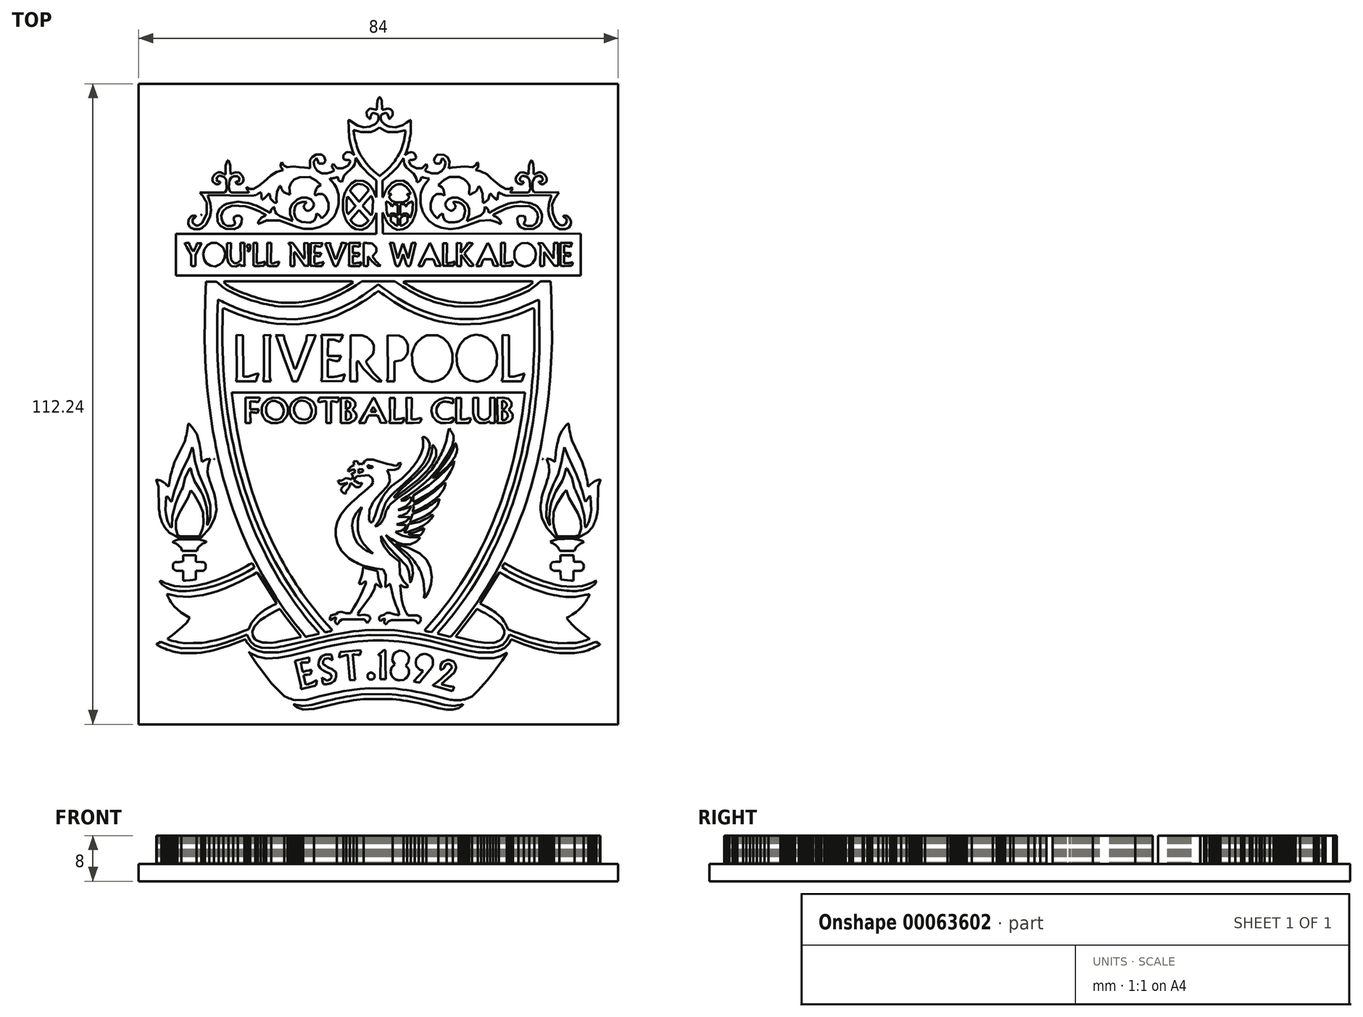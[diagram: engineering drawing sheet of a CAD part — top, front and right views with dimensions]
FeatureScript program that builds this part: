
annotation { "Feature Type Name" : "Feature", "Feature Type Description" : "" }
export const myFeature = defineFeature(function(context is Context, id is Id, definition is map)
    precondition{}
    {
        {
            var Q0;
            Q0=qCreatedBy(makeId("Top.planeOp"),FACE);
            var sketch = newSketch(context, id + "F0", { "sketchPlane" : qUnion([Q0])});
            skLineSegment(sketch, "E0", {"start": v(-12.21, -53.6) * mm, "end": v(-11.26, -53.57) * mm});
            skLineSegment(sketch, "E1", {"start": v(-11.26, -53.57) * mm, "end": v(-7.27, -52.58) * mm});
            skLineSegment(sketch, "E2", {"start": v(-7.27, -52.58) * mm, "end": v(-6.14, -52.35) * mm});
            skLineSegment(sketch, "E3", {"start": v(-6.14, -52.35) * mm, "end": v(-5.6, -52.25) * mm});
            skLineSegment(sketch, "E4", {"start": v(-5.6, -52.25) * mm, "end": v(-4.98, -52.14) * mm});
            skLineSegment(sketch, "E5", {"start": v(-4.98, -52.14) * mm, "end": v(-4.35, -52.04) * mm});
            skLineSegment(sketch, "E6", {"start": v(-4.35, -52.04) * mm, "end": v(-3.78, -51.96) * mm});
            skLineSegment(sketch, "E7", {"start": v(-3.78, -51.96) * mm, "end": v(-2.56, -51.8) * mm});
            skLineSegment(sketch, "E8", {"start": v(-2.56, -51.8) * mm, "end": v(2.51, -51.8) * mm});
            skLineSegment(sketch, "E9", {"start": v(2.51, -51.8) * mm, "end": v(3.74, -51.96) * mm});
            skLineSegment(sketch, "E10", {"start": v(3.74, -51.96) * mm, "end": v(4.37, -52.05) * mm});
            skLineSegment(sketch, "E11", {"start": v(4.37, -52.05) * mm, "end": v(5.03, -52.16) * mm});
            skLineSegment(sketch, "E12", {"start": v(5.03, -52.16) * mm, "end": v(5.7, -52.28) * mm});
            skLineSegment(sketch, "E13", {"start": v(5.7, -52.28) * mm, "end": v(6.39, -52.4) * mm});
            skLineSegment(sketch, "E14", {"start": v(6.39, -52.4) * mm, "end": v(7.08, -52.55) * mm});
            skLineSegment(sketch, "E15", {"start": v(7.08, -52.55) * mm, "end": v(7.76, -52.7) * mm});
            skLineSegment(sketch, "E16", {"start": v(7.76, -52.7) * mm, "end": v(8.43, -52.86) * mm});
            skLineSegment(sketch, "E17", {"start": v(8.43, -52.86) * mm, "end": v(9.08, -53.03) * mm});
            skLineSegment(sketch, "E18", {"start": v(9.08, -53.03) * mm, "end": v(10.49, -53.4) * mm});
            skLineSegment(sketch, "E19", {"start": v(10.49, -53.4) * mm, "end": v(11.94, -53.65) * mm});
            skLineSegment(sketch, "E20", {"start": v(11.94, -53.65) * mm, "end": v(13.03, -53.65) * mm});
            skLineSegment(sketch, "E21", {"start": v(13.03, -53.65) * mm, "end": v(14.07, -53.38) * mm});
            skLineSegment(sketch, "E22", {"start": v(14.07, -53.38) * mm, "end": v(14.43, -53.14) * mm});
            skLineSegment(sketch, "E23", {"start": v(14.43, -53.14) * mm, "end": v(14.57, -53.04) * mm});
            skLineSegment(sketch, "E24", {"start": v(14.57, -53.04) * mm, "end": v(14.69, -52.95) * mm});
            skLineSegment(sketch, "E25", {"start": v(14.69, -52.95) * mm, "end": v(14.77, -52.87) * mm});
            skLineSegment(sketch, "E26", {"start": v(14.77, -52.87) * mm, "end": v(14.79, -52.84) * mm});
            skLineSegment(sketch, "E27", {"start": v(14.79, -52.84) * mm, "end": v(14.8, -52.81) * mm});
            skLineSegment(sketch, "E28", {"start": v(14.8, -52.81) * mm, "end": v(14.8, -52.72) * mm});
            skLineSegment(sketch, "E29", {"start": v(14.8, -52.72) * mm, "end": v(14.65, -52.78) * mm});
            skLineSegment(sketch, "E30", {"start": v(14.65, -52.78) * mm, "end": v(14.54, -52.8) * mm});
            skLineSegment(sketch, "E31", {"start": v(14.54, -52.8) * mm, "end": v(14.37, -52.85) * mm});
            skLineSegment(sketch, "E32", {"start": v(14.37, -52.85) * mm, "end": v(13.89, -52.93) * mm});
            skLineSegment(sketch, "E33", {"start": v(13.89, -52.93) * mm, "end": v(13.27, -53.03) * mm});
            skLineSegment(sketch, "E34", {"start": v(13.27, -53.03) * mm, "end": v(11.56, -52.84) * mm});
            skLineSegment(sketch, "E35", {"start": v(11.56, -52.84) * mm, "end": v(10.35, -52.52) * mm});
            skLineSegment(sketch, "E36", {"start": v(10.35, -52.52) * mm, "end": v(9.17, -52.21) * mm});
            skLineSegment(sketch, "E37", {"start": v(9.17, -52.21) * mm, "end": v(8.12, -51.95) * mm});
            skLineSegment(sketch, "E38", {"start": v(8.12, -51.95) * mm, "end": v(7.18, -51.73) * mm});
            skLineSegment(sketch, "E39", {"start": v(7.18, -51.73) * mm, "end": v(6.32, -51.55) * mm});
            skLineSegment(sketch, "E40", {"start": v(6.32, -51.55) * mm, "end": v(5.5, -51.4) * mm});
            skLineSegment(sketch, "E41", {"start": v(5.5, -51.4) * mm, "end": v(4.71, -51.27) * mm});
            skLineSegment(sketch, "E42", {"start": v(4.71, -51.27) * mm, "end": v(3.92, -51.16) * mm});
            skLineSegment(sketch, "E43", {"start": v(3.92, -51.16) * mm, "end": v(3.1, -51.06) * mm});
            skLineSegment(sketch, "E44", {"start": v(3.1, -51.06) * mm, "end": v(1.7, -50.9) * mm});
            skLineSegment(sketch, "E45", {"start": v(1.7, -50.9) * mm, "end": v(-3.01, -51) * mm});
            skLineSegment(sketch, "E46", {"start": v(-3.01, -51) * mm, "end": v(-4.26, -51.2) * mm});
            skLineSegment(sketch, "E47", {"start": v(-4.26, -51.2) * mm, "end": v(-4.9, -51.3) * mm});
            skLineSegment(sketch, "E48", {"start": v(-4.9, -51.3) * mm, "end": v(-5.54, -51.4) * mm});
            skLineSegment(sketch, "E49", {"start": v(-5.54, -51.4) * mm, "end": v(-6.17, -51.52) * mm});
            skLineSegment(sketch, "E50", {"start": v(-6.17, -51.52) * mm, "end": v(-6.8, -51.65) * mm});
            skLineSegment(sketch, "E51", {"start": v(-6.8, -51.65) * mm, "end": v(-7.45, -51.79) * mm});
            skLineSegment(sketch, "E52", {"start": v(-7.45, -51.79) * mm, "end": v(-8.1, -51.94) * mm});
            skLineSegment(sketch, "E53", {"start": v(-8.1, -51.94) * mm, "end": v(-8.78, -52.1) * mm});
            skLineSegment(sketch, "E54", {"start": v(-8.78, -52.1) * mm, "end": v(-9.5, -52.29) * mm});
            skLineSegment(sketch, "E55", {"start": v(-9.5, -52.29) * mm, "end": v(-11.67, -52.82) * mm});
            skLineSegment(sketch, "E56", {"start": v(-11.67, -52.82) * mm, "end": v(-12.2, -52.9) * mm});
            skLineSegment(sketch, "E57", {"start": v(-12.2, -52.9) * mm, "end": v(-12.76, -52.97) * mm});
            skLineSegment(sketch, "E58", {"start": v(-12.76, -52.97) * mm, "end": v(-13.34, -53.03) * mm});
            skLineSegment(sketch, "E59", {"start": v(-13.34, -53.03) * mm, "end": v(-13.95, -52.93) * mm});
            skLineSegment(sketch, "E60", {"start": v(-13.95, -52.93) * mm, "end": v(-14.43, -52.84) * mm});
            skLineSegment(sketch, "E61", {"start": v(-14.43, -52.84) * mm, "end": v(-14.61, -52.8) * mm});
            skLineSegment(sketch, "E62", {"start": v(-14.61, -52.8) * mm, "end": v(-14.72, -52.77) * mm});
            skLineSegment(sketch, "E63", {"start": v(-14.72, -52.77) * mm, "end": v(-14.89, -52.71) * mm});
            skLineSegment(sketch, "E64", {"start": v(-14.89, -52.71) * mm, "end": v(-14.7, -52.92) * mm});
            skLineSegment(sketch, "E65", {"start": v(-14.7, -52.92) * mm, "end": v(-14.6, -53.01) * mm});
            skLineSegment(sketch, "E66", {"start": v(-14.6, -53.01) * mm, "end": v(-14.5, -53.1) * mm});
            skLineSegment(sketch, "E67", {"start": v(-14.5, -53.1) * mm, "end": v(-14.35, -53.2) * mm});
            skLineSegment(sketch, "E68", {"start": v(-14.35, -53.2) * mm, "end": v(-14.2, -53.29) * mm});
            skLineSegment(sketch, "E69", {"start": v(-14.2, -53.29) * mm, "end": v(-14.03, -53.37) * mm});
            skLineSegment(sketch, "E70", {"start": v(-14.03, -53.37) * mm, "end": v(-13.86, -53.44) * mm});
            skLineSegment(sketch, "E71", {"start": v(-13.86, -53.44) * mm, "end": v(-13.68, -53.5) * mm});
            skLineSegment(sketch, "E72", {"start": v(-13.68, -53.5) * mm, "end": v(-13.5, -53.56) * mm});
            skLineSegment(sketch, "E73", {"start": v(-13.5, -53.56) * mm, "end": v(-13.16, -53.64) * mm});
            skLineSegment(sketch, "E74", {"start": v(-13.16, -53.64) * mm, "end": v(-12.21, -53.6) * mm});
            skLineSegment(sketch, "E75", {"start": v(-13.53, -51.98) * mm, "end": v(-12.53, -51.94) * mm});
            skLineSegment(sketch, "E76", {"start": v(-12.53, -51.94) * mm, "end": v(-11.62, -51.7) * mm});
            skLineSegment(sketch, "E77", {"start": v(-11.62, -51.7) * mm, "end": v(-10.25, -51.34) * mm});
            skLineSegment(sketch, "E78", {"start": v(-10.25, -51.34) * mm, "end": v(-9.04, -51.04) * mm});
            skLineSegment(sketch, "E79", {"start": v(-9.04, -51.04) * mm, "end": v(-7.96, -50.8) * mm});
            skLineSegment(sketch, "E80", {"start": v(-7.96, -50.8) * mm, "end": v(-6.98, -50.6) * mm});
            skLineSegment(sketch, "E81", {"start": v(-6.98, -50.6) * mm, "end": v(-6.05, -50.42) * mm});
            skLineSegment(sketch, "E82", {"start": v(-6.05, -50.42) * mm, "end": v(-5.15, -50.29) * mm});
            skLineSegment(sketch, "E83", {"start": v(-5.15, -50.29) * mm, "end": v(-4.22, -50.17) * mm});
            skLineSegment(sketch, "E84", {"start": v(-4.22, -50.17) * mm, "end": v(-3.23, -50.07) * mm});
            skLineSegment(sketch, "E85", {"start": v(-3.23, -50.07) * mm, "end": v(-1.65, -49.92) * mm});
            skLineSegment(sketch, "E86", {"start": v(-1.65, -49.92) * mm, "end": v(3.06, -50) * mm});
            skLineSegment(sketch, "E87", {"start": v(3.06, -50) * mm, "end": v(4.2, -50.15) * mm});
            skLineSegment(sketch, "E88", {"start": v(4.2, -50.15) * mm, "end": v(5, -50.27) * mm});
            skLineSegment(sketch, "E89", {"start": v(5, -50.27) * mm, "end": v(5.8, -50.4) * mm});
            skLineSegment(sketch, "E90", {"start": v(5.8, -50.4) * mm, "end": v(6.62, -50.54) * mm});
            skLineSegment(sketch, "E91", {"start": v(6.62, -50.54) * mm, "end": v(7.45, -50.7) * mm});
            skLineSegment(sketch, "E92", {"start": v(7.45, -50.7) * mm, "end": v(8.28, -50.87) * mm});
            skLineSegment(sketch, "E93", {"start": v(8.28, -50.87) * mm, "end": v(9.13, -51.07) * mm});
            skLineSegment(sketch, "E94", {"start": v(9.13, -51.07) * mm, "end": v(10, -51.28) * mm});
            skLineSegment(sketch, "E95", {"start": v(10, -51.28) * mm, "end": v(10.87, -51.5) * mm});
            skLineSegment(sketch, "E96", {"start": v(10.87, -51.5) * mm, "end": v(12.07, -51.83) * mm});
            skLineSegment(sketch, "E97", {"start": v(12.07, -51.83) * mm, "end": v(12.64, -51.93) * mm});
            skLineSegment(sketch, "E98", {"start": v(12.64, -51.93) * mm, "end": v(12.9, -51.96) * mm});
            skLineSegment(sketch, "E99", {"start": v(12.9, -51.96) * mm, "end": v(13.22, -52) * mm});
            skLineSegment(sketch, "E100", {"start": v(13.22, -52) * mm, "end": v(13.53, -52.01) * mm});
            skLineSegment(sketch, "E101", {"start": v(13.53, -52.01) * mm, "end": v(13.82, -52.02) * mm});
            skLineSegment(sketch, "E102", {"start": v(13.82, -52.02) * mm, "end": v(14.42, -52.02) * mm});
            skLineSegment(sketch, "E103", {"start": v(14.42, -52.02) * mm, "end": v(14.9, -51.92) * mm});
            skLineSegment(sketch, "E104", {"start": v(14.9, -51.92) * mm, "end": v(15.13, -51.86) * mm});
            skLineSegment(sketch, "E105", {"start": v(15.13, -51.86) * mm, "end": v(15.39, -51.78) * mm});
            skLineSegment(sketch, "E106", {"start": v(15.39, -51.78) * mm, "end": v(15.65, -51.68) * mm});
            skLineSegment(sketch, "E107", {"start": v(15.65, -51.68) * mm, "end": v(15.88, -51.59) * mm});
            skLineSegment(sketch, "E108", {"start": v(15.88, -51.59) * mm, "end": v(16.38, -51.35) * mm});
            skLineSegment(sketch, "E109", {"start": v(16.38, -51.35) * mm, "end": v(17.39, -50.35) * mm});
            skLineSegment(sketch, "E110", {"start": v(17.39, -50.35) * mm, "end": v(17.97, -49.76) * mm});
            skLineSegment(sketch, "E111", {"start": v(17.97, -49.76) * mm, "end": v(18.52, -49.16) * mm});
            skLineSegment(sketch, "E112", {"start": v(18.52, -49.16) * mm, "end": v(19.06, -48.55) * mm});
            skLineSegment(sketch, "E113", {"start": v(19.06, -48.55) * mm, "end": v(19.59, -47.92) * mm});
            skLineSegment(sketch, "E114", {"start": v(19.59, -47.92) * mm, "end": v(20.1, -47.26) * mm});
            skLineSegment(sketch, "E115", {"start": v(20.1, -47.26) * mm, "end": v(20.61, -46.58) * mm});
            skLineSegment(sketch, "E116", {"start": v(20.61, -46.58) * mm, "end": v(21.13, -45.86) * mm});
            skLineSegment(sketch, "E117", {"start": v(21.13, -45.86) * mm, "end": v(21.64, -45.1) * mm});
            skLineSegment(sketch, "E118", {"start": v(21.64, -45.1) * mm, "end": v(22.5, -43.83) * mm});
            skLineSegment(sketch, "E119", {"start": v(22.5, -43.83) * mm, "end": v(22.5, -43.68) * mm});
            skLineSegment(sketch, "E120", {"start": v(22.5, -43.68) * mm, "end": v(21.36, -44.3) * mm});
            skLineSegment(sketch, "E121", {"start": v(21.36, -44.3) * mm, "end": v(20.19, -44.62) * mm});
            skLineSegment(sketch, "E122", {"start": v(20.19, -44.62) * mm, "end": v(17.65, -44.63) * mm});
            skLineSegment(sketch, "E123", {"start": v(17.65, -44.63) * mm, "end": v(15.66, -44.3) * mm});
            skLineSegment(sketch, "E124", {"start": v(15.66, -44.3) * mm, "end": v(9.13, -42.68) * mm});
            skLineSegment(sketch, "E125", {"start": v(9.13, -42.68) * mm, "end": v(7.59, -42.37) * mm});
            skLineSegment(sketch, "E126", {"start": v(7.59, -42.37) * mm, "end": v(6.56, -42.17) * mm});
            skLineSegment(sketch, "E127", {"start": v(6.56, -42.17) * mm, "end": v(5.56, -42) * mm});
            skLineSegment(sketch, "E128", {"start": v(5.56, -42) * mm, "end": v(4.6, -41.85) * mm});
            skLineSegment(sketch, "E129", {"start": v(4.6, -41.85) * mm, "end": v(3.64, -41.73) * mm});
            skLineSegment(sketch, "E130", {"start": v(3.64, -41.73) * mm, "end": v(2.71, -41.64) * mm});
            skLineSegment(sketch, "E131", {"start": v(2.71, -41.64) * mm, "end": v(1.8, -41.57) * mm});
            skLineSegment(sketch, "E132", {"start": v(1.8, -41.57) * mm, "end": v(0.9, -41.53) * mm});
            skLineSegment(sketch, "E133", {"start": v(0.9, -41.53) * mm, "end": v(-0.01, -41.52) * mm});
            skLineSegment(sketch, "E134", {"start": v(-0.01, -41.52) * mm, "end": v(-0.91, -41.53) * mm});
            skLineSegment(sketch, "E135", {"start": v(-0.91, -41.53) * mm, "end": v(-1.82, -41.57) * mm});
            skLineSegment(sketch, "E136", {"start": v(-1.82, -41.57) * mm, "end": v(-2.74, -41.64) * mm});
            skLineSegment(sketch, "E137", {"start": v(-2.74, -41.64) * mm, "end": v(-3.67, -41.73) * mm});
            skLineSegment(sketch, "E138", {"start": v(-3.67, -41.73) * mm, "end": v(-4.62, -41.85) * mm});
            skLineSegment(sketch, "E139", {"start": v(-4.62, -41.85) * mm, "end": v(-5.6, -42) * mm});
            skLineSegment(sketch, "E140", {"start": v(-5.6, -42) * mm, "end": v(-6.6, -42.17) * mm});
            skLineSegment(sketch, "E141", {"start": v(-6.6, -42.17) * mm, "end": v(-7.64, -42.37) * mm});
            skLineSegment(sketch, "E142", {"start": v(-7.64, -42.37) * mm, "end": v(-9.18, -42.68) * mm});
            skLineSegment(sketch, "E143", {"start": v(-9.18, -42.68) * mm, "end": v(-15.43, -44.24) * mm});
            skLineSegment(sketch, "E144", {"start": v(-15.43, -44.24) * mm, "end": v(-17.5, -44.6) * mm});
            skLineSegment(sketch, "E145", {"start": v(-17.5, -44.6) * mm, "end": v(-19.6, -44.7) * mm});
            skLineSegment(sketch, "E146", {"start": v(-19.6, -44.7) * mm, "end": v(-21.14, -44.42) * mm});
            skLineSegment(sketch, "E147", {"start": v(-21.14, -44.42) * mm, "end": v(-22.56, -43.7) * mm});
            skLineSegment(sketch, "E148", {"start": v(-22.56, -43.7) * mm, "end": v(-22.46, -43.96) * mm});
            skLineSegment(sketch, "E149", {"start": v(-22.46, -43.96) * mm, "end": v(-21.55, -45.3) * mm});
            skLineSegment(sketch, "E150", {"start": v(-21.55, -45.3) * mm, "end": v(-21.13, -45.9) * mm});
            skLineSegment(sketch, "E151", {"start": v(-21.13, -45.9) * mm, "end": v(-20.63, -46.58) * mm});
            skLineSegment(sketch, "E152", {"start": v(-20.63, -46.58) * mm, "end": v(-20.14, -47.25) * mm});
            skLineSegment(sketch, "E153", {"start": v(-20.14, -47.25) * mm, "end": v(-19.7, -47.82) * mm});
            skLineSegment(sketch, "E154", {"start": v(-19.7, -47.82) * mm, "end": v(-18.75, -49) * mm});
            skLineSegment(sketch, "E155", {"start": v(-18.75, -49) * mm, "end": v(-16.52, -51.29) * mm});
            skLineSegment(sketch, "E156", {"start": v(-16.52, -51.29) * mm, "end": v(-15.92, -51.56) * mm});
            skLineSegment(sketch, "E157", {"start": v(-15.92, -51.56) * mm, "end": v(-15.65, -51.68) * mm});
            skLineSegment(sketch, "E158", {"start": v(-15.65, -51.68) * mm, "end": v(-15.38, -51.79) * mm});
            skLineSegment(sketch, "E159", {"start": v(-15.38, -51.79) * mm, "end": v(-15.12, -51.87) * mm});
            skLineSegment(sketch, "E160", {"start": v(-15.12, -51.87) * mm, "end": v(-14.92, -51.93) * mm});
            skLineSegment(sketch, "E161", {"start": v(-14.92, -51.93) * mm, "end": v(-14.52, -52.01) * mm});
            skLineSegment(sketch, "E162", {"start": v(-14.52, -52.01) * mm, "end": v(-13.53, -51.98) * mm});
            skLineSegment(sketch, "E163", {"start": v(13.22, -49.7) * mm, "end": v(13.17, -49.68) * mm});
            skLineSegment(sketch, "E164", {"start": v(13.17, -49.68) * mm, "end": v(13.06, -49.65) * mm});
            skLineSegment(sketch, "E165", {"start": v(13.06, -49.65) * mm, "end": v(12.7, -49.6) * mm});
            skLineSegment(sketch, "E166", {"start": v(12.7, -49.6) * mm, "end": v(12.51, -49.58) * mm});
            skLineSegment(sketch, "E167", {"start": v(12.51, -49.58) * mm, "end": v(12.27, -49.53) * mm});
            skLineSegment(sketch, "E168", {"start": v(12.27, -49.53) * mm, "end": v(11.73, -49.4) * mm});
            skLineSegment(sketch, "E169", {"start": v(11.73, -49.4) * mm, "end": v(11.48, -49.33) * mm});
            skLineSegment(sketch, "E170", {"start": v(11.48, -49.33) * mm, "end": v(11.27, -49.26) * mm});
            skLineSegment(sketch, "E171", {"start": v(11.27, -49.26) * mm, "end": v(11.13, -49.2) * mm});
            skLineSegment(sketch, "E172", {"start": v(11.13, -49.2) * mm, "end": v(11.1, -49.19) * mm});
            skLineSegment(sketch, "E173", {"start": v(11.1, -49.19) * mm, "end": v(11.08, -49.17) * mm});
            skLineSegment(sketch, "E174", {"start": v(11.08, -49.17) * mm, "end": v(11.08, -49.15) * mm});
            skLineSegment(sketch, "E175", {"start": v(11.08, -49.15) * mm, "end": v(13.28, -47.19) * mm});
            skLineSegment(sketch, "E176", {"start": v(13.28, -47.19) * mm, "end": v(13.64, -46.37) * mm});
            skLineSegment(sketch, "E177", {"start": v(13.64, -46.37) * mm, "end": v(13.54, -45.76) * mm});
            skLineSegment(sketch, "E178", {"start": v(13.54, -45.76) * mm, "end": v(13.17, -45.24) * mm});
            skLineSegment(sketch, "E179", {"start": v(13.17, -45.24) * mm, "end": v(12.8, -45.1) * mm});
            skLineSegment(sketch, "E180", {"start": v(12.8, -45.1) * mm, "end": v(12.63, -45.03) * mm});
            skLineSegment(sketch, "E181", {"start": v(12.63, -45.03) * mm, "end": v(12.49, -45) * mm});
            skLineSegment(sketch, "E182", {"start": v(12.49, -45) * mm, "end": v(12.35, -44.97) * mm});
            skLineSegment(sketch, "E183", {"start": v(12.35, -44.97) * mm, "end": v(12.22, -44.96) * mm});
            skLineSegment(sketch, "E184", {"start": v(12.22, -44.96) * mm, "end": v(12.1, -44.97) * mm});
            skLineSegment(sketch, "E185", {"start": v(12.1, -44.97) * mm, "end": v(11.96, -45) * mm});
            skLineSegment(sketch, "E186", {"start": v(11.96, -45) * mm, "end": v(11.81, -45.06) * mm});
            skLineSegment(sketch, "E187", {"start": v(11.81, -45.06) * mm, "end": v(11.65, -45.13) * mm});
            skLineSegment(sketch, "E188", {"start": v(11.65, -45.13) * mm, "end": v(11.26, -45.3) * mm});
            skLineSegment(sketch, "E189", {"start": v(11.26, -45.3) * mm, "end": v(10.9, -45.9) * mm});
            skLineSegment(sketch, "E190", {"start": v(10.9, -45.9) * mm, "end": v(10.9, -46.67) * mm});
            skLineSegment(sketch, "E191", {"start": v(10.9, -46.67) * mm, "end": v(11, -46.67) * mm});
            skLineSegment(sketch, "E192", {"start": v(11, -46.67) * mm, "end": v(11.05, -46.66) * mm});
            skLineSegment(sketch, "E193", {"start": v(11.05, -46.66) * mm, "end": v(11.12, -46.63) * mm});
            skLineSegment(sketch, "E194", {"start": v(11.12, -46.63) * mm, "end": v(11.22, -46.58) * mm});
            skLineSegment(sketch, "E195", {"start": v(11.22, -46.58) * mm, "end": v(11.31, -46.52) * mm});
            skLineSegment(sketch, "E196", {"start": v(11.31, -46.52) * mm, "end": v(11.54, -46.37) * mm});
            skLineSegment(sketch, "E197", {"start": v(11.54, -46.37) * mm, "end": v(11.8, -45.76) * mm});
            skLineSegment(sketch, "E198", {"start": v(11.8, -45.76) * mm, "end": v(12.21, -45.6) * mm});
            skLineSegment(sketch, "E199", {"start": v(12.21, -45.6) * mm, "end": v(12.39, -45.67) * mm});
            skLineSegment(sketch, "E200", {"start": v(12.39, -45.67) * mm, "end": v(12.47, -45.72) * mm});
            skLineSegment(sketch, "E201", {"start": v(12.47, -45.72) * mm, "end": v(12.56, -45.78) * mm});
            skLineSegment(sketch, "E202", {"start": v(12.56, -45.78) * mm, "end": v(12.66, -45.87) * mm});
            skLineSegment(sketch, "E203", {"start": v(12.66, -45.87) * mm, "end": v(12.73, -45.96) * mm});
            skLineSegment(sketch, "E204", {"start": v(12.73, -45.96) * mm, "end": v(12.9, -46.18) * mm});
            skLineSegment(sketch, "E205", {"start": v(12.9, -46.18) * mm, "end": v(12.75, -46.58) * mm});
            skLineSegment(sketch, "E206", {"start": v(12.75, -46.58) * mm, "end": v(12.07, -47.27) * mm});
            skLineSegment(sketch, "E207", {"start": v(12.07, -47.27) * mm, "end": v(11.82, -47.53) * mm});
            skLineSegment(sketch, "E208", {"start": v(11.82, -47.53) * mm, "end": v(11.54, -47.79) * mm});
            skLineSegment(sketch, "E209", {"start": v(11.54, -47.79) * mm, "end": v(10.95, -48.32) * mm});
            skLineSegment(sketch, "E210", {"start": v(10.95, -48.32) * mm, "end": v(10.65, -48.57) * mm});
            skLineSegment(sketch, "E211", {"start": v(10.65, -48.57) * mm, "end": v(10.36, -48.8) * mm});
            skLineSegment(sketch, "E212", {"start": v(10.36, -48.8) * mm, "end": v(10.08, -49.02) * mm});
            skLineSegment(sketch, "E213", {"start": v(10.08, -49.02) * mm, "end": v(9.83, -49.2) * mm});
            skLineSegment(sketch, "E214", {"start": v(9.83, -49.2) * mm, "end": v(9.71, -49.29) * mm});
            skLineSegment(sketch, "E215", {"start": v(9.71, -49.29) * mm, "end": v(9.63, -49.36) * mm});
            skLineSegment(sketch, "E216", {"start": v(9.63, -49.36) * mm, "end": v(9.57, -49.42) * mm});
            skLineSegment(sketch, "E217", {"start": v(9.57, -49.42) * mm, "end": v(9.56, -49.44) * mm});
            skLineSegment(sketch, "E218", {"start": v(9.56, -49.44) * mm, "end": v(9.57, -49.45) * mm});
            skLineSegment(sketch, "E219", {"start": v(9.57, -49.45) * mm, "end": v(9.6, -49.49) * mm});
            skLineSegment(sketch, "E220", {"start": v(9.6, -49.49) * mm, "end": v(12.97, -50.45) * mm});
            skLineSegment(sketch, "E221", {"start": v(12.97, -50.45) * mm, "end": v(13.12, -50.1) * mm});
            skLineSegment(sketch, "E222", {"start": v(13.12, -50.1) * mm, "end": v(13.2, -49.83) * mm});
            skLineSegment(sketch, "E223", {"start": v(13.2, -49.83) * mm, "end": v(13.23, -49.74) * mm});
            skLineSegment(sketch, "E224", {"start": v(13.23, -49.74) * mm, "end": v(13.22, -49.7) * mm});
            skLineSegment(sketch, "E225", {"start": v(-10.99, -49.46) * mm, "end": v(-10.96, -49.41) * mm});
            skLineSegment(sketch, "E226", {"start": v(-10.96, -49.41) * mm, "end": v(-10.93, -49.3) * mm});
            skLineSegment(sketch, "E227", {"start": v(-10.93, -49.3) * mm, "end": v(-10.86, -49) * mm});
            skLineSegment(sketch, "E228", {"start": v(-10.86, -49) * mm, "end": v(-10.79, -48.58) * mm});
            skLineSegment(sketch, "E229", {"start": v(-10.79, -48.58) * mm, "end": v(-10.86, -48.58) * mm});
            skLineSegment(sketch, "E230", {"start": v(-10.86, -48.58) * mm, "end": v(-10.94, -48.6) * mm});
            skLineSegment(sketch, "E231", {"start": v(-10.94, -48.6) * mm, "end": v(-11.1, -48.67) * mm});
            skLineSegment(sketch, "E232", {"start": v(-11.1, -48.67) * mm, "end": v(-11.55, -48.88) * mm});
            skLineSegment(sketch, "E233", {"start": v(-11.55, -48.88) * mm, "end": v(-11.81, -49) * mm});
            skLineSegment(sketch, "E234", {"start": v(-11.81, -49) * mm, "end": v(-12.07, -49.12) * mm});
            skLineSegment(sketch, "E235", {"start": v(-12.07, -49.12) * mm, "end": v(-12.3, -49.2) * mm});
            skLineSegment(sketch, "E236", {"start": v(-12.3, -49.2) * mm, "end": v(-12.45, -49.25) * mm});
            skLineSegment(sketch, "E237", {"start": v(-12.45, -49.25) * mm, "end": v(-12.74, -49.31) * mm});
            skLineSegment(sketch, "E238", {"start": v(-12.74, -49.31) * mm, "end": v(-13.12, -47.66) * mm});
            skLineSegment(sketch, "E239", {"start": v(-13.12, -47.66) * mm, "end": v(-13.12, -47.62) * mm});
            skLineSegment(sketch, "E240", {"start": v(-13.12, -47.62) * mm, "end": v(-13.07, -47.6) * mm});
            skLineSegment(sketch, "E241", {"start": v(-13.07, -47.6) * mm, "end": v(-12.94, -47.59) * mm});
            skLineSegment(sketch, "E242", {"start": v(-12.94, -47.59) * mm, "end": v(-12.52, -47.56) * mm});
            skLineSegment(sketch, "E243", {"start": v(-12.52, -47.56) * mm, "end": v(-11.91, -47.53) * mm});
            skLineSegment(sketch, "E244", {"start": v(-11.91, -47.53) * mm, "end": v(-11.69, -46.76) * mm});
            skLineSegment(sketch, "E245", {"start": v(-11.69, -46.76) * mm, "end": v(-11.89, -46.76) * mm});
            skLineSegment(sketch, "E246", {"start": v(-11.89, -46.76) * mm, "end": v(-12, -46.77) * mm});
            skLineSegment(sketch, "E247", {"start": v(-12, -46.77) * mm, "end": v(-12.18, -46.8) * mm});
            skLineSegment(sketch, "E248", {"start": v(-12.18, -46.8) * mm, "end": v(-12.6, -46.9) * mm});
            skLineSegment(sketch, "E249", {"start": v(-12.6, -46.9) * mm, "end": v(-13, -47) * mm});
            skLineSegment(sketch, "E250", {"start": v(-13, -47) * mm, "end": v(-13.2, -47.03) * mm});
            skLineSegment(sketch, "E251", {"start": v(-13.2, -47.03) * mm, "end": v(-13.27, -47.03) * mm});
            skLineSegment(sketch, "E252", {"start": v(-13.27, -47.03) * mm, "end": v(-13.42, -46.33) * mm});
            skLineSegment(sketch, "E253", {"start": v(-13.42, -46.33) * mm, "end": v(-13.53, -45.8) * mm});
            skLineSegment(sketch, "E254", {"start": v(-13.53, -45.8) * mm, "end": v(-13.57, -45.51) * mm});
            skLineSegment(sketch, "E255", {"start": v(-13.57, -45.51) * mm, "end": v(-13.57, -45.4) * mm});
            skLineSegment(sketch, "E256", {"start": v(-13.57, -45.4) * mm, "end": v(-12.2, -45.4) * mm});
            skLineSegment(sketch, "E257", {"start": v(-12.2, -45.4) * mm, "end": v(-12.15, -45.26) * mm});
            skLineSegment(sketch, "E258", {"start": v(-12.15, -45.26) * mm, "end": v(-12.13, -45.18) * mm});
            skLineSegment(sketch, "E259", {"start": v(-12.13, -45.18) * mm, "end": v(-12.1, -45.07) * mm});
            skLineSegment(sketch, "E260", {"start": v(-12.1, -45.07) * mm, "end": v(-12.09, -44.82) * mm});
            skLineSegment(sketch, "E261", {"start": v(-12.09, -44.82) * mm, "end": v(-12.08, -44.53) * mm});
            skLineSegment(sketch, "E262", {"start": v(-12.08, -44.53) * mm, "end": v(-14.25, -45.03) * mm});
            skLineSegment(sketch, "E263", {"start": v(-14.25, -45.03) * mm, "end": v(-14.66, -45.14) * mm});
            skLineSegment(sketch, "E264", {"start": v(-14.66, -45.14) * mm, "end": v(-14.5, -45.45) * mm});
            skLineSegment(sketch, "E265", {"start": v(-14.5, -45.45) * mm, "end": v(-13.57, -49.44) * mm});
            skLineSegment(sketch, "E266", {"start": v(-13.57, -49.44) * mm, "end": v(-13.57, -50.02) * mm});
            skLineSegment(sketch, "E267", {"start": v(-13.57, -50.02) * mm, "end": v(-13.37, -50.02) * mm});
            skLineSegment(sketch, "E268", {"start": v(-13.37, -50.02) * mm, "end": v(-13.2, -50) * mm});
            skLineSegment(sketch, "E269", {"start": v(-13.2, -50) * mm, "end": v(-12.9, -49.94) * mm});
            skLineSegment(sketch, "E270", {"start": v(-12.9, -49.94) * mm, "end": v(-12.1, -49.76) * mm});
            skLineSegment(sketch, "E271", {"start": v(-12.1, -49.76) * mm, "end": v(-11.03, -49.5) * mm});
            skLineSegment(sketch, "E272", {"start": v(-11.03, -49.5) * mm, "end": v(-10.99, -49.46) * mm});
            skLineSegment(sketch, "E273", {"start": v(-8.01, -48.86) * mm, "end": v(-7.7, -48.67) * mm});
            skLineSegment(sketch, "E274", {"start": v(-7.7, -48.67) * mm, "end": v(-7.56, -48.33) * mm});
            skLineSegment(sketch, "E275", {"start": v(-7.56, -48.33) * mm, "end": v(-7.45, -48.05) * mm});
            skLineSegment(sketch, "E276", {"start": v(-7.45, -48.05) * mm, "end": v(-7.42, -47.94) * mm});
            skLineSegment(sketch, "E277", {"start": v(-7.42, -47.94) * mm, "end": v(-7.4, -47.84) * mm});
            skLineSegment(sketch, "E278", {"start": v(-7.4, -47.84) * mm, "end": v(-7.4, -47.74) * mm});
            skLineSegment(sketch, "E279", {"start": v(-7.4, -47.74) * mm, "end": v(-7.4, -47.64) * mm});
            skLineSegment(sketch, "E280", {"start": v(-7.4, -47.64) * mm, "end": v(-7.44, -47.39) * mm});
            skLineSegment(sketch, "E281", {"start": v(-7.44, -47.39) * mm, "end": v(-7.5, -47.06) * mm});
            skLineSegment(sketch, "E282", {"start": v(-7.5, -47.06) * mm, "end": v(-7.7, -46.88) * mm});
            skLineSegment(sketch, "E283", {"start": v(-7.7, -46.88) * mm, "end": v(-7.84, -46.78) * mm});
            skLineSegment(sketch, "E284", {"start": v(-7.84, -46.78) * mm, "end": v(-8.05, -46.65) * mm});
            skLineSegment(sketch, "E285", {"start": v(-8.05, -46.65) * mm, "end": v(-8.3, -46.5) * mm});
            skLineSegment(sketch, "E286", {"start": v(-8.3, -46.5) * mm, "end": v(-8.59, -46.35) * mm});
            skLineSegment(sketch, "E287", {"start": v(-8.59, -46.35) * mm, "end": v(-8.87, -46.2) * mm});
            skLineSegment(sketch, "E288", {"start": v(-8.87, -46.2) * mm, "end": v(-9.13, -46.06) * mm});
            skLineSegment(sketch, "E289", {"start": v(-9.13, -46.06) * mm, "end": v(-9.34, -45.93) * mm});
            skLineSegment(sketch, "E290", {"start": v(-9.34, -45.93) * mm, "end": v(-9.47, -45.83) * mm});
            skLineSegment(sketch, "E291", {"start": v(-9.47, -45.83) * mm, "end": v(-9.67, -45.64) * mm});
            skLineSegment(sketch, "E292", {"start": v(-9.67, -45.64) * mm, "end": v(-9.67, -45.17) * mm});
            skLineSegment(sketch, "E293", {"start": v(-9.67, -45.17) * mm, "end": v(-9.4, -44.78) * mm});
            skLineSegment(sketch, "E294", {"start": v(-9.4, -44.78) * mm, "end": v(-8.8, -44.66) * mm});
            skLineSegment(sketch, "E295", {"start": v(-8.8, -44.66) * mm, "end": v(-8.51, -44.8) * mm});
            skLineSegment(sketch, "E296", {"start": v(-8.51, -44.8) * mm, "end": v(-8.3, -44.9) * mm});
            skLineSegment(sketch, "E297", {"start": v(-8.3, -44.9) * mm, "end": v(-8.2, -44.94) * mm});
            skLineSegment(sketch, "E298", {"start": v(-8.2, -44.94) * mm, "end": v(-8.15, -44.95) * mm});
            skLineSegment(sketch, "E299", {"start": v(-8.15, -44.95) * mm, "end": v(-8.07, -44.95) * mm});
            skLineSegment(sketch, "E300", {"start": v(-8.07, -44.95) * mm, "end": v(-8.13, -44.54) * mm});
            skLineSegment(sketch, "E301", {"start": v(-8.13, -44.54) * mm, "end": v(-8.16, -44.38) * mm});
            skLineSegment(sketch, "E302", {"start": v(-8.16, -44.38) * mm, "end": v(-8.2, -44.23) * mm});
            skLineSegment(sketch, "E303", {"start": v(-8.2, -44.23) * mm, "end": v(-8.23, -44.13) * mm});
            skLineSegment(sketch, "E304", {"start": v(-8.23, -44.13) * mm, "end": v(-8.26, -44.07) * mm});
            skLineSegment(sketch, "E305", {"start": v(-8.26, -44.07) * mm, "end": v(-8.32, -44) * mm});
            skLineSegment(sketch, "E306", {"start": v(-8.32, -44) * mm, "end": v(-9.27, -44) * mm});
            skLineSegment(sketch, "E307", {"start": v(-9.27, -44) * mm, "end": v(-9.96, -44.34) * mm});
            skLineSegment(sketch, "E308", {"start": v(-9.96, -44.34) * mm, "end": v(-10.42, -45.04) * mm});
            skLineSegment(sketch, "E309", {"start": v(-10.42, -45.04) * mm, "end": v(-10.51, -45.83) * mm});
            skLineSegment(sketch, "E310", {"start": v(-10.51, -45.83) * mm, "end": v(-10.22, -46.4) * mm});
            skLineSegment(sketch, "E311", {"start": v(-10.22, -46.4) * mm, "end": v(-9.92, -46.61) * mm});
            skLineSegment(sketch, "E312", {"start": v(-9.92, -46.61) * mm, "end": v(-9.76, -46.72) * mm});
            skLineSegment(sketch, "E313", {"start": v(-9.76, -46.72) * mm, "end": v(-9.54, -46.85) * mm});
            skLineSegment(sketch, "E314", {"start": v(-9.54, -46.85) * mm, "end": v(-9.29, -46.98) * mm});
            skLineSegment(sketch, "E315", {"start": v(-9.29, -46.98) * mm, "end": v(-9.03, -47.1) * mm});
            skLineSegment(sketch, "E316", {"start": v(-9.03, -47.1) * mm, "end": v(-8.44, -47.37) * mm});
            skLineSegment(sketch, "E317", {"start": v(-8.44, -47.37) * mm, "end": v(-8.2, -47.94) * mm});
            skLineSegment(sketch, "E318", {"start": v(-8.2, -47.94) * mm, "end": v(-8.5, -48.4) * mm});
            skLineSegment(sketch, "E319", {"start": v(-8.5, -48.4) * mm, "end": v(-8.97, -48.61) * mm});
            skLineSegment(sketch, "E320", {"start": v(-8.97, -48.61) * mm, "end": v(-9.88, -48.1) * mm});
            skLineSegment(sketch, "E321", {"start": v(-9.88, -48.1) * mm, "end": v(-9.83, -48.57) * mm});
            skLineSegment(sketch, "E322", {"start": v(-9.83, -48.57) * mm, "end": v(-9.77, -48.92) * mm});
            skLineSegment(sketch, "E323", {"start": v(-9.77, -48.92) * mm, "end": v(-9.74, -49.05) * mm});
            skLineSegment(sketch, "E324", {"start": v(-9.74, -49.05) * mm, "end": v(-9.72, -49.12) * mm});
            skLineSegment(sketch, "E325", {"start": v(-9.72, -49.12) * mm, "end": v(-9.66, -49.2) * mm});
            skLineSegment(sketch, "E326", {"start": v(-9.66, -49.2) * mm, "end": v(-9.24, -49.2) * mm});
            skLineSegment(sketch, "E327", {"start": v(-9.24, -49.2) * mm, "end": v(-9.05, -49.2) * mm});
            skLineSegment(sketch, "E328", {"start": v(-9.05, -49.2) * mm, "end": v(-8.89, -49.18) * mm});
            skLineSegment(sketch, "E329", {"start": v(-8.89, -49.18) * mm, "end": v(-8.73, -49.15) * mm});
            skLineSegment(sketch, "E330", {"start": v(-8.73, -49.15) * mm, "end": v(-8.58, -49.12) * mm});
            skLineSegment(sketch, "E331", {"start": v(-8.58, -49.12) * mm, "end": v(-8.44, -49.07) * mm});
            skLineSegment(sketch, "E332", {"start": v(-8.44, -49.07) * mm, "end": v(-8.3, -49.01) * mm});
            skLineSegment(sketch, "E333", {"start": v(-8.3, -49.01) * mm, "end": v(-8.16, -48.94) * mm});
            skLineSegment(sketch, "E334", {"start": v(-8.16, -48.94) * mm, "end": v(-8.01, -48.86) * mm});
            skLineSegment(sketch, "E335", {"start": v(8.38, -47.46) * mm, "end": v(9.27, -46.4) * mm});
            skLineSegment(sketch, "E336", {"start": v(9.27, -46.4) * mm, "end": v(9.56, -45.82) * mm});
            skLineSegment(sketch, "E337", {"start": v(9.56, -45.82) * mm, "end": v(9.56, -44.98) * mm});
            skLineSegment(sketch, "E338", {"start": v(9.56, -44.98) * mm, "end": v(9.27, -44.42) * mm});
            skLineSegment(sketch, "E339", {"start": v(9.27, -44.42) * mm, "end": v(9.02, -44.24) * mm});
            skLineSegment(sketch, "E340", {"start": v(9.02, -44.24) * mm, "end": v(8.9, -44.17) * mm});
            skLineSegment(sketch, "E341", {"start": v(8.9, -44.17) * mm, "end": v(8.74, -44.09) * mm});
            skLineSegment(sketch, "E342", {"start": v(8.74, -44.09) * mm, "end": v(8.58, -44.02) * mm});
            skLineSegment(sketch, "E343", {"start": v(8.58, -44.02) * mm, "end": v(8.43, -43.97) * mm});
            skLineSegment(sketch, "E344", {"start": v(8.43, -43.97) * mm, "end": v(8.1, -43.88) * mm});
            skLineSegment(sketch, "E345", {"start": v(8.1, -43.88) * mm, "end": v(7.8, -43.95) * mm});
            skLineSegment(sketch, "E346", {"start": v(7.8, -43.95) * mm, "end": v(7.65, -43.99) * mm});
            skLineSegment(sketch, "E347", {"start": v(7.65, -43.99) * mm, "end": v(7.51, -44.03) * mm});
            skLineSegment(sketch, "E348", {"start": v(7.51, -44.03) * mm, "end": v(7.4, -44.08) * mm});
            skLineSegment(sketch, "E349", {"start": v(7.4, -44.08) * mm, "end": v(7.28, -44.14) * mm});
            skLineSegment(sketch, "E350", {"start": v(7.28, -44.14) * mm, "end": v(7.17, -44.2) * mm});
            skLineSegment(sketch, "E351", {"start": v(7.17, -44.2) * mm, "end": v(7.08, -44.3) * mm});
            skLineSegment(sketch, "E352", {"start": v(7.08, -44.3) * mm, "end": v(6.98, -44.39) * mm});
            skLineSegment(sketch, "E353", {"start": v(6.98, -44.39) * mm, "end": v(6.88, -44.5) * mm});
            skLineSegment(sketch, "E354", {"start": v(6.88, -44.5) * mm, "end": v(6.65, -44.77) * mm});
            skLineSegment(sketch, "E355", {"start": v(6.65, -44.77) * mm, "end": v(6.53, -45.4) * mm});
            skLineSegment(sketch, "E356", {"start": v(6.53, -45.4) * mm, "end": v(6.65, -46.07) * mm});
            skLineSegment(sketch, "E357", {"start": v(6.65, -46.07) * mm, "end": v(7.34, -46.76) * mm});
            skLineSegment(sketch, "E358", {"start": v(7.34, -46.76) * mm, "end": v(7.53, -46.76) * mm});
            skLineSegment(sketch, "E359", {"start": v(7.53, -46.76) * mm, "end": v(7.6, -46.77) * mm});
            skLineSegment(sketch, "E360", {"start": v(7.6, -46.77) * mm, "end": v(7.67, -46.79) * mm});
            skLineSegment(sketch, "E361", {"start": v(7.67, -46.79) * mm, "end": v(7.73, -46.81) * mm});
            skLineSegment(sketch, "E362", {"start": v(7.73, -46.81) * mm, "end": v(7.77, -46.84) * mm});
            skLineSegment(sketch, "E363", {"start": v(7.77, -46.84) * mm, "end": v(7.82, -46.93) * mm});
            skLineSegment(sketch, "E364", {"start": v(7.82, -46.93) * mm, "end": v(6.19, -48.74) * mm});
            skLineSegment(sketch, "E365", {"start": v(6.19, -48.74) * mm, "end": v(6.64, -48.84) * mm});
            skLineSegment(sketch, "E366", {"start": v(6.64, -48.84) * mm, "end": v(7, -48.91) * mm});
            skLineSegment(sketch, "E367", {"start": v(7, -48.91) * mm, "end": v(7.1, -48.93) * mm});
            skLineSegment(sketch, "E368", {"start": v(7.1, -48.93) * mm, "end": v(7.19, -48.92) * mm});
            skLineSegment(sketch, "E369", {"start": v(7.19, -48.92) * mm, "end": v(7.25, -48.9) * mm});
            skLineSegment(sketch, "E370", {"start": v(7.25, -48.9) * mm, "end": v(7.3, -48.87) * mm});
            skLineSegment(sketch, "E371", {"start": v(7.3, -48.87) * mm, "end": v(7.38, -48.73) * mm});
            skLineSegment(sketch, "E372", {"start": v(7.38, -48.73) * mm, "end": v(7.48, -48.53) * mm});
            skLineSegment(sketch, "E373", {"start": v(7.48, -48.53) * mm, "end": v(8.38, -47.46) * mm});
            skLineSegment(sketch, "E374", {"start": v(-4.1, -48.28) * mm, "end": v(-4.33, -46.17) * mm});
            skLineSegment(sketch, "E375", {"start": v(-4.33, -46.17) * mm, "end": v(-4.5, -44.1) * mm});
            skLineSegment(sketch, "E376", {"start": v(-4.5, -44.1) * mm, "end": v(-4.5, -43.93) * mm});
            skLineSegment(sketch, "E377", {"start": v(-4.5, -43.93) * mm, "end": v(-4.17, -43.98) * mm});
            skLineSegment(sketch, "E378", {"start": v(-4.17, -43.98) * mm, "end": v(-3.54, -44.1) * mm});
            skLineSegment(sketch, "E379", {"start": v(-3.54, -44.1) * mm, "end": v(-3.25, -44.15) * mm});
            skLineSegment(sketch, "E380", {"start": v(-3.25, -44.15) * mm, "end": v(-3.05, -43.39) * mm});
            skLineSegment(sketch, "E381", {"start": v(-3.05, -43.39) * mm, "end": v(-3.2, -43.26) * mm});
            skLineSegment(sketch, "E382", {"start": v(-3.2, -43.26) * mm, "end": v(-6.61, -43.57) * mm});
            skLineSegment(sketch, "E383", {"start": v(-6.61, -43.57) * mm, "end": v(-6.69, -43.65) * mm});
            skLineSegment(sketch, "E384", {"start": v(-6.69, -43.65) * mm, "end": v(-6.72, -43.71) * mm});
            skLineSegment(sketch, "E385", {"start": v(-6.72, -43.71) * mm, "end": v(-6.76, -43.82) * mm});
            skLineSegment(sketch, "E386", {"start": v(-6.76, -43.82) * mm, "end": v(-6.8, -43.97) * mm});
            skLineSegment(sketch, "E387", {"start": v(-6.8, -43.97) * mm, "end": v(-6.83, -44.13) * mm});
            skLineSegment(sketch, "E388", {"start": v(-6.83, -44.13) * mm, "end": v(-6.9, -44.53) * mm});
            skLineSegment(sketch, "E389", {"start": v(-6.9, -44.53) * mm, "end": v(-6.72, -44.46) * mm});
            skLineSegment(sketch, "E390", {"start": v(-6.72, -44.46) * mm, "end": v(-6.35, -44.32) * mm});
            skLineSegment(sketch, "E391", {"start": v(-6.35, -44.32) * mm, "end": v(-5.94, -44.2) * mm});
            skLineSegment(sketch, "E392", {"start": v(-5.94, -44.2) * mm, "end": v(-5.6, -44.1) * mm});
            skLineSegment(sketch, "E393", {"start": v(-5.6, -44.1) * mm, "end": v(-5.49, -44.08) * mm});
            skLineSegment(sketch, "E394", {"start": v(-5.49, -44.08) * mm, "end": v(-5.44, -44.08) * mm});
            skLineSegment(sketch, "E395", {"start": v(-5.44, -44.08) * mm, "end": v(-5.4, -44.13) * mm});
            skLineSegment(sketch, "E396", {"start": v(-5.4, -44.13) * mm, "end": v(-5.06, -47.8) * mm});
            skLineSegment(sketch, "E397", {"start": v(-5.06, -47.8) * mm, "end": v(-5, -48.53) * mm});
            skLineSegment(sketch, "E398", {"start": v(-5, -48.53) * mm, "end": v(-4.04, -48.47) * mm});
            skLineSegment(sketch, "E399", {"start": v(-4.04, -48.47) * mm, "end": v(-4.1, -48.28) * mm});
            skLineSegment(sketch, "E400", {"start": v(4.72, -48.22) * mm, "end": v(5.01, -48.02) * mm});
            skLineSegment(sketch, "E401", {"start": v(5.01, -48.02) * mm, "end": v(5.37, -47.31) * mm});
            skLineSegment(sketch, "E402", {"start": v(5.37, -47.31) * mm, "end": v(5.37, -46.75) * mm});
            skLineSegment(sketch, "E403", {"start": v(5.37, -46.75) * mm, "end": v(5.27, -46.55) * mm});
            skLineSegment(sketch, "E404", {"start": v(5.27, -46.55) * mm, "end": v(5.14, -46.35) * mm});
            skLineSegment(sketch, "E405", {"start": v(5.14, -46.35) * mm, "end": v(4.99, -46.16) * mm});
            skLineSegment(sketch, "E406", {"start": v(4.99, -46.16) * mm, "end": v(4.8, -45.96) * mm});
            skLineSegment(sketch, "E407", {"start": v(4.8, -45.96) * mm, "end": v(5.3, -45.3) * mm});
            skLineSegment(sketch, "E408", {"start": v(5.3, -45.3) * mm, "end": v(5.38, -44.45) * mm});
            skLineSegment(sketch, "E409", {"start": v(5.38, -44.45) * mm, "end": v(5.03, -43.82) * mm});
            skLineSegment(sketch, "E410", {"start": v(5.03, -43.82) * mm, "end": v(4.46, -43.42) * mm});
            skLineSegment(sketch, "E411", {"start": v(4.46, -43.42) * mm, "end": v(3.73, -43.3) * mm});
            skLineSegment(sketch, "E412", {"start": v(3.73, -43.3) * mm, "end": v(2.89, -43.73) * mm});
            skLineSegment(sketch, "E413", {"start": v(2.89, -43.73) * mm, "end": v(2.54, -44.2) * mm});
            skLineSegment(sketch, "E414", {"start": v(2.54, -44.2) * mm, "end": v(2.45, -45.02) * mm});
            skLineSegment(sketch, "E415", {"start": v(2.45, -45.02) * mm, "end": v(2.86, -45.75) * mm});
            skLineSegment(sketch, "E416", {"start": v(2.86, -45.75) * mm, "end": v(2.3, -46.32) * mm});
            skLineSegment(sketch, "E417", {"start": v(2.3, -46.32) * mm, "end": v(2.11, -46.98) * mm});
            skLineSegment(sketch, "E418", {"start": v(2.11, -46.98) * mm, "end": v(2.3, -47.67) * mm});
            skLineSegment(sketch, "E419", {"start": v(2.3, -47.67) * mm, "end": v(2.58, -48) * mm});
            skLineSegment(sketch, "E420", {"start": v(2.58, -48) * mm, "end": v(2.7, -48.12) * mm});
            skLineSegment(sketch, "E421", {"start": v(2.7, -48.12) * mm, "end": v(2.8, -48.22) * mm});
            skLineSegment(sketch, "E422", {"start": v(2.8, -48.22) * mm, "end": v(2.9, -48.3) * mm});
            skLineSegment(sketch, "E423", {"start": v(2.9, -48.3) * mm, "end": v(2.99, -48.37) * mm});
            skLineSegment(sketch, "E424", {"start": v(2.99, -48.37) * mm, "end": v(3.08, -48.42) * mm});
            skLineSegment(sketch, "E425", {"start": v(3.08, -48.42) * mm, "end": v(3.2, -48.45) * mm});
            skLineSegment(sketch, "E426", {"start": v(3.2, -48.45) * mm, "end": v(3.32, -48.48) * mm});
            skLineSegment(sketch, "E427", {"start": v(3.32, -48.48) * mm, "end": v(3.47, -48.5) * mm});
            skLineSegment(sketch, "E428", {"start": v(3.47, -48.5) * mm, "end": v(3.78, -48.55) * mm});
            skLineSegment(sketch, "E429", {"start": v(3.78, -48.55) * mm, "end": v(4.43, -48.43) * mm});
            skLineSegment(sketch, "E430", {"start": v(4.43, -48.43) * mm, "end": v(4.72, -48.22) * mm});
            skLineSegment(sketch, "E431", {"start": v(-0.7, -47.81) * mm, "end": v(-0.7, -47.52) * mm});
            skLineSegment(sketch, "E432", {"start": v(-0.7, -47.52) * mm, "end": v(-0.86, -47.37) * mm});
            skLineSegment(sketch, "E433", {"start": v(-0.86, -47.37) * mm, "end": v(-0.96, -47.3) * mm});
            skLineSegment(sketch, "E434", {"start": v(-0.96, -47.3) * mm, "end": v(-1.08, -47.24) * mm});
            skLineSegment(sketch, "E435", {"start": v(-1.08, -47.24) * mm, "end": v(-1.2, -47.2) * mm});
            skLineSegment(sketch, "E436", {"start": v(-1.2, -47.2) * mm, "end": v(-1.31, -47.2) * mm});
            skLineSegment(sketch, "E437", {"start": v(-1.31, -47.2) * mm, "end": v(-1.43, -47.2) * mm});
            skLineSegment(sketch, "E438", {"start": v(-1.43, -47.2) * mm, "end": v(-1.54, -47.23) * mm});
            skLineSegment(sketch, "E439", {"start": v(-1.54, -47.23) * mm, "end": v(-1.65, -47.29) * mm});
            skLineSegment(sketch, "E440", {"start": v(-1.65, -47.29) * mm, "end": v(-1.74, -47.36) * mm});
            skLineSegment(sketch, "E441", {"start": v(-1.74, -47.36) * mm, "end": v(-1.88, -47.5) * mm});
            skLineSegment(sketch, "E442", {"start": v(-1.88, -47.5) * mm, "end": v(-1.88, -48.06) * mm});
            skLineSegment(sketch, "E443", {"start": v(-1.88, -48.06) * mm, "end": v(-1.58, -48.4) * mm});
            skLineSegment(sketch, "E444", {"start": v(-1.58, -48.4) * mm, "end": v(-1.1, -48.4) * mm});
            skLineSegment(sketch, "E445", {"start": v(-1.1, -48.4) * mm, "end": v(-0.7, -48.11) * mm});
            skLineSegment(sketch, "E446", {"start": v(-0.7, -48.11) * mm, "end": v(-0.7, -47.81) * mm});
            skLineSegment(sketch, "E447", {"start": v(1.3, -48.08) * mm, "end": v(1.25, -45.67) * mm});
            skLineSegment(sketch, "E448", {"start": v(1.25, -45.67) * mm, "end": v(1.21, -43.3) * mm});
            skLineSegment(sketch, "E449", {"start": v(1.21, -43.3) * mm, "end": v(1.2, -43.27) * mm});
            skLineSegment(sketch, "E450", {"start": v(1.2, -43.27) * mm, "end": v(1.17, -43.25) * mm});
            skLineSegment(sketch, "E451", {"start": v(1.17, -43.25) * mm, "end": v(1.14, -43.23) * mm});
            skLineSegment(sketch, "E452", {"start": v(1.14, -43.23) * mm, "end": v(1.1, -43.23) * mm});
            skLineSegment(sketch, "E453", {"start": v(1.1, -43.23) * mm, "end": v(1.06, -43.24) * mm});
            skLineSegment(sketch, "E454", {"start": v(1.06, -43.24) * mm, "end": v(1.01, -43.26) * mm});
            skLineSegment(sketch, "E455", {"start": v(1.01, -43.26) * mm, "end": v(0.87, -43.34) * mm});
            skLineSegment(sketch, "E456", {"start": v(0.87, -43.34) * mm, "end": v(0.7, -43.46) * mm});
            skLineSegment(sketch, "E457", {"start": v(0.7, -43.46) * mm, "end": v(0.5, -43.6) * mm});
            skLineSegment(sketch, "E458", {"start": v(0.5, -43.6) * mm, "end": v(0.33, -43.75) * mm});
            skLineSegment(sketch, "E459", {"start": v(0.33, -43.75) * mm, "end": v(0.17, -43.88) * mm});
            skLineSegment(sketch, "E460", {"start": v(0.17, -43.88) * mm, "end": v(0.06, -43.99) * mm});
            skLineSegment(sketch, "E461", {"start": v(0.06, -43.99) * mm, "end": v(0.03, -44.03) * mm});
            skLineSegment(sketch, "E462", {"start": v(0.03, -44.03) * mm, "end": v(0.02, -44.05) * mm});
            skLineSegment(sketch, "E463", {"start": v(0.02, -44.05) * mm, "end": v(0.02, -44.13) * mm});
            skLineSegment(sketch, "E464", {"start": v(0.02, -44.13) * mm, "end": v(0.4, -44.13) * mm});
            skLineSegment(sketch, "E465", {"start": v(0.4, -44.13) * mm, "end": v(0.34, -48.3) * mm});
            skLineSegment(sketch, "E466", {"start": v(0.34, -48.3) * mm, "end": v(1.3, -48.3) * mm});
            skLineSegment(sketch, "E467", {"start": v(1.3, -48.3) * mm, "end": v(1.3, -48.24) * mm});
            skLineSegment(sketch, "E468", {"start": v(1.3, -48.24) * mm, "end": v(1.3, -48.16) * mm});
            skLineSegment(sketch, "E469", {"start": v(1.3, -48.16) * mm, "end": v(1.3, -48.08) * mm});
            skLineSegment(sketch, "E470", {"start": v(3.73, -47.85) * mm, "end": v(4, -47.85) * mm});
            skLineSegment(sketch, "E471", {"start": v(4, -47.85) * mm, "end": v(4.47, -47.44) * mm});
            skLineSegment(sketch, "E472", {"start": v(4.47, -47.44) * mm, "end": v(4.58, -46.77) * mm});
            skLineSegment(sketch, "E473", {"start": v(4.58, -46.77) * mm, "end": v(4.02, -46.22) * mm});
            skLineSegment(sketch, "E474", {"start": v(4.02, -46.22) * mm, "end": v(3.4, -46.22) * mm});
            skLineSegment(sketch, "E475", {"start": v(3.4, -46.22) * mm, "end": v(2.92, -46.7) * mm});
            skLineSegment(sketch, "E476", {"start": v(2.92, -46.7) * mm, "end": v(2.92, -47.32) * mm});
            skLineSegment(sketch, "E477", {"start": v(2.92, -47.32) * mm, "end": v(3.45, -47.85) * mm});
            skLineSegment(sketch, "E478", {"start": v(3.45, -47.85) * mm, "end": v(3.73, -47.85) * mm});
            skLineSegment(sketch, "E479", {"start": v(8.03, -46.13) * mm, "end": v(8.34, -46.13) * mm});
            skLineSegment(sketch, "E480", {"start": v(8.34, -46.13) * mm, "end": v(8.81, -45.65) * mm});
            skLineSegment(sketch, "E481", {"start": v(8.81, -45.65) * mm, "end": v(8.81, -45.08) * mm});
            skLineSegment(sketch, "E482", {"start": v(8.81, -45.08) * mm, "end": v(8.54, -44.69) * mm});
            skLineSegment(sketch, "E483", {"start": v(8.54, -44.69) * mm, "end": v(7.93, -44.57) * mm});
            skLineSegment(sketch, "E484", {"start": v(7.93, -44.57) * mm, "end": v(7.38, -44.85) * mm});
            skLineSegment(sketch, "E485", {"start": v(7.38, -44.85) * mm, "end": v(7.33, -45) * mm});
            skLineSegment(sketch, "E486", {"start": v(7.33, -45) * mm, "end": v(7.3, -45.08) * mm});
            skLineSegment(sketch, "E487", {"start": v(7.3, -45.08) * mm, "end": v(7.29, -45.18) * mm});
            skLineSegment(sketch, "E488", {"start": v(7.29, -45.18) * mm, "end": v(7.28, -45.3) * mm});
            skLineSegment(sketch, "E489", {"start": v(7.28, -45.3) * mm, "end": v(7.27, -45.41) * mm});
            skLineSegment(sketch, "E490", {"start": v(7.27, -45.41) * mm, "end": v(7.27, -45.68) * mm});
            skLineSegment(sketch, "E491", {"start": v(7.27, -45.68) * mm, "end": v(7.72, -46.13) * mm});
            skLineSegment(sketch, "E492", {"start": v(7.72, -46.13) * mm, "end": v(8.03, -46.13) * mm});
            skLineSegment(sketch, "E493", {"start": v(3.9, -45.58) * mm, "end": v(4.16, -45.58) * mm});
            skLineSegment(sketch, "E494", {"start": v(4.16, -45.58) * mm, "end": v(4.64, -45.14) * mm});
            skLineSegment(sketch, "E495", {"start": v(4.64, -45.14) * mm, "end": v(4.64, -44.87) * mm});
            skLineSegment(sketch, "E496", {"start": v(4.64, -44.87) * mm, "end": v(4.63, -44.64) * mm});
            skLineSegment(sketch, "E497", {"start": v(4.63, -44.64) * mm, "end": v(4.6, -44.53) * mm});
            skLineSegment(sketch, "E498", {"start": v(4.6, -44.53) * mm, "end": v(4.59, -44.46) * mm});
            skLineSegment(sketch, "E499", {"start": v(4.59, -44.46) * mm, "end": v(4.53, -44.3) * mm});
            skLineSegment(sketch, "E500", {"start": v(4.53, -44.3) * mm, "end": v(4.28, -44.18) * mm});
            skLineSegment(sketch, "E501", {"start": v(4.28, -44.18) * mm, "end": v(4.16, -44.12) * mm});
            skLineSegment(sketch, "E502", {"start": v(4.16, -44.12) * mm, "end": v(4.04, -44.08) * mm});
            skLineSegment(sketch, "E503", {"start": v(4.04, -44.08) * mm, "end": v(3.92, -44.05) * mm});
            skLineSegment(sketch, "E504", {"start": v(3.92, -44.05) * mm, "end": v(3.83, -44.04) * mm});
            skLineSegment(sketch, "E505", {"start": v(3.83, -44.04) * mm, "end": v(3.63, -44.04) * mm});
            skLineSegment(sketch, "E506", {"start": v(3.63, -44.04) * mm, "end": v(3.1, -44.57) * mm});
            skLineSegment(sketch, "E507", {"start": v(3.1, -44.57) * mm, "end": v(3.1, -45.05) * mm});
            skLineSegment(sketch, "E508", {"start": v(3.1, -45.05) * mm, "end": v(3.63, -45.58) * mm});
            skLineSegment(sketch, "E509", {"start": v(3.63, -45.58) * mm, "end": v(3.9, -45.58) * mm});
            skLineSegment(sketch, "E510", {"start": v(-33.19, -43.76) * mm, "end": v(-31.83, -43.77) * mm});
            skLineSegment(sketch, "E511", {"start": v(-31.83, -43.77) * mm, "end": v(-31.06, -43.68) * mm});
            skLineSegment(sketch, "E512", {"start": v(-31.06, -43.68) * mm, "end": v(-30.72, -43.63) * mm});
            skLineSegment(sketch, "E513", {"start": v(-30.72, -43.63) * mm, "end": v(-30.37, -43.57) * mm});
            skLineSegment(sketch, "E514", {"start": v(-30.37, -43.57) * mm, "end": v(-29.62, -43.43) * mm});
            skLineSegment(sketch, "E515", {"start": v(-29.62, -43.43) * mm, "end": v(-28.82, -43.24) * mm});
            skLineSegment(sketch, "E516", {"start": v(-28.82, -43.24) * mm, "end": v(-28, -43.02) * mm});
            skLineSegment(sketch, "E517", {"start": v(-28, -43.02) * mm, "end": v(-27.14, -42.77) * mm});
            skLineSegment(sketch, "E518", {"start": v(-27.14, -42.77) * mm, "end": v(-26.28, -42.5) * mm});
            skLineSegment(sketch, "E519", {"start": v(-26.28, -42.5) * mm, "end": v(-25.43, -42.19) * mm});
            skLineSegment(sketch, "E520", {"start": v(-25.43, -42.19) * mm, "end": v(-24.59, -41.86) * mm});
            skLineSegment(sketch, "E521", {"start": v(-24.59, -41.86) * mm, "end": v(-23.5, -41.42) * mm});
            skLineSegment(sketch, "E522", {"start": v(-23.5, -41.42) * mm, "end": v(-23.2, -41.42) * mm});
            skLineSegment(sketch, "E523", {"start": v(-23.2, -41.42) * mm, "end": v(-23.09, -41.85) * mm});
            skLineSegment(sketch, "E524", {"start": v(-23.09, -41.85) * mm, "end": v(-22.16, -42.86) * mm});
            skLineSegment(sketch, "E525", {"start": v(-22.16, -42.86) * mm, "end": v(-21.6, -43.13) * mm});
            skLineSegment(sketch, "E526", {"start": v(-21.6, -43.13) * mm, "end": v(-21.35, -43.24) * mm});
            skLineSegment(sketch, "E527", {"start": v(-21.35, -43.24) * mm, "end": v(-21.07, -43.35) * mm});
            skLineSegment(sketch, "E528", {"start": v(-21.07, -43.35) * mm, "end": v(-20.79, -43.44) * mm});
            skLineSegment(sketch, "E529", {"start": v(-20.79, -43.44) * mm, "end": v(-20.55, -43.5) * mm});
            skLineSegment(sketch, "E530", {"start": v(-20.55, -43.5) * mm, "end": v(-20.05, -43.63) * mm});
            skLineSegment(sketch, "E531", {"start": v(-20.05, -43.63) * mm, "end": v(-17.51, -43.62) * mm});
            skLineSegment(sketch, "E532", {"start": v(-17.51, -43.62) * mm, "end": v(-16.43, -43.43) * mm});
            skLineSegment(sketch, "E533", {"start": v(-16.43, -43.43) * mm, "end": v(-15.88, -43.32) * mm});
            skLineSegment(sketch, "E534", {"start": v(-15.88, -43.32) * mm, "end": v(-15.2, -43.17) * mm});
            skLineSegment(sketch, "E535", {"start": v(-15.2, -43.17) * mm, "end": v(-14.48, -43) * mm});
            skLineSegment(sketch, "E536", {"start": v(-14.48, -43) * mm, "end": v(-13.8, -42.81) * mm});
            skLineSegment(sketch, "E537", {"start": v(-13.8, -42.81) * mm, "end": v(-12.05, -42.35) * mm});
            skLineSegment(sketch, "E538", {"start": v(-12.05, -42.35) * mm, "end": v(-10.46, -41.95) * mm});
            skLineSegment(sketch, "E539", {"start": v(-10.46, -41.95) * mm, "end": v(-9.73, -41.77) * mm});
            skLineSegment(sketch, "E540", {"start": v(-9.73, -41.77) * mm, "end": v(-9.02, -41.61) * mm});
            skLineSegment(sketch, "E541", {"start": v(-9.02, -41.61) * mm, "end": v(-8.34, -41.47) * mm});
            skLineSegment(sketch, "E542", {"start": v(-8.34, -41.47) * mm, "end": v(-7.69, -41.33) * mm});
            skLineSegment(sketch, "E543", {"start": v(-7.69, -41.33) * mm, "end": v(-7.06, -41.22) * mm});
            skLineSegment(sketch, "E544", {"start": v(-7.06, -41.22) * mm, "end": v(-6.44, -41.1) * mm});
            skLineSegment(sketch, "E545", {"start": v(-6.44, -41.1) * mm, "end": v(-5.83, -41.01) * mm});
            skLineSegment(sketch, "E546", {"start": v(-5.83, -41.01) * mm, "end": v(-5.24, -40.93) * mm});
            skLineSegment(sketch, "E547", {"start": v(-5.24, -40.93) * mm, "end": v(-4.65, -40.85) * mm});
            skLineSegment(sketch, "E548", {"start": v(-4.65, -40.85) * mm, "end": v(-4.06, -40.79) * mm});
            skLineSegment(sketch, "E549", {"start": v(-4.06, -40.79) * mm, "end": v(-3.47, -40.73) * mm});
            skLineSegment(sketch, "E550", {"start": v(-3.47, -40.73) * mm, "end": v(-2.88, -40.68) * mm});
            skLineSegment(sketch, "E551", {"start": v(-2.88, -40.68) * mm, "end": v(-1.47, -40.58) * mm});
            skLineSegment(sketch, "E552", {"start": v(-1.47, -40.58) * mm, "end": v(3.24, -40.68) * mm});
            skLineSegment(sketch, "E553", {"start": v(3.24, -40.68) * mm, "end": v(4.46, -40.83) * mm});
            skLineSegment(sketch, "E554", {"start": v(4.46, -40.83) * mm, "end": v(5.07, -40.9) * mm});
            skLineSegment(sketch, "E555", {"start": v(5.07, -40.9) * mm, "end": v(5.82, -41.02) * mm});
            skLineSegment(sketch, "E556", {"start": v(5.82, -41.02) * mm, "end": v(6.62, -41.15) * mm});
            skLineSegment(sketch, "E557", {"start": v(6.62, -41.15) * mm, "end": v(7.36, -41.28) * mm});
            skLineSegment(sketch, "E558", {"start": v(7.36, -41.28) * mm, "end": v(9.04, -41.59) * mm});
            skLineSegment(sketch, "E559", {"start": v(9.04, -41.59) * mm, "end": v(12.94, -42.59) * mm});
            skLineSegment(sketch, "E560", {"start": v(12.94, -42.59) * mm, "end": v(15.72, -43.32) * mm});
            skLineSegment(sketch, "E561", {"start": v(15.72, -43.32) * mm, "end": v(17.47, -43.62) * mm});
            skLineSegment(sketch, "E562", {"start": v(17.47, -43.62) * mm, "end": v(20.1, -43.62) * mm});
            skLineSegment(sketch, "E563", {"start": v(20.1, -43.62) * mm, "end": v(20.68, -43.46) * mm});
            skLineSegment(sketch, "E564", {"start": v(20.68, -43.46) * mm, "end": v(20.95, -43.38) * mm});
            skLineSegment(sketch, "E565", {"start": v(20.95, -43.38) * mm, "end": v(21.23, -43.28) * mm});
            skLineSegment(sketch, "E566", {"start": v(21.23, -43.28) * mm, "end": v(21.49, -43.18) * mm});
            skLineSegment(sketch, "E567", {"start": v(21.49, -43.18) * mm, "end": v(21.7, -43.07) * mm});
            skLineSegment(sketch, "E568", {"start": v(21.7, -43.07) * mm, "end": v(22.12, -42.84) * mm});
            skLineSegment(sketch, "E569", {"start": v(22.12, -42.84) * mm, "end": v(22.86, -42.12) * mm});
            skLineSegment(sketch, "E570", {"start": v(22.86, -42.12) * mm, "end": v(23.24, -41.33) * mm});
            skLineSegment(sketch, "E571", {"start": v(23.24, -41.33) * mm, "end": v(23.57, -41.47) * mm});
            skLineSegment(sketch, "E572", {"start": v(23.57, -41.47) * mm, "end": v(24.53, -41.87) * mm});
            skLineSegment(sketch, "E573", {"start": v(24.53, -41.87) * mm, "end": v(25.48, -42.23) * mm});
            skLineSegment(sketch, "E574", {"start": v(25.48, -42.23) * mm, "end": v(26.42, -42.55) * mm});
            skLineSegment(sketch, "E575", {"start": v(26.42, -42.55) * mm, "end": v(27.34, -42.84) * mm});
            skLineSegment(sketch, "E576", {"start": v(27.34, -42.84) * mm, "end": v(28.23, -43.1) * mm});
            skLineSegment(sketch, "E577", {"start": v(28.23, -43.1) * mm, "end": v(28.67, -43.21) * mm});
            skLineSegment(sketch, "E578", {"start": v(28.67, -43.21) * mm, "end": v(29.1, -43.32) * mm});
            skLineSegment(sketch, "E579", {"start": v(29.1, -43.32) * mm, "end": v(29.53, -43.4) * mm});
            skLineSegment(sketch, "E580", {"start": v(29.53, -43.4) * mm, "end": v(29.95, -43.5) * mm});
            skLineSegment(sketch, "E581", {"start": v(29.95, -43.5) * mm, "end": v(30.36, -43.57) * mm});
            skLineSegment(sketch, "E582", {"start": v(30.36, -43.57) * mm, "end": v(30.76, -43.63) * mm});
            skLineSegment(sketch, "E583", {"start": v(30.76, -43.63) * mm, "end": v(31.72, -43.77) * mm});
            skLineSegment(sketch, "E584", {"start": v(31.72, -43.77) * mm, "end": v(34.35, -43.77) * mm});
            skLineSegment(sketch, "E585", {"start": v(34.35, -43.77) * mm, "end": v(35.95, -43.5) * mm});
            skLineSegment(sketch, "E586", {"start": v(35.95, -43.5) * mm, "end": v(36.76, -43.22) * mm});
            skLineSegment(sketch, "E587", {"start": v(36.76, -43.22) * mm, "end": v(37.13, -43.09) * mm});
            skLineSegment(sketch, "E588", {"start": v(37.13, -43.09) * mm, "end": v(37.52, -42.93) * mm});
            skLineSegment(sketch, "E589", {"start": v(37.52, -42.93) * mm, "end": v(37.89, -42.77) * mm});
            skLineSegment(sketch, "E590", {"start": v(37.89, -42.77) * mm, "end": v(38.2, -42.62) * mm});
            skLineSegment(sketch, "E591", {"start": v(38.2, -42.62) * mm, "end": v(38.8, -42.3) * mm});
            skLineSegment(sketch, "E592", {"start": v(38.8, -42.3) * mm, "end": v(38.8, -42.22) * mm});
            skLineSegment(sketch, "E593", {"start": v(38.8, -42.22) * mm, "end": v(38.8, -42.2) * mm});
            skLineSegment(sketch, "E594", {"start": v(38.8, -42.2) * mm, "end": v(38.78, -42.18) * mm});
            skLineSegment(sketch, "E595", {"start": v(38.78, -42.18) * mm, "end": v(38.7, -42.11) * mm});
            skLineSegment(sketch, "E596", {"start": v(38.7, -42.11) * mm, "end": v(38.59, -42.04) * mm});
            skLineSegment(sketch, "E597", {"start": v(38.59, -42.04) * mm, "end": v(38.45, -41.96) * mm});
            skLineSegment(sketch, "E598", {"start": v(38.45, -41.96) * mm, "end": v(38.09, -41.78) * mm});
            skLineSegment(sketch, "E599", {"start": v(38.09, -41.78) * mm, "end": v(37.56, -42) * mm});
            skLineSegment(sketch, "E600", {"start": v(37.56, -42) * mm, "end": v(37.26, -42.11) * mm});
            skLineSegment(sketch, "E601", {"start": v(37.26, -42.11) * mm, "end": v(36.94, -42.23) * mm});
            skLineSegment(sketch, "E602", {"start": v(36.94, -42.23) * mm, "end": v(36.6, -42.35) * mm});
            skLineSegment(sketch, "E603", {"start": v(36.6, -42.35) * mm, "end": v(36.24, -42.46) * mm});
            skLineSegment(sketch, "E604", {"start": v(36.24, -42.46) * mm, "end": v(35.89, -42.56) * mm});
            skLineSegment(sketch, "E605", {"start": v(35.89, -42.56) * mm, "end": v(35.55, -42.65) * mm});
            skLineSegment(sketch, "E606", {"start": v(35.55, -42.65) * mm, "end": v(35.22, -42.73) * mm});
            skLineSegment(sketch, "E607", {"start": v(35.22, -42.73) * mm, "end": v(34.91, -42.79) * mm});
            skLineSegment(sketch, "E608", {"start": v(34.91, -42.79) * mm, "end": v(34.23, -42.9) * mm});
            skLineSegment(sketch, "E609", {"start": v(34.23, -42.9) * mm, "end": v(30.88, -42.9) * mm});
            skLineSegment(sketch, "E610", {"start": v(30.88, -42.9) * mm, "end": v(29.97, -42.74) * mm});
            skLineSegment(sketch, "E611", {"start": v(29.97, -42.74) * mm, "end": v(29.28, -42.6) * mm});
            skLineSegment(sketch, "E612", {"start": v(29.28, -42.6) * mm, "end": v(28.57, -42.45) * mm});
            skLineSegment(sketch, "E613", {"start": v(28.57, -42.45) * mm, "end": v(27.86, -42.26) * mm});
            skLineSegment(sketch, "E614", {"start": v(27.86, -42.26) * mm, "end": v(27.14, -42.06) * mm});
            skLineSegment(sketch, "E615", {"start": v(27.14, -42.06) * mm, "end": v(26.41, -41.83) * mm});
            skLineSegment(sketch, "E616", {"start": v(26.41, -41.83) * mm, "end": v(25.68, -41.58) * mm});
            skLineSegment(sketch, "E617", {"start": v(25.68, -41.58) * mm, "end": v(24.94, -41.3) * mm});
            skLineSegment(sketch, "E618", {"start": v(24.94, -41.3) * mm, "end": v(24.2, -41) * mm});
            skLineSegment(sketch, "E619", {"start": v(24.2, -41) * mm, "end": v(23, -40.51) * mm});
            skLineSegment(sketch, "E620", {"start": v(23, -40.51) * mm, "end": v(23, -40.53) * mm});
            skLineSegment(sketch, "E621", {"start": v(23, -40.53) * mm, "end": v(22.78, -40.98) * mm});
            skLineSegment(sketch, "E622", {"start": v(22.78, -40.98) * mm, "end": v(22.57, -41.41) * mm});
            skLineSegment(sketch, "E623", {"start": v(22.57, -41.41) * mm, "end": v(21.78, -42.3) * mm});
            skLineSegment(sketch, "E624", {"start": v(21.78, -42.3) * mm, "end": v(20.9, -42.68) * mm});
            skLineSegment(sketch, "E625", {"start": v(20.9, -42.68) * mm, "end": v(20.32, -42.77) * mm});
            skLineSegment(sketch, "E626", {"start": v(20.32, -42.77) * mm, "end": v(20.05, -42.8) * mm});
            skLineSegment(sketch, "E627", {"start": v(20.05, -42.8) * mm, "end": v(19.76, -42.84) * mm});
            skLineSegment(sketch, "E628", {"start": v(19.76, -42.84) * mm, "end": v(19.47, -42.86) * mm});
            skLineSegment(sketch, "E629", {"start": v(19.47, -42.86) * mm, "end": v(19.23, -42.86) * mm});
            skLineSegment(sketch, "E630", {"start": v(19.23, -42.86) * mm, "end": v(18.94, -42.86) * mm});
            skLineSegment(sketch, "E631", {"start": v(18.94, -42.86) * mm, "end": v(18.58, -42.83) * mm});
            skLineSegment(sketch, "E632", {"start": v(18.58, -42.83) * mm, "end": v(18.16, -42.78) * mm});
            skLineSegment(sketch, "E633", {"start": v(18.16, -42.78) * mm, "end": v(17.7, -42.73) * mm});
            skLineSegment(sketch, "E634", {"start": v(17.7, -42.73) * mm, "end": v(17.25, -42.67) * mm});
            skLineSegment(sketch, "E635", {"start": v(17.25, -42.67) * mm, "end": v(16.82, -42.6) * mm});
            skLineSegment(sketch, "E636", {"start": v(16.82, -42.6) * mm, "end": v(16.43, -42.53) * mm});
            skLineSegment(sketch, "E637", {"start": v(16.43, -42.53) * mm, "end": v(16.11, -42.46) * mm});
            skLineSegment(sketch, "E638", {"start": v(16.11, -42.46) * mm, "end": v(12.12, -41.51) * mm});
            skLineSegment(sketch, "E639", {"start": v(12.12, -41.51) * mm, "end": v(8.68, -40.7) * mm});
            skLineSegment(sketch, "E640", {"start": v(8.68, -40.7) * mm, "end": v(7.23, -40.43) * mm});
            skLineSegment(sketch, "E641", {"start": v(7.23, -40.43) * mm, "end": v(6.55, -40.3) * mm});
            skLineSegment(sketch, "E642", {"start": v(6.55, -40.3) * mm, "end": v(5.78, -40.18) * mm});
            skLineSegment(sketch, "E643", {"start": v(5.78, -40.18) * mm, "end": v(5, -40.06) * mm});
            skLineSegment(sketch, "E644", {"start": v(5, -40.06) * mm, "end": v(4.33, -39.96) * mm});
            skLineSegment(sketch, "E645", {"start": v(4.33, -39.96) * mm, "end": v(2.88, -39.78) * mm});
            skLineSegment(sketch, "E646", {"start": v(2.88, -39.78) * mm, "end": v(-0.93, -39.67) * mm});
            skLineSegment(sketch, "E647", {"start": v(-0.93, -39.67) * mm, "end": v(-2.38, -39.78) * mm});
            skLineSegment(sketch, "E648", {"start": v(-2.38, -39.78) * mm, "end": v(-3.42, -39.86) * mm});
            skLineSegment(sketch, "E649", {"start": v(-3.42, -39.86) * mm, "end": v(-4.44, -39.98) * mm});
            skLineSegment(sketch, "E650", {"start": v(-4.44, -39.98) * mm, "end": v(-5.5, -40.12) * mm});
            skLineSegment(sketch, "E651", {"start": v(-5.5, -40.12) * mm, "end": v(-6.6, -40.3) * mm});
            skLineSegment(sketch, "E652", {"start": v(-6.6, -40.3) * mm, "end": v(-7.8, -40.53) * mm});
            skLineSegment(sketch, "E653", {"start": v(-7.8, -40.53) * mm, "end": v(-9.11, -40.81) * mm});
            skLineSegment(sketch, "E654", {"start": v(-9.11, -40.81) * mm, "end": v(-10.59, -41.14) * mm});
            skLineSegment(sketch, "E655", {"start": v(-10.59, -41.14) * mm, "end": v(-12.26, -41.54) * mm});
            skLineSegment(sketch, "E656", {"start": v(-12.26, -41.54) * mm, "end": v(-16.1, -42.44) * mm});
            skLineSegment(sketch, "E657", {"start": v(-16.1, -42.44) * mm, "end": v(-16.59, -42.54) * mm});
            skLineSegment(sketch, "E658", {"start": v(-16.59, -42.54) * mm, "end": v(-17.12, -42.64) * mm});
            skLineSegment(sketch, "E659", {"start": v(-17.12, -42.64) * mm, "end": v(-17.65, -42.72) * mm});
            skLineSegment(sketch, "E660", {"start": v(-17.65, -42.72) * mm, "end": v(-18.1, -42.78) * mm});
            skLineSegment(sketch, "E661", {"start": v(-18.1, -42.78) * mm, "end": v(-19.05, -42.89) * mm});
            skLineSegment(sketch, "E662", {"start": v(-19.05, -42.89) * mm, "end": v(-20.5, -42.78) * mm});
            skLineSegment(sketch, "E663", {"start": v(-20.5, -42.78) * mm, "end": v(-21.62, -42.4) * mm});
            skLineSegment(sketch, "E664", {"start": v(-21.62, -42.4) * mm, "end": v(-22.42, -41.7) * mm});
            skLineSegment(sketch, "E665", {"start": v(-22.42, -41.7) * mm, "end": v(-22.72, -41.13) * mm});
            skLineSegment(sketch, "E666", {"start": v(-22.72, -41.13) * mm, "end": v(-23.04, -40.53) * mm});
            skLineSegment(sketch, "E667", {"start": v(-23.04, -40.53) * mm, "end": v(-23.06, -40.51) * mm});
            skLineSegment(sketch, "E668", {"start": v(-23.06, -40.51) * mm, "end": v(-24.24, -41) * mm});
            skLineSegment(sketch, "E669", {"start": v(-24.24, -41) * mm, "end": v(-24.79, -41.22) * mm});
            skLineSegment(sketch, "E670", {"start": v(-24.79, -41.22) * mm, "end": v(-25.4, -41.45) * mm});
            skLineSegment(sketch, "E671", {"start": v(-25.4, -41.45) * mm, "end": v(-26.02, -41.67) * mm});
            skLineSegment(sketch, "E672", {"start": v(-26.02, -41.67) * mm, "end": v(-26.54, -41.85) * mm});
            skLineSegment(sketch, "E673", {"start": v(-26.54, -41.85) * mm, "end": v(-28.39, -42.4) * mm});
            skLineSegment(sketch, "E674", {"start": v(-28.39, -42.4) * mm, "end": v(-29.15, -42.58) * mm});
            skLineSegment(sketch, "E675", {"start": v(-29.15, -42.58) * mm, "end": v(-29.97, -42.74) * mm});
            skLineSegment(sketch, "E676", {"start": v(-29.97, -42.74) * mm, "end": v(-30.84, -42.9) * mm});
            skLineSegment(sketch, "E677", {"start": v(-30.84, -42.9) * mm, "end": v(-34.46, -42.9) * mm});
            skLineSegment(sketch, "E678", {"start": v(-34.46, -42.9) * mm, "end": v(-36.5, -42.42) * mm});
            skLineSegment(sketch, "E679", {"start": v(-36.5, -42.42) * mm, "end": v(-38.12, -41.77) * mm});
            skLineSegment(sketch, "E680", {"start": v(-38.12, -41.77) * mm, "end": v(-38.5, -41.96) * mm});
            skLineSegment(sketch, "E681", {"start": v(-38.5, -41.96) * mm, "end": v(-38.63, -42.04) * mm});
            skLineSegment(sketch, "E682", {"start": v(-38.63, -42.04) * mm, "end": v(-38.75, -42.11) * mm});
            skLineSegment(sketch, "E683", {"start": v(-38.75, -42.11) * mm, "end": v(-38.83, -42.18) * mm});
            skLineSegment(sketch, "E684", {"start": v(-38.83, -42.18) * mm, "end": v(-38.85, -42.2) * mm});
            skLineSegment(sketch, "E685", {"start": v(-38.85, -42.2) * mm, "end": v(-38.86, -42.23) * mm});
            skLineSegment(sketch, "E686", {"start": v(-38.86, -42.23) * mm, "end": v(-38.86, -42.3) * mm});
            skLineSegment(sketch, "E687", {"start": v(-38.86, -42.3) * mm, "end": v(-38.02, -42.71) * mm});
            skLineSegment(sketch, "E688", {"start": v(-38.02, -42.71) * mm, "end": v(-37.67, -42.88) * mm});
            skLineSegment(sketch, "E689", {"start": v(-37.67, -42.88) * mm, "end": v(-37.33, -43.02) * mm});
            skLineSegment(sketch, "E690", {"start": v(-37.33, -43.02) * mm, "end": v(-36.99, -43.16) * mm});
            skLineSegment(sketch, "E691", {"start": v(-36.99, -43.16) * mm, "end": v(-36.64, -43.28) * mm});
            skLineSegment(sketch, "E692", {"start": v(-36.64, -43.28) * mm, "end": v(-36.3, -43.38) * mm});
            skLineSegment(sketch, "E693", {"start": v(-36.3, -43.38) * mm, "end": v(-35.94, -43.48) * mm});
            skLineSegment(sketch, "E694", {"start": v(-35.94, -43.48) * mm, "end": v(-35.58, -43.56) * mm});
            skLineSegment(sketch, "E695", {"start": v(-35.58, -43.56) * mm, "end": v(-35.2, -43.64) * mm});
            skLineSegment(sketch, "E696", {"start": v(-35.2, -43.64) * mm, "end": v(-34.55, -43.76) * mm});
            skLineSegment(sketch, "E697", {"start": v(-34.55, -43.76) * mm, "end": v(-33.19, -43.76) * mm});
            skLineSegment(sketch, "E698", {"start": v(-22.59, -43.68) * mm, "end": v(-22.56, -43.67) * mm});
            skLineSegment(sketch, "E699", {"start": v(-22.56, -43.67) * mm, "end": v(-22.54, -43.64) * mm});
            skLineSegment(sketch, "E700", {"start": v(-22.54, -43.64) * mm, "end": v(-22.56, -43.6) * mm});
            skLineSegment(sketch, "E701", {"start": v(-22.56, -43.6) * mm, "end": v(-22.59, -43.6) * mm});
            skLineSegment(sketch, "E702", {"start": v(-22.59, -43.6) * mm, "end": v(-22.62, -43.6) * mm});
            skLineSegment(sketch, "E703", {"start": v(-22.62, -43.6) * mm, "end": v(-22.63, -43.64) * mm});
            skLineSegment(sketch, "E704", {"start": v(-22.63, -43.64) * mm, "end": v(-22.62, -43.67) * mm});
            skLineSegment(sketch, "E705", {"start": v(-22.62, -43.67) * mm, "end": v(-22.59, -43.68) * mm});
            skLineSegment(sketch, "E706", {"start": v(-32.42, -42) * mm, "end": v(-30.93, -41.97) * mm});
            skLineSegment(sketch, "E707", {"start": v(-30.93, -41.97) * mm, "end": v(-30.16, -41.84) * mm});
            skLineSegment(sketch, "E708", {"start": v(-30.16, -41.84) * mm, "end": v(-29.36, -41.69) * mm});
            skLineSegment(sketch, "E709", {"start": v(-29.36, -41.69) * mm, "end": v(-28.6, -41.53) * mm});
            skLineSegment(sketch, "E710", {"start": v(-28.6, -41.53) * mm, "end": v(-27.86, -41.35) * mm});
            skLineSegment(sketch, "E711", {"start": v(-27.86, -41.35) * mm, "end": v(-27.13, -41.15) * mm});
            skLineSegment(sketch, "E712", {"start": v(-27.13, -41.15) * mm, "end": v(-26.39, -40.92) * mm});
            skLineSegment(sketch, "E713", {"start": v(-26.39, -40.92) * mm, "end": v(-25.62, -40.67) * mm});
            skLineSegment(sketch, "E714", {"start": v(-25.62, -40.67) * mm, "end": v(-24.8, -40.37) * mm});
            skLineSegment(sketch, "E715", {"start": v(-24.8, -40.37) * mm, "end": v(-23.93, -40.04) * mm});
            skLineSegment(sketch, "E716", {"start": v(-23.93, -40.04) * mm, "end": v(-22.74, -39.57) * mm});
            skLineSegment(sketch, "E717", {"start": v(-22.74, -39.57) * mm, "end": v(-22.24, -38.5) * mm});
            skLineSegment(sketch, "E718", {"start": v(-22.24, -38.5) * mm, "end": v(-21.21, -37.2) * mm});
            skLineSegment(sketch, "E719", {"start": v(-21.21, -37.2) * mm, "end": v(-20.63, -36.74) * mm});
            skLineSegment(sketch, "E720", {"start": v(-20.63, -36.74) * mm, "end": v(-20.09, -36.33) * mm});
            skLineSegment(sketch, "E721", {"start": v(-20.09, -36.33) * mm, "end": v(-19.85, -36.16) * mm});
            skLineSegment(sketch, "E722", {"start": v(-19.85, -36.16) * mm, "end": v(-19.62, -36.01) * mm});
            skLineSegment(sketch, "E723", {"start": v(-19.62, -36.01) * mm, "end": v(-19.4, -35.87) * mm});
            skLineSegment(sketch, "E724", {"start": v(-19.4, -35.87) * mm, "end": v(-19.15, -35.74) * mm});
            skLineSegment(sketch, "E725", {"start": v(-19.15, -35.74) * mm, "end": v(-18.6, -35.46) * mm});
            skLineSegment(sketch, "E726", {"start": v(-18.6, -35.46) * mm, "end": v(-17.88, -35.1) * mm});
            skLineSegment(sketch, "E727", {"start": v(-17.88, -35.1) * mm, "end": v(-17.92, -34.9) * mm});
            skLineSegment(sketch, "E728", {"start": v(-17.92, -34.9) * mm, "end": v(-21.12, -29.77) * mm});
            skLineSegment(sketch, "E729", {"start": v(-21.12, -29.77) * mm, "end": v(-21.26, -29.61) * mm});
            skLineSegment(sketch, "E730", {"start": v(-21.26, -29.61) * mm, "end": v(-21.97, -30.02) * mm});
            skLineSegment(sketch, "E731", {"start": v(-21.97, -30.02) * mm, "end": v(-22.35, -30.23) * mm});
            skLineSegment(sketch, "E732", {"start": v(-22.35, -30.23) * mm, "end": v(-22.87, -30.5) * mm});
            skLineSegment(sketch, "E733", {"start": v(-22.87, -30.5) * mm, "end": v(-24.04, -31.1) * mm});
            skLineSegment(sketch, "E734", {"start": v(-24.04, -31.1) * mm, "end": v(-25.4, -31.79) * mm});
            skLineSegment(sketch, "E735", {"start": v(-25.4, -31.79) * mm, "end": v(-26.26, -32.15) * mm});
            skLineSegment(sketch, "E736", {"start": v(-26.26, -32.15) * mm, "end": v(-26.68, -32.32) * mm});
            skLineSegment(sketch, "E737", {"start": v(-26.68, -32.32) * mm, "end": v(-27.18, -32.52) * mm});
            skLineSegment(sketch, "E738", {"start": v(-27.18, -32.52) * mm, "end": v(-27.7, -32.71) * mm});
            skLineSegment(sketch, "E739", {"start": v(-27.7, -32.71) * mm, "end": v(-28.18, -32.88) * mm});
            skLineSegment(sketch, "E740", {"start": v(-28.18, -32.88) * mm, "end": v(-29.23, -33.25) * mm});
            skLineSegment(sketch, "E741", {"start": v(-29.23, -33.25) * mm, "end": v(-30.26, -33.47) * mm});
            skLineSegment(sketch, "E742", {"start": v(-30.26, -33.47) * mm, "end": v(-30.73, -33.57) * mm});
            skLineSegment(sketch, "E743", {"start": v(-30.73, -33.57) * mm, "end": v(-31.27, -33.67) * mm});
            skLineSegment(sketch, "E744", {"start": v(-31.27, -33.67) * mm, "end": v(-31.79, -33.75) * mm});
            skLineSegment(sketch, "E745", {"start": v(-31.79, -33.75) * mm, "end": v(-32.24, -33.81) * mm});
            skLineSegment(sketch, "E746", {"start": v(-32.24, -33.81) * mm, "end": v(-33.2, -33.92) * mm});
            skLineSegment(sketch, "E747", {"start": v(-33.2, -33.92) * mm, "end": v(-35.28, -33.82) * mm});
            skLineSegment(sketch, "E748", {"start": v(-35.28, -33.82) * mm, "end": v(-36.9, -33.44) * mm});
            skLineSegment(sketch, "E749", {"start": v(-36.9, -33.44) * mm, "end": v(-37.04, -33.49) * mm});
            skLineSegment(sketch, "E750", {"start": v(-37.04, -33.49) * mm, "end": v(-36.81, -33.98) * mm});
            skLineSegment(sketch, "E751", {"start": v(-36.81, -33.98) * mm, "end": v(-36.7, -34.21) * mm});
            skLineSegment(sketch, "E752", {"start": v(-36.7, -34.21) * mm, "end": v(-36.53, -34.49) * mm});
            skLineSegment(sketch, "E753", {"start": v(-36.53, -34.49) * mm, "end": v(-36.36, -34.77) * mm});
            skLineSegment(sketch, "E754", {"start": v(-36.36, -34.77) * mm, "end": v(-36.18, -35.03) * mm});
            skLineSegment(sketch, "E755", {"start": v(-36.18, -35.03) * mm, "end": v(-35.78, -35.6) * mm});
            skLineSegment(sketch, "E756", {"start": v(-35.78, -35.6) * mm, "end": v(-34.58, -36.68) * mm});
            skLineSegment(sketch, "E757", {"start": v(-34.58, -36.68) * mm, "end": v(-33.1, -37.55) * mm});
            skLineSegment(sketch, "E758", {"start": v(-33.1, -37.55) * mm, "end": v(-33.07, -37.57) * mm});
            skLineSegment(sketch, "E759", {"start": v(-33.07, -37.57) * mm, "end": v(-33.08, -37.61) * mm});
            skLineSegment(sketch, "E760", {"start": v(-33.08, -37.61) * mm, "end": v(-33.13, -37.7) * mm});
            skLineSegment(sketch, "E761", {"start": v(-33.13, -37.7) * mm, "end": v(-33.31, -38) * mm});
            skLineSegment(sketch, "E762", {"start": v(-33.31, -38) * mm, "end": v(-33.6, -38.4) * mm});
            skLineSegment(sketch, "E763", {"start": v(-33.6, -38.4) * mm, "end": v(-34.4, -39.16) * mm});
            skLineSegment(sketch, "E764", {"start": v(-34.4, -39.16) * mm, "end": v(-34.78, -39.5) * mm});
            skLineSegment(sketch, "E765", {"start": v(-34.78, -39.5) * mm, "end": v(-35.22, -39.88) * mm});
            skLineSegment(sketch, "E766", {"start": v(-35.22, -39.88) * mm, "end": v(-35.68, -40.25) * mm});
            skLineSegment(sketch, "E767", {"start": v(-35.68, -40.25) * mm, "end": v(-36.08, -40.55) * mm});
            skLineSegment(sketch, "E768", {"start": v(-36.08, -40.55) * mm, "end": v(-36.95, -41.19) * mm});
            skLineSegment(sketch, "E769", {"start": v(-36.95, -41.19) * mm, "end": v(-36.9, -41.37) * mm});
            skLineSegment(sketch, "E770", {"start": v(-36.9, -41.37) * mm, "end": v(-36.22, -41.57) * mm});
            skLineSegment(sketch, "E771", {"start": v(-36.22, -41.57) * mm, "end": v(-35.9, -41.66) * mm});
            skLineSegment(sketch, "E772", {"start": v(-35.9, -41.66) * mm, "end": v(-35.5, -41.76) * mm});
            skLineSegment(sketch, "E773", {"start": v(-35.5, -41.76) * mm, "end": v(-35.1, -41.84) * mm});
            skLineSegment(sketch, "E774", {"start": v(-35.1, -41.84) * mm, "end": v(-34.73, -41.91) * mm});
            skLineSegment(sketch, "E775", {"start": v(-34.73, -41.91) * mm, "end": v(-33.92, -42.04) * mm});
            skLineSegment(sketch, "E776", {"start": v(-33.92, -42.04) * mm, "end": v(-32.42, -42) * mm});
            skLineSegment(sketch, "E777", {"start": v(33.1, -42) * mm, "end": v(34.6, -41.97) * mm});
            skLineSegment(sketch, "E778", {"start": v(34.6, -41.97) * mm, "end": v(35.37, -41.8) * mm});
            skLineSegment(sketch, "E779", {"start": v(35.37, -41.8) * mm, "end": v(35.7, -41.7) * mm});
            skLineSegment(sketch, "E780", {"start": v(35.7, -41.7) * mm, "end": v(36.04, -41.61) * mm});
            skLineSegment(sketch, "E781", {"start": v(36.04, -41.61) * mm, "end": v(36.35, -41.52) * mm});
            skLineSegment(sketch, "E782", {"start": v(36.35, -41.52) * mm, "end": v(36.58, -41.44) * mm});
            skLineSegment(sketch, "E783", {"start": v(36.58, -41.44) * mm, "end": v(37.02, -41.27) * mm});
            skLineSegment(sketch, "E784", {"start": v(37.02, -41.27) * mm, "end": v(36.07, -40.57) * mm});
            skLineSegment(sketch, "E785", {"start": v(36.07, -40.57) * mm, "end": v(35.65, -40.26) * mm});
            skLineSegment(sketch, "E786", {"start": v(35.65, -40.26) * mm, "end": v(35.25, -39.94) * mm});
            skLineSegment(sketch, "E787", {"start": v(35.25, -39.94) * mm, "end": v(34.86, -39.62) * mm});
            skLineSegment(sketch, "E788", {"start": v(34.86, -39.62) * mm, "end": v(34.5, -39.3) * mm});
            skLineSegment(sketch, "E789", {"start": v(34.5, -39.3) * mm, "end": v(34.17, -38.98) * mm});
            skLineSegment(sketch, "E790", {"start": v(34.17, -38.98) * mm, "end": v(33.86, -38.67) * mm});
            skLineSegment(sketch, "E791", {"start": v(33.86, -38.67) * mm, "end": v(33.6, -38.38) * mm});
            skLineSegment(sketch, "E792", {"start": v(33.6, -38.38) * mm, "end": v(33.36, -38.1) * mm});
            skLineSegment(sketch, "E793", {"start": v(33.36, -38.1) * mm, "end": v(32.96, -37.58) * mm});
            skLineSegment(sketch, "E794", {"start": v(32.96, -37.58) * mm, "end": v(33.06, -37.55) * mm});
            skLineSegment(sketch, "E795", {"start": v(33.06, -37.55) * mm, "end": v(33.35, -37.39) * mm});
            skLineSegment(sketch, "E796", {"start": v(33.35, -37.39) * mm, "end": v(33.9, -37.06) * mm});
            skLineSegment(sketch, "E797", {"start": v(33.9, -37.06) * mm, "end": v(34.64, -36.6) * mm});
            skLineSegment(sketch, "E798", {"start": v(34.64, -36.6) * mm, "end": v(35.2, -36.09) * mm});
            skLineSegment(sketch, "E799", {"start": v(35.2, -36.09) * mm, "end": v(35.44, -35.85) * mm});
            skLineSegment(sketch, "E800", {"start": v(35.44, -35.85) * mm, "end": v(35.7, -35.59) * mm});
            skLineSegment(sketch, "E801", {"start": v(35.7, -35.59) * mm, "end": v(35.92, -35.33) * mm});
            skLineSegment(sketch, "E802", {"start": v(35.92, -35.33) * mm, "end": v(36.1, -35.11) * mm});
            skLineSegment(sketch, "E803", {"start": v(36.1, -35.11) * mm, "end": v(36.24, -34.9) * mm});
            skLineSegment(sketch, "E804", {"start": v(36.24, -34.9) * mm, "end": v(36.4, -34.65) * mm});
            skLineSegment(sketch, "E805", {"start": v(36.4, -34.65) * mm, "end": v(36.55, -34.39) * mm});
            skLineSegment(sketch, "E806", {"start": v(36.55, -34.39) * mm, "end": v(36.7, -34.13) * mm});
            skLineSegment(sketch, "E807", {"start": v(36.7, -34.13) * mm, "end": v(36.82, -33.88) * mm});
            skLineSegment(sketch, "E808", {"start": v(36.82, -33.88) * mm, "end": v(36.91, -33.68) * mm});
            skLineSegment(sketch, "E809", {"start": v(36.91, -33.68) * mm, "end": v(36.96, -33.54) * mm});
            skLineSegment(sketch, "E810", {"start": v(36.96, -33.54) * mm, "end": v(36.97, -33.5) * mm});
            skLineSegment(sketch, "E811", {"start": v(36.97, -33.5) * mm, "end": v(36.96, -33.47) * mm});
            skLineSegment(sketch, "E812", {"start": v(36.96, -33.47) * mm, "end": v(36.94, -33.46) * mm});
            skLineSegment(sketch, "E813", {"start": v(36.94, -33.46) * mm, "end": v(36.9, -33.46) * mm});
            skLineSegment(sketch, "E814", {"start": v(36.9, -33.46) * mm, "end": v(36.76, -33.48) * mm});
            skLineSegment(sketch, "E815", {"start": v(36.76, -33.48) * mm, "end": v(36.57, -33.51) * mm});
            skLineSegment(sketch, "E816", {"start": v(36.57, -33.51) * mm, "end": v(36.35, -33.57) * mm});
            skLineSegment(sketch, "E817", {"start": v(36.35, -33.57) * mm, "end": v(35.76, -33.7) * mm});
            skLineSegment(sketch, "E818", {"start": v(35.76, -33.7) * mm, "end": v(35.14, -33.8) * mm});
            skLineSegment(sketch, "E819", {"start": v(35.14, -33.8) * mm, "end": v(34.5, -33.9) * mm});
            skLineSegment(sketch, "E820", {"start": v(34.5, -33.9) * mm, "end": v(32.78, -33.9) * mm});
            skLineSegment(sketch, "E821", {"start": v(32.78, -33.9) * mm, "end": v(31.82, -33.76) * mm});
            skLineSegment(sketch, "E822", {"start": v(31.82, -33.76) * mm, "end": v(31.29, -33.68) * mm});
            skLineSegment(sketch, "E823", {"start": v(31.29, -33.68) * mm, "end": v(30.74, -33.58) * mm});
            skLineSegment(sketch, "E824", {"start": v(30.74, -33.58) * mm, "end": v(30.2, -33.46) * mm});
            skLineSegment(sketch, "E825", {"start": v(30.2, -33.46) * mm, "end": v(29.63, -33.32) * mm});
            skLineSegment(sketch, "E826", {"start": v(29.63, -33.32) * mm, "end": v(29.05, -33.16) * mm});
            skLineSegment(sketch, "E827", {"start": v(29.05, -33.16) * mm, "end": v(28.47, -32.98) * mm});
            skLineSegment(sketch, "E828", {"start": v(28.47, -32.98) * mm, "end": v(27.88, -32.78) * mm});
            skLineSegment(sketch, "E829", {"start": v(27.88, -32.78) * mm, "end": v(27.27, -32.56) * mm});
            skLineSegment(sketch, "E830", {"start": v(27.27, -32.56) * mm, "end": v(26.66, -32.33) * mm});
            skLineSegment(sketch, "E831", {"start": v(26.66, -32.33) * mm, "end": v(26.04, -32.07) * mm});
            skLineSegment(sketch, "E832", {"start": v(26.04, -32.07) * mm, "end": v(25.4, -31.8) * mm});
            skLineSegment(sketch, "E833", {"start": v(25.4, -31.8) * mm, "end": v(24.76, -31.5) * mm});
            skLineSegment(sketch, "E834", {"start": v(24.76, -31.5) * mm, "end": v(24.11, -31.18) * mm});
            skLineSegment(sketch, "E835", {"start": v(24.11, -31.18) * mm, "end": v(23.45, -30.84) * mm});
            skLineSegment(sketch, "E836", {"start": v(23.45, -30.84) * mm, "end": v(22.79, -30.49) * mm});
            skLineSegment(sketch, "E837", {"start": v(22.79, -30.49) * mm, "end": v(22.1, -30.11) * mm});
            skLineSegment(sketch, "E838", {"start": v(22.1, -30.11) * mm, "end": v(21.22, -29.61) * mm});
            skLineSegment(sketch, "E839", {"start": v(21.22, -29.61) * mm, "end": v(21.16, -29.68) * mm});
            skLineSegment(sketch, "E840", {"start": v(21.16, -29.68) * mm, "end": v(18.1, -34.57) * mm});
            skLineSegment(sketch, "E841", {"start": v(18.1, -34.57) * mm, "end": v(17.77, -35.06) * mm});
            skLineSegment(sketch, "E842", {"start": v(17.77, -35.06) * mm, "end": v(18.62, -35.49) * mm});
            skLineSegment(sketch, "E843", {"start": v(18.62, -35.49) * mm, "end": v(19, -35.68) * mm});
            skLineSegment(sketch, "E844", {"start": v(19, -35.68) * mm, "end": v(19.34, -35.87) * mm});
            skLineSegment(sketch, "E845", {"start": v(19.34, -35.87) * mm, "end": v(19.66, -36.06) * mm});
            skLineSegment(sketch, "E846", {"start": v(19.66, -36.06) * mm, "end": v(19.96, -36.25) * mm});
            skLineSegment(sketch, "E847", {"start": v(19.96, -36.25) * mm, "end": v(20.24, -36.45) * mm});
            skLineSegment(sketch, "E848", {"start": v(20.24, -36.45) * mm, "end": v(20.51, -36.66) * mm});
            skLineSegment(sketch, "E849", {"start": v(20.51, -36.66) * mm, "end": v(20.78, -36.88) * mm});
            skLineSegment(sketch, "E850", {"start": v(20.78, -36.88) * mm, "end": v(21.04, -37.12) * mm});
            skLineSegment(sketch, "E851", {"start": v(21.04, -37.12) * mm, "end": v(21.6, -37.63) * mm});
            skLineSegment(sketch, "E852", {"start": v(21.6, -37.63) * mm, "end": v(22.04, -38.3) * mm});
            skLineSegment(sketch, "E853", {"start": v(22.04, -38.3) * mm, "end": v(22.22, -38.57) * mm});
            skLineSegment(sketch, "E854", {"start": v(22.22, -38.57) * mm, "end": v(22.38, -38.85) * mm});
            skLineSegment(sketch, "E855", {"start": v(22.38, -38.85) * mm, "end": v(22.5, -39.1) * mm});
            skLineSegment(sketch, "E856", {"start": v(22.5, -39.1) * mm, "end": v(22.58, -39.26) * mm});
            skLineSegment(sketch, "E857", {"start": v(22.58, -39.26) * mm, "end": v(22.68, -39.57) * mm});
            skLineSegment(sketch, "E858", {"start": v(22.68, -39.57) * mm, "end": v(23.92, -40.05) * mm});
            skLineSegment(sketch, "E859", {"start": v(23.92, -40.05) * mm, "end": v(24.5, -40.28) * mm});
            skLineSegment(sketch, "E860", {"start": v(24.5, -40.28) * mm, "end": v(25.06, -40.48) * mm});
            skLineSegment(sketch, "E861", {"start": v(25.06, -40.48) * mm, "end": v(25.6, -40.67) * mm});
            skLineSegment(sketch, "E862", {"start": v(25.6, -40.67) * mm, "end": v(26.13, -40.85) * mm});
            skLineSegment(sketch, "E863", {"start": v(26.13, -40.85) * mm, "end": v(26.67, -41) * mm});
            skLineSegment(sketch, "E864", {"start": v(26.67, -41) * mm, "end": v(27.2, -41.16) * mm});
            skLineSegment(sketch, "E865", {"start": v(27.2, -41.16) * mm, "end": v(27.76, -41.31) * mm});
            skLineSegment(sketch, "E866", {"start": v(27.76, -41.31) * mm, "end": v(28.34, -41.46) * mm});
            skLineSegment(sketch, "E867", {"start": v(28.34, -41.46) * mm, "end": v(29.61, -41.76) * mm});
            skLineSegment(sketch, "E868", {"start": v(29.61, -41.76) * mm, "end": v(30.38, -41.86) * mm});
            skLineSegment(sketch, "E869", {"start": v(30.38, -41.86) * mm, "end": v(31.38, -42) * mm});
            skLineSegment(sketch, "E870", {"start": v(31.38, -42) * mm, "end": v(31.6, -42.04) * mm});
            skLineSegment(sketch, "E871", {"start": v(31.6, -42.04) * mm, "end": v(33.1, -42) * mm});
            skLineSegment(sketch, "E872", {"start": v(-19.46, -41.95) * mm, "end": v(-18.78, -41.96) * mm});
            skLineSegment(sketch, "E873", {"start": v(-18.78, -41.96) * mm, "end": v(-17.92, -41.83) * mm});
            skLineSegment(sketch, "E874", {"start": v(-17.92, -41.83) * mm, "end": v(-17.45, -41.75) * mm});
            skLineSegment(sketch, "E875", {"start": v(-17.45, -41.75) * mm, "end": v(-16.82, -41.63) * mm});
            skLineSegment(sketch, "E876", {"start": v(-16.82, -41.63) * mm, "end": v(-16.1, -41.48) * mm});
            skLineSegment(sketch, "E877", {"start": v(-16.1, -41.48) * mm, "end": v(-15.38, -41.32) * mm});
            skLineSegment(sketch, "E878", {"start": v(-15.38, -41.32) * mm, "end": v(-13.7, -40.94) * mm});
            skLineSegment(sketch, "E879", {"start": v(-13.7, -40.94) * mm, "end": v(-13.58, -40.86) * mm});
            skLineSegment(sketch, "E880", {"start": v(-13.58, -40.86) * mm, "end": v(-14.55, -39.6) * mm});
            skLineSegment(sketch, "E881", {"start": v(-14.55, -39.6) * mm, "end": v(-16.34, -37.3) * mm});
            skLineSegment(sketch, "E882", {"start": v(-16.34, -37.3) * mm, "end": v(-17.22, -36.13) * mm});
            skLineSegment(sketch, "E883", {"start": v(-17.22, -36.13) * mm, "end": v(-17.28, -36.02) * mm});
            skLineSegment(sketch, "E884", {"start": v(-17.28, -36.02) * mm, "end": v(-18.16, -36.48) * mm});
            skLineSegment(sketch, "E885", {"start": v(-18.16, -36.48) * mm, "end": v(-18.57, -36.7) * mm});
            skLineSegment(sketch, "E886", {"start": v(-18.57, -36.7) * mm, "end": v(-19.03, -36.95) * mm});
            skLineSegment(sketch, "E887", {"start": v(-19.03, -36.95) * mm, "end": v(-19.48, -37.22) * mm});
            skLineSegment(sketch, "E888", {"start": v(-19.48, -37.22) * mm, "end": v(-19.86, -37.47) * mm});
            skLineSegment(sketch, "E889", {"start": v(-19.86, -37.47) * mm, "end": v(-20.69, -38) * mm});
            skLineSegment(sketch, "E890", {"start": v(-20.69, -38) * mm, "end": v(-21.73, -39.05) * mm});
            skLineSegment(sketch, "E891", {"start": v(-21.73, -39.05) * mm, "end": v(-22.1, -39.92) * mm});
            skLineSegment(sketch, "E892", {"start": v(-22.1, -39.92) * mm, "end": v(-22.02, -40.7) * mm});
            skLineSegment(sketch, "E893", {"start": v(-22.02, -40.7) * mm, "end": v(-21.54, -41.38) * mm});
            skLineSegment(sketch, "E894", {"start": v(-21.54, -41.38) * mm, "end": v(-21.2, -41.58) * mm});
            skLineSegment(sketch, "E895", {"start": v(-21.2, -41.58) * mm, "end": v(-21.02, -41.67) * mm});
            skLineSegment(sketch, "E896", {"start": v(-21.02, -41.67) * mm, "end": v(-20.84, -41.75) * mm});
            skLineSegment(sketch, "E897", {"start": v(-20.84, -41.75) * mm, "end": v(-20.66, -41.8) * mm});
            skLineSegment(sketch, "E898", {"start": v(-20.66, -41.8) * mm, "end": v(-20.46, -41.86) * mm});
            skLineSegment(sketch, "E899", {"start": v(-20.46, -41.86) * mm, "end": v(-20.24, -41.9) * mm});
            skLineSegment(sketch, "E900", {"start": v(-20.24, -41.9) * mm, "end": v(-20, -41.92) * mm});
            skLineSegment(sketch, "E901", {"start": v(-20, -41.92) * mm, "end": v(-19.75, -41.94) * mm});
            skLineSegment(sketch, "E902", {"start": v(-19.75, -41.94) * mm, "end": v(-19.46, -41.95) * mm});
            skLineSegment(sketch, "E903", {"start": v(19.29, -41.95) * mm, "end": v(20.1, -41.96) * mm});
            skLineSegment(sketch, "E904", {"start": v(20.1, -41.96) * mm, "end": v(20.56, -41.82) * mm});
            skLineSegment(sketch, "E905", {"start": v(20.56, -41.82) * mm, "end": v(20.76, -41.76) * mm});
            skLineSegment(sketch, "E906", {"start": v(20.76, -41.76) * mm, "end": v(20.98, -41.67) * mm});
            skLineSegment(sketch, "E907", {"start": v(20.98, -41.67) * mm, "end": v(21.17, -41.57) * mm});
            skLineSegment(sketch, "E908", {"start": v(21.17, -41.57) * mm, "end": v(21.33, -41.48) * mm});
            skLineSegment(sketch, "E909", {"start": v(21.33, -41.48) * mm, "end": v(21.64, -41.28) * mm});
            skLineSegment(sketch, "E910", {"start": v(21.64, -41.28) * mm, "end": v(22.04, -40.47) * mm});
            skLineSegment(sketch, "E911", {"start": v(22.04, -40.47) * mm, "end": v(22.04, -39.82) * mm});
            skLineSegment(sketch, "E912", {"start": v(22.04, -39.82) * mm, "end": v(21.58, -38.89) * mm});
            skLineSegment(sketch, "E913", {"start": v(21.58, -38.89) * mm, "end": v(21.05, -38.4) * mm});
            skLineSegment(sketch, "E914", {"start": v(21.05, -38.4) * mm, "end": v(20.8, -38.18) * mm});
            skLineSegment(sketch, "E915", {"start": v(20.8, -38.18) * mm, "end": v(20.52, -37.95) * mm});
            skLineSegment(sketch, "E916", {"start": v(20.52, -37.95) * mm, "end": v(20.22, -37.73) * mm});
            skLineSegment(sketch, "E917", {"start": v(20.22, -37.73) * mm, "end": v(19.9, -37.5) * mm});
            skLineSegment(sketch, "E918", {"start": v(19.9, -37.5) * mm, "end": v(19.54, -37.27) * mm});
            skLineSegment(sketch, "E919", {"start": v(19.54, -37.27) * mm, "end": v(19.15, -37.04) * mm});
            skLineSegment(sketch, "E920", {"start": v(19.15, -37.04) * mm, "end": v(18.74, -36.8) * mm});
            skLineSegment(sketch, "E921", {"start": v(18.74, -36.8) * mm, "end": v(18.3, -36.56) * mm});
            skLineSegment(sketch, "E922", {"start": v(18.3, -36.56) * mm, "end": v(17.36, -36.07) * mm});
            skLineSegment(sketch, "E923", {"start": v(17.36, -36.07) * mm, "end": v(17.25, -36.07) * mm});
            skLineSegment(sketch, "E924", {"start": v(17.25, -36.07) * mm, "end": v(13.62, -40.77) * mm});
            skLineSegment(sketch, "E925", {"start": v(13.62, -40.77) * mm, "end": v(13.62, -40.92) * mm});
            skLineSegment(sketch, "E926", {"start": v(13.62, -40.92) * mm, "end": v(17.01, -41.7) * mm});
            skLineSegment(sketch, "E927", {"start": v(17.01, -41.7) * mm, "end": v(18.46, -41.94) * mm});
            skLineSegment(sketch, "E928", {"start": v(18.46, -41.94) * mm, "end": v(19.29, -41.95) * mm});
            skLineSegment(sketch, "E929", {"start": v(-34.27, -32.89) * mm, "end": v(-33.96, -32.89) * mm});
            skLineSegment(sketch, "E930", {"start": v(-33.96, -32.89) * mm, "end": v(-33.66, -32.88) * mm});
            skLineSegment(sketch, "E931", {"start": v(-33.66, -32.88) * mm, "end": v(-33.02, -32.84) * mm});
            skLineSegment(sketch, "E932", {"start": v(-33.02, -32.84) * mm, "end": v(-32.36, -32.77) * mm});
            skLineSegment(sketch, "E933", {"start": v(-32.36, -32.77) * mm, "end": v(-31.69, -32.67) * mm});
            skLineSegment(sketch, "E934", {"start": v(-31.69, -32.67) * mm, "end": v(-30.99, -32.54) * mm});
            skLineSegment(sketch, "E935", {"start": v(-30.99, -32.54) * mm, "end": v(-30.28, -32.39) * mm});
            skLineSegment(sketch, "E936", {"start": v(-30.28, -32.39) * mm, "end": v(-29.56, -32.2) * mm});
            skLineSegment(sketch, "E937", {"start": v(-29.56, -32.2) * mm, "end": v(-28.82, -32) * mm});
            skLineSegment(sketch, "E938", {"start": v(-28.82, -32) * mm, "end": v(-28.08, -31.76) * mm});
            skLineSegment(sketch, "E939", {"start": v(-28.08, -31.76) * mm, "end": v(-27.33, -31.5) * mm});
            skLineSegment(sketch, "E940", {"start": v(-27.33, -31.5) * mm, "end": v(-26.59, -31.2) * mm});
            skLineSegment(sketch, "E941", {"start": v(-26.59, -31.2) * mm, "end": v(-25.84, -30.9) * mm});
            skLineSegment(sketch, "E942", {"start": v(-25.84, -30.9) * mm, "end": v(-25.1, -30.57) * mm});
            skLineSegment(sketch, "E943", {"start": v(-25.1, -30.57) * mm, "end": v(-24.36, -30.22) * mm});
            skLineSegment(sketch, "E944", {"start": v(-24.36, -30.22) * mm, "end": v(-23.63, -29.84) * mm});
            skLineSegment(sketch, "E945", {"start": v(-23.63, -29.84) * mm, "end": v(-22.9, -29.45) * mm});
            skLineSegment(sketch, "E946", {"start": v(-22.9, -29.45) * mm, "end": v(-21.83, -28.83) * mm});
            skLineSegment(sketch, "E947", {"start": v(-21.83, -28.83) * mm, "end": v(-21.71, -28.75) * mm});
            skLineSegment(sketch, "E948", {"start": v(-21.71, -28.75) * mm, "end": v(-22.1, -28) * mm});
            skLineSegment(sketch, "E949", {"start": v(-22.1, -28) * mm, "end": v(-22.25, -28.07) * mm});
            skLineSegment(sketch, "E950", {"start": v(-22.25, -28.07) * mm, "end": v(-22.57, -28.23) * mm});
            skLineSegment(sketch, "E951", {"start": v(-22.57, -28.23) * mm, "end": v(-23.1, -28.52) * mm});
            skLineSegment(sketch, "E952", {"start": v(-23.1, -28.52) * mm, "end": v(-23.81, -28.9) * mm});
            skLineSegment(sketch, "E953", {"start": v(-23.81, -28.9) * mm, "end": v(-24.5, -29.26) * mm});
            skLineSegment(sketch, "E954", {"start": v(-24.5, -29.26) * mm, "end": v(-25.19, -29.6) * mm});
            skLineSegment(sketch, "E955", {"start": v(-25.19, -29.6) * mm, "end": v(-25.86, -29.92) * mm});
            skLineSegment(sketch, "E956", {"start": v(-25.86, -29.92) * mm, "end": v(-26.52, -30.22) * mm});
            skLineSegment(sketch, "E957", {"start": v(-26.52, -30.22) * mm, "end": v(-27.17, -30.5) * mm});
            skLineSegment(sketch, "E958", {"start": v(-27.17, -30.5) * mm, "end": v(-27.8, -30.75) * mm});
            skLineSegment(sketch, "E959", {"start": v(-27.8, -30.75) * mm, "end": v(-28.43, -30.98) * mm});
            skLineSegment(sketch, "E960", {"start": v(-28.43, -30.98) * mm, "end": v(-29.05, -31.2) * mm});
            skLineSegment(sketch, "E961", {"start": v(-29.05, -31.2) * mm, "end": v(-29.65, -31.39) * mm});
            skLineSegment(sketch, "E962", {"start": v(-29.65, -31.39) * mm, "end": v(-30.24, -31.56) * mm});
            skLineSegment(sketch, "E963", {"start": v(-30.24, -31.56) * mm, "end": v(-30.81, -31.7) * mm});
            skLineSegment(sketch, "E964", {"start": v(-30.81, -31.7) * mm, "end": v(-31.38, -31.83) * mm});
            skLineSegment(sketch, "E965", {"start": v(-31.38, -31.83) * mm, "end": v(-31.93, -31.93) * mm});
            skLineSegment(sketch, "E966", {"start": v(-31.93, -31.93) * mm, "end": v(-32.46, -32.02) * mm});
            skLineSegment(sketch, "E967", {"start": v(-32.46, -32.02) * mm, "end": v(-32.98, -32.07) * mm});
            skLineSegment(sketch, "E968", {"start": v(-32.98, -32.07) * mm, "end": v(-33.86, -32.16) * mm});
            skLineSegment(sketch, "E969", {"start": v(-33.86, -32.16) * mm, "end": v(-35.75, -32) * mm});
            skLineSegment(sketch, "E970", {"start": v(-35.75, -32) * mm, "end": v(-36.54, -31.76) * mm});
            skLineSegment(sketch, "E971", {"start": v(-36.54, -31.76) * mm, "end": v(-36.88, -31.66) * mm});
            skLineSegment(sketch, "E972", {"start": v(-36.88, -31.66) * mm, "end": v(-37.22, -31.54) * mm});
            skLineSegment(sketch, "E973", {"start": v(-37.22, -31.54) * mm, "end": v(-37.54, -31.42) * mm});
            skLineSegment(sketch, "E974", {"start": v(-37.54, -31.42) * mm, "end": v(-37.77, -31.3) * mm});
            skLineSegment(sketch, "E975", {"start": v(-37.77, -31.3) * mm, "end": v(-38.1, -31.15) * mm});
            skLineSegment(sketch, "E976", {"start": v(-38.1, -31.15) * mm, "end": v(-38.19, -31.11) * mm});
            skLineSegment(sketch, "E977", {"start": v(-38.19, -31.11) * mm, "end": v(-38.25, -31.1) * mm});
            skLineSegment(sketch, "E978", {"start": v(-38.25, -31.1) * mm, "end": v(-38.26, -31.1) * mm});
            skLineSegment(sketch, "E979", {"start": v(-38.26, -31.1) * mm, "end": v(-38.27, -31.12) * mm});
            skLineSegment(sketch, "E980", {"start": v(-38.27, -31.12) * mm, "end": v(-38.27, -31.17) * mm});
            skLineSegment(sketch, "E981", {"start": v(-38.27, -31.17) * mm, "end": v(-38.18, -31.35) * mm});
            skLineSegment(sketch, "E982", {"start": v(-38.18, -31.35) * mm, "end": v(-38.1, -31.48) * mm});
            skLineSegment(sketch, "E983", {"start": v(-38.1, -31.48) * mm, "end": v(-38, -31.62) * mm});
            skLineSegment(sketch, "E984", {"start": v(-38, -31.62) * mm, "end": v(-37.86, -31.75) * mm});
            skLineSegment(sketch, "E985", {"start": v(-37.86, -31.75) * mm, "end": v(-37.7, -31.88) * mm});
            skLineSegment(sketch, "E986", {"start": v(-37.7, -31.88) * mm, "end": v(-37.53, -32.01) * mm});
            skLineSegment(sketch, "E987", {"start": v(-37.53, -32.01) * mm, "end": v(-37.34, -32.13) * mm});
            skLineSegment(sketch, "E988", {"start": v(-37.34, -32.13) * mm, "end": v(-37.12, -32.25) * mm});
            skLineSegment(sketch, "E989", {"start": v(-37.12, -32.25) * mm, "end": v(-36.88, -32.37) * mm});
            skLineSegment(sketch, "E990", {"start": v(-36.88, -32.37) * mm, "end": v(-36.32, -32.63) * mm});
            skLineSegment(sketch, "E991", {"start": v(-36.32, -32.63) * mm, "end": v(-34.91, -32.88) * mm});
            skLineSegment(sketch, "E992", {"start": v(-34.91, -32.88) * mm, "end": v(-34.27, -32.89) * mm});
            skLineSegment(sketch, "E993", {"start": v(33.92, -32.88) * mm, "end": v(34.69, -32.9) * mm});
            skLineSegment(sketch, "E994", {"start": v(34.69, -32.9) * mm, "end": v(35.3, -32.8) * mm});
            skLineSegment(sketch, "E995", {"start": v(35.3, -32.8) * mm, "end": v(35.57, -32.76) * mm});
            skLineSegment(sketch, "E996", {"start": v(35.57, -32.76) * mm, "end": v(35.89, -32.69) * mm});
            skLineSegment(sketch, "E997", {"start": v(35.89, -32.69) * mm, "end": v(36.2, -32.6) * mm});
            skLineSegment(sketch, "E998", {"start": v(36.2, -32.6) * mm, "end": v(36.47, -32.53) * mm});
            skLineSegment(sketch, "E999", {"start": v(36.47, -32.53) * mm, "end": v(37.04, -32.34) * mm});
            skLineSegment(sketch, "E1000", {"start": v(37.04, -32.34) * mm, "end": v(37.91, -31.71) * mm});
            skLineSegment(sketch, "E1001", {"start": v(37.91, -31.71) * mm, "end": v(38.08, -31.43) * mm});
            skLineSegment(sketch, "E1002", {"start": v(38.08, -31.43) * mm, "end": v(38.2, -31.21) * mm});
            skLineSegment(sketch, "E1003", {"start": v(38.2, -31.21) * mm, "end": v(38.23, -31.14) * mm});
            skLineSegment(sketch, "E1004", {"start": v(38.23, -31.14) * mm, "end": v(38.23, -31.1) * mm});
            skLineSegment(sketch, "E1005", {"start": v(38.23, -31.1) * mm, "end": v(38.18, -31.11) * mm});
            skLineSegment(sketch, "E1006", {"start": v(38.18, -31.11) * mm, "end": v(38.08, -31.15) * mm});
            skLineSegment(sketch, "E1007", {"start": v(38.08, -31.15) * mm, "end": v(37.76, -31.3) * mm});
            skLineSegment(sketch, "E1008", {"start": v(37.76, -31.3) * mm, "end": v(37.52, -31.4) * mm});
            skLineSegment(sketch, "E1009", {"start": v(37.52, -31.4) * mm, "end": v(37.2, -31.53) * mm});
            skLineSegment(sketch, "E1010", {"start": v(37.2, -31.53) * mm, "end": v(36.86, -31.65) * mm});
            skLineSegment(sketch, "E1011", {"start": v(36.86, -31.65) * mm, "end": v(36.5, -31.76) * mm});
            skLineSegment(sketch, "E1012", {"start": v(36.5, -31.76) * mm, "end": v(35.7, -32) * mm});
            skLineSegment(sketch, "E1013", {"start": v(35.7, -32) * mm, "end": v(33.97, -32.15) * mm});
            skLineSegment(sketch, "E1014", {"start": v(33.97, -32.15) * mm, "end": v(32.03, -32) * mm});
            skLineSegment(sketch, "E1015", {"start": v(32.03, -32) * mm, "end": v(31.14, -31.8) * mm});
            skLineSegment(sketch, "E1016", {"start": v(31.14, -31.8) * mm, "end": v(30.72, -31.7) * mm});
            skLineSegment(sketch, "E1017", {"start": v(30.72, -31.7) * mm, "end": v(30.28, -31.6) * mm});
            skLineSegment(sketch, "E1018", {"start": v(30.28, -31.6) * mm, "end": v(29.84, -31.47) * mm});
            skLineSegment(sketch, "E1019", {"start": v(29.84, -31.47) * mm, "end": v(29.4, -31.33) * mm});
            skLineSegment(sketch, "E1020", {"start": v(29.4, -31.33) * mm, "end": v(28.93, -31.18) * mm});
            skLineSegment(sketch, "E1021", {"start": v(28.93, -31.18) * mm, "end": v(28.46, -31.01) * mm});
            skLineSegment(sketch, "E1022", {"start": v(28.46, -31.01) * mm, "end": v(27.97, -30.83) * mm});
            skLineSegment(sketch, "E1023", {"start": v(27.97, -30.83) * mm, "end": v(27.48, -30.63) * mm});
            skLineSegment(sketch, "E1024", {"start": v(27.48, -30.63) * mm, "end": v(26.97, -30.42) * mm});
            skLineSegment(sketch, "E1025", {"start": v(26.97, -30.42) * mm, "end": v(26.45, -30.2) * mm});
            skLineSegment(sketch, "E1026", {"start": v(26.45, -30.2) * mm, "end": v(25.92, -29.95) * mm});
            skLineSegment(sketch, "E1027", {"start": v(25.92, -29.95) * mm, "end": v(25.37, -29.7) * mm});
            skLineSegment(sketch, "E1028", {"start": v(25.37, -29.7) * mm, "end": v(24.81, -29.42) * mm});
            skLineSegment(sketch, "E1029", {"start": v(24.81, -29.42) * mm, "end": v(24.24, -29.13) * mm});
            skLineSegment(sketch, "E1030", {"start": v(24.24, -29.13) * mm, "end": v(23.05, -28.51) * mm});
            skLineSegment(sketch, "E1031", {"start": v(23.05, -28.51) * mm, "end": v(22.1, -28) * mm});
            skLineSegment(sketch, "E1032", {"start": v(22.1, -28) * mm, "end": v(22.08, -28) * mm});
            skLineSegment(sketch, "E1033", {"start": v(22.08, -28) * mm, "end": v(22.05, -28.03) * mm});
            skLineSegment(sketch, "E1034", {"start": v(22.05, -28.03) * mm, "end": v(22, -28.1) * mm});
            skLineSegment(sketch, "E1035", {"start": v(22, -28.1) * mm, "end": v(21.86, -28.37) * mm});
            skLineSegment(sketch, "E1036", {"start": v(21.86, -28.37) * mm, "end": v(21.68, -28.73) * mm});
            skLineSegment(sketch, "E1037", {"start": v(21.68, -28.73) * mm, "end": v(22.18, -29.05) * mm});
            skLineSegment(sketch, "E1038", {"start": v(22.18, -29.05) * mm, "end": v(22.48, -29.23) * mm});
            skLineSegment(sketch, "E1039", {"start": v(22.48, -29.23) * mm, "end": v(22.84, -29.44) * mm});
            skLineSegment(sketch, "E1040", {"start": v(22.84, -29.44) * mm, "end": v(23.69, -29.9) * mm});
            skLineSegment(sketch, "E1041", {"start": v(23.69, -29.9) * mm, "end": v(24.6, -30.36) * mm});
            skLineSegment(sketch, "E1042", {"start": v(24.6, -30.36) * mm, "end": v(25.06, -30.58) * mm});
            skLineSegment(sketch, "E1043", {"start": v(25.06, -30.58) * mm, "end": v(25.49, -30.77) * mm});
            skLineSegment(sketch, "E1044", {"start": v(25.49, -30.77) * mm, "end": v(26.04, -31.01) * mm});
            skLineSegment(sketch, "E1045", {"start": v(26.04, -31.01) * mm, "end": v(26.6, -31.24) * mm});
            skLineSegment(sketch, "E1046", {"start": v(26.6, -31.24) * mm, "end": v(27.16, -31.45) * mm});
            skLineSegment(sketch, "E1047", {"start": v(27.16, -31.45) * mm, "end": v(27.71, -31.65) * mm});
            skLineSegment(sketch, "E1048", {"start": v(27.71, -31.65) * mm, "end": v(28.27, -31.84) * mm});
            skLineSegment(sketch, "E1049", {"start": v(28.27, -31.84) * mm, "end": v(28.82, -32) * mm});
            skLineSegment(sketch, "E1050", {"start": v(28.82, -32) * mm, "end": v(29.37, -32.16) * mm});
            skLineSegment(sketch, "E1051", {"start": v(29.37, -32.16) * mm, "end": v(29.91, -32.3) * mm});
            skLineSegment(sketch, "E1052", {"start": v(29.91, -32.3) * mm, "end": v(30.45, -32.43) * mm});
            skLineSegment(sketch, "E1053", {"start": v(30.45, -32.43) * mm, "end": v(30.97, -32.55) * mm});
            skLineSegment(sketch, "E1054", {"start": v(30.97, -32.55) * mm, "end": v(31.5, -32.64) * mm});
            skLineSegment(sketch, "E1055", {"start": v(31.5, -32.64) * mm, "end": v(32, -32.72) * mm});
            skLineSegment(sketch, "E1056", {"start": v(32, -32.72) * mm, "end": v(32.5, -32.79) * mm});
            skLineSegment(sketch, "E1057", {"start": v(32.5, -32.79) * mm, "end": v(32.99, -32.84) * mm});
            skLineSegment(sketch, "E1058", {"start": v(32.99, -32.84) * mm, "end": v(33.46, -32.87) * mm});
            skLineSegment(sketch, "E1059", {"start": v(33.46, -32.87) * mm, "end": v(33.92, -32.88) * mm});
            skLineSegment(sketch, "E1060", {"start": v(-34.13, -31.08) * mm, "end": v(-33.75, -31.05) * mm});
            skLineSegment(sketch, "E1061", {"start": v(-33.75, -31.05) * mm, "end": v(-33, -30.98) * mm});
            skLineSegment(sketch, "E1062", {"start": v(-33, -30.98) * mm, "end": v(-31.97, -30.88) * mm});
            skLineSegment(sketch, "E1063", {"start": v(-31.97, -30.88) * mm, "end": v(-31.97, -29.36) * mm});
            skLineSegment(sketch, "E1064", {"start": v(-31.97, -29.36) * mm, "end": v(-30.64, -29.36) * mm});
            skLineSegment(sketch, "E1065", {"start": v(-30.64, -29.36) * mm, "end": v(-30.25, -28.94) * mm});
            skLineSegment(sketch, "E1066", {"start": v(-30.25, -28.94) * mm, "end": v(-30.25, -28.12) * mm});
            skLineSegment(sketch, "E1067", {"start": v(-30.25, -28.12) * mm, "end": v(-30.56, -27.84) * mm});
            skLineSegment(sketch, "E1068", {"start": v(-30.56, -27.84) * mm, "end": v(-31.1, -27.8) * mm});
            skLineSegment(sketch, "E1069", {"start": v(-31.1, -27.8) * mm, "end": v(-31.8, -27.74) * mm});
            skLineSegment(sketch, "E1070", {"start": v(-31.8, -27.74) * mm, "end": v(-31.97, -27.73) * mm});
            skLineSegment(sketch, "E1071", {"start": v(-31.97, -27.73) * mm, "end": v(-31.97, -26.64) * mm});
            skLineSegment(sketch, "E1072", {"start": v(-31.97, -26.64) * mm, "end": v(-34.23, -26.64) * mm});
            skLineSegment(sketch, "E1073", {"start": v(-34.23, -26.64) * mm, "end": v(-34.23, -27.7) * mm});
            skLineSegment(sketch, "E1074", {"start": v(-34.23, -27.7) * mm, "end": v(-34.57, -27.76) * mm});
            skLineSegment(sketch, "E1075", {"start": v(-34.57, -27.76) * mm, "end": v(-34.92, -27.8) * mm});
            skLineSegment(sketch, "E1076", {"start": v(-34.92, -27.8) * mm, "end": v(-35.28, -27.82) * mm});
            skLineSegment(sketch, "E1077", {"start": v(-35.28, -27.82) * mm, "end": v(-35.66, -27.82) * mm});
            skLineSegment(sketch, "E1078", {"start": v(-35.66, -27.82) * mm, "end": v(-35.97, -28.17) * mm});
            skLineSegment(sketch, "E1079", {"start": v(-35.97, -28.17) * mm, "end": v(-35.98, -28.95) * mm});
            skLineSegment(sketch, "E1080", {"start": v(-35.98, -28.95) * mm, "end": v(-35.5, -29.36) * mm});
            skLineSegment(sketch, "E1081", {"start": v(-35.5, -29.36) * mm, "end": v(-34.23, -29.36) * mm});
            skLineSegment(sketch, "E1082", {"start": v(-34.23, -29.36) * mm, "end": v(-34.23, -31.08) * mm});
            skLineSegment(sketch, "E1083", {"start": v(-34.23, -31.08) * mm, "end": v(-34.13, -31.08) * mm});
            skLineSegment(sketch, "E1084", {"start": v(33.94, -31.07) * mm, "end": v(34.19, -31.08) * mm});
            skLineSegment(sketch, "E1085", {"start": v(34.19, -31.08) * mm, "end": v(34.19, -29.36) * mm});
            skLineSegment(sketch, "E1086", {"start": v(34.19, -29.36) * mm, "end": v(35.47, -29.36) * mm});
            skLineSegment(sketch, "E1087", {"start": v(35.47, -29.36) * mm, "end": v(35.8, -29.18) * mm});
            skLineSegment(sketch, "E1088", {"start": v(35.8, -29.18) * mm, "end": v(36, -28.57) * mm});
            skLineSegment(sketch, "E1089", {"start": v(36, -28.57) * mm, "end": v(35.9, -28.1) * mm});
            skLineSegment(sketch, "E1090", {"start": v(35.9, -28.1) * mm, "end": v(35.54, -27.78) * mm});
            skLineSegment(sketch, "E1091", {"start": v(35.54, -27.78) * mm, "end": v(34.23, -27.74) * mm});
            skLineSegment(sketch, "E1092", {"start": v(34.23, -27.74) * mm, "end": v(34.18, -26.64) * mm});
            skLineSegment(sketch, "E1093", {"start": v(34.18, -26.64) * mm, "end": v(31.92, -26.64) * mm});
            skLineSegment(sketch, "E1094", {"start": v(31.92, -26.64) * mm, "end": v(31.92, -27.73) * mm});
            skLineSegment(sketch, "E1095", {"start": v(31.92, -27.73) * mm, "end": v(31.72, -27.74) * mm});
            skLineSegment(sketch, "E1096", {"start": v(31.72, -27.74) * mm, "end": v(31.02, -27.78) * mm});
            skLineSegment(sketch, "E1097", {"start": v(31.02, -27.78) * mm, "end": v(30.53, -27.8) * mm});
            skLineSegment(sketch, "E1098", {"start": v(30.53, -27.8) * mm, "end": v(30.2, -28.2) * mm});
            skLineSegment(sketch, "E1099", {"start": v(30.2, -28.2) * mm, "end": v(30.2, -28.99) * mm});
            skLineSegment(sketch, "E1100", {"start": v(30.2, -28.99) * mm, "end": v(30.68, -29.36) * mm});
            skLineSegment(sketch, "E1101", {"start": v(30.68, -29.36) * mm, "end": v(31.92, -29.36) * mm});
            skLineSegment(sketch, "E1102", {"start": v(31.92, -29.36) * mm, "end": v(31.97, -30.86) * mm});
            skLineSegment(sketch, "E1103", {"start": v(31.97, -30.86) * mm, "end": v(33.69, -31.06) * mm});
            skLineSegment(sketch, "E1104", {"start": v(33.69, -31.06) * mm, "end": v(33.94, -31.07) * mm});
            skLineSegment(sketch, "E1105", {"start": v(-33.1, -25.83) * mm, "end": v(-31.8, -25.83) * mm});
            skLineSegment(sketch, "E1106", {"start": v(-31.8, -25.83) * mm, "end": v(-31.59, -25.29) * mm});
            skLineSegment(sketch, "E1107", {"start": v(-31.59, -25.29) * mm, "end": v(-30.82, -24.58) * mm});
            skLineSegment(sketch, "E1108", {"start": v(-30.82, -24.58) * mm, "end": v(-30.49, -24.46) * mm});
            skLineSegment(sketch, "E1109", {"start": v(-30.49, -24.46) * mm, "end": v(-30.36, -24.4) * mm});
            skLineSegment(sketch, "E1110", {"start": v(-30.36, -24.4) * mm, "end": v(-30.25, -24.36) * mm});
            skLineSegment(sketch, "E1111", {"start": v(-30.25, -24.36) * mm, "end": v(-30.18, -24.3) * mm});
            skLineSegment(sketch, "E1112", {"start": v(-30.18, -24.3) * mm, "end": v(-30.16, -24.29) * mm});
            skLineSegment(sketch, "E1113", {"start": v(-30.16, -24.29) * mm, "end": v(-30.16, -24.27) * mm});
            skLineSegment(sketch, "E1114", {"start": v(-30.16, -24.27) * mm, "end": v(-30.16, -24.2) * mm});
            skLineSegment(sketch, "E1115", {"start": v(-30.16, -24.2) * mm, "end": v(-31.47, -23.79) * mm});
            skLineSegment(sketch, "E1116", {"start": v(-31.47, -23.79) * mm, "end": v(-34.82, -23.79) * mm});
            skLineSegment(sketch, "E1117", {"start": v(-34.82, -23.79) * mm, "end": v(-35.19, -23.9) * mm});
            skLineSegment(sketch, "E1118", {"start": v(-35.19, -23.9) * mm, "end": v(-35.51, -24.02) * mm});
            skLineSegment(sketch, "E1119", {"start": v(-35.51, -24.02) * mm, "end": v(-35.75, -24.1) * mm});
            skLineSegment(sketch, "E1120", {"start": v(-35.75, -24.1) * mm, "end": v(-35.92, -24.18) * mm});
            skLineSegment(sketch, "E1121", {"start": v(-35.92, -24.18) * mm, "end": v(-35.97, -24.21) * mm});
            skLineSegment(sketch, "E1122", {"start": v(-35.97, -24.21) * mm, "end": v(-36, -24.24) * mm});
            skLineSegment(sketch, "E1123", {"start": v(-36, -24.24) * mm, "end": v(-36.03, -24.27) * mm});
            skLineSegment(sketch, "E1124", {"start": v(-36.03, -24.27) * mm, "end": v(-36.03, -24.3) * mm});
            skLineSegment(sketch, "E1125", {"start": v(-36.03, -24.3) * mm, "end": v(-36.01, -24.32) * mm});
            skLineSegment(sketch, "E1126", {"start": v(-36.01, -24.32) * mm, "end": v(-35.98, -24.34) * mm});
            skLineSegment(sketch, "E1127", {"start": v(-35.98, -24.34) * mm, "end": v(-35.88, -24.4) * mm});
            skLineSegment(sketch, "E1128", {"start": v(-35.88, -24.4) * mm, "end": v(-35.72, -24.46) * mm});
            skLineSegment(sketch, "E1129", {"start": v(-35.72, -24.46) * mm, "end": v(-35.38, -24.58) * mm});
            skLineSegment(sketch, "E1130", {"start": v(-35.38, -24.58) * mm, "end": v(-34.62, -25.29) * mm});
            skLineSegment(sketch, "E1131", {"start": v(-34.62, -25.29) * mm, "end": v(-34.4, -25.83) * mm});
            skLineSegment(sketch, "E1132", {"start": v(-34.4, -25.83) * mm, "end": v(-33.1, -25.83) * mm});
            skLineSegment(sketch, "E1133", {"start": v(33.08, -25.83) * mm, "end": v(34.33, -25.83) * mm});
            skLineSegment(sketch, "E1134", {"start": v(34.33, -25.83) * mm, "end": v(34.68, -25.17) * mm});
            skLineSegment(sketch, "E1135", {"start": v(34.68, -25.17) * mm, "end": v(35.4, -24.56) * mm});
            skLineSegment(sketch, "E1136", {"start": v(35.4, -24.56) * mm, "end": v(35.7, -24.45) * mm});
            skLineSegment(sketch, "E1137", {"start": v(35.7, -24.45) * mm, "end": v(35.82, -24.4) * mm});
            skLineSegment(sketch, "E1138", {"start": v(35.82, -24.4) * mm, "end": v(35.91, -24.36) * mm});
            skLineSegment(sketch, "E1139", {"start": v(35.91, -24.36) * mm, "end": v(35.98, -24.31) * mm});
            skLineSegment(sketch, "E1140", {"start": v(35.98, -24.31) * mm, "end": v(36, -24.3) * mm});
            skLineSegment(sketch, "E1141", {"start": v(36, -24.3) * mm, "end": v(36, -24.28) * mm});
            skLineSegment(sketch, "E1142", {"start": v(36, -24.28) * mm, "end": v(36, -24.26) * mm});
            skLineSegment(sketch, "E1143", {"start": v(36, -24.26) * mm, "end": v(35.97, -24.24) * mm});
            skLineSegment(sketch, "E1144", {"start": v(35.97, -24.24) * mm, "end": v(35.9, -24.2) * mm});
            skLineSegment(sketch, "E1145", {"start": v(35.9, -24.2) * mm, "end": v(35.77, -24.13) * mm});
            skLineSegment(sketch, "E1146", {"start": v(35.77, -24.13) * mm, "end": v(35.63, -24.07) * mm});
            skLineSegment(sketch, "E1147", {"start": v(35.63, -24.07) * mm, "end": v(35.26, -23.92) * mm});
            skLineSegment(sketch, "E1148", {"start": v(35.26, -23.92) * mm, "end": v(33.87, -23.72) * mm});
            skLineSegment(sketch, "E1149", {"start": v(33.87, -23.72) * mm, "end": v(31.33, -23.82) * mm});
            skLineSegment(sketch, "E1150", {"start": v(31.33, -23.82) * mm, "end": v(30.72, -24.01) * mm});
            skLineSegment(sketch, "E1151", {"start": v(30.72, -24.01) * mm, "end": v(30.29, -24.16) * mm});
            skLineSegment(sketch, "E1152", {"start": v(30.29, -24.16) * mm, "end": v(30.16, -24.21) * mm});
            skLineSegment(sketch, "E1153", {"start": v(30.16, -24.21) * mm, "end": v(30.1, -24.24) * mm});
            skLineSegment(sketch, "E1154", {"start": v(30.1, -24.24) * mm, "end": v(30.14, -24.28) * mm});
            skLineSegment(sketch, "E1155", {"start": v(30.14, -24.28) * mm, "end": v(30.24, -24.34) * mm});
            skLineSegment(sketch, "E1156", {"start": v(30.24, -24.34) * mm, "end": v(30.54, -24.5) * mm});
            skLineSegment(sketch, "E1157", {"start": v(30.54, -24.5) * mm, "end": v(30.74, -24.62) * mm});
            skLineSegment(sketch, "E1158", {"start": v(30.74, -24.62) * mm, "end": v(30.9, -24.72) * mm});
            skLineSegment(sketch, "E1159", {"start": v(30.9, -24.72) * mm, "end": v(31.05, -24.82) * mm});
            skLineSegment(sketch, "E1160", {"start": v(31.05, -24.82) * mm, "end": v(31.18, -24.92) * mm});
            skLineSegment(sketch, "E1161", {"start": v(31.18, -24.92) * mm, "end": v(31.29, -25.03) * mm});
            skLineSegment(sketch, "E1162", {"start": v(31.29, -25.03) * mm, "end": v(31.4, -25.15) * mm});
            skLineSegment(sketch, "E1163", {"start": v(31.4, -25.15) * mm, "end": v(31.5, -25.28) * mm});
            skLineSegment(sketch, "E1164", {"start": v(31.5, -25.28) * mm, "end": v(31.6, -25.44) * mm});
            skLineSegment(sketch, "E1165", {"start": v(31.6, -25.44) * mm, "end": v(31.83, -25.83) * mm});
            skLineSegment(sketch, "E1166", {"start": v(31.83, -25.83) * mm, "end": v(33.08, -25.83) * mm});
            skLineSegment(sketch, "E1167", {"start": v(-0.02, 22.38) * mm, "end": v(35.46, 22.38) * mm});
            skLineSegment(sketch, "E1168", {"start": v(35.46, 22.38) * mm, "end": v(35.46, 29.72) * mm});
            skLineSegment(sketch, "E1169", {"start": v(35.46, 29.72) * mm, "end": v(0.8, 29.77) * mm});
            skLineSegment(sketch, "E1170", {"start": v(0.8, 29.77) * mm, "end": v(0.74, 33.4) * mm});
            skLineSegment(sketch, "E1171", {"start": v(0.74, 33.4) * mm, "end": v(0.82, 33.3) * mm});
            skLineSegment(sketch, "E1172", {"start": v(0.82, 33.3) * mm, "end": v(0.86, 33.23) * mm});
            skLineSegment(sketch, "E1173", {"start": v(0.86, 33.23) * mm, "end": v(0.92, 33.1) * mm});
            skLineSegment(sketch, "E1174", {"start": v(0.92, 33.1) * mm, "end": v(1.06, 32.76) * mm});
            skLineSegment(sketch, "E1175", {"start": v(1.06, 32.76) * mm, "end": v(1.14, 32.56) * mm});
            skLineSegment(sketch, "E1176", {"start": v(1.14, 32.56) * mm, "end": v(1.24, 32.33) * mm});
            skLineSegment(sketch, "E1177", {"start": v(1.24, 32.33) * mm, "end": v(1.35, 32.11) * mm});
            skLineSegment(sketch, "E1178", {"start": v(1.35, 32.11) * mm, "end": v(1.44, 31.93) * mm});
            skLineSegment(sketch, "E1179", {"start": v(1.44, 31.93) * mm, "end": v(1.66, 31.55) * mm});
            skLineSegment(sketch, "E1180", {"start": v(1.66, 31.55) * mm, "end": v(2.48, 30.8) * mm});
            skLineSegment(sketch, "E1181", {"start": v(2.48, 30.8) * mm, "end": v(3.32, 30.43) * mm});
            skLineSegment(sketch, "E1182", {"start": v(3.32, 30.43) * mm, "end": v(4.34, 30.52) * mm});
            skLineSegment(sketch, "E1183", {"start": v(4.34, 30.52) * mm, "end": v(5.07, 30.9) * mm});
            skLineSegment(sketch, "E1184", {"start": v(5.07, 30.9) * mm, "end": v(5.9, 31.82) * mm});
            skLineSegment(sketch, "E1185", {"start": v(5.9, 31.82) * mm, "end": v(6.13, 32.3) * mm});
            skLineSegment(sketch, "E1186", {"start": v(6.13, 32.3) * mm, "end": v(6.23, 32.52) * mm});
            skLineSegment(sketch, "E1187", {"start": v(6.23, 32.52) * mm, "end": v(6.34, 32.78) * mm});
            skLineSegment(sketch, "E1188", {"start": v(6.34, 32.78) * mm, "end": v(6.43, 33.06) * mm});
            skLineSegment(sketch, "E1189", {"start": v(6.43, 33.06) * mm, "end": v(6.5, 33.3) * mm});
            skLineSegment(sketch, "E1190", {"start": v(6.5, 33.3) * mm, "end": v(6.65, 33.85) * mm});
            skLineSegment(sketch, "E1191", {"start": v(6.65, 33.85) * mm, "end": v(6.65, 35.75) * mm});
            skLineSegment(sketch, "E1192", {"start": v(6.65, 35.75) * mm, "end": v(6.45, 36.39) * mm});
            skLineSegment(sketch, "E1193", {"start": v(6.45, 36.39) * mm, "end": v(6.35, 36.68) * mm});
            skLineSegment(sketch, "E1194", {"start": v(6.35, 36.68) * mm, "end": v(6.26, 36.95) * mm});
            skLineSegment(sketch, "E1195", {"start": v(6.26, 36.95) * mm, "end": v(6.16, 37.18) * mm});
            skLineSegment(sketch, "E1196", {"start": v(6.16, 37.18) * mm, "end": v(6.06, 37.4) * mm});
            skLineSegment(sketch, "E1197", {"start": v(6.06, 37.4) * mm, "end": v(5.95, 37.58) * mm});
            skLineSegment(sketch, "E1198", {"start": v(5.95, 37.58) * mm, "end": v(5.82, 37.77) * mm});
            skLineSegment(sketch, "E1199", {"start": v(5.82, 37.77) * mm, "end": v(5.68, 37.94) * mm});
            skLineSegment(sketch, "E1200", {"start": v(5.68, 37.94) * mm, "end": v(5.53, 38.12) * mm});
            skLineSegment(sketch, "E1201", {"start": v(5.53, 38.12) * mm, "end": v(5.15, 38.53) * mm});
            skLineSegment(sketch, "E1202", {"start": v(5.15, 38.53) * mm, "end": v(4.33, 39.01) * mm});
            skLineSegment(sketch, "E1203", {"start": v(4.33, 39.01) * mm, "end": v(3.06, 39) * mm});
            skLineSegment(sketch, "E1204", {"start": v(3.06, 39) * mm, "end": v(2.33, 38.62) * mm});
            skLineSegment(sketch, "E1205", {"start": v(2.33, 38.62) * mm, "end": v(1.96, 38.23) * mm});
            skLineSegment(sketch, "E1206", {"start": v(1.96, 38.23) * mm, "end": v(1.8, 38.06) * mm});
            skLineSegment(sketch, "E1207", {"start": v(1.8, 38.06) * mm, "end": v(1.67, 37.9) * mm});
            skLineSegment(sketch, "E1208", {"start": v(1.67, 37.9) * mm, "end": v(1.54, 37.72) * mm});
            skLineSegment(sketch, "E1209", {"start": v(1.54, 37.72) * mm, "end": v(1.43, 37.55) * mm});
            skLineSegment(sketch, "E1210", {"start": v(1.43, 37.55) * mm, "end": v(1.33, 37.37) * mm});
            skLineSegment(sketch, "E1211", {"start": v(1.33, 37.37) * mm, "end": v(1.24, 37.18) * mm});
            skLineSegment(sketch, "E1212", {"start": v(1.24, 37.18) * mm, "end": v(1.15, 36.97) * mm});
            skLineSegment(sketch, "E1213", {"start": v(1.15, 36.97) * mm, "end": v(1.06, 36.75) * mm});
            skLineSegment(sketch, "E1214", {"start": v(1.06, 36.75) * mm, "end": v(0.92, 36.4) * mm});
            skLineSegment(sketch, "E1215", {"start": v(0.92, 36.4) * mm, "end": v(0.87, 36.28) * mm});
            skLineSegment(sketch, "E1216", {"start": v(0.87, 36.28) * mm, "end": v(0.82, 36.2) * mm});
            skLineSegment(sketch, "E1217", {"start": v(0.82, 36.2) * mm, "end": v(0.75, 36.12) * mm});
            skLineSegment(sketch, "E1218", {"start": v(0.75, 36.12) * mm, "end": v(0.75, 39.04) * mm});
            skLineSegment(sketch, "E1219", {"start": v(0.75, 39.04) * mm, "end": v(1.37, 39.55) * mm});
            skLineSegment(sketch, "E1220", {"start": v(1.37, 39.55) * mm, "end": v(1.67, 39.8) * mm});
            skLineSegment(sketch, "E1221", {"start": v(1.67, 39.8) * mm, "end": v(2.01, 40.12) * mm});
            skLineSegment(sketch, "E1222", {"start": v(2.01, 40.12) * mm, "end": v(2.36, 40.46) * mm});
            skLineSegment(sketch, "E1223", {"start": v(2.36, 40.46) * mm, "end": v(2.68, 40.77) * mm});
            skLineSegment(sketch, "E1224", {"start": v(2.68, 40.77) * mm, "end": v(3.36, 41.48) * mm});
            skLineSegment(sketch, "E1225", {"start": v(3.36, 41.48) * mm, "end": v(4.42, 43) * mm});
            skLineSegment(sketch, "E1226", {"start": v(4.42, 43) * mm, "end": v(4.53, 41.98) * mm});
            skLineSegment(sketch, "E1227", {"start": v(4.53, 41.98) * mm, "end": v(4.91, 41.35) * mm});
            skLineSegment(sketch, "E1228", {"start": v(4.91, 41.35) * mm, "end": v(6.19, 40.22) * mm});
            skLineSegment(sketch, "E1229", {"start": v(6.19, 40.22) * mm, "end": v(6.62, 39.47) * mm});
            skLineSegment(sketch, "E1230", {"start": v(6.62, 39.47) * mm, "end": v(6.75, 38.79) * mm});
            skLineSegment(sketch, "E1231", {"start": v(6.75, 38.79) * mm, "end": v(6.85, 38.79) * mm});
            skLineSegment(sketch, "E1232", {"start": v(6.85, 38.79) * mm, "end": v(6.91, 38.8) * mm});
            skLineSegment(sketch, "E1233", {"start": v(6.91, 38.8) * mm, "end": v(6.99, 38.83) * mm});
            skLineSegment(sketch, "E1234", {"start": v(6.99, 38.83) * mm, "end": v(7.07, 38.87) * mm});
            skLineSegment(sketch, "E1235", {"start": v(7.07, 38.87) * mm, "end": v(7.15, 38.92) * mm});
            skLineSegment(sketch, "E1236", {"start": v(7.15, 38.92) * mm, "end": v(7.35, 39.06) * mm});
            skLineSegment(sketch, "E1237", {"start": v(7.35, 39.06) * mm, "end": v(7.56, 39.7) * mm});
            skLineSegment(sketch, "E1238", {"start": v(7.56, 39.7) * mm, "end": v(7.71, 39.64) * mm});
            skLineSegment(sketch, "E1239", {"start": v(7.71, 39.64) * mm, "end": v(7.8, 39.6) * mm});
            skLineSegment(sketch, "E1240", {"start": v(7.8, 39.6) * mm, "end": v(7.96, 39.57) * mm});
            skLineSegment(sketch, "E1241", {"start": v(7.96, 39.57) * mm, "end": v(8.36, 39.48) * mm});
            skLineSegment(sketch, "E1242", {"start": v(8.36, 39.48) * mm, "end": v(8.72, 39.41) * mm});
            skLineSegment(sketch, "E1243", {"start": v(8.72, 39.41) * mm, "end": v(8.9, 39.37) * mm});
            skLineSegment(sketch, "E1244", {"start": v(8.9, 39.37) * mm, "end": v(8.89, 39.35) * mm});
            skLineSegment(sketch, "E1245", {"start": v(8.89, 39.35) * mm, "end": v(8.87, 39.31) * mm});
            skLineSegment(sketch, "E1246", {"start": v(8.87, 39.31) * mm, "end": v(8.78, 39.18) * mm});
            skLineSegment(sketch, "E1247", {"start": v(8.78, 39.18) * mm, "end": v(8.46, 38.77) * mm});
            skLineSegment(sketch, "E1248", {"start": v(8.46, 38.77) * mm, "end": v(8, 38.2) * mm});
            skLineSegment(sketch, "E1249", {"start": v(8, 38.2) * mm, "end": v(7.77, 37.72) * mm});
            skLineSegment(sketch, "E1250", {"start": v(7.77, 37.72) * mm, "end": v(7.68, 37.5) * mm});
            skLineSegment(sketch, "E1251", {"start": v(7.68, 37.5) * mm, "end": v(7.58, 37.27) * mm});
            skLineSegment(sketch, "E1252", {"start": v(7.58, 37.27) * mm, "end": v(7.5, 37.05) * mm});
            skLineSegment(sketch, "E1253", {"start": v(7.5, 37.05) * mm, "end": v(7.46, 36.86) * mm});
            skLineSegment(sketch, "E1254", {"start": v(7.46, 36.86) * mm, "end": v(7.37, 36.48) * mm});
            skLineSegment(sketch, "E1255", {"start": v(7.37, 36.48) * mm, "end": v(7.36, 35.1) * mm});
            skLineSegment(sketch, "E1256", {"start": v(7.36, 35.1) * mm, "end": v(7.54, 34.41) * mm});
            skLineSegment(sketch, "E1257", {"start": v(7.54, 34.41) * mm, "end": v(7.62, 34.12) * mm});
            skLineSegment(sketch, "E1258", {"start": v(7.62, 34.12) * mm, "end": v(7.7, 33.86) * mm});
            skLineSegment(sketch, "E1259", {"start": v(7.7, 33.86) * mm, "end": v(7.8, 33.61) * mm});
            skLineSegment(sketch, "E1260", {"start": v(7.8, 33.61) * mm, "end": v(7.9, 33.38) * mm});
            skLineSegment(sketch, "E1261", {"start": v(7.9, 33.38) * mm, "end": v(8.01, 33.15) * mm});
            skLineSegment(sketch, "E1262", {"start": v(8.01, 33.15) * mm, "end": v(8.14, 32.93) * mm});
            skLineSegment(sketch, "E1263", {"start": v(8.14, 32.93) * mm, "end": v(8.3, 32.7) * mm});
            skLineSegment(sketch, "E1264", {"start": v(8.3, 32.7) * mm, "end": v(8.46, 32.48) * mm});
            skLineSegment(sketch, "E1265", {"start": v(8.46, 32.48) * mm, "end": v(8.82, 32.01) * mm});
            skLineSegment(sketch, "E1266", {"start": v(8.82, 32.01) * mm, "end": v(9.9, 31.25) * mm});
            skLineSegment(sketch, "E1267", {"start": v(9.9, 31.25) * mm, "end": v(11.03, 30.8) * mm});
            skLineSegment(sketch, "E1268", {"start": v(11.03, 30.8) * mm, "end": v(12.56, 30.54) * mm});
            skLineSegment(sketch, "E1269", {"start": v(12.56, 30.54) * mm, "end": v(14.06, 30.73) * mm});
            skLineSegment(sketch, "E1270", {"start": v(14.06, 30.73) * mm, "end": v(14.68, 30.91) * mm});
            skLineSegment(sketch, "E1271", {"start": v(14.68, 30.91) * mm, "end": v(15.47, 31.18) * mm});
            skLineSegment(sketch, "E1272", {"start": v(15.47, 31.18) * mm, "end": v(16.52, 31.56) * mm});
            skLineSegment(sketch, "E1273", {"start": v(16.52, 31.56) * mm, "end": v(17.74, 32.02) * mm});
            skLineSegment(sketch, "E1274", {"start": v(17.74, 32.02) * mm, "end": v(19.58, 32.1) * mm});
            skLineSegment(sketch, "E1275", {"start": v(19.58, 32.1) * mm, "end": v(20.25, 31.9) * mm});
            skLineSegment(sketch, "E1276", {"start": v(20.25, 31.9) * mm, "end": v(20.8, 31.72) * mm});
            skLineSegment(sketch, "E1277", {"start": v(20.8, 31.72) * mm, "end": v(21.02, 31.63) * mm});
            skLineSegment(sketch, "E1278", {"start": v(21.02, 31.63) * mm, "end": v(21.17, 31.57) * mm});
            skLineSegment(sketch, "E1279", {"start": v(21.17, 31.57) * mm, "end": v(21.28, 31.51) * mm});
            skLineSegment(sketch, "E1280", {"start": v(21.28, 31.51) * mm, "end": v(21.36, 31.48) * mm});
            skLineSegment(sketch, "E1281", {"start": v(21.36, 31.48) * mm, "end": v(21.42, 31.48) * mm});
            skLineSegment(sketch, "E1282", {"start": v(21.42, 31.48) * mm, "end": v(21.45, 31.48) * mm});
            skLineSegment(sketch, "E1283", {"start": v(21.45, 31.48) * mm, "end": v(21.46, 31.5) * mm});
            skLineSegment(sketch, "E1284", {"start": v(21.46, 31.5) * mm, "end": v(21.48, 31.54) * mm});
            skLineSegment(sketch, "E1285", {"start": v(21.48, 31.54) * mm, "end": v(21.48, 31.6) * mm});
            skLineSegment(sketch, "E1286", {"start": v(21.48, 31.6) * mm, "end": v(21.46, 31.7) * mm});
            skLineSegment(sketch, "E1287", {"start": v(21.46, 31.7) * mm, "end": v(21.42, 31.83) * mm});
            skLineSegment(sketch, "E1288", {"start": v(21.42, 31.83) * mm, "end": v(21.32, 32.14) * mm});
            skLineSegment(sketch, "E1289", {"start": v(21.32, 32.14) * mm, "end": v(21.07, 32.38) * mm});
            skLineSegment(sketch, "E1290", {"start": v(21.07, 32.38) * mm, "end": v(20.95, 32.48) * mm});
            skLineSegment(sketch, "E1291", {"start": v(20.95, 32.48) * mm, "end": v(20.8, 32.59) * mm});
            skLineSegment(sketch, "E1292", {"start": v(20.8, 32.59) * mm, "end": v(20.63, 32.68) * mm});
            skLineSegment(sketch, "E1293", {"start": v(20.63, 32.68) * mm, "end": v(20.48, 32.76) * mm});
            skLineSegment(sketch, "E1294", {"start": v(20.48, 32.76) * mm, "end": v(20.14, 32.9) * mm});
            skLineSegment(sketch, "E1295", {"start": v(20.14, 32.9) * mm, "end": v(20.14, 33.08) * mm});
            skLineSegment(sketch, "E1296", {"start": v(20.14, 33.08) * mm, "end": v(22.36, 34.16) * mm});
            skLineSegment(sketch, "E1297", {"start": v(22.36, 34.16) * mm, "end": v(23.81, 34.57) * mm});
            skLineSegment(sketch, "E1298", {"start": v(23.81, 34.57) * mm, "end": v(26.35, 34.57) * mm});
            skLineSegment(sketch, "E1299", {"start": v(26.35, 34.57) * mm, "end": v(27.2, 34.15) * mm});
            skLineSegment(sketch, "E1300", {"start": v(27.2, 34.15) * mm, "end": v(27.83, 33.45) * mm});
            skLineSegment(sketch, "E1301", {"start": v(27.83, 33.45) * mm, "end": v(27.95, 32.64) * mm});
            skLineSegment(sketch, "E1302", {"start": v(27.95, 32.64) * mm, "end": v(27.66, 31.64) * mm});
            skLineSegment(sketch, "E1303", {"start": v(27.66, 31.64) * mm, "end": v(26.99, 31.08) * mm});
            skLineSegment(sketch, "E1304", {"start": v(26.99, 31.08) * mm, "end": v(26.13, 31.08) * mm});
            skLineSegment(sketch, "E1305", {"start": v(26.13, 31.08) * mm, "end": v(25.49, 31.39) * mm});
            skLineSegment(sketch, "E1306", {"start": v(25.49, 31.39) * mm, "end": v(25.5, 31.49) * mm});
            skLineSegment(sketch, "E1307", {"start": v(25.5, 31.49) * mm, "end": v(25.5, 31.54) * mm});
            skLineSegment(sketch, "E1308", {"start": v(25.5, 31.54) * mm, "end": v(25.53, 31.62) * mm});
            skLineSegment(sketch, "E1309", {"start": v(25.53, 31.62) * mm, "end": v(25.62, 31.8) * mm});
            skLineSegment(sketch, "E1310", {"start": v(25.62, 31.8) * mm, "end": v(25.75, 32.04) * mm});
            skLineSegment(sketch, "E1311", {"start": v(25.75, 32.04) * mm, "end": v(25.76, 32.5) * mm});
            skLineSegment(sketch, "E1312", {"start": v(25.76, 32.5) * mm, "end": v(25.52, 32.82) * mm});
            skLineSegment(sketch, "E1313", {"start": v(25.52, 32.82) * mm, "end": v(24.72, 32.92) * mm});
            skLineSegment(sketch, "E1314", {"start": v(24.72, 32.92) * mm, "end": v(24.36, 32.51) * mm});
            skLineSegment(sketch, "E1315", {"start": v(24.36, 32.51) * mm, "end": v(24.38, 31.62) * mm});
            skLineSegment(sketch, "E1316", {"start": v(24.38, 31.62) * mm, "end": v(24.84, 30.93) * mm});
            skLineSegment(sketch, "E1317", {"start": v(24.84, 30.93) * mm, "end": v(25.68, 30.52) * mm});
            skLineSegment(sketch, "E1318", {"start": v(25.68, 30.52) * mm, "end": v(27.16, 30.6) * mm});
            skLineSegment(sketch, "E1319", {"start": v(27.16, 30.6) * mm, "end": v(28.12, 31.09) * mm});
            skLineSegment(sketch, "E1320", {"start": v(28.12, 31.09) * mm, "end": v(28.61, 31.83) * mm});
            skLineSegment(sketch, "E1321", {"start": v(28.61, 31.83) * mm, "end": v(28.68, 33.09) * mm});
            skLineSegment(sketch, "E1322", {"start": v(28.68, 33.09) * mm, "end": v(28.37, 33.91) * mm});
            skLineSegment(sketch, "E1323", {"start": v(28.37, 33.91) * mm, "end": v(27.82, 34.54) * mm});
            skLineSegment(sketch, "E1324", {"start": v(27.82, 34.54) * mm, "end": v(27.35, 34.77) * mm});
            skLineSegment(sketch, "E1325", {"start": v(27.35, 34.77) * mm, "end": v(27.14, 34.88) * mm});
            skLineSegment(sketch, "E1326", {"start": v(27.14, 34.88) * mm, "end": v(26.95, 34.96) * mm});
            skLineSegment(sketch, "E1327", {"start": v(26.95, 34.96) * mm, "end": v(26.77, 35.03) * mm});
            skLineSegment(sketch, "E1328", {"start": v(26.77, 35.03) * mm, "end": v(26.59, 35.1) * mm});
            skLineSegment(sketch, "E1329", {"start": v(26.59, 35.1) * mm, "end": v(26.4, 35.14) * mm});
            skLineSegment(sketch, "E1330", {"start": v(26.4, 35.14) * mm, "end": v(26.18, 35.18) * mm});
            skLineSegment(sketch, "E1331", {"start": v(26.18, 35.18) * mm, "end": v(25.65, 35.25) * mm});
            skLineSegment(sketch, "E1332", {"start": v(25.65, 35.25) * mm, "end": v(24.95, 35.34) * mm});
            skLineSegment(sketch, "E1333", {"start": v(24.95, 35.34) * mm, "end": v(24.2, 35.25) * mm});
            skLineSegment(sketch, "E1334", {"start": v(24.2, 35.25) * mm, "end": v(23.69, 35.18) * mm});
            skLineSegment(sketch, "E1335", {"start": v(23.69, 35.18) * mm, "end": v(23.2, 35.09) * mm});
            skLineSegment(sketch, "E1336", {"start": v(23.2, 35.09) * mm, "end": v(22.72, 34.96) * mm});
            skLineSegment(sketch, "E1337", {"start": v(22.72, 34.96) * mm, "end": v(22.25, 34.81) * mm});
            skLineSegment(sketch, "E1338", {"start": v(22.25, 34.81) * mm, "end": v(21.77, 34.63) * mm});
            skLineSegment(sketch, "E1339", {"start": v(21.77, 34.63) * mm, "end": v(21.28, 34.41) * mm});
            skLineSegment(sketch, "E1340", {"start": v(21.28, 34.41) * mm, "end": v(20.77, 34.15) * mm});
            skLineSegment(sketch, "E1341", {"start": v(20.77, 34.15) * mm, "end": v(20.23, 33.85) * mm});
            skLineSegment(sketch, "E1342", {"start": v(20.23, 33.85) * mm, "end": v(19.37, 33.36) * mm});
            skLineSegment(sketch, "E1343", {"start": v(19.37, 33.36) * mm, "end": v(19.32, 33.6) * mm});
            skLineSegment(sketch, "E1344", {"start": v(19.32, 33.6) * mm, "end": v(19.29, 33.74) * mm});
            skLineSegment(sketch, "E1345", {"start": v(19.29, 33.74) * mm, "end": v(19.24, 33.86) * mm});
            skLineSegment(sketch, "E1346", {"start": v(19.24, 33.86) * mm, "end": v(19.2, 33.97) * mm});
            skLineSegment(sketch, "E1347", {"start": v(19.2, 33.97) * mm, "end": v(19.14, 34.07) * mm});
            skLineSegment(sketch, "E1348", {"start": v(19.14, 34.07) * mm, "end": v(19.08, 34.16) * mm});
            skLineSegment(sketch, "E1349", {"start": v(19.08, 34.16) * mm, "end": v(19.01, 34.24) * mm});
            skLineSegment(sketch, "E1350", {"start": v(19.01, 34.24) * mm, "end": v(18.94, 34.3) * mm});
            skLineSegment(sketch, "E1351", {"start": v(18.94, 34.3) * mm, "end": v(18.87, 34.35) * mm});
            skLineSegment(sketch, "E1352", {"start": v(18.87, 34.35) * mm, "end": v(18.69, 34.45) * mm});
            skLineSegment(sketch, "E1353", {"start": v(18.69, 34.45) * mm, "end": v(18.65, 34.33) * mm});
            skLineSegment(sketch, "E1354", {"start": v(18.65, 34.33) * mm, "end": v(18.6, 34.14) * mm});
            skLineSegment(sketch, "E1355", {"start": v(18.6, 34.14) * mm, "end": v(18.55, 33.85) * mm});
            skLineSegment(sketch, "E1356", {"start": v(18.55, 33.85) * mm, "end": v(18.5, 33.5) * mm});
            skLineSegment(sketch, "E1357", {"start": v(18.5, 33.5) * mm, "end": v(17.9, 32.94) * mm});
            skLineSegment(sketch, "E1358", {"start": v(17.9, 32.94) * mm, "end": v(15.75, 32.06) * mm});
            skLineSegment(sketch, "E1359", {"start": v(15.75, 32.06) * mm, "end": v(15.5, 31.96) * mm});
            skLineSegment(sketch, "E1360", {"start": v(15.5, 31.96) * mm, "end": v(15.54, 32.18) * mm});
            skLineSegment(sketch, "E1361", {"start": v(15.54, 32.18) * mm, "end": v(15.62, 32.44) * mm});
            skLineSegment(sketch, "E1362", {"start": v(15.62, 32.44) * mm, "end": v(15.73, 32.76) * mm});
            skLineSegment(sketch, "E1363", {"start": v(15.73, 32.76) * mm, "end": v(15.87, 33.12) * mm});
            skLineSegment(sketch, "E1364", {"start": v(15.87, 33.12) * mm, "end": v(15.88, 34.12) * mm});
            skLineSegment(sketch, "E1365", {"start": v(15.88, 34.12) * mm, "end": v(15.55, 34.85) * mm});
            skLineSegment(sketch, "E1366", {"start": v(15.55, 34.85) * mm, "end": v(14.78, 35.6) * mm});
            skLineSegment(sketch, "E1367", {"start": v(14.78, 35.6) * mm, "end": v(13.85, 36.07) * mm});
            skLineSegment(sketch, "E1368", {"start": v(13.85, 36.07) * mm, "end": v(12.94, 36.06) * mm});
            skLineSegment(sketch, "E1369", {"start": v(12.94, 36.06) * mm, "end": v(12.2, 35.73) * mm});
            skLineSegment(sketch, "E1370", {"start": v(12.2, 35.73) * mm, "end": v(12, 35.48) * mm});
            skLineSegment(sketch, "E1371", {"start": v(12, 35.48) * mm, "end": v(11.92, 35.36) * mm});
            skLineSegment(sketch, "E1372", {"start": v(11.92, 35.36) * mm, "end": v(11.84, 35.24) * mm});
            skLineSegment(sketch, "E1373", {"start": v(11.84, 35.24) * mm, "end": v(11.78, 35.12) * mm});
            skLineSegment(sketch, "E1374", {"start": v(11.78, 35.12) * mm, "end": v(11.75, 35.02) * mm});
            skLineSegment(sketch, "E1375", {"start": v(11.75, 35.02) * mm, "end": v(11.7, 34.82) * mm});
            skLineSegment(sketch, "E1376", {"start": v(11.7, 34.82) * mm, "end": v(12.02, 34.14) * mm});
            skLineSegment(sketch, "E1377", {"start": v(12.02, 34.14) * mm, "end": v(12.57, 33.8) * mm});
            skLineSegment(sketch, "E1378", {"start": v(12.57, 33.8) * mm, "end": v(13, 33.8) * mm});
            skLineSegment(sketch, "E1379", {"start": v(13, 33.8) * mm, "end": v(13.54, 34.35) * mm});
            skLineSegment(sketch, "E1380", {"start": v(13.54, 34.35) * mm, "end": v(13.48, 34.6) * mm});
            skLineSegment(sketch, "E1381", {"start": v(13.48, 34.6) * mm, "end": v(13.45, 34.7) * mm});
            skLineSegment(sketch, "E1382", {"start": v(13.45, 34.7) * mm, "end": v(13.4, 34.81) * mm});
            skLineSegment(sketch, "E1383", {"start": v(13.4, 34.81) * mm, "end": v(13.35, 34.91) * mm});
            skLineSegment(sketch, "E1384", {"start": v(13.35, 34.91) * mm, "end": v(13.3, 34.99) * mm});
            skLineSegment(sketch, "E1385", {"start": v(13.3, 34.99) * mm, "end": v(13.24, 35.05) * mm});
            skLineSegment(sketch, "E1386", {"start": v(13.24, 35.05) * mm, "end": v(13.2, 35.12) * mm});
            skLineSegment(sketch, "E1387", {"start": v(13.2, 35.12) * mm, "end": v(13.17, 35.2) * mm});
            skLineSegment(sketch, "E1388", {"start": v(13.17, 35.2) * mm, "end": v(13.16, 35.25) * mm});
            skLineSegment(sketch, "E1389", {"start": v(13.16, 35.25) * mm, "end": v(13.16, 35.36) * mm});
            skLineSegment(sketch, "E1390", {"start": v(13.16, 35.36) * mm, "end": v(13.6, 35.3) * mm});
            skLineSegment(sketch, "E1391", {"start": v(13.6, 35.3) * mm, "end": v(13.78, 35.27) * mm});
            skLineSegment(sketch, "E1392", {"start": v(13.78, 35.27) * mm, "end": v(13.98, 35.22) * mm});
            skLineSegment(sketch, "E1393", {"start": v(13.98, 35.22) * mm, "end": v(14.16, 35.17) * mm});
            skLineSegment(sketch, "E1394", {"start": v(14.16, 35.17) * mm, "end": v(14.3, 35.12) * mm});
            skLineSegment(sketch, "E1395", {"start": v(14.3, 35.12) * mm, "end": v(14.58, 35) * mm});
            skLineSegment(sketch, "E1396", {"start": v(14.58, 35) * mm, "end": v(14.97, 34.5) * mm});
            skLineSegment(sketch, "E1397", {"start": v(14.97, 34.5) * mm, "end": v(15.17, 33.76) * mm});
            skLineSegment(sketch, "E1398", {"start": v(15.17, 33.76) * mm, "end": v(15.12, 33.32) * mm});
            skLineSegment(sketch, "E1399", {"start": v(15.12, 33.32) * mm, "end": v(15.08, 33.12) * mm});
            skLineSegment(sketch, "E1400", {"start": v(15.08, 33.12) * mm, "end": v(15.04, 32.93) * mm});
            skLineSegment(sketch, "E1401", {"start": v(15.04, 32.93) * mm, "end": v(14.98, 32.75) * mm});
            skLineSegment(sketch, "E1402", {"start": v(14.98, 32.75) * mm, "end": v(14.93, 32.62) * mm});
            skLineSegment(sketch, "E1403", {"start": v(14.93, 32.62) * mm, "end": v(14.8, 32.36) * mm});
            skLineSegment(sketch, "E1404", {"start": v(14.8, 32.36) * mm, "end": v(14.2, 31.91) * mm});
            skLineSegment(sketch, "E1405", {"start": v(14.2, 31.91) * mm, "end": v(13.8, 31.82) * mm});
            skLineSegment(sketch, "E1406", {"start": v(13.8, 31.82) * mm, "end": v(13.6, 31.78) * mm});
            skLineSegment(sketch, "E1407", {"start": v(13.6, 31.78) * mm, "end": v(13.35, 31.75) * mm});
            skLineSegment(sketch, "E1408", {"start": v(13.35, 31.75) * mm, "end": v(13.1, 31.73) * mm});
            skLineSegment(sketch, "E1409", {"start": v(13.1, 31.73) * mm, "end": v(12.87, 31.72) * mm});
            skLineSegment(sketch, "E1410", {"start": v(12.87, 31.72) * mm, "end": v(12.34, 31.72) * mm});
            skLineSegment(sketch, "E1411", {"start": v(12.34, 31.72) * mm, "end": v(11.72, 31.98) * mm});
            skLineSegment(sketch, "E1412", {"start": v(11.72, 31.98) * mm, "end": v(11.37, 32.55) * mm});
            skLineSegment(sketch, "E1413", {"start": v(11.37, 32.55) * mm, "end": v(11.26, 33.27) * mm});
            skLineSegment(sketch, "E1414", {"start": v(11.26, 33.27) * mm, "end": v(10.7, 32.94) * mm});
            skLineSegment(sketch, "E1415", {"start": v(10.7, 32.94) * mm, "end": v(10.57, 32.7) * mm});
            skLineSegment(sketch, "E1416", {"start": v(10.57, 32.7) * mm, "end": v(10.51, 32.6) * mm});
            skLineSegment(sketch, "E1417", {"start": v(10.51, 32.6) * mm, "end": v(10.46, 32.52) * mm});
            skLineSegment(sketch, "E1418", {"start": v(10.46, 32.52) * mm, "end": v(10.4, 32.46) * mm});
            skLineSegment(sketch, "E1419", {"start": v(10.4, 32.46) * mm, "end": v(10.36, 32.44) * mm});
            skLineSegment(sketch, "E1420", {"start": v(10.36, 32.44) * mm, "end": v(10.3, 32.48) * mm});
            skLineSegment(sketch, "E1421", {"start": v(10.3, 32.48) * mm, "end": v(10.19, 32.57) * mm});
            skLineSegment(sketch, "E1422", {"start": v(10.19, 32.57) * mm, "end": v(10.04, 32.72) * mm});
            skLineSegment(sketch, "E1423", {"start": v(10.04, 32.72) * mm, "end": v(9.87, 32.89) * mm});
            skLineSegment(sketch, "E1424", {"start": v(9.87, 32.89) * mm, "end": v(9.46, 33.33) * mm});
            skLineSegment(sketch, "E1425", {"start": v(9.46, 33.33) * mm, "end": v(9.18, 34) * mm});
            skLineSegment(sketch, "E1426", {"start": v(9.18, 34) * mm, "end": v(9.18, 35.07) * mm});
            skLineSegment(sketch, "E1427", {"start": v(9.18, 35.07) * mm, "end": v(9.57, 36.11) * mm});
            skLineSegment(sketch, "E1428", {"start": v(9.57, 36.11) * mm, "end": v(10.15, 36.7) * mm});
            skLineSegment(sketch, "E1429", {"start": v(10.15, 36.7) * mm, "end": v(11, 36.7) * mm});
            skLineSegment(sketch, "E1430", {"start": v(11, 36.7) * mm, "end": v(11.56, 36.41) * mm});
            skLineSegment(sketch, "E1431", {"start": v(11.56, 36.41) * mm, "end": v(11.45, 37.33) * mm});
            skLineSegment(sketch, "E1432", {"start": v(11.45, 37.33) * mm, "end": v(11.17, 37.86) * mm});
            skLineSegment(sketch, "E1433", {"start": v(11.17, 37.86) * mm, "end": v(10.5, 38.28) * mm});
            skLineSegment(sketch, "E1434", {"start": v(10.5, 38.28) * mm, "end": v(11.49, 39.17) * mm});
            skLineSegment(sketch, "E1435", {"start": v(11.49, 39.17) * mm, "end": v(12.48, 39.65) * mm});
            skLineSegment(sketch, "E1436", {"start": v(12.48, 39.65) * mm, "end": v(14.2, 39.65) * mm});
            skLineSegment(sketch, "E1437", {"start": v(14.2, 39.65) * mm, "end": v(14.66, 39.44) * mm});
            skLineSegment(sketch, "E1438", {"start": v(14.66, 39.44) * mm, "end": v(14.86, 39.34) * mm});
            skLineSegment(sketch, "E1439", {"start": v(14.86, 39.34) * mm, "end": v(15.04, 39.23) * mm});
            skLineSegment(sketch, "E1440", {"start": v(15.04, 39.23) * mm, "end": v(15.2, 39.12) * mm});
            skLineSegment(sketch, "E1441", {"start": v(15.2, 39.12) * mm, "end": v(15.35, 39) * mm});
            skLineSegment(sketch, "E1442", {"start": v(15.35, 39) * mm, "end": v(15.48, 38.86) * mm});
            skLineSegment(sketch, "E1443", {"start": v(15.48, 38.86) * mm, "end": v(15.6, 38.72) * mm});
            skLineSegment(sketch, "E1444", {"start": v(15.6, 38.72) * mm, "end": v(15.71, 38.56) * mm});
            skLineSegment(sketch, "E1445", {"start": v(15.71, 38.56) * mm, "end": v(15.8, 38.39) * mm});
            skLineSegment(sketch, "E1446", {"start": v(15.8, 38.39) * mm, "end": v(16, 38.03) * mm});
            skLineSegment(sketch, "E1447", {"start": v(16, 38.03) * mm, "end": v(15.93, 36.6) * mm});
            skLineSegment(sketch, "E1448", {"start": v(15.93, 36.6) * mm, "end": v(16.15, 36.66) * mm});
            skLineSegment(sketch, "E1449", {"start": v(16.15, 36.66) * mm, "end": v(16.27, 36.7) * mm});
            skLineSegment(sketch, "E1450", {"start": v(16.27, 36.7) * mm, "end": v(16.43, 36.77) * mm});
            skLineSegment(sketch, "E1451", {"start": v(16.43, 36.77) * mm, "end": v(16.6, 36.86) * mm});
            skLineSegment(sketch, "E1452", {"start": v(16.6, 36.86) * mm, "end": v(16.78, 36.96) * mm});
            skLineSegment(sketch, "E1453", {"start": v(16.78, 36.96) * mm, "end": v(17.19, 37.2) * mm});
            skLineSegment(sketch, "E1454", {"start": v(17.19, 37.2) * mm, "end": v(17.64, 38.08) * mm});
            skLineSegment(sketch, "E1455", {"start": v(17.64, 38.08) * mm, "end": v(17.76, 37.92) * mm});
            skLineSegment(sketch, "E1456", {"start": v(17.76, 37.92) * mm, "end": v(17.82, 37.82) * mm});
            skLineSegment(sketch, "E1457", {"start": v(17.82, 37.82) * mm, "end": v(17.9, 37.66) * mm});
            skLineSegment(sketch, "E1458", {"start": v(17.9, 37.66) * mm, "end": v(17.99, 37.46) * mm});
            skLineSegment(sketch, "E1459", {"start": v(17.99, 37.46) * mm, "end": v(18.07, 37.25) * mm});
            skLineSegment(sketch, "E1460", {"start": v(18.07, 37.25) * mm, "end": v(18.26, 36.75) * mm});
            skLineSegment(sketch, "E1461", {"start": v(18.26, 36.75) * mm, "end": v(18.28, 35.16) * mm});
            skLineSegment(sketch, "E1462", {"start": v(18.28, 35.16) * mm, "end": v(18.6, 35.16) * mm});
            skLineSegment(sketch, "E1463", {"start": v(18.6, 35.16) * mm, "end": v(19.24, 35.73) * mm});
            skLineSegment(sketch, "E1464", {"start": v(19.24, 35.73) * mm, "end": v(19.38, 36.24) * mm});
            skLineSegment(sketch, "E1465", {"start": v(19.38, 36.24) * mm, "end": v(19.5, 36.6) * mm});
            skLineSegment(sketch, "E1466", {"start": v(19.5, 36.6) * mm, "end": v(19.56, 36.79) * mm});
            skLineSegment(sketch, "E1467", {"start": v(19.56, 36.79) * mm, "end": v(19.58, 36.78) * mm});
            skLineSegment(sketch, "E1468", {"start": v(19.58, 36.78) * mm, "end": v(19.6, 36.77) * mm});
            skLineSegment(sketch, "E1469", {"start": v(19.6, 36.77) * mm, "end": v(19.7, 36.69) * mm});
            skLineSegment(sketch, "E1470", {"start": v(19.7, 36.69) * mm, "end": v(19.82, 36.56) * mm});
            skLineSegment(sketch, "E1471", {"start": v(19.82, 36.56) * mm, "end": v(19.97, 36.4) * mm});
            skLineSegment(sketch, "E1472", {"start": v(19.97, 36.4) * mm, "end": v(20.34, 35.97) * mm});
            skLineSegment(sketch, "E1473", {"start": v(20.34, 35.97) * mm, "end": v(20.85, 35.7) * mm});
            skLineSegment(sketch, "E1474", {"start": v(20.85, 35.7) * mm, "end": v(20.91, 36.23) * mm});
            skLineSegment(sketch, "E1475", {"start": v(20.91, 36.23) * mm, "end": v(20.96, 36.63) * mm});
            skLineSegment(sketch, "E1476", {"start": v(20.96, 36.63) * mm, "end": v(21, 36.87) * mm});
            skLineSegment(sketch, "E1477", {"start": v(21, 36.87) * mm, "end": v(21.05, 36.99) * mm});
            skLineSegment(sketch, "E1478", {"start": v(21.05, 36.99) * mm, "end": v(21.48, 36.76) * mm});
            skLineSegment(sketch, "E1479", {"start": v(21.48, 36.76) * mm, "end": v(21.67, 36.66) * mm});
            skLineSegment(sketch, "E1480", {"start": v(21.67, 36.66) * mm, "end": v(21.89, 36.57) * mm});
            skLineSegment(sketch, "E1481", {"start": v(21.89, 36.57) * mm, "end": v(22.1, 36.5) * mm});
            skLineSegment(sketch, "E1482", {"start": v(22.1, 36.5) * mm, "end": v(22.27, 36.44) * mm});
            skLineSegment(sketch, "E1483", {"start": v(22.27, 36.44) * mm, "end": v(22.63, 36.36) * mm});
            skLineSegment(sketch, "E1484", {"start": v(22.63, 36.36) * mm, "end": v(30.22, 36.48) * mm});
            skLineSegment(sketch, "E1485", {"start": v(30.22, 36.48) * mm, "end": v(30.26, 36.41) * mm});
            skLineSegment(sketch, "E1486", {"start": v(30.26, 36.41) * mm, "end": v(30.26, 36.39) * mm});
            skLineSegment(sketch, "E1487", {"start": v(30.26, 36.39) * mm, "end": v(30.26, 36.35) * mm});
            skLineSegment(sketch, "E1488", {"start": v(30.26, 36.35) * mm, "end": v(30.23, 36.2) * mm});
            skLineSegment(sketch, "E1489", {"start": v(30.23, 36.2) * mm, "end": v(30.18, 36.02) * mm});
            skLineSegment(sketch, "E1490", {"start": v(30.18, 36.02) * mm, "end": v(30.11, 35.8) * mm});
            skLineSegment(sketch, "E1491", {"start": v(30.11, 35.8) * mm, "end": v(30.03, 35.54) * mm});
            skLineSegment(sketch, "E1492", {"start": v(30.03, 35.54) * mm, "end": v(29.95, 35.22) * mm});
            skLineSegment(sketch, "E1493", {"start": v(29.95, 35.22) * mm, "end": v(29.88, 34.88) * mm});
            skLineSegment(sketch, "E1494", {"start": v(29.88, 34.88) * mm, "end": v(29.83, 34.57) * mm});
            skLineSegment(sketch, "E1495", {"start": v(29.83, 34.57) * mm, "end": v(29.74, 33.9) * mm});
            skLineSegment(sketch, "E1496", {"start": v(29.74, 33.9) * mm, "end": v(29.93, 32.86) * mm});
            skLineSegment(sketch, "E1497", {"start": v(29.93, 32.86) * mm, "end": v(30.2, 32.27) * mm});
            skLineSegment(sketch, "E1498", {"start": v(30.2, 32.27) * mm, "end": v(30.33, 32) * mm});
            skLineSegment(sketch, "E1499", {"start": v(30.33, 32) * mm, "end": v(30.47, 31.75) * mm});
            skLineSegment(sketch, "E1500", {"start": v(30.47, 31.75) * mm, "end": v(30.6, 31.5) * mm});
            skLineSegment(sketch, "E1501", {"start": v(30.6, 31.5) * mm, "end": v(30.72, 31.33) * mm});
            skLineSegment(sketch, "E1502", {"start": v(30.72, 31.33) * mm, "end": v(30.96, 30.98) * mm});
            skLineSegment(sketch, "E1503", {"start": v(30.96, 30.98) * mm, "end": v(31.76, 30.51) * mm});
            skLineSegment(sketch, "E1504", {"start": v(31.76, 30.51) * mm, "end": v(32.7, 30.52) * mm});
            skLineSegment(sketch, "E1505", {"start": v(32.7, 30.52) * mm, "end": v(33.37, 30.8) * mm});
            skLineSegment(sketch, "E1506", {"start": v(33.37, 30.8) * mm, "end": v(33.73, 31.4) * mm});
            skLineSegment(sketch, "E1507", {"start": v(33.73, 31.4) * mm, "end": v(33.73, 31.64) * mm});
            skLineSegment(sketch, "E1508", {"start": v(33.73, 31.64) * mm, "end": v(33.73, 31.78) * mm});
            skLineSegment(sketch, "E1509", {"start": v(33.73, 31.78) * mm, "end": v(33.7, 31.9) * mm});
            skLineSegment(sketch, "E1510", {"start": v(33.7, 31.9) * mm, "end": v(33.67, 32.04) * mm});
            skLineSegment(sketch, "E1511", {"start": v(33.67, 32.04) * mm, "end": v(33.62, 32.17) * mm});
            skLineSegment(sketch, "E1512", {"start": v(33.62, 32.17) * mm, "end": v(33.56, 32.3) * mm});
            skLineSegment(sketch, "E1513", {"start": v(33.56, 32.3) * mm, "end": v(33.49, 32.42) * mm});
            skLineSegment(sketch, "E1514", {"start": v(33.49, 32.42) * mm, "end": v(33.4, 32.54) * mm});
            skLineSegment(sketch, "E1515", {"start": v(33.4, 32.54) * mm, "end": v(33.3, 32.65) * mm});
            skLineSegment(sketch, "E1516", {"start": v(33.3, 32.65) * mm, "end": v(33.07, 32.9) * mm});
            skLineSegment(sketch, "E1517", {"start": v(33.07, 32.9) * mm, "end": v(32.38, 32.9) * mm});
            skLineSegment(sketch, "E1518", {"start": v(32.38, 32.9) * mm, "end": v(32.38, 32.82) * mm});
            skLineSegment(sketch, "E1519", {"start": v(32.38, 32.82) * mm, "end": v(32.4, 32.78) * mm});
            skLineSegment(sketch, "E1520", {"start": v(32.4, 32.78) * mm, "end": v(32.46, 32.71) * mm});
            skLineSegment(sketch, "E1521", {"start": v(32.46, 32.71) * mm, "end": v(32.54, 32.63) * mm});
            skLineSegment(sketch, "E1522", {"start": v(32.54, 32.63) * mm, "end": v(32.65, 32.55) * mm});
            skLineSegment(sketch, "E1523", {"start": v(32.65, 32.55) * mm, "end": v(32.92, 32.35) * mm});
            skLineSegment(sketch, "E1524", {"start": v(32.92, 32.35) * mm, "end": v(33.02, 31.92) * mm});
            skLineSegment(sketch, "E1525", {"start": v(33.02, 31.92) * mm, "end": v(32.73, 31.35) * mm});
            skLineSegment(sketch, "E1526", {"start": v(32.73, 31.35) * mm, "end": v(32.25, 31.17) * mm});
            skLineSegment(sketch, "E1527", {"start": v(32.25, 31.17) * mm, "end": v(31.76, 31.28) * mm});
            skLineSegment(sketch, "E1528", {"start": v(31.76, 31.28) * mm, "end": v(31.11, 31.92) * mm});
            skLineSegment(sketch, "E1529", {"start": v(31.11, 31.92) * mm, "end": v(30.53, 33.3) * mm});
            skLineSegment(sketch, "E1530", {"start": v(30.53, 33.3) * mm, "end": v(30.46, 34.85) * mm});
            skLineSegment(sketch, "E1531", {"start": v(30.46, 34.85) * mm, "end": v(30.85, 35.9) * mm});
            skLineSegment(sketch, "E1532", {"start": v(30.85, 35.9) * mm, "end": v(31.64, 36.93) * mm});
            skLineSegment(sketch, "E1533", {"start": v(31.64, 36.93) * mm, "end": v(27.26, 37.02) * mm});
            skLineSegment(sketch, "E1534", {"start": v(27.26, 37.02) * mm, "end": v(27.03, 37.47) * mm});
            skLineSegment(sketch, "E1535", {"start": v(27.03, 37.47) * mm, "end": v(27.03, 38.84) * mm});
            skLineSegment(sketch, "E1536", {"start": v(27.03, 38.84) * mm, "end": v(27.44, 39.65) * mm});
            skLineSegment(sketch, "E1537", {"start": v(27.44, 39.65) * mm, "end": v(28.21, 39.92) * mm});
            skLineSegment(sketch, "E1538", {"start": v(28.21, 39.92) * mm, "end": v(28.7, 39.64) * mm});
            skLineSegment(sketch, "E1539", {"start": v(28.7, 39.64) * mm, "end": v(28.76, 39.14) * mm});
            skLineSegment(sketch, "E1540", {"start": v(28.76, 39.14) * mm, "end": v(28.55, 38.88) * mm});
            skLineSegment(sketch, "E1541", {"start": v(28.55, 38.88) * mm, "end": v(28.12, 38.88) * mm});
            skLineSegment(sketch, "E1542", {"start": v(28.12, 38.88) * mm, "end": v(28.12, 38.8) * mm});
            skLineSegment(sketch, "E1543", {"start": v(28.12, 38.8) * mm, "end": v(28.13, 38.76) * mm});
            skLineSegment(sketch, "E1544", {"start": v(28.13, 38.76) * mm, "end": v(28.16, 38.7) * mm});
            skLineSegment(sketch, "E1545", {"start": v(28.16, 38.7) * mm, "end": v(28.22, 38.64) * mm});
            skLineSegment(sketch, "E1546", {"start": v(28.22, 38.64) * mm, "end": v(28.28, 38.57) * mm});
            skLineSegment(sketch, "E1547", {"start": v(28.28, 38.57) * mm, "end": v(28.45, 38.43) * mm});
            skLineSegment(sketch, "E1548", {"start": v(28.45, 38.43) * mm, "end": v(28.92, 38.43) * mm});
            skLineSegment(sketch, "E1549", {"start": v(28.92, 38.43) * mm, "end": v(29.48, 38.9) * mm});
            skLineSegment(sketch, "E1550", {"start": v(29.48, 38.9) * mm, "end": v(29.47, 39.56) * mm});
            skLineSegment(sketch, "E1551", {"start": v(29.47, 39.56) * mm, "end": v(29.11, 40.15) * mm});
            skLineSegment(sketch, "E1552", {"start": v(29.11, 40.15) * mm, "end": v(28.52, 40.5) * mm});
            skLineSegment(sketch, "E1553", {"start": v(28.52, 40.5) * mm, "end": v(28.07, 40.5) * mm});
            skLineSegment(sketch, "E1554", {"start": v(28.07, 40.5) * mm, "end": v(27.68, 40.33) * mm});
            skLineSegment(sketch, "E1555", {"start": v(27.68, 40.33) * mm, "end": v(27.39, 40.2) * mm});
            skLineSegment(sketch, "E1556", {"start": v(27.39, 40.2) * mm, "end": v(27.25, 40.15) * mm});
            skLineSegment(sketch, "E1557", {"start": v(27.25, 40.15) * mm, "end": v(27.24, 40.22) * mm});
            skLineSegment(sketch, "E1558", {"start": v(27.24, 40.22) * mm, "end": v(27.22, 40.4) * mm});
            skLineSegment(sketch, "E1559", {"start": v(27.22, 40.4) * mm, "end": v(27.2, 41.03) * mm});
            skLineSegment(sketch, "E1560", {"start": v(27.2, 41.03) * mm, "end": v(27.16, 41.91) * mm});
            skLineSegment(sketch, "E1561", {"start": v(27.16, 41.91) * mm, "end": v(26.85, 42.62) * mm});
            skLineSegment(sketch, "E1562", {"start": v(26.85, 42.62) * mm, "end": v(26.73, 42.52) * mm});
            skLineSegment(sketch, "E1563", {"start": v(26.73, 42.52) * mm, "end": v(26.67, 42.45) * mm});
            skLineSegment(sketch, "E1564", {"start": v(26.67, 42.45) * mm, "end": v(26.6, 42.33) * mm});
            skLineSegment(sketch, "E1565", {"start": v(26.6, 42.33) * mm, "end": v(26.54, 42.19) * mm});
            skLineSegment(sketch, "E1566", {"start": v(26.54, 42.19) * mm, "end": v(26.48, 42.03) * mm});
            skLineSegment(sketch, "E1567", {"start": v(26.48, 42.03) * mm, "end": v(26.36, 41.64) * mm});
            skLineSegment(sketch, "E1568", {"start": v(26.36, 41.64) * mm, "end": v(26.33, 40.2) * mm});
            skLineSegment(sketch, "E1569", {"start": v(26.33, 40.2) * mm, "end": v(26.25, 40.21) * mm});
            skLineSegment(sketch, "E1570", {"start": v(26.25, 40.21) * mm, "end": v(25.76, 40.38) * mm});
            skLineSegment(sketch, "E1571", {"start": v(25.76, 40.38) * mm, "end": v(25.36, 40.52) * mm});
            skLineSegment(sketch, "E1572", {"start": v(25.36, 40.52) * mm, "end": v(24.78, 40.41) * mm});
            skLineSegment(sketch, "E1573", {"start": v(24.78, 40.41) * mm, "end": v(24.15, 39.71) * mm});
            skLineSegment(sketch, "E1574", {"start": v(24.15, 39.71) * mm, "end": v(24.03, 39.16) * mm});
            skLineSegment(sketch, "E1575", {"start": v(24.03, 39.16) * mm, "end": v(24.32, 38.6) * mm});
            skLineSegment(sketch, "E1576", {"start": v(24.32, 38.6) * mm, "end": v(24.55, 38.51) * mm});
            skLineSegment(sketch, "E1577", {"start": v(24.55, 38.51) * mm, "end": v(24.65, 38.48) * mm});
            skLineSegment(sketch, "E1578", {"start": v(24.65, 38.48) * mm, "end": v(24.77, 38.45) * mm});
            skLineSegment(sketch, "E1579", {"start": v(24.77, 38.45) * mm, "end": v(24.89, 38.43) * mm});
            skLineSegment(sketch, "E1580", {"start": v(24.89, 38.43) * mm, "end": v(25, 38.43) * mm});
            skLineSegment(sketch, "E1581", {"start": v(25, 38.43) * mm, "end": v(25.2, 38.43) * mm});
            skLineSegment(sketch, "E1582", {"start": v(25.2, 38.43) * mm, "end": v(25.5, 38.83) * mm});
            skLineSegment(sketch, "E1583", {"start": v(25.5, 38.83) * mm, "end": v(24.99, 38.89) * mm});
            skLineSegment(sketch, "E1584", {"start": v(24.99, 38.89) * mm, "end": v(24.88, 39.04) * mm});
            skLineSegment(sketch, "E1585", {"start": v(24.88, 39.04) * mm, "end": v(24.82, 39.12) * mm});
            skLineSegment(sketch, "E1586", {"start": v(24.82, 39.12) * mm, "end": v(24.79, 39.19) * mm});
            skLineSegment(sketch, "E1587", {"start": v(24.79, 39.19) * mm, "end": v(24.77, 39.26) * mm});
            skLineSegment(sketch, "E1588", {"start": v(24.77, 39.26) * mm, "end": v(24.78, 39.33) * mm});
            skLineSegment(sketch, "E1589", {"start": v(24.78, 39.33) * mm, "end": v(24.8, 39.4) * mm});
            skLineSegment(sketch, "E1590", {"start": v(24.8, 39.4) * mm, "end": v(24.84, 39.48) * mm});
            skLineSegment(sketch, "E1591", {"start": v(24.84, 39.48) * mm, "end": v(24.9, 39.56) * mm});
            skLineSegment(sketch, "E1592", {"start": v(24.9, 39.56) * mm, "end": v(24.99, 39.65) * mm});
            skLineSegment(sketch, "E1593", {"start": v(24.99, 39.65) * mm, "end": v(25.2, 39.88) * mm});
            skLineSegment(sketch, "E1594", {"start": v(25.2, 39.88) * mm, "end": v(25.4, 39.88) * mm});
            skLineSegment(sketch, "E1595", {"start": v(25.4, 39.88) * mm, "end": v(25.5, 39.86) * mm});
            skLineSegment(sketch, "E1596", {"start": v(25.5, 39.86) * mm, "end": v(25.63, 39.83) * mm});
            skLineSegment(sketch, "E1597", {"start": v(25.63, 39.83) * mm, "end": v(25.77, 39.78) * mm});
            skLineSegment(sketch, "E1598", {"start": v(25.77, 39.78) * mm, "end": v(25.9, 39.73) * mm});
            skLineSegment(sketch, "E1599", {"start": v(25.9, 39.73) * mm, "end": v(26.22, 39.58) * mm});
            skLineSegment(sketch, "E1600", {"start": v(26.22, 39.58) * mm, "end": v(26.5, 39.03) * mm});
            skLineSegment(sketch, "E1601", {"start": v(26.5, 39.03) * mm, "end": v(26.6, 37.55) * mm});
            skLineSegment(sketch, "E1602", {"start": v(26.6, 37.55) * mm, "end": v(26.3, 36.98) * mm});
            skLineSegment(sketch, "E1603", {"start": v(26.3, 36.98) * mm, "end": v(23.13, 36.98) * mm});
            skLineSegment(sketch, "E1604", {"start": v(23.13, 36.98) * mm, "end": v(23.13, 37.02) * mm});
            skLineSegment(sketch, "E1605", {"start": v(23.13, 37.02) * mm, "end": v(23.19, 37.14) * mm});
            skLineSegment(sketch, "E1606", {"start": v(23.19, 37.14) * mm, "end": v(23.32, 37.38) * mm});
            skLineSegment(sketch, "E1607", {"start": v(23.32, 37.38) * mm, "end": v(23.52, 37.7) * mm});
            skLineSegment(sketch, "E1608", {"start": v(23.52, 37.7) * mm, "end": v(23.4, 37.82) * mm});
            skLineSegment(sketch, "E1609", {"start": v(23.4, 37.82) * mm, "end": v(22.94, 37.6) * mm});
            skLineSegment(sketch, "E1610", {"start": v(22.94, 37.6) * mm, "end": v(22.31, 37.6) * mm});
            skLineSegment(sketch, "E1611", {"start": v(22.31, 37.6) * mm, "end": v(21.27, 38.14) * mm});
            skLineSegment(sketch, "E1612", {"start": v(21.27, 38.14) * mm, "end": v(20.77, 38.57) * mm});
            skLineSegment(sketch, "E1613", {"start": v(20.77, 38.57) * mm, "end": v(20.24, 39.05) * mm});
            skLineSegment(sketch, "E1614", {"start": v(20.24, 39.05) * mm, "end": v(19.67, 39.58) * mm});
            skLineSegment(sketch, "E1615", {"start": v(19.67, 39.58) * mm, "end": v(19.05, 40.14) * mm});
            skLineSegment(sketch, "E1616", {"start": v(19.05, 40.14) * mm, "end": v(18.6, 40.37) * mm});
            skLineSegment(sketch, "E1617", {"start": v(18.6, 40.37) * mm, "end": v(18.4, 40.47) * mm});
            skLineSegment(sketch, "E1618", {"start": v(18.4, 40.47) * mm, "end": v(18.13, 40.57) * mm});
            skLineSegment(sketch, "E1619", {"start": v(18.13, 40.57) * mm, "end": v(17.86, 40.67) * mm});
            skLineSegment(sketch, "E1620", {"start": v(17.86, 40.67) * mm, "end": v(17.6, 40.75) * mm});
            skLineSegment(sketch, "E1621", {"start": v(17.6, 40.75) * mm, "end": v(17.06, 40.9) * mm});
            skLineSegment(sketch, "E1622", {"start": v(17.06, 40.9) * mm, "end": v(17.51, 41.38) * mm});
            skLineSegment(sketch, "E1623", {"start": v(17.51, 41.38) * mm, "end": v(17.51, 42.13) * mm});
            skLineSegment(sketch, "E1624", {"start": v(17.51, 42.13) * mm, "end": v(17.37, 42.22) * mm});
            skLineSegment(sketch, "E1625", {"start": v(17.37, 42.22) * mm, "end": v(17.05, 41.69) * mm});
            skLineSegment(sketch, "E1626", {"start": v(17.05, 41.69) * mm, "end": v(16.5, 41.4) * mm});
            skLineSegment(sketch, "E1627", {"start": v(16.5, 41.4) * mm, "end": v(15.11, 41.52) * mm});
            skLineSegment(sketch, "E1628", {"start": v(15.11, 41.52) * mm, "end": v(12.93, 41.33) * mm});
            skLineSegment(sketch, "E1629", {"start": v(12.93, 41.33) * mm, "end": v(12.34, 41.2) * mm});
            skLineSegment(sketch, "E1630", {"start": v(12.34, 41.2) * mm, "end": v(12.46, 42.32) * mm});
            skLineSegment(sketch, "E1631", {"start": v(12.46, 42.32) * mm, "end": v(12.17, 43.1) * mm});
            skLineSegment(sketch, "E1632", {"start": v(12.17, 43.1) * mm, "end": v(11.51, 43.54) * mm});
            skLineSegment(sketch, "E1633", {"start": v(11.51, 43.54) * mm, "end": v(10.39, 43.6) * mm});
            skLineSegment(sketch, "E1634", {"start": v(10.39, 43.6) * mm, "end": v(9.83, 43.06) * mm});
            skLineSegment(sketch, "E1635", {"start": v(9.83, 43.06) * mm, "end": v(9.72, 42.46) * mm});
            skLineSegment(sketch, "E1636", {"start": v(9.72, 42.46) * mm, "end": v(10.06, 42) * mm});
            skLineSegment(sketch, "E1637", {"start": v(10.06, 42) * mm, "end": v(10.84, 42) * mm});
            skLineSegment(sketch, "E1638", {"start": v(10.84, 42) * mm, "end": v(10.97, 42.37) * mm});
            skLineSegment(sketch, "E1639", {"start": v(10.97, 42.37) * mm, "end": v(11.14, 42.86) * mm});
            skLineSegment(sketch, "E1640", {"start": v(11.14, 42.86) * mm, "end": v(11.17, 42.98) * mm});
            skLineSegment(sketch, "E1641", {"start": v(11.17, 42.98) * mm, "end": v(11.4, 42.77) * mm});
            skLineSegment(sketch, "E1642", {"start": v(11.4, 42.77) * mm, "end": v(11.5, 42.67) * mm});
            skLineSegment(sketch, "E1643", {"start": v(11.5, 42.67) * mm, "end": v(11.6, 42.55) * mm});
            skLineSegment(sketch, "E1644", {"start": v(11.6, 42.55) * mm, "end": v(11.67, 42.44) * mm});
            skLineSegment(sketch, "E1645", {"start": v(11.67, 42.44) * mm, "end": v(11.72, 42.35) * mm});
            skLineSegment(sketch, "E1646", {"start": v(11.72, 42.35) * mm, "end": v(11.8, 42.15) * mm});
            skLineSegment(sketch, "E1647", {"start": v(11.8, 42.15) * mm, "end": v(11.55, 41.32) * mm});
            skLineSegment(sketch, "E1648", {"start": v(11.55, 41.32) * mm, "end": v(11.07, 40.69) * mm});
            skLineSegment(sketch, "E1649", {"start": v(11.07, 40.69) * mm, "end": v(10.36, 40.33) * mm});
            skLineSegment(sketch, "E1650", {"start": v(10.36, 40.33) * mm, "end": v(9.35, 40.33) * mm});
            skLineSegment(sketch, "E1651", {"start": v(9.35, 40.33) * mm, "end": v(8.84, 40.5) * mm});
            skLineSegment(sketch, "E1652", {"start": v(8.84, 40.5) * mm, "end": v(8.63, 40.59) * mm});
            skLineSegment(sketch, "E1653", {"start": v(8.63, 40.59) * mm, "end": v(8.45, 40.66) * mm});
            skLineSegment(sketch, "E1654", {"start": v(8.45, 40.66) * mm, "end": v(8.31, 40.73) * mm});
            skLineSegment(sketch, "E1655", {"start": v(8.31, 40.73) * mm, "end": v(8.24, 40.77) * mm});
            skLineSegment(sketch, "E1656", {"start": v(8.24, 40.77) * mm, "end": v(8.16, 40.86) * mm});
            skLineSegment(sketch, "E1657", {"start": v(8.16, 40.86) * mm, "end": v(8.54, 41.35) * mm});
            skLineSegment(sketch, "E1658", {"start": v(8.54, 41.35) * mm, "end": v(8.54, 41.54) * mm});
            skLineSegment(sketch, "E1659", {"start": v(8.54, 41.54) * mm, "end": v(8.53, 41.62) * mm});
            skLineSegment(sketch, "E1660", {"start": v(8.53, 41.62) * mm, "end": v(8.52, 41.71) * mm});
            skLineSegment(sketch, "E1661", {"start": v(8.52, 41.71) * mm, "end": v(8.5, 41.79) * mm});
            skLineSegment(sketch, "E1662", {"start": v(8.5, 41.79) * mm, "end": v(8.46, 41.85) * mm});
            skLineSegment(sketch, "E1663", {"start": v(8.46, 41.85) * mm, "end": v(8.39, 41.97) * mm});
            skLineSegment(sketch, "E1664", {"start": v(8.39, 41.97) * mm, "end": v(7.66, 41.23) * mm});
            skLineSegment(sketch, "E1665", {"start": v(7.66, 41.23) * mm, "end": v(6.68, 41.23) * mm});
            skLineSegment(sketch, "E1666", {"start": v(6.68, 41.23) * mm, "end": v(5.7, 41.73) * mm});
            skLineSegment(sketch, "E1667", {"start": v(5.7, 41.73) * mm, "end": v(5.35, 42.41) * mm});
            skLineSegment(sketch, "E1668", {"start": v(5.35, 42.41) * mm, "end": v(5.45, 42.68) * mm});
            skLineSegment(sketch, "E1669", {"start": v(5.45, 42.68) * mm, "end": v(5.81, 42.68) * mm});
            skLineSegment(sketch, "E1670", {"start": v(5.81, 42.68) * mm, "end": v(5.97, 42.69) * mm});
            skLineSegment(sketch, "E1671", {"start": v(5.97, 42.69) * mm, "end": v(6.1, 42.7) * mm});
            skLineSegment(sketch, "E1672", {"start": v(6.1, 42.7) * mm, "end": v(6.21, 42.72) * mm});
            skLineSegment(sketch, "E1673", {"start": v(6.21, 42.72) * mm, "end": v(6.3, 42.74) * mm});
            skLineSegment(sketch, "E1674", {"start": v(6.3, 42.74) * mm, "end": v(6.39, 42.78) * mm});
            skLineSegment(sketch, "E1675", {"start": v(6.39, 42.78) * mm, "end": v(6.45, 42.83) * mm});
            skLineSegment(sketch, "E1676", {"start": v(6.45, 42.83) * mm, "end": v(6.5, 42.9) * mm});
            skLineSegment(sketch, "E1677", {"start": v(6.5, 42.9) * mm, "end": v(6.55, 42.96) * mm});
            skLineSegment(sketch, "E1678", {"start": v(6.55, 42.96) * mm, "end": v(6.64, 43.13) * mm});
            skLineSegment(sketch, "E1679", {"start": v(6.64, 43.13) * mm, "end": v(6.38, 43.76) * mm});
            skLineSegment(sketch, "E1680", {"start": v(6.38, 43.76) * mm, "end": v(5.9, 44.07) * mm});
            skLineSegment(sketch, "E1681", {"start": v(5.9, 44.07) * mm, "end": v(5.28, 43.97) * mm});
            skLineSegment(sketch, "E1682", {"start": v(5.28, 43.97) * mm, "end": v(4.64, 43.47) * mm});
            skLineSegment(sketch, "E1683", {"start": v(4.64, 43.47) * mm, "end": v(4.83, 43.96) * mm});
            skLineSegment(sketch, "E1684", {"start": v(4.83, 43.96) * mm, "end": v(4.94, 44.25) * mm});
            skLineSegment(sketch, "E1685", {"start": v(4.94, 44.25) * mm, "end": v(5.04, 44.54) * mm});
            skLineSegment(sketch, "E1686", {"start": v(5.04, 44.54) * mm, "end": v(5.14, 44.84) * mm});
            skLineSegment(sketch, "E1687", {"start": v(5.14, 44.84) * mm, "end": v(5.23, 45.15) * mm});
            skLineSegment(sketch, "E1688", {"start": v(5.23, 45.15) * mm, "end": v(5.3, 45.46) * mm});
            skLineSegment(sketch, "E1689", {"start": v(5.3, 45.46) * mm, "end": v(5.38, 45.79) * mm});
            skLineSegment(sketch, "E1690", {"start": v(5.38, 45.79) * mm, "end": v(5.45, 46.11) * mm});
            skLineSegment(sketch, "E1691", {"start": v(5.45, 46.11) * mm, "end": v(5.5, 46.45) * mm});
            skLineSegment(sketch, "E1692", {"start": v(5.5, 46.45) * mm, "end": v(5.64, 47.26) * mm});
            skLineSegment(sketch, "E1693", {"start": v(5.64, 47.26) * mm, "end": v(5.64, 49.66) * mm});
            skLineSegment(sketch, "E1694", {"start": v(5.64, 49.66) * mm, "end": v(5.6, 49.66) * mm});
            skLineSegment(sketch, "E1695", {"start": v(5.6, 49.66) * mm, "end": v(5.54, 49.63) * mm});
            skLineSegment(sketch, "E1696", {"start": v(5.54, 49.63) * mm, "end": v(5.39, 49.53) * mm});
            skLineSegment(sketch, "E1697", {"start": v(5.39, 49.53) * mm, "end": v(4.92, 49.22) * mm});
            skLineSegment(sketch, "E1698", {"start": v(4.92, 49.22) * mm, "end": v(4.28, 48.78) * mm});
            skLineSegment(sketch, "E1699", {"start": v(4.28, 48.78) * mm, "end": v(3, 48.37) * mm});
            skLineSegment(sketch, "E1700", {"start": v(3, 48.37) * mm, "end": v(1.9, 48.48) * mm});
            skLineSegment(sketch, "E1701", {"start": v(1.9, 48.48) * mm, "end": v(1.53, 48.65) * mm});
            skLineSegment(sketch, "E1702", {"start": v(1.53, 48.65) * mm, "end": v(1.36, 48.73) * mm});
            skLineSegment(sketch, "E1703", {"start": v(1.36, 48.73) * mm, "end": v(1.2, 48.82) * mm});
            skLineSegment(sketch, "E1704", {"start": v(1.2, 48.82) * mm, "end": v(1.06, 48.92) * mm});
            skLineSegment(sketch, "E1705", {"start": v(1.06, 48.92) * mm, "end": v(0.93, 49.03) * mm});
            skLineSegment(sketch, "E1706", {"start": v(0.93, 49.03) * mm, "end": v(0.82, 49.14) * mm});
            skLineSegment(sketch, "E1707", {"start": v(0.82, 49.14) * mm, "end": v(0.7, 49.27) * mm});
            skLineSegment(sketch, "E1708", {"start": v(0.7, 49.27) * mm, "end": v(0.62, 49.4) * mm});
            skLineSegment(sketch, "E1709", {"start": v(0.62, 49.4) * mm, "end": v(0.53, 49.54) * mm});
            skLineSegment(sketch, "E1710", {"start": v(0.53, 49.54) * mm, "end": v(0.38, 49.83) * mm});
            skLineSegment(sketch, "E1711", {"start": v(0.38, 49.83) * mm, "end": v(0.38, 50.06) * mm});
            skLineSegment(sketch, "E1712", {"start": v(0.38, 50.06) * mm, "end": v(0.4, 50.26) * mm});
            skLineSegment(sketch, "E1713", {"start": v(0.4, 50.26) * mm, "end": v(0.42, 50.36) * mm});
            skLineSegment(sketch, "E1714", {"start": v(0.42, 50.36) * mm, "end": v(0.44, 50.44) * mm});
            skLineSegment(sketch, "E1715", {"start": v(0.44, 50.44) * mm, "end": v(0.5, 50.59) * mm});
            skLineSegment(sketch, "E1716", {"start": v(0.5, 50.59) * mm, "end": v(1.22, 50.9) * mm});
            skLineSegment(sketch, "E1717", {"start": v(1.22, 50.9) * mm, "end": v(1.55, 50.82) * mm});
            skLineSegment(sketch, "E1718", {"start": v(1.55, 50.82) * mm, "end": v(1.7, 50.47) * mm});
            skLineSegment(sketch, "E1719", {"start": v(1.7, 50.47) * mm, "end": v(1.8, 50.17) * mm});
            skLineSegment(sketch, "E1720", {"start": v(1.8, 50.17) * mm, "end": v(1.82, 50.05) * mm});
            skLineSegment(sketch, "E1721", {"start": v(1.82, 50.05) * mm, "end": v(1.83, 49.97) * mm});
            skLineSegment(sketch, "E1722", {"start": v(1.83, 49.97) * mm, "end": v(1.83, 49.83) * mm});
            skLineSegment(sketch, "E1723", {"start": v(1.83, 49.83) * mm, "end": v(1.95, 49.87) * mm});
            skLineSegment(sketch, "E1724", {"start": v(1.95, 49.87) * mm, "end": v(2, 49.9) * mm});
            skLineSegment(sketch, "E1725", {"start": v(2, 49.9) * mm, "end": v(2.09, 49.98) * mm});
            skLineSegment(sketch, "E1726", {"start": v(2.09, 49.98) * mm, "end": v(2.18, 50.08) * mm});
            skLineSegment(sketch, "E1727", {"start": v(2.18, 50.08) * mm, "end": v(2.27, 50.2) * mm});
            skLineSegment(sketch, "E1728", {"start": v(2.27, 50.2) * mm, "end": v(2.47, 50.5) * mm});
            skLineSegment(sketch, "E1729", {"start": v(2.47, 50.5) * mm, "end": v(2.47, 51.2) * mm});
            skLineSegment(sketch, "E1730", {"start": v(2.47, 51.2) * mm, "end": v(2.11, 51.56) * mm});
            skLineSegment(sketch, "E1731", {"start": v(2.11, 51.56) * mm, "end": v(1.62, 51.68) * mm});
            skLineSegment(sketch, "E1732", {"start": v(1.62, 51.68) * mm, "end": v(1.23, 51.58) * mm});
            skLineSegment(sketch, "E1733", {"start": v(1.23, 51.58) * mm, "end": v(0.93, 51.5) * mm});
            skLineSegment(sketch, "E1734", {"start": v(0.93, 51.5) * mm, "end": v(0.76, 51.48) * mm});
            skLineSegment(sketch, "E1735", {"start": v(0.76, 51.48) * mm, "end": v(0.68, 51.48) * mm});
            skLineSegment(sketch, "E1736", {"start": v(0.68, 51.48) * mm, "end": v(0.6, 53.06) * mm});
            skLineSegment(sketch, "E1737", {"start": v(0.6, 53.06) * mm, "end": v(0.44, 53.36) * mm});
            skLineSegment(sketch, "E1738", {"start": v(0.44, 53.36) * mm, "end": v(0.38, 53.47) * mm});
            skLineSegment(sketch, "E1739", {"start": v(0.38, 53.47) * mm, "end": v(0.3, 53.56) * mm});
            skLineSegment(sketch, "E1740", {"start": v(0.3, 53.56) * mm, "end": v(0.25, 53.63) * mm});
            skLineSegment(sketch, "E1741", {"start": v(0.25, 53.63) * mm, "end": v(0.22, 53.64) * mm});
            skLineSegment(sketch, "E1742", {"start": v(0.22, 53.64) * mm, "end": v(0.2, 53.65) * mm});
            skLineSegment(sketch, "E1743", {"start": v(0.2, 53.65) * mm, "end": v(0.18, 53.64) * mm});
            skLineSegment(sketch, "E1744", {"start": v(0.18, 53.64) * mm, "end": v(0.16, 53.63) * mm});
            skLineSegment(sketch, "E1745", {"start": v(0.16, 53.63) * mm, "end": v(0.1, 53.56) * mm});
            skLineSegment(sketch, "E1746", {"start": v(0.1, 53.56) * mm, "end": v(0.03, 53.47) * mm});
            skLineSegment(sketch, "E1747", {"start": v(0.03, 53.47) * mm, "end": v(-0.04, 53.36) * mm});
            skLineSegment(sketch, "E1748", {"start": v(-0.04, 53.36) * mm, "end": v(-0.2, 53.06) * mm});
            skLineSegment(sketch, "E1749", {"start": v(-0.2, 53.06) * mm, "end": v(-0.27, 51.46) * mm});
            skLineSegment(sketch, "E1750", {"start": v(-0.27, 51.46) * mm, "end": v(-0.51, 51.51) * mm});
            skLineSegment(sketch, "E1751", {"start": v(-0.51, 51.51) * mm, "end": v(-0.79, 51.57) * mm});
            skLineSegment(sketch, "E1752", {"start": v(-0.79, 51.57) * mm, "end": v(-1.13, 51.63) * mm});
            skLineSegment(sketch, "E1753", {"start": v(-1.13, 51.63) * mm, "end": v(-1.5, 51.68) * mm});
            skLineSegment(sketch, "E1754", {"start": v(-1.5, 51.68) * mm, "end": v(-2.08, 51.1) * mm});
            skLineSegment(sketch, "E1755", {"start": v(-2.08, 51.1) * mm, "end": v(-1.98, 50.36) * mm});
            skLineSegment(sketch, "E1756", {"start": v(-1.98, 50.36) * mm, "end": v(-1.81, 50.13) * mm});
            skLineSegment(sketch, "E1757", {"start": v(-1.81, 50.13) * mm, "end": v(-1.74, 50.04) * mm});
            skLineSegment(sketch, "E1758", {"start": v(-1.74, 50.04) * mm, "end": v(-1.66, 49.96) * mm});
            skLineSegment(sketch, "E1759", {"start": v(-1.66, 49.96) * mm, "end": v(-1.6, 49.9) * mm});
            skLineSegment(sketch, "E1760", {"start": v(-1.6, 49.9) * mm, "end": v(-1.54, 49.87) * mm});
            skLineSegment(sketch, "E1761", {"start": v(-1.54, 49.87) * mm, "end": v(-1.45, 49.83) * mm});
            skLineSegment(sketch, "E1762", {"start": v(-1.45, 49.83) * mm, "end": v(-1.39, 50.18) * mm});
            skLineSegment(sketch, "E1763", {"start": v(-1.39, 50.18) * mm, "end": v(-1.36, 50.31) * mm});
            skLineSegment(sketch, "E1764", {"start": v(-1.36, 50.31) * mm, "end": v(-1.32, 50.43) * mm});
            skLineSegment(sketch, "E1765", {"start": v(-1.32, 50.43) * mm, "end": v(-1.28, 50.54) * mm});
            skLineSegment(sketch, "E1766", {"start": v(-1.28, 50.54) * mm, "end": v(-1.23, 50.63) * mm});
            skLineSegment(sketch, "E1767", {"start": v(-1.23, 50.63) * mm, "end": v(-1.18, 50.7) * mm});
            skLineSegment(sketch, "E1768", {"start": v(-1.18, 50.7) * mm, "end": v(-1.11, 50.77) * mm});
            skLineSegment(sketch, "E1769", {"start": v(-1.11, 50.77) * mm, "end": v(-1.04, 50.82) * mm});
            skLineSegment(sketch, "E1770", {"start": v(-1.04, 50.82) * mm, "end": v(-0.97, 50.86) * mm});
            skLineSegment(sketch, "E1771", {"start": v(-0.97, 50.86) * mm, "end": v(-0.82, 50.91) * mm});
            skLineSegment(sketch, "E1772", {"start": v(-0.82, 50.91) * mm, "end": v(-0.07, 50.58) * mm});
            skLineSegment(sketch, "E1773", {"start": v(-0.07, 50.58) * mm, "end": v(0.04, 50.1) * mm});
            skLineSegment(sketch, "E1774", {"start": v(0.04, 50.1) * mm, "end": v(-0.07, 49.54) * mm});
            skLineSegment(sketch, "E1775", {"start": v(-0.07, 49.54) * mm, "end": v(-0.52, 48.95) * mm});
            skLineSegment(sketch, "E1776", {"start": v(-0.52, 48.95) * mm, "end": v(-1.47, 48.49) * mm});
            skLineSegment(sketch, "E1777", {"start": v(-1.47, 48.49) * mm, "end": v(-2.57, 48.37) * mm});
            skLineSegment(sketch, "E1778", {"start": v(-2.57, 48.37) * mm, "end": v(-3.65, 48.68) * mm});
            skLineSegment(sketch, "E1779", {"start": v(-3.65, 48.68) * mm, "end": v(-5.15, 49.66) * mm});
            skLineSegment(sketch, "E1780", {"start": v(-5.15, 49.66) * mm, "end": v(-5.26, 49.66) * mm});
            skLineSegment(sketch, "E1781", {"start": v(-5.26, 49.66) * mm, "end": v(-5.15, 46.63) * mm});
            skLineSegment(sketch, "E1782", {"start": v(-5.15, 46.63) * mm, "end": v(-5, 45.95) * mm});
            skLineSegment(sketch, "E1783", {"start": v(-5, 45.95) * mm, "end": v(-4.87, 45.42) * mm});
            skLineSegment(sketch, "E1784", {"start": v(-4.87, 45.42) * mm, "end": v(-4.68, 44.78) * mm});
            skLineSegment(sketch, "E1785", {"start": v(-4.68, 44.78) * mm, "end": v(-4.47, 44.15) * mm});
            skLineSegment(sketch, "E1786", {"start": v(-4.47, 44.15) * mm, "end": v(-4.37, 43.88) * mm});
            skLineSegment(sketch, "E1787", {"start": v(-4.37, 43.88) * mm, "end": v(-4.28, 43.64) * mm});
            skLineSegment(sketch, "E1788", {"start": v(-4.28, 43.64) * mm, "end": v(-4.2, 43.47) * mm});
            skLineSegment(sketch, "E1789", {"start": v(-4.2, 43.47) * mm, "end": v(-4.86, 43.97) * mm});
            skLineSegment(sketch, "E1790", {"start": v(-4.86, 43.97) * mm, "end": v(-5.59, 44.07) * mm});
            skLineSegment(sketch, "E1791", {"start": v(-5.59, 44.07) * mm, "end": v(-6.14, 43.51) * mm});
            skLineSegment(sketch, "E1792", {"start": v(-6.14, 43.51) * mm, "end": v(-6.14, 42.87) * mm});
            skLineSegment(sketch, "E1793", {"start": v(-6.14, 42.87) * mm, "end": v(-5.79, 42.68) * mm});
            skLineSegment(sketch, "E1794", {"start": v(-5.79, 42.68) * mm, "end": v(-5.05, 42.68) * mm});
            skLineSegment(sketch, "E1795", {"start": v(-5.05, 42.68) * mm, "end": v(-4.93, 42.38) * mm});
            skLineSegment(sketch, "E1796", {"start": v(-4.93, 42.38) * mm, "end": v(-5.28, 41.74) * mm});
            skLineSegment(sketch, "E1797", {"start": v(-5.28, 41.74) * mm, "end": v(-6.25, 41.23) * mm});
            skLineSegment(sketch, "E1798", {"start": v(-6.25, 41.23) * mm, "end": v(-7.25, 41.23) * mm});
            skLineSegment(sketch, "E1799", {"start": v(-7.25, 41.23) * mm, "end": v(-7.95, 41.94) * mm});
            skLineSegment(sketch, "E1800", {"start": v(-7.95, 41.94) * mm, "end": v(-8.15, 41.69) * mm});
            skLineSegment(sketch, "E1801", {"start": v(-8.15, 41.69) * mm, "end": v(-8.1, 41.44) * mm});
            skLineSegment(sketch, "E1802", {"start": v(-8.1, 41.44) * mm, "end": v(-8.06, 41.33) * mm});
            skLineSegment(sketch, "E1803", {"start": v(-8.06, 41.33) * mm, "end": v(-8, 41.21) * mm});
            skLineSegment(sketch, "E1804", {"start": v(-8, 41.21) * mm, "end": v(-7.94, 41.1) * mm});
            skLineSegment(sketch, "E1805", {"start": v(-7.94, 41.1) * mm, "end": v(-7.88, 41.02) * mm});
            skLineSegment(sketch, "E1806", {"start": v(-7.88, 41.02) * mm, "end": v(-7.73, 40.86) * mm});
            skLineSegment(sketch, "E1807", {"start": v(-7.73, 40.86) * mm, "end": v(-7.9, 40.73) * mm});
            skLineSegment(sketch, "E1808", {"start": v(-7.9, 40.73) * mm, "end": v(-8.01, 40.66) * mm});
            skLineSegment(sketch, "E1809", {"start": v(-8.01, 40.66) * mm, "end": v(-8.16, 40.6) * mm});
            skLineSegment(sketch, "E1810", {"start": v(-8.16, 40.6) * mm, "end": v(-8.35, 40.52) * mm});
            skLineSegment(sketch, "E1811", {"start": v(-8.35, 40.52) * mm, "end": v(-8.53, 40.46) * mm});
            skLineSegment(sketch, "E1812", {"start": v(-8.53, 40.46) * mm, "end": v(-8.98, 40.33) * mm});
            skLineSegment(sketch, "E1813", {"start": v(-8.98, 40.33) * mm, "end": v(-9.92, 40.33) * mm});
            skLineSegment(sketch, "E1814", {"start": v(-9.92, 40.33) * mm, "end": v(-10.72, 40.75) * mm});
            skLineSegment(sketch, "E1815", {"start": v(-10.72, 40.75) * mm, "end": v(-11.24, 41.53) * mm});
            skLineSegment(sketch, "E1816", {"start": v(-11.24, 41.53) * mm, "end": v(-11.33, 42.38) * mm});
            skLineSegment(sketch, "E1817", {"start": v(-11.33, 42.38) * mm, "end": v(-10.83, 42.96) * mm});
            skLineSegment(sketch, "E1818", {"start": v(-10.83, 42.96) * mm, "end": v(-10.78, 42.91) * mm});
            skLineSegment(sketch, "E1819", {"start": v(-10.78, 42.91) * mm, "end": v(-10.75, 42.86) * mm});
            skLineSegment(sketch, "E1820", {"start": v(-10.75, 42.86) * mm, "end": v(-10.7, 42.75) * mm});
            skLineSegment(sketch, "E1821", {"start": v(-10.7, 42.75) * mm, "end": v(-10.59, 42.43) * mm});
            skLineSegment(sketch, "E1822", {"start": v(-10.59, 42.43) * mm, "end": v(-10.44, 42) * mm});
            skLineSegment(sketch, "E1823", {"start": v(-10.44, 42) * mm, "end": v(-9.65, 42) * mm});
            skLineSegment(sketch, "E1824", {"start": v(-9.65, 42) * mm, "end": v(-9.28, 42.5) * mm});
            skLineSegment(sketch, "E1825", {"start": v(-9.28, 42.5) * mm, "end": v(-9.5, 43.22) * mm});
            skLineSegment(sketch, "E1826", {"start": v(-9.5, 43.22) * mm, "end": v(-9.97, 43.6) * mm});
            skLineSegment(sketch, "E1827", {"start": v(-9.97, 43.6) * mm, "end": v(-10.9, 43.59) * mm});
            skLineSegment(sketch, "E1828", {"start": v(-10.9, 43.59) * mm, "end": v(-11.6, 43.18) * mm});
            skLineSegment(sketch, "E1829", {"start": v(-11.6, 43.18) * mm, "end": v(-11.99, 42.67) * mm});
            skLineSegment(sketch, "E1830", {"start": v(-11.99, 42.67) * mm, "end": v(-11.96, 41.21) * mm});
            skLineSegment(sketch, "E1831", {"start": v(-11.96, 41.21) * mm, "end": v(-12.33, 41.28) * mm});
            skLineSegment(sketch, "E1832", {"start": v(-12.33, 41.28) * mm, "end": v(-12.92, 41.34) * mm});
            skLineSegment(sketch, "E1833", {"start": v(-12.92, 41.34) * mm, "end": v(-13.8, 41.42) * mm});
            skLineSegment(sketch, "E1834", {"start": v(-13.8, 41.42) * mm, "end": v(-14.89, 41.5) * mm});
            skLineSegment(sketch, "E1835", {"start": v(-14.89, 41.5) * mm, "end": v(-15.99, 41.4) * mm});
            skLineSegment(sketch, "E1836", {"start": v(-15.99, 41.4) * mm, "end": v(-16.62, 41.7) * mm});
            skLineSegment(sketch, "E1837", {"start": v(-16.62, 41.7) * mm, "end": v(-16.95, 42.25) * mm});
            skLineSegment(sketch, "E1838", {"start": v(-16.95, 42.25) * mm, "end": v(-17.02, 42.13) * mm});
            skLineSegment(sketch, "E1839", {"start": v(-17.02, 42.13) * mm, "end": v(-17.06, 42.06) * mm});
            skLineSegment(sketch, "E1840", {"start": v(-17.06, 42.06) * mm, "end": v(-17.08, 41.96) * mm});
            skLineSegment(sketch, "E1841", {"start": v(-17.08, 41.96) * mm, "end": v(-17.1, 41.84) * mm});
            skLineSegment(sketch, "E1842", {"start": v(-17.1, 41.84) * mm, "end": v(-17.1, 41.72) * mm});
            skLineSegment(sketch, "E1843", {"start": v(-17.1, 41.72) * mm, "end": v(-17.1, 41.43) * mm});
            skLineSegment(sketch, "E1844", {"start": v(-17.1, 41.43) * mm, "end": v(-16.66, 40.9) * mm});
            skLineSegment(sketch, "E1845", {"start": v(-16.66, 40.9) * mm, "end": v(-17.83, 40.58) * mm});
            skLineSegment(sketch, "E1846", {"start": v(-17.83, 40.58) * mm, "end": v(-18.86, 39.96) * mm});
            skLineSegment(sketch, "E1847", {"start": v(-18.86, 39.96) * mm, "end": v(-19.5, 39.35) * mm});
            skLineSegment(sketch, "E1848", {"start": v(-19.5, 39.35) * mm, "end": v(-20.1, 38.8) * mm});
            skLineSegment(sketch, "E1849", {"start": v(-20.1, 38.8) * mm, "end": v(-20.36, 38.57) * mm});
            skLineSegment(sketch, "E1850", {"start": v(-20.36, 38.57) * mm, "end": v(-20.6, 38.38) * mm});
            skLineSegment(sketch, "E1851", {"start": v(-20.6, 38.38) * mm, "end": v(-20.82, 38.22) * mm});
            skLineSegment(sketch, "E1852", {"start": v(-20.82, 38.22) * mm, "end": v(-21.03, 38.08) * mm});
            skLineSegment(sketch, "E1853", {"start": v(-21.03, 38.08) * mm, "end": v(-21.23, 37.95) * mm});
            skLineSegment(sketch, "E1854", {"start": v(-21.23, 37.95) * mm, "end": v(-21.43, 37.85) * mm});
            skLineSegment(sketch, "E1855", {"start": v(-21.43, 37.85) * mm, "end": v(-21.9, 37.6) * mm});
            skLineSegment(sketch, "E1856", {"start": v(-21.9, 37.6) * mm, "end": v(-22.55, 37.6) * mm});
            skLineSegment(sketch, "E1857", {"start": v(-22.55, 37.6) * mm, "end": v(-23.09, 37.89) * mm});
            skLineSegment(sketch, "E1858", {"start": v(-23.09, 37.89) * mm, "end": v(-23.09, 37.77) * mm});
            skLineSegment(sketch, "E1859", {"start": v(-23.09, 37.77) * mm, "end": v(-23.07, 37.7) * mm});
            skLineSegment(sketch, "E1860", {"start": v(-23.07, 37.7) * mm, "end": v(-23.03, 37.6) * mm});
            skLineSegment(sketch, "E1861", {"start": v(-23.03, 37.6) * mm, "end": v(-22.98, 37.48) * mm});
            skLineSegment(sketch, "E1862", {"start": v(-22.98, 37.48) * mm, "end": v(-22.9, 37.36) * mm});
            skLineSegment(sketch, "E1863", {"start": v(-22.9, 37.36) * mm, "end": v(-22.78, 37.14) * mm});
            skLineSegment(sketch, "E1864", {"start": v(-22.78, 37.14) * mm, "end": v(-22.72, 37.02) * mm});
            skLineSegment(sketch, "E1865", {"start": v(-22.72, 37.02) * mm, "end": v(-22.72, 36.98) * mm});
            skLineSegment(sketch, "E1866", {"start": v(-22.72, 36.98) * mm, "end": v(-25.8, 36.98) * mm});
            skLineSegment(sketch, "E1867", {"start": v(-25.8, 36.98) * mm, "end": v(-26.07, 37.25) * mm});
            skLineSegment(sketch, "E1868", {"start": v(-26.07, 37.25) * mm, "end": v(-26.2, 37.9) * mm});
            skLineSegment(sketch, "E1869", {"start": v(-26.2, 37.9) * mm, "end": v(-26.07, 39.1) * mm});
            skLineSegment(sketch, "E1870", {"start": v(-26.07, 39.1) * mm, "end": v(-25.78, 39.59) * mm});
            skLineSegment(sketch, "E1871", {"start": v(-25.78, 39.59) * mm, "end": v(-25.33, 39.83) * mm});
            skLineSegment(sketch, "E1872", {"start": v(-25.33, 39.83) * mm, "end": v(-24.62, 39.83) * mm});
            skLineSegment(sketch, "E1873", {"start": v(-24.62, 39.83) * mm, "end": v(-24.53, 39.7) * mm});
            skLineSegment(sketch, "E1874", {"start": v(-24.53, 39.7) * mm, "end": v(-24.45, 39.54) * mm});
            skLineSegment(sketch, "E1875", {"start": v(-24.45, 39.54) * mm, "end": v(-24.4, 39.35) * mm});
            skLineSegment(sketch, "E1876", {"start": v(-24.4, 39.35) * mm, "end": v(-24.34, 39.15) * mm});
            skLineSegment(sketch, "E1877", {"start": v(-24.34, 39.15) * mm, "end": v(-24.56, 38.88) * mm});
            skLineSegment(sketch, "E1878", {"start": v(-24.56, 38.88) * mm, "end": v(-25, 38.88) * mm});
            skLineSegment(sketch, "E1879", {"start": v(-25, 38.88) * mm, "end": v(-25, 38.76) * mm});
            skLineSegment(sketch, "E1880", {"start": v(-25, 38.76) * mm, "end": v(-24.98, 38.7) * mm});
            skLineSegment(sketch, "E1881", {"start": v(-24.98, 38.7) * mm, "end": v(-24.96, 38.65) * mm});
            skLineSegment(sketch, "E1882", {"start": v(-24.96, 38.65) * mm, "end": v(-24.92, 38.59) * mm});
            skLineSegment(sketch, "E1883", {"start": v(-24.92, 38.59) * mm, "end": v(-24.88, 38.53) * mm});
            skLineSegment(sketch, "E1884", {"start": v(-24.88, 38.53) * mm, "end": v(-24.77, 38.43) * mm});
            skLineSegment(sketch, "E1885", {"start": v(-24.77, 38.43) * mm, "end": v(-24.2, 38.43) * mm});
            skLineSegment(sketch, "E1886", {"start": v(-24.2, 38.43) * mm, "end": v(-23.73, 38.8) * mm});
            skLineSegment(sketch, "E1887", {"start": v(-23.73, 38.8) * mm, "end": v(-23.62, 39.38) * mm});
            skLineSegment(sketch, "E1888", {"start": v(-23.62, 39.38) * mm, "end": v(-23.7, 39.61) * mm});
            skLineSegment(sketch, "E1889", {"start": v(-23.7, 39.61) * mm, "end": v(-23.76, 39.72) * mm});
            skLineSegment(sketch, "E1890", {"start": v(-23.76, 39.72) * mm, "end": v(-23.85, 39.86) * mm});
            skLineSegment(sketch, "E1891", {"start": v(-23.85, 39.86) * mm, "end": v(-23.96, 40) * mm});
            skLineSegment(sketch, "E1892", {"start": v(-23.96, 40) * mm, "end": v(-24.08, 40.13) * mm});
            skLineSegment(sketch, "E1893", {"start": v(-24.08, 40.13) * mm, "end": v(-24.36, 40.41) * mm});
            skLineSegment(sketch, "E1894", {"start": v(-24.36, 40.41) * mm, "end": v(-25.02, 40.53) * mm});
            skLineSegment(sketch, "E1895", {"start": v(-25.02, 40.53) * mm, "end": v(-25.46, 40.35) * mm});
            skLineSegment(sketch, "E1896", {"start": v(-25.46, 40.35) * mm, "end": v(-25.63, 40.28) * mm});
            skLineSegment(sketch, "E1897", {"start": v(-25.63, 40.28) * mm, "end": v(-25.77, 40.23) * mm});
            skLineSegment(sketch, "E1898", {"start": v(-25.77, 40.23) * mm, "end": v(-25.86, 40.21) * mm});
            skLineSegment(sketch, "E1899", {"start": v(-25.86, 40.21) * mm, "end": v(-25.89, 40.21) * mm});
            skLineSegment(sketch, "E1900", {"start": v(-25.89, 40.21) * mm, "end": v(-25.9, 40.22) * mm});
            skLineSegment(sketch, "E1901", {"start": v(-25.9, 40.22) * mm, "end": v(-25.93, 41) * mm});
            skLineSegment(sketch, "E1902", {"start": v(-25.93, 41) * mm, "end": v(-25.95, 41.73) * mm});
            skLineSegment(sketch, "E1903", {"start": v(-25.95, 41.73) * mm, "end": v(-26.29, 42.6) * mm});
            skLineSegment(sketch, "E1904", {"start": v(-26.29, 42.6) * mm, "end": v(-26.49, 42.54) * mm});
            skLineSegment(sketch, "E1905", {"start": v(-26.49, 42.54) * mm, "end": v(-26.8, 41.64) * mm});
            skLineSegment(sketch, "E1906", {"start": v(-26.8, 41.64) * mm, "end": v(-26.8, 40.15) * mm});
            skLineSegment(sketch, "E1907", {"start": v(-26.8, 40.15) * mm, "end": v(-26.84, 40.15) * mm});
            skLineSegment(sketch, "E1908", {"start": v(-26.84, 40.15) * mm, "end": v(-26.98, 40.2) * mm});
            skLineSegment(sketch, "E1909", {"start": v(-26.98, 40.2) * mm, "end": v(-27.27, 40.33) * mm});
            skLineSegment(sketch, "E1910", {"start": v(-27.27, 40.33) * mm, "end": v(-27.66, 40.5) * mm});
            skLineSegment(sketch, "E1911", {"start": v(-27.66, 40.5) * mm, "end": v(-28.12, 40.5) * mm});
            skLineSegment(sketch, "E1912", {"start": v(-28.12, 40.5) * mm, "end": v(-28.7, 40.15) * mm});
            skLineSegment(sketch, "E1913", {"start": v(-28.7, 40.15) * mm, "end": v(-29.07, 39.56) * mm});
            skLineSegment(sketch, "E1914", {"start": v(-29.07, 39.56) * mm, "end": v(-29.07, 38.9) * mm});
            skLineSegment(sketch, "E1915", {"start": v(-29.07, 38.9) * mm, "end": v(-28.51, 38.43) * mm});
            skLineSegment(sketch, "E1916", {"start": v(-28.51, 38.43) * mm, "end": v(-28, 38.43) * mm});
            skLineSegment(sketch, "E1917", {"start": v(-28, 38.43) * mm, "end": v(-27.85, 38.57) * mm});
            skLineSegment(sketch, "E1918", {"start": v(-27.85, 38.57) * mm, "end": v(-27.8, 38.63) * mm});
            skLineSegment(sketch, "E1919", {"start": v(-27.8, 38.63) * mm, "end": v(-27.75, 38.7) * mm});
            skLineSegment(sketch, "E1920", {"start": v(-27.75, 38.7) * mm, "end": v(-27.72, 38.75) * mm});
            skLineSegment(sketch, "E1921", {"start": v(-27.72, 38.75) * mm, "end": v(-27.7, 38.79) * mm});
            skLineSegment(sketch, "E1922", {"start": v(-27.7, 38.79) * mm, "end": v(-27.7, 38.87) * mm});
            skLineSegment(sketch, "E1923", {"start": v(-27.7, 38.87) * mm, "end": v(-28.19, 38.92) * mm});
            skLineSegment(sketch, "E1924", {"start": v(-28.19, 38.92) * mm, "end": v(-28.37, 39.21) * mm});
            skLineSegment(sketch, "E1925", {"start": v(-28.37, 39.21) * mm, "end": v(-28.25, 39.7) * mm});
            skLineSegment(sketch, "E1926", {"start": v(-28.25, 39.7) * mm, "end": v(-27.79, 39.91) * mm});
            skLineSegment(sketch, "E1927", {"start": v(-27.79, 39.91) * mm, "end": v(-27.05, 39.65) * mm});
            skLineSegment(sketch, "E1928", {"start": v(-27.05, 39.65) * mm, "end": v(-26.67, 39.15) * mm});
            skLineSegment(sketch, "E1929", {"start": v(-26.67, 39.15) * mm, "end": v(-26.6, 37.43) * mm});
            skLineSegment(sketch, "E1930", {"start": v(-26.6, 37.43) * mm, "end": v(-26.9, 36.98) * mm});
            skLineSegment(sketch, "E1931", {"start": v(-26.9, 36.98) * mm, "end": v(-31.27, 36.98) * mm});
            skLineSegment(sketch, "E1932", {"start": v(-31.27, 36.98) * mm, "end": v(-30.95, 36.59) * mm});
            skLineSegment(sketch, "E1933", {"start": v(-30.95, 36.59) * mm, "end": v(-30.8, 36.4) * mm});
            skLineSegment(sketch, "E1934", {"start": v(-30.8, 36.4) * mm, "end": v(-30.65, 36.17) * mm});
            skLineSegment(sketch, "E1935", {"start": v(-30.65, 36.17) * mm, "end": v(-30.5, 35.93) * mm});
            skLineSegment(sketch, "E1936", {"start": v(-30.5, 35.93) * mm, "end": v(-30.37, 35.7) * mm});
            skLineSegment(sketch, "E1937", {"start": v(-30.37, 35.7) * mm, "end": v(-30.11, 35.2) * mm});
            skLineSegment(sketch, "E1938", {"start": v(-30.11, 35.2) * mm, "end": v(-30.11, 33.21) * mm});
            skLineSegment(sketch, "E1939", {"start": v(-30.11, 33.21) * mm, "end": v(-30.88, 31.63) * mm});
            skLineSegment(sketch, "E1940", {"start": v(-30.88, 31.63) * mm, "end": v(-31.56, 31.17) * mm});
            skLineSegment(sketch, "E1941", {"start": v(-31.56, 31.17) * mm, "end": v(-31.97, 31.17) * mm});
            skLineSegment(sketch, "E1942", {"start": v(-31.97, 31.17) * mm, "end": v(-32.54, 31.7) * mm});
            skLineSegment(sketch, "E1943", {"start": v(-32.54, 31.7) * mm, "end": v(-32.54, 32.3) * mm});
            skLineSegment(sketch, "E1944", {"start": v(-32.54, 32.3) * mm, "end": v(-32.26, 32.53) * mm});
            skLineSegment(sketch, "E1945", {"start": v(-32.26, 32.53) * mm, "end": v(-32.05, 32.72) * mm});
            skLineSegment(sketch, "E1946", {"start": v(-32.05, 32.72) * mm, "end": v(-32, 32.8) * mm});
            skLineSegment(sketch, "E1947", {"start": v(-32, 32.8) * mm, "end": v(-31.97, 32.84) * mm});
            skLineSegment(sketch, "E1948", {"start": v(-31.97, 32.84) * mm, "end": v(-31.97, 32.9) * mm});
            skLineSegment(sketch, "E1949", {"start": v(-31.97, 32.9) * mm, "end": v(-32.67, 32.9) * mm});
            skLineSegment(sketch, "E1950", {"start": v(-32.67, 32.9) * mm, "end": v(-33.22, 32.27) * mm});
            skLineSegment(sketch, "E1951", {"start": v(-33.22, 32.27) * mm, "end": v(-33.35, 31.45) * mm});
            skLineSegment(sketch, "E1952", {"start": v(-33.35, 31.45) * mm, "end": v(-33, 30.86) * mm});
            skLineSegment(sketch, "E1953", {"start": v(-33, 30.86) * mm, "end": v(-32.3, 30.53) * mm});
            skLineSegment(sketch, "E1954", {"start": v(-32.3, 30.53) * mm, "end": v(-31.38, 30.53) * mm});
            skLineSegment(sketch, "E1955", {"start": v(-31.38, 30.53) * mm, "end": v(-30.89, 30.71) * mm});
            skLineSegment(sketch, "E1956", {"start": v(-30.89, 30.71) * mm, "end": v(-30.17, 31.43) * mm});
            skLineSegment(sketch, "E1957", {"start": v(-30.17, 31.43) * mm, "end": v(-29.54, 32.76) * mm});
            skLineSegment(sketch, "E1958", {"start": v(-29.54, 32.76) * mm, "end": v(-29.32, 33.83) * mm});
            skLineSegment(sketch, "E1959", {"start": v(-29.32, 33.83) * mm, "end": v(-29.45, 35.03) * mm});
            skLineSegment(sketch, "E1960", {"start": v(-29.45, 35.03) * mm, "end": v(-29.87, 36.37) * mm});
            skLineSegment(sketch, "E1961", {"start": v(-29.87, 36.37) * mm, "end": v(-29.81, 36.48) * mm});
            skLineSegment(sketch, "E1962", {"start": v(-29.81, 36.48) * mm, "end": v(-22.23, 36.36) * mm});
            skLineSegment(sketch, "E1963", {"start": v(-22.23, 36.36) * mm, "end": v(-21.45, 36.52) * mm});
            skLineSegment(sketch, "E1964", {"start": v(-21.45, 36.52) * mm, "end": v(-21.1, 36.75) * mm});
            skLineSegment(sketch, "E1965", {"start": v(-21.1, 36.75) * mm, "end": v(-20.81, 36.9) * mm});
            skLineSegment(sketch, "E1966", {"start": v(-20.81, 36.9) * mm, "end": v(-20.71, 36.96) * mm});
            skLineSegment(sketch, "E1967", {"start": v(-20.71, 36.96) * mm, "end": v(-20.65, 36.98) * mm});
            skLineSegment(sketch, "E1968", {"start": v(-20.65, 36.98) * mm, "end": v(-20.57, 36.98) * mm});
            skLineSegment(sketch, "E1969", {"start": v(-20.57, 36.98) * mm, "end": v(-20.44, 35.73) * mm});
            skLineSegment(sketch, "E1970", {"start": v(-20.44, 35.73) * mm, "end": v(-20.27, 35.77) * mm});
            skLineSegment(sketch, "E1971", {"start": v(-20.27, 35.77) * mm, "end": v(-20.2, 35.8) * mm});
            skLineSegment(sketch, "E1972", {"start": v(-20.2, 35.8) * mm, "end": v(-20.1, 35.85) * mm});
            skLineSegment(sketch, "E1973", {"start": v(-20.1, 35.85) * mm, "end": v(-20.01, 35.92) * mm});
            skLineSegment(sketch, "E1974", {"start": v(-20.01, 35.92) * mm, "end": v(-19.9, 36) * mm});
            skLineSegment(sketch, "E1975", {"start": v(-19.9, 36) * mm, "end": v(-19.8, 36.1) * mm});
            skLineSegment(sketch, "E1976", {"start": v(-19.8, 36.1) * mm, "end": v(-19.69, 36.23) * mm});
            skLineSegment(sketch, "E1977", {"start": v(-19.69, 36.23) * mm, "end": v(-19.44, 36.52) * mm});
            skLineSegment(sketch, "E1978", {"start": v(-19.44, 36.52) * mm, "end": v(-19.19, 36.84) * mm});
            skLineSegment(sketch, "E1979", {"start": v(-19.19, 36.84) * mm, "end": v(-19.1, 36.71) * mm});
            skLineSegment(sketch, "E1980", {"start": v(-19.1, 36.71) * mm, "end": v(-19.07, 36.64) * mm});
            skLineSegment(sketch, "E1981", {"start": v(-19.07, 36.64) * mm, "end": v(-19.03, 36.52) * mm});
            skLineSegment(sketch, "E1982", {"start": v(-19.03, 36.52) * mm, "end": v(-19, 36.37) * mm});
            skLineSegment(sketch, "E1983", {"start": v(-19, 36.37) * mm, "end": v(-18.97, 36.22) * mm});
            skLineSegment(sketch, "E1984", {"start": v(-18.97, 36.22) * mm, "end": v(-18.91, 35.86) * mm});
            skLineSegment(sketch, "E1985", {"start": v(-18.91, 35.86) * mm, "end": v(-18.21, 35.16) * mm});
            skLineSegment(sketch, "E1986", {"start": v(-18.21, 35.16) * mm, "end": v(-17.8, 35.16) * mm});
            skLineSegment(sketch, "E1987", {"start": v(-17.8, 35.16) * mm, "end": v(-17.92, 36.02) * mm});
            skLineSegment(sketch, "E1988", {"start": v(-17.92, 36.02) * mm, "end": v(-17.75, 37.08) * mm});
            skLineSegment(sketch, "E1989", {"start": v(-17.75, 37.08) * mm, "end": v(-17.3, 38.06) * mm});
            skLineSegment(sketch, "E1990", {"start": v(-17.3, 38.06) * mm, "end": v(-17.13, 38.06) * mm});
            skLineSegment(sketch, "E1991", {"start": v(-17.13, 38.06) * mm, "end": v(-17.06, 37.82) * mm});
            skLineSegment(sketch, "E1992", {"start": v(-17.06, 37.82) * mm, "end": v(-17.03, 37.7) * mm});
            skLineSegment(sketch, "E1993", {"start": v(-17.03, 37.7) * mm, "end": v(-16.97, 37.57) * mm});
            skLineSegment(sketch, "E1994", {"start": v(-16.97, 37.57) * mm, "end": v(-16.9, 37.44) * mm});
            skLineSegment(sketch, "E1995", {"start": v(-16.9, 37.44) * mm, "end": v(-16.83, 37.33) * mm});
            skLineSegment(sketch, "E1996", {"start": v(-16.83, 37.33) * mm, "end": v(-16.65, 37.08) * mm});
            skLineSegment(sketch, "E1997", {"start": v(-16.65, 37.08) * mm, "end": v(-16.18, 36.85) * mm});
            skLineSegment(sketch, "E1998", {"start": v(-16.18, 36.85) * mm, "end": v(-15.82, 36.68) * mm});
            skLineSegment(sketch, "E1999", {"start": v(-15.82, 36.68) * mm, "end": v(-15.68, 36.63) * mm});
            skLineSegment(sketch, "E2000", {"start": v(-15.68, 36.63) * mm, "end": v(-15.6, 36.61) * mm});
            skLineSegment(sketch, "E2001", {"start": v(-15.6, 36.61) * mm, "end": v(-15.5, 36.61) * mm});
            skLineSegment(sketch, "E2002", {"start": v(-15.5, 36.61) * mm, "end": v(-15.59, 37.86) * mm});
            skLineSegment(sketch, "E2003", {"start": v(-15.59, 37.86) * mm, "end": v(-15.36, 38.54) * mm});
            skLineSegment(sketch, "E2004", {"start": v(-15.36, 38.54) * mm, "end": v(-14.75, 39.22) * mm});
            skLineSegment(sketch, "E2005", {"start": v(-14.75, 39.22) * mm, "end": v(-13.8, 39.64) * mm});
            skLineSegment(sketch, "E2006", {"start": v(-13.8, 39.64) * mm, "end": v(-12.07, 39.65) * mm});
            skLineSegment(sketch, "E2007", {"start": v(-12.07, 39.65) * mm, "end": v(-10.87, 39.04) * mm});
            skLineSegment(sketch, "E2008", {"start": v(-10.87, 39.04) * mm, "end": v(-10.1, 38.25) * mm});
            skLineSegment(sketch, "E2009", {"start": v(-10.1, 38.25) * mm, "end": v(-10.72, 37.89) * mm});
            skLineSegment(sketch, "E2010", {"start": v(-10.72, 37.89) * mm, "end": v(-10.87, 37.64) * mm});
            skLineSegment(sketch, "E2011", {"start": v(-10.87, 37.64) * mm, "end": v(-10.93, 37.5) * mm});
            skLineSegment(sketch, "E2012", {"start": v(-10.93, 37.5) * mm, "end": v(-10.99, 37.35) * mm});
            skLineSegment(sketch, "E2013", {"start": v(-10.99, 37.35) * mm, "end": v(-11.04, 37.17) * mm});
            skLineSegment(sketch, "E2014", {"start": v(-11.04, 37.17) * mm, "end": v(-11.08, 37) * mm});
            skLineSegment(sketch, "E2015", {"start": v(-11.08, 37) * mm, "end": v(-11.14, 36.62) * mm});
            skLineSegment(sketch, "E2016", {"start": v(-11.14, 36.62) * mm, "end": v(-11.03, 36.44) * mm});
            skLineSegment(sketch, "E2017", {"start": v(-11.03, 36.44) * mm, "end": v(-10.54, 36.7) * mm});
            skLineSegment(sketch, "E2018", {"start": v(-10.54, 36.7) * mm, "end": v(-9.78, 36.7) * mm});
            skLineSegment(sketch, "E2019", {"start": v(-9.78, 36.7) * mm, "end": v(-9.25, 36.26) * mm});
            skLineSegment(sketch, "E2020", {"start": v(-9.25, 36.26) * mm, "end": v(-8.75, 35.13) * mm});
            skLineSegment(sketch, "E2021", {"start": v(-8.75, 35.13) * mm, "end": v(-8.74, 34.03) * mm});
            skLineSegment(sketch, "E2022", {"start": v(-8.74, 34.03) * mm, "end": v(-9.1, 33.21) * mm});
            skLineSegment(sketch, "E2023", {"start": v(-9.1, 33.21) * mm, "end": v(-9.49, 32.83) * mm});
            skLineSegment(sketch, "E2024", {"start": v(-9.49, 32.83) * mm, "end": v(-9.78, 32.56) * mm});
            skLineSegment(sketch, "E2025", {"start": v(-9.78, 32.56) * mm, "end": v(-9.88, 32.47) * mm});
            skLineSegment(sketch, "E2026", {"start": v(-9.88, 32.47) * mm, "end": v(-9.93, 32.44) * mm});
            skLineSegment(sketch, "E2027", {"start": v(-9.93, 32.44) * mm, "end": v(-9.97, 32.47) * mm});
            skLineSegment(sketch, "E2028", {"start": v(-9.97, 32.47) * mm, "end": v(-10.02, 32.52) * mm});
            skLineSegment(sketch, "E2029", {"start": v(-10.02, 32.52) * mm, "end": v(-10.08, 32.6) * mm});
            skLineSegment(sketch, "E2030", {"start": v(-10.08, 32.6) * mm, "end": v(-10.14, 32.7) * mm});
            skLineSegment(sketch, "E2031", {"start": v(-10.14, 32.7) * mm, "end": v(-10.3, 32.97) * mm});
            skLineSegment(sketch, "E2032", {"start": v(-10.3, 32.97) * mm, "end": v(-10.85, 33.26) * mm});
            skLineSegment(sketch, "E2033", {"start": v(-10.85, 33.26) * mm, "end": v(-10.96, 32.55) * mm});
            skLineSegment(sketch, "E2034", {"start": v(-10.96, 32.55) * mm, "end": v(-11.3, 31.98) * mm});
            skLineSegment(sketch, "E2035", {"start": v(-11.3, 31.98) * mm, "end": v(-11.99, 31.7) * mm});
            skLineSegment(sketch, "E2036", {"start": v(-11.99, 31.7) * mm, "end": v(-13.44, 31.79) * mm});
            skLineSegment(sketch, "E2037", {"start": v(-13.44, 31.79) * mm, "end": v(-14.2, 32.17) * mm});
            skLineSegment(sketch, "E2038", {"start": v(-14.2, 32.17) * mm, "end": v(-14.56, 32.68) * mm});
            skLineSegment(sketch, "E2039", {"start": v(-14.56, 32.68) * mm, "end": v(-14.77, 33.55) * mm});
            skLineSegment(sketch, "E2040", {"start": v(-14.77, 33.55) * mm, "end": v(-14.56, 34.52) * mm});
            skLineSegment(sketch, "E2041", {"start": v(-14.56, 34.52) * mm, "end": v(-14.19, 34.99) * mm});
            skLineSegment(sketch, "E2042", {"start": v(-14.19, 34.99) * mm, "end": v(-13.87, 35.12) * mm});
            skLineSegment(sketch, "E2043", {"start": v(-13.87, 35.12) * mm, "end": v(-13.72, 35.17) * mm});
            skLineSegment(sketch, "E2044", {"start": v(-13.72, 35.17) * mm, "end": v(-13.52, 35.23) * mm});
            skLineSegment(sketch, "E2045", {"start": v(-13.52, 35.23) * mm, "end": v(-13.3, 35.28) * mm});
            skLineSegment(sketch, "E2046", {"start": v(-13.3, 35.28) * mm, "end": v(-13.1, 35.3) * mm});
            skLineSegment(sketch, "E2047", {"start": v(-13.1, 35.3) * mm, "end": v(-12.63, 35.37) * mm});
            skLineSegment(sketch, "E2048", {"start": v(-12.63, 35.37) * mm, "end": v(-12.82, 35.06) * mm});
            skLineSegment(sketch, "E2049", {"start": v(-12.82, 35.06) * mm, "end": v(-12.97, 34.79) * mm});
            skLineSegment(sketch, "E2050", {"start": v(-12.97, 34.79) * mm, "end": v(-13.03, 34.65) * mm});
            skLineSegment(sketch, "E2051", {"start": v(-13.03, 34.65) * mm, "end": v(-13.07, 34.55) * mm});
            skLineSegment(sketch, "E2052", {"start": v(-13.07, 34.55) * mm, "end": v(-13.13, 34.35) * mm});
            skLineSegment(sketch, "E2053", {"start": v(-13.13, 34.35) * mm, "end": v(-12.59, 33.8) * mm});
            skLineSegment(sketch, "E2054", {"start": v(-12.59, 33.8) * mm, "end": v(-12.1, 33.8) * mm});
            skLineSegment(sketch, "E2055", {"start": v(-12.1, 33.8) * mm, "end": v(-11.51, 34.25) * mm});
            skLineSegment(sketch, "E2056", {"start": v(-11.51, 34.25) * mm, "end": v(-11.29, 34.8) * mm});
            skLineSegment(sketch, "E2057", {"start": v(-11.29, 34.8) * mm, "end": v(-11.34, 35.01) * mm});
            skLineSegment(sketch, "E2058", {"start": v(-11.34, 35.01) * mm, "end": v(-11.38, 35.11) * mm});
            skLineSegment(sketch, "E2059", {"start": v(-11.38, 35.11) * mm, "end": v(-11.44, 35.24) * mm});
            skLineSegment(sketch, "E2060", {"start": v(-11.44, 35.24) * mm, "end": v(-11.5, 35.36) * mm});
            skLineSegment(sketch, "E2061", {"start": v(-11.5, 35.36) * mm, "end": v(-11.6, 35.48) * mm});
            skLineSegment(sketch, "E2062", {"start": v(-11.6, 35.48) * mm, "end": v(-11.79, 35.73) * mm});
            skLineSegment(sketch, "E2063", {"start": v(-11.79, 35.73) * mm, "end": v(-12.53, 36.06) * mm});
            skLineSegment(sketch, "E2064", {"start": v(-12.53, 36.06) * mm, "end": v(-13.44, 36.06) * mm});
            skLineSegment(sketch, "E2065", {"start": v(-13.44, 36.06) * mm, "end": v(-14.2, 35.72) * mm});
            skLineSegment(sketch, "E2066", {"start": v(-14.2, 35.72) * mm, "end": v(-15.14, 34.85) * mm});
            skLineSegment(sketch, "E2067", {"start": v(-15.14, 34.85) * mm, "end": v(-15.47, 34.12) * mm});
            skLineSegment(sketch, "E2068", {"start": v(-15.47, 34.12) * mm, "end": v(-15.47, 33.12) * mm});
            skLineSegment(sketch, "E2069", {"start": v(-15.47, 33.12) * mm, "end": v(-15.25, 32.58) * mm});
            skLineSegment(sketch, "E2070", {"start": v(-15.25, 32.58) * mm, "end": v(-15.1, 32.2) * mm});
            skLineSegment(sketch, "E2071", {"start": v(-15.1, 32.2) * mm, "end": v(-15.06, 32.07) * mm});
            skLineSegment(sketch, "E2072", {"start": v(-15.06, 32.07) * mm, "end": v(-15.06, 32.01) * mm});
            skLineSegment(sketch, "E2073", {"start": v(-15.06, 32.01) * mm, "end": v(-15.1, 31.98) * mm});
            skLineSegment(sketch, "E2074", {"start": v(-15.1, 31.98) * mm, "end": v(-17.24, 32.84) * mm});
            skLineSegment(sketch, "E2075", {"start": v(-17.24, 32.84) * mm, "end": v(-17.9, 33.27) * mm});
            skLineSegment(sketch, "E2076", {"start": v(-17.9, 33.27) * mm, "end": v(-18.05, 33.58) * mm});
            skLineSegment(sketch, "E2077", {"start": v(-18.05, 33.58) * mm, "end": v(-18.1, 33.71) * mm});
            skLineSegment(sketch, "E2078", {"start": v(-18.1, 33.71) * mm, "end": v(-18.15, 33.86) * mm});
            skLineSegment(sketch, "E2079", {"start": v(-18.15, 33.86) * mm, "end": v(-18.18, 34) * mm});
            skLineSegment(sketch, "E2080", {"start": v(-18.18, 34) * mm, "end": v(-18.2, 34.1) * mm});
            skLineSegment(sketch, "E2081", {"start": v(-18.2, 34.1) * mm, "end": v(-18.2, 34.34) * mm});
            skLineSegment(sketch, "E2082", {"start": v(-18.2, 34.34) * mm, "end": v(-18.36, 34.44) * mm});
            skLineSegment(sketch, "E2083", {"start": v(-18.36, 34.44) * mm, "end": v(-18.78, 34) * mm});
            skLineSegment(sketch, "E2084", {"start": v(-18.78, 34) * mm, "end": v(-18.96, 33.36) * mm});
            skLineSegment(sketch, "E2085", {"start": v(-18.96, 33.36) * mm, "end": v(-19.82, 33.85) * mm});
            skLineSegment(sketch, "E2086", {"start": v(-19.82, 33.85) * mm, "end": v(-20.36, 34.15) * mm});
            skLineSegment(sketch, "E2087", {"start": v(-20.36, 34.15) * mm, "end": v(-20.88, 34.41) * mm});
            skLineSegment(sketch, "E2088", {"start": v(-20.88, 34.41) * mm, "end": v(-21.37, 34.63) * mm});
            skLineSegment(sketch, "E2089", {"start": v(-21.37, 34.63) * mm, "end": v(-21.84, 34.81) * mm});
            skLineSegment(sketch, "E2090", {"start": v(-21.84, 34.81) * mm, "end": v(-22.32, 34.97) * mm});
            skLineSegment(sketch, "E2091", {"start": v(-22.32, 34.97) * mm, "end": v(-22.8, 35.09) * mm});
            skLineSegment(sketch, "E2092", {"start": v(-22.8, 35.09) * mm, "end": v(-23.28, 35.18) * mm});
            skLineSegment(sketch, "E2093", {"start": v(-23.28, 35.18) * mm, "end": v(-23.79, 35.25) * mm});
            skLineSegment(sketch, "E2094", {"start": v(-23.79, 35.25) * mm, "end": v(-24.54, 35.34) * mm});
            skLineSegment(sketch, "E2095", {"start": v(-24.54, 35.34) * mm, "end": v(-25.24, 35.25) * mm});
            skLineSegment(sketch, "E2096", {"start": v(-25.24, 35.25) * mm, "end": v(-25.63, 35.2) * mm});
            skLineSegment(sketch, "E2097", {"start": v(-25.63, 35.2) * mm, "end": v(-25.98, 35.13) * mm});
            skLineSegment(sketch, "E2098", {"start": v(-25.98, 35.13) * mm, "end": v(-26.3, 35.05) * mm});
            skLineSegment(sketch, "E2099", {"start": v(-26.3, 35.05) * mm, "end": v(-26.58, 34.95) * mm});
            skLineSegment(sketch, "E2100", {"start": v(-26.58, 34.95) * mm, "end": v(-26.85, 34.83) * mm});
            skLineSegment(sketch, "E2101", {"start": v(-26.85, 34.83) * mm, "end": v(-27.1, 34.7) * mm});
            skLineSegment(sketch, "E2102", {"start": v(-27.1, 34.7) * mm, "end": v(-27.33, 34.53) * mm});
            skLineSegment(sketch, "E2103", {"start": v(-27.33, 34.53) * mm, "end": v(-27.56, 34.35) * mm});
            skLineSegment(sketch, "E2104", {"start": v(-27.56, 34.35) * mm, "end": v(-27.87, 34.08) * mm});
            skLineSegment(sketch, "E2105", {"start": v(-27.87, 34.08) * mm, "end": v(-28.27, 33.14) * mm});
            skLineSegment(sketch, "E2106", {"start": v(-28.27, 33.14) * mm, "end": v(-28.2, 31.84) * mm});
            skLineSegment(sketch, "E2107", {"start": v(-28.2, 31.84) * mm, "end": v(-27.69, 31.09) * mm});
            skLineSegment(sketch, "E2108", {"start": v(-27.69, 31.09) * mm, "end": v(-26.7, 30.6) * mm});
            skLineSegment(sketch, "E2109", {"start": v(-26.7, 30.6) * mm, "end": v(-25.28, 30.52) * mm});
            skLineSegment(sketch, "E2110", {"start": v(-25.28, 30.52) * mm, "end": v(-24.43, 30.93) * mm});
            skLineSegment(sketch, "E2111", {"start": v(-24.43, 30.93) * mm, "end": v(-23.96, 31.64) * mm});
            skLineSegment(sketch, "E2112", {"start": v(-23.96, 31.64) * mm, "end": v(-23.95, 32.52) * mm});
            skLineSegment(sketch, "E2113", {"start": v(-23.95, 32.52) * mm, "end": v(-24.3, 32.9) * mm});
            skLineSegment(sketch, "E2114", {"start": v(-24.3, 32.9) * mm, "end": v(-24.55, 32.9) * mm});
            skLineSegment(sketch, "E2115", {"start": v(-24.55, 32.9) * mm, "end": v(-24.66, 32.89) * mm});
            skLineSegment(sketch, "E2116", {"start": v(-24.66, 32.89) * mm, "end": v(-24.8, 32.87) * mm});
            skLineSegment(sketch, "E2117", {"start": v(-24.8, 32.87) * mm, "end": v(-24.92, 32.83) * mm});
            skLineSegment(sketch, "E2118", {"start": v(-24.92, 32.83) * mm, "end": v(-25.03, 32.8) * mm});
            skLineSegment(sketch, "E2119", {"start": v(-25.03, 32.8) * mm, "end": v(-25.27, 32.68) * mm});
            skLineSegment(sketch, "E2120", {"start": v(-25.27, 32.68) * mm, "end": v(-25.37, 32.25) * mm});
            skLineSegment(sketch, "E2121", {"start": v(-25.37, 32.25) * mm, "end": v(-25.22, 31.85) * mm});
            skLineSegment(sketch, "E2122", {"start": v(-25.22, 31.85) * mm, "end": v(-25.12, 31.55) * mm});
            skLineSegment(sketch, "E2123", {"start": v(-25.12, 31.55) * mm, "end": v(-25.1, 31.45) * mm});
            skLineSegment(sketch, "E2124", {"start": v(-25.1, 31.45) * mm, "end": v(-25.1, 31.4) * mm});
            skLineSegment(sketch, "E2125", {"start": v(-25.1, 31.4) * mm, "end": v(-25.2, 31.34) * mm});
            skLineSegment(sketch, "E2126", {"start": v(-25.2, 31.34) * mm, "end": v(-25.42, 31.23) * mm});
            skLineSegment(sketch, "E2127", {"start": v(-25.42, 31.23) * mm, "end": v(-25.7, 31.08) * mm});
            skLineSegment(sketch, "E2128", {"start": v(-25.7, 31.08) * mm, "end": v(-26.55, 31.08) * mm});
            skLineSegment(sketch, "E2129", {"start": v(-26.55, 31.08) * mm, "end": v(-27.08, 31.46) * mm});
            skLineSegment(sketch, "E2130", {"start": v(-27.08, 31.46) * mm, "end": v(-27.26, 31.8) * mm});
            skLineSegment(sketch, "E2131", {"start": v(-27.26, 31.8) * mm, "end": v(-27.33, 31.97) * mm});
            skLineSegment(sketch, "E2132", {"start": v(-27.33, 31.97) * mm, "end": v(-27.4, 32.16) * mm});
            skLineSegment(sketch, "E2133", {"start": v(-27.4, 32.16) * mm, "end": v(-27.45, 32.36) * mm});
            skLineSegment(sketch, "E2134", {"start": v(-27.45, 32.36) * mm, "end": v(-27.5, 32.53) * mm});
            skLineSegment(sketch, "E2135", {"start": v(-27.5, 32.53) * mm, "end": v(-27.55, 32.9) * mm});
            skLineSegment(sketch, "E2136", {"start": v(-27.55, 32.9) * mm, "end": v(-27.24, 33.7) * mm});
            skLineSegment(sketch, "E2137", {"start": v(-27.24, 33.7) * mm, "end": v(-26.64, 34.24) * mm});
            skLineSegment(sketch, "E2138", {"start": v(-26.64, 34.24) * mm, "end": v(-25.58, 34.64) * mm});
            skLineSegment(sketch, "E2139", {"start": v(-25.58, 34.64) * mm, "end": v(-23.31, 34.54) * mm});
            skLineSegment(sketch, "E2140", {"start": v(-23.31, 34.54) * mm, "end": v(-22.68, 34.36) * mm});
            skLineSegment(sketch, "E2141", {"start": v(-22.68, 34.36) * mm, "end": v(-22.26, 34.22) * mm});
            skLineSegment(sketch, "E2142", {"start": v(-22.26, 34.22) * mm, "end": v(-21.8, 34.05) * mm});
            skLineSegment(sketch, "E2143", {"start": v(-21.8, 34.05) * mm, "end": v(-21.3, 33.84) * mm});
            skLineSegment(sketch, "E2144", {"start": v(-21.3, 33.84) * mm, "end": v(-20.83, 33.63) * mm});
            skLineSegment(sketch, "E2145", {"start": v(-20.83, 33.63) * mm, "end": v(-20.4, 33.42) * mm});
            skLineSegment(sketch, "E2146", {"start": v(-20.4, 33.42) * mm, "end": v(-20.05, 33.23) * mm});
            skLineSegment(sketch, "E2147", {"start": v(-20.05, 33.23) * mm, "end": v(-19.92, 33.15) * mm});
            skLineSegment(sketch, "E2148", {"start": v(-19.92, 33.15) * mm, "end": v(-19.82, 33.08) * mm});
            skLineSegment(sketch, "E2149", {"start": v(-19.82, 33.08) * mm, "end": v(-19.76, 33.02) * mm});
            skLineSegment(sketch, "E2150", {"start": v(-19.76, 33.02) * mm, "end": v(-19.74, 33) * mm});
            skLineSegment(sketch, "E2151", {"start": v(-19.74, 33) * mm, "end": v(-19.73, 32.98) * mm});
            skLineSegment(sketch, "E2152", {"start": v(-19.73, 32.98) * mm, "end": v(-19.74, 32.96) * mm});
            skLineSegment(sketch, "E2153", {"start": v(-19.74, 32.96) * mm, "end": v(-19.76, 32.94) * mm});
            skLineSegment(sketch, "E2154", {"start": v(-19.76, 32.94) * mm, "end": v(-19.85, 32.88) * mm});
            skLineSegment(sketch, "E2155", {"start": v(-19.85, 32.88) * mm, "end": v(-19.97, 32.8) * mm});
            skLineSegment(sketch, "E2156", {"start": v(-19.97, 32.8) * mm, "end": v(-20.12, 32.73) * mm});
            skLineSegment(sketch, "E2157", {"start": v(-20.12, 32.73) * mm, "end": v(-20.5, 32.56) * mm});
            skLineSegment(sketch, "E2158", {"start": v(-20.5, 32.56) * mm, "end": v(-20.7, 32.34) * mm});
            skLineSegment(sketch, "E2159", {"start": v(-20.7, 32.34) * mm, "end": v(-20.77, 32.24) * mm});
            skLineSegment(sketch, "E2160", {"start": v(-20.77, 32.24) * mm, "end": v(-20.85, 32.12) * mm});
            skLineSegment(sketch, "E2161", {"start": v(-20.85, 32.12) * mm, "end": v(-20.92, 32) * mm});
            skLineSegment(sketch, "E2162", {"start": v(-20.92, 32) * mm, "end": v(-20.99, 31.86) * mm});
            skLineSegment(sketch, "E2163", {"start": v(-20.99, 31.86) * mm, "end": v(-21.04, 31.73) * mm});
            skLineSegment(sketch, "E2164", {"start": v(-21.04, 31.73) * mm, "end": v(-21.07, 31.62) * mm});
            skLineSegment(sketch, "E2165", {"start": v(-21.07, 31.62) * mm, "end": v(-21.09, 31.54) * mm});
            skLineSegment(sketch, "E2166", {"start": v(-21.09, 31.54) * mm, "end": v(-21.09, 31.51) * mm});
            skLineSegment(sketch, "E2167", {"start": v(-21.09, 31.51) * mm, "end": v(-21.08, 31.5) * mm});
            skLineSegment(sketch, "E2168", {"start": v(-21.08, 31.5) * mm, "end": v(-21.06, 31.5) * mm});
            skLineSegment(sketch, "E2169", {"start": v(-21.06, 31.5) * mm, "end": v(-21, 31.5) * mm});
            skLineSegment(sketch, "E2170", {"start": v(-21, 31.5) * mm, "end": v(-20.84, 31.55) * mm});
            skLineSegment(sketch, "E2171", {"start": v(-20.84, 31.55) * mm, "end": v(-20.6, 31.63) * mm});
            skLineSegment(sketch, "E2172", {"start": v(-20.6, 31.63) * mm, "end": v(-20.32, 31.74) * mm});
            skLineSegment(sketch, "E2173", {"start": v(-20.32, 31.74) * mm, "end": v(-19.6, 32.04) * mm});
            skLineSegment(sketch, "E2174", {"start": v(-19.6, 32.04) * mm, "end": v(-17.33, 32.03) * mm});
            skLineSegment(sketch, "E2175", {"start": v(-17.33, 32.03) * mm, "end": v(-14.28, 30.9) * mm});
            skLineSegment(sketch, "E2176", {"start": v(-14.28, 30.9) * mm, "end": v(-13.07, 30.61) * mm});
            skLineSegment(sketch, "E2177", {"start": v(-13.07, 30.61) * mm, "end": v(-11.53, 30.6) * mm});
            skLineSegment(sketch, "E2178", {"start": v(-11.53, 30.6) * mm, "end": v(-10.26, 30.92) * mm});
            skLineSegment(sketch, "E2179", {"start": v(-10.26, 30.92) * mm, "end": v(-8.93, 31.55) * mm});
            skLineSegment(sketch, "E2180", {"start": v(-8.93, 31.55) * mm, "end": v(-7.82, 32.67) * mm});
            skLineSegment(sketch, "E2181", {"start": v(-7.82, 32.67) * mm, "end": v(-7.55, 33.21) * mm});
            skLineSegment(sketch, "E2182", {"start": v(-7.55, 33.21) * mm, "end": v(-7.44, 33.48) * mm});
            skLineSegment(sketch, "E2183", {"start": v(-7.44, 33.48) * mm, "end": v(-7.32, 33.78) * mm});
            skLineSegment(sketch, "E2184", {"start": v(-7.32, 33.78) * mm, "end": v(-7.2, 34.1) * mm});
            skLineSegment(sketch, "E2185", {"start": v(-7.2, 34.1) * mm, "end": v(-7.12, 34.39) * mm});
            skLineSegment(sketch, "E2186", {"start": v(-7.12, 34.39) * mm, "end": v(-6.96, 35.01) * mm});
            skLineSegment(sketch, "E2187", {"start": v(-6.96, 35.01) * mm, "end": v(-6.96, 36.6) * mm});
            skLineSegment(sketch, "E2188", {"start": v(-6.96, 36.6) * mm, "end": v(-7.32, 37.76) * mm});
            skLineSegment(sketch, "E2189", {"start": v(-7.32, 37.76) * mm, "end": v(-7.76, 38.39) * mm});
            skLineSegment(sketch, "E2190", {"start": v(-7.76, 38.39) * mm, "end": v(-8.11, 38.87) * mm});
            skLineSegment(sketch, "E2191", {"start": v(-8.11, 38.87) * mm, "end": v(-8.25, 39.04) * mm});
            skLineSegment(sketch, "E2192", {"start": v(-8.25, 39.04) * mm, "end": v(-8.35, 39.14) * mm});
            skLineSegment(sketch, "E2193", {"start": v(-8.35, 39.14) * mm, "end": v(-8.4, 39.2) * mm});
            skLineSegment(sketch, "E2194", {"start": v(-8.4, 39.2) * mm, "end": v(-8.45, 39.25) * mm});
            skLineSegment(sketch, "E2195", {"start": v(-8.45, 39.25) * mm, "end": v(-8.48, 39.3) * mm});
            skLineSegment(sketch, "E2196", {"start": v(-8.48, 39.3) * mm, "end": v(-8.5, 39.34) * mm});
            skLineSegment(sketch, "E2197", {"start": v(-8.5, 39.34) * mm, "end": v(-8.5, 39.42) * mm});
            skLineSegment(sketch, "E2198", {"start": v(-8.5, 39.42) * mm, "end": v(-8.24, 39.42) * mm});
            skLineSegment(sketch, "E2199", {"start": v(-8.24, 39.42) * mm, "end": v(-8.1, 39.43) * mm});
            skLineSegment(sketch, "E2200", {"start": v(-8.1, 39.43) * mm, "end": v(-7.93, 39.46) * mm});
            skLineSegment(sketch, "E2201", {"start": v(-7.93, 39.46) * mm, "end": v(-7.74, 39.5) * mm});
            skLineSegment(sketch, "E2202", {"start": v(-7.74, 39.5) * mm, "end": v(-7.56, 39.55) * mm});
            skLineSegment(sketch, "E2203", {"start": v(-7.56, 39.55) * mm, "end": v(-7.14, 39.68) * mm});
            skLineSegment(sketch, "E2204", {"start": v(-7.14, 39.68) * mm, "end": v(-7.1, 39.62) * mm});
            skLineSegment(sketch, "E2205", {"start": v(-7.1, 39.62) * mm, "end": v(-7.06, 39.5) * mm});
            skLineSegment(sketch, "E2206", {"start": v(-7.06, 39.5) * mm, "end": v(-7.01, 39.31) * mm});
            skLineSegment(sketch, "E2207", {"start": v(-7.01, 39.31) * mm, "end": v(-6.95, 39.06) * mm});
            skLineSegment(sketch, "E2208", {"start": v(-6.95, 39.06) * mm, "end": v(-6.67, 38.92) * mm});
            skLineSegment(sketch, "E2209", {"start": v(-6.67, 38.92) * mm, "end": v(-6.47, 38.83) * mm});
            skLineSegment(sketch, "E2210", {"start": v(-6.47, 38.83) * mm, "end": v(-6.4, 38.8) * mm});
            skLineSegment(sketch, "E2211", {"start": v(-6.4, 38.8) * mm, "end": v(-6.37, 38.8) * mm});
            skLineSegment(sketch, "E2212", {"start": v(-6.37, 38.8) * mm, "end": v(-6.3, 38.98) * mm});
            skLineSegment(sketch, "E2213", {"start": v(-6.3, 38.98) * mm, "end": v(-6.19, 39.38) * mm});
            skLineSegment(sketch, "E2214", {"start": v(-6.19, 39.38) * mm, "end": v(-6.03, 39.92) * mm});
            skLineSegment(sketch, "E2215", {"start": v(-6.03, 39.92) * mm, "end": v(-4.44, 41.46) * mm});
            skLineSegment(sketch, "E2216", {"start": v(-4.44, 41.46) * mm, "end": v(-4.12, 41.97) * mm});
            skLineSegment(sketch, "E2217", {"start": v(-4.12, 41.97) * mm, "end": v(-4.01, 43.07) * mm});
            skLineSegment(sketch, "E2218", {"start": v(-4.01, 43.07) * mm, "end": v(-3.03, 41.58) * mm});
            skLineSegment(sketch, "E2219", {"start": v(-3.03, 41.58) * mm, "end": v(-2.35, 40.86) * mm});
            skLineSegment(sketch, "E2220", {"start": v(-2.35, 40.86) * mm, "end": v(-2.03, 40.53) * mm});
            skLineSegment(sketch, "E2221", {"start": v(-2.03, 40.53) * mm, "end": v(-1.67, 40.18) * mm});
            skLineSegment(sketch, "E2222", {"start": v(-1.67, 40.18) * mm, "end": v(-1.31, 39.86) * mm});
            skLineSegment(sketch, "E2223", {"start": v(-1.31, 39.86) * mm, "end": v(-1, 39.59) * mm});
            skLineSegment(sketch, "E2224", {"start": v(-1, 39.59) * mm, "end": v(-0.34, 39.05) * mm});
            skLineSegment(sketch, "E2225", {"start": v(-0.34, 39.05) * mm, "end": v(-0.34, 36.12) * mm});
            skLineSegment(sketch, "E2226", {"start": v(-0.34, 36.12) * mm, "end": v(-0.42, 36.2) * mm});
            skLineSegment(sketch, "E2227", {"start": v(-0.42, 36.2) * mm, "end": v(-0.46, 36.27) * mm});
            skLineSegment(sketch, "E2228", {"start": v(-0.46, 36.27) * mm, "end": v(-0.5, 36.38) * mm});
            skLineSegment(sketch, "E2229", {"start": v(-0.5, 36.38) * mm, "end": v(-0.56, 36.51) * mm});
            skLineSegment(sketch, "E2230", {"start": v(-0.56, 36.51) * mm, "end": v(-0.61, 36.66) * mm});
            skLineSegment(sketch, "E2231", {"start": v(-0.61, 36.66) * mm, "end": v(-0.67, 36.82) * mm});
            skLineSegment(sketch, "E2232", {"start": v(-0.67, 36.82) * mm, "end": v(-0.73, 36.99) * mm});
            skLineSegment(sketch, "E2233", {"start": v(-0.73, 36.99) * mm, "end": v(-0.8, 37.15) * mm});
            skLineSegment(sketch, "E2234", {"start": v(-0.8, 37.15) * mm, "end": v(-0.9, 37.32) * mm});
            skLineSegment(sketch, "E2235", {"start": v(-0.9, 37.32) * mm, "end": v(-0.98, 37.48) * mm});
            skLineSegment(sketch, "E2236", {"start": v(-0.98, 37.48) * mm, "end": v(-1.08, 37.63) * mm});
            skLineSegment(sketch, "E2237", {"start": v(-1.08, 37.63) * mm, "end": v(-1.18, 37.78) * mm});
            skLineSegment(sketch, "E2238", {"start": v(-1.18, 37.78) * mm, "end": v(-1.29, 37.93) * mm});
            skLineSegment(sketch, "E2239", {"start": v(-1.29, 37.93) * mm, "end": v(-1.4, 38.07) * mm});
            skLineSegment(sketch, "E2240", {"start": v(-1.4, 38.07) * mm, "end": v(-1.52, 38.2) * mm});
            skLineSegment(sketch, "E2241", {"start": v(-1.52, 38.2) * mm, "end": v(-1.64, 38.33) * mm});
            skLineSegment(sketch, "E2242", {"start": v(-1.64, 38.33) * mm, "end": v(-1.77, 38.45) * mm});
            skLineSegment(sketch, "E2243", {"start": v(-1.77, 38.45) * mm, "end": v(-1.9, 38.55) * mm});
            skLineSegment(sketch, "E2244", {"start": v(-1.9, 38.55) * mm, "end": v(-2.03, 38.65) * mm});
            skLineSegment(sketch, "E2245", {"start": v(-2.03, 38.65) * mm, "end": v(-2.16, 38.74) * mm});
            skLineSegment(sketch, "E2246", {"start": v(-2.16, 38.74) * mm, "end": v(-2.29, 38.82) * mm});
            skLineSegment(sketch, "E2247", {"start": v(-2.29, 38.82) * mm, "end": v(-2.65, 39) * mm});
            skLineSegment(sketch, "E2248", {"start": v(-2.65, 39) * mm, "end": v(-3.92, 39.01) * mm});
            skLineSegment(sketch, "E2249", {"start": v(-3.92, 39.01) * mm, "end": v(-4.75, 38.53) * mm});
            skLineSegment(sketch, "E2250", {"start": v(-4.75, 38.53) * mm, "end": v(-5.47, 37.74) * mm});
            skLineSegment(sketch, "E2251", {"start": v(-5.47, 37.74) * mm, "end": v(-5.72, 37.23) * mm});
            skLineSegment(sketch, "E2252", {"start": v(-5.72, 37.23) * mm, "end": v(-5.82, 36.99) * mm});
            skLineSegment(sketch, "E2253", {"start": v(-5.82, 36.99) * mm, "end": v(-5.93, 36.71) * mm});
            skLineSegment(sketch, "E2254", {"start": v(-5.93, 36.71) * mm, "end": v(-6.02, 36.44) * mm});
            skLineSegment(sketch, "E2255", {"start": v(-6.02, 36.44) * mm, "end": v(-6.1, 36.2) * mm});
            skLineSegment(sketch, "E2256", {"start": v(-6.1, 36.2) * mm, "end": v(-6.23, 35.67) * mm});
            skLineSegment(sketch, "E2257", {"start": v(-6.23, 35.67) * mm, "end": v(-6.23, 33.84) * mm});
            skLineSegment(sketch, "E2258", {"start": v(-6.23, 33.84) * mm, "end": v(-6.1, 33.33) * mm});
            skLineSegment(sketch, "E2259", {"start": v(-6.1, 33.33) * mm, "end": v(-6.03, 33.1) * mm});
            skLineSegment(sketch, "E2260", {"start": v(-6.03, 33.1) * mm, "end": v(-5.93, 32.83) * mm});
            skLineSegment(sketch, "E2261", {"start": v(-5.93, 32.83) * mm, "end": v(-5.83, 32.56) * mm});
            skLineSegment(sketch, "E2262", {"start": v(-5.83, 32.56) * mm, "end": v(-5.73, 32.32) * mm});
            skLineSegment(sketch, "E2263", {"start": v(-5.73, 32.32) * mm, "end": v(-5.49, 31.81) * mm});
            skLineSegment(sketch, "E2264", {"start": v(-5.49, 31.81) * mm, "end": v(-4.76, 31) * mm});
            skLineSegment(sketch, "E2265", {"start": v(-4.76, 31) * mm, "end": v(-3.97, 30.52) * mm});
            skLineSegment(sketch, "E2266", {"start": v(-3.97, 30.52) * mm, "end": v(-2.92, 30.43) * mm});
            skLineSegment(sketch, "E2267", {"start": v(-2.92, 30.43) * mm, "end": v(-1.98, 30.83) * mm});
            skLineSegment(sketch, "E2268", {"start": v(-1.98, 30.83) * mm, "end": v(-1.1, 31.76) * mm});
            skLineSegment(sketch, "E2269", {"start": v(-1.1, 31.76) * mm, "end": v(-0.83, 32.35) * mm});
            skLineSegment(sketch, "E2270", {"start": v(-0.83, 32.35) * mm, "end": v(-0.45, 33.17) * mm});
            skLineSegment(sketch, "E2271", {"start": v(-0.45, 33.17) * mm, "end": v(-0.35, 33.4) * mm});
            skLineSegment(sketch, "E2272", {"start": v(-0.35, 33.4) * mm, "end": v(-0.34, 29.73) * mm});
            skLineSegment(sketch, "E2273", {"start": v(-0.34, 29.73) * mm, "end": v(-35.5, 29.73) * mm});
            skLineSegment(sketch, "E2274", {"start": v(-35.5, 29.73) * mm, "end": v(-35.5, 22.38) * mm});
            skLineSegment(sketch, "E2275", {"start": v(-35.5, 22.38) * mm, "end": v(-0.02, 22.38) * mm});
            skLineSegment(sketch, "E2276", {"start": v(-32.07, 25.09) * mm, "end": v(-32.07, 26.05) * mm});
            skLineSegment(sketch, "E2277", {"start": v(-32.07, 26.05) * mm, "end": v(-31, 28.05) * mm});
            skLineSegment(sketch, "E2278", {"start": v(-31, 28.05) * mm, "end": v(-31.82, 28.05) * mm});
            skLineSegment(sketch, "E2279", {"start": v(-31.82, 28.05) * mm, "end": v(-31.88, 27.76) * mm});
            skLineSegment(sketch, "E2280", {"start": v(-31.88, 27.76) * mm, "end": v(-31.93, 27.62) * mm});
            skLineSegment(sketch, "E2281", {"start": v(-31.93, 27.62) * mm, "end": v(-32, 27.43) * mm});
            skLineSegment(sketch, "E2282", {"start": v(-32, 27.43) * mm, "end": v(-32.09, 27.24) * mm});
            skLineSegment(sketch, "E2283", {"start": v(-32.09, 27.24) * mm, "end": v(-32.2, 27.05) * mm});
            skLineSegment(sketch, "E2284", {"start": v(-32.2, 27.05) * mm, "end": v(-32.44, 26.63) * mm});
            skLineSegment(sketch, "E2285", {"start": v(-32.44, 26.63) * mm, "end": v(-32.51, 26.7) * mm});
            skLineSegment(sketch, "E2286", {"start": v(-32.51, 26.7) * mm, "end": v(-32.58, 26.8) * mm});
            skLineSegment(sketch, "E2287", {"start": v(-32.58, 26.8) * mm, "end": v(-32.67, 26.94) * mm});
            skLineSegment(sketch, "E2288", {"start": v(-32.67, 26.94) * mm, "end": v(-32.88, 27.34) * mm});
            skLineSegment(sketch, "E2289", {"start": v(-32.88, 27.34) * mm, "end": v(-33.07, 27.74) * mm});
            skLineSegment(sketch, "E2290", {"start": v(-33.07, 27.74) * mm, "end": v(-33.12, 27.89) * mm});
            skLineSegment(sketch, "E2291", {"start": v(-33.12, 27.89) * mm, "end": v(-33.15, 27.97) * mm});
            skLineSegment(sketch, "E2292", {"start": v(-33.15, 27.97) * mm, "end": v(-33.15, 28.1) * mm});
            skLineSegment(sketch, "E2293", {"start": v(-33.15, 28.1) * mm, "end": v(-33.55, 28.1) * mm});
            skLineSegment(sketch, "E2294", {"start": v(-33.55, 28.1) * mm, "end": v(-33.71, 28.09) * mm});
            skLineSegment(sketch, "E2295", {"start": v(-33.71, 28.09) * mm, "end": v(-33.84, 28.08) * mm});
            skLineSegment(sketch, "E2296", {"start": v(-33.84, 28.08) * mm, "end": v(-33.93, 28.06) * mm});
            skLineSegment(sketch, "E2297", {"start": v(-33.93, 28.06) * mm, "end": v(-33.95, 28.05) * mm});
            skLineSegment(sketch, "E2298", {"start": v(-33.95, 28.05) * mm, "end": v(-33.96, 28.04) * mm});
            skLineSegment(sketch, "E2299", {"start": v(-33.96, 28.04) * mm, "end": v(-33.95, 28) * mm});
            skLineSegment(sketch, "E2300", {"start": v(-33.95, 28) * mm, "end": v(-33.91, 27.93) * mm});
            skLineSegment(sketch, "E2301", {"start": v(-33.91, 27.93) * mm, "end": v(-33.8, 27.75) * mm});
            skLineSegment(sketch, "E2302", {"start": v(-33.8, 27.75) * mm, "end": v(-33.55, 27.35) * mm});
            skLineSegment(sketch, "E2303", {"start": v(-33.55, 27.35) * mm, "end": v(-33.2, 26.73) * mm});
            skLineSegment(sketch, "E2304", {"start": v(-33.2, 26.73) * mm, "end": v(-32.78, 25.95) * mm});
            skLineSegment(sketch, "E2305", {"start": v(-32.78, 25.95) * mm, "end": v(-32.78, 24.13) * mm});
            skLineSegment(sketch, "E2306", {"start": v(-32.78, 24.13) * mm, "end": v(-32.67, 24.1) * mm});
            skLineSegment(sketch, "E2307", {"start": v(-32.67, 24.1) * mm, "end": v(-32.6, 24.08) * mm});
            skLineSegment(sketch, "E2308", {"start": v(-32.6, 24.08) * mm, "end": v(-32.52, 24.07) * mm});
            skLineSegment(sketch, "E2309", {"start": v(-32.52, 24.07) * mm, "end": v(-32.32, 24.09) * mm});
            skLineSegment(sketch, "E2310", {"start": v(-32.32, 24.09) * mm, "end": v(-32.08, 24.12) * mm});
            skLineSegment(sketch, "E2311", {"start": v(-32.08, 24.12) * mm, "end": v(-32.07, 25.09) * mm});
            skLineSegment(sketch, "E2312", {"start": v(-27.7, 24.43) * mm, "end": v(-27.35, 24.67) * mm});
            skLineSegment(sketch, "E2313", {"start": v(-27.35, 24.67) * mm, "end": v(-26.95, 25.5) * mm});
            skLineSegment(sketch, "E2314", {"start": v(-26.95, 25.5) * mm, "end": v(-26.87, 26.35) * mm});
            skLineSegment(sketch, "E2315", {"start": v(-26.87, 26.35) * mm, "end": v(-27.17, 27.25) * mm});
            skLineSegment(sketch, "E2316", {"start": v(-27.17, 27.25) * mm, "end": v(-27.46, 27.52) * mm});
            skLineSegment(sketch, "E2317", {"start": v(-27.46, 27.52) * mm, "end": v(-27.6, 27.64) * mm});
            skLineSegment(sketch, "E2318", {"start": v(-27.6, 27.64) * mm, "end": v(-27.75, 27.76) * mm});
            skLineSegment(sketch, "E2319", {"start": v(-27.75, 27.76) * mm, "end": v(-27.9, 27.87) * mm});
            skLineSegment(sketch, "E2320", {"start": v(-27.9, 27.87) * mm, "end": v(-28.04, 27.95) * mm});
            skLineSegment(sketch, "E2321", {"start": v(-28.04, 27.95) * mm, "end": v(-28.33, 28.1) * mm});
            skLineSegment(sketch, "E2322", {"start": v(-28.33, 28.1) * mm, "end": v(-29.26, 28.1) * mm});
            skLineSegment(sketch, "E2323", {"start": v(-29.26, 28.1) * mm, "end": v(-29.98, 27.73) * mm});
            skLineSegment(sketch, "E2324", {"start": v(-29.98, 27.73) * mm, "end": v(-30.5, 27.01) * mm});
            skLineSegment(sketch, "E2325", {"start": v(-30.5, 27.01) * mm, "end": v(-30.72, 26.19) * mm});
            skLineSegment(sketch, "E2326", {"start": v(-30.72, 26.19) * mm, "end": v(-30.52, 25.17) * mm});
            skLineSegment(sketch, "E2327", {"start": v(-30.52, 25.17) * mm, "end": v(-30.14, 24.56) * mm});
            skLineSegment(sketch, "E2328", {"start": v(-30.14, 24.56) * mm, "end": v(-29.37, 24.1) * mm});
            skLineSegment(sketch, "E2329", {"start": v(-29.37, 24.1) * mm, "end": v(-28.57, 24.02) * mm});
            skLineSegment(sketch, "E2330", {"start": v(-28.57, 24.02) * mm, "end": v(-28.31, 24.1) * mm});
            skLineSegment(sketch, "E2331", {"start": v(-28.31, 24.1) * mm, "end": v(-28.18, 24.16) * mm});
            skLineSegment(sketch, "E2332", {"start": v(-28.18, 24.16) * mm, "end": v(-28.02, 24.23) * mm});
            skLineSegment(sketch, "E2333", {"start": v(-28.02, 24.23) * mm, "end": v(-27.86, 24.33) * mm});
            skLineSegment(sketch, "E2334", {"start": v(-27.86, 24.33) * mm, "end": v(-27.7, 24.43) * mm});
            skLineSegment(sketch, "E2335", {"start": v(-24.17, 24.24) * mm, "end": v(-24.17, 24.1) * mm});
            skLineSegment(sketch, "E2336", {"start": v(-24.17, 24.1) * mm, "end": v(-23.34, 24.1) * mm});
            skLineSegment(sketch, "E2337", {"start": v(-23.34, 24.1) * mm, "end": v(-23.45, 24.4) * mm});
            skLineSegment(sketch, "E2338", {"start": v(-23.45, 24.4) * mm, "end": v(-23.45, 28.1) * mm});
            skLineSegment(sketch, "E2339", {"start": v(-23.45, 28.1) * mm, "end": v(-24.18, 28.1) * mm});
            skLineSegment(sketch, "E2340", {"start": v(-24.18, 28.1) * mm, "end": v(-24.14, 25.08) * mm});
            skLineSegment(sketch, "E2341", {"start": v(-24.14, 25.08) * mm, "end": v(-24.72, 24.56) * mm});
            skLineSegment(sketch, "E2342", {"start": v(-24.72, 24.56) * mm, "end": v(-25.28, 24.56) * mm});
            skLineSegment(sketch, "E2343", {"start": v(-25.28, 24.56) * mm, "end": v(-25.78, 25.06) * mm});
            skLineSegment(sketch, "E2344", {"start": v(-25.78, 25.06) * mm, "end": v(-25.9, 25.82) * mm});
            skLineSegment(sketch, "E2345", {"start": v(-25.9, 25.82) * mm, "end": v(-25.84, 28.1) * mm});
            skLineSegment(sketch, "E2346", {"start": v(-25.84, 28.1) * mm, "end": v(-26.55, 28.05) * mm});
            skLineSegment(sketch, "E2347", {"start": v(-26.55, 28.05) * mm, "end": v(-26.52, 25.56) * mm});
            skLineSegment(sketch, "E2348", {"start": v(-26.52, 25.56) * mm, "end": v(-26.25, 24.64) * mm});
            skLineSegment(sketch, "E2349", {"start": v(-26.25, 24.64) * mm, "end": v(-25.75, 24.09) * mm});
            skLineSegment(sketch, "E2350", {"start": v(-25.75, 24.09) * mm, "end": v(-24.94, 24) * mm});
            skLineSegment(sketch, "E2351", {"start": v(-24.94, 24) * mm, "end": v(-24.17, 24.37) * mm});
            skLineSegment(sketch, "E2352", {"start": v(-24.17, 24.37) * mm, "end": v(-24.17, 24.24) * mm});
            skLineSegment(sketch, "E2353", {"start": v(-19.92, 24.43) * mm, "end": v(-19.88, 24.56) * mm});
            skLineSegment(sketch, "E2354", {"start": v(-19.88, 24.56) * mm, "end": v(-19.86, 24.67) * mm});
            skLineSegment(sketch, "E2355", {"start": v(-19.86, 24.67) * mm, "end": v(-19.84, 24.76) * mm});
            skLineSegment(sketch, "E2356", {"start": v(-19.84, 24.76) * mm, "end": v(-19.85, 24.8) * mm});
            skLineSegment(sketch, "E2357", {"start": v(-19.85, 24.8) * mm, "end": v(-19.87, 24.8) * mm});
            skLineSegment(sketch, "E2358", {"start": v(-19.87, 24.8) * mm, "end": v(-19.9, 24.8) * mm});
            skLineSegment(sketch, "E2359", {"start": v(-19.9, 24.8) * mm, "end": v(-20.02, 24.79) * mm});
            skLineSegment(sketch, "E2360", {"start": v(-20.02, 24.79) * mm, "end": v(-20.19, 24.75) * mm});
            skLineSegment(sketch, "E2361", {"start": v(-20.19, 24.75) * mm, "end": v(-20.38, 24.7) * mm});
            skLineSegment(sketch, "E2362", {"start": v(-20.38, 24.7) * mm, "end": v(-20.58, 24.65) * mm});
            skLineSegment(sketch, "E2363", {"start": v(-20.58, 24.65) * mm, "end": v(-20.78, 24.6) * mm});
            skLineSegment(sketch, "E2364", {"start": v(-20.78, 24.6) * mm, "end": v(-20.95, 24.57) * mm});
            skLineSegment(sketch, "E2365", {"start": v(-20.95, 24.57) * mm, "end": v(-21.07, 24.56) * mm});
            skLineSegment(sketch, "E2366", {"start": v(-21.07, 24.56) * mm, "end": v(-21.3, 24.56) * mm});
            skLineSegment(sketch, "E2367", {"start": v(-21.3, 24.56) * mm, "end": v(-21.23, 28.1) * mm});
            skLineSegment(sketch, "E2368", {"start": v(-21.23, 28.1) * mm, "end": v(-21.9, 28.1) * mm});
            skLineSegment(sketch, "E2369", {"start": v(-21.9, 28.1) * mm, "end": v(-21.9, 24.1) * mm});
            skLineSegment(sketch, "E2370", {"start": v(-21.9, 24.1) * mm, "end": v(-21.83, 24.1) * mm});
            skLineSegment(sketch, "E2371", {"start": v(-21.83, 24.1) * mm, "end": v(-21.73, 24.1) * mm});
            skLineSegment(sketch, "E2372", {"start": v(-21.73, 24.1) * mm, "end": v(-21.62, 24.08) * mm});
            skLineSegment(sketch, "E2373", {"start": v(-21.62, 24.08) * mm, "end": v(-21.52, 24.07) * mm});
            skLineSegment(sketch, "E2374", {"start": v(-21.52, 24.07) * mm, "end": v(-21.32, 24.07) * mm});
            skLineSegment(sketch, "E2375", {"start": v(-21.32, 24.07) * mm, "end": v(-20.77, 24.08) * mm});
            skLineSegment(sketch, "E2376", {"start": v(-20.77, 24.08) * mm, "end": v(-20.04, 24.11) * mm});
            skLineSegment(sketch, "E2377", {"start": v(-20.04, 24.11) * mm, "end": v(-19.92, 24.43) * mm});
            skLineSegment(sketch, "E2378", {"start": v(-17.53, 24.41) * mm, "end": v(-17.46, 24.55) * mm});
            skLineSegment(sketch, "E2379", {"start": v(-17.46, 24.55) * mm, "end": v(-17.42, 24.66) * mm});
            skLineSegment(sketch, "E2380", {"start": v(-17.42, 24.66) * mm, "end": v(-17.4, 24.75) * mm});
            skLineSegment(sketch, "E2381", {"start": v(-17.4, 24.75) * mm, "end": v(-17.4, 24.78) * mm});
            skLineSegment(sketch, "E2382", {"start": v(-17.4, 24.78) * mm, "end": v(-17.4, 24.8) * mm});
            skLineSegment(sketch, "E2383", {"start": v(-17.4, 24.8) * mm, "end": v(-17.42, 24.8) * mm});
            skLineSegment(sketch, "E2384", {"start": v(-17.42, 24.8) * mm, "end": v(-17.46, 24.8) * mm});
            skLineSegment(sketch, "E2385", {"start": v(-17.46, 24.8) * mm, "end": v(-17.6, 24.78) * mm});
            skLineSegment(sketch, "E2386", {"start": v(-17.6, 24.78) * mm, "end": v(-17.78, 24.74) * mm});
            skLineSegment(sketch, "E2387", {"start": v(-17.78, 24.74) * mm, "end": v(-18, 24.69) * mm});
            skLineSegment(sketch, "E2388", {"start": v(-18, 24.69) * mm, "end": v(-18.54, 24.53) * mm});
            skLineSegment(sketch, "E2389", {"start": v(-18.54, 24.53) * mm, "end": v(-18.84, 24.65) * mm});
            skLineSegment(sketch, "E2390", {"start": v(-18.84, 24.65) * mm, "end": v(-18.78, 28.1) * mm});
            skLineSegment(sketch, "E2391", {"start": v(-18.78, 28.1) * mm, "end": v(-19.46, 28.1) * mm});
            skLineSegment(sketch, "E2392", {"start": v(-19.46, 28.1) * mm, "end": v(-19.46, 24.1) * mm});
            skLineSegment(sketch, "E2393", {"start": v(-19.46, 24.1) * mm, "end": v(-19.33, 24.1) * mm});
            skLineSegment(sketch, "E2394", {"start": v(-19.33, 24.1) * mm, "end": v(-19.2, 24.1) * mm});
            skLineSegment(sketch, "E2395", {"start": v(-19.2, 24.1) * mm, "end": v(-19.08, 24.08) * mm});
            skLineSegment(sketch, "E2396", {"start": v(-19.08, 24.08) * mm, "end": v(-18.81, 24.07) * mm});
            skLineSegment(sketch, "E2397", {"start": v(-18.81, 24.07) * mm, "end": v(-18.33, 24.07) * mm});
            skLineSegment(sketch, "E2398", {"start": v(-18.33, 24.07) * mm, "end": v(-17.7, 24.08) * mm});
            skLineSegment(sketch, "E2399", {"start": v(-17.7, 24.08) * mm, "end": v(-17.53, 24.41) * mm});
            skLineSegment(sketch, "E2400", {"start": v(-14.74, 25.29) * mm, "end": v(-14.77, 26.46) * mm});
            skLineSegment(sketch, "E2401", {"start": v(-14.77, 26.46) * mm, "end": v(-14.61, 26.46) * mm});
            skLineSegment(sketch, "E2402", {"start": v(-14.61, 26.46) * mm, "end": v(-12.92, 24.1) * mm});
            skLineSegment(sketch, "E2403", {"start": v(-12.92, 24.1) * mm, "end": v(-12.26, 24.1) * mm});
            skLineSegment(sketch, "E2404", {"start": v(-12.26, 24.1) * mm, "end": v(-12.3, 28.05) * mm});
            skLineSegment(sketch, "E2405", {"start": v(-12.3, 28.05) * mm, "end": v(-12.98, 28.1) * mm});
            skLineSegment(sketch, "E2406", {"start": v(-12.98, 28.1) * mm, "end": v(-12.92, 25.38) * mm});
            skLineSegment(sketch, "E2407", {"start": v(-12.92, 25.38) * mm, "end": v(-13.07, 25.38) * mm});
            skLineSegment(sketch, "E2408", {"start": v(-13.07, 25.38) * mm, "end": v(-14.61, 27.57) * mm});
            skLineSegment(sketch, "E2409", {"start": v(-14.61, 27.57) * mm, "end": v(-15.04, 28.1) * mm});
            skLineSegment(sketch, "E2410", {"start": v(-15.04, 28.1) * mm, "end": v(-15.75, 28.1) * mm});
            skLineSegment(sketch, "E2411", {"start": v(-15.75, 28.1) * mm, "end": v(-15.75, 28.02) * mm});
            skLineSegment(sketch, "E2412", {"start": v(-15.75, 28.02) * mm, "end": v(-15.73, 27.97) * mm});
            skLineSegment(sketch, "E2413", {"start": v(-15.73, 27.97) * mm, "end": v(-15.7, 27.91) * mm});
            skLineSegment(sketch, "E2414", {"start": v(-15.7, 27.91) * mm, "end": v(-15.63, 27.84) * mm});
            skLineSegment(sketch, "E2415", {"start": v(-15.63, 27.84) * mm, "end": v(-15.56, 27.77) * mm});
            skLineSegment(sketch, "E2416", {"start": v(-15.56, 27.77) * mm, "end": v(-15.37, 27.6) * mm});
            skLineSegment(sketch, "E2417", {"start": v(-15.37, 27.6) * mm, "end": v(-15.43, 24.12) * mm});
            skLineSegment(sketch, "E2418", {"start": v(-15.43, 24.12) * mm, "end": v(-15.25, 24.09) * mm});
            skLineSegment(sketch, "E2419", {"start": v(-15.25, 24.09) * mm, "end": v(-15.07, 24.07) * mm});
            skLineSegment(sketch, "E2420", {"start": v(-15.07, 24.07) * mm, "end": v(-14.89, 24.09) * mm});
            skLineSegment(sketch, "E2421", {"start": v(-14.89, 24.09) * mm, "end": v(-14.7, 24.11) * mm});
            skLineSegment(sketch, "E2422", {"start": v(-14.7, 24.11) * mm, "end": v(-14.74, 25.29) * mm});
            skLineSegment(sketch, "E2423", {"start": v(-9.75, 24.41) * mm, "end": v(-9.58, 24.74) * mm});
            skLineSegment(sketch, "E2424", {"start": v(-9.58, 24.74) * mm, "end": v(-9.67, 24.74) * mm});
            skLineSegment(sketch, "E2425", {"start": v(-9.67, 24.74) * mm, "end": v(-9.9, 24.7) * mm});
            skLineSegment(sketch, "E2426", {"start": v(-9.9, 24.7) * mm, "end": v(-10.36, 24.6) * mm});
            skLineSegment(sketch, "E2427", {"start": v(-10.36, 24.6) * mm, "end": v(-10.97, 24.46) * mm});
            skLineSegment(sketch, "E2428", {"start": v(-10.97, 24.46) * mm, "end": v(-11.22, 24.55) * mm});
            skLineSegment(sketch, "E2429", {"start": v(-11.22, 24.55) * mm, "end": v(-11.22, 25.82) * mm});
            skLineSegment(sketch, "E2430", {"start": v(-11.22, 25.82) * mm, "end": v(-11.04, 25.93) * mm});
            skLineSegment(sketch, "E2431", {"start": v(-11.04, 25.93) * mm, "end": v(-10.35, 25.74) * mm});
            skLineSegment(sketch, "E2432", {"start": v(-10.35, 25.74) * mm, "end": v(-10.2, 25.93) * mm});
            skLineSegment(sketch, "E2433", {"start": v(-10.2, 25.93) * mm, "end": v(-10.13, 26.01) * mm});
            skLineSegment(sketch, "E2434", {"start": v(-10.13, 26.01) * mm, "end": v(-10.08, 26.1) * mm});
            skLineSegment(sketch, "E2435", {"start": v(-10.08, 26.1) * mm, "end": v(-10.05, 26.18) * mm});
            skLineSegment(sketch, "E2436", {"start": v(-10.05, 26.18) * mm, "end": v(-10.04, 26.25) * mm});
            skLineSegment(sketch, "E2437", {"start": v(-10.04, 26.25) * mm, "end": v(-10.04, 26.37) * mm});
            skLineSegment(sketch, "E2438", {"start": v(-10.04, 26.37) * mm, "end": v(-11.22, 26.37) * mm});
            skLineSegment(sketch, "E2439", {"start": v(-11.22, 26.37) * mm, "end": v(-11.17, 27.6) * mm});
            skLineSegment(sketch, "E2440", {"start": v(-11.17, 27.6) * mm, "end": v(-10.99, 27.58) * mm});
            skLineSegment(sketch, "E2441", {"start": v(-10.99, 27.58) * mm, "end": v(-10.75, 27.56) * mm});
            skLineSegment(sketch, "E2442", {"start": v(-10.75, 27.56) * mm, "end": v(-10.44, 27.5) * mm});
            skLineSegment(sketch, "E2443", {"start": v(-10.44, 27.5) * mm, "end": v(-10.07, 27.44) * mm});
            skLineSegment(sketch, "E2444", {"start": v(-10.07, 27.44) * mm, "end": v(-9.96, 27.68) * mm});
            skLineSegment(sketch, "E2445", {"start": v(-9.96, 27.68) * mm, "end": v(-9.89, 27.88) * mm});
            skLineSegment(sketch, "E2446", {"start": v(-9.89, 27.88) * mm, "end": v(-9.86, 27.96) * mm});
            skLineSegment(sketch, "E2447", {"start": v(-9.86, 27.96) * mm, "end": v(-9.86, 28.01) * mm});
            skLineSegment(sketch, "E2448", {"start": v(-9.86, 28.01) * mm, "end": v(-9.86, 28.1) * mm});
            skLineSegment(sketch, "E2449", {"start": v(-9.86, 28.1) * mm, "end": v(-11.86, 28.05) * mm});
            skLineSegment(sketch, "E2450", {"start": v(-11.86, 28.05) * mm, "end": v(-11.9, 24.12) * mm});
            skLineSegment(sketch, "E2451", {"start": v(-11.9, 24.12) * mm, "end": v(-11.49, 24.1) * mm});
            skLineSegment(sketch, "E2452", {"start": v(-11.49, 24.1) * mm, "end": v(-11.03, 24.07) * mm});
            skLineSegment(sketch, "E2453", {"start": v(-11.03, 24.07) * mm, "end": v(-10.5, 24.07) * mm});
            skLineSegment(sketch, "E2454", {"start": v(-10.5, 24.07) * mm, "end": v(-9.92, 24.08) * mm});
            skLineSegment(sketch, "E2455", {"start": v(-9.92, 24.08) * mm, "end": v(-9.75, 24.41) * mm});
            skLineSegment(sketch, "E2456", {"start": v(-7.21, 24.2) * mm, "end": v(-6.37, 26.18) * mm});
            skLineSegment(sketch, "E2457", {"start": v(-6.37, 26.18) * mm, "end": v(-5.6, 28.02) * mm});
            skLineSegment(sketch, "E2458", {"start": v(-5.6, 28.02) * mm, "end": v(-5.6, 28.06) * mm});
            skLineSegment(sketch, "E2459", {"start": v(-5.6, 28.06) * mm, "end": v(-5.63, 28.07) * mm});
            skLineSegment(sketch, "E2460", {"start": v(-5.63, 28.07) * mm, "end": v(-5.73, 28.08) * mm});
            skLineSegment(sketch, "E2461", {"start": v(-5.73, 28.08) * mm, "end": v(-6.05, 28.1) * mm});
            skLineSegment(sketch, "E2462", {"start": v(-6.05, 28.1) * mm, "end": v(-6.5, 28.1) * mm});
            skLineSegment(sketch, "E2463", {"start": v(-6.5, 28.1) * mm, "end": v(-6.5, 27.73) * mm});
            skLineSegment(sketch, "E2464", {"start": v(-6.5, 27.73) * mm, "end": v(-7.43, 25.27) * mm});
            skLineSegment(sketch, "E2465", {"start": v(-7.43, 25.27) * mm, "end": v(-7.58, 25.42) * mm});
            skLineSegment(sketch, "E2466", {"start": v(-7.58, 25.42) * mm, "end": v(-8.4, 27.75) * mm});
            skLineSegment(sketch, "E2467", {"start": v(-8.4, 27.75) * mm, "end": v(-8.4, 28.1) * mm});
            skLineSegment(sketch, "E2468", {"start": v(-8.4, 28.1) * mm, "end": v(-9.27, 28.05) * mm});
            skLineSegment(sketch, "E2469", {"start": v(-9.27, 28.05) * mm, "end": v(-9.23, 27.87) * mm});
            skLineSegment(sketch, "E2470", {"start": v(-9.23, 27.87) * mm, "end": v(-7.79, 24.18) * mm});
            skLineSegment(sketch, "E2471", {"start": v(-7.79, 24.18) * mm, "end": v(-7.71, 24.11) * mm});
            skLineSegment(sketch, "E2472", {"start": v(-7.71, 24.11) * mm, "end": v(-7.67, 24.09) * mm});
            skLineSegment(sketch, "E2473", {"start": v(-7.67, 24.09) * mm, "end": v(-7.6, 24.07) * mm});
            skLineSegment(sketch, "E2474", {"start": v(-7.6, 24.07) * mm, "end": v(-7.54, 24.06) * mm});
            skLineSegment(sketch, "E2475", {"start": v(-7.54, 24.06) * mm, "end": v(-7.46, 24.05) * mm});
            skLineSegment(sketch, "E2476", {"start": v(-7.46, 24.05) * mm, "end": v(-7.3, 24.06) * mm});
            skLineSegment(sketch, "E2477", {"start": v(-7.3, 24.06) * mm, "end": v(-7.21, 24.2) * mm});
            skLineSegment(sketch, "E2478", {"start": v(-3.07, 24.37) * mm, "end": v(-3.02, 24.48) * mm});
            skLineSegment(sketch, "E2479", {"start": v(-3.02, 24.48) * mm, "end": v(-2.99, 24.58) * mm});
            skLineSegment(sketch, "E2480", {"start": v(-2.99, 24.58) * mm, "end": v(-2.97, 24.65) * mm});
            skLineSegment(sketch, "E2481", {"start": v(-2.97, 24.65) * mm, "end": v(-2.97, 24.68) * mm});
            skLineSegment(sketch, "E2482", {"start": v(-2.97, 24.68) * mm, "end": v(-2.98, 24.7) * mm});
            skLineSegment(sketch, "E2483", {"start": v(-2.98, 24.7) * mm, "end": v(-3, 24.7) * mm});
            skLineSegment(sketch, "E2484", {"start": v(-3, 24.7) * mm, "end": v(-3.05, 24.7) * mm});
            skLineSegment(sketch, "E2485", {"start": v(-3.05, 24.7) * mm, "end": v(-3.2, 24.69) * mm});
            skLineSegment(sketch, "E2486", {"start": v(-3.2, 24.69) * mm, "end": v(-3.4, 24.66) * mm});
            skLineSegment(sketch, "E2487", {"start": v(-3.4, 24.66) * mm, "end": v(-3.64, 24.6) * mm});
            skLineSegment(sketch, "E2488", {"start": v(-3.64, 24.6) * mm, "end": v(-4.25, 24.48) * mm});
            skLineSegment(sketch, "E2489", {"start": v(-4.25, 24.48) * mm, "end": v(-4.52, 24.58) * mm});
            skLineSegment(sketch, "E2490", {"start": v(-4.52, 24.58) * mm, "end": v(-4.46, 25.87) * mm});
            skLineSegment(sketch, "E2491", {"start": v(-4.46, 25.87) * mm, "end": v(-4.28, 25.87) * mm});
            skLineSegment(sketch, "E2492", {"start": v(-4.28, 25.87) * mm, "end": v(-4.07, 25.84) * mm});
            skLineSegment(sketch, "E2493", {"start": v(-4.07, 25.84) * mm, "end": v(-3.82, 25.8) * mm});
            skLineSegment(sketch, "E2494", {"start": v(-3.82, 25.8) * mm, "end": v(-3.54, 25.73) * mm});
            skLineSegment(sketch, "E2495", {"start": v(-3.54, 25.73) * mm, "end": v(-3.44, 25.96) * mm});
            skLineSegment(sketch, "E2496", {"start": v(-3.44, 25.96) * mm, "end": v(-3.36, 26.16) * mm});
            skLineSegment(sketch, "E2497", {"start": v(-3.36, 26.16) * mm, "end": v(-3.34, 26.23) * mm});
            skLineSegment(sketch, "E2498", {"start": v(-3.34, 26.23) * mm, "end": v(-3.33, 26.29) * mm});
            skLineSegment(sketch, "E2499", {"start": v(-3.33, 26.29) * mm, "end": v(-3.33, 26.37) * mm});
            skLineSegment(sketch, "E2500", {"start": v(-3.33, 26.37) * mm, "end": v(-4.52, 26.37) * mm});
            skLineSegment(sketch, "E2501", {"start": v(-4.52, 26.37) * mm, "end": v(-4.46, 27.6) * mm});
            skLineSegment(sketch, "E2502", {"start": v(-4.46, 27.6) * mm, "end": v(-4.24, 27.58) * mm});
            skLineSegment(sketch, "E2503", {"start": v(-4.24, 27.58) * mm, "end": v(-3.98, 27.55) * mm});
            skLineSegment(sketch, "E2504", {"start": v(-3.98, 27.55) * mm, "end": v(-3.68, 27.5) * mm});
            skLineSegment(sketch, "E2505", {"start": v(-3.68, 27.5) * mm, "end": v(-3.36, 27.44) * mm});
            skLineSegment(sketch, "E2506", {"start": v(-3.36, 27.44) * mm, "end": v(-3.3, 27.6) * mm});
            skLineSegment(sketch, "E2507", {"start": v(-3.3, 27.6) * mm, "end": v(-3.26, 27.77) * mm});
            skLineSegment(sketch, "E2508", {"start": v(-3.26, 27.77) * mm, "end": v(-3.2, 27.94) * mm});
            skLineSegment(sketch, "E2509", {"start": v(-3.2, 27.94) * mm, "end": v(-3.13, 28.1) * mm});
            skLineSegment(sketch, "E2510", {"start": v(-3.13, 28.1) * mm, "end": v(-5.14, 28.1) * mm});
            skLineSegment(sketch, "E2511", {"start": v(-5.14, 28.1) * mm, "end": v(-5.14, 24.4) * mm});
            skLineSegment(sketch, "E2512", {"start": v(-5.14, 24.4) * mm, "end": v(-5.24, 24.13) * mm});
            skLineSegment(sketch, "E2513", {"start": v(-5.24, 24.13) * mm, "end": v(-5, 24.1) * mm});
            skLineSegment(sketch, "E2514", {"start": v(-5, 24.1) * mm, "end": v(-4.83, 24.08) * mm});
            skLineSegment(sketch, "E2515", {"start": v(-4.83, 24.08) * mm, "end": v(-4.59, 24.07) * mm});
            skLineSegment(sketch, "E2516", {"start": v(-4.59, 24.07) * mm, "end": v(-3.97, 24.07) * mm});
            skLineSegment(sketch, "E2517", {"start": v(-3.97, 24.07) * mm, "end": v(-3.2, 24.09) * mm});
            skLineSegment(sketch, "E2518", {"start": v(-3.2, 24.09) * mm, "end": v(-3.07, 24.37) * mm});
            skLineSegment(sketch, "E2519", {"start": v(-1.84, 24.96) * mm, "end": v(-1.84, 25.78) * mm});
            skLineSegment(sketch, "E2520", {"start": v(-1.84, 25.78) * mm, "end": v(-1.48, 25.33) * mm});
            skLineSegment(sketch, "E2521", {"start": v(-1.48, 25.33) * mm, "end": v(-1.3, 25.12) * mm});
            skLineSegment(sketch, "E2522", {"start": v(-1.3, 25.12) * mm, "end": v(-1.1, 24.9) * mm});
            skLineSegment(sketch, "E2523", {"start": v(-1.1, 24.9) * mm, "end": v(-0.87, 24.68) * mm});
            skLineSegment(sketch, "E2524", {"start": v(-0.87, 24.68) * mm, "end": v(-0.67, 24.5) * mm});
            skLineSegment(sketch, "E2525", {"start": v(-0.67, 24.5) * mm, "end": v(-0.21, 24.1) * mm});
            skLineSegment(sketch, "E2526", {"start": v(-0.21, 24.1) * mm, "end": v(0.43, 24.1) * mm});
            skLineSegment(sketch, "E2527", {"start": v(0.43, 24.1) * mm, "end": v(0.04, 24.45) * mm});
            skLineSegment(sketch, "E2528", {"start": v(0.04, 24.45) * mm, "end": v(-0.13, 24.62) * mm});
            skLineSegment(sketch, "E2529", {"start": v(-0.13, 24.62) * mm, "end": v(-0.33, 24.83) * mm});
            skLineSegment(sketch, "E2530", {"start": v(-0.33, 24.83) * mm, "end": v(-0.53, 25.06) * mm});
            skLineSegment(sketch, "E2531", {"start": v(-0.53, 25.06) * mm, "end": v(-0.7, 25.28) * mm});
            skLineSegment(sketch, "E2532", {"start": v(-0.7, 25.28) * mm, "end": v(-1.06, 25.77) * mm});
            skLineSegment(sketch, "E2533", {"start": v(-1.06, 25.77) * mm, "end": v(-0.34, 26.55) * mm});
            skLineSegment(sketch, "E2534", {"start": v(-0.34, 26.55) * mm, "end": v(-0.34, 27.3) * mm});
            skLineSegment(sketch, "E2535", {"start": v(-0.34, 27.3) * mm, "end": v(-1.04, 27.98) * mm});
            skLineSegment(sketch, "E2536", {"start": v(-1.04, 27.98) * mm, "end": v(-1.34, 28.04) * mm});
            skLineSegment(sketch, "E2537", {"start": v(-1.34, 28.04) * mm, "end": v(-1.49, 28.06) * mm});
            skLineSegment(sketch, "E2538", {"start": v(-1.49, 28.06) * mm, "end": v(-1.68, 28.08) * mm});
            skLineSegment(sketch, "E2539", {"start": v(-1.68, 28.08) * mm, "end": v(-1.9, 28.09) * mm});
            skLineSegment(sketch, "E2540", {"start": v(-1.9, 28.09) * mm, "end": v(-2.1, 28.1) * mm});
            skLineSegment(sketch, "E2541", {"start": v(-2.1, 28.1) * mm, "end": v(-2.56, 28.1) * mm});
            skLineSegment(sketch, "E2542", {"start": v(-2.56, 28.1) * mm, "end": v(-2.56, 24.12) * mm});
            skLineSegment(sketch, "E2543", {"start": v(-2.56, 24.12) * mm, "end": v(-2.26, 24.09) * mm});
            skLineSegment(sketch, "E2544", {"start": v(-2.26, 24.09) * mm, "end": v(-2.14, 24.08) * mm});
            skLineSegment(sketch, "E2545", {"start": v(-2.14, 24.08) * mm, "end": v(-2.04, 24.08) * mm});
            skLineSegment(sketch, "E2546", {"start": v(-2.04, 24.08) * mm, "end": v(-1.95, 24.08) * mm});
            skLineSegment(sketch, "E2547", {"start": v(-1.95, 24.08) * mm, "end": v(-1.9, 24.1) * mm});
            skLineSegment(sketch, "E2548", {"start": v(-1.9, 24.1) * mm, "end": v(-1.84, 24.15) * mm});
            skLineSegment(sketch, "E2549", {"start": v(-1.84, 24.15) * mm, "end": v(-1.84, 24.96) * mm});
            skLineSegment(sketch, "E2550", {"start": v(3.94, 25.01) * mm, "end": v(4.3, 26.05) * mm});
            skLineSegment(sketch, "E2551", {"start": v(4.3, 26.05) * mm, "end": v(4.35, 26.15) * mm});
            skLineSegment(sketch, "E2552", {"start": v(4.35, 26.15) * mm, "end": v(4.93, 24.34) * mm});
            skLineSegment(sketch, "E2553", {"start": v(4.93, 24.34) * mm, "end": v(5.08, 24.07) * mm});
            skLineSegment(sketch, "E2554", {"start": v(5.08, 24.07) * mm, "end": v(5.48, 24.04) * mm});
            skLineSegment(sketch, "E2555", {"start": v(5.48, 24.04) * mm, "end": v(5.64, 24.42) * mm});
            skLineSegment(sketch, "E2556", {"start": v(5.64, 24.42) * mm, "end": v(6.46, 27.69) * mm});
            skLineSegment(sketch, "E2557", {"start": v(6.46, 27.69) * mm, "end": v(6.57, 28.1) * mm});
            skLineSegment(sketch, "E2558", {"start": v(6.57, 28.1) * mm, "end": v(5.87, 28.1) * mm});
            skLineSegment(sketch, "E2559", {"start": v(5.87, 28.1) * mm, "end": v(5.23, 25.42) * mm});
            skLineSegment(sketch, "E2560", {"start": v(5.23, 25.42) * mm, "end": v(4.35, 28.01) * mm});
            skLineSegment(sketch, "E2561", {"start": v(4.35, 28.01) * mm, "end": v(4.24, 27.9) * mm});
            skLineSegment(sketch, "E2562", {"start": v(4.24, 27.9) * mm, "end": v(3.4, 25.42) * mm});
            skLineSegment(sketch, "E2563", {"start": v(3.4, 25.42) * mm, "end": v(3.25, 25.92) * mm});
            skLineSegment(sketch, "E2564", {"start": v(3.25, 25.92) * mm, "end": v(3.09, 26.52) * mm});
            skLineSegment(sketch, "E2565", {"start": v(3.09, 26.52) * mm, "end": v(2.9, 27.25) * mm});
            skLineSegment(sketch, "E2566", {"start": v(2.9, 27.25) * mm, "end": v(2.7, 28.1) * mm});
            skLineSegment(sketch, "E2567", {"start": v(2.7, 28.1) * mm, "end": v(2, 28.1) * mm});
            skLineSegment(sketch, "E2568", {"start": v(2, 28.1) * mm, "end": v(2.11, 27.79) * mm});
            skLineSegment(sketch, "E2569", {"start": v(2.11, 27.79) * mm, "end": v(3.03, 24.33) * mm});
            skLineSegment(sketch, "E2570", {"start": v(3.03, 24.33) * mm, "end": v(3.12, 24.17) * mm});
            skLineSegment(sketch, "E2571", {"start": v(3.12, 24.17) * mm, "end": v(3.16, 24.11) * mm});
            skLineSegment(sketch, "E2572", {"start": v(3.16, 24.11) * mm, "end": v(3.2, 24.07) * mm});
            skLineSegment(sketch, "E2573", {"start": v(3.2, 24.07) * mm, "end": v(3.25, 24.04) * mm});
            skLineSegment(sketch, "E2574", {"start": v(3.25, 24.04) * mm, "end": v(3.29, 24.03) * mm});
            skLineSegment(sketch, "E2575", {"start": v(3.29, 24.03) * mm, "end": v(3.49, 24.05) * mm});
            skLineSegment(sketch, "E2576", {"start": v(3.49, 24.05) * mm, "end": v(3.6, 24.06) * mm});
            skLineSegment(sketch, "E2577", {"start": v(3.6, 24.06) * mm, "end": v(3.94, 25.01) * mm});
            skLineSegment(sketch, "E2578", {"start": v(8.03, 24.7) * mm, "end": v(8.29, 25.28) * mm});
            skLineSegment(sketch, "E2579", {"start": v(8.29, 25.28) * mm, "end": v(9.6, 25.28) * mm});
            skLineSegment(sketch, "E2580", {"start": v(9.6, 25.28) * mm, "end": v(9.8, 24.84) * mm});
            skLineSegment(sketch, "E2581", {"start": v(9.8, 24.84) * mm, "end": v(9.87, 24.65) * mm});
            skLineSegment(sketch, "E2582", {"start": v(9.87, 24.65) * mm, "end": v(9.93, 24.48) * mm});
            skLineSegment(sketch, "E2583", {"start": v(9.93, 24.48) * mm, "end": v(9.98, 24.34) * mm});
            skLineSegment(sketch, "E2584", {"start": v(9.98, 24.34) * mm, "end": v(10, 24.26) * mm});
            skLineSegment(sketch, "E2585", {"start": v(10, 24.26) * mm, "end": v(10, 24.12) * mm});
            skLineSegment(sketch, "E2586", {"start": v(10, 24.12) * mm, "end": v(10.82, 24.06) * mm});
            skLineSegment(sketch, "E2587", {"start": v(10.82, 24.06) * mm, "end": v(10.86, 24.12) * mm});
            skLineSegment(sketch, "E2588", {"start": v(10.86, 24.12) * mm, "end": v(10.86, 24.17) * mm});
            skLineSegment(sketch, "E2589", {"start": v(10.86, 24.17) * mm, "end": v(10.84, 24.25) * mm});
            skLineSegment(sketch, "E2590", {"start": v(10.84, 24.25) * mm, "end": v(10.79, 24.36) * mm});
            skLineSegment(sketch, "E2591", {"start": v(10.79, 24.36) * mm, "end": v(10.72, 24.48) * mm});
            skLineSegment(sketch, "E2592", {"start": v(10.72, 24.48) * mm, "end": v(9.86, 26.36) * mm});
            skLineSegment(sketch, "E2593", {"start": v(9.86, 26.36) * mm, "end": v(9.18, 27.94) * mm});
            skLineSegment(sketch, "E2594", {"start": v(9.18, 27.94) * mm, "end": v(9, 28.11) * mm});
            skLineSegment(sketch, "E2595", {"start": v(9, 28.11) * mm, "end": v(7.05, 24.24) * mm});
            skLineSegment(sketch, "E2596", {"start": v(7.05, 24.24) * mm, "end": v(7.05, 24.06) * mm});
            skLineSegment(sketch, "E2597", {"start": v(7.05, 24.06) * mm, "end": v(7.18, 24.05) * mm});
            skLineSegment(sketch, "E2598", {"start": v(7.18, 24.05) * mm, "end": v(7.35, 24.06) * mm});
            skLineSegment(sketch, "E2599", {"start": v(7.35, 24.06) * mm, "end": v(7.55, 24.08) * mm});
            skLineSegment(sketch, "E2600", {"start": v(7.55, 24.08) * mm, "end": v(7.78, 24.11) * mm});
            skLineSegment(sketch, "E2601", {"start": v(7.78, 24.11) * mm, "end": v(8.03, 24.7) * mm});
            skLineSegment(sketch, "E2602", {"start": v(14.48, 25.08) * mm, "end": v(14.48, 26.04) * mm});
            skLineSegment(sketch, "E2603", {"start": v(14.48, 26.04) * mm, "end": v(15.9, 24.15) * mm});
            skLineSegment(sketch, "E2604", {"start": v(15.9, 24.15) * mm, "end": v(16.29, 24.05) * mm});
            skLineSegment(sketch, "E2605", {"start": v(16.29, 24.05) * mm, "end": v(16.7, 24.15) * mm});
            skLineSegment(sketch, "E2606", {"start": v(16.7, 24.15) * mm, "end": v(15.4, 25.78) * mm});
            skLineSegment(sketch, "E2607", {"start": v(15.4, 25.78) * mm, "end": v(15.06, 26.27) * mm});
            skLineSegment(sketch, "E2608", {"start": v(15.06, 26.27) * mm, "end": v(16.52, 28) * mm});
            skLineSegment(sketch, "E2609", {"start": v(16.52, 28) * mm, "end": v(16.52, 28.05) * mm});
            skLineSegment(sketch, "E2610", {"start": v(16.52, 28.05) * mm, "end": v(16.5, 28.06) * mm});
            skLineSegment(sketch, "E2611", {"start": v(16.5, 28.06) * mm, "end": v(16.48, 28.07) * mm});
            skLineSegment(sketch, "E2612", {"start": v(16.48, 28.07) * mm, "end": v(16.4, 28.08) * mm});
            skLineSegment(sketch, "E2613", {"start": v(16.4, 28.08) * mm, "end": v(16.27, 28.1) * mm});
            skLineSegment(sketch, "E2614", {"start": v(16.27, 28.1) * mm, "end": v(16.11, 28.1) * mm});
            skLineSegment(sketch, "E2615", {"start": v(16.11, 28.1) * mm, "end": v(15.71, 28.1) * mm});
            skLineSegment(sketch, "E2616", {"start": v(15.71, 28.1) * mm, "end": v(15.4, 27.62) * mm});
            skLineSegment(sketch, "E2617", {"start": v(15.4, 27.62) * mm, "end": v(15.24, 27.4) * mm});
            skLineSegment(sketch, "E2618", {"start": v(15.24, 27.4) * mm, "end": v(15.07, 27.17) * mm});
            skLineSegment(sketch, "E2619", {"start": v(15.07, 27.17) * mm, "end": v(14.9, 26.96) * mm});
            skLineSegment(sketch, "E2620", {"start": v(14.9, 26.96) * mm, "end": v(14.75, 26.78) * mm});
            skLineSegment(sketch, "E2621", {"start": v(14.75, 26.78) * mm, "end": v(14.43, 26.42) * mm});
            skLineSegment(sketch, "E2622", {"start": v(14.43, 26.42) * mm, "end": v(14.47, 28.05) * mm});
            skLineSegment(sketch, "E2623", {"start": v(14.47, 28.05) * mm, "end": v(13.75, 28.1) * mm});
            skLineSegment(sketch, "E2624", {"start": v(13.75, 28.1) * mm, "end": v(13.75, 24.12) * mm});
            skLineSegment(sketch, "E2625", {"start": v(13.75, 24.12) * mm, "end": v(13.98, 24.09) * mm});
            skLineSegment(sketch, "E2626", {"start": v(13.98, 24.09) * mm, "end": v(14.18, 24.07) * mm});
            skLineSegment(sketch, "E2627", {"start": v(14.18, 24.07) * mm, "end": v(14.27, 24.08) * mm});
            skLineSegment(sketch, "E2628", {"start": v(14.27, 24.08) * mm, "end": v(14.34, 24.08) * mm});
            skLineSegment(sketch, "E2629", {"start": v(14.34, 24.08) * mm, "end": v(14.48, 24.11) * mm});
            skLineSegment(sketch, "E2630", {"start": v(14.48, 24.11) * mm, "end": v(14.48, 25.08) * mm});
            skLineSegment(sketch, "E2631", {"start": v(18.06, 24.3) * mm, "end": v(18.07, 24.4) * mm});
            skLineSegment(sketch, "E2632", {"start": v(18.07, 24.4) * mm, "end": v(18.12, 24.53) * mm});
            skLineSegment(sketch, "E2633", {"start": v(18.12, 24.53) * mm, "end": v(18.18, 24.7) * mm});
            skLineSegment(sketch, "E2634", {"start": v(18.18, 24.7) * mm, "end": v(18.26, 24.88) * mm});
            skLineSegment(sketch, "E2635", {"start": v(18.26, 24.88) * mm, "end": v(18.46, 25.3) * mm});
            skLineSegment(sketch, "E2636", {"start": v(18.46, 25.3) * mm, "end": v(19.82, 25.24) * mm});
            skLineSegment(sketch, "E2637", {"start": v(19.82, 25.24) * mm, "end": v(20.19, 24.12) * mm});
            skLineSegment(sketch, "E2638", {"start": v(20.19, 24.12) * mm, "end": v(20.87, 24.06) * mm});
            skLineSegment(sketch, "E2639", {"start": v(20.87, 24.06) * mm, "end": v(21.06, 24.17) * mm});
            skLineSegment(sketch, "E2640", {"start": v(21.06, 24.17) * mm, "end": v(20.7, 24.79) * mm});
            skLineSegment(sketch, "E2641", {"start": v(20.7, 24.79) * mm, "end": v(19.4, 27.87) * mm});
            skLineSegment(sketch, "E2642", {"start": v(19.4, 27.87) * mm, "end": v(19.16, 28.12) * mm});
            skLineSegment(sketch, "E2643", {"start": v(19.16, 28.12) * mm, "end": v(17.17, 24.15) * mm});
            skLineSegment(sketch, "E2644", {"start": v(17.17, 24.15) * mm, "end": v(17.27, 24.09) * mm});
            skLineSegment(sketch, "E2645", {"start": v(17.27, 24.09) * mm, "end": v(17.36, 24.04) * mm});
            skLineSegment(sketch, "E2646", {"start": v(17.36, 24.04) * mm, "end": v(17.4, 24.03) * mm});
            skLineSegment(sketch, "E2647", {"start": v(17.4, 24.03) * mm, "end": v(17.42, 24.03) * mm});
            skLineSegment(sketch, "E2648", {"start": v(17.42, 24.03) * mm, "end": v(17.76, 24.08) * mm});
            skLineSegment(sketch, "E2649", {"start": v(17.76, 24.08) * mm, "end": v(18.06, 24.12) * mm});
            skLineSegment(sketch, "E2650", {"start": v(18.06, 24.12) * mm, "end": v(18.06, 24.3) * mm});
            skLineSegment(sketch, "E2651", {"start": v(22.89, 24.1) * mm, "end": v(23.32, 24.1) * mm});
            skLineSegment(sketch, "E2652", {"start": v(23.32, 24.1) * mm, "end": v(23.46, 24.43) * mm});
            skLineSegment(sketch, "E2653", {"start": v(23.46, 24.43) * mm, "end": v(23.5, 24.56) * mm});
            skLineSegment(sketch, "E2654", {"start": v(23.5, 24.56) * mm, "end": v(23.54, 24.68) * mm});
            skLineSegment(sketch, "E2655", {"start": v(23.54, 24.68) * mm, "end": v(23.56, 24.76) * mm});
            skLineSegment(sketch, "E2656", {"start": v(23.56, 24.76) * mm, "end": v(23.55, 24.8) * mm});
            skLineSegment(sketch, "E2657", {"start": v(23.55, 24.8) * mm, "end": v(23.5, 24.8) * mm});
            skLineSegment(sketch, "E2658", {"start": v(23.5, 24.8) * mm, "end": v(23.38, 24.79) * mm});
            skLineSegment(sketch, "E2659", {"start": v(23.38, 24.79) * mm, "end": v(23.22, 24.75) * mm});
            skLineSegment(sketch, "E2660", {"start": v(23.22, 24.75) * mm, "end": v(23.03, 24.7) * mm});
            skLineSegment(sketch, "E2661", {"start": v(23.03, 24.7) * mm, "end": v(22.83, 24.65) * mm});
            skLineSegment(sketch, "E2662", {"start": v(22.83, 24.65) * mm, "end": v(22.63, 24.6) * mm});
            skLineSegment(sketch, "E2663", {"start": v(22.63, 24.6) * mm, "end": v(22.46, 24.57) * mm});
            skLineSegment(sketch, "E2664", {"start": v(22.46, 24.57) * mm, "end": v(22.34, 24.56) * mm});
            skLineSegment(sketch, "E2665", {"start": v(22.34, 24.56) * mm, "end": v(22.12, 24.56) * mm});
            skLineSegment(sketch, "E2666", {"start": v(22.12, 24.56) * mm, "end": v(22.18, 28.1) * mm});
            skLineSegment(sketch, "E2667", {"start": v(22.18, 28.1) * mm, "end": v(21.5, 28.1) * mm});
            skLineSegment(sketch, "E2668", {"start": v(21.5, 28.1) * mm, "end": v(21.46, 24.15) * mm});
            skLineSegment(sketch, "E2669", {"start": v(21.46, 24.15) * mm, "end": v(21.46, 24.14) * mm});
            skLineSegment(sketch, "E2670", {"start": v(21.46, 24.14) * mm, "end": v(21.48, 24.13) * mm});
            skLineSegment(sketch, "E2671", {"start": v(21.48, 24.13) * mm, "end": v(21.54, 24.11) * mm});
            skLineSegment(sketch, "E2672", {"start": v(21.54, 24.11) * mm, "end": v(21.73, 24.09) * mm});
            skLineSegment(sketch, "E2673", {"start": v(21.73, 24.09) * mm, "end": v(21.97, 24.07) * mm});
            skLineSegment(sketch, "E2674", {"start": v(21.97, 24.07) * mm, "end": v(22.18, 24.07) * mm});
            skLineSegment(sketch, "E2675", {"start": v(22.18, 24.07) * mm, "end": v(22.89, 24.1) * mm});
            skLineSegment(sketch, "E2676", {"start": v(26.8, 24.41) * mm, "end": v(27.02, 24.56) * mm});
            skLineSegment(sketch, "E2677", {"start": v(27.02, 24.56) * mm, "end": v(27.5, 25.37) * mm});
            skLineSegment(sketch, "E2678", {"start": v(27.5, 25.37) * mm, "end": v(27.6, 26.33) * mm});
            skLineSegment(sketch, "E2679", {"start": v(27.6, 26.33) * mm, "end": v(27.38, 27.1) * mm});
            skLineSegment(sketch, "E2680", {"start": v(27.38, 27.1) * mm, "end": v(26.75, 27.8) * mm});
            skLineSegment(sketch, "E2681", {"start": v(26.75, 27.8) * mm, "end": v(26.1, 28.11) * mm});
            skLineSegment(sketch, "E2682", {"start": v(26.1, 28.11) * mm, "end": v(25.03, 28.04) * mm});
            skLineSegment(sketch, "E2683", {"start": v(25.03, 28.04) * mm, "end": v(24.28, 27.5) * mm});
            skLineSegment(sketch, "E2684", {"start": v(24.28, 27.5) * mm, "end": v(23.86, 26.69) * mm});
            skLineSegment(sketch, "E2685", {"start": v(23.86, 26.69) * mm, "end": v(23.86, 25.5) * mm});
            skLineSegment(sketch, "E2686", {"start": v(23.86, 25.5) * mm, "end": v(24.3, 24.6) * mm});
            skLineSegment(sketch, "E2687", {"start": v(24.3, 24.6) * mm, "end": v(24.61, 24.4) * mm});
            skLineSegment(sketch, "E2688", {"start": v(24.61, 24.4) * mm, "end": v(24.74, 24.32) * mm});
            skLineSegment(sketch, "E2689", {"start": v(24.74, 24.32) * mm, "end": v(24.88, 24.25) * mm});
            skLineSegment(sketch, "E2690", {"start": v(24.88, 24.25) * mm, "end": v(25.03, 24.18) * mm});
            skLineSegment(sketch, "E2691", {"start": v(25.03, 24.18) * mm, "end": v(25.17, 24.12) * mm});
            skLineSegment(sketch, "E2692", {"start": v(25.17, 24.12) * mm, "end": v(25.32, 24.08) * mm});
            skLineSegment(sketch, "E2693", {"start": v(25.32, 24.08) * mm, "end": v(25.46, 24.05) * mm});
            skLineSegment(sketch, "E2694", {"start": v(25.46, 24.05) * mm, "end": v(25.6, 24.02) * mm});
            skLineSegment(sketch, "E2695", {"start": v(25.6, 24.02) * mm, "end": v(25.71, 24.02) * mm});
            skLineSegment(sketch, "E2696", {"start": v(25.71, 24.02) * mm, "end": v(25.82, 24.03) * mm});
            skLineSegment(sketch, "E2697", {"start": v(25.82, 24.03) * mm, "end": v(25.95, 24.06) * mm});
            skLineSegment(sketch, "E2698", {"start": v(25.95, 24.06) * mm, "end": v(26.09, 24.1) * mm});
            skLineSegment(sketch, "E2699", {"start": v(26.09, 24.1) * mm, "end": v(26.24, 24.15) * mm});
            skLineSegment(sketch, "E2700", {"start": v(26.24, 24.15) * mm, "end": v(26.54, 24.27) * mm});
            skLineSegment(sketch, "E2701", {"start": v(26.54, 24.27) * mm, "end": v(26.68, 24.34) * mm});
            skLineSegment(sketch, "E2702", {"start": v(26.68, 24.34) * mm, "end": v(26.8, 24.41) * mm});
            skLineSegment(sketch, "E2703", {"start": v(28.95, 24.1) * mm, "end": v(29.07, 24.1) * mm});
            skLineSegment(sketch, "E2704", {"start": v(29.07, 24.1) * mm, "end": v(29.07, 26.56) * mm});
            skLineSegment(sketch, "E2705", {"start": v(29.07, 26.56) * mm, "end": v(30.8, 24.15) * mm});
            skLineSegment(sketch, "E2706", {"start": v(30.8, 24.15) * mm, "end": v(31.51, 24.1) * mm});
            skLineSegment(sketch, "E2707", {"start": v(31.51, 24.1) * mm, "end": v(31.46, 28.1) * mm});
            skLineSegment(sketch, "E2708", {"start": v(31.46, 28.1) * mm, "end": v(30.75, 28.1) * mm});
            skLineSegment(sketch, "E2709", {"start": v(30.75, 28.1) * mm, "end": v(30.7, 25.39) * mm});
            skLineSegment(sketch, "E2710", {"start": v(30.7, 25.39) * mm, "end": v(28.79, 28.05) * mm});
            skLineSegment(sketch, "E2711", {"start": v(28.79, 28.05) * mm, "end": v(28.03, 28.1) * mm});
            skLineSegment(sketch, "E2712", {"start": v(28.03, 28.1) * mm, "end": v(28.03, 28.02) * mm});
            skLineSegment(sketch, "E2713", {"start": v(28.03, 28.02) * mm, "end": v(28.04, 27.98) * mm});
            skLineSegment(sketch, "E2714", {"start": v(28.04, 27.98) * mm, "end": v(28.08, 27.92) * mm});
            skLineSegment(sketch, "E2715", {"start": v(28.08, 27.92) * mm, "end": v(28.14, 27.84) * mm});
            skLineSegment(sketch, "E2716", {"start": v(28.14, 27.84) * mm, "end": v(28.21, 27.77) * mm});
            skLineSegment(sketch, "E2717", {"start": v(28.21, 27.77) * mm, "end": v(28.4, 27.6) * mm});
            skLineSegment(sketch, "E2718", {"start": v(28.4, 27.6) * mm, "end": v(28.34, 24.12) * mm});
            skLineSegment(sketch, "E2719", {"start": v(28.34, 24.12) * mm, "end": v(28.48, 24.08) * mm});
            skLineSegment(sketch, "E2720", {"start": v(28.48, 24.08) * mm, "end": v(28.6, 24.07) * mm});
            skLineSegment(sketch, "E2721", {"start": v(28.6, 24.07) * mm, "end": v(28.73, 24.07) * mm});
            skLineSegment(sketch, "E2722", {"start": v(28.73, 24.07) * mm, "end": v(28.95, 24.1) * mm});
            skLineSegment(sketch, "E2723", {"start": v(33.34, 24.1) * mm, "end": v(33.9, 24.1) * mm});
            skLineSegment(sketch, "E2724", {"start": v(33.9, 24.1) * mm, "end": v(34, 24.4) * mm});
            skLineSegment(sketch, "E2725", {"start": v(34, 24.4) * mm, "end": v(34.06, 24.6) * mm});
            skLineSegment(sketch, "E2726", {"start": v(34.06, 24.6) * mm, "end": v(34.07, 24.68) * mm});
            skLineSegment(sketch, "E2727", {"start": v(34.07, 24.68) * mm, "end": v(34.06, 24.72) * mm});
            skLineSegment(sketch, "E2728", {"start": v(34.06, 24.72) * mm, "end": v(34.02, 24.72) * mm});
            skLineSegment(sketch, "E2729", {"start": v(34.02, 24.72) * mm, "end": v(33.93, 24.71) * mm});
            skLineSegment(sketch, "E2730", {"start": v(33.93, 24.71) * mm, "end": v(33.81, 24.7) * mm});
            skLineSegment(sketch, "E2731", {"start": v(33.81, 24.7) * mm, "end": v(33.68, 24.66) * mm});
            skLineSegment(sketch, "E2732", {"start": v(33.68, 24.66) * mm, "end": v(33.5, 24.62) * mm});
            skLineSegment(sketch, "E2733", {"start": v(33.5, 24.62) * mm, "end": v(33.32, 24.59) * mm});
            skLineSegment(sketch, "E2734", {"start": v(33.32, 24.59) * mm, "end": v(33.12, 24.57) * mm});
            skLineSegment(sketch, "E2735", {"start": v(33.12, 24.57) * mm, "end": v(32.94, 24.56) * mm});
            skLineSegment(sketch, "E2736", {"start": v(32.94, 24.56) * mm, "end": v(32.56, 24.56) * mm});
            skLineSegment(sketch, "E2737", {"start": v(32.56, 24.56) * mm, "end": v(32.56, 25.94) * mm});
            skLineSegment(sketch, "E2738", {"start": v(32.56, 25.94) * mm, "end": v(32.88, 25.88) * mm});
            skLineSegment(sketch, "E2739", {"start": v(32.88, 25.88) * mm, "end": v(33.14, 25.82) * mm});
            skLineSegment(sketch, "E2740", {"start": v(33.14, 25.82) * mm, "end": v(33.32, 25.77) * mm});
            skLineSegment(sketch, "E2741", {"start": v(33.32, 25.77) * mm, "end": v(33.44, 25.73) * mm});
            skLineSegment(sketch, "E2742", {"start": v(33.44, 25.73) * mm, "end": v(33.74, 26.2) * mm});
            skLineSegment(sketch, "E2743", {"start": v(33.74, 26.2) * mm, "end": v(33.63, 26.37) * mm});
            skLineSegment(sketch, "E2744", {"start": v(33.63, 26.37) * mm, "end": v(32.56, 26.37) * mm});
            skLineSegment(sketch, "E2745", {"start": v(32.56, 26.37) * mm, "end": v(32.56, 27.66) * mm});
            skLineSegment(sketch, "E2746", {"start": v(32.56, 27.66) * mm, "end": v(32.85, 27.6) * mm});
            skLineSegment(sketch, "E2747", {"start": v(32.85, 27.6) * mm, "end": v(33.39, 27.5) * mm});
            skLineSegment(sketch, "E2748", {"start": v(33.39, 27.5) * mm, "end": v(33.63, 27.44) * mm});
            skLineSegment(sketch, "E2749", {"start": v(33.63, 27.44) * mm, "end": v(33.77, 27.72) * mm});
            skLineSegment(sketch, "E2750", {"start": v(33.77, 27.72) * mm, "end": v(33.87, 27.93) * mm});
            skLineSegment(sketch, "E2751", {"start": v(33.87, 27.93) * mm, "end": v(33.92, 28.04) * mm});
            skLineSegment(sketch, "E2752", {"start": v(33.92, 28.04) * mm, "end": v(33.92, 28.1) * mm});
            skLineSegment(sketch, "E2753", {"start": v(33.92, 28.1) * mm, "end": v(31.88, 28.1) * mm});
            skLineSegment(sketch, "E2754", {"start": v(31.88, 28.1) * mm, "end": v(31.88, 24.12) * mm});
            skLineSegment(sketch, "E2755", {"start": v(31.88, 24.12) * mm, "end": v(32.1, 24.1) * mm});
            skLineSegment(sketch, "E2756", {"start": v(32.1, 24.1) * mm, "end": v(32.33, 24.07) * mm});
            skLineSegment(sketch, "E2757", {"start": v(32.33, 24.07) * mm, "end": v(32.56, 24.07) * mm});
            skLineSegment(sketch, "E2758", {"start": v(32.56, 24.07) * mm, "end": v(33.34, 24.1) * mm});
            skLineSegment(sketch, "E2759", {"start": v(13.4, 24.8) * mm, "end": v(13.35, 24.8) * mm});
            skLineSegment(sketch, "E2760", {"start": v(13.35, 24.8) * mm, "end": v(13.23, 24.8) * mm});
            skLineSegment(sketch, "E2761", {"start": v(13.23, 24.8) * mm, "end": v(13.07, 24.75) * mm});
            skLineSegment(sketch, "E2762", {"start": v(13.07, 24.75) * mm, "end": v(12.88, 24.7) * mm});
            skLineSegment(sketch, "E2763", {"start": v(12.88, 24.7) * mm, "end": v(12.68, 24.65) * mm});
            skLineSegment(sketch, "E2764", {"start": v(12.68, 24.65) * mm, "end": v(12.48, 24.6) * mm});
            skLineSegment(sketch, "E2765", {"start": v(12.48, 24.6) * mm, "end": v(12.31, 24.57) * mm});
            skLineSegment(sketch, "E2766", {"start": v(12.31, 24.57) * mm, "end": v(12.2, 24.56) * mm});
            skLineSegment(sketch, "E2767", {"start": v(12.2, 24.56) * mm, "end": v(11.98, 24.56) * mm});
            skLineSegment(sketch, "E2768", {"start": v(11.98, 24.56) * mm, "end": v(12, 28.05) * mm});
            skLineSegment(sketch, "E2769", {"start": v(12, 28.05) * mm, "end": v(11.35, 28.05) * mm});
            skLineSegment(sketch, "E2770", {"start": v(11.35, 28.05) * mm, "end": v(11.3, 24.1) * mm});
            skLineSegment(sketch, "E2771", {"start": v(11.3, 24.1) * mm, "end": v(13.16, 24.1) * mm});
            skLineSegment(sketch, "E2772", {"start": v(13.16, 24.1) * mm, "end": v(13.3, 24.44) * mm});
            skLineSegment(sketch, "E2773", {"start": v(13.3, 24.44) * mm, "end": v(13.35, 24.57) * mm});
            skLineSegment(sketch, "E2774", {"start": v(13.35, 24.57) * mm, "end": v(13.39, 24.68) * mm});
            skLineSegment(sketch, "E2775", {"start": v(13.39, 24.68) * mm, "end": v(13.4, 24.77) * mm});
            skLineSegment(sketch, "E2776", {"start": v(13.4, 24.77) * mm, "end": v(13.4, 24.8) * mm});
            skLineSegment(sketch, "E2777", {"start": v(-28.6, 24.56) * mm, "end": v(-28.28, 24.56) * mm});
            skLineSegment(sketch, "E2778", {"start": v(-28.28, 24.56) * mm, "end": v(-27.82, 24.92) * mm});
            skLineSegment(sketch, "E2779", {"start": v(-27.82, 24.92) * mm, "end": v(-27.53, 25.54) * mm});
            skLineSegment(sketch, "E2780", {"start": v(-27.53, 25.54) * mm, "end": v(-27.53, 26.5) * mm});
            skLineSegment(sketch, "E2781", {"start": v(-27.53, 26.5) * mm, "end": v(-27.98, 27.26) * mm});
            skLineSegment(sketch, "E2782", {"start": v(-27.98, 27.26) * mm, "end": v(-28.76, 27.64) * mm});
            skLineSegment(sketch, "E2783", {"start": v(-28.76, 27.64) * mm, "end": v(-29.18, 27.64) * mm});
            skLineSegment(sketch, "E2784", {"start": v(-29.18, 27.64) * mm, "end": v(-29.68, 27.34) * mm});
            skLineSegment(sketch, "E2785", {"start": v(-29.68, 27.34) * mm, "end": v(-29.98, 26.84) * mm});
            skLineSegment(sketch, "E2786", {"start": v(-29.98, 26.84) * mm, "end": v(-30.09, 26.03) * mm});
            skLineSegment(sketch, "E2787", {"start": v(-30.09, 26.03) * mm, "end": v(-29.86, 25.33) * mm});
            skLineSegment(sketch, "E2788", {"start": v(-29.86, 25.33) * mm, "end": v(-29.67, 25.11) * mm});
            skLineSegment(sketch, "E2789", {"start": v(-29.67, 25.11) * mm, "end": v(-29.57, 25.02) * mm});
            skLineSegment(sketch, "E2790", {"start": v(-29.57, 25.02) * mm, "end": v(-29.45, 24.91) * mm});
            skLineSegment(sketch, "E2791", {"start": v(-29.45, 24.91) * mm, "end": v(-29.32, 24.81) * mm});
            skLineSegment(sketch, "E2792", {"start": v(-29.32, 24.81) * mm, "end": v(-29.2, 24.73) * mm});
            skLineSegment(sketch, "E2793", {"start": v(-29.2, 24.73) * mm, "end": v(-28.93, 24.56) * mm});
            skLineSegment(sketch, "E2794", {"start": v(-28.93, 24.56) * mm, "end": v(-28.6, 24.56) * mm});
            skLineSegment(sketch, "E2795", {"start": v(25.86, 24.56) * mm, "end": v(26.2, 24.56) * mm});
            skLineSegment(sketch, "E2796", {"start": v(26.2, 24.56) * mm, "end": v(26.74, 25.02) * mm});
            skLineSegment(sketch, "E2797", {"start": v(26.74, 25.02) * mm, "end": v(26.97, 25.69) * mm});
            skLineSegment(sketch, "E2798", {"start": v(26.97, 25.69) * mm, "end": v(26.95, 26.46) * mm});
            skLineSegment(sketch, "E2799", {"start": v(26.95, 26.46) * mm, "end": v(26.48, 27.28) * mm});
            skLineSegment(sketch, "E2800", {"start": v(26.48, 27.28) * mm, "end": v(25.77, 27.64) * mm});
            skLineSegment(sketch, "E2801", {"start": v(25.77, 27.64) * mm, "end": v(25.2, 27.64) * mm});
            skLineSegment(sketch, "E2802", {"start": v(25.2, 27.64) * mm, "end": v(24.6, 27.04) * mm});
            skLineSegment(sketch, "E2803", {"start": v(24.6, 27.04) * mm, "end": v(24.38, 26.24) * mm});
            skLineSegment(sketch, "E2804", {"start": v(24.38, 26.24) * mm, "end": v(24.48, 25.83) * mm});
            skLineSegment(sketch, "E2805", {"start": v(24.48, 25.83) * mm, "end": v(24.53, 25.65) * mm});
            skLineSegment(sketch, "E2806", {"start": v(24.53, 25.65) * mm, "end": v(24.6, 25.5) * mm});
            skLineSegment(sketch, "E2807", {"start": v(24.6, 25.5) * mm, "end": v(24.67, 25.35) * mm});
            skLineSegment(sketch, "E2808", {"start": v(24.67, 25.35) * mm, "end": v(24.75, 25.21) * mm});
            skLineSegment(sketch, "E2809", {"start": v(24.75, 25.21) * mm, "end": v(24.84, 25.09) * mm});
            skLineSegment(sketch, "E2810", {"start": v(24.84, 25.09) * mm, "end": v(24.95, 24.97) * mm});
            skLineSegment(sketch, "E2811", {"start": v(24.95, 24.97) * mm, "end": v(25.07, 24.87) * mm});
            skLineSegment(sketch, "E2812", {"start": v(25.07, 24.87) * mm, "end": v(25.22, 24.76) * mm});
            skLineSegment(sketch, "E2813", {"start": v(25.22, 24.76) * mm, "end": v(25.51, 24.56) * mm});
            skLineSegment(sketch, "E2814", {"start": v(25.51, 24.56) * mm, "end": v(25.86, 24.56) * mm});
            skLineSegment(sketch, "E2815", {"start": v(8.95, 25.83) * mm, "end": v(9.37, 25.83) * mm});
            skLineSegment(sketch, "E2816", {"start": v(9.37, 25.83) * mm, "end": v(9.3, 26.03) * mm});
            skLineSegment(sketch, "E2817", {"start": v(9.3, 26.03) * mm, "end": v(9.23, 26.25) * mm});
            skLineSegment(sketch, "E2818", {"start": v(9.23, 26.25) * mm, "end": v(9.13, 26.5) * mm});
            skLineSegment(sketch, "E2819", {"start": v(9.13, 26.5) * mm, "end": v(9.01, 26.77) * mm});
            skLineSegment(sketch, "E2820", {"start": v(9.01, 26.77) * mm, "end": v(8.54, 25.83) * mm});
            skLineSegment(sketch, "E2821", {"start": v(8.54, 25.83) * mm, "end": v(8.95, 25.83) * mm});
            skLineSegment(sketch, "E2822", {"start": v(19.14, 25.83) * mm, "end": v(19.5, 25.83) * mm});
            skLineSegment(sketch, "E2823", {"start": v(19.5, 25.83) * mm, "end": v(19.5, 25.94) * mm});
            skLineSegment(sketch, "E2824", {"start": v(19.5, 25.94) * mm, "end": v(19.48, 26.01) * mm});
            skLineSegment(sketch, "E2825", {"start": v(19.48, 26.01) * mm, "end": v(19.45, 26.13) * mm});
            skLineSegment(sketch, "E2826", {"start": v(19.45, 26.13) * mm, "end": v(19.33, 26.42) * mm});
            skLineSegment(sketch, "E2827", {"start": v(19.33, 26.42) * mm, "end": v(19.17, 26.78) * mm});
            skLineSegment(sketch, "E2828", {"start": v(19.17, 26.78) * mm, "end": v(19.03, 26.5) * mm});
            skLineSegment(sketch, "E2829", {"start": v(19.03, 26.5) * mm, "end": v(18.92, 26.26) * mm});
            skLineSegment(sketch, "E2830", {"start": v(18.92, 26.26) * mm, "end": v(18.83, 26.03) * mm});
            skLineSegment(sketch, "E2831", {"start": v(18.83, 26.03) * mm, "end": v(18.77, 25.83) * mm});
            skLineSegment(sketch, "E2832", {"start": v(18.77, 25.83) * mm, "end": v(19.14, 25.83) * mm});
            skLineSegment(sketch, "E2833", {"start": v(-1.83, 26) * mm, "end": v(-1.78, 26.02) * mm});
            skLineSegment(sketch, "E2834", {"start": v(-1.78, 26.02) * mm, "end": v(-1.71, 26.04) * mm});
            skLineSegment(sketch, "E2835", {"start": v(-1.71, 26.04) * mm, "end": v(-1.54, 26.14) * mm});
            skLineSegment(sketch, "E2836", {"start": v(-1.54, 26.14) * mm, "end": v(-1.35, 26.26) * mm});
            skLineSegment(sketch, "E2837", {"start": v(-1.35, 26.26) * mm, "end": v(-1.18, 26.4) * mm});
            skLineSegment(sketch, "E2838", {"start": v(-1.18, 26.4) * mm, "end": v(-0.97, 26.58) * mm});
            skLineSegment(sketch, "E2839", {"start": v(-0.97, 26.58) * mm, "end": v(-0.97, 27.09) * mm});
            skLineSegment(sketch, "E2840", {"start": v(-0.97, 27.09) * mm, "end": v(-1.38, 27.54) * mm});
            skLineSegment(sketch, "E2841", {"start": v(-1.38, 27.54) * mm, "end": v(-1.88, 27.66) * mm});
            skLineSegment(sketch, "E2842", {"start": v(-1.88, 27.66) * mm, "end": v(-1.88, 26) * mm});
            skLineSegment(sketch, "E2843", {"start": v(-1.88, 26) * mm, "end": v(-1.83, 26) * mm});
            skLineSegment(sketch, "E2844", {"start": v(-22.45, 27.47) * mm, "end": v(-22.45, 27.83) * mm});
            skLineSegment(sketch, "E2845", {"start": v(-22.45, 27.83) * mm, "end": v(-22.95, 27.78) * mm});
            skLineSegment(sketch, "E2846", {"start": v(-22.95, 27.78) * mm, "end": v(-23.01, 27.45) * mm});
            skLineSegment(sketch, "E2847", {"start": v(-23.01, 27.45) * mm, "end": v(-22.7, 27.1) * mm});
            skLineSegment(sketch, "E2848", {"start": v(-22.7, 27.1) * mm, "end": v(-22.8, 26.99) * mm});
            skLineSegment(sketch, "E2849", {"start": v(-22.8, 26.99) * mm, "end": v(-22.84, 26.94) * mm});
            skLineSegment(sketch, "E2850", {"start": v(-22.84, 26.94) * mm, "end": v(-22.87, 26.88) * mm});
            skLineSegment(sketch, "E2851", {"start": v(-22.87, 26.88) * mm, "end": v(-22.9, 26.82) * mm});
            skLineSegment(sketch, "E2852", {"start": v(-22.9, 26.82) * mm, "end": v(-22.9, 26.76) * mm});
            skLineSegment(sketch, "E2853", {"start": v(-22.9, 26.76) * mm, "end": v(-22.9, 26.64) * mm});
            skLineSegment(sketch, "E2854", {"start": v(-22.9, 26.64) * mm, "end": v(-22.63, 26.64) * mm});
            skLineSegment(sketch, "E2855", {"start": v(-22.63, 26.64) * mm, "end": v(-22.54, 26.88) * mm});
            skLineSegment(sketch, "E2856", {"start": v(-22.54, 26.88) * mm, "end": v(-22.5, 27) * mm});
            skLineSegment(sketch, "E2857", {"start": v(-22.5, 27) * mm, "end": v(-22.48, 27.15) * mm});
            skLineSegment(sketch, "E2858", {"start": v(-22.48, 27.15) * mm, "end": v(-22.46, 27.31) * mm});
            skLineSegment(sketch, "E2859", {"start": v(-22.46, 27.31) * mm, "end": v(-22.45, 27.47) * mm});
            skLineSegment(sketch, "E2860", {"start": v(-2.08, 31.65) * mm, "end": v(-1.97, 31.77) * mm});
            skLineSegment(sketch, "E2861", {"start": v(-1.97, 31.77) * mm, "end": v(-1.88, 31.87) * mm});
            skLineSegment(sketch, "E2862", {"start": v(-1.88, 31.87) * mm, "end": v(-1.81, 31.96) * mm});
            skLineSegment(sketch, "E2863", {"start": v(-1.81, 31.96) * mm, "end": v(-1.8, 32) * mm});
            skLineSegment(sketch, "E2864", {"start": v(-1.8, 32) * mm, "end": v(-1.8, 32.08) * mm});
            skLineSegment(sketch, "E2865", {"start": v(-1.8, 32.08) * mm, "end": v(-3.36, 33.8) * mm});
            skLineSegment(sketch, "E2866", {"start": v(-3.36, 33.8) * mm, "end": v(-3.48, 33.76) * mm});
            skLineSegment(sketch, "E2867", {"start": v(-3.48, 33.76) * mm, "end": v(-4.87, 32.22) * mm});
            skLineSegment(sketch, "E2868", {"start": v(-4.87, 32.22) * mm, "end": v(-4.87, 32.12) * mm});
            skLineSegment(sketch, "E2869", {"start": v(-4.87, 32.12) * mm, "end": v(-4.86, 32.09) * mm});
            skLineSegment(sketch, "E2870", {"start": v(-4.86, 32.09) * mm, "end": v(-4.84, 32.05) * mm});
            skLineSegment(sketch, "E2871", {"start": v(-4.84, 32.05) * mm, "end": v(-4.75, 31.94) * mm});
            skLineSegment(sketch, "E2872", {"start": v(-4.75, 31.94) * mm, "end": v(-4.63, 31.8) * mm});
            skLineSegment(sketch, "E2873", {"start": v(-4.63, 31.8) * mm, "end": v(-4.47, 31.65) * mm});
            skLineSegment(sketch, "E2874", {"start": v(-4.47, 31.65) * mm, "end": v(-4.07, 31.28) * mm});
            skLineSegment(sketch, "E2875", {"start": v(-4.07, 31.28) * mm, "end": v(-3.73, 31.18) * mm});
            skLineSegment(sketch, "E2876", {"start": v(-3.73, 31.18) * mm, "end": v(-3.43, 31.11) * mm});
            skLineSegment(sketch, "E2877", {"start": v(-3.43, 31.11) * mm, "end": v(-3.3, 31.1) * mm});
            skLineSegment(sketch, "E2878", {"start": v(-3.3, 31.1) * mm, "end": v(-3.2, 31.09) * mm});
            skLineSegment(sketch, "E2879", {"start": v(-3.2, 31.09) * mm, "end": v(-3.07, 31.1) * mm});
            skLineSegment(sketch, "E2880", {"start": v(-3.07, 31.1) * mm, "end": v(-2.94, 31.14) * mm});
            skLineSegment(sketch, "E2881", {"start": v(-2.94, 31.14) * mm, "end": v(-2.8, 31.19) * mm});
            skLineSegment(sketch, "E2882", {"start": v(-2.8, 31.19) * mm, "end": v(-2.65, 31.26) * mm});
            skLineSegment(sketch, "E2883", {"start": v(-2.65, 31.26) * mm, "end": v(-2.5, 31.34) * mm});
            skLineSegment(sketch, "E2884", {"start": v(-2.5, 31.34) * mm, "end": v(-2.35, 31.44) * mm});
            skLineSegment(sketch, "E2885", {"start": v(-2.35, 31.44) * mm, "end": v(-2.21, 31.54) * mm});
            skLineSegment(sketch, "E2886", {"start": v(-2.21, 31.54) * mm, "end": v(-2.08, 31.65) * mm});
            skLineSegment(sketch, "E2887", {"start": v(3.1, 32.7) * mm, "end": v(2.84, 32.9) * mm});
            skLineSegment(sketch, "E2888", {"start": v(2.84, 32.9) * mm, "end": v(2.41, 32.9) * mm});
            skLineSegment(sketch, "E2889", {"start": v(2.41, 32.9) * mm, "end": v(2.2, 32.68) * mm});
            skLineSegment(sketch, "E2890", {"start": v(2.2, 32.68) * mm, "end": v(2.2, 31.94) * mm});
            skLineSegment(sketch, "E2891", {"start": v(2.2, 31.94) * mm, "end": v(2.5, 31.66) * mm});
            skLineSegment(sketch, "E2892", {"start": v(2.5, 31.66) * mm, "end": v(2.72, 31.46) * mm});
            skLineSegment(sketch, "E2893", {"start": v(2.72, 31.46) * mm, "end": v(2.94, 31.3) * mm});
            skLineSegment(sketch, "E2894", {"start": v(2.94, 31.3) * mm, "end": v(3.04, 31.25) * mm});
            skLineSegment(sketch, "E2895", {"start": v(3.04, 31.25) * mm, "end": v(3.13, 31.2) * mm});
            skLineSegment(sketch, "E2896", {"start": v(3.13, 31.2) * mm, "end": v(3.2, 31.18) * mm});
            skLineSegment(sketch, "E2897", {"start": v(3.2, 31.18) * mm, "end": v(3.28, 31.17) * mm});
            skLineSegment(sketch, "E2898", {"start": v(3.28, 31.17) * mm, "end": v(3.38, 31.17) * mm});
            skLineSegment(sketch, "E2899", {"start": v(3.38, 31.17) * mm, "end": v(3.38, 32.5) * mm});
            skLineSegment(sketch, "E2900", {"start": v(3.38, 32.5) * mm, "end": v(3.1, 32.7) * mm});
            skLineSegment(sketch, "E2901", {"start": v(4.85, 31.61) * mm, "end": v(5.1, 31.84) * mm});
            skLineSegment(sketch, "E2902", {"start": v(5.1, 31.84) * mm, "end": v(5.1, 32.68) * mm});
            skLineSegment(sketch, "E2903", {"start": v(5.1, 32.68) * mm, "end": v(4.88, 32.9) * mm});
            skLineSegment(sketch, "E2904", {"start": v(4.88, 32.9) * mm, "end": v(4.36, 32.9) * mm});
            skLineSegment(sketch, "E2905", {"start": v(4.36, 32.9) * mm, "end": v(3.83, 32.37) * mm});
            skLineSegment(sketch, "E2906", {"start": v(3.83, 32.37) * mm, "end": v(3.83, 31.17) * mm});
            skLineSegment(sketch, "E2907", {"start": v(3.83, 31.17) * mm, "end": v(4.03, 31.18) * mm});
            skLineSegment(sketch, "E2908", {"start": v(4.03, 31.18) * mm, "end": v(4.13, 31.18) * mm});
            skLineSegment(sketch, "E2909", {"start": v(4.13, 31.18) * mm, "end": v(4.22, 31.2) * mm});
            skLineSegment(sketch, "E2910", {"start": v(4.22, 31.2) * mm, "end": v(4.31, 31.24) * mm});
            skLineSegment(sketch, "E2911", {"start": v(4.31, 31.24) * mm, "end": v(4.41, 31.28) * mm});
            skLineSegment(sketch, "E2912", {"start": v(4.41, 31.28) * mm, "end": v(4.51, 31.34) * mm});
            skLineSegment(sketch, "E2913", {"start": v(4.51, 31.34) * mm, "end": v(4.62, 31.42) * mm});
            skLineSegment(sketch, "E2914", {"start": v(4.62, 31.42) * mm, "end": v(4.85, 31.61) * mm});
            skLineSegment(sketch, "E2915", {"start": v(5.86, 33.35) * mm, "end": v(6, 33.85) * mm});
            skLineSegment(sketch, "E2916", {"start": v(6, 33.85) * mm, "end": v(6.02, 34.4) * mm});
            skLineSegment(sketch, "E2917", {"start": v(6.02, 34.4) * mm, "end": v(6.02, 34.84) * mm});
            skLineSegment(sketch, "E2918", {"start": v(6.02, 34.84) * mm, "end": v(6.02, 35.14) * mm});
            skLineSegment(sketch, "E2919", {"start": v(6.02, 35.14) * mm, "end": v(6, 35.34) * mm});
            skLineSegment(sketch, "E2920", {"start": v(6, 35.34) * mm, "end": v(5.85, 35.34) * mm});
            skLineSegment(sketch, "E2921", {"start": v(5.85, 35.34) * mm, "end": v(5.76, 35.33) * mm});
            skLineSegment(sketch, "E2922", {"start": v(5.76, 35.33) * mm, "end": v(5.65, 35.3) * mm});
            skLineSegment(sketch, "E2923", {"start": v(5.65, 35.3) * mm, "end": v(5.52, 35.23) * mm});
            skLineSegment(sketch, "E2924", {"start": v(5.52, 35.23) * mm, "end": v(5.4, 35.16) * mm});
            skLineSegment(sketch, "E2925", {"start": v(5.4, 35.16) * mm, "end": v(5.1, 34.98) * mm});
            skLineSegment(sketch, "E2926", {"start": v(5.1, 34.98) * mm, "end": v(5, 34.75) * mm});
            skLineSegment(sketch, "E2927", {"start": v(5, 34.75) * mm, "end": v(4.95, 34.66) * mm});
            skLineSegment(sketch, "E2928", {"start": v(4.95, 34.66) * mm, "end": v(4.9, 34.6) * mm});
            skLineSegment(sketch, "E2929", {"start": v(4.9, 34.6) * mm, "end": v(4.86, 34.56) * mm});
            skLineSegment(sketch, "E2930", {"start": v(4.86, 34.56) * mm, "end": v(4.83, 34.54) * mm});
            skLineSegment(sketch, "E2931", {"start": v(4.83, 34.54) * mm, "end": v(4.8, 34.54) * mm});
            skLineSegment(sketch, "E2932", {"start": v(4.8, 34.54) * mm, "end": v(4.76, 34.58) * mm});
            skLineSegment(sketch, "E2933", {"start": v(4.76, 34.58) * mm, "end": v(4.73, 34.63) * mm});
            skLineSegment(sketch, "E2934", {"start": v(4.73, 34.63) * mm, "end": v(4.7, 34.7) * mm});
            skLineSegment(sketch, "E2935", {"start": v(4.7, 34.7) * mm, "end": v(4.66, 34.9) * mm});
            skLineSegment(sketch, "E2936", {"start": v(4.66, 34.9) * mm, "end": v(4.05, 34.9) * mm});
            skLineSegment(sketch, "E2937", {"start": v(4.05, 34.9) * mm, "end": v(3.83, 34.67) * mm});
            skLineSegment(sketch, "E2938", {"start": v(3.83, 34.67) * mm, "end": v(3.83, 32.99) * mm});
            skLineSegment(sketch, "E2939", {"start": v(3.83, 32.99) * mm, "end": v(3.93, 32.99) * mm});
            skLineSegment(sketch, "E2940", {"start": v(3.93, 32.99) * mm, "end": v(3.99, 33) * mm});
            skLineSegment(sketch, "E2941", {"start": v(3.99, 33) * mm, "end": v(4.06, 33.03) * mm});
            skLineSegment(sketch, "E2942", {"start": v(4.06, 33.03) * mm, "end": v(4.13, 33.08) * mm});
            skLineSegment(sketch, "E2943", {"start": v(4.13, 33.08) * mm, "end": v(4.2, 33.13) * mm});
            skLineSegment(sketch, "E2944", {"start": v(4.2, 33.13) * mm, "end": v(4.36, 33.28) * mm});
            skLineSegment(sketch, "E2945", {"start": v(4.36, 33.28) * mm, "end": v(5.01, 33.28) * mm});
            skLineSegment(sketch, "E2946", {"start": v(5.01, 33.28) * mm, "end": v(5.15, 33.16) * mm});
            skLineSegment(sketch, "E2947", {"start": v(5.15, 33.16) * mm, "end": v(5.21, 33.1) * mm});
            skLineSegment(sketch, "E2948", {"start": v(5.21, 33.1) * mm, "end": v(5.28, 33) * mm});
            skLineSegment(sketch, "E2949", {"start": v(5.28, 33) * mm, "end": v(5.35, 32.88) * mm});
            skLineSegment(sketch, "E2950", {"start": v(5.35, 32.88) * mm, "end": v(5.4, 32.77) * mm});
            skLineSegment(sketch, "E2951", {"start": v(5.4, 32.77) * mm, "end": v(5.52, 32.49) * mm});
            skLineSegment(sketch, "E2952", {"start": v(5.52, 32.49) * mm, "end": v(5.62, 32.67) * mm});
            skLineSegment(sketch, "E2953", {"start": v(5.62, 32.67) * mm, "end": v(5.67, 32.78) * mm});
            skLineSegment(sketch, "E2954", {"start": v(5.67, 32.78) * mm, "end": v(5.73, 32.94) * mm});
            skLineSegment(sketch, "E2955", {"start": v(5.73, 32.94) * mm, "end": v(5.86, 33.35) * mm});
            skLineSegment(sketch, "E2956", {"start": v(2.3, 33.25) * mm, "end": v(2.55, 33.34) * mm});
            skLineSegment(sketch, "E2957", {"start": v(2.55, 33.34) * mm, "end": v(2.76, 33.29) * mm});
            skLineSegment(sketch, "E2958", {"start": v(2.76, 33.29) * mm, "end": v(2.86, 33.25) * mm});
            skLineSegment(sketch, "E2959", {"start": v(2.86, 33.25) * mm, "end": v(2.97, 33.2) * mm});
            skLineSegment(sketch, "E2960", {"start": v(2.97, 33.2) * mm, "end": v(3.08, 33.13) * mm});
            skLineSegment(sketch, "E2961", {"start": v(3.08, 33.13) * mm, "end": v(3.17, 33.05) * mm});
            skLineSegment(sketch, "E2962", {"start": v(3.17, 33.05) * mm, "end": v(3.38, 32.87) * mm});
            skLineSegment(sketch, "E2963", {"start": v(3.38, 32.87) * mm, "end": v(3.38, 34.78) * mm});
            skLineSegment(sketch, "E2964", {"start": v(3.38, 34.78) * mm, "end": v(3.23, 34.84) * mm});
            skLineSegment(sketch, "E2965", {"start": v(3.23, 34.84) * mm, "end": v(3.16, 34.86) * mm});
            skLineSegment(sketch, "E2966", {"start": v(3.16, 34.86) * mm, "end": v(3.05, 34.87) * mm});
            skLineSegment(sketch, "E2967", {"start": v(3.05, 34.87) * mm, "end": v(2.94, 34.89) * mm});
            skLineSegment(sketch, "E2968", {"start": v(2.94, 34.89) * mm, "end": v(2.82, 34.9) * mm});
            skLineSegment(sketch, "E2969", {"start": v(2.82, 34.9) * mm, "end": v(2.56, 34.9) * mm});
            skLineSegment(sketch, "E2970", {"start": v(2.56, 34.9) * mm, "end": v(2.56, 34.76) * mm});
            skLineSegment(sketch, "E2971", {"start": v(2.56, 34.76) * mm, "end": v(2.55, 34.7) * mm});
            skLineSegment(sketch, "E2972", {"start": v(2.55, 34.7) * mm, "end": v(2.54, 34.65) * mm});
            skLineSegment(sketch, "E2973", {"start": v(2.54, 34.65) * mm, "end": v(2.5, 34.6) * mm});
            skLineSegment(sketch, "E2974", {"start": v(2.5, 34.6) * mm, "end": v(2.48, 34.58) * mm});
            skLineSegment(sketch, "E2975", {"start": v(2.48, 34.58) * mm, "end": v(2.4, 34.52) * mm});
            skLineSegment(sketch, "E2976", {"start": v(2.4, 34.52) * mm, "end": v(2.08, 35.05) * mm});
            skLineSegment(sketch, "E2977", {"start": v(2.08, 35.05) * mm, "end": v(1.83, 35.2) * mm});
            skLineSegment(sketch, "E2978", {"start": v(1.83, 35.2) * mm, "end": v(1.62, 35.3) * mm});
            skLineSegment(sketch, "E2979", {"start": v(1.62, 35.3) * mm, "end": v(1.54, 35.33) * mm});
            skLineSegment(sketch, "E2980", {"start": v(1.54, 35.33) * mm, "end": v(1.48, 35.34) * mm});
            skLineSegment(sketch, "E2981", {"start": v(1.48, 35.34) * mm, "end": v(1.38, 35.34) * mm});
            skLineSegment(sketch, "E2982", {"start": v(1.38, 35.34) * mm, "end": v(1.38, 33.94) * mm});
            skLineSegment(sketch, "E2983", {"start": v(1.38, 33.94) * mm, "end": v(1.5, 33.48) * mm});
            skLineSegment(sketch, "E2984", {"start": v(1.5, 33.48) * mm, "end": v(1.62, 33.1) * mm});
            skLineSegment(sketch, "E2985", {"start": v(1.62, 33.1) * mm, "end": v(1.68, 32.95) * mm});
            skLineSegment(sketch, "E2986", {"start": v(1.68, 32.95) * mm, "end": v(1.73, 32.84) * mm});
            skLineSegment(sketch, "E2987", {"start": v(1.73, 32.84) * mm, "end": v(1.82, 32.67) * mm});
            skLineSegment(sketch, "E2988", {"start": v(1.82, 32.67) * mm, "end": v(2.04, 33.16) * mm});
            skLineSegment(sketch, "E2989", {"start": v(2.04, 33.16) * mm, "end": v(2.3, 33.25) * mm});
            skLineSegment(sketch, "E2990", {"start": v(-1, 34.53) * mm, "end": v(-0.95, 35.57) * mm});
            skLineSegment(sketch, "E2991", {"start": v(-0.95, 35.57) * mm, "end": v(-1.16, 36.34) * mm});
            skLineSegment(sketch, "E2992", {"start": v(-1.16, 36.34) * mm, "end": v(-1.24, 36.34) * mm});
            skLineSegment(sketch, "E2993", {"start": v(-1.24, 36.34) * mm, "end": v(-1.29, 36.33) * mm});
            skLineSegment(sketch, "E2994", {"start": v(-1.29, 36.33) * mm, "end": v(-1.34, 36.29) * mm});
            skLineSegment(sketch, "E2995", {"start": v(-1.34, 36.29) * mm, "end": v(-1.4, 36.23) * mm});
            skLineSegment(sketch, "E2996", {"start": v(-1.4, 36.23) * mm, "end": v(-1.46, 36.16) * mm});
            skLineSegment(sketch, "E2997", {"start": v(-1.46, 36.16) * mm, "end": v(-1.65, 35.91) * mm});
            skLineSegment(sketch, "E2998", {"start": v(-1.65, 35.91) * mm, "end": v(-1.94, 35.6) * mm});
            skLineSegment(sketch, "E2999", {"start": v(-1.94, 35.6) * mm, "end": v(-2.26, 35.23) * mm});
            skLineSegment(sketch, "E3000", {"start": v(-2.26, 35.23) * mm, "end": v(-2.53, 34.9) * mm});
            skLineSegment(sketch, "E3001", {"start": v(-2.53, 34.9) * mm, "end": v(-2.77, 34.57) * mm});
            skLineSegment(sketch, "E3002", {"start": v(-2.77, 34.57) * mm, "end": v(-1.26, 32.94) * mm});
            skLineSegment(sketch, "E3003", {"start": v(-1.26, 32.94) * mm, "end": v(-1.04, 33.49) * mm});
            skLineSegment(sketch, "E3004", {"start": v(-1.04, 33.49) * mm, "end": v(-1, 34.53) * mm});
            skLineSegment(sketch, "E3005", {"start": v(-4.07, 34.63) * mm, "end": v(-4.13, 34.72) * mm});
            skLineSegment(sketch, "E3006", {"start": v(-4.13, 34.72) * mm, "end": v(-4.27, 34.9) * mm});
            skLineSegment(sketch, "E3007", {"start": v(-4.27, 34.9) * mm, "end": v(-4.7, 35.44) * mm});
            skLineSegment(sketch, "E3008", {"start": v(-4.7, 35.44) * mm, "end": v(-5.28, 36.15) * mm});
            skLineSegment(sketch, "E3009", {"start": v(-5.28, 36.15) * mm, "end": v(-5.48, 36.16) * mm});
            skLineSegment(sketch, "E3010", {"start": v(-5.48, 36.16) * mm, "end": v(-5.54, 35.82) * mm});
            skLineSegment(sketch, "E3011", {"start": v(-5.54, 35.82) * mm, "end": v(-5.56, 35.62) * mm});
            skLineSegment(sketch, "E3012", {"start": v(-5.56, 35.62) * mm, "end": v(-5.58, 35.34) * mm});
            skLineSegment(sketch, "E3013", {"start": v(-5.58, 35.34) * mm, "end": v(-5.6, 35.01) * mm});
            skLineSegment(sketch, "E3014", {"start": v(-5.6, 35.01) * mm, "end": v(-5.6, 34.67) * mm});
            skLineSegment(sketch, "E3015", {"start": v(-5.6, 34.67) * mm, "end": v(-5.6, 33.87) * mm});
            skLineSegment(sketch, "E3016", {"start": v(-5.6, 33.87) * mm, "end": v(-5.5, 33.52) * mm});
            skLineSegment(sketch, "E3017", {"start": v(-5.5, 33.52) * mm, "end": v(-5.45, 33.38) * mm});
            skLineSegment(sketch, "E3018", {"start": v(-5.45, 33.38) * mm, "end": v(-5.4, 33.27) * mm});
            skLineSegment(sketch, "E3019", {"start": v(-5.4, 33.27) * mm, "end": v(-5.36, 33.2) * mm});
            skLineSegment(sketch, "E3020", {"start": v(-5.36, 33.2) * mm, "end": v(-5.35, 33.18) * mm});
            skLineSegment(sketch, "E3021", {"start": v(-5.35, 33.18) * mm, "end": v(-5.33, 33.17) * mm});
            skLineSegment(sketch, "E3022", {"start": v(-5.33, 33.17) * mm, "end": v(-5.26, 33.23) * mm});
            skLineSegment(sketch, "E3023", {"start": v(-5.26, 33.23) * mm, "end": v(-5.11, 33.37) * mm});
            skLineSegment(sketch, "E3024", {"start": v(-5.11, 33.37) * mm, "end": v(-4.66, 33.85) * mm});
            skLineSegment(sketch, "E3025", {"start": v(-4.66, 33.85) * mm, "end": v(-4.04, 34.53) * mm});
            skLineSegment(sketch, "E3026", {"start": v(-4.04, 34.53) * mm, "end": v(-4.07, 34.63) * mm});
            skLineSegment(sketch, "E3027", {"start": v(5.22, 35.8) * mm, "end": v(5.28, 35.9) * mm});
            skLineSegment(sketch, "E3028", {"start": v(5.28, 35.9) * mm, "end": v(5.33, 36) * mm});
            skLineSegment(sketch, "E3029", {"start": v(5.33, 36) * mm, "end": v(5.36, 36.1) * mm});
            skLineSegment(sketch, "E3030", {"start": v(5.36, 36.1) * mm, "end": v(5.37, 36.18) * mm});
            skLineSegment(sketch, "E3031", {"start": v(5.37, 36.18) * mm, "end": v(5.37, 36.34) * mm});
            skLineSegment(sketch, "E3032", {"start": v(5.37, 36.34) * mm, "end": v(5.19, 36.45) * mm});
            skLineSegment(sketch, "E3033", {"start": v(5.19, 36.45) * mm, "end": v(5.12, 36.5) * mm});
            skLineSegment(sketch, "E3034", {"start": v(5.12, 36.5) * mm, "end": v(5.06, 36.55) * mm});
            skLineSegment(sketch, "E3035", {"start": v(5.06, 36.55) * mm, "end": v(5.02, 36.6) * mm});
            skLineSegment(sketch, "E3036", {"start": v(5.02, 36.6) * mm, "end": v(5, 36.63) * mm});
            skLineSegment(sketch, "E3037", {"start": v(5, 36.63) * mm, "end": v(5, 36.7) * mm});
            skLineSegment(sketch, "E3038", {"start": v(5, 36.7) * mm, "end": v(5.32, 36.7) * mm});
            skLineSegment(sketch, "E3039", {"start": v(5.32, 36.7) * mm, "end": v(5.45, 36.7) * mm});
            skLineSegment(sketch, "E3040", {"start": v(5.45, 36.7) * mm, "end": v(5.55, 36.72) * mm});
            skLineSegment(sketch, "E3041", {"start": v(5.55, 36.72) * mm, "end": v(5.62, 36.73) * mm});
            skLineSegment(sketch, "E3042", {"start": v(5.62, 36.73) * mm, "end": v(5.63, 36.74) * mm});
            skLineSegment(sketch, "E3043", {"start": v(5.63, 36.74) * mm, "end": v(5.64, 36.75) * mm});
            skLineSegment(sketch, "E3044", {"start": v(5.64, 36.75) * mm, "end": v(5.59, 36.9) * mm});
            skLineSegment(sketch, "E3045", {"start": v(5.59, 36.9) * mm, "end": v(5.46, 37.16) * mm});
            skLineSegment(sketch, "E3046", {"start": v(5.46, 37.16) * mm, "end": v(5.36, 37.33) * mm});
            skLineSegment(sketch, "E3047", {"start": v(5.36, 37.33) * mm, "end": v(5.25, 37.5) * mm});
            skLineSegment(sketch, "E3048", {"start": v(5.25, 37.5) * mm, "end": v(5.12, 37.66) * mm});
            skLineSegment(sketch, "E3049", {"start": v(5.12, 37.66) * mm, "end": v(4.97, 37.81) * mm});
            skLineSegment(sketch, "E3050", {"start": v(4.97, 37.81) * mm, "end": v(4.82, 37.95) * mm});
            skLineSegment(sketch, "E3051", {"start": v(4.82, 37.95) * mm, "end": v(4.67, 38.08) * mm});
            skLineSegment(sketch, "E3052", {"start": v(4.67, 38.08) * mm, "end": v(4.5, 38.19) * mm});
            skLineSegment(sketch, "E3053", {"start": v(4.5, 38.19) * mm, "end": v(4.35, 38.27) * mm});
            skLineSegment(sketch, "E3054", {"start": v(4.35, 38.27) * mm, "end": v(4.03, 38.43) * mm});
            skLineSegment(sketch, "E3055", {"start": v(4.03, 38.43) * mm, "end": v(3.42, 38.42) * mm});
            skLineSegment(sketch, "E3056", {"start": v(3.42, 38.42) * mm, "end": v(3.06, 38.25) * mm});
            skLineSegment(sketch, "E3057", {"start": v(3.06, 38.25) * mm, "end": v(2.9, 38.17) * mm});
            skLineSegment(sketch, "E3058", {"start": v(2.9, 38.17) * mm, "end": v(2.75, 38.08) * mm});
            skLineSegment(sketch, "E3059", {"start": v(2.75, 38.08) * mm, "end": v(2.62, 37.99) * mm});
            skLineSegment(sketch, "E3060", {"start": v(2.62, 37.99) * mm, "end": v(2.5, 37.88) * mm});
            skLineSegment(sketch, "E3061", {"start": v(2.5, 37.88) * mm, "end": v(2.37, 37.76) * mm});
            skLineSegment(sketch, "E3062", {"start": v(2.37, 37.76) * mm, "end": v(2.25, 37.61) * mm});
            skLineSegment(sketch, "E3063", {"start": v(2.25, 37.61) * mm, "end": v(2.13, 37.45) * mm});
            skLineSegment(sketch, "E3064", {"start": v(2.13, 37.45) * mm, "end": v(2, 37.27) * mm});
            skLineSegment(sketch, "E3065", {"start": v(2, 37.27) * mm, "end": v(1.75, 36.86) * mm});
            skLineSegment(sketch, "E3066", {"start": v(1.75, 36.86) * mm, "end": v(1.85, 36.7) * mm});
            skLineSegment(sketch, "E3067", {"start": v(1.85, 36.7) * mm, "end": v(2.32, 36.7) * mm});
            skLineSegment(sketch, "E3068", {"start": v(2.32, 36.7) * mm, "end": v(1.93, 36.28) * mm});
            skLineSegment(sketch, "E3069", {"start": v(1.93, 36.28) * mm, "end": v(1.93, 36) * mm});
            skLineSegment(sketch, "E3070", {"start": v(1.93, 36) * mm, "end": v(2.37, 35.47) * mm});
            skLineSegment(sketch, "E3071", {"start": v(2.37, 35.47) * mm, "end": v(3.08, 35.25) * mm});
            skLineSegment(sketch, "E3072", {"start": v(3.08, 35.25) * mm, "end": v(4.33, 35.26) * mm});
            skLineSegment(sketch, "E3073", {"start": v(4.33, 35.26) * mm, "end": v(5.07, 35.6) * mm});
            skLineSegment(sketch, "E3074", {"start": v(5.07, 35.6) * mm, "end": v(5.22, 35.8) * mm});
            skLineSegment(sketch, "E3075", {"start": v(-1.8, 37.58) * mm, "end": v(-1.92, 37.81) * mm});
            skLineSegment(sketch, "E3076", {"start": v(-1.92, 37.81) * mm, "end": v(-2.73, 38.36) * mm});
            skLineSegment(sketch, "E3077", {"start": v(-2.73, 38.36) * mm, "end": v(-3.58, 38.45) * mm});
            skLineSegment(sketch, "E3078", {"start": v(-3.58, 38.45) * mm, "end": v(-4.22, 38.14) * mm});
            skLineSegment(sketch, "E3079", {"start": v(-4.22, 38.14) * mm, "end": v(-4.6, 37.77) * mm});
            skLineSegment(sketch, "E3080", {"start": v(-4.6, 37.77) * mm, "end": v(-4.74, 37.61) * mm});
            skLineSegment(sketch, "E3081", {"start": v(-4.74, 37.61) * mm, "end": v(-4.85, 37.47) * mm});
            skLineSegment(sketch, "E3082", {"start": v(-4.85, 37.47) * mm, "end": v(-4.93, 37.35) * mm});
            skLineSegment(sketch, "E3083", {"start": v(-4.93, 37.35) * mm, "end": v(-4.95, 37.31) * mm});
            skLineSegment(sketch, "E3084", {"start": v(-4.95, 37.31) * mm, "end": v(-4.96, 37.28) * mm});
            skLineSegment(sketch, "E3085", {"start": v(-4.96, 37.28) * mm, "end": v(-4.96, 37.17) * mm});
            skLineSegment(sketch, "E3086", {"start": v(-4.96, 37.17) * mm, "end": v(-3.4, 35.34) * mm});
            skLineSegment(sketch, "E3087", {"start": v(-3.4, 35.34) * mm, "end": v(-3.36, 35.34) * mm});
            skLineSegment(sketch, "E3088", {"start": v(-3.36, 35.34) * mm, "end": v(-1.67, 37.35) * mm});
            skLineSegment(sketch, "E3089", {"start": v(-1.67, 37.35) * mm, "end": v(-1.8, 37.58) * mm});
            skLineSegment(sketch, "E3090", {"start": v(3.66, 35.8) * mm, "end": v(3.83, 35.8) * mm});
            skLineSegment(sketch, "E3091", {"start": v(3.83, 35.8) * mm, "end": v(4.2, 36.16) * mm});
            skLineSegment(sketch, "E3092", {"start": v(4.2, 36.16) * mm, "end": v(4.16, 37.33) * mm});
            skLineSegment(sketch, "E3093", {"start": v(4.16, 37.33) * mm, "end": v(3.06, 37.32) * mm});
            skLineSegment(sketch, "E3094", {"start": v(3.06, 37.32) * mm, "end": v(3.09, 36.12) * mm});
            skLineSegment(sketch, "E3095", {"start": v(3.09, 36.12) * mm, "end": v(3.49, 35.8) * mm});
            skLineSegment(sketch, "E3096", {"start": v(3.49, 35.8) * mm, "end": v(3.66, 35.8) * mm});
            skLineSegment(sketch, "E3097", {"start": v(2.02, 41.47) * mm, "end": v(2.25, 41.72) * mm});
            skLineSegment(sketch, "E3098", {"start": v(2.25, 41.72) * mm, "end": v(2.46, 41.98) * mm});
            skLineSegment(sketch, "E3099", {"start": v(2.46, 41.98) * mm, "end": v(2.67, 42.23) * mm});
            skLineSegment(sketch, "E3100", {"start": v(2.67, 42.23) * mm, "end": v(2.86, 42.5) * mm});
            skLineSegment(sketch, "E3101", {"start": v(2.86, 42.5) * mm, "end": v(3.05, 42.77) * mm});
            skLineSegment(sketch, "E3102", {"start": v(3.05, 42.77) * mm, "end": v(3.22, 43.04) * mm});
            skLineSegment(sketch, "E3103", {"start": v(3.22, 43.04) * mm, "end": v(3.4, 43.32) * mm});
            skLineSegment(sketch, "E3104", {"start": v(3.4, 43.32) * mm, "end": v(3.55, 43.6) * mm});
            skLineSegment(sketch, "E3105", {"start": v(3.55, 43.6) * mm, "end": v(3.92, 44.3) * mm});
            skLineSegment(sketch, "E3106", {"start": v(3.92, 44.3) * mm, "end": v(4.46, 45.87) * mm});
            skLineSegment(sketch, "E3107", {"start": v(4.46, 45.87) * mm, "end": v(4.76, 47.76) * mm});
            skLineSegment(sketch, "E3108", {"start": v(4.76, 47.76) * mm, "end": v(4.64, 47.88) * mm});
            skLineSegment(sketch, "E3109", {"start": v(4.64, 47.88) * mm, "end": v(3.33, 47.53) * mm});
            skLineSegment(sketch, "E3110", {"start": v(3.33, 47.53) * mm, "end": v(1.7, 47.54) * mm});
            skLineSegment(sketch, "E3111", {"start": v(1.7, 47.54) * mm, "end": v(1.1, 47.83) * mm});
            skLineSegment(sketch, "E3112", {"start": v(1.1, 47.83) * mm, "end": v(0.65, 48.07) * mm});
            skLineSegment(sketch, "E3113", {"start": v(0.65, 48.07) * mm, "end": v(0.47, 48.17) * mm});
            skLineSegment(sketch, "E3114", {"start": v(0.47, 48.17) * mm, "end": v(0.36, 48.23) * mm});
            skLineSegment(sketch, "E3115", {"start": v(0.36, 48.23) * mm, "end": v(0.2, 48.35) * mm});
            skLineSegment(sketch, "E3116", {"start": v(0.2, 48.35) * mm, "end": v(0.05, 48.23) * mm});
            skLineSegment(sketch, "E3117", {"start": v(0.05, 48.23) * mm, "end": v(-0.24, 48.07) * mm});
            skLineSegment(sketch, "E3118", {"start": v(-0.24, 48.07) * mm, "end": v(-0.7, 47.83) * mm});
            skLineSegment(sketch, "E3119", {"start": v(-0.7, 47.83) * mm, "end": v(-1.3, 47.53) * mm});
            skLineSegment(sketch, "E3120", {"start": v(-1.3, 47.53) * mm, "end": v(-3.01, 47.55) * mm});
            skLineSegment(sketch, "E3121", {"start": v(-3.01, 47.55) * mm, "end": v(-3.5, 47.7) * mm});
            skLineSegment(sketch, "E3122", {"start": v(-3.5, 47.7) * mm, "end": v(-3.9, 47.8) * mm});
            skLineSegment(sketch, "E3123", {"start": v(-3.9, 47.8) * mm, "end": v(-4.06, 47.84) * mm});
            skLineSegment(sketch, "E3124", {"start": v(-4.06, 47.84) * mm, "end": v(-4.17, 47.85) * mm});
            skLineSegment(sketch, "E3125", {"start": v(-4.17, 47.85) * mm, "end": v(-4.34, 47.85) * mm});
            skLineSegment(sketch, "E3126", {"start": v(-4.34, 47.85) * mm, "end": v(-4.28, 47.28) * mm});
            skLineSegment(sketch, "E3127", {"start": v(-4.28, 47.28) * mm, "end": v(-4.23, 46.96) * mm});
            skLineSegment(sketch, "E3128", {"start": v(-4.23, 46.96) * mm, "end": v(-4.17, 46.6) * mm});
            skLineSegment(sketch, "E3129", {"start": v(-4.17, 46.6) * mm, "end": v(-4.08, 46.22) * mm});
            skLineSegment(sketch, "E3130", {"start": v(-4.08, 46.22) * mm, "end": v(-3.99, 45.83) * mm});
            skLineSegment(sketch, "E3131", {"start": v(-3.99, 45.83) * mm, "end": v(-3.88, 45.44) * mm});
            skLineSegment(sketch, "E3132", {"start": v(-3.88, 45.44) * mm, "end": v(-3.76, 45.06) * mm});
            skLineSegment(sketch, "E3133", {"start": v(-3.76, 45.06) * mm, "end": v(-3.64, 44.7) * mm});
            skLineSegment(sketch, "E3134", {"start": v(-3.64, 44.7) * mm, "end": v(-3.52, 44.39) * mm});
            skLineSegment(sketch, "E3135", {"start": v(-3.52, 44.39) * mm, "end": v(-3.23, 43.7) * mm});
            skLineSegment(sketch, "E3136", {"start": v(-3.23, 43.7) * mm, "end": v(-2.17, 42.1) * mm});
            skLineSegment(sketch, "E3137", {"start": v(-2.17, 42.1) * mm, "end": v(-1.62, 41.5) * mm});
            skLineSegment(sketch, "E3138", {"start": v(-1.62, 41.5) * mm, "end": v(-1.36, 41.23) * mm});
            skLineSegment(sketch, "E3139", {"start": v(-1.36, 41.23) * mm, "end": v(-1.05, 40.93) * mm});
            skLineSegment(sketch, "E3140", {"start": v(-1.05, 40.93) * mm, "end": v(-0.74, 40.63) * mm});
            skLineSegment(sketch, "E3141", {"start": v(-0.74, 40.63) * mm, "end": v(-0.45, 40.39) * mm});
            skLineSegment(sketch, "E3142", {"start": v(-0.45, 40.39) * mm, "end": v(0.18, 39.88) * mm});
            skLineSegment(sketch, "E3143", {"start": v(0.18, 39.88) * mm, "end": v(0.22, 39.88) * mm});
            skLineSegment(sketch, "E3144", {"start": v(0.22, 39.88) * mm, "end": v(0.25, 39.89) * mm});
            skLineSegment(sketch, "E3145", {"start": v(0.25, 39.89) * mm, "end": v(0.3, 39.93) * mm});
            skLineSegment(sketch, "E3146", {"start": v(0.3, 39.93) * mm, "end": v(0.48, 40.06) * mm});
            skLineSegment(sketch, "E3147", {"start": v(0.48, 40.06) * mm, "end": v(1, 40.5) * mm});
            skLineSegment(sketch, "E3148", {"start": v(1, 40.5) * mm, "end": v(1.58, 41.04) * mm});
            skLineSegment(sketch, "E3149", {"start": v(1.58, 41.04) * mm, "end": v(1.83, 41.28) * mm});
            skLineSegment(sketch, "E3150", {"start": v(1.83, 41.28) * mm, "end": v(2.02, 41.47) * mm});
            skLineSegment(sketch, "E3151", {"start": v(-12.62, -40.87) * mm, "end": v(-12.5, -40.85) * mm});
            skLineSegment(sketch, "E3152", {"start": v(-12.5, -40.85) * mm, "end": v(-12.25, -40.8) * mm});
            skLineSegment(sketch, "E3153", {"start": v(-12.25, -40.8) * mm, "end": v(-11.52, -40.64) * mm});
            skLineSegment(sketch, "E3154", {"start": v(-11.52, -40.64) * mm, "end": v(-10.54, -40.4) * mm});
            skLineSegment(sketch, "E3155", {"start": v(-10.54, -40.4) * mm, "end": v(-10.4, -40.28) * mm});
            skLineSegment(sketch, "E3156", {"start": v(-10.4, -40.28) * mm, "end": v(-10.68, -39.96) * mm});
            skLineSegment(sketch, "E3157", {"start": v(-10.68, -39.96) * mm, "end": v(-11.43, -39.1) * mm});
            skLineSegment(sketch, "E3158", {"start": v(-11.43, -39.1) * mm, "end": v(-12.16, -38.22) * mm});
            skLineSegment(sketch, "E3159", {"start": v(-12.16, -38.22) * mm, "end": v(-12.86, -37.35) * mm});
            skLineSegment(sketch, "E3160", {"start": v(-12.86, -37.35) * mm, "end": v(-13.54, -36.48) * mm});
            skLineSegment(sketch, "E3161", {"start": v(-13.54, -36.48) * mm, "end": v(-14.2, -35.59) * mm});
            skLineSegment(sketch, "E3162", {"start": v(-14.2, -35.59) * mm, "end": v(-14.85, -34.68) * mm});
            skLineSegment(sketch, "E3163", {"start": v(-14.85, -34.68) * mm, "end": v(-15.5, -33.75) * mm});
            skLineSegment(sketch, "E3164", {"start": v(-15.5, -33.75) * mm, "end": v(-16.14, -32.8) * mm});
            skLineSegment(sketch, "E3165", {"start": v(-16.14, -32.8) * mm, "end": v(-17.17, -31.22) * mm});
            skLineSegment(sketch, "E3166", {"start": v(-17.17, -31.22) * mm, "end": v(-18.52, -28.86) * mm});
            skLineSegment(sketch, "E3167", {"start": v(-18.52, -28.86) * mm, "end": v(-18.94, -28.1) * mm});
            skLineSegment(sketch, "E3168", {"start": v(-18.94, -28.1) * mm, "end": v(-19.45, -27.12) * mm});
            skLineSegment(sketch, "E3169", {"start": v(-19.45, -27.12) * mm, "end": v(-20.08, -25.87) * mm});
            skLineSegment(sketch, "E3170", {"start": v(-20.08, -25.87) * mm, "end": v(-21.05, -23.88) * mm});
            skLineSegment(sketch, "E3171", {"start": v(-21.05, -23.88) * mm, "end": v(-21.42, -23.05) * mm});
            skLineSegment(sketch, "E3172", {"start": v(-21.42, -23.05) * mm, "end": v(-21.75, -22.27) * mm});
            skLineSegment(sketch, "E3173", {"start": v(-21.75, -22.27) * mm, "end": v(-22.06, -21.54) * mm});
            skLineSegment(sketch, "E3174", {"start": v(-22.06, -21.54) * mm, "end": v(-22.35, -20.82) * mm});
            skLineSegment(sketch, "E3175", {"start": v(-22.35, -20.82) * mm, "end": v(-22.63, -20.1) * mm});
            skLineSegment(sketch, "E3176", {"start": v(-22.63, -20.1) * mm, "end": v(-22.91, -19.35) * mm});
            skLineSegment(sketch, "E3177", {"start": v(-22.91, -19.35) * mm, "end": v(-23.5, -17.68) * mm});
            skLineSegment(sketch, "E3178", {"start": v(-23.5, -17.68) * mm, "end": v(-24.19, -15.72) * mm});
            skLineSegment(sketch, "E3179", {"start": v(-24.19, -15.72) * mm, "end": v(-24.69, -14) * mm});
            skLineSegment(sketch, "E3180", {"start": v(-24.69, -14) * mm, "end": v(-25.17, -12.27) * mm});
            skLineSegment(sketch, "E3181", {"start": v(-25.17, -12.27) * mm, "end": v(-25.64, -10.52) * mm});
            skLineSegment(sketch, "E3182", {"start": v(-25.64, -10.52) * mm, "end": v(-26.12, -8.52) * mm});
            skLineSegment(sketch, "E3183", {"start": v(-26.12, -8.52) * mm, "end": v(-26.35, -7.4) * mm});
            skLineSegment(sketch, "E3184", {"start": v(-26.35, -7.4) * mm, "end": v(-26.52, -6.52) * mm});
            skLineSegment(sketch, "E3185", {"start": v(-26.52, -6.52) * mm, "end": v(-26.7, -5.64) * mm});
            skLineSegment(sketch, "E3186", {"start": v(-26.7, -5.64) * mm, "end": v(-26.85, -4.75) * mm});
            skLineSegment(sketch, "E3187", {"start": v(-26.85, -4.75) * mm, "end": v(-27, -3.85) * mm});
            skLineSegment(sketch, "E3188", {"start": v(-27, -3.85) * mm, "end": v(-27.14, -2.94) * mm});
            skLineSegment(sketch, "E3189", {"start": v(-27.14, -2.94) * mm, "end": v(-27.28, -2.02) * mm});
            skLineSegment(sketch, "E3190", {"start": v(-27.28, -2.02) * mm, "end": v(-27.4, -1.09) * mm});
            skLineSegment(sketch, "E3191", {"start": v(-27.4, -1.09) * mm, "end": v(-27.52, -0.15) * mm});
            skLineSegment(sketch, "E3192", {"start": v(-27.52, -0.15) * mm, "end": v(-27.63, 0.8) * mm});
            skLineSegment(sketch, "E3193", {"start": v(-27.63, 0.8) * mm, "end": v(-27.73, 1.76) * mm});
            skLineSegment(sketch, "E3194", {"start": v(-27.73, 1.76) * mm, "end": v(-27.82, 2.73) * mm});
            skLineSegment(sketch, "E3195", {"start": v(-27.82, 2.73) * mm, "end": v(-27.9, 3.7) * mm});
            skLineSegment(sketch, "E3196", {"start": v(-27.9, 3.7) * mm, "end": v(-27.98, 4.7) * mm});
            skLineSegment(sketch, "E3197", {"start": v(-27.98, 4.7) * mm, "end": v(-28.05, 5.7) * mm});
            skLineSegment(sketch, "E3198", {"start": v(-28.05, 5.7) * mm, "end": v(-28.1, 6.71) * mm});
            skLineSegment(sketch, "E3199", {"start": v(-28.1, 6.71) * mm, "end": v(-28.16, 7.73) * mm});
            skLineSegment(sketch, "E3200", {"start": v(-28.16, 7.73) * mm, "end": v(-28.25, 9.8) * mm});
            skLineSegment(sketch, "E3201", {"start": v(-28.25, 9.8) * mm, "end": v(-28.25, 15.1) * mm});
            skLineSegment(sketch, "E3202", {"start": v(-28.25, 15.1) * mm, "end": v(-28.13, 18.12) * mm});
            skLineSegment(sketch, "E3203", {"start": v(-28.13, 18.12) * mm, "end": v(-28.03, 18.12) * mm});
            skLineSegment(sketch, "E3204", {"start": v(-28.03, 18.12) * mm, "end": v(-27.92, 18.1) * mm});
            skLineSegment(sketch, "E3205", {"start": v(-27.92, 18.1) * mm, "end": v(-27.7, 18) * mm});
            skLineSegment(sketch, "E3206", {"start": v(-27.7, 18) * mm, "end": v(-27.4, 17.87) * mm});
            skLineSegment(sketch, "E3207", {"start": v(-27.4, 17.87) * mm, "end": v(-27.07, 17.7) * mm});
            skLineSegment(sketch, "E3208", {"start": v(-27.07, 17.7) * mm, "end": v(-26.55, 17.46) * mm});
            skLineSegment(sketch, "E3209", {"start": v(-26.55, 17.46) * mm, "end": v(-26.03, 17.22) * mm});
            skLineSegment(sketch, "E3210", {"start": v(-26.03, 17.22) * mm, "end": v(-25.52, 17) * mm});
            skLineSegment(sketch, "E3211", {"start": v(-25.52, 17) * mm, "end": v(-25, 16.78) * mm});
            skLineSegment(sketch, "E3212", {"start": v(-25, 16.78) * mm, "end": v(-24.49, 16.58) * mm});
            skLineSegment(sketch, "E3213", {"start": v(-24.49, 16.58) * mm, "end": v(-23.98, 16.39) * mm});
            skLineSegment(sketch, "E3214", {"start": v(-23.98, 16.39) * mm, "end": v(-23.46, 16.2) * mm});
            skLineSegment(sketch, "E3215", {"start": v(-23.46, 16.2) * mm, "end": v(-22.95, 16.03) * mm});
            skLineSegment(sketch, "E3216", {"start": v(-22.95, 16.03) * mm, "end": v(-22.44, 15.87) * mm});
            skLineSegment(sketch, "E3217", {"start": v(-22.44, 15.87) * mm, "end": v(-21.93, 15.72) * mm});
            skLineSegment(sketch, "E3218", {"start": v(-21.93, 15.72) * mm, "end": v(-21.42, 15.58) * mm});
            skLineSegment(sketch, "E3219", {"start": v(-21.42, 15.58) * mm, "end": v(-20.91, 15.45) * mm});
            skLineSegment(sketch, "E3220", {"start": v(-20.91, 15.45) * mm, "end": v(-20.4, 15.33) * mm});
            skLineSegment(sketch, "E3221", {"start": v(-20.4, 15.33) * mm, "end": v(-19.9, 15.22) * mm});
            skLineSegment(sketch, "E3222", {"start": v(-19.9, 15.22) * mm, "end": v(-19.38, 15.12) * mm});
            skLineSegment(sketch, "E3223", {"start": v(-19.38, 15.12) * mm, "end": v(-18.87, 15.03) * mm});
            skLineSegment(sketch, "E3224", {"start": v(-18.87, 15.03) * mm, "end": v(-17.79, 14.85) * mm});
            skLineSegment(sketch, "E3225", {"start": v(-17.79, 14.85) * mm, "end": v(-14.59, 14.75) * mm});
            skLineSegment(sketch, "E3226", {"start": v(-14.59, 14.75) * mm, "end": v(-13.56, 14.86) * mm});
            skLineSegment(sketch, "E3227", {"start": v(-13.56, 14.86) * mm, "end": v(-12.74, 14.96) * mm});
            skLineSegment(sketch, "E3228", {"start": v(-12.74, 14.96) * mm, "end": v(-11.93, 15.09) * mm});
            skLineSegment(sketch, "E3229", {"start": v(-11.93, 15.09) * mm, "end": v(-11.13, 15.24) * mm});
            skLineSegment(sketch, "E3230", {"start": v(-11.13, 15.24) * mm, "end": v(-10.34, 15.43) * mm});
            skLineSegment(sketch, "E3231", {"start": v(-10.34, 15.43) * mm, "end": v(-9.55, 15.65) * mm});
            skLineSegment(sketch, "E3232", {"start": v(-9.55, 15.65) * mm, "end": v(-8.77, 15.9) * mm});
            skLineSegment(sketch, "E3233", {"start": v(-8.77, 15.9) * mm, "end": v(-8, 16.17) * mm});
            skLineSegment(sketch, "E3234", {"start": v(-8, 16.17) * mm, "end": v(-7.23, 16.47) * mm});
            skLineSegment(sketch, "E3235", {"start": v(-7.23, 16.47) * mm, "end": v(-6.46, 16.8) * mm});
            skLineSegment(sketch, "E3236", {"start": v(-6.46, 16.8) * mm, "end": v(-5.7, 17.17) * mm});
            skLineSegment(sketch, "E3237", {"start": v(-5.7, 17.17) * mm, "end": v(-4.94, 17.57) * mm});
            skLineSegment(sketch, "E3238", {"start": v(-4.94, 17.57) * mm, "end": v(-4.19, 18) * mm});
            skLineSegment(sketch, "E3239", {"start": v(-4.19, 18) * mm, "end": v(-3.43, 18.45) * mm});
            skLineSegment(sketch, "E3240", {"start": v(-3.43, 18.45) * mm, "end": v(-2.68, 18.94) * mm});
            skLineSegment(sketch, "E3241", {"start": v(-2.68, 18.94) * mm, "end": v(-1.93, 19.46) * mm});
            skLineSegment(sketch, "E3242", {"start": v(-1.93, 19.46) * mm, "end": v(-1.18, 20) * mm});
            skLineSegment(sketch, "E3243", {"start": v(-1.18, 20) * mm, "end": v(-0.08, 20.84) * mm});
            skLineSegment(sketch, "E3244", {"start": v(-0.08, 20.84) * mm, "end": v(0.05, 20.84) * mm});
            skLineSegment(sketch, "E3245", {"start": v(0.05, 20.84) * mm, "end": v(1.06, 20.09) * mm});
            skLineSegment(sketch, "E3246", {"start": v(1.06, 20.09) * mm, "end": v(1.82, 19.52) * mm});
            skLineSegment(sketch, "E3247", {"start": v(1.82, 19.52) * mm, "end": v(2.59, 19) * mm});
            skLineSegment(sketch, "E3248", {"start": v(2.59, 19) * mm, "end": v(3.35, 18.5) * mm});
            skLineSegment(sketch, "E3249", {"start": v(3.35, 18.5) * mm, "end": v(4.1, 18.03) * mm});
            skLineSegment(sketch, "E3250", {"start": v(4.1, 18.03) * mm, "end": v(4.87, 17.6) * mm});
            skLineSegment(sketch, "E3251", {"start": v(4.87, 17.6) * mm, "end": v(5.63, 17.2) * mm});
            skLineSegment(sketch, "E3252", {"start": v(5.63, 17.2) * mm, "end": v(6.38, 16.83) * mm});
            skLineSegment(sketch, "E3253", {"start": v(6.38, 16.83) * mm, "end": v(7.15, 16.49) * mm});
            skLineSegment(sketch, "E3254", {"start": v(7.15, 16.49) * mm, "end": v(7.9, 16.18) * mm});
            skLineSegment(sketch, "E3255", {"start": v(7.9, 16.18) * mm, "end": v(8.67, 15.9) * mm});
            skLineSegment(sketch, "E3256", {"start": v(8.67, 15.9) * mm, "end": v(9.44, 15.66) * mm});
            skLineSegment(sketch, "E3257", {"start": v(9.44, 15.66) * mm, "end": v(10.22, 15.44) * mm});
            skLineSegment(sketch, "E3258", {"start": v(10.22, 15.44) * mm, "end": v(11, 15.25) * mm});
            skLineSegment(sketch, "E3259", {"start": v(11, 15.25) * mm, "end": v(11.78, 15.1) * mm});
            skLineSegment(sketch, "E3260", {"start": v(11.78, 15.1) * mm, "end": v(12.57, 14.97) * mm});
            skLineSegment(sketch, "E3261", {"start": v(12.57, 14.97) * mm, "end": v(13.36, 14.87) * mm});
            skLineSegment(sketch, "E3262", {"start": v(13.36, 14.87) * mm, "end": v(14.24, 14.77) * mm});
            skLineSegment(sketch, "E3263", {"start": v(14.24, 14.77) * mm, "end": v(16.7, 14.77) * mm});
            skLineSegment(sketch, "E3264", {"start": v(16.7, 14.77) * mm, "end": v(17.58, 14.87) * mm});
            skLineSegment(sketch, "E3265", {"start": v(17.58, 14.87) * mm, "end": v(18.01, 14.92) * mm});
            skLineSegment(sketch, "E3266", {"start": v(18.01, 14.92) * mm, "end": v(18.44, 14.98) * mm});
            skLineSegment(sketch, "E3267", {"start": v(18.44, 14.98) * mm, "end": v(18.87, 15.04) * mm});
            skLineSegment(sketch, "E3268", {"start": v(18.87, 15.04) * mm, "end": v(19.31, 15.12) * mm});
            skLineSegment(sketch, "E3269", {"start": v(19.31, 15.12) * mm, "end": v(20.2, 15.3) * mm});
            skLineSegment(sketch, "E3270", {"start": v(20.2, 15.3) * mm, "end": v(21.08, 15.5) * mm});
            skLineSegment(sketch, "E3271", {"start": v(21.08, 15.5) * mm, "end": v(21.96, 15.73) * mm});
            skLineSegment(sketch, "E3272", {"start": v(21.96, 15.73) * mm, "end": v(22.82, 15.99) * mm});
            skLineSegment(sketch, "E3273", {"start": v(22.82, 15.99) * mm, "end": v(23.25, 16.13) * mm});
            skLineSegment(sketch, "E3274", {"start": v(23.25, 16.13) * mm, "end": v(23.67, 16.27) * mm});
            skLineSegment(sketch, "E3275", {"start": v(23.67, 16.27) * mm, "end": v(24.08, 16.42) * mm});
            skLineSegment(sketch, "E3276", {"start": v(24.08, 16.42) * mm, "end": v(24.5, 16.58) * mm});
            skLineSegment(sketch, "E3277", {"start": v(24.5, 16.58) * mm, "end": v(25.29, 16.92) * mm});
            skLineSegment(sketch, "E3278", {"start": v(25.29, 16.92) * mm, "end": v(26.51, 17.46) * mm});
            skLineSegment(sketch, "E3279", {"start": v(26.51, 17.46) * mm, "end": v(28.03, 18.15) * mm});
            skLineSegment(sketch, "E3280", {"start": v(28.03, 18.15) * mm, "end": v(28.16, 18.02) * mm});
            skLineSegment(sketch, "E3281", {"start": v(28.16, 18.02) * mm, "end": v(28.23, 9.02) * mm});
            skLineSegment(sketch, "E3282", {"start": v(28.23, 9.02) * mm, "end": v(28.02, 5.3) * mm});
            skLineSegment(sketch, "E3283", {"start": v(28.02, 5.3) * mm, "end": v(27.75, 2.04) * mm});
            skLineSegment(sketch, "E3284", {"start": v(27.75, 2.04) * mm, "end": v(27.61, 0.82) * mm});
            skLineSegment(sketch, "E3285", {"start": v(27.61, 0.82) * mm, "end": v(27.44, -0.6) * mm});
            skLineSegment(sketch, "E3286", {"start": v(27.44, -0.6) * mm, "end": v(27.25, -2) * mm});
            skLineSegment(sketch, "E3287", {"start": v(27.25, -2) * mm, "end": v(27.04, -3.39) * mm});
            skLineSegment(sketch, "E3288", {"start": v(27.04, -3.39) * mm, "end": v(26.8, -4.77) * mm});
            skLineSegment(sketch, "E3289", {"start": v(26.8, -4.77) * mm, "end": v(26.55, -6.15) * mm});
            skLineSegment(sketch, "E3290", {"start": v(26.55, -6.15) * mm, "end": v(26.27, -7.54) * mm});
            skLineSegment(sketch, "E3291", {"start": v(26.27, -7.54) * mm, "end": v(25.96, -8.94) * mm});
            skLineSegment(sketch, "E3292", {"start": v(25.96, -8.94) * mm, "end": v(25.62, -10.38) * mm});
            skLineSegment(sketch, "E3293", {"start": v(25.62, -10.38) * mm, "end": v(24.81, -13.5) * mm});
            skLineSegment(sketch, "E3294", {"start": v(24.81, -13.5) * mm, "end": v(24.55, -14.37) * mm});
            skLineSegment(sketch, "E3295", {"start": v(24.55, -14.37) * mm, "end": v(24.3, -15.21) * mm});
            skLineSegment(sketch, "E3296", {"start": v(24.3, -15.21) * mm, "end": v(24.03, -16.04) * mm});
            skLineSegment(sketch, "E3297", {"start": v(24.03, -16.04) * mm, "end": v(23.77, -16.84) * mm});
            skLineSegment(sketch, "E3298", {"start": v(23.77, -16.84) * mm, "end": v(23.5, -17.63) * mm});
            skLineSegment(sketch, "E3299", {"start": v(23.5, -17.63) * mm, "end": v(23.23, -18.41) * mm});
            skLineSegment(sketch, "E3300", {"start": v(23.23, -18.41) * mm, "end": v(22.95, -19.18) * mm});
            skLineSegment(sketch, "E3301", {"start": v(22.95, -19.18) * mm, "end": v(22.66, -19.93) * mm});
            skLineSegment(sketch, "E3302", {"start": v(22.66, -19.93) * mm, "end": v(22.37, -20.68) * mm});
            skLineSegment(sketch, "E3303", {"start": v(22.37, -20.68) * mm, "end": v(22.07, -21.42) * mm});
            skLineSegment(sketch, "E3304", {"start": v(22.07, -21.42) * mm, "end": v(21.76, -22.16) * mm});
            skLineSegment(sketch, "E3305", {"start": v(21.76, -22.16) * mm, "end": v(21.44, -22.9) * mm});
            skLineSegment(sketch, "E3306", {"start": v(21.44, -22.9) * mm, "end": v(21.1, -23.64) * mm});
            skLineSegment(sketch, "E3307", {"start": v(21.1, -23.64) * mm, "end": v(20.76, -24.38) * mm});
            skLineSegment(sketch, "E3308", {"start": v(20.76, -24.38) * mm, "end": v(20.41, -25.12) * mm});
            skLineSegment(sketch, "E3309", {"start": v(20.41, -25.12) * mm, "end": v(20.05, -25.87) * mm});
            skLineSegment(sketch, "E3310", {"start": v(20.05, -25.87) * mm, "end": v(19.06, -27.87) * mm});
            skLineSegment(sketch, "E3311", {"start": v(19.06, -27.87) * mm, "end": v(17.44, -30.72) * mm});
            skLineSegment(sketch, "E3312", {"start": v(17.44, -30.72) * mm, "end": v(16.82, -31.7) * mm});
            skLineSegment(sketch, "E3313", {"start": v(16.82, -31.7) * mm, "end": v(16.12, -32.77) * mm});
            skLineSegment(sketch, "E3314", {"start": v(16.12, -32.77) * mm, "end": v(15.3, -33.98) * mm});
            skLineSegment(sketch, "E3315", {"start": v(15.3, -33.98) * mm, "end": v(13.6, -36.35) * mm});
            skLineSegment(sketch, "E3316", {"start": v(13.6, -36.35) * mm, "end": v(13.22, -36.85) * mm});
            skLineSegment(sketch, "E3317", {"start": v(13.22, -36.85) * mm, "end": v(12.77, -37.42) * mm});
            skLineSegment(sketch, "E3318", {"start": v(12.77, -37.42) * mm, "end": v(12.3, -38) * mm});
            skLineSegment(sketch, "E3319", {"start": v(12.3, -38) * mm, "end": v(11.88, -38.52) * mm});
            skLineSegment(sketch, "E3320", {"start": v(11.88, -38.52) * mm, "end": v(10.65, -39.97) * mm});
            skLineSegment(sketch, "E3321", {"start": v(10.65, -39.97) * mm, "end": v(10.35, -40.31) * mm});
            skLineSegment(sketch, "E3322", {"start": v(10.35, -40.31) * mm, "end": v(10.49, -40.4) * mm});
            skLineSegment(sketch, "E3323", {"start": v(10.49, -40.4) * mm, "end": v(12.53, -40.9) * mm});
            skLineSegment(sketch, "E3324", {"start": v(12.53, -40.9) * mm, "end": v(12.78, -40.8) * mm});
            skLineSegment(sketch, "E3325", {"start": v(12.78, -40.8) * mm, "end": v(13.66, -39.74) * mm});
            skLineSegment(sketch, "E3326", {"start": v(13.66, -39.74) * mm, "end": v(14.18, -39.1) * mm});
            skLineSegment(sketch, "E3327", {"start": v(14.18, -39.1) * mm, "end": v(14.7, -38.45) * mm});
            skLineSegment(sketch, "E3328", {"start": v(14.7, -38.45) * mm, "end": v(15.21, -37.79) * mm});
            skLineSegment(sketch, "E3329", {"start": v(15.21, -37.79) * mm, "end": v(15.72, -37.1) * mm});
            skLineSegment(sketch, "E3330", {"start": v(15.72, -37.1) * mm, "end": v(16.23, -36.4) * mm});
            skLineSegment(sketch, "E3331", {"start": v(16.23, -36.4) * mm, "end": v(16.73, -35.7) * mm});
            skLineSegment(sketch, "E3332", {"start": v(16.73, -35.7) * mm, "end": v(17.23, -34.98) * mm});
            skLineSegment(sketch, "E3333", {"start": v(17.23, -34.98) * mm, "end": v(17.72, -34.24) * mm});
            skLineSegment(sketch, "E3334", {"start": v(17.72, -34.24) * mm, "end": v(18.94, -32.4) * mm});
            skLineSegment(sketch, "E3335", {"start": v(18.94, -32.4) * mm, "end": v(19.57, -31.31) * mm});
            skLineSegment(sketch, "E3336", {"start": v(19.57, -31.31) * mm, "end": v(20.3, -30.02) * mm});
            skLineSegment(sketch, "E3337", {"start": v(20.3, -30.02) * mm, "end": v(20.97, -28.8) * mm});
            skLineSegment(sketch, "E3338", {"start": v(20.97, -28.8) * mm, "end": v(21.6, -27.6) * mm});
            skLineSegment(sketch, "E3339", {"start": v(21.6, -27.6) * mm, "end": v(22.22, -26.34) * mm});
            skLineSegment(sketch, "E3340", {"start": v(22.22, -26.34) * mm, "end": v(23.02, -24.7) * mm});
            skLineSegment(sketch, "E3341", {"start": v(23.02, -24.7) * mm, "end": v(23.58, -23.38) * mm});
            skLineSegment(sketch, "E3342", {"start": v(23.58, -23.38) * mm, "end": v(24.17, -21.95) * mm});
            skLineSegment(sketch, "E3343", {"start": v(24.17, -21.95) * mm, "end": v(24.8, -20.35) * mm});
            skLineSegment(sketch, "E3344", {"start": v(24.8, -20.35) * mm, "end": v(25.47, -18.62) * mm});
            skLineSegment(sketch, "E3345", {"start": v(25.47, -18.62) * mm, "end": v(25.97, -17.08) * mm});
            skLineSegment(sketch, "E3346", {"start": v(25.97, -17.08) * mm, "end": v(26.44, -15.57) * mm});
            skLineSegment(sketch, "E3347", {"start": v(26.44, -15.57) * mm, "end": v(26.68, -14.78) * mm});
            skLineSegment(sketch, "E3348", {"start": v(26.68, -14.78) * mm, "end": v(26.88, -14.1) * mm});
            skLineSegment(sketch, "E3349", {"start": v(26.88, -14.1) * mm, "end": v(27.52, -11.7) * mm});
            skLineSegment(sketch, "E3350", {"start": v(27.52, -11.7) * mm, "end": v(27.81, -10.5) * mm});
            skLineSegment(sketch, "E3351", {"start": v(27.81, -10.5) * mm, "end": v(28.1, -9.22) * mm});
            skLineSegment(sketch, "E3352", {"start": v(28.1, -9.22) * mm, "end": v(28.38, -7.86) * mm});
            skLineSegment(sketch, "E3353", {"start": v(28.38, -7.86) * mm, "end": v(28.67, -6.4) * mm});
            skLineSegment(sketch, "E3354", {"start": v(28.67, -6.4) * mm, "end": v(29.25, -3) * mm});
            skLineSegment(sketch, "E3355", {"start": v(29.25, -3) * mm, "end": v(29.6, -0.36) * mm});
            skLineSegment(sketch, "E3356", {"start": v(29.6, -0.36) * mm, "end": v(29.73, 0.7) * mm});
            skLineSegment(sketch, "E3357", {"start": v(29.73, 0.7) * mm, "end": v(29.84, 1.74) * mm});
            skLineSegment(sketch, "E3358", {"start": v(29.84, 1.74) * mm, "end": v(29.94, 2.8) * mm});
            skLineSegment(sketch, "E3359", {"start": v(29.94, 2.8) * mm, "end": v(30.03, 3.86) * mm});
            skLineSegment(sketch, "E3360", {"start": v(30.03, 3.86) * mm, "end": v(30.11, 4.94) * mm});
            skLineSegment(sketch, "E3361", {"start": v(30.11, 4.94) * mm, "end": v(30.18, 6.05) * mm});
            skLineSegment(sketch, "E3362", {"start": v(30.18, 6.05) * mm, "end": v(30.25, 7.2) * mm});
            skLineSegment(sketch, "E3363", {"start": v(30.25, 7.2) * mm, "end": v(30.3, 8.38) * mm});
            skLineSegment(sketch, "E3364", {"start": v(30.3, 8.38) * mm, "end": v(30.4, 10.92) * mm});
            skLineSegment(sketch, "E3365", {"start": v(30.4, 10.92) * mm, "end": v(30.29, 18.35) * mm});
            skLineSegment(sketch, "E3366", {"start": v(30.29, 18.35) * mm, "end": v(30.17, 21.39) * mm});
            skLineSegment(sketch, "E3367", {"start": v(30.17, 21.39) * mm, "end": v(28.4, 21.39) * mm});
            skLineSegment(sketch, "E3368", {"start": v(28.4, 21.39) * mm, "end": v(27.98, 21) * mm});
            skLineSegment(sketch, "E3369", {"start": v(27.98, 21) * mm, "end": v(27.77, 20.82) * mm});
            skLineSegment(sketch, "E3370", {"start": v(27.77, 20.82) * mm, "end": v(27.51, 20.62) * mm});
            skLineSegment(sketch, "E3371", {"start": v(27.51, 20.62) * mm, "end": v(27.25, 20.4) * mm});
            skLineSegment(sketch, "E3372", {"start": v(27.25, 20.4) * mm, "end": v(27, 20.22) * mm});
            skLineSegment(sketch, "E3373", {"start": v(27, 20.22) * mm, "end": v(26.44, 19.83) * mm});
            skLineSegment(sketch, "E3374", {"start": v(26.44, 19.83) * mm, "end": v(25.58, 19.42) * mm});
            skLineSegment(sketch, "E3375", {"start": v(25.58, 19.42) * mm, "end": v(24.76, 19.05) * mm});
            skLineSegment(sketch, "E3376", {"start": v(24.76, 19.05) * mm, "end": v(23.93, 18.7) * mm});
            skLineSegment(sketch, "E3377", {"start": v(23.93, 18.7) * mm, "end": v(23.1, 18.38) * mm});
            skLineSegment(sketch, "E3378", {"start": v(23.1, 18.38) * mm, "end": v(22.25, 18.08) * mm});
            skLineSegment(sketch, "E3379", {"start": v(22.25, 18.08) * mm, "end": v(21.4, 17.82) * mm});
            skLineSegment(sketch, "E3380", {"start": v(21.4, 17.82) * mm, "end": v(20.56, 17.59) * mm});
            skLineSegment(sketch, "E3381", {"start": v(20.56, 17.59) * mm, "end": v(19.72, 17.38) * mm});
            skLineSegment(sketch, "E3382", {"start": v(19.72, 17.38) * mm, "end": v(18.87, 17.2) * mm});
            skLineSegment(sketch, "E3383", {"start": v(18.87, 17.2) * mm, "end": v(17.92, 17.03) * mm});
            skLineSegment(sketch, "E3384", {"start": v(17.92, 17.03) * mm, "end": v(14.26, 16.92) * mm});
            skLineSegment(sketch, "E3385", {"start": v(14.26, 16.92) * mm, "end": v(13.37, 17.03) * mm});
            skLineSegment(sketch, "E3386", {"start": v(13.37, 17.03) * mm, "end": v(12.74, 17.12) * mm});
            skLineSegment(sketch, "E3387", {"start": v(12.74, 17.12) * mm, "end": v(12.11, 17.23) * mm});
            skLineSegment(sketch, "E3388", {"start": v(12.11, 17.23) * mm, "end": v(11.5, 17.36) * mm});
            skLineSegment(sketch, "E3389", {"start": v(11.5, 17.36) * mm, "end": v(10.87, 17.5) * mm});
            skLineSegment(sketch, "E3390", {"start": v(10.87, 17.5) * mm, "end": v(10.25, 17.68) * mm});
            skLineSegment(sketch, "E3391", {"start": v(10.25, 17.68) * mm, "end": v(9.64, 17.86) * mm});
            skLineSegment(sketch, "E3392", {"start": v(9.64, 17.86) * mm, "end": v(9.03, 18.07) * mm});
            skLineSegment(sketch, "E3393", {"start": v(9.03, 18.07) * mm, "end": v(8.42, 18.3) * mm});
            skLineSegment(sketch, "E3394", {"start": v(8.42, 18.3) * mm, "end": v(7.82, 18.55) * mm});
            skLineSegment(sketch, "E3395", {"start": v(7.82, 18.55) * mm, "end": v(7.22, 18.82) * mm});
            skLineSegment(sketch, "E3396", {"start": v(7.22, 18.82) * mm, "end": v(6.62, 19.1) * mm});
            skLineSegment(sketch, "E3397", {"start": v(6.62, 19.1) * mm, "end": v(6.02, 19.42) * mm});
            skLineSegment(sketch, "E3398", {"start": v(6.02, 19.42) * mm, "end": v(5.43, 19.75) * mm});
            skLineSegment(sketch, "E3399", {"start": v(5.43, 19.75) * mm, "end": v(4.83, 20.1) * mm});
            skLineSegment(sketch, "E3400", {"start": v(4.83, 20.1) * mm, "end": v(4.24, 20.47) * mm});
            skLineSegment(sketch, "E3401", {"start": v(4.24, 20.47) * mm, "end": v(3.65, 20.86) * mm});
            skLineSegment(sketch, "E3402", {"start": v(3.65, 20.86) * mm, "end": v(2.89, 21.39) * mm});
            skLineSegment(sketch, "E3403", {"start": v(2.89, 21.39) * mm, "end": v(-2.9, 21.39) * mm});
            skLineSegment(sketch, "E3404", {"start": v(-2.9, 21.39) * mm, "end": v(-3.9, 20.72) * mm});
            skLineSegment(sketch, "E3405", {"start": v(-3.9, 20.72) * mm, "end": v(-4.64, 20.25) * mm});
            skLineSegment(sketch, "E3406", {"start": v(-4.64, 20.25) * mm, "end": v(-5.36, 19.81) * mm});
            skLineSegment(sketch, "E3407", {"start": v(-5.36, 19.81) * mm, "end": v(-6.07, 19.41) * mm});
            skLineSegment(sketch, "E3408", {"start": v(-6.07, 19.41) * mm, "end": v(-6.77, 19.05) * mm});
            skLineSegment(sketch, "E3409", {"start": v(-6.77, 19.05) * mm, "end": v(-7.48, 18.71) * mm});
            skLineSegment(sketch, "E3410", {"start": v(-7.48, 18.71) * mm, "end": v(-8.2, 18.4) * mm});
            skLineSegment(sketch, "E3411", {"start": v(-8.2, 18.4) * mm, "end": v(-8.93, 18.12) * mm});
            skLineSegment(sketch, "E3412", {"start": v(-8.93, 18.12) * mm, "end": v(-9.69, 17.85) * mm});
            skLineSegment(sketch, "E3413", {"start": v(-9.69, 17.85) * mm, "end": v(-10.74, 17.5) * mm});
            skLineSegment(sketch, "E3414", {"start": v(-10.74, 17.5) * mm, "end": v(-13.16, 17.01) * mm});
            skLineSegment(sketch, "E3415", {"start": v(-13.16, 17.01) * mm, "end": v(-16.69, 16.92) * mm});
            skLineSegment(sketch, "E3416", {"start": v(-16.69, 16.92) * mm, "end": v(-17.64, 17.03) * mm});
            skLineSegment(sketch, "E3417", {"start": v(-17.64, 17.03) * mm, "end": v(-18.12, 17.1) * mm});
            skLineSegment(sketch, "E3418", {"start": v(-18.12, 17.1) * mm, "end": v(-18.6, 17.17) * mm});
            skLineSegment(sketch, "E3419", {"start": v(-18.6, 17.17) * mm, "end": v(-19.1, 17.26) * mm});
            skLineSegment(sketch, "E3420", {"start": v(-19.1, 17.26) * mm, "end": v(-19.6, 17.36) * mm});
            skLineSegment(sketch, "E3421", {"start": v(-19.6, 17.36) * mm, "end": v(-20.11, 17.48) * mm});
            skLineSegment(sketch, "E3422", {"start": v(-20.11, 17.48) * mm, "end": v(-20.62, 17.6) * mm});
            skLineSegment(sketch, "E3423", {"start": v(-20.62, 17.6) * mm, "end": v(-21.14, 17.74) * mm});
            skLineSegment(sketch, "E3424", {"start": v(-21.14, 17.74) * mm, "end": v(-21.66, 17.9) * mm});
            skLineSegment(sketch, "E3425", {"start": v(-21.66, 17.9) * mm, "end": v(-22.18, 18.05) * mm});
            skLineSegment(sketch, "E3426", {"start": v(-22.18, 18.05) * mm, "end": v(-22.7, 18.23) * mm});
            skLineSegment(sketch, "E3427", {"start": v(-22.7, 18.23) * mm, "end": v(-23.21, 18.4) * mm});
            skLineSegment(sketch, "E3428", {"start": v(-23.21, 18.4) * mm, "end": v(-23.72, 18.6) * mm});
            skLineSegment(sketch, "E3429", {"start": v(-23.72, 18.6) * mm, "end": v(-24.23, 18.8) * mm});
            skLineSegment(sketch, "E3430", {"start": v(-24.23, 18.8) * mm, "end": v(-24.73, 19.01) * mm});
            skLineSegment(sketch, "E3431", {"start": v(-24.73, 19.01) * mm, "end": v(-25.21, 19.23) * mm});
            skLineSegment(sketch, "E3432", {"start": v(-25.21, 19.23) * mm, "end": v(-25.7, 19.46) * mm});
            skLineSegment(sketch, "E3433", {"start": v(-25.7, 19.46) * mm, "end": v(-26.54, 19.87) * mm});
            skLineSegment(sketch, "E3434", {"start": v(-26.54, 19.87) * mm, "end": v(-27.1, 20.28) * mm});
            skLineSegment(sketch, "E3435", {"start": v(-27.1, 20.28) * mm, "end": v(-27.35, 20.46) * mm});
            skLineSegment(sketch, "E3436", {"start": v(-27.35, 20.46) * mm, "end": v(-27.6, 20.66) * mm});
            skLineSegment(sketch, "E3437", {"start": v(-27.6, 20.66) * mm, "end": v(-27.83, 20.85) * mm});
            skLineSegment(sketch, "E3438", {"start": v(-27.83, 20.85) * mm, "end": v(-28, 21.01) * mm});
            skLineSegment(sketch, "E3439", {"start": v(-28, 21.01) * mm, "end": v(-28.35, 21.34) * mm});
            skLineSegment(sketch, "E3440", {"start": v(-28.35, 21.34) * mm, "end": v(-30.2, 21.34) * mm});
            skLineSegment(sketch, "E3441", {"start": v(-30.2, 21.34) * mm, "end": v(-30.32, 18.35) * mm});
            skLineSegment(sketch, "E3442", {"start": v(-30.32, 18.35) * mm, "end": v(-30.45, 11.2) * mm});
            skLineSegment(sketch, "E3443", {"start": v(-30.45, 11.2) * mm, "end": v(-30.24, 6.12) * mm});
            skLineSegment(sketch, "E3444", {"start": v(-30.24, 6.12) * mm, "end": v(-30.15, 4.9) * mm});
            skLineSegment(sketch, "E3445", {"start": v(-30.15, 4.9) * mm, "end": v(-30.05, 3.6) * mm});
            skLineSegment(sketch, "E3446", {"start": v(-30.05, 3.6) * mm, "end": v(-29.92, 2.22) * mm});
            skLineSegment(sketch, "E3447", {"start": v(-29.92, 2.22) * mm, "end": v(-29.65, -0.32) * mm});
            skLineSegment(sketch, "E3448", {"start": v(-29.65, -0.32) * mm, "end": v(-29.53, -1.24) * mm});
            skLineSegment(sketch, "E3449", {"start": v(-29.53, -1.24) * mm, "end": v(-29.4, -2.16) * mm});
            skLineSegment(sketch, "E3450", {"start": v(-29.4, -2.16) * mm, "end": v(-29.27, -3.08) * mm});
            skLineSegment(sketch, "E3451", {"start": v(-29.27, -3.08) * mm, "end": v(-29.13, -4) * mm});
            skLineSegment(sketch, "E3452", {"start": v(-29.13, -4) * mm, "end": v(-28.98, -4.9) * mm});
            skLineSegment(sketch, "E3453", {"start": v(-28.98, -4.9) * mm, "end": v(-28.82, -5.8) * mm});
            skLineSegment(sketch, "E3454", {"start": v(-28.82, -5.8) * mm, "end": v(-28.65, -6.7) * mm});
            skLineSegment(sketch, "E3455", {"start": v(-28.65, -6.7) * mm, "end": v(-28.47, -7.6) * mm});
            skLineSegment(sketch, "E3456", {"start": v(-28.47, -7.6) * mm, "end": v(-28.3, -8.48) * mm});
            skLineSegment(sketch, "E3457", {"start": v(-28.3, -8.48) * mm, "end": v(-28.1, -9.36) * mm});
            skLineSegment(sketch, "E3458", {"start": v(-28.1, -9.36) * mm, "end": v(-27.9, -10.23) * mm});
            skLineSegment(sketch, "E3459", {"start": v(-27.9, -10.23) * mm, "end": v(-27.7, -11.1) * mm});
            skLineSegment(sketch, "E3460", {"start": v(-27.7, -11.1) * mm, "end": v(-27.48, -11.96) * mm});
            skLineSegment(sketch, "E3461", {"start": v(-27.48, -11.96) * mm, "end": v(-27.26, -12.81) * mm});
            skLineSegment(sketch, "E3462", {"start": v(-27.26, -12.81) * mm, "end": v(-27.03, -13.66) * mm});
            skLineSegment(sketch, "E3463", {"start": v(-27.03, -13.66) * mm, "end": v(-26.8, -14.5) * mm});
            skLineSegment(sketch, "E3464", {"start": v(-26.8, -14.5) * mm, "end": v(-25.9, -17.4) * mm});
            skLineSegment(sketch, "E3465", {"start": v(-25.9, -17.4) * mm, "end": v(-25.44, -18.74) * mm});
            skLineSegment(sketch, "E3466", {"start": v(-25.44, -18.74) * mm, "end": v(-24.95, -20.07) * mm});
            skLineSegment(sketch, "E3467", {"start": v(-24.95, -20.07) * mm, "end": v(-24.44, -21.4) * mm});
            skLineSegment(sketch, "E3468", {"start": v(-24.44, -21.4) * mm, "end": v(-23.9, -22.7) * mm});
            skLineSegment(sketch, "E3469", {"start": v(-23.9, -22.7) * mm, "end": v(-22.88, -25.01) * mm});
            skLineSegment(sketch, "E3470", {"start": v(-22.88, -25.01) * mm, "end": v(-22.44, -25.95) * mm});
            skLineSegment(sketch, "E3471", {"start": v(-22.44, -25.95) * mm, "end": v(-22, -26.85) * mm});
            skLineSegment(sketch, "E3472", {"start": v(-22, -26.85) * mm, "end": v(-21.58, -27.7) * mm});
            skLineSegment(sketch, "E3473", {"start": v(-21.58, -27.7) * mm, "end": v(-21.15, -28.52) * mm});
            skLineSegment(sketch, "E3474", {"start": v(-21.15, -28.52) * mm, "end": v(-20.73, -29.31) * mm});
            skLineSegment(sketch, "E3475", {"start": v(-20.73, -29.31) * mm, "end": v(-20.3, -30.08) * mm});
            skLineSegment(sketch, "E3476", {"start": v(-20.3, -30.08) * mm, "end": v(-19.88, -30.84) * mm});
            skLineSegment(sketch, "E3477", {"start": v(-19.88, -30.84) * mm, "end": v(-19.44, -31.58) * mm});
            skLineSegment(sketch, "E3478", {"start": v(-19.44, -31.58) * mm, "end": v(-17.93, -33.98) * mm});
            skLineSegment(sketch, "E3479", {"start": v(-17.93, -33.98) * mm, "end": v(-17.39, -34.8) * mm});
            skLineSegment(sketch, "E3480", {"start": v(-17.39, -34.8) * mm, "end": v(-16.86, -35.57) * mm});
            skLineSegment(sketch, "E3481", {"start": v(-16.86, -35.57) * mm, "end": v(-16.34, -36.3) * mm});
            skLineSegment(sketch, "E3482", {"start": v(-16.34, -36.3) * mm, "end": v(-15.82, -37.02) * mm});
            skLineSegment(sketch, "E3483", {"start": v(-15.82, -37.02) * mm, "end": v(-15.3, -37.72) * mm});
            skLineSegment(sketch, "E3484", {"start": v(-15.3, -37.72) * mm, "end": v(-14.76, -38.42) * mm});
            skLineSegment(sketch, "E3485", {"start": v(-14.76, -38.42) * mm, "end": v(-14.19, -39.12) * mm});
            skLineSegment(sketch, "E3486", {"start": v(-14.19, -39.12) * mm, "end": v(-13.6, -39.85) * mm});
            skLineSegment(sketch, "E3487", {"start": v(-13.6, -39.85) * mm, "end": v(-12.74, -40.87) * mm});
            skLineSegment(sketch, "E3488", {"start": v(-12.74, -40.87) * mm, "end": v(-12.62, -40.87) * mm});
            skLineSegment(sketch, "E3489", {"start": v(-9.15, -40.06) * mm, "end": v(-9.02, -40.05) * mm});
            skLineSegment(sketch, "E3490", {"start": v(-9.02, -40.05) * mm, "end": v(-8.87, -40.03) * mm});
            skLineSegment(sketch, "E3491", {"start": v(-8.87, -40.03) * mm, "end": v(-8.57, -39.96) * mm});
            skLineSegment(sketch, "E3492", {"start": v(-8.57, -39.96) * mm, "end": v(-8.43, -39.92) * mm});
            skLineSegment(sketch, "E3493", {"start": v(-8.43, -39.92) * mm, "end": v(-8.32, -39.87) * mm});
            skLineSegment(sketch, "E3494", {"start": v(-8.32, -39.87) * mm, "end": v(-8.23, -39.83) * mm});
            skLineSegment(sketch, "E3495", {"start": v(-8.23, -39.83) * mm, "end": v(-8.18, -39.8) * mm});
            skLineSegment(sketch, "E3496", {"start": v(-8.18, -39.8) * mm, "end": v(-8.14, -39.71) * mm});
            skLineSegment(sketch, "E3497", {"start": v(-8.14, -39.71) * mm, "end": v(-9.02, -38.73) * mm});
            skLineSegment(sketch, "E3498", {"start": v(-9.02, -38.73) * mm, "end": v(-9.43, -38.26) * mm});
            skLineSegment(sketch, "E3499", {"start": v(-9.43, -38.26) * mm, "end": v(-9.89, -37.73) * mm});
            skLineSegment(sketch, "E3500", {"start": v(-9.89, -37.73) * mm, "end": v(-10.33, -37.2) * mm});
            skLineSegment(sketch, "E3501", {"start": v(-10.33, -37.2) * mm, "end": v(-10.72, -36.73) * mm});
            skLineSegment(sketch, "E3502", {"start": v(-10.72, -36.73) * mm, "end": v(-11.94, -35.2) * mm});
            skLineSegment(sketch, "E3503", {"start": v(-11.94, -35.2) * mm, "end": v(-12.44, -34.53) * mm});
            skLineSegment(sketch, "E3504", {"start": v(-12.44, -34.53) * mm, "end": v(-12.94, -33.85) * mm});
            skLineSegment(sketch, "E3505", {"start": v(-12.94, -33.85) * mm, "end": v(-13.43, -33.16) * mm});
            skLineSegment(sketch, "E3506", {"start": v(-13.43, -33.16) * mm, "end": v(-13.9, -32.46) * mm});
            skLineSegment(sketch, "E3507", {"start": v(-13.9, -32.46) * mm, "end": v(-14.39, -31.74) * mm});
            skLineSegment(sketch, "E3508", {"start": v(-14.39, -31.74) * mm, "end": v(-14.85, -31.01) * mm});
            skLineSegment(sketch, "E3509", {"start": v(-14.85, -31.01) * mm, "end": v(-15.31, -30.28) * mm});
            skLineSegment(sketch, "E3510", {"start": v(-15.31, -30.28) * mm, "end": v(-15.77, -29.53) * mm});
            skLineSegment(sketch, "E3511", {"start": v(-15.77, -29.53) * mm, "end": v(-16.21, -28.77) * mm});
            skLineSegment(sketch, "E3512", {"start": v(-16.21, -28.77) * mm, "end": v(-16.65, -28) * mm});
            skLineSegment(sketch, "E3513", {"start": v(-16.65, -28) * mm, "end": v(-17.07, -27.22) * mm});
            skLineSegment(sketch, "E3514", {"start": v(-17.07, -27.22) * mm, "end": v(-17.5, -26.43) * mm});
            skLineSegment(sketch, "E3515", {"start": v(-17.5, -26.43) * mm, "end": v(-17.9, -25.64) * mm});
            skLineSegment(sketch, "E3516", {"start": v(-17.9, -25.64) * mm, "end": v(-18.3, -24.83) * mm});
            skLineSegment(sketch, "E3517", {"start": v(-18.3, -24.83) * mm, "end": v(-18.7, -24.02) * mm});
            skLineSegment(sketch, "E3518", {"start": v(-18.7, -24.02) * mm, "end": v(-19.09, -23.2) * mm});
            skLineSegment(sketch, "E3519", {"start": v(-19.09, -23.2) * mm, "end": v(-19.9, -21.42) * mm});
            skLineSegment(sketch, "E3520", {"start": v(-19.9, -21.42) * mm, "end": v(-21.26, -17.99) * mm});
            skLineSegment(sketch, "E3521", {"start": v(-21.26, -17.99) * mm, "end": v(-21.77, -16.5) * mm});
            skLineSegment(sketch, "E3522", {"start": v(-21.77, -16.5) * mm, "end": v(-22.05, -15.65) * mm});
            skLineSegment(sketch, "E3523", {"start": v(-22.05, -15.65) * mm, "end": v(-22.33, -14.78) * mm});
            skLineSegment(sketch, "E3524", {"start": v(-22.33, -14.78) * mm, "end": v(-22.6, -13.9) * mm});
            skLineSegment(sketch, "E3525", {"start": v(-22.6, -13.9) * mm, "end": v(-22.86, -13) * mm});
            skLineSegment(sketch, "E3526", {"start": v(-22.86, -13) * mm, "end": v(-23.1, -12.1) * mm});
            skLineSegment(sketch, "E3527", {"start": v(-23.1, -12.1) * mm, "end": v(-23.35, -11.18) * mm});
            skLineSegment(sketch, "E3528", {"start": v(-23.35, -11.18) * mm, "end": v(-23.58, -10.25) * mm});
            skLineSegment(sketch, "E3529", {"start": v(-23.58, -10.25) * mm, "end": v(-23.8, -9.31) * mm});
            skLineSegment(sketch, "E3530", {"start": v(-23.8, -9.31) * mm, "end": v(-24.03, -8.37) * mm});
            skLineSegment(sketch, "E3531", {"start": v(-24.03, -8.37) * mm, "end": v(-24.23, -7.41) * mm});
            skLineSegment(sketch, "E3532", {"start": v(-24.23, -7.41) * mm, "end": v(-24.43, -6.45) * mm});
            skLineSegment(sketch, "E3533", {"start": v(-24.43, -6.45) * mm, "end": v(-24.61, -5.48) * mm});
            skLineSegment(sketch, "E3534", {"start": v(-24.61, -5.48) * mm, "end": v(-24.8, -4.51) * mm});
            skLineSegment(sketch, "E3535", {"start": v(-24.8, -4.51) * mm, "end": v(-24.96, -3.54) * mm});
            skLineSegment(sketch, "E3536", {"start": v(-24.96, -3.54) * mm, "end": v(-25.11, -2.56) * mm});
            skLineSegment(sketch, "E3537", {"start": v(-25.11, -2.56) * mm, "end": v(-25.25, -1.59) * mm});
            skLineSegment(sketch, "E3538", {"start": v(-25.25, -1.59) * mm, "end": v(-25.58, 0.95) * mm});
            skLineSegment(sketch, "E3539", {"start": v(-25.58, 0.95) * mm, "end": v(-25.64, 1.45) * mm});
            skLineSegment(sketch, "E3540", {"start": v(-25.64, 1.45) * mm, "end": v(-25.66, 1.63) * mm});
            skLineSegment(sketch, "E3541", {"start": v(-25.66, 1.63) * mm, "end": v(-25.68, 1.74) * mm});
            skLineSegment(sketch, "E3542", {"start": v(-25.68, 1.74) * mm, "end": v(-25.73, 1.9) * mm});
            skLineSegment(sketch, "E3543", {"start": v(-25.73, 1.9) * mm, "end": v(25.67, 1.9) * mm});
            skLineSegment(sketch, "E3544", {"start": v(25.67, 1.9) * mm, "end": v(25.67, 1.85) * mm});
            skLineSegment(sketch, "E3545", {"start": v(25.67, 1.85) * mm, "end": v(25.21, -1.77) * mm});
            skLineSegment(sketch, "E3546", {"start": v(25.21, -1.77) * mm, "end": v(24.67, -5.03) * mm});
            skLineSegment(sketch, "E3547", {"start": v(24.67, -5.03) * mm, "end": v(24.53, -5.8) * mm});
            skLineSegment(sketch, "E3548", {"start": v(24.53, -5.8) * mm, "end": v(24.3, -7.02) * mm});
            skLineSegment(sketch, "E3549", {"start": v(24.3, -7.02) * mm, "end": v(24.04, -8.25) * mm});
            skLineSegment(sketch, "E3550", {"start": v(24.04, -8.25) * mm, "end": v(23.76, -9.48) * mm});
            skLineSegment(sketch, "E3551", {"start": v(23.76, -9.48) * mm, "end": v(23.45, -10.72) * mm});
            skLineSegment(sketch, "E3552", {"start": v(23.45, -10.72) * mm, "end": v(23.12, -11.97) * mm});
            skLineSegment(sketch, "E3553", {"start": v(23.12, -11.97) * mm, "end": v(22.77, -13.2) * mm});
            skLineSegment(sketch, "E3554", {"start": v(22.77, -13.2) * mm, "end": v(22.4, -14.45) * mm});
            skLineSegment(sketch, "E3555", {"start": v(22.4, -14.45) * mm, "end": v(22, -15.68) * mm});
            skLineSegment(sketch, "E3556", {"start": v(22, -15.68) * mm, "end": v(21.58, -16.9) * mm});
            skLineSegment(sketch, "E3557", {"start": v(21.58, -16.9) * mm, "end": v(21.14, -18.13) * mm});
            skLineSegment(sketch, "E3558", {"start": v(21.14, -18.13) * mm, "end": v(20.68, -19.34) * mm});
            skLineSegment(sketch, "E3559", {"start": v(20.68, -19.34) * mm, "end": v(20.2, -20.54) * mm});
            skLineSegment(sketch, "E3560", {"start": v(20.2, -20.54) * mm, "end": v(19.71, -21.72) * mm});
            skLineSegment(sketch, "E3561", {"start": v(19.71, -21.72) * mm, "end": v(19.2, -22.88) * mm});
            skLineSegment(sketch, "E3562", {"start": v(19.2, -22.88) * mm, "end": v(18.67, -24.03) * mm});
            skLineSegment(sketch, "E3563", {"start": v(18.67, -24.03) * mm, "end": v(18.13, -25.15) * mm});
            skLineSegment(sketch, "E3564", {"start": v(18.13, -25.15) * mm, "end": v(17.1, -27.14) * mm});
            skLineSegment(sketch, "E3565", {"start": v(17.1, -27.14) * mm, "end": v(16.67, -27.9) * mm});
            skLineSegment(sketch, "E3566", {"start": v(16.67, -27.9) * mm, "end": v(16.12, -28.86) * mm});
            skLineSegment(sketch, "E3567", {"start": v(16.12, -28.86) * mm, "end": v(15.17, -30.45) * mm});
            skLineSegment(sketch, "E3568", {"start": v(15.17, -30.45) * mm, "end": v(14.38, -31.67) * mm});
            skLineSegment(sketch, "E3569", {"start": v(14.38, -31.67) * mm, "end": v(13.6, -32.84) * mm});
            skLineSegment(sketch, "E3570", {"start": v(13.6, -32.84) * mm, "end": v(12.86, -33.9) * mm});
            skLineSegment(sketch, "E3571", {"start": v(12.86, -33.9) * mm, "end": v(12.2, -34.82) * mm});
            skLineSegment(sketch, "E3572", {"start": v(12.2, -34.82) * mm, "end": v(10.51, -36.96) * mm});
            skLineSegment(sketch, "E3573", {"start": v(10.51, -36.96) * mm, "end": v(9.74, -37.87) * mm});
            skLineSegment(sketch, "E3574", {"start": v(9.74, -37.87) * mm, "end": v(8.92, -38.82) * mm});
            skLineSegment(sketch, "E3575", {"start": v(8.92, -38.82) * mm, "end": v(8.08, -39.78) * mm});
            skLineSegment(sketch, "E3576", {"start": v(8.08, -39.78) * mm, "end": v(8.27, -39.88) * mm});
            skLineSegment(sketch, "E3577", {"start": v(8.27, -39.88) * mm, "end": v(8.38, -39.92) * mm});
            skLineSegment(sketch, "E3578", {"start": v(8.38, -39.92) * mm, "end": v(8.53, -39.96) * mm});
            skLineSegment(sketch, "E3579", {"start": v(8.53, -39.96) * mm, "end": v(8.7, -40) * mm});
            skLineSegment(sketch, "E3580", {"start": v(8.7, -40) * mm, "end": v(8.9, -40.03) * mm});
            skLineSegment(sketch, "E3581", {"start": v(8.9, -40.03) * mm, "end": v(9.33, -40.08) * mm});
            skLineSegment(sketch, "E3582", {"start": v(9.33, -40.08) * mm, "end": v(10.25, -39.02) * mm});
            skLineSegment(sketch, "E3583", {"start": v(10.25, -39.02) * mm, "end": v(10.98, -38.16) * mm});
            skLineSegment(sketch, "E3584", {"start": v(10.98, -38.16) * mm, "end": v(11.73, -37.24) * mm});
            skLineSegment(sketch, "E3585", {"start": v(11.73, -37.24) * mm, "end": v(12.47, -36.3) * mm});
            skLineSegment(sketch, "E3586", {"start": v(12.47, -36.3) * mm, "end": v(13.21, -35.32) * mm});
            skLineSegment(sketch, "E3587", {"start": v(13.21, -35.32) * mm, "end": v(13.93, -34.34) * mm});
            skLineSegment(sketch, "E3588", {"start": v(13.93, -34.34) * mm, "end": v(14.62, -33.36) * mm});
            skLineSegment(sketch, "E3589", {"start": v(14.62, -33.36) * mm, "end": v(15.27, -32.4) * mm});
            skLineSegment(sketch, "E3590", {"start": v(15.27, -32.4) * mm, "end": v(15.87, -31.47) * mm});
            skLineSegment(sketch, "E3591", {"start": v(15.87, -31.47) * mm, "end": v(17.34, -29.05) * mm});
            skLineSegment(sketch, "E3592", {"start": v(17.34, -29.05) * mm, "end": v(17.68, -28.44) * mm});
            skLineSegment(sketch, "E3593", {"start": v(17.68, -28.44) * mm, "end": v(18.13, -27.59) * mm});
            skLineSegment(sketch, "E3594", {"start": v(18.13, -27.59) * mm, "end": v(18.64, -26.6) * mm});
            skLineSegment(sketch, "E3595", {"start": v(18.64, -26.6) * mm, "end": v(19.14, -25.6) * mm});
            skLineSegment(sketch, "E3596", {"start": v(19.14, -25.6) * mm, "end": v(20.31, -23.25) * mm});
            skLineSegment(sketch, "E3597", {"start": v(20.31, -23.25) * mm, "end": v(20.87, -21.93) * mm});
            skLineSegment(sketch, "E3598", {"start": v(20.87, -21.93) * mm, "end": v(21.28, -20.93) * mm});
            skLineSegment(sketch, "E3599", {"start": v(21.28, -20.93) * mm, "end": v(21.68, -19.95) * mm});
            skLineSegment(sketch, "E3600", {"start": v(21.68, -19.95) * mm, "end": v(22.05, -18.96) * mm});
            skLineSegment(sketch, "E3601", {"start": v(22.05, -18.96) * mm, "end": v(22.41, -17.97) * mm});
            skLineSegment(sketch, "E3602", {"start": v(22.41, -17.97) * mm, "end": v(22.76, -16.96) * mm});
            skLineSegment(sketch, "E3603", {"start": v(22.76, -16.96) * mm, "end": v(23.1, -15.94) * mm});
            skLineSegment(sketch, "E3604", {"start": v(23.1, -15.94) * mm, "end": v(23.43, -14.9) * mm});
            skLineSegment(sketch, "E3605", {"start": v(23.43, -14.9) * mm, "end": v(23.75, -13.82) * mm});
            skLineSegment(sketch, "E3606", {"start": v(23.75, -13.82) * mm, "end": v(24.49, -11.2) * mm});
            skLineSegment(sketch, "E3607", {"start": v(24.49, -11.2) * mm, "end": v(24.78, -10.02) * mm});
            skLineSegment(sketch, "E3608", {"start": v(24.78, -10.02) * mm, "end": v(25.07, -8.75) * mm});
            skLineSegment(sketch, "E3609", {"start": v(25.07, -8.75) * mm, "end": v(25.57, -6.43) * mm});
            skLineSegment(sketch, "E3610", {"start": v(25.57, -6.43) * mm, "end": v(25.73, -5.6) * mm});
            skLineSegment(sketch, "E3611", {"start": v(25.73, -5.6) * mm, "end": v(25.88, -4.76) * mm});
            skLineSegment(sketch, "E3612", {"start": v(25.88, -4.76) * mm, "end": v(26.02, -3.92) * mm});
            skLineSegment(sketch, "E3613", {"start": v(26.02, -3.92) * mm, "end": v(26.16, -3.08) * mm});
            skLineSegment(sketch, "E3614", {"start": v(26.16, -3.08) * mm, "end": v(26.29, -2.23) * mm});
            skLineSegment(sketch, "E3615", {"start": v(26.29, -2.23) * mm, "end": v(26.4, -1.38) * mm});
            skLineSegment(sketch, "E3616", {"start": v(26.4, -1.38) * mm, "end": v(26.52, -0.52) * mm});
            skLineSegment(sketch, "E3617", {"start": v(26.52, -0.52) * mm, "end": v(26.63, 0.34) * mm});
            skLineSegment(sketch, "E3618", {"start": v(26.63, 0.34) * mm, "end": v(26.73, 1.21) * mm});
            skLineSegment(sketch, "E3619", {"start": v(26.73, 1.21) * mm, "end": v(26.82, 2.09) * mm});
            skLineSegment(sketch, "E3620", {"start": v(26.82, 2.09) * mm, "end": v(26.9, 2.98) * mm});
            skLineSegment(sketch, "E3621", {"start": v(26.9, 2.98) * mm, "end": v(26.97, 3.87) * mm});
            skLineSegment(sketch, "E3622", {"start": v(26.97, 3.87) * mm, "end": v(27.04, 4.78) * mm});
            skLineSegment(sketch, "E3623", {"start": v(27.04, 4.78) * mm, "end": v(27.1, 5.7) * mm});
            skLineSegment(sketch, "E3624", {"start": v(27.1, 5.7) * mm, "end": v(27.2, 7.57) * mm});
            skLineSegment(sketch, "E3625", {"start": v(27.2, 7.57) * mm, "end": v(27.3, 9.47) * mm});
            skLineSegment(sketch, "E3626", {"start": v(27.3, 9.47) * mm, "end": v(27.3, 16.45) * mm});
            skLineSegment(sketch, "E3627", {"start": v(27.3, 16.45) * mm, "end": v(27.13, 16.72) * mm});
            skLineSegment(sketch, "E3628", {"start": v(27.13, 16.72) * mm, "end": v(26.65, 16.5) * mm});
            skLineSegment(sketch, "E3629", {"start": v(26.65, 16.5) * mm, "end": v(25.65, 16.07) * mm});
            skLineSegment(sketch, "E3630", {"start": v(25.65, 16.07) * mm, "end": v(24.7, 15.68) * mm});
            skLineSegment(sketch, "E3631", {"start": v(24.7, 15.68) * mm, "end": v(24.22, 15.5) * mm});
            skLineSegment(sketch, "E3632", {"start": v(24.22, 15.5) * mm, "end": v(23.76, 15.34) * mm});
            skLineSegment(sketch, "E3633", {"start": v(23.76, 15.34) * mm, "end": v(23.3, 15.19) * mm});
            skLineSegment(sketch, "E3634", {"start": v(23.3, 15.19) * mm, "end": v(22.85, 15.04) * mm});
            skLineSegment(sketch, "E3635", {"start": v(22.85, 15.04) * mm, "end": v(22.4, 14.9) * mm});
            skLineSegment(sketch, "E3636", {"start": v(22.4, 14.9) * mm, "end": v(21.94, 14.78) * mm});
            skLineSegment(sketch, "E3637", {"start": v(21.94, 14.78) * mm, "end": v(21.47, 14.65) * mm});
            skLineSegment(sketch, "E3638", {"start": v(21.47, 14.65) * mm, "end": v(21, 14.54) * mm});
            skLineSegment(sketch, "E3639", {"start": v(21, 14.54) * mm, "end": v(20.03, 14.32) * mm});
            skLineSegment(sketch, "E3640", {"start": v(20.03, 14.32) * mm, "end": v(19, 14.13) * mm});
            skLineSegment(sketch, "E3641", {"start": v(19, 14.13) * mm, "end": v(18.01, 13.95) * mm});
            skLineSegment(sketch, "E3642", {"start": v(18.01, 13.95) * mm, "end": v(14.38, 13.84) * mm});
            skLineSegment(sketch, "E3643", {"start": v(14.38, 13.84) * mm, "end": v(13.34, 13.95) * mm});
            skLineSegment(sketch, "E3644", {"start": v(13.34, 13.95) * mm, "end": v(12.82, 14) * mm});
            skLineSegment(sketch, "E3645", {"start": v(12.82, 14) * mm, "end": v(12.3, 14.08) * mm});
            skLineSegment(sketch, "E3646", {"start": v(12.3, 14.08) * mm, "end": v(11.78, 14.17) * mm});
            skLineSegment(sketch, "E3647", {"start": v(11.78, 14.17) * mm, "end": v(11.26, 14.26) * mm});
            skLineSegment(sketch, "E3648", {"start": v(11.26, 14.26) * mm, "end": v(10.74, 14.37) * mm});
            skLineSegment(sketch, "E3649", {"start": v(10.74, 14.37) * mm, "end": v(10.23, 14.5) * mm});
            skLineSegment(sketch, "E3650", {"start": v(10.23, 14.5) * mm, "end": v(9.71, 14.63) * mm});
            skLineSegment(sketch, "E3651", {"start": v(9.71, 14.63) * mm, "end": v(9.2, 14.77) * mm});
            skLineSegment(sketch, "E3652", {"start": v(9.2, 14.77) * mm, "end": v(8.7, 14.93) * mm});
            skLineSegment(sketch, "E3653", {"start": v(8.7, 14.93) * mm, "end": v(8.2, 15.1) * mm});
            skLineSegment(sketch, "E3654", {"start": v(8.2, 15.1) * mm, "end": v(7.7, 15.27) * mm});
            skLineSegment(sketch, "E3655", {"start": v(7.7, 15.27) * mm, "end": v(7.21, 15.46) * mm});
            skLineSegment(sketch, "E3656", {"start": v(7.21, 15.46) * mm, "end": v(6.72, 15.66) * mm});
            skLineSegment(sketch, "E3657", {"start": v(6.72, 15.66) * mm, "end": v(6.24, 15.87) * mm});
            skLineSegment(sketch, "E3658", {"start": v(6.24, 15.87) * mm, "end": v(5.77, 16.1) * mm});
            skLineSegment(sketch, "E3659", {"start": v(5.77, 16.1) * mm, "end": v(5.3, 16.33) * mm});
            skLineSegment(sketch, "E3660", {"start": v(5.3, 16.33) * mm, "end": v(4.68, 16.66) * mm});
            skLineSegment(sketch, "E3661", {"start": v(4.68, 16.66) * mm, "end": v(4.04, 17.02) * mm});
            skLineSegment(sketch, "E3662", {"start": v(4.04, 17.02) * mm, "end": v(3.39, 17.4) * mm});
            skLineSegment(sketch, "E3663", {"start": v(3.39, 17.4) * mm, "end": v(2.74, 17.8) * mm});
            skLineSegment(sketch, "E3664", {"start": v(2.74, 17.8) * mm, "end": v(2.12, 18.2) * mm});
            skLineSegment(sketch, "E3665", {"start": v(2.12, 18.2) * mm, "end": v(1.54, 18.59) * mm});
            skLineSegment(sketch, "E3666", {"start": v(1.54, 18.59) * mm, "end": v(1, 18.97) * mm});
            skLineSegment(sketch, "E3667", {"start": v(1, 18.97) * mm, "end": v(0.54, 19.32) * mm});
            skLineSegment(sketch, "E3668", {"start": v(0.54, 19.32) * mm, "end": v(0.36, 19.45) * mm});
            skLineSegment(sketch, "E3669", {"start": v(0.36, 19.45) * mm, "end": v(0.2, 19.56) * mm});
            skLineSegment(sketch, "E3670", {"start": v(0.2, 19.56) * mm, "end": v(0.07, 19.64) * mm});
            skLineSegment(sketch, "E3671", {"start": v(0.07, 19.64) * mm, "end": v(0, 19.67) * mm});
            skLineSegment(sketch, "E3672", {"start": v(0, 19.67) * mm, "end": v(-0.03, 19.65) * mm});
            skLineSegment(sketch, "E3673", {"start": v(-0.03, 19.65) * mm, "end": v(-0.1, 19.62) * mm});
            skLineSegment(sketch, "E3674", {"start": v(-0.1, 19.62) * mm, "end": v(-0.3, 19.5) * mm});
            skLineSegment(sketch, "E3675", {"start": v(-0.3, 19.5) * mm, "end": v(-0.56, 19.31) * mm});
            skLineSegment(sketch, "E3676", {"start": v(-0.56, 19.31) * mm, "end": v(-0.87, 19.09) * mm});
            skLineSegment(sketch, "E3677", {"start": v(-0.87, 19.09) * mm, "end": v(-1.51, 18.63) * mm});
            skLineSegment(sketch, "E3678", {"start": v(-1.51, 18.63) * mm, "end": v(-2.17, 18.18) * mm});
            skLineSegment(sketch, "E3679", {"start": v(-2.17, 18.18) * mm, "end": v(-2.84, 17.74) * mm});
            skLineSegment(sketch, "E3680", {"start": v(-2.84, 17.74) * mm, "end": v(-3.52, 17.33) * mm});
            skLineSegment(sketch, "E3681", {"start": v(-3.52, 17.33) * mm, "end": v(-4.2, 16.93) * mm});
            skLineSegment(sketch, "E3682", {"start": v(-4.2, 16.93) * mm, "end": v(-4.88, 16.56) * mm});
            skLineSegment(sketch, "E3683", {"start": v(-4.88, 16.56) * mm, "end": v(-5.56, 16.22) * mm});
            skLineSegment(sketch, "E3684", {"start": v(-5.56, 16.22) * mm, "end": v(-6.23, 15.9) * mm});
            skLineSegment(sketch, "E3685", {"start": v(-6.23, 15.9) * mm, "end": v(-7.36, 15.39) * mm});
            skLineSegment(sketch, "E3686", {"start": v(-7.36, 15.39) * mm, "end": v(-8.13, 15.12) * mm});
            skLineSegment(sketch, "E3687", {"start": v(-8.13, 15.12) * mm, "end": v(-8.78, 14.9) * mm});
            skLineSegment(sketch, "E3688", {"start": v(-8.78, 14.9) * mm, "end": v(-9.41, 14.72) * mm});
            skLineSegment(sketch, "E3689", {"start": v(-9.41, 14.72) * mm, "end": v(-10.04, 14.55) * mm});
            skLineSegment(sketch, "E3690", {"start": v(-10.04, 14.55) * mm, "end": v(-10.68, 14.4) * mm});
            skLineSegment(sketch, "E3691", {"start": v(-10.68, 14.4) * mm, "end": v(-11.32, 14.26) * mm});
            skLineSegment(sketch, "E3692", {"start": v(-11.32, 14.26) * mm, "end": v(-11.97, 14.14) * mm});
            skLineSegment(sketch, "E3693", {"start": v(-11.97, 14.14) * mm, "end": v(-12.63, 14.04) * mm});
            skLineSegment(sketch, "E3694", {"start": v(-12.63, 14.04) * mm, "end": v(-13.32, 13.95) * mm});
            skLineSegment(sketch, "E3695", {"start": v(-13.32, 13.95) * mm, "end": v(-14.3, 13.84) * mm});
            skLineSegment(sketch, "E3696", {"start": v(-14.3, 13.84) * mm, "end": v(-17.88, 13.95) * mm});
            skLineSegment(sketch, "E3697", {"start": v(-17.88, 13.95) * mm, "end": v(-18.78, 14.09) * mm});
            skLineSegment(sketch, "E3698", {"start": v(-18.78, 14.09) * mm, "end": v(-19.25, 14.16) * mm});
            skLineSegment(sketch, "E3699", {"start": v(-19.25, 14.16) * mm, "end": v(-19.73, 14.25) * mm});
            skLineSegment(sketch, "E3700", {"start": v(-19.73, 14.25) * mm, "end": v(-20.2, 14.34) * mm});
            skLineSegment(sketch, "E3701", {"start": v(-20.2, 14.34) * mm, "end": v(-20.67, 14.45) * mm});
            skLineSegment(sketch, "E3702", {"start": v(-20.67, 14.45) * mm, "end": v(-21.15, 14.56) * mm});
            skLineSegment(sketch, "E3703", {"start": v(-21.15, 14.56) * mm, "end": v(-21.62, 14.68) * mm});
            skLineSegment(sketch, "E3704", {"start": v(-21.62, 14.68) * mm, "end": v(-22.1, 14.8) * mm});
            skLineSegment(sketch, "E3705", {"start": v(-22.1, 14.8) * mm, "end": v(-22.57, 14.94) * mm});
            skLineSegment(sketch, "E3706", {"start": v(-22.57, 14.94) * mm, "end": v(-23.04, 15.09) * mm});
            skLineSegment(sketch, "E3707", {"start": v(-23.04, 15.09) * mm, "end": v(-23.5, 15.24) * mm});
            skLineSegment(sketch, "E3708", {"start": v(-23.5, 15.24) * mm, "end": v(-23.97, 15.4) * mm});
            skLineSegment(sketch, "E3709", {"start": v(-23.97, 15.4) * mm, "end": v(-24.43, 15.57) * mm});
            skLineSegment(sketch, "E3710", {"start": v(-24.43, 15.57) * mm, "end": v(-24.9, 15.74) * mm});
            skLineSegment(sketch, "E3711", {"start": v(-24.9, 15.74) * mm, "end": v(-25.35, 15.93) * mm});
            skLineSegment(sketch, "E3712", {"start": v(-25.35, 15.93) * mm, "end": v(-25.8, 16.11) * mm});
            skLineSegment(sketch, "E3713", {"start": v(-25.8, 16.11) * mm, "end": v(-26.25, 16.31) * mm});
            skLineSegment(sketch, "E3714", {"start": v(-26.25, 16.31) * mm, "end": v(-27.1, 16.7) * mm});
            skLineSegment(sketch, "E3715", {"start": v(-27.1, 16.7) * mm, "end": v(-27.3, 16.48) * mm});
            skLineSegment(sketch, "E3716", {"start": v(-27.3, 16.48) * mm, "end": v(-27.37, 10.83) * mm});
            skLineSegment(sketch, "E3717", {"start": v(-27.37, 10.83) * mm, "end": v(-27.16, 5.85) * mm});
            skLineSegment(sketch, "E3718", {"start": v(-27.16, 5.85) * mm, "end": v(-26.9, 2.4) * mm});
            skLineSegment(sketch, "E3719", {"start": v(-26.9, 2.4) * mm, "end": v(-26.75, 1.18) * mm});
            skLineSegment(sketch, "E3720", {"start": v(-26.75, 1.18) * mm, "end": v(-26.56, -0.38) * mm});
            skLineSegment(sketch, "E3721", {"start": v(-26.56, -0.38) * mm, "end": v(-26.37, -1.86) * mm});
            skLineSegment(sketch, "E3722", {"start": v(-26.37, -1.86) * mm, "end": v(-26.15, -3.29) * mm});
            skLineSegment(sketch, "E3723", {"start": v(-26.15, -3.29) * mm, "end": v(-25.93, -4.67) * mm});
            skLineSegment(sketch, "E3724", {"start": v(-25.93, -4.67) * mm, "end": v(-25.68, -6.02) * mm});
            skLineSegment(sketch, "E3725", {"start": v(-25.68, -6.02) * mm, "end": v(-25.41, -7.36) * mm});
            skLineSegment(sketch, "E3726", {"start": v(-25.41, -7.36) * mm, "end": v(-25.12, -8.7) * mm});
            skLineSegment(sketch, "E3727", {"start": v(-25.12, -8.7) * mm, "end": v(-24.8, -10.06) * mm});
            skLineSegment(sketch, "E3728", {"start": v(-24.8, -10.06) * mm, "end": v(-24.35, -11.91) * mm});
            skLineSegment(sketch, "E3729", {"start": v(-24.35, -11.91) * mm, "end": v(-23.94, -13.32) * mm});
            skLineSegment(sketch, "E3730", {"start": v(-23.94, -13.32) * mm, "end": v(-23.73, -14.03) * mm});
            skLineSegment(sketch, "E3731", {"start": v(-23.73, -14.03) * mm, "end": v(-23.45, -14.91) * mm});
            skLineSegment(sketch, "E3732", {"start": v(-23.45, -14.91) * mm, "end": v(-22.85, -16.77) * mm});
            skLineSegment(sketch, "E3733", {"start": v(-22.85, -16.77) * mm, "end": v(-22.17, -18.8) * mm});
            skLineSegment(sketch, "E3734", {"start": v(-22.17, -18.8) * mm, "end": v(-21.57, -20.3) * mm});
            skLineSegment(sketch, "E3735", {"start": v(-21.57, -20.3) * mm, "end": v(-21.28, -21) * mm});
            skLineSegment(sketch, "E3736", {"start": v(-21.28, -21) * mm, "end": v(-20.94, -21.82) * mm});
            skLineSegment(sketch, "E3737", {"start": v(-20.94, -21.82) * mm, "end": v(-20.58, -22.65) * mm});
            skLineSegment(sketch, "E3738", {"start": v(-20.58, -22.65) * mm, "end": v(-20.26, -23.38) * mm});
            skLineSegment(sketch, "E3739", {"start": v(-20.26, -23.38) * mm, "end": v(-19.54, -24.97) * mm});
            skLineSegment(sketch, "E3740", {"start": v(-19.54, -24.97) * mm, "end": v(-18.11, -27.71) * mm});
            skLineSegment(sketch, "E3741", {"start": v(-18.11, -27.71) * mm, "end": v(-16.9, -29.86) * mm});
            skLineSegment(sketch, "E3742", {"start": v(-16.9, -29.86) * mm, "end": v(-16.49, -30.54) * mm});
            skLineSegment(sketch, "E3743", {"start": v(-16.49, -30.54) * mm, "end": v(-15.81, -31.62) * mm});
            skLineSegment(sketch, "E3744", {"start": v(-15.81, -31.62) * mm, "end": v(-15.12, -32.7) * mm});
            skLineSegment(sketch, "E3745", {"start": v(-15.12, -32.7) * mm, "end": v(-14.39, -33.76) * mm});
            skLineSegment(sketch, "E3746", {"start": v(-14.39, -33.76) * mm, "end": v(-13.62, -34.83) * mm});
            skLineSegment(sketch, "E3747", {"start": v(-13.62, -34.83) * mm, "end": v(-12.83, -35.9) * mm});
            skLineSegment(sketch, "E3748", {"start": v(-12.83, -35.9) * mm, "end": v(-12, -36.96) * mm});
            skLineSegment(sketch, "E3749", {"start": v(-12, -36.96) * mm, "end": v(-11.11, -38.04) * mm});
            skLineSegment(sketch, "E3750", {"start": v(-11.11, -38.04) * mm, "end": v(-10.19, -39.13) * mm});
            skLineSegment(sketch, "E3751", {"start": v(-10.19, -39.13) * mm, "end": v(-9.39, -40.06) * mm});
            skLineSegment(sketch, "E3752", {"start": v(-9.39, -40.06) * mm, "end": v(-9.15, -40.06) * mm});
            skLineSegment(sketch, "E3753", {"start": v(-22.86, -3.44) * mm, "end": v(-22.4, -3.44) * mm});
            skLineSegment(sketch, "E3754", {"start": v(-22.4, -3.44) * mm, "end": v(-22.47, -1.54) * mm});
            skLineSegment(sketch, "E3755", {"start": v(-22.47, -1.54) * mm, "end": v(-22.21, -1.54) * mm});
            skLineSegment(sketch, "E3756", {"start": v(-22.21, -1.54) * mm, "end": v(-22.09, -1.55) * mm});
            skLineSegment(sketch, "E3757", {"start": v(-22.09, -1.55) * mm, "end": v(-21.93, -1.57) * mm});
            skLineSegment(sketch, "E3758", {"start": v(-21.93, -1.57) * mm, "end": v(-21.6, -1.63) * mm});
            skLineSegment(sketch, "E3759", {"start": v(-21.6, -1.63) * mm, "end": v(-21.26, -1.7) * mm});
            skLineSegment(sketch, "E3760", {"start": v(-21.26, -1.7) * mm, "end": v(-20.92, -1.15) * mm});
            skLineSegment(sketch, "E3761", {"start": v(-20.92, -1.15) * mm, "end": v(-21.01, -1) * mm});
            skLineSegment(sketch, "E3762", {"start": v(-21.01, -1) * mm, "end": v(-22.45, -1) * mm});
            skLineSegment(sketch, "E3763", {"start": v(-22.45, -1) * mm, "end": v(-22.45, 0.39) * mm});
            skLineSegment(sketch, "E3764", {"start": v(-22.45, 0.39) * mm, "end": v(-21.93, 0.34) * mm});
            skLineSegment(sketch, "E3765", {"start": v(-21.93, 0.34) * mm, "end": v(-21.52, 0.29) * mm});
            skLineSegment(sketch, "E3766", {"start": v(-21.52, 0.29) * mm, "end": v(-21.36, 0.25) * mm});
            skLineSegment(sketch, "E3767", {"start": v(-21.36, 0.25) * mm, "end": v(-21.26, 0.23) * mm});
            skLineSegment(sketch, "E3768", {"start": v(-21.26, 0.23) * mm, "end": v(-21.1, 0.16) * mm});
            skLineSegment(sketch, "E3769", {"start": v(-21.1, 0.16) * mm, "end": v(-20.75, 0.75) * mm});
            skLineSegment(sketch, "E3770", {"start": v(-20.75, 0.75) * mm, "end": v(-20.84, 1) * mm});
            skLineSegment(sketch, "E3771", {"start": v(-20.84, 1) * mm, "end": v(-23.27, 1) * mm});
            skLineSegment(sketch, "E3772", {"start": v(-23.27, 1) * mm, "end": v(-23.27, 0.77) * mm});
            skLineSegment(sketch, "E3773", {"start": v(-23.27, 0.77) * mm, "end": v(-23.31, -3.44) * mm});
            skLineSegment(sketch, "E3774", {"start": v(-23.31, -3.44) * mm, "end": v(-22.86, -3.44) * mm});
            skLineSegment(sketch, "E3775", {"start": v(-18.23, -3.44) * mm, "end": v(-17.68, -3.44) * mm});
            skLineSegment(sketch, "E3776", {"start": v(-17.68, -3.44) * mm, "end": v(-16.84, -3.16) * mm});
            skLineSegment(sketch, "E3777", {"start": v(-16.84, -3.16) * mm, "end": v(-16.02, -2.25) * mm});
            skLineSegment(sketch, "E3778", {"start": v(-16.02, -2.25) * mm, "end": v(-15.93, -1.92) * mm});
            skLineSegment(sketch, "E3779", {"start": v(-15.93, -1.92) * mm, "end": v(-15.9, -1.76) * mm});
            skLineSegment(sketch, "E3780", {"start": v(-15.9, -1.76) * mm, "end": v(-15.86, -1.56) * mm});
            skLineSegment(sketch, "E3781", {"start": v(-15.86, -1.56) * mm, "end": v(-15.84, -1.35) * mm});
            skLineSegment(sketch, "E3782", {"start": v(-15.84, -1.35) * mm, "end": v(-15.84, -1.15) * mm});
            skLineSegment(sketch, "E3783", {"start": v(-15.84, -1.15) * mm, "end": v(-15.84, -0.72) * mm});
            skLineSegment(sketch, "E3784", {"start": v(-15.84, -0.72) * mm, "end": v(-15.96, -0.42) * mm});
            skLineSegment(sketch, "E3785", {"start": v(-15.96, -0.42) * mm, "end": v(-16.03, -0.28) * mm});
            skLineSegment(sketch, "E3786", {"start": v(-16.03, -0.28) * mm, "end": v(-16.14, -0.11) * mm});
            skLineSegment(sketch, "E3787", {"start": v(-16.14, -0.11) * mm, "end": v(-16.26, 0.06) * mm});
            skLineSegment(sketch, "E3788", {"start": v(-16.26, 0.06) * mm, "end": v(-16.38, 0.22) * mm});
            skLineSegment(sketch, "E3789", {"start": v(-16.38, 0.22) * mm, "end": v(-16.68, 0.55) * mm});
            skLineSegment(sketch, "E3790", {"start": v(-16.68, 0.55) * mm, "end": v(-17.4, 0.93) * mm});
            skLineSegment(sketch, "E3791", {"start": v(-17.4, 0.93) * mm, "end": v(-18.44, 1.02) * mm});
            skLineSegment(sketch, "E3792", {"start": v(-18.44, 1.02) * mm, "end": v(-19.4, 0.7) * mm});
            skLineSegment(sketch, "E3793", {"start": v(-19.4, 0.7) * mm, "end": v(-20.26, -0.16) * mm});
            skLineSegment(sketch, "E3794", {"start": v(-20.26, -0.16) * mm, "end": v(-20.36, -0.5) * mm});
            skLineSegment(sketch, "E3795", {"start": v(-20.36, -0.5) * mm, "end": v(-20.4, -0.68) * mm});
            skLineSegment(sketch, "E3796", {"start": v(-20.4, -0.68) * mm, "end": v(-20.43, -0.88) * mm});
            skLineSegment(sketch, "E3797", {"start": v(-20.43, -0.88) * mm, "end": v(-20.45, -1.1) * mm});
            skLineSegment(sketch, "E3798", {"start": v(-20.45, -1.1) * mm, "end": v(-20.46, -1.3) * mm});
            skLineSegment(sketch, "E3799", {"start": v(-20.46, -1.3) * mm, "end": v(-20.46, -1.73) * mm});
            skLineSegment(sketch, "E3800", {"start": v(-20.46, -1.73) * mm, "end": v(-20.32, -2.06) * mm});
            skLineSegment(sketch, "E3801", {"start": v(-20.32, -2.06) * mm, "end": v(-20.25, -2.21) * mm});
            skLineSegment(sketch, "E3802", {"start": v(-20.25, -2.21) * mm, "end": v(-20.16, -2.38) * mm});
            skLineSegment(sketch, "E3803", {"start": v(-20.16, -2.38) * mm, "end": v(-20.06, -2.54) * mm});
            skLineSegment(sketch, "E3804", {"start": v(-20.06, -2.54) * mm, "end": v(-19.96, -2.68) * mm});
            skLineSegment(sketch, "E3805", {"start": v(-19.96, -2.68) * mm, "end": v(-19.74, -2.98) * mm});
            skLineSegment(sketch, "E3806", {"start": v(-19.74, -2.98) * mm, "end": v(-18.78, -3.44) * mm});
            skLineSegment(sketch, "E3807", {"start": v(-18.78, -3.44) * mm, "end": v(-18.23, -3.44) * mm});
            skLineSegment(sketch, "E3808", {"start": v(-13.25, -3.43) * mm, "end": v(-12.71, -3.44) * mm});
            skLineSegment(sketch, "E3809", {"start": v(-12.71, -3.44) * mm, "end": v(-12.39, -3.32) * mm});
            skLineSegment(sketch, "E3810", {"start": v(-12.39, -3.32) * mm, "end": v(-12.23, -3.25) * mm});
            skLineSegment(sketch, "E3811", {"start": v(-12.23, -3.25) * mm, "end": v(-12.05, -3.16) * mm});
            skLineSegment(sketch, "E3812", {"start": v(-12.05, -3.16) * mm, "end": v(-11.87, -3.05) * mm});
            skLineSegment(sketch, "E3813", {"start": v(-11.87, -3.05) * mm, "end": v(-11.71, -2.94) * mm});
            skLineSegment(sketch, "E3814", {"start": v(-11.71, -2.94) * mm, "end": v(-11.37, -2.68) * mm});
            skLineSegment(sketch, "E3815", {"start": v(-11.37, -2.68) * mm, "end": v(-10.94, -1.77) * mm});
            skLineSegment(sketch, "E3816", {"start": v(-10.94, -1.77) * mm, "end": v(-10.94, -0.67) * mm});
            skLineSegment(sketch, "E3817", {"start": v(-10.94, -0.67) * mm, "end": v(-11.4, 0.25) * mm});
            skLineSegment(sketch, "E3818", {"start": v(-11.4, 0.25) * mm, "end": v(-11.76, 0.5) * mm});
            skLineSegment(sketch, "E3819", {"start": v(-11.76, 0.5) * mm, "end": v(-11.92, 0.6) * mm});
            skLineSegment(sketch, "E3820", {"start": v(-11.92, 0.6) * mm, "end": v(-12.1, 0.7) * mm});
            skLineSegment(sketch, "E3821", {"start": v(-12.1, 0.7) * mm, "end": v(-12.3, 0.8) * mm});
            skLineSegment(sketch, "E3822", {"start": v(-12.3, 0.8) * mm, "end": v(-12.46, 0.87) * mm});
            skLineSegment(sketch, "E3823", {"start": v(-12.46, 0.87) * mm, "end": v(-12.8, 0.99) * mm});
            skLineSegment(sketch, "E3824", {"start": v(-12.8, 0.99) * mm, "end": v(-13.63, 1) * mm});
            skLineSegment(sketch, "E3825", {"start": v(-13.63, 1) * mm, "end": v(-14.44, 0.72) * mm});
            skLineSegment(sketch, "E3826", {"start": v(-14.44, 0.72) * mm, "end": v(-15.14, 0.15) * mm});
            skLineSegment(sketch, "E3827", {"start": v(-15.14, 0.15) * mm, "end": v(-15.56, -0.77) * mm});
            skLineSegment(sketch, "E3828", {"start": v(-15.56, -0.77) * mm, "end": v(-15.55, -1.68) * mm});
            skLineSegment(sketch, "E3829", {"start": v(-15.55, -1.68) * mm, "end": v(-15.23, -2.47) * mm});
            skLineSegment(sketch, "E3830", {"start": v(-15.23, -2.47) * mm, "end": v(-14.54, -3.17) * mm});
            skLineSegment(sketch, "E3831", {"start": v(-14.54, -3.17) * mm, "end": v(-13.8, -3.43) * mm});
            skLineSegment(sketch, "E3832", {"start": v(-13.8, -3.43) * mm, "end": v(-13.25, -3.43) * mm});
            skLineSegment(sketch, "E3833", {"start": v(-8.7, -3.44) * mm, "end": v(-8.27, -3.44) * mm});
            skLineSegment(sketch, "E3834", {"start": v(-8.27, -3.44) * mm, "end": v(-8.33, 0.03) * mm});
            skLineSegment(sketch, "E3835", {"start": v(-8.33, 0.03) * mm, "end": v(-8.23, 0.44) * mm});
            skLineSegment(sketch, "E3836", {"start": v(-8.23, 0.44) * mm, "end": v(-7.18, 0.2) * mm});
            skLineSegment(sketch, "E3837", {"start": v(-7.18, 0.2) * mm, "end": v(-7.07, 0.34) * mm});
            skLineSegment(sketch, "E3838", {"start": v(-7.07, 0.34) * mm, "end": v(-6.99, 0.47) * mm});
            skLineSegment(sketch, "E3839", {"start": v(-6.99, 0.47) * mm, "end": v(-6.96, 0.53) * mm});
            skLineSegment(sketch, "E3840", {"start": v(-6.96, 0.53) * mm, "end": v(-6.95, 0.58) * mm});
            skLineSegment(sketch, "E3841", {"start": v(-6.95, 0.58) * mm, "end": v(-6.91, 0.84) * mm});
            skLineSegment(sketch, "E3842", {"start": v(-6.91, 0.84) * mm, "end": v(-6.88, 1) * mm});
            skLineSegment(sketch, "E3843", {"start": v(-6.88, 1) * mm, "end": v(-10.32, 1) * mm});
            skLineSegment(sketch, "E3844", {"start": v(-10.32, 1) * mm, "end": v(-10.6, 0.34) * mm});
            skLineSegment(sketch, "E3845", {"start": v(-10.6, 0.34) * mm, "end": v(-10.42, 0.17) * mm});
            skLineSegment(sketch, "E3846", {"start": v(-10.42, 0.17) * mm, "end": v(-10.07, 0.26) * mm});
            skLineSegment(sketch, "E3847", {"start": v(-10.07, 0.26) * mm, "end": v(-9.91, 0.3) * mm});
            skLineSegment(sketch, "E3848", {"start": v(-9.91, 0.3) * mm, "end": v(-9.74, 0.33) * mm});
            skLineSegment(sketch, "E3849", {"start": v(-9.74, 0.33) * mm, "end": v(-9.57, 0.35) * mm});
            skLineSegment(sketch, "E3850", {"start": v(-9.57, 0.35) * mm, "end": v(-9.42, 0.36) * mm});
            skLineSegment(sketch, "E3851", {"start": v(-9.42, 0.36) * mm, "end": v(-9.12, 0.36) * mm});
            skLineSegment(sketch, "E3852", {"start": v(-9.12, 0.36) * mm, "end": v(-9.14, -3.22) * mm});
            skLineSegment(sketch, "E3853", {"start": v(-9.14, -3.22) * mm, "end": v(-9.13, -3.44) * mm});
            skLineSegment(sketch, "E3854", {"start": v(-9.13, -3.44) * mm, "end": v(-8.7, -3.44) * mm});
            skLineSegment(sketch, "E3855", {"start": v(-5.84, -3.44) * mm, "end": v(-5.09, -3.44) * mm});
            skLineSegment(sketch, "E3856", {"start": v(-5.09, -3.44) * mm, "end": v(-4.1, -2.95) * mm});
            skLineSegment(sketch, "E3857", {"start": v(-4.1, -2.95) * mm, "end": v(-3.77, -2.26) * mm});
            skLineSegment(sketch, "E3858", {"start": v(-3.77, -2.26) * mm, "end": v(-3.97, -1.68) * mm});
            skLineSegment(sketch, "E3859", {"start": v(-3.97, -1.68) * mm, "end": v(-4.53, -1.1) * mm});
            skLineSegment(sketch, "E3860", {"start": v(-4.53, -1.1) * mm, "end": v(-4.06, -0.53) * mm});
            skLineSegment(sketch, "E3861", {"start": v(-4.06, -0.53) * mm, "end": v(-4.06, 0.16) * mm});
            skLineSegment(sketch, "E3862", {"start": v(-4.06, 0.16) * mm, "end": v(-4.24, 0.4) * mm});
            skLineSegment(sketch, "E3863", {"start": v(-4.24, 0.4) * mm, "end": v(-4.34, 0.5) * mm});
            skLineSegment(sketch, "E3864", {"start": v(-4.34, 0.5) * mm, "end": v(-4.46, 0.61) * mm});
            skLineSegment(sketch, "E3865", {"start": v(-4.46, 0.61) * mm, "end": v(-4.6, 0.71) * mm});
            skLineSegment(sketch, "E3866", {"start": v(-4.6, 0.71) * mm, "end": v(-4.72, 0.79) * mm});
            skLineSegment(sketch, "E3867", {"start": v(-4.72, 0.79) * mm, "end": v(-5, 0.94) * mm});
            skLineSegment(sketch, "E3868", {"start": v(-5, 0.94) * mm, "end": v(-6.6, 0.95) * mm});
            skLineSegment(sketch, "E3869", {"start": v(-6.6, 0.95) * mm, "end": v(-6.6, -3.35) * mm});
            skLineSegment(sketch, "E3870", {"start": v(-6.6, -3.35) * mm, "end": v(-6.6, -3.4) * mm});
            skLineSegment(sketch, "E3871", {"start": v(-6.6, -3.4) * mm, "end": v(-6.58, -3.4) * mm});
            skLineSegment(sketch, "E3872", {"start": v(-6.58, -3.4) * mm, "end": v(-6.53, -3.42) * mm});
            skLineSegment(sketch, "E3873", {"start": v(-6.53, -3.42) * mm, "end": v(-6.37, -3.43) * mm});
            skLineSegment(sketch, "E3874", {"start": v(-6.37, -3.43) * mm, "end": v(-6.13, -3.44) * mm});
            skLineSegment(sketch, "E3875", {"start": v(-6.13, -3.44) * mm, "end": v(-5.84, -3.44) * mm});
            skLineSegment(sketch, "E3876", {"start": v(-2.88, -3.44) * mm, "end": v(-2.33, -3.44) * mm});
            skLineSegment(sketch, "E3877", {"start": v(-2.33, -3.44) * mm, "end": v(-2.28, -3.29) * mm});
            skLineSegment(sketch, "E3878", {"start": v(-2.28, -3.29) * mm, "end": v(-2.19, -3.04) * mm});
            skLineSegment(sketch, "E3879", {"start": v(-2.19, -3.04) * mm, "end": v(-2.04, -2.69) * mm});
            skLineSegment(sketch, "E3880", {"start": v(-2.04, -2.69) * mm, "end": v(-1.84, -2.25) * mm});
            skLineSegment(sketch, "E3881", {"start": v(-1.84, -2.25) * mm, "end": v(-1.56, -2.1) * mm});
            skLineSegment(sketch, "E3882", {"start": v(-1.56, -2.1) * mm, "end": v(-0.15, -2.11) * mm});
            skLineSegment(sketch, "E3883", {"start": v(-0.15, -2.11) * mm, "end": v(0, -2.4) * mm});
            skLineSegment(sketch, "E3884", {"start": v(0, -2.4) * mm, "end": v(0.06, -2.53) * mm});
            skLineSegment(sketch, "E3885", {"start": v(0.06, -2.53) * mm, "end": v(0.13, -2.7) * mm});
            skLineSegment(sketch, "E3886", {"start": v(0.13, -2.7) * mm, "end": v(0.2, -2.87) * mm});
            skLineSegment(sketch, "E3887", {"start": v(0.2, -2.87) * mm, "end": v(0.25, -3.04) * mm});
            skLineSegment(sketch, "E3888", {"start": v(0.25, -3.04) * mm, "end": v(0.36, -3.4) * mm});
            skLineSegment(sketch, "E3889", {"start": v(0.36, -3.4) * mm, "end": v(1.32, -3.45) * mm});
            skLineSegment(sketch, "E3890", {"start": v(1.32, -3.45) * mm, "end": v(1.48, -3.3) * mm});
            skLineSegment(sketch, "E3891", {"start": v(1.48, -3.3) * mm, "end": v(1.14, -2.85) * mm});
            skLineSegment(sketch, "E3892", {"start": v(1.14, -2.85) * mm, "end": v(-0.74, 1) * mm});
            skLineSegment(sketch, "E3893", {"start": v(-0.74, 1) * mm, "end": v(-0.92, 0.94) * mm});
            skLineSegment(sketch, "E3894", {"start": v(-0.92, 0.94) * mm, "end": v(-2.36, -1.59) * mm});
            skLineSegment(sketch, "E3895", {"start": v(-2.36, -1.59) * mm, "end": v(-3.38, -3.3) * mm});
            skLineSegment(sketch, "E3896", {"start": v(-3.38, -3.3) * mm, "end": v(-3.44, -3.44) * mm});
            skLineSegment(sketch, "E3897", {"start": v(-3.44, -3.44) * mm, "end": v(-2.88, -3.44) * mm});
            skLineSegment(sketch, "E3898", {"start": v(3.07, -3.44) * mm, "end": v(4.2, -3.44) * mm});
            skLineSegment(sketch, "E3899", {"start": v(4.2, -3.44) * mm, "end": v(4.59, -2.63) * mm});
            skLineSegment(sketch, "E3900", {"start": v(4.59, -2.63) * mm, "end": v(4.48, -2.53) * mm});
            skLineSegment(sketch, "E3901", {"start": v(4.48, -2.53) * mm, "end": v(3.94, -2.67) * mm});
            skLineSegment(sketch, "E3902", {"start": v(3.94, -2.67) * mm, "end": v(3.7, -2.72) * mm});
            skLineSegment(sketch, "E3903", {"start": v(3.7, -2.72) * mm, "end": v(3.47, -2.77) * mm});
            skLineSegment(sketch, "E3904", {"start": v(3.47, -2.77) * mm, "end": v(3.26, -2.8) * mm});
            skLineSegment(sketch, "E3905", {"start": v(3.26, -2.8) * mm, "end": v(3.1, -2.8) * mm});
            skLineSegment(sketch, "E3906", {"start": v(3.1, -2.8) * mm, "end": v(2.82, -2.8) * mm});
            skLineSegment(sketch, "E3907", {"start": v(2.82, -2.8) * mm, "end": v(2.85, 0.95) * mm});
            skLineSegment(sketch, "E3908", {"start": v(2.85, 0.95) * mm, "end": v(1.99, 0.95) * mm});
            skLineSegment(sketch, "E3909", {"start": v(1.99, 0.95) * mm, "end": v(2.03, -2.86) * mm});
            skLineSegment(sketch, "E3910", {"start": v(2.03, -2.86) * mm, "end": v(1.85, -3.33) * mm});
            skLineSegment(sketch, "E3911", {"start": v(1.85, -3.33) * mm, "end": v(1.96, -3.44) * mm});
            skLineSegment(sketch, "E3912", {"start": v(1.96, -3.44) * mm, "end": v(3.07, -3.44) * mm});
            skLineSegment(sketch, "E3913", {"start": v(6.09, -3.42) * mm, "end": v(7.23, -3.4) * mm});
            skLineSegment(sketch, "E3914", {"start": v(7.23, -3.4) * mm, "end": v(7.56, -2.7) * mm});
            skLineSegment(sketch, "E3915", {"start": v(7.56, -2.7) * mm, "end": v(7.4, -2.54) * mm});
            skLineSegment(sketch, "E3916", {"start": v(7.4, -2.54) * mm, "end": v(6.5, -2.8) * mm});
            skLineSegment(sketch, "E3917", {"start": v(6.5, -2.8) * mm, "end": v(5.81, -2.8) * mm});
            skLineSegment(sketch, "E3918", {"start": v(5.81, -2.8) * mm, "end": v(5.84, 0.95) * mm});
            skLineSegment(sketch, "E3919", {"start": v(5.84, 0.95) * mm, "end": v(4.93, 1) * mm});
            skLineSegment(sketch, "E3920", {"start": v(4.93, 1) * mm, "end": v(4.99, -2.7) * mm});
            skLineSegment(sketch, "E3921", {"start": v(4.99, -2.7) * mm, "end": v(4.85, -3.34) * mm});
            skLineSegment(sketch, "E3922", {"start": v(4.85, -3.34) * mm, "end": v(4.95, -3.45) * mm});
            skLineSegment(sketch, "E3923", {"start": v(4.95, -3.45) * mm, "end": v(6.09, -3.42) * mm});
            skLineSegment(sketch, "E3924", {"start": v(11.81, -3.42) * mm, "end": v(12.68, -3.4) * mm});
            skLineSegment(sketch, "E3925", {"start": v(12.68, -3.4) * mm, "end": v(13.16, -3.08) * mm});
            skLineSegment(sketch, "E3926", {"start": v(13.16, -3.08) * mm, "end": v(13.16, -2.55) * mm});
            skLineSegment(sketch, "E3927", {"start": v(13.16, -2.55) * mm, "end": v(12.94, -2.47) * mm});
            skLineSegment(sketch, "E3928", {"start": v(12.94, -2.47) * mm, "end": v(12.23, -2.83) * mm});
            skLineSegment(sketch, "E3929", {"start": v(12.23, -2.83) * mm, "end": v(11.12, -2.76) * mm});
            skLineSegment(sketch, "E3930", {"start": v(11.12, -2.76) * mm, "end": v(10.53, -2.34) * mm});
            skLineSegment(sketch, "E3931", {"start": v(10.53, -2.34) * mm, "end": v(10.17, -1.64) * mm});
            skLineSegment(sketch, "E3932", {"start": v(10.17, -1.64) * mm, "end": v(10.17, -0.85) * mm});
            skLineSegment(sketch, "E3933", {"start": v(10.17, -0.85) * mm, "end": v(10.7, -0.03) * mm});
            skLineSegment(sketch, "E3934", {"start": v(10.7, -0.03) * mm, "end": v(11.37, 0.29) * mm});
            skLineSegment(sketch, "E3935", {"start": v(11.37, 0.29) * mm, "end": v(11.8, 0.28) * mm});
            skLineSegment(sketch, "E3936", {"start": v(11.8, 0.28) * mm, "end": v(12.07, 0.27) * mm});
            skLineSegment(sketch, "E3937", {"start": v(12.07, 0.27) * mm, "end": v(12.35, 0.22) * mm});
            skLineSegment(sketch, "E3938", {"start": v(12.35, 0.22) * mm, "end": v(12.63, 0.15) * mm});
            skLineSegment(sketch, "E3939", {"start": v(12.63, 0.15) * mm, "end": v(12.91, 0.05) * mm});
            skLineSegment(sketch, "E3940", {"start": v(12.91, 0.05) * mm, "end": v(13.07, -0.02) * mm});
            skLineSegment(sketch, "E3941", {"start": v(13.07, -0.02) * mm, "end": v(13.07, 0.8) * mm});
            skLineSegment(sketch, "E3942", {"start": v(13.07, 0.8) * mm, "end": v(12.95, 0.84) * mm});
            skLineSegment(sketch, "E3943", {"start": v(12.95, 0.84) * mm, "end": v(12.72, 0.9) * mm});
            skLineSegment(sketch, "E3944", {"start": v(12.72, 0.9) * mm, "end": v(12.33, 0.95) * mm});
            skLineSegment(sketch, "E3945", {"start": v(12.33, 0.95) * mm, "end": v(11.83, 1.01) * mm});
            skLineSegment(sketch, "E3946", {"start": v(11.83, 1.01) * mm, "end": v(10.67, 0.72) * mm});
            skLineSegment(sketch, "E3947", {"start": v(10.67, 0.72) * mm, "end": v(9.95, 0.2) * mm});
            skLineSegment(sketch, "E3948", {"start": v(9.95, 0.2) * mm, "end": v(9.38, -0.62) * mm});
            skLineSegment(sketch, "E3949", {"start": v(9.38, -0.62) * mm, "end": v(9.26, -1.4) * mm});
            skLineSegment(sketch, "E3950", {"start": v(9.26, -1.4) * mm, "end": v(9.55, -2.37) * mm});
            skLineSegment(sketch, "E3951", {"start": v(9.55, -2.37) * mm, "end": v(10.22, -3.1) * mm});
            skLineSegment(sketch, "E3952", {"start": v(10.22, -3.1) * mm, "end": v(10.94, -3.45) * mm});
            skLineSegment(sketch, "E3953", {"start": v(10.94, -3.45) * mm, "end": v(11.81, -3.42) * mm});
            skLineSegment(sketch, "E3954", {"start": v(14.75, -3.44) * mm, "end": v(15.9, -3.44) * mm});
            skLineSegment(sketch, "E3955", {"start": v(15.9, -3.44) * mm, "end": v(16.23, -2.68) * mm});
            skLineSegment(sketch, "E3956", {"start": v(16.23, -2.68) * mm, "end": v(16.04, -2.56) * mm});
            skLineSegment(sketch, "E3957", {"start": v(16.04, -2.56) * mm, "end": v(15.58, -2.68) * mm});
            skLineSegment(sketch, "E3958", {"start": v(15.58, -2.68) * mm, "end": v(15.37, -2.73) * mm});
            skLineSegment(sketch, "E3959", {"start": v(15.37, -2.73) * mm, "end": v(15.15, -2.77) * mm});
            skLineSegment(sketch, "E3960", {"start": v(15.15, -2.77) * mm, "end": v(14.94, -2.8) * mm});
            skLineSegment(sketch, "E3961", {"start": v(14.94, -2.8) * mm, "end": v(14.77, -2.8) * mm});
            skLineSegment(sketch, "E3962", {"start": v(14.77, -2.8) * mm, "end": v(14.43, -2.8) * mm});
            skLineSegment(sketch, "E3963", {"start": v(14.43, -2.8) * mm, "end": v(14.47, 0.95) * mm});
            skLineSegment(sketch, "E3964", {"start": v(14.47, 0.95) * mm, "end": v(13.61, 0.95) * mm});
            skLineSegment(sketch, "E3965", {"start": v(13.61, 0.95) * mm, "end": v(13.6, -3.3) * mm});
            skLineSegment(sketch, "E3966", {"start": v(13.6, -3.3) * mm, "end": v(13.62, -3.44) * mm});
            skLineSegment(sketch, "E3967", {"start": v(13.62, -3.44) * mm, "end": v(14.75, -3.44) * mm});
            skLineSegment(sketch, "E3968", {"start": v(18.24, -3.44) * mm, "end": v(18.74, -3.44) * mm});
            skLineSegment(sketch, "E3969", {"start": v(18.74, -3.44) * mm, "end": v(19.1, -3.3) * mm});
            skLineSegment(sketch, "E3970", {"start": v(19.1, -3.3) * mm, "end": v(19.35, -3.22) * mm});
            skLineSegment(sketch, "E3971", {"start": v(19.35, -3.22) * mm, "end": v(19.42, -3.2) * mm});
            skLineSegment(sketch, "E3972", {"start": v(19.42, -3.2) * mm, "end": v(19.47, -3.19) * mm});
            skLineSegment(sketch, "E3973", {"start": v(19.47, -3.19) * mm, "end": v(19.5, -3.2) * mm});
            skLineSegment(sketch, "E3974", {"start": v(19.5, -3.2) * mm, "end": v(19.5, -3.22) * mm});
            skLineSegment(sketch, "E3975", {"start": v(19.5, -3.22) * mm, "end": v(19.5, -3.3) * mm});
            skLineSegment(sketch, "E3976", {"start": v(19.5, -3.3) * mm, "end": v(19.5, -3.44) * mm});
            skLineSegment(sketch, "E3977", {"start": v(19.5, -3.44) * mm, "end": v(20.41, -3.44) * mm});
            skLineSegment(sketch, "E3978", {"start": v(20.41, -3.44) * mm, "end": v(20.42, -3.3) * mm});
            skLineSegment(sketch, "E3979", {"start": v(20.42, -3.3) * mm, "end": v(20.43, 0.95) * mm});
            skLineSegment(sketch, "E3980", {"start": v(20.43, 0.95) * mm, "end": v(19.55, 1) * mm});
            skLineSegment(sketch, "E3981", {"start": v(19.55, 1) * mm, "end": v(19.55, -2.16) * mm});
            skLineSegment(sketch, "E3982", {"start": v(19.55, -2.16) * mm, "end": v(19.17, -2.67) * mm});
            skLineSegment(sketch, "E3983", {"start": v(19.17, -2.67) * mm, "end": v(18.48, -2.9) * mm});
            skLineSegment(sketch, "E3984", {"start": v(18.48, -2.9) * mm, "end": v(17.88, -2.7) * mm});
            skLineSegment(sketch, "E3985", {"start": v(17.88, -2.7) * mm, "end": v(17.51, -2.2) * mm});
            skLineSegment(sketch, "E3986", {"start": v(17.51, -2.2) * mm, "end": v(17.51, 1) * mm});
            skLineSegment(sketch, "E3987", {"start": v(17.51, 1) * mm, "end": v(16.58, 0.95) * mm});
            skLineSegment(sketch, "E3988", {"start": v(16.58, 0.95) * mm, "end": v(16.62, -1.68) * mm});
            skLineSegment(sketch, "E3989", {"start": v(16.62, -1.68) * mm, "end": v(16.8, -2.49) * mm});
            skLineSegment(sketch, "E3990", {"start": v(16.8, -2.49) * mm, "end": v(17.18, -3.1) * mm});
            skLineSegment(sketch, "E3991", {"start": v(17.18, -3.1) * mm, "end": v(17.74, -3.44) * mm});
            skLineSegment(sketch, "E3992", {"start": v(17.74, -3.44) * mm, "end": v(18.24, -3.44) * mm});
            skLineSegment(sketch, "E3993", {"start": v(21.5, -3.44) * mm, "end": v(22.2, -3.44) * mm});
            skLineSegment(sketch, "E3994", {"start": v(22.2, -3.44) * mm, "end": v(23.02, -3.16) * mm});
            skLineSegment(sketch, "E3995", {"start": v(23.02, -3.16) * mm, "end": v(23.54, -2.62) * mm});
            skLineSegment(sketch, "E3996", {"start": v(23.54, -2.62) * mm, "end": v(23.54, -1.82) * mm});
            skLineSegment(sketch, "E3997", {"start": v(23.54, -1.82) * mm, "end": v(22.83, -1.1) * mm});
            skLineSegment(sketch, "E3998", {"start": v(22.83, -1.1) * mm, "end": v(23.31, -0.53) * mm});
            skLineSegment(sketch, "E3999", {"start": v(23.31, -0.53) * mm, "end": v(23.31, 0.17) * mm});
            skLineSegment(sketch, "E4000", {"start": v(23.31, 0.17) * mm, "end": v(22.76, 0.8) * mm});
            skLineSegment(sketch, "E4001", {"start": v(22.76, 0.8) * mm, "end": v(21.82, 1.01) * mm});
            skLineSegment(sketch, "E4002", {"start": v(21.82, 1.01) * mm, "end": v(20.73, 0.95) * mm});
            skLineSegment(sketch, "E4003", {"start": v(20.73, 0.95) * mm, "end": v(20.81, 0.68) * mm});
            skLineSegment(sketch, "E4004", {"start": v(20.81, 0.68) * mm, "end": v(20.88, -2.97) * mm});
            skLineSegment(sketch, "E4005", {"start": v(20.88, -2.97) * mm, "end": v(20.7, -3.33) * mm});
            skLineSegment(sketch, "E4006", {"start": v(20.7, -3.33) * mm, "end": v(20.8, -3.44) * mm});
            skLineSegment(sketch, "E4007", {"start": v(20.8, -3.44) * mm, "end": v(21.5, -3.44) * mm});
            skLineSegment(sketch, "E4008", {"start": v(-17.12, -2.6) * mm, "end": v(-17.06, -2.53) * mm});
            skLineSegment(sketch, "E4009", {"start": v(-17.06, -2.53) * mm, "end": v(-16.98, -2.43) * mm});
            skLineSegment(sketch, "E4010", {"start": v(-16.98, -2.43) * mm, "end": v(-16.91, -2.3) * mm});
            skLineSegment(sketch, "E4011", {"start": v(-16.91, -2.3) * mm, "end": v(-16.84, -2.17) * mm});
            skLineSegment(sketch, "E4012", {"start": v(-16.84, -2.17) * mm, "end": v(-16.77, -2.02) * mm});
            skLineSegment(sketch, "E4013", {"start": v(-16.77, -2.02) * mm, "end": v(-16.7, -1.86) * mm});
            skLineSegment(sketch, "E4014", {"start": v(-16.7, -1.86) * mm, "end": v(-16.66, -1.72) * mm});
            skLineSegment(sketch, "E4015", {"start": v(-16.66, -1.72) * mm, "end": v(-16.63, -1.58) * mm});
            skLineSegment(sketch, "E4016", {"start": v(-16.63, -1.58) * mm, "end": v(-16.57, -1.3) * mm});
            skLineSegment(sketch, "E4017", {"start": v(-16.57, -1.3) * mm, "end": v(-16.73, -0.63) * mm});
            skLineSegment(sketch, "E4018", {"start": v(-16.73, -0.63) * mm, "end": v(-17.15, 0.01) * mm});
            skLineSegment(sketch, "E4019", {"start": v(-17.15, 0.01) * mm, "end": v(-18.07, 0.45) * mm});
            skLineSegment(sketch, "E4020", {"start": v(-18.07, 0.45) * mm, "end": v(-18.7, 0.45) * mm});
            skLineSegment(sketch, "E4021", {"start": v(-18.7, 0.45) * mm, "end": v(-19.35, 0.01) * mm});
            skLineSegment(sketch, "E4022", {"start": v(-19.35, 0.01) * mm, "end": v(-19.64, -0.62) * mm});
            skLineSegment(sketch, "E4023", {"start": v(-19.64, -0.62) * mm, "end": v(-19.64, -1.55) * mm});
            skLineSegment(sketch, "E4024", {"start": v(-19.64, -1.55) * mm, "end": v(-19.4, -2.14) * mm});
            skLineSegment(sketch, "E4025", {"start": v(-19.4, -2.14) * mm, "end": v(-19.1, -2.4) * mm});
            skLineSegment(sketch, "E4026", {"start": v(-19.1, -2.4) * mm, "end": v(-18.97, -2.49) * mm});
            skLineSegment(sketch, "E4027", {"start": v(-18.97, -2.49) * mm, "end": v(-18.86, -2.57) * mm});
            skLineSegment(sketch, "E4028", {"start": v(-18.86, -2.57) * mm, "end": v(-18.75, -2.64) * mm});
            skLineSegment(sketch, "E4029", {"start": v(-18.75, -2.64) * mm, "end": v(-18.65, -2.7) * mm});
            skLineSegment(sketch, "E4030", {"start": v(-18.65, -2.7) * mm, "end": v(-18.53, -2.74) * mm});
            skLineSegment(sketch, "E4031", {"start": v(-18.53, -2.74) * mm, "end": v(-18.4, -2.77) * mm});
            skLineSegment(sketch, "E4032", {"start": v(-18.4, -2.77) * mm, "end": v(-18.1, -2.83) * mm});
            skLineSegment(sketch, "E4033", {"start": v(-18.1, -2.83) * mm, "end": v(-17.79, -2.89) * mm});
            skLineSegment(sketch, "E4034", {"start": v(-17.79, -2.89) * mm, "end": v(-17.51, -2.79) * mm});
            skLineSegment(sketch, "E4035", {"start": v(-17.51, -2.79) * mm, "end": v(-17.29, -2.7) * mm});
            skLineSegment(sketch, "E4036", {"start": v(-17.29, -2.7) * mm, "end": v(-17.19, -2.64) * mm});
            skLineSegment(sketch, "E4037", {"start": v(-17.19, -2.64) * mm, "end": v(-17.12, -2.6) * mm});
            skLineSegment(sketch, "E4038", {"start": v(-12.16, -2.53) * mm, "end": v(-11.95, -2.33) * mm});
            skLineSegment(sketch, "E4039", {"start": v(-11.95, -2.33) * mm, "end": v(-11.65, -1.43) * mm});
            skLineSegment(sketch, "E4040", {"start": v(-11.65, -1.43) * mm, "end": v(-11.7, -1.13) * mm});
            skLineSegment(sketch, "E4041", {"start": v(-11.7, -1.13) * mm, "end": v(-11.73, -0.98) * mm});
            skLineSegment(sketch, "E4042", {"start": v(-11.73, -0.98) * mm, "end": v(-11.78, -0.82) * mm});
            skLineSegment(sketch, "E4043", {"start": v(-11.78, -0.82) * mm, "end": v(-11.84, -0.65) * mm});
            skLineSegment(sketch, "E4044", {"start": v(-11.84, -0.65) * mm, "end": v(-11.9, -0.5) * mm});
            skLineSegment(sketch, "E4045", {"start": v(-11.9, -0.5) * mm, "end": v(-12.06, -0.16) * mm});
            skLineSegment(sketch, "E4046", {"start": v(-12.06, -0.16) * mm, "end": v(-12.76, 0.35) * mm});
            skLineSegment(sketch, "E4047", {"start": v(-12.76, 0.35) * mm, "end": v(-13.48, 0.47) * mm});
            skLineSegment(sketch, "E4048", {"start": v(-13.48, 0.47) * mm, "end": v(-13.99, 0.36) * mm});
            skLineSegment(sketch, "E4049", {"start": v(-13.99, 0.36) * mm, "end": v(-14.48, -0.07) * mm});
            skLineSegment(sketch, "E4050", {"start": v(-14.48, -0.07) * mm, "end": v(-14.75, -0.72) * mm});
            skLineSegment(sketch, "E4051", {"start": v(-14.75, -0.72) * mm, "end": v(-14.75, -1.46) * mm});
            skLineSegment(sketch, "E4052", {"start": v(-14.75, -1.46) * mm, "end": v(-14.61, -1.79) * mm});
            skLineSegment(sketch, "E4053", {"start": v(-14.61, -1.79) * mm, "end": v(-14.51, -2) * mm});
            skLineSegment(sketch, "E4054", {"start": v(-14.51, -2) * mm, "end": v(-14.4, -2.17) * mm});
            skLineSegment(sketch, "E4055", {"start": v(-14.4, -2.17) * mm, "end": v(-14.26, -2.33) * mm});
            skLineSegment(sketch, "E4056", {"start": v(-14.26, -2.33) * mm, "end": v(-14.11, -2.47) * mm});
            skLineSegment(sketch, "E4057", {"start": v(-14.11, -2.47) * mm, "end": v(-13.94, -2.58) * mm});
            skLineSegment(sketch, "E4058", {"start": v(-13.94, -2.58) * mm, "end": v(-13.75, -2.68) * mm});
            skLineSegment(sketch, "E4059", {"start": v(-13.75, -2.68) * mm, "end": v(-13.53, -2.75) * mm});
            skLineSegment(sketch, "E4060", {"start": v(-13.53, -2.75) * mm, "end": v(-13.3, -2.8) * mm});
            skLineSegment(sketch, "E4061", {"start": v(-13.3, -2.8) * mm, "end": v(-12.98, -2.86) * mm});
            skLineSegment(sketch, "E4062", {"start": v(-12.98, -2.86) * mm, "end": v(-12.38, -2.74) * mm});
            skLineSegment(sketch, "E4063", {"start": v(-12.38, -2.74) * mm, "end": v(-12.16, -2.53) * mm});
            skLineSegment(sketch, "E4064", {"start": v(-4.78, -2.18) * mm, "end": v(-4.78, -1.84) * mm});
            skLineSegment(sketch, "E4065", {"start": v(-4.78, -1.84) * mm, "end": v(-5.02, -1.6) * mm});
            skLineSegment(sketch, "E4066", {"start": v(-5.02, -1.6) * mm, "end": v(-5.2, -1.43) * mm});
            skLineSegment(sketch, "E4067", {"start": v(-5.2, -1.43) * mm, "end": v(-5.28, -1.38) * mm});
            skLineSegment(sketch, "E4068", {"start": v(-5.28, -1.38) * mm, "end": v(-5.33, -1.36) * mm});
            skLineSegment(sketch, "E4069", {"start": v(-5.33, -1.36) * mm, "end": v(-5.42, -1.34) * mm});
            skLineSegment(sketch, "E4070", {"start": v(-5.42, -1.34) * mm, "end": v(-5.54, -1.3) * mm});
            skLineSegment(sketch, "E4071", {"start": v(-5.54, -1.3) * mm, "end": v(-5.69, -1.25) * mm});
            skLineSegment(sketch, "E4072", {"start": v(-5.69, -1.25) * mm, "end": v(-5.69, -2.9) * mm});
            skLineSegment(sketch, "E4073", {"start": v(-5.69, -2.9) * mm, "end": v(-5.28, -2.9) * mm});
            skLineSegment(sketch, "E4074", {"start": v(-5.28, -2.9) * mm, "end": v(-4.78, -2.52) * mm});
            skLineSegment(sketch, "E4075", {"start": v(-4.78, -2.52) * mm, "end": v(-4.78, -2.18) * mm});
            skLineSegment(sketch, "E4076", {"start": v(22.68, -2.22) * mm, "end": v(22.67, -2.14) * mm});
            skLineSegment(sketch, "E4077", {"start": v(22.67, -2.14) * mm, "end": v(22.64, -2.04) * mm});
            skLineSegment(sketch, "E4078", {"start": v(22.64, -2.04) * mm, "end": v(22.6, -1.92) * mm});
            skLineSegment(sketch, "E4079", {"start": v(22.6, -1.92) * mm, "end": v(22.54, -1.8) * mm});
            skLineSegment(sketch, "E4080", {"start": v(22.54, -1.8) * mm, "end": v(22.4, -1.54) * mm});
            skLineSegment(sketch, "E4081", {"start": v(22.4, -1.54) * mm, "end": v(22.14, -1.4) * mm});
            skLineSegment(sketch, "E4082", {"start": v(22.14, -1.4) * mm, "end": v(21.92, -1.3) * mm});
            skLineSegment(sketch, "E4083", {"start": v(21.92, -1.3) * mm, "end": v(21.83, -1.28) * mm});
            skLineSegment(sketch, "E4084", {"start": v(21.83, -1.28) * mm, "end": v(21.78, -1.27) * mm});
            skLineSegment(sketch, "E4085", {"start": v(21.78, -1.27) * mm, "end": v(21.68, -1.27) * mm});
            skLineSegment(sketch, "E4086", {"start": v(21.68, -1.27) * mm, "end": v(21.68, -2.9) * mm});
            skLineSegment(sketch, "E4087", {"start": v(21.68, -2.9) * mm, "end": v(22.15, -2.9) * mm});
            skLineSegment(sketch, "E4088", {"start": v(22.15, -2.9) * mm, "end": v(22.68, -2.37) * mm});
            skLineSegment(sketch, "E4089", {"start": v(22.68, -2.37) * mm, "end": v(22.68, -2.22) * mm});
            skLineSegment(sketch, "E4090", {"start": v(-0.89, -0.63) * mm, "end": v(-0.92, -0.66) * mm});
            skLineSegment(sketch, "E4091", {"start": v(-0.92, -0.66) * mm, "end": v(-0.98, -0.74) * mm});
            skLineSegment(sketch, "E4092", {"start": v(-0.98, -0.74) * mm, "end": v(-1.13, -1) * mm});
            skLineSegment(sketch, "E4093", {"start": v(-1.13, -1) * mm, "end": v(-1.27, -1.25) * mm});
            skLineSegment(sketch, "E4094", {"start": v(-1.27, -1.25) * mm, "end": v(-1.32, -1.35) * mm});
            skLineSegment(sketch, "E4095", {"start": v(-1.32, -1.35) * mm, "end": v(-1.34, -1.41) * mm});
            skLineSegment(sketch, "E4096", {"start": v(-1.34, -1.41) * mm, "end": v(-1.3, -1.43) * mm});
            skLineSegment(sketch, "E4097", {"start": v(-1.3, -1.43) * mm, "end": v(-1.2, -1.44) * mm});
            skLineSegment(sketch, "E4098", {"start": v(-1.2, -1.44) * mm, "end": v(-0.89, -1.45) * mm});
            skLineSegment(sketch, "E4099", {"start": v(-0.89, -1.45) * mm, "end": v(-0.43, -1.45) * mm});
            skLineSegment(sketch, "E4100", {"start": v(-0.43, -1.45) * mm, "end": v(-0.63, -1.04) * mm});
            skLineSegment(sketch, "E4101", {"start": v(-0.63, -1.04) * mm, "end": v(-0.71, -0.88) * mm});
            skLineSegment(sketch, "E4102", {"start": v(-0.71, -0.88) * mm, "end": v(-0.79, -0.75) * mm});
            skLineSegment(sketch, "E4103", {"start": v(-0.79, -0.75) * mm, "end": v(-0.85, -0.67) * mm});
            skLineSegment(sketch, "E4104", {"start": v(-0.85, -0.67) * mm, "end": v(-0.87, -0.64) * mm});
            skLineSegment(sketch, "E4105", {"start": v(-0.87, -0.64) * mm, "end": v(-0.89, -0.63) * mm});
            skLineSegment(sketch, "E4106", {"start": v(-5.12, -0.74) * mm, "end": v(-4.96, -0.6) * mm});
            skLineSegment(sketch, "E4107", {"start": v(-4.96, -0.6) * mm, "end": v(-4.96, 0.06) * mm});
            skLineSegment(sketch, "E4108", {"start": v(-4.96, 0.06) * mm, "end": v(-5.13, 0.22) * mm});
            skLineSegment(sketch, "E4109", {"start": v(-5.13, 0.22) * mm, "end": v(-5.21, 0.28) * mm});
            skLineSegment(sketch, "E4110", {"start": v(-5.21, 0.28) * mm, "end": v(-5.3, 0.33) * mm});
            skLineSegment(sketch, "E4111", {"start": v(-5.3, 0.33) * mm, "end": v(-5.4, 0.38) * mm});
            skLineSegment(sketch, "E4112", {"start": v(-5.4, 0.38) * mm, "end": v(-5.5, 0.4) * mm});
            skLineSegment(sketch, "E4113", {"start": v(-5.5, 0.4) * mm, "end": v(-5.69, 0.44) * mm});
            skLineSegment(sketch, "E4114", {"start": v(-5.69, 0.44) * mm, "end": v(-5.69, -1) * mm});
            skLineSegment(sketch, "E4115", {"start": v(-5.69, -1) * mm, "end": v(-5.62, -0.99) * mm});
            skLineSegment(sketch, "E4116", {"start": v(-5.62, -0.99) * mm, "end": v(-5.5, -0.96) * mm});
            skLineSegment(sketch, "E4117", {"start": v(-5.5, -0.96) * mm, "end": v(-5.37, -0.91) * mm});
            skLineSegment(sketch, "E4118", {"start": v(-5.37, -0.91) * mm, "end": v(-5.24, -0.84) * mm});
            skLineSegment(sketch, "E4119", {"start": v(-5.24, -0.84) * mm, "end": v(-5.12, -0.74) * mm});
            skLineSegment(sketch, "E4120", {"start": v(22.5, -0.28) * mm, "end": v(22.5, -0.1) * mm});
            skLineSegment(sketch, "E4121", {"start": v(22.5, -0.1) * mm, "end": v(22.3, 0.12) * mm});
            skLineSegment(sketch, "E4122", {"start": v(22.3, 0.12) * mm, "end": v(22.2, 0.22) * mm});
            skLineSegment(sketch, "E4123", {"start": v(22.2, 0.22) * mm, "end": v(22.09, 0.3) * mm});
            skLineSegment(sketch, "E4124", {"start": v(22.09, 0.3) * mm, "end": v(21.98, 0.37) * mm});
            skLineSegment(sketch, "E4125", {"start": v(21.98, 0.37) * mm, "end": v(21.89, 0.4) * mm});
            skLineSegment(sketch, "E4126", {"start": v(21.89, 0.4) * mm, "end": v(21.68, 0.47) * mm});
            skLineSegment(sketch, "E4127", {"start": v(21.68, 0.47) * mm, "end": v(21.68, -1) * mm});
            skLineSegment(sketch, "E4128", {"start": v(21.68, -1) * mm, "end": v(21.97, -1) * mm});
            skLineSegment(sketch, "E4129", {"start": v(21.97, -1) * mm, "end": v(22.5, -0.47) * mm});
            skLineSegment(sketch, "E4130", {"start": v(22.5, -0.47) * mm, "end": v(22.5, -0.28) * mm});
            skLineSegment(sketch, "E4131", {"start": v(11.03, 4.24) * mm, "end": v(11.4, 4.42) * mm});
            skLineSegment(sketch, "E4132", {"start": v(11.4, 4.42) * mm, "end": v(12.15, 5.19) * mm});
            skLineSegment(sketch, "E4133", {"start": v(12.15, 5.19) * mm, "end": v(12.7, 6.22) * mm});
            skLineSegment(sketch, "E4134", {"start": v(12.7, 6.22) * mm, "end": v(12.98, 7.29) * mm});
            skLineSegment(sketch, "E4135", {"start": v(12.98, 7.29) * mm, "end": v(12.98, 8.68) * mm});
            skLineSegment(sketch, "E4136", {"start": v(12.98, 8.68) * mm, "end": v(12.8, 9.3) * mm});
            skLineSegment(sketch, "E4137", {"start": v(12.8, 9.3) * mm, "end": v(12.7, 9.57) * mm});
            skLineSegment(sketch, "E4138", {"start": v(12.7, 9.57) * mm, "end": v(12.6, 9.85) * mm});
            skLineSegment(sketch, "E4139", {"start": v(12.6, 9.85) * mm, "end": v(12.48, 10.1) * mm});
            skLineSegment(sketch, "E4140", {"start": v(12.48, 10.1) * mm, "end": v(12.38, 10.3) * mm});
            skLineSegment(sketch, "E4141", {"start": v(12.38, 10.3) * mm, "end": v(12.16, 10.68) * mm});
            skLineSegment(sketch, "E4142", {"start": v(12.16, 10.68) * mm, "end": v(11.37, 11.4) * mm});
            skLineSegment(sketch, "E4143", {"start": v(11.37, 11.4) * mm, "end": v(10.4, 11.92) * mm});
            skLineSegment(sketch, "E4144", {"start": v(10.4, 11.92) * mm, "end": v(8.5, 11.92) * mm});
            skLineSegment(sketch, "E4145", {"start": v(8.5, 11.92) * mm, "end": v(7.62, 11.48) * mm});
            skLineSegment(sketch, "E4146", {"start": v(7.62, 11.48) * mm, "end": v(6.68, 10.62) * mm});
            skLineSegment(sketch, "E4147", {"start": v(6.68, 10.62) * mm, "end": v(6.44, 10.18) * mm});
            skLineSegment(sketch, "E4148", {"start": v(6.44, 10.18) * mm, "end": v(6.33, 9.97) * mm});
            skLineSegment(sketch, "E4149", {"start": v(6.33, 9.97) * mm, "end": v(6.23, 9.71) * mm});
            skLineSegment(sketch, "E4150", {"start": v(6.23, 9.71) * mm, "end": v(6.13, 9.45) * mm});
            skLineSegment(sketch, "E4151", {"start": v(6.13, 9.45) * mm, "end": v(6.05, 9.21) * mm});
            skLineSegment(sketch, "E4152", {"start": v(6.05, 9.21) * mm, "end": v(5.9, 8.68) * mm});
            skLineSegment(sketch, "E4153", {"start": v(5.9, 8.68) * mm, "end": v(5.97, 6.75) * mm});
            skLineSegment(sketch, "E4154", {"start": v(5.97, 6.75) * mm, "end": v(6.5, 5.41) * mm});
            skLineSegment(sketch, "E4155", {"start": v(6.5, 5.41) * mm, "end": v(7.18, 4.64) * mm});
            skLineSegment(sketch, "E4156", {"start": v(7.18, 4.64) * mm, "end": v(8.1, 4.05) * mm});
            skLineSegment(sketch, "E4157", {"start": v(8.1, 4.05) * mm, "end": v(8.62, 3.93) * mm});
            skLineSegment(sketch, "E4158", {"start": v(8.62, 3.93) * mm, "end": v(8.93, 3.87) * mm});
            skLineSegment(sketch, "E4159", {"start": v(8.93, 3.87) * mm, "end": v(9.24, 3.83) * mm});
            skLineSegment(sketch, "E4160", {"start": v(9.24, 3.83) * mm, "end": v(9.55, 3.83) * mm});
            skLineSegment(sketch, "E4161", {"start": v(9.55, 3.83) * mm, "end": v(9.85, 3.85) * mm});
            skLineSegment(sketch, "E4162", {"start": v(9.85, 3.85) * mm, "end": v(10.14, 3.9) * mm});
            skLineSegment(sketch, "E4163", {"start": v(10.14, 3.9) * mm, "end": v(10.44, 3.98) * mm});
            skLineSegment(sketch, "E4164", {"start": v(10.44, 3.98) * mm, "end": v(10.73, 4.1) * mm});
            skLineSegment(sketch, "E4165", {"start": v(10.73, 4.1) * mm, "end": v(11.03, 4.24) * mm});
            skLineSegment(sketch, "E4166", {"start": v(18.7, 4.17) * mm, "end": v(18.91, 4.29) * mm});
            skLineSegment(sketch, "E4167", {"start": v(18.91, 4.29) * mm, "end": v(19.1, 4.4) * mm});
            skLineSegment(sketch, "E4168", {"start": v(19.1, 4.4) * mm, "end": v(19.26, 4.5) * mm});
            skLineSegment(sketch, "E4169", {"start": v(19.26, 4.5) * mm, "end": v(19.4, 4.62) * mm});
            skLineSegment(sketch, "E4170", {"start": v(19.4, 4.62) * mm, "end": v(19.54, 4.74) * mm});
            skLineSegment(sketch, "E4171", {"start": v(19.54, 4.74) * mm, "end": v(19.67, 4.87) * mm});
            skLineSegment(sketch, "E4172", {"start": v(19.67, 4.87) * mm, "end": v(19.8, 5.02) * mm});
            skLineSegment(sketch, "E4173", {"start": v(19.8, 5.02) * mm, "end": v(19.93, 5.19) * mm});
            skLineSegment(sketch, "E4174", {"start": v(19.93, 5.19) * mm, "end": v(20.24, 5.61) * mm});
            skLineSegment(sketch, "E4175", {"start": v(20.24, 5.61) * mm, "end": v(20.7, 6.75) * mm});
            skLineSegment(sketch, "E4176", {"start": v(20.7, 6.75) * mm, "end": v(20.8, 8.6) * mm});
            skLineSegment(sketch, "E4177", {"start": v(20.8, 8.6) * mm, "end": v(20.6, 9.26) * mm});
            skLineSegment(sketch, "E4178", {"start": v(20.6, 9.26) * mm, "end": v(20.5, 9.55) * mm});
            skLineSegment(sketch, "E4179", {"start": v(20.5, 9.55) * mm, "end": v(20.4, 9.84) * mm});
            skLineSegment(sketch, "E4180", {"start": v(20.4, 9.84) * mm, "end": v(20.28, 10.1) * mm});
            skLineSegment(sketch, "E4181", {"start": v(20.28, 10.1) * mm, "end": v(20.19, 10.29) * mm});
            skLineSegment(sketch, "E4182", {"start": v(20.19, 10.29) * mm, "end": v(19.98, 10.65) * mm});
            skLineSegment(sketch, "E4183", {"start": v(19.98, 10.65) * mm, "end": v(19.06, 11.52) * mm});
            skLineSegment(sketch, "E4184", {"start": v(19.06, 11.52) * mm, "end": v(18.64, 11.7) * mm});
            skLineSegment(sketch, "E4185", {"start": v(18.64, 11.7) * mm, "end": v(18.44, 11.77) * mm});
            skLineSegment(sketch, "E4186", {"start": v(18.44, 11.77) * mm, "end": v(18.2, 11.84) * mm});
            skLineSegment(sketch, "E4187", {"start": v(18.2, 11.84) * mm, "end": v(17.94, 11.9) * mm});
            skLineSegment(sketch, "E4188", {"start": v(17.94, 11.9) * mm, "end": v(17.71, 11.95) * mm});
            skLineSegment(sketch, "E4189", {"start": v(17.71, 11.95) * mm, "end": v(17.2, 12.04) * mm});
            skLineSegment(sketch, "E4190", {"start": v(17.2, 12.04) * mm, "end": v(16.2, 11.86) * mm});
            skLineSegment(sketch, "E4191", {"start": v(16.2, 11.86) * mm, "end": v(15.15, 11.3) * mm});
            skLineSegment(sketch, "E4192", {"start": v(15.15, 11.3) * mm, "end": v(14.35, 10.41) * mm});
            skLineSegment(sketch, "E4193", {"start": v(14.35, 10.41) * mm, "end": v(14.12, 9.92) * mm});
            skLineSegment(sketch, "E4194", {"start": v(14.12, 9.92) * mm, "end": v(14.02, 9.7) * mm});
            skLineSegment(sketch, "E4195", {"start": v(14.02, 9.7) * mm, "end": v(13.93, 9.44) * mm});
            skLineSegment(sketch, "E4196", {"start": v(13.93, 9.44) * mm, "end": v(13.84, 9.18) * mm});
            skLineSegment(sketch, "E4197", {"start": v(13.84, 9.18) * mm, "end": v(13.79, 8.96) * mm});
            skLineSegment(sketch, "E4198", {"start": v(13.79, 8.96) * mm, "end": v(13.68, 8.48) * mm});
            skLineSegment(sketch, "E4199", {"start": v(13.68, 8.48) * mm, "end": v(13.77, 6.75) * mm});
            skLineSegment(sketch, "E4200", {"start": v(13.77, 6.75) * mm, "end": v(14.36, 5.35) * mm});
            skLineSegment(sketch, "E4201", {"start": v(14.36, 5.35) * mm, "end": v(15.14, 4.48) * mm});
            skLineSegment(sketch, "E4202", {"start": v(15.14, 4.48) * mm, "end": v(16.1, 4) * mm});
            skLineSegment(sketch, "E4203", {"start": v(16.1, 4) * mm, "end": v(16.6, 3.9) * mm});
            skLineSegment(sketch, "E4204", {"start": v(16.6, 3.9) * mm, "end": v(16.89, 3.85) * mm});
            skLineSegment(sketch, "E4205", {"start": v(16.89, 3.85) * mm, "end": v(17.16, 3.83) * mm});
            skLineSegment(sketch, "E4206", {"start": v(17.16, 3.83) * mm, "end": v(17.43, 3.83) * mm});
            skLineSegment(sketch, "E4207", {"start": v(17.43, 3.83) * mm, "end": v(17.7, 3.85) * mm});
            skLineSegment(sketch, "E4208", {"start": v(17.7, 3.85) * mm, "end": v(17.95, 3.9) * mm});
            skLineSegment(sketch, "E4209", {"start": v(17.95, 3.9) * mm, "end": v(18.2, 3.97) * mm});
            skLineSegment(sketch, "E4210", {"start": v(18.2, 3.97) * mm, "end": v(18.45, 4.06) * mm});
            skLineSegment(sketch, "E4211", {"start": v(18.45, 4.06) * mm, "end": v(18.7, 4.17) * mm});
            skLineSegment(sketch, "E4212", {"start": v(-21.05, 5.07) * mm, "end": v(-20.98, 5.28) * mm});
            skLineSegment(sketch, "E4213", {"start": v(-20.98, 5.28) * mm, "end": v(-21.15, 5.22) * mm});
            skLineSegment(sketch, "E4214", {"start": v(-21.15, 5.22) * mm, "end": v(-21.5, 5.1) * mm});
            skLineSegment(sketch, "E4215", {"start": v(-21.5, 5.1) * mm, "end": v(-22.09, 4.93) * mm});
            skLineSegment(sketch, "E4216", {"start": v(-22.09, 4.93) * mm, "end": v(-22.85, 4.7) * mm});
            skLineSegment(sketch, "E4217", {"start": v(-22.85, 4.7) * mm, "end": v(-23.68, 4.67) * mm});
            skLineSegment(sketch, "E4218", {"start": v(-23.68, 4.67) * mm, "end": v(-23.7, 11.92) * mm});
            skLineSegment(sketch, "E4219", {"start": v(-23.7, 11.92) * mm, "end": v(-24.85, 11.97) * mm});
            skLineSegment(sketch, "E4220", {"start": v(-24.85, 11.97) * mm, "end": v(-24.8, 4.69) * mm});
            skLineSegment(sketch, "E4221", {"start": v(-24.8, 4.69) * mm, "end": v(-24.97, 3.9) * mm});
            skLineSegment(sketch, "E4222", {"start": v(-24.97, 3.9) * mm, "end": v(-21.47, 3.9) * mm});
            skLineSegment(sketch, "E4223", {"start": v(-21.47, 3.9) * mm, "end": v(-21.3, 4.37) * mm});
            skLineSegment(sketch, "E4224", {"start": v(-21.3, 4.37) * mm, "end": v(-21.05, 5.07) * mm});
            skLineSegment(sketch, "E4225", {"start": v(-19, 7.98) * mm, "end": v(-19, 11.37) * mm});
            skLineSegment(sketch, "E4226", {"start": v(-19, 11.37) * mm, "end": v(-18.84, 11.97) * mm});
            skLineSegment(sketch, "E4227", {"start": v(-18.84, 11.97) * mm, "end": v(-20.14, 11.92) * mm});
            skLineSegment(sketch, "E4228", {"start": v(-20.14, 11.92) * mm, "end": v(-20.05, 11.1) * mm});
            skLineSegment(sketch, "E4229", {"start": v(-20.05, 11.1) * mm, "end": v(-20.05, 4.85) * mm});
            skLineSegment(sketch, "E4230", {"start": v(-20.05, 4.85) * mm, "end": v(-20.18, 3.9) * mm});
            skLineSegment(sketch, "E4231", {"start": v(-20.18, 3.9) * mm, "end": v(-18.85, 3.9) * mm});
            skLineSegment(sketch, "E4232", {"start": v(-18.85, 3.9) * mm, "end": v(-19, 4.58) * mm});
            skLineSegment(sketch, "E4233", {"start": v(-19, 4.58) * mm, "end": v(-19, 7.98) * mm});
            skLineSegment(sketch, "E4234", {"start": v(-13.34, 6.04) * mm, "end": v(-12.01, 9.42) * mm});
            skLineSegment(sketch, "E4235", {"start": v(-12.01, 9.42) * mm, "end": v(-11.25, 11.32) * mm});
            skLineSegment(sketch, "E4236", {"start": v(-11.25, 11.32) * mm, "end": v(-11.1, 11.68) * mm});
            skLineSegment(sketch, "E4237", {"start": v(-11.1, 11.68) * mm, "end": v(-11.05, 11.82) * mm});
            skLineSegment(sketch, "E4238", {"start": v(-11.05, 11.82) * mm, "end": v(-11.03, 11.89) * mm});
            skLineSegment(sketch, "E4239", {"start": v(-11.03, 11.89) * mm, "end": v(-11.03, 11.97) * mm});
            skLineSegment(sketch, "E4240", {"start": v(-11.03, 11.97) * mm, "end": v(-12.53, 11.92) * mm});
            skLineSegment(sketch, "E4241", {"start": v(-12.53, 11.92) * mm, "end": v(-12.65, 11.07) * mm});
            skLineSegment(sketch, "E4242", {"start": v(-12.65, 11.07) * mm, "end": v(-14.43, 6.07) * mm});
            skLineSegment(sketch, "E4243", {"start": v(-14.43, 6.07) * mm, "end": v(-14.7, 6.07) * mm});
            skLineSegment(sketch, "E4244", {"start": v(-14.7, 6.07) * mm, "end": v(-16.47, 11.28) * mm});
            skLineSegment(sketch, "E4245", {"start": v(-16.47, 11.28) * mm, "end": v(-16.53, 11.92) * mm});
            skLineSegment(sketch, "E4246", {"start": v(-16.53, 11.92) * mm, "end": v(-17.15, 11.94) * mm});
            skLineSegment(sketch, "E4247", {"start": v(-17.15, 11.94) * mm, "end": v(-17.4, 11.95) * mm});
            skLineSegment(sketch, "E4248", {"start": v(-17.4, 11.95) * mm, "end": v(-17.62, 11.95) * mm});
            skLineSegment(sketch, "E4249", {"start": v(-17.62, 11.95) * mm, "end": v(-17.8, 11.94) * mm});
            skLineSegment(sketch, "E4250", {"start": v(-17.8, 11.94) * mm, "end": v(-17.9, 11.92) * mm});
            skLineSegment(sketch, "E4251", {"start": v(-17.9, 11.92) * mm, "end": v(-18.03, 11.87) * mm});
            skLineSegment(sketch, "E4252", {"start": v(-18.03, 11.87) * mm, "end": v(-17.91, 11.73) * mm});
            skLineSegment(sketch, "E4253", {"start": v(-17.91, 11.73) * mm, "end": v(-17.82, 11.6) * mm});
            skLineSegment(sketch, "E4254", {"start": v(-17.82, 11.6) * mm, "end": v(-17.8, 11.53) * mm});
            skLineSegment(sketch, "E4255", {"start": v(-17.8, 11.53) * mm, "end": v(-17.78, 11.48) * mm});
            skLineSegment(sketch, "E4256", {"start": v(-17.78, 11.48) * mm, "end": v(-16.67, 8.38) * mm});
            skLineSegment(sketch, "E4257", {"start": v(-16.67, 8.38) * mm, "end": v(-15.3, 4.64) * mm});
            skLineSegment(sketch, "E4258", {"start": v(-15.3, 4.64) * mm, "end": v(-15, 3.9) * mm});
            skLineSegment(sketch, "E4259", {"start": v(-15, 3.9) * mm, "end": v(-14.22, 3.9) * mm});
            skLineSegment(sketch, "E4260", {"start": v(-14.22, 3.9) * mm, "end": v(-14.12, 4.05) * mm});
            skLineSegment(sketch, "E4261", {"start": v(-14.12, 4.05) * mm, "end": v(-13.34, 6.04) * mm});
            skLineSegment(sketch, "E4262", {"start": v(-5.9, 5.05) * mm, "end": v(-5.92, 5.05) * mm});
            skLineSegment(sketch, "E4263", {"start": v(-5.92, 5.05) * mm, "end": v(-5.95, 5.05) * mm});
            skLineSegment(sketch, "E4264", {"start": v(-5.95, 5.05) * mm, "end": v(-6.06, 5.04) * mm});
            skLineSegment(sketch, "E4265", {"start": v(-6.06, 5.04) * mm, "end": v(-6.21, 5) * mm});
            skLineSegment(sketch, "E4266", {"start": v(-6.21, 5) * mm, "end": v(-6.38, 4.95) * mm});
            skLineSegment(sketch, "E4267", {"start": v(-6.38, 4.95) * mm, "end": v(-6.64, 4.88) * mm});
            skLineSegment(sketch, "E4268", {"start": v(-6.64, 4.88) * mm, "end": v(-6.9, 4.81) * mm});
            skLineSegment(sketch, "E4269", {"start": v(-6.9, 4.81) * mm, "end": v(-7.14, 4.75) * mm});
            skLineSegment(sketch, "E4270", {"start": v(-7.14, 4.75) * mm, "end": v(-7.4, 4.7) * mm});
            skLineSegment(sketch, "E4271", {"start": v(-7.4, 4.7) * mm, "end": v(-7.63, 4.67) * mm});
            skLineSegment(sketch, "E4272", {"start": v(-7.63, 4.67) * mm, "end": v(-7.87, 4.64) * mm});
            skLineSegment(sketch, "E4273", {"start": v(-7.87, 4.64) * mm, "end": v(-8.1, 4.63) * mm});
            skLineSegment(sketch, "E4274", {"start": v(-8.1, 4.63) * mm, "end": v(-8.32, 4.62) * mm});
            skLineSegment(sketch, "E4275", {"start": v(-8.32, 4.62) * mm, "end": v(-8.86, 4.62) * mm});
            skLineSegment(sketch, "E4276", {"start": v(-8.86, 4.62) * mm, "end": v(-8.86, 7.6) * mm});
            skLineSegment(sketch, "E4277", {"start": v(-8.86, 7.6) * mm, "end": v(-8.69, 7.7) * mm});
            skLineSegment(sketch, "E4278", {"start": v(-8.69, 7.7) * mm, "end": v(-8.03, 7.56) * mm});
            skLineSegment(sketch, "E4279", {"start": v(-8.03, 7.56) * mm, "end": v(-7.5, 7.45) * mm});
            skLineSegment(sketch, "E4280", {"start": v(-7.5, 7.45) * mm, "end": v(-7.18, 7.4) * mm});
            skLineSegment(sketch, "E4281", {"start": v(-7.18, 7.4) * mm, "end": v(-7, 7.39) * mm});
            skLineSegment(sketch, "E4282", {"start": v(-7, 7.39) * mm, "end": v(-6.5, 8.34) * mm});
            skLineSegment(sketch, "E4283", {"start": v(-6.5, 8.34) * mm, "end": v(-8.86, 8.34) * mm});
            skLineSegment(sketch, "E4284", {"start": v(-8.86, 8.34) * mm, "end": v(-8.81, 11.2) * mm});
            skLineSegment(sketch, "E4285", {"start": v(-8.81, 11.2) * mm, "end": v(-7.82, 11.16) * mm});
            skLineSegment(sketch, "E4286", {"start": v(-7.82, 11.16) * mm, "end": v(-6.79, 10.8) * mm});
            skLineSegment(sketch, "E4287", {"start": v(-6.79, 10.8) * mm, "end": v(-6.7, 10.9) * mm});
            skLineSegment(sketch, "E4288", {"start": v(-6.7, 10.9) * mm, "end": v(-6.6, 11.1) * mm});
            skLineSegment(sketch, "E4289", {"start": v(-6.6, 11.1) * mm, "end": v(-6.44, 11.43) * mm});
            skLineSegment(sketch, "E4290", {"start": v(-6.44, 11.43) * mm, "end": v(-6.3, 11.75) * mm});
            skLineSegment(sketch, "E4291", {"start": v(-6.3, 11.75) * mm, "end": v(-6.25, 11.87) * mm});
            skLineSegment(sketch, "E4292", {"start": v(-6.25, 11.87) * mm, "end": v(-6.23, 11.93) * mm});
            skLineSegment(sketch, "E4293", {"start": v(-6.23, 11.93) * mm, "end": v(-6.23, 11.96) * mm});
            skLineSegment(sketch, "E4294", {"start": v(-6.23, 11.96) * mm, "end": v(-10.03, 11.96) * mm});
            skLineSegment(sketch, "E4295", {"start": v(-10.03, 11.96) * mm, "end": v(-9.9, 11.28) * mm});
            skLineSegment(sketch, "E4296", {"start": v(-9.9, 11.28) * mm, "end": v(-9.9, 4.58) * mm});
            skLineSegment(sketch, "E4297", {"start": v(-9.9, 4.58) * mm, "end": v(-10.03, 3.9) * mm});
            skLineSegment(sketch, "E4298", {"start": v(-10.03, 3.9) * mm, "end": v(-6.28, 3.9) * mm});
            skLineSegment(sketch, "E4299", {"start": v(-6.28, 3.9) * mm, "end": v(-6.06, 4.45) * mm});
            skLineSegment(sketch, "E4300", {"start": v(-6.06, 4.45) * mm, "end": v(-5.99, 4.67) * mm});
            skLineSegment(sketch, "E4301", {"start": v(-5.99, 4.67) * mm, "end": v(-5.93, 4.85) * mm});
            skLineSegment(sketch, "E4302", {"start": v(-5.93, 4.85) * mm, "end": v(-5.9, 4.98) * mm});
            skLineSegment(sketch, "E4303", {"start": v(-5.9, 4.98) * mm, "end": v(-5.9, 5.03) * mm});
            skLineSegment(sketch, "E4304", {"start": v(-5.9, 5.03) * mm, "end": v(-5.9, 5.05) * mm});
            skLineSegment(sketch, "E4305", {"start": v(-3.66, 7.37) * mm, "end": v(-3.52, 7.42) * mm});
            skLineSegment(sketch, "E4306", {"start": v(-3.52, 7.42) * mm, "end": v(-2.65, 6.12) * mm});
            skLineSegment(sketch, "E4307", {"start": v(-2.65, 6.12) * mm, "end": v(-1.02, 4.41) * mm});
            skLineSegment(sketch, "E4308", {"start": v(-1.02, 4.41) * mm, "end": v(-0.21, 3.9) * mm});
            skLineSegment(sketch, "E4309", {"start": v(-0.21, 3.9) * mm, "end": v(0.58, 3.9) * mm});
            skLineSegment(sketch, "E4310", {"start": v(0.58, 3.9) * mm, "end": v(-0.84, 5.3) * mm});
            skLineSegment(sketch, "E4311", {"start": v(-0.84, 5.3) * mm, "end": v(-2.07, 7.02) * mm});
            skLineSegment(sketch, "E4312", {"start": v(-2.07, 7.02) * mm, "end": v(-2.17, 7.42) * mm});
            skLineSegment(sketch, "E4313", {"start": v(-2.17, 7.42) * mm, "end": v(-0.99, 8.56) * mm});
            skLineSegment(sketch, "E4314", {"start": v(-0.99, 8.56) * mm, "end": v(-0.9, 8.93) * mm});
            skLineSegment(sketch, "E4315", {"start": v(-0.9, 8.93) * mm, "end": v(-0.85, 9.1) * mm});
            skLineSegment(sketch, "E4316", {"start": v(-0.85, 9.1) * mm, "end": v(-0.82, 9.31) * mm});
            skLineSegment(sketch, "E4317", {"start": v(-0.82, 9.31) * mm, "end": v(-0.8, 9.53) * mm});
            skLineSegment(sketch, "E4318", {"start": v(-0.8, 9.53) * mm, "end": v(-0.8, 9.72) * mm});
            skLineSegment(sketch, "E4319", {"start": v(-0.8, 9.72) * mm, "end": v(-0.8, 10.16) * mm});
            skLineSegment(sketch, "E4320", {"start": v(-0.8, 10.16) * mm, "end": v(-1.15, 10.85) * mm});
            skLineSegment(sketch, "E4321", {"start": v(-1.15, 10.85) * mm, "end": v(-1.99, 11.6) * mm});
            skLineSegment(sketch, "E4322", {"start": v(-1.99, 11.6) * mm, "end": v(-2.92, 11.9) * mm});
            skLineSegment(sketch, "E4323", {"start": v(-2.92, 11.9) * mm, "end": v(-4.88, 11.92) * mm});
            skLineSegment(sketch, "E4324", {"start": v(-4.88, 11.92) * mm, "end": v(-4.92, 3.9) * mm});
            skLineSegment(sketch, "E4325", {"start": v(-4.92, 3.9) * mm, "end": v(-3.74, 3.9) * mm});
            skLineSegment(sketch, "E4326", {"start": v(-3.74, 3.9) * mm, "end": v(-3.8, 7.31) * mm});
            skLineSegment(sketch, "E4327", {"start": v(-3.8, 7.31) * mm, "end": v(-3.66, 7.37) * mm});
            skLineSegment(sketch, "E4328", {"start": v(3.42, 7.48) * mm, "end": v(4.06, 7.58) * mm});
            skLineSegment(sketch, "E4329", {"start": v(4.06, 7.58) * mm, "end": v(4.3, 7.74) * mm});
            skLineSegment(sketch, "E4330", {"start": v(4.3, 7.74) * mm, "end": v(4.4, 7.82) * mm});
            skLineSegment(sketch, "E4331", {"start": v(4.4, 7.82) * mm, "end": v(4.51, 7.93) * mm});
            skLineSegment(sketch, "E4332", {"start": v(4.51, 7.93) * mm, "end": v(4.63, 8.05) * mm});
            skLineSegment(sketch, "E4333", {"start": v(4.63, 8.05) * mm, "end": v(4.74, 8.2) * mm});
            skLineSegment(sketch, "E4334", {"start": v(4.74, 8.2) * mm, "end": v(4.85, 8.35) * mm});
            skLineSegment(sketch, "E4335", {"start": v(4.85, 8.35) * mm, "end": v(4.94, 8.51) * mm});
            skLineSegment(sketch, "E4336", {"start": v(4.94, 8.51) * mm, "end": v(5.03, 8.67) * mm});
            skLineSegment(sketch, "E4337", {"start": v(5.03, 8.67) * mm, "end": v(5.1, 8.82) * mm});
            skLineSegment(sketch, "E4338", {"start": v(5.1, 8.82) * mm, "end": v(5.19, 9.07) * mm});
            skLineSegment(sketch, "E4339", {"start": v(5.19, 9.07) * mm, "end": v(5.19, 10.25) * mm});
            skLineSegment(sketch, "E4340", {"start": v(5.19, 10.25) * mm, "end": v(5.06, 10.54) * mm});
            skLineSegment(sketch, "E4341", {"start": v(5.06, 10.54) * mm, "end": v(5, 10.69) * mm});
            skLineSegment(sketch, "E4342", {"start": v(5, 10.69) * mm, "end": v(4.89, 10.85) * mm});
            skLineSegment(sketch, "E4343", {"start": v(4.89, 10.85) * mm, "end": v(4.77, 11.03) * mm});
            skLineSegment(sketch, "E4344", {"start": v(4.77, 11.03) * mm, "end": v(4.64, 11.18) * mm});
            skLineSegment(sketch, "E4345", {"start": v(4.64, 11.18) * mm, "end": v(4.34, 11.52) * mm});
            skLineSegment(sketch, "E4346", {"start": v(4.34, 11.52) * mm, "end": v(3.61, 11.9) * mm});
            skLineSegment(sketch, "E4347", {"start": v(3.61, 11.9) * mm, "end": v(1.64, 11.92) * mm});
            skLineSegment(sketch, "E4348", {"start": v(1.64, 11.92) * mm, "end": v(1.66, 4.49) * mm});
            skLineSegment(sketch, "E4349", {"start": v(1.66, 4.49) * mm, "end": v(1.49, 3.9) * mm});
            skLineSegment(sketch, "E4350", {"start": v(1.49, 3.9) * mm, "end": v(2.79, 3.9) * mm});
            skLineSegment(sketch, "E4351", {"start": v(2.79, 3.9) * mm, "end": v(2.79, 7.39) * mm});
            skLineSegment(sketch, "E4352", {"start": v(2.79, 7.39) * mm, "end": v(3.42, 7.48) * mm});
            skLineSegment(sketch, "E4353", {"start": v(25.56, 5.2) * mm, "end": v(25.48, 5.2) * mm});
            skLineSegment(sketch, "E4354", {"start": v(25.48, 5.2) * mm, "end": v(25.28, 5.16) * mm});
            skLineSegment(sketch, "E4355", {"start": v(25.28, 5.16) * mm, "end": v(24.63, 4.98) * mm});
            skLineSegment(sketch, "E4356", {"start": v(24.63, 4.98) * mm, "end": v(23.72, 4.7) * mm});
            skLineSegment(sketch, "E4357", {"start": v(23.72, 4.7) * mm, "end": v(22.9, 4.67) * mm});
            skLineSegment(sketch, "E4358", {"start": v(22.9, 4.67) * mm, "end": v(22.87, 11.92) * mm});
            skLineSegment(sketch, "E4359", {"start": v(22.87, 11.92) * mm, "end": v(21.73, 11.97) * mm});
            skLineSegment(sketch, "E4360", {"start": v(21.73, 11.97) * mm, "end": v(21.78, 4.69) * mm});
            skLineSegment(sketch, "E4361", {"start": v(21.78, 4.69) * mm, "end": v(21.61, 3.9) * mm});
            skLineSegment(sketch, "E4362", {"start": v(21.61, 3.9) * mm, "end": v(25.1, 3.9) * mm});
            skLineSegment(sketch, "E4363", {"start": v(25.1, 3.9) * mm, "end": v(25.6, 5.18) * mm});
            skLineSegment(sketch, "E4364", {"start": v(25.6, 5.18) * mm, "end": v(25.56, 5.2) * mm});
            skLineSegment(sketch, "E4365", {"start": v(9.75, 4.63) * mm, "end": v(9.88, 4.63) * mm});
            skLineSegment(sketch, "E4366", {"start": v(9.88, 4.63) * mm, "end": v(10.04, 4.65) * mm});
            skLineSegment(sketch, "E4367", {"start": v(10.04, 4.65) * mm, "end": v(10.21, 4.69) * mm});
            skLineSegment(sketch, "E4368", {"start": v(10.21, 4.69) * mm, "end": v(10.37, 4.73) * mm});
            skLineSegment(sketch, "E4369", {"start": v(10.37, 4.73) * mm, "end": v(10.73, 4.83) * mm});
            skLineSegment(sketch, "E4370", {"start": v(10.73, 4.83) * mm, "end": v(11.45, 5.56) * mm});
            skLineSegment(sketch, "E4371", {"start": v(11.45, 5.56) * mm, "end": v(11.66, 6.02) * mm});
            skLineSegment(sketch, "E4372", {"start": v(11.66, 6.02) * mm, "end": v(11.75, 6.24) * mm});
            skLineSegment(sketch, "E4373", {"start": v(11.75, 6.24) * mm, "end": v(11.84, 6.5) * mm});
            skLineSegment(sketch, "E4374", {"start": v(11.84, 6.5) * mm, "end": v(11.92, 6.77) * mm});
            skLineSegment(sketch, "E4375", {"start": v(11.92, 6.77) * mm, "end": v(11.98, 7.02) * mm});
            skLineSegment(sketch, "E4376", {"start": v(11.98, 7.02) * mm, "end": v(12.1, 7.55) * mm});
            skLineSegment(sketch, "E4377", {"start": v(12.1, 7.55) * mm, "end": v(11.97, 8.64) * mm});
            skLineSegment(sketch, "E4378", {"start": v(11.97, 8.64) * mm, "end": v(11.5, 9.83) * mm});
            skLineSegment(sketch, "E4379", {"start": v(11.5, 9.83) * mm, "end": v(10.49, 10.85) * mm});
            skLineSegment(sketch, "E4380", {"start": v(10.49, 10.85) * mm, "end": v(9.44, 11.24) * mm});
            skLineSegment(sketch, "E4381", {"start": v(9.44, 11.24) * mm, "end": v(8.72, 11.24) * mm});
            skLineSegment(sketch, "E4382", {"start": v(8.72, 11.24) * mm, "end": v(8.1, 10.98) * mm});
            skLineSegment(sketch, "E4383", {"start": v(8.1, 10.98) * mm, "end": v(7.4, 10.27) * mm});
            skLineSegment(sketch, "E4384", {"start": v(7.4, 10.27) * mm, "end": v(6.98, 9.38) * mm});
            skLineSegment(sketch, "E4385", {"start": v(6.98, 9.38) * mm, "end": v(6.79, 8.17) * mm});
            skLineSegment(sketch, "E4386", {"start": v(6.79, 8.17) * mm, "end": v(6.99, 6.98) * mm});
            skLineSegment(sketch, "E4387", {"start": v(6.99, 6.98) * mm, "end": v(7.44, 6) * mm});
            skLineSegment(sketch, "E4388", {"start": v(7.44, 6) * mm, "end": v(8.21, 5.15) * mm});
            skLineSegment(sketch, "E4389", {"start": v(8.21, 5.15) * mm, "end": v(8.5, 5) * mm});
            skLineSegment(sketch, "E4390", {"start": v(8.5, 5) * mm, "end": v(8.64, 4.93) * mm});
            skLineSegment(sketch, "E4391", {"start": v(8.64, 4.93) * mm, "end": v(8.8, 4.86) * mm});
            skLineSegment(sketch, "E4392", {"start": v(8.8, 4.86) * mm, "end": v(8.98, 4.8) * mm});
            skLineSegment(sketch, "E4393", {"start": v(8.98, 4.8) * mm, "end": v(9.15, 4.74) * mm});
            skLineSegment(sketch, "E4394", {"start": v(9.15, 4.74) * mm, "end": v(9.32, 4.7) * mm});
            skLineSegment(sketch, "E4395", {"start": v(9.32, 4.7) * mm, "end": v(9.48, 4.66) * mm});
            skLineSegment(sketch, "E4396", {"start": v(9.48, 4.66) * mm, "end": v(9.63, 4.64) * mm});
            skLineSegment(sketch, "E4397", {"start": v(9.63, 4.64) * mm, "end": v(9.75, 4.63) * mm});
            skLineSegment(sketch, "E4398", {"start": v(17.57, 4.63) * mm, "end": v(17.7, 4.63) * mm});
            skLineSegment(sketch, "E4399", {"start": v(17.7, 4.63) * mm, "end": v(17.81, 4.64) * mm});
            skLineSegment(sketch, "E4400", {"start": v(17.81, 4.64) * mm, "end": v(17.93, 4.66) * mm});
            skLineSegment(sketch, "E4401", {"start": v(17.93, 4.66) * mm, "end": v(18.05, 4.7) * mm});
            skLineSegment(sketch, "E4402", {"start": v(18.05, 4.7) * mm, "end": v(18.17, 4.73) * mm});
            skLineSegment(sketch, "E4403", {"start": v(18.17, 4.73) * mm, "end": v(18.28, 4.78) * mm});
            skLineSegment(sketch, "E4404", {"start": v(18.28, 4.78) * mm, "end": v(18.4, 4.83) * mm});
            skLineSegment(sketch, "E4405", {"start": v(18.4, 4.83) * mm, "end": v(18.5, 4.9) * mm});
            skLineSegment(sketch, "E4406", {"start": v(18.5, 4.9) * mm, "end": v(18.61, 4.97) * mm});
            skLineSegment(sketch, "E4407", {"start": v(18.61, 4.97) * mm, "end": v(18.72, 5.05) * mm});
            skLineSegment(sketch, "E4408", {"start": v(18.72, 5.05) * mm, "end": v(18.82, 5.14) * mm});
            skLineSegment(sketch, "E4409", {"start": v(18.82, 5.14) * mm, "end": v(18.92, 5.24) * mm});
            skLineSegment(sketch, "E4410", {"start": v(18.92, 5.24) * mm, "end": v(19.02, 5.35) * mm});
            skLineSegment(sketch, "E4411", {"start": v(19.02, 5.35) * mm, "end": v(19.11, 5.46) * mm});
            skLineSegment(sketch, "E4412", {"start": v(19.11, 5.46) * mm, "end": v(19.3, 5.72) * mm});
            skLineSegment(sketch, "E4413", {"start": v(19.3, 5.72) * mm, "end": v(19.58, 6.17) * mm});
            skLineSegment(sketch, "E4414", {"start": v(19.58, 6.17) * mm, "end": v(19.87, 7.33) * mm});
            skLineSegment(sketch, "E4415", {"start": v(19.87, 7.33) * mm, "end": v(19.87, 8.12) * mm});
            skLineSegment(sketch, "E4416", {"start": v(19.87, 8.12) * mm, "end": v(19.6, 9.18) * mm});
            skLineSegment(sketch, "E4417", {"start": v(19.6, 9.18) * mm, "end": v(19.11, 10.07) * mm});
            skLineSegment(sketch, "E4418", {"start": v(19.11, 10.07) * mm, "end": v(18.73, 10.42) * mm});
            skLineSegment(sketch, "E4419", {"start": v(18.73, 10.42) * mm, "end": v(18.55, 10.57) * mm});
            skLineSegment(sketch, "E4420", {"start": v(18.55, 10.57) * mm, "end": v(18.35, 10.73) * mm});
            skLineSegment(sketch, "E4421", {"start": v(18.35, 10.73) * mm, "end": v(18.14, 10.86) * mm});
            skLineSegment(sketch, "E4422", {"start": v(18.14, 10.86) * mm, "end": v(17.96, 10.97) * mm});
            skLineSegment(sketch, "E4423", {"start": v(17.96, 10.97) * mm, "end": v(17.57, 11.17) * mm});
            skLineSegment(sketch, "E4424", {"start": v(17.57, 11.17) * mm, "end": v(16.55, 11.26) * mm});
            skLineSegment(sketch, "E4425", {"start": v(16.55, 11.26) * mm, "end": v(15.84, 10.93) * mm});
            skLineSegment(sketch, "E4426", {"start": v(15.84, 10.93) * mm, "end": v(15.2, 10.28) * mm});
            skLineSegment(sketch, "E4427", {"start": v(15.2, 10.28) * mm, "end": v(14.8, 9.43) * mm});
            skLineSegment(sketch, "E4428", {"start": v(14.8, 9.43) * mm, "end": v(14.58, 8.18) * mm});
            skLineSegment(sketch, "E4429", {"start": v(14.58, 8.18) * mm, "end": v(14.8, 6.92) * mm});
            skLineSegment(sketch, "E4430", {"start": v(14.8, 6.92) * mm, "end": v(15.23, 6) * mm});
            skLineSegment(sketch, "E4431", {"start": v(15.23, 6) * mm, "end": v(15.56, 5.63) * mm});
            skLineSegment(sketch, "E4432", {"start": v(15.56, 5.63) * mm, "end": v(15.78, 5.42) * mm});
            skLineSegment(sketch, "E4433", {"start": v(15.78, 5.42) * mm, "end": v(16, 5.22) * mm});
            skLineSegment(sketch, "E4434", {"start": v(16, 5.22) * mm, "end": v(16.26, 5.05) * mm});
            skLineSegment(sketch, "E4435", {"start": v(16.26, 5.05) * mm, "end": v(16.51, 4.91) * mm});
            skLineSegment(sketch, "E4436", {"start": v(16.51, 4.91) * mm, "end": v(16.78, 4.8) * mm});
            skLineSegment(sketch, "E4437", {"start": v(16.78, 4.8) * mm, "end": v(17.04, 4.7) * mm});
            skLineSegment(sketch, "E4438", {"start": v(17.04, 4.7) * mm, "end": v(17.17, 4.67) * mm});
            skLineSegment(sketch, "E4439", {"start": v(17.17, 4.67) * mm, "end": v(17.3, 4.65) * mm});
            skLineSegment(sketch, "E4440", {"start": v(17.3, 4.65) * mm, "end": v(17.44, 4.64) * mm});
            skLineSegment(sketch, "E4441", {"start": v(17.44, 4.64) * mm, "end": v(17.57, 4.63) * mm});
            skLineSegment(sketch, "E4442", {"start": v(-14.61, 5.9) * mm, "end": v(-14.58, 5.9) * mm});
            skLineSegment(sketch, "E4443", {"start": v(-14.58, 5.9) * mm, "end": v(-14.57, 5.94) * mm});
            skLineSegment(sketch, "E4444", {"start": v(-14.57, 5.94) * mm, "end": v(-14.58, 5.97) * mm});
            skLineSegment(sketch, "E4445", {"start": v(-14.58, 5.97) * mm, "end": v(-14.61, 5.98) * mm});
            skLineSegment(sketch, "E4446", {"start": v(-14.61, 5.98) * mm, "end": v(-14.65, 5.97) * mm});
            skLineSegment(sketch, "E4447", {"start": v(-14.65, 5.97) * mm, "end": v(-14.66, 5.94) * mm});
            skLineSegment(sketch, "E4448", {"start": v(-14.66, 5.94) * mm, "end": v(-14.65, 5.9) * mm});
            skLineSegment(sketch, "E4449", {"start": v(-14.65, 5.9) * mm, "end": v(-14.61, 5.9) * mm});
            skLineSegment(sketch, "E4450", {"start": v(-3.43, 7.7) * mm, "end": v(-3.18, 7.78) * mm});
            skLineSegment(sketch, "E4451", {"start": v(-3.18, 7.78) * mm, "end": v(-2.95, 7.9) * mm});
            skLineSegment(sketch, "E4452", {"start": v(-2.95, 7.9) * mm, "end": v(-2.7, 8.04) * mm});
            skLineSegment(sketch, "E4453", {"start": v(-2.7, 8.04) * mm, "end": v(-2.44, 8.23) * mm});
            skLineSegment(sketch, "E4454", {"start": v(-2.44, 8.23) * mm, "end": v(-2.13, 8.45) * mm});
            skLineSegment(sketch, "E4455", {"start": v(-2.13, 8.45) * mm, "end": v(-1.8, 9.2) * mm});
            skLineSegment(sketch, "E4456", {"start": v(-1.8, 9.2) * mm, "end": v(-1.8, 9.8) * mm});
            skLineSegment(sketch, "E4457", {"start": v(-1.8, 9.8) * mm, "end": v(-1.93, 10.13) * mm});
            skLineSegment(sketch, "E4458", {"start": v(-1.93, 10.13) * mm, "end": v(-2, 10.28) * mm});
            skLineSegment(sketch, "E4459", {"start": v(-2, 10.28) * mm, "end": v(-2.1, 10.44) * mm});
            skLineSegment(sketch, "E4460", {"start": v(-2.1, 10.44) * mm, "end": v(-2.2, 10.59) * mm});
            skLineSegment(sketch, "E4461", {"start": v(-2.2, 10.59) * mm, "end": v(-2.3, 10.71) * mm});
            skLineSegment(sketch, "E4462", {"start": v(-2.3, 10.71) * mm, "end": v(-2.54, 10.95) * mm});
            skLineSegment(sketch, "E4463", {"start": v(-2.54, 10.95) * mm, "end": v(-3.5, 11.35) * mm});
            skLineSegment(sketch, "E4464", {"start": v(-3.5, 11.35) * mm, "end": v(-3.78, 11.24) * mm});
            skLineSegment(sketch, "E4465", {"start": v(-3.78, 11.24) * mm, "end": v(-3.78, 7.9) * mm});
            skLineSegment(sketch, "E4466", {"start": v(-3.78, 7.9) * mm, "end": v(-3.68, 7.63) * mm});
            skLineSegment(sketch, "E4467", {"start": v(-3.68, 7.63) * mm, "end": v(-3.43, 7.7) * mm});
            skLineSegment(sketch, "E4468", {"start": v(3.08, 7.84) * mm, "end": v(3.42, 7.98) * mm});
            skLineSegment(sketch, "E4469", {"start": v(3.42, 7.98) * mm, "end": v(4, 8.64) * mm});
            skLineSegment(sketch, "E4470", {"start": v(4, 8.64) * mm, "end": v(4.1, 8.96) * mm});
            skLineSegment(sketch, "E4471", {"start": v(4.1, 8.96) * mm, "end": v(4.13, 9.12) * mm});
            skLineSegment(sketch, "E4472", {"start": v(4.13, 9.12) * mm, "end": v(4.16, 9.3) * mm});
            skLineSegment(sketch, "E4473", {"start": v(4.16, 9.3) * mm, "end": v(4.18, 9.47) * mm});
            skLineSegment(sketch, "E4474", {"start": v(4.18, 9.47) * mm, "end": v(4.2, 9.62) * mm});
            skLineSegment(sketch, "E4475", {"start": v(4.2, 9.62) * mm, "end": v(4.2, 9.95) * mm});
            skLineSegment(sketch, "E4476", {"start": v(4.2, 9.95) * mm, "end": v(3.85, 10.75) * mm});
            skLineSegment(sketch, "E4477", {"start": v(3.85, 10.75) * mm, "end": v(3.52, 11.04) * mm});
            skLineSegment(sketch, "E4478", {"start": v(3.52, 11.04) * mm, "end": v(3.38, 11.15) * mm});
            skLineSegment(sketch, "E4479", {"start": v(3.38, 11.15) * mm, "end": v(3.26, 11.24) * mm});
            skLineSegment(sketch, "E4480", {"start": v(3.26, 11.24) * mm, "end": v(3.17, 11.3) * mm});
            skLineSegment(sketch, "E4481", {"start": v(3.17, 11.3) * mm, "end": v(3.1, 11.33) * mm});
            skLineSegment(sketch, "E4482", {"start": v(3.1, 11.33) * mm, "end": v(3, 11.34) * mm});
            skLineSegment(sketch, "E4483", {"start": v(3, 11.34) * mm, "end": v(2.88, 11.38) * mm});
            skLineSegment(sketch, "E4484", {"start": v(2.88, 11.38) * mm, "end": v(2.74, 11.44) * mm});
            skLineSegment(sketch, "E4485", {"start": v(2.74, 11.44) * mm, "end": v(2.74, 7.7) * mm});
            skLineSegment(sketch, "E4486", {"start": v(2.74, 7.7) * mm, "end": v(3.08, 7.84) * mm});
            skLineSegment(sketch, "E4487", {"start": v(-14.93, 17.64) * mm, "end": v(-14.45, 17.67) * mm});
            skLineSegment(sketch, "E4488", {"start": v(-14.45, 17.67) * mm, "end": v(-13.92, 17.7) * mm});
            skLineSegment(sketch, "E4489", {"start": v(-13.92, 17.7) * mm, "end": v(-13.4, 17.76) * mm});
            skLineSegment(sketch, "E4490", {"start": v(-13.4, 17.76) * mm, "end": v(-12.94, 17.81) * mm});
            skLineSegment(sketch, "E4491", {"start": v(-12.94, 17.81) * mm, "end": v(-12, 17.94) * mm});
            skLineSegment(sketch, "E4492", {"start": v(-12, 17.94) * mm, "end": v(-9.96, 18.48) * mm});
            skLineSegment(sketch, "E4493", {"start": v(-9.96, 18.48) * mm, "end": v(-8.89, 18.9) * mm});
            skLineSegment(sketch, "E4494", {"start": v(-8.89, 18.9) * mm, "end": v(-8.39, 19.1) * mm});
            skLineSegment(sketch, "E4495", {"start": v(-8.39, 19.1) * mm, "end": v(-7.81, 19.36) * mm});
            skLineSegment(sketch, "E4496", {"start": v(-7.81, 19.36) * mm, "end": v(-7.24, 19.63) * mm});
            skLineSegment(sketch, "E4497", {"start": v(-7.24, 19.63) * mm, "end": v(-6.73, 19.88) * mm});
            skLineSegment(sketch, "E4498", {"start": v(-6.73, 19.88) * mm, "end": v(-5.64, 20.45) * mm});
            skLineSegment(sketch, "E4499", {"start": v(-5.64, 20.45) * mm, "end": v(-4.4, 21.23) * mm});
            skLineSegment(sketch, "E4500", {"start": v(-4.4, 21.23) * mm, "end": v(-4.64, 21.38) * mm});
            skLineSegment(sketch, "E4501", {"start": v(-4.64, 21.38) * mm, "end": v(-26.97, 21.39) * mm});
            skLineSegment(sketch, "E4502", {"start": v(-26.97, 21.39) * mm, "end": v(-27.1, 21.17) * mm});
            skLineSegment(sketch, "E4503", {"start": v(-27.1, 21.17) * mm, "end": v(-26.8, 20.92) * mm});
            skLineSegment(sketch, "E4504", {"start": v(-26.8, 20.92) * mm, "end": v(-26.6, 20.77) * mm});
            skLineSegment(sketch, "E4505", {"start": v(-26.6, 20.77) * mm, "end": v(-26.35, 20.6) * mm});
            skLineSegment(sketch, "E4506", {"start": v(-26.35, 20.6) * mm, "end": v(-26.06, 20.44) * mm});
            skLineSegment(sketch, "E4507", {"start": v(-26.06, 20.44) * mm, "end": v(-25.73, 20.26) * mm});
            skLineSegment(sketch, "E4508", {"start": v(-25.73, 20.26) * mm, "end": v(-25.35, 20.08) * mm});
            skLineSegment(sketch, "E4509", {"start": v(-25.35, 20.08) * mm, "end": v(-24.95, 19.89) * mm});
            skLineSegment(sketch, "E4510", {"start": v(-24.95, 19.89) * mm, "end": v(-24.53, 19.7) * mm});
            skLineSegment(sketch, "E4511", {"start": v(-24.53, 19.7) * mm, "end": v(-24.07, 19.5) * mm});
            skLineSegment(sketch, "E4512", {"start": v(-24.07, 19.5) * mm, "end": v(-23.6, 19.32) * mm});
            skLineSegment(sketch, "E4513", {"start": v(-23.6, 19.32) * mm, "end": v(-23.13, 19.14) * mm});
            skLineSegment(sketch, "E4514", {"start": v(-23.13, 19.14) * mm, "end": v(-22.64, 18.96) * mm});
            skLineSegment(sketch, "E4515", {"start": v(-22.64, 18.96) * mm, "end": v(-22.14, 18.8) * mm});
            skLineSegment(sketch, "E4516", {"start": v(-22.14, 18.8) * mm, "end": v(-21.65, 18.63) * mm});
            skLineSegment(sketch, "E4517", {"start": v(-21.65, 18.63) * mm, "end": v(-21.17, 18.48) * mm});
            skLineSegment(sketch, "E4518", {"start": v(-21.17, 18.48) * mm, "end": v(-20.7, 18.34) * mm});
            skLineSegment(sketch, "E4519", {"start": v(-20.7, 18.34) * mm, "end": v(-20.23, 18.22) * mm});
            skLineSegment(sketch, "E4520", {"start": v(-20.23, 18.22) * mm, "end": v(-19.14, 17.95) * mm});
            skLineSegment(sketch, "E4521", {"start": v(-19.14, 17.95) * mm, "end": v(-17.06, 17.68) * mm});
            skLineSegment(sketch, "E4522", {"start": v(-17.06, 17.68) * mm, "end": v(-16.52, 17.64) * mm});
            skLineSegment(sketch, "E4523", {"start": v(-16.52, 17.64) * mm, "end": v(-16.22, 17.63) * mm});
            skLineSegment(sketch, "E4524", {"start": v(-16.22, 17.63) * mm, "end": v(-15.83, 17.63) * mm});
            skLineSegment(sketch, "E4525", {"start": v(-15.83, 17.63) * mm, "end": v(-15.38, 17.63) * mm});
            skLineSegment(sketch, "E4526", {"start": v(-15.38, 17.63) * mm, "end": v(-14.93, 17.64) * mm});
            skLineSegment(sketch, "E4527", {"start": v(15.11, 17.6) * mm, "end": v(16.7, 17.68) * mm});
            skLineSegment(sketch, "E4528", {"start": v(16.7, 17.68) * mm, "end": v(18.01, 17.77) * mm});
            skLineSegment(sketch, "E4529", {"start": v(18.01, 17.77) * mm, "end": v(19.14, 18) * mm});
            skLineSegment(sketch, "E4530", {"start": v(19.14, 18) * mm, "end": v(19.7, 18.12) * mm});
            skLineSegment(sketch, "E4531", {"start": v(19.7, 18.12) * mm, "end": v(20.25, 18.24) * mm});
            skLineSegment(sketch, "E4532", {"start": v(20.25, 18.24) * mm, "end": v(20.78, 18.38) * mm});
            skLineSegment(sketch, "E4533", {"start": v(20.78, 18.38) * mm, "end": v(21.3, 18.53) * mm});
            skLineSegment(sketch, "E4534", {"start": v(21.3, 18.53) * mm, "end": v(21.82, 18.69) * mm});
            skLineSegment(sketch, "E4535", {"start": v(21.82, 18.69) * mm, "end": v(22.35, 18.87) * mm});
            skLineSegment(sketch, "E4536", {"start": v(22.35, 18.87) * mm, "end": v(22.9, 19.06) * mm});
            skLineSegment(sketch, "E4537", {"start": v(22.9, 19.06) * mm, "end": v(23.45, 19.28) * mm});
            skLineSegment(sketch, "E4538", {"start": v(23.45, 19.28) * mm, "end": v(24.72, 19.78) * mm});
            skLineSegment(sketch, "E4539", {"start": v(24.72, 19.78) * mm, "end": v(26.44, 20.66) * mm});
            skLineSegment(sketch, "E4540", {"start": v(26.44, 20.66) * mm, "end": v(27.06, 21.17) * mm});
            skLineSegment(sketch, "E4541", {"start": v(27.06, 21.17) * mm, "end": v(26.93, 21.39) * mm});
            skLineSegment(sketch, "E4542", {"start": v(26.93, 21.39) * mm, "end": v(4.69, 21.37) * mm});
            skLineSegment(sketch, "E4543", {"start": v(4.69, 21.37) * mm, "end": v(4.35, 21.24) * mm});
            skLineSegment(sketch, "E4544", {"start": v(4.35, 21.24) * mm, "end": v(4.94, 20.86) * mm});
            skLineSegment(sketch, "E4545", {"start": v(4.94, 20.86) * mm, "end": v(5.35, 20.62) * mm});
            skLineSegment(sketch, "E4546", {"start": v(5.35, 20.62) * mm, "end": v(5.8, 20.35) * mm});
            skLineSegment(sketch, "E4547", {"start": v(5.8, 20.35) * mm, "end": v(6.31, 20.08) * mm});
            skLineSegment(sketch, "E4548", {"start": v(6.31, 20.08) * mm, "end": v(6.84, 19.81) * mm});
            skLineSegment(sketch, "E4549", {"start": v(6.84, 19.81) * mm, "end": v(7.37, 19.55) * mm});
            skLineSegment(sketch, "E4550", {"start": v(7.37, 19.55) * mm, "end": v(7.9, 19.3) * mm});
            skLineSegment(sketch, "E4551", {"start": v(7.9, 19.3) * mm, "end": v(8.4, 19.09) * mm});
            skLineSegment(sketch, "E4552", {"start": v(8.4, 19.09) * mm, "end": v(8.85, 18.9) * mm});
            skLineSegment(sketch, "E4553", {"start": v(8.85, 18.9) * mm, "end": v(9.92, 18.48) * mm});
            skLineSegment(sketch, "E4554", {"start": v(9.92, 18.48) * mm, "end": v(12.3, 17.87) * mm});
            skLineSegment(sketch, "E4555", {"start": v(12.3, 17.87) * mm, "end": v(14.2, 17.67) * mm});
            skLineSegment(sketch, "E4556", {"start": v(14.2, 17.67) * mm, "end": v(14.52, 17.64) * mm});
            skLineSegment(sketch, "E4557", {"start": v(14.52, 17.64) * mm, "end": v(15.11, 17.6) * mm});
            skLineSegment(sketch, "E4558", {"start": v(-31.02, 32.99) * mm, "end": v(-30.98, 33) * mm});
            skLineSegment(sketch, "E4559", {"start": v(-30.98, 33) * mm, "end": v(-30.97, 33.03) * mm});
            skLineSegment(sketch, "E4560", {"start": v(-30.97, 33.03) * mm, "end": v(-30.98, 33.06) * mm});
            skLineSegment(sketch, "E4561", {"start": v(-30.98, 33.06) * mm, "end": v(-31.02, 33.08) * mm});
            skLineSegment(sketch, "E4562", {"start": v(-31.02, 33.08) * mm, "end": v(-31.05, 33.06) * mm});
            skLineSegment(sketch, "E4563", {"start": v(-31.05, 33.06) * mm, "end": v(-31.06, 33.03) * mm});
            skLineSegment(sketch, "E4564", {"start": v(-31.06, 33.03) * mm, "end": v(-31.05, 33) * mm});
            skLineSegment(sketch, "E4565", {"start": v(-31.05, 33) * mm, "end": v(-31.02, 32.99) * mm});
            skLineSegment(sketch, "E4566", {"start": v(-7.25, -38.7) * mm, "end": v(-7.2, -38.69) * mm});
            skLineSegment(sketch, "E4567", {"start": v(-7.2, -38.69) * mm, "end": v(-7.15, -38.67) * mm});
            skLineSegment(sketch, "E4568", {"start": v(-7.15, -38.67) * mm, "end": v(-7.1, -38.64) * mm});
            skLineSegment(sketch, "E4569", {"start": v(-7.1, -38.64) * mm, "end": v(-7.05, -38.6) * mm});
            skLineSegment(sketch, "E4570", {"start": v(-7.05, -38.6) * mm, "end": v(-7.01, -38.55) * mm});
            skLineSegment(sketch, "E4571", {"start": v(-7.01, -38.55) * mm, "end": v(-6.97, -38.5) * mm});
            skLineSegment(sketch, "E4572", {"start": v(-6.97, -38.5) * mm, "end": v(-6.94, -38.43) * mm});
            skLineSegment(sketch, "E4573", {"start": v(-6.94, -38.43) * mm, "end": v(-6.92, -38.36) * mm});
            skLineSegment(sketch, "E4574", {"start": v(-6.92, -38.36) * mm, "end": v(-6.85, -38.15) * mm});
            skLineSegment(sketch, "E4575", {"start": v(-6.85, -38.15) * mm, "end": v(-6.33, -37.88) * mm});
            skLineSegment(sketch, "E4576", {"start": v(-6.33, -37.88) * mm, "end": v(-2.44, -37.88) * mm});
            skLineSegment(sketch, "E4577", {"start": v(-2.44, -37.88) * mm, "end": v(-1.95, -38.46) * mm});
            skLineSegment(sketch, "E4578", {"start": v(-1.95, -38.46) * mm, "end": v(-1.43, -37.88) * mm});
            skLineSegment(sketch, "E4579", {"start": v(-1.43, -37.88) * mm, "end": v(-1.43, -37.72) * mm});
            skLineSegment(sketch, "E4580", {"start": v(-1.43, -37.72) * mm, "end": v(-1.44, -37.64) * mm});
            skLineSegment(sketch, "E4581", {"start": v(-1.44, -37.64) * mm, "end": v(-1.46, -37.55) * mm});
            skLineSegment(sketch, "E4582", {"start": v(-1.46, -37.55) * mm, "end": v(-1.5, -37.47) * mm});
            skLineSegment(sketch, "E4583", {"start": v(-1.5, -37.47) * mm, "end": v(-1.54, -37.4) * mm});
            skLineSegment(sketch, "E4584", {"start": v(-1.54, -37.4) * mm, "end": v(-1.66, -37.24) * mm});
            skLineSegment(sketch, "E4585", {"start": v(-1.66, -37.24) * mm, "end": v(-2.47, -37.05) * mm});
            skLineSegment(sketch, "E4586", {"start": v(-2.47, -37.05) * mm, "end": v(-3.51, -37.17) * mm});
            skLineSegment(sketch, "E4587", {"start": v(-3.51, -37.17) * mm, "end": v(-3.62, -36.88) * mm});
            skLineSegment(sketch, "E4588", {"start": v(-3.62, -36.88) * mm, "end": v(-3.2, -36.27) * mm});
            skLineSegment(sketch, "E4589", {"start": v(-3.2, -36.27) * mm, "end": v(-1.43, -33.94) * mm});
            skLineSegment(sketch, "E4590", {"start": v(-1.43, -33.94) * mm, "end": v(-0.7, -32.49) * mm});
            skLineSegment(sketch, "E4591", {"start": v(-0.7, -32.49) * mm, "end": v(-0.62, -32.1) * mm});
            skLineSegment(sketch, "E4592", {"start": v(-0.62, -32.1) * mm, "end": v(-0.55, -31.8) * mm});
            skLineSegment(sketch, "E4593", {"start": v(-0.55, -31.8) * mm, "end": v(-0.51, -31.7) * mm});
            skLineSegment(sketch, "E4594", {"start": v(-0.51, -31.7) * mm, "end": v(-0.49, -31.66) * mm});
            skLineSegment(sketch, "E4595", {"start": v(-0.49, -31.66) * mm, "end": v(-0.44, -31.6) * mm});
            skLineSegment(sketch, "E4596", {"start": v(-0.44, -31.6) * mm, "end": v(0, -31.93) * mm});
            skLineSegment(sketch, "E4597", {"start": v(0, -31.93) * mm, "end": v(0.19, -32.05) * mm});
            skLineSegment(sketch, "E4598", {"start": v(0.19, -32.05) * mm, "end": v(0.34, -32.14) * mm});
            skLineSegment(sketch, "E4599", {"start": v(0.34, -32.14) * mm, "end": v(0.45, -32.2) * mm});
            skLineSegment(sketch, "E4600", {"start": v(0.45, -32.2) * mm, "end": v(0.49, -32.2) * mm});
            skLineSegment(sketch, "E4601", {"start": v(0.49, -32.2) * mm, "end": v(0.5, -32.2) * mm});
            skLineSegment(sketch, "E4602", {"start": v(0.5, -32.2) * mm, "end": v(0.5, -32.18) * mm});
            skLineSegment(sketch, "E4603", {"start": v(0.5, -32.18) * mm, "end": v(0.5, -32.13) * mm});
            skLineSegment(sketch, "E4604", {"start": v(0.5, -32.13) * mm, "end": v(0.46, -31.97) * mm});
            skLineSegment(sketch, "E4605", {"start": v(0.46, -31.97) * mm, "end": v(0.4, -31.74) * mm});
            skLineSegment(sketch, "E4606", {"start": v(0.4, -31.74) * mm, "end": v(0.3, -31.46) * mm});
            skLineSegment(sketch, "E4607", {"start": v(0.3, -31.46) * mm, "end": v(0.04, -30.77) * mm});
            skLineSegment(sketch, "E4608", {"start": v(0.04, -30.77) * mm, "end": v(-0.18, -29.36) * mm});
            skLineSegment(sketch, "E4609", {"start": v(-0.18, -29.36) * mm, "end": v(-0.24, -29.36) * mm});
            skLineSegment(sketch, "E4610", {"start": v(-0.24, -29.36) * mm, "end": v(-0.38, -29.35) * mm});
            skLineSegment(sketch, "E4611", {"start": v(-0.38, -29.35) * mm, "end": v(-0.57, -29.3) * mm});
            skLineSegment(sketch, "E4612", {"start": v(-0.57, -29.3) * mm, "end": v(-1.08, -29.18) * mm});
            skLineSegment(sketch, "E4613", {"start": v(-1.08, -29.18) * mm, "end": v(-1.61, -29.03) * mm});
            skLineSegment(sketch, "E4614", {"start": v(-1.61, -29.03) * mm, "end": v(-1.85, -28.95) * mm});
            skLineSegment(sketch, "E4615", {"start": v(-1.85, -28.95) * mm, "end": v(-2.04, -28.87) * mm});
            skLineSegment(sketch, "E4616", {"start": v(-2.04, -28.87) * mm, "end": v(-2.41, -28.72) * mm});
            skLineSegment(sketch, "E4617", {"start": v(-2.41, -28.72) * mm, "end": v(-2.52, -28.68) * mm});
            skLineSegment(sketch, "E4618", {"start": v(-2.52, -28.68) * mm, "end": v(-2.6, -28.65) * mm});
            skLineSegment(sketch, "E4619", {"start": v(-2.6, -28.65) * mm, "end": v(-2.64, -28.65) * mm});
            skLineSegment(sketch, "E4620", {"start": v(-2.64, -28.65) * mm, "end": v(-2.66, -28.67) * mm});
            skLineSegment(sketch, "E4621", {"start": v(-2.66, -28.67) * mm, "end": v(-2.67, -28.75) * mm});
            skLineSegment(sketch, "E4622", {"start": v(-2.67, -28.75) * mm, "end": v(-2.7, -29.02) * mm});
            skLineSegment(sketch, "E4623", {"start": v(-2.7, -29.02) * mm, "end": v(-2.77, -29.52) * mm});
            skLineSegment(sketch, "E4624", {"start": v(-2.77, -29.52) * mm, "end": v(-2.88, -30.18) * mm});
            skLineSegment(sketch, "E4625", {"start": v(-2.88, -30.18) * mm, "end": v(-3.4, -31.63) * mm});
            skLineSegment(sketch, "E4626", {"start": v(-3.4, -31.63) * mm, "end": v(-2.9, -31.63) * mm});
            skLineSegment(sketch, "E4627", {"start": v(-2.9, -31.63) * mm, "end": v(-2.56, -31.4) * mm});
            skLineSegment(sketch, "E4628", {"start": v(-2.56, -31.4) * mm, "end": v(-2.43, -31.31) * mm});
            skLineSegment(sketch, "E4629", {"start": v(-2.43, -31.31) * mm, "end": v(-2.3, -31.25) * mm});
            skLineSegment(sketch, "E4630", {"start": v(-2.3, -31.25) * mm, "end": v(-2.22, -31.21) * mm});
            skLineSegment(sketch, "E4631", {"start": v(-2.22, -31.21) * mm, "end": v(-2.2, -31.2) * mm});
            skLineSegment(sketch, "E4632", {"start": v(-2.2, -31.2) * mm, "end": v(-2.18, -31.21) * mm});
            skLineSegment(sketch, "E4633", {"start": v(-2.18, -31.21) * mm, "end": v(-2.17, -31.23) * mm});
            skLineSegment(sketch, "E4634", {"start": v(-2.17, -31.23) * mm, "end": v(-2.16, -31.27) * mm});
            skLineSegment(sketch, "E4635", {"start": v(-2.16, -31.27) * mm, "end": v(-2.18, -31.38) * mm});
            skLineSegment(sketch, "E4636", {"start": v(-2.18, -31.38) * mm, "end": v(-2.22, -31.54) * mm});
            skLineSegment(sketch, "E4637", {"start": v(-2.22, -31.54) * mm, "end": v(-2.3, -31.75) * mm});
            skLineSegment(sketch, "E4638", {"start": v(-2.3, -31.75) * mm, "end": v(-2.5, -32.27) * mm});
            skLineSegment(sketch, "E4639", {"start": v(-2.5, -32.27) * mm, "end": v(-2.78, -32.9) * mm});
            skLineSegment(sketch, "E4640", {"start": v(-2.78, -32.9) * mm, "end": v(-3.11, -33.61) * mm});
            skLineSegment(sketch, "E4641", {"start": v(-3.11, -33.61) * mm, "end": v(-3.49, -34.35) * mm});
            skLineSegment(sketch, "E4642", {"start": v(-3.49, -34.35) * mm, "end": v(-3.88, -35.09) * mm});
            skLineSegment(sketch, "E4643", {"start": v(-3.88, -35.09) * mm, "end": v(-4.27, -35.77) * mm});
            skLineSegment(sketch, "E4644", {"start": v(-4.27, -35.77) * mm, "end": v(-4.88, -36.8) * mm});
            skLineSegment(sketch, "E4645", {"start": v(-4.88, -36.8) * mm, "end": v(-5.65, -36.8) * mm});
            skLineSegment(sketch, "E4646", {"start": v(-5.65, -36.8) * mm, "end": v(-6.5, -36.5) * mm});
            skLineSegment(sketch, "E4647", {"start": v(-6.5, -36.5) * mm, "end": v(-7.14, -36.62) * mm});
            skLineSegment(sketch, "E4648", {"start": v(-7.14, -36.62) * mm, "end": v(-7.36, -36.97) * mm});
            skLineSegment(sketch, "E4649", {"start": v(-7.36, -36.97) * mm, "end": v(-7.55, -36.97) * mm});
            skLineSegment(sketch, "E4650", {"start": v(-7.55, -36.97) * mm, "end": v(-7.65, -36.98) * mm});
            skLineSegment(sketch, "E4651", {"start": v(-7.65, -36.98) * mm, "end": v(-7.77, -37) * mm});
            skLineSegment(sketch, "E4652", {"start": v(-7.77, -37) * mm, "end": v(-7.9, -37.04) * mm});
            skLineSegment(sketch, "E4653", {"start": v(-7.9, -37.04) * mm, "end": v(-8.03, -37.08) * mm});
            skLineSegment(sketch, "E4654", {"start": v(-8.03, -37.08) * mm, "end": v(-8.32, -37.18) * mm});
            skLineSegment(sketch, "E4655", {"start": v(-8.32, -37.18) * mm, "end": v(-8.4, -37.34) * mm});
            skLineSegment(sketch, "E4656", {"start": v(-8.4, -37.34) * mm, "end": v(-8.44, -37.41) * mm});
            skLineSegment(sketch, "E4657", {"start": v(-8.44, -37.41) * mm, "end": v(-8.46, -37.5) * mm});
            skLineSegment(sketch, "E4658", {"start": v(-8.46, -37.5) * mm, "end": v(-8.5, -37.72) * mm});
            skLineSegment(sketch, "E4659", {"start": v(-8.5, -37.72) * mm, "end": v(-8.5, -37.81) * mm});
            skLineSegment(sketch, "E4660", {"start": v(-8.5, -37.81) * mm, "end": v(-8.5, -37.9) * mm});
            skLineSegment(sketch, "E4661", {"start": v(-8.5, -37.9) * mm, "end": v(-8.48, -37.95) * mm});
            skLineSegment(sketch, "E4662", {"start": v(-8.48, -37.95) * mm, "end": v(-8.47, -37.97) * mm});
            skLineSegment(sketch, "E4663", {"start": v(-8.47, -37.97) * mm, "end": v(-8.46, -37.97) * mm});
            skLineSegment(sketch, "E4664", {"start": v(-8.46, -37.97) * mm, "end": v(-8.3, -37.9) * mm});
            skLineSegment(sketch, "E4665", {"start": v(-8.3, -37.9) * mm, "end": v(-7.96, -37.73) * mm});
            skLineSegment(sketch, "E4666", {"start": v(-7.96, -37.73) * mm, "end": v(-7.5, -37.5) * mm});
            skLineSegment(sketch, "E4667", {"start": v(-7.5, -37.5) * mm, "end": v(-7.4, -37.6) * mm});
            skLineSegment(sketch, "E4668", {"start": v(-7.4, -37.6) * mm, "end": v(-7.5, -37.78) * mm});
            skLineSegment(sketch, "E4669", {"start": v(-7.5, -37.78) * mm, "end": v(-7.53, -37.86) * mm});
            skLineSegment(sketch, "E4670", {"start": v(-7.53, -37.86) * mm, "end": v(-7.56, -37.96) * mm});
            skLineSegment(sketch, "E4671", {"start": v(-7.56, -37.96) * mm, "end": v(-7.58, -38.05) * mm});
            skLineSegment(sketch, "E4672", {"start": v(-7.58, -38.05) * mm, "end": v(-7.6, -38.13) * mm});
            skLineSegment(sketch, "E4673", {"start": v(-7.6, -38.13) * mm, "end": v(-7.58, -38.2) * mm});
            skLineSegment(sketch, "E4674", {"start": v(-7.58, -38.2) * mm, "end": v(-7.55, -38.3) * mm});
            skLineSegment(sketch, "E4675", {"start": v(-7.55, -38.3) * mm, "end": v(-7.5, -38.39) * mm});
            skLineSegment(sketch, "E4676", {"start": v(-7.5, -38.39) * mm, "end": v(-7.46, -38.48) * mm});
            skLineSegment(sketch, "E4677", {"start": v(-7.46, -38.48) * mm, "end": v(-7.4, -38.56) * mm});
            skLineSegment(sketch, "E4678", {"start": v(-7.4, -38.56) * mm, "end": v(-7.34, -38.63) * mm});
            skLineSegment(sketch, "E4679", {"start": v(-7.34, -38.63) * mm, "end": v(-7.3, -38.68) * mm});
            skLineSegment(sketch, "E4680", {"start": v(-7.3, -38.68) * mm, "end": v(-7.25, -38.7) * mm});
            skLineSegment(sketch, "E4681", {"start": v(8.1, -34.07) * mm, "end": v(8.23, -34.07) * mm});
            skLineSegment(sketch, "E4682", {"start": v(8.23, -34.07) * mm, "end": v(8.56, -33.46) * mm});
            skLineSegment(sketch, "E4683", {"start": v(8.56, -33.46) * mm, "end": v(8.7, -33.18) * mm});
            skLineSegment(sketch, "E4684", {"start": v(8.7, -33.18) * mm, "end": v(8.84, -32.86) * mm});
            skLineSegment(sketch, "E4685", {"start": v(8.84, -32.86) * mm, "end": v(8.97, -32.54) * mm});
            skLineSegment(sketch, "E4686", {"start": v(8.97, -32.54) * mm, "end": v(9.07, -32.26) * mm});
            skLineSegment(sketch, "E4687", {"start": v(9.07, -32.26) * mm, "end": v(9.24, -31.67) * mm});
            skLineSegment(sketch, "E4688", {"start": v(9.24, -31.67) * mm, "end": v(9.37, -30.4) * mm});
            skLineSegment(sketch, "E4689", {"start": v(9.37, -30.4) * mm, "end": v(9.08, -28.77) * mm});
            skLineSegment(sketch, "E4690", {"start": v(9.08, -28.77) * mm, "end": v(8.45, -27.44) * mm});
            skLineSegment(sketch, "E4691", {"start": v(8.45, -27.44) * mm, "end": v(7.27, -26.28) * mm});
            skLineSegment(sketch, "E4692", {"start": v(7.27, -26.28) * mm, "end": v(5.23, -25.3) * mm});
            skLineSegment(sketch, "E4693", {"start": v(5.23, -25.3) * mm, "end": v(3.15, -24.66) * mm});
            skLineSegment(sketch, "E4694", {"start": v(3.15, -24.66) * mm, "end": v(3.01, -24.8) * mm});
            skLineSegment(sketch, "E4695", {"start": v(3.01, -24.8) * mm, "end": v(3.52, -25.14) * mm});
            skLineSegment(sketch, "E4696", {"start": v(3.52, -25.14) * mm, "end": v(3.83, -25.35) * mm});
            skLineSegment(sketch, "E4697", {"start": v(3.83, -25.35) * mm, "end": v(4.13, -25.57) * mm});
            skLineSegment(sketch, "E4698", {"start": v(4.13, -25.57) * mm, "end": v(4.42, -25.8) * mm});
            skLineSegment(sketch, "E4699", {"start": v(4.42, -25.8) * mm, "end": v(4.7, -26.02) * mm});
            skLineSegment(sketch, "E4700", {"start": v(4.7, -26.02) * mm, "end": v(4.96, -26.25) * mm});
            skLineSegment(sketch, "E4701", {"start": v(4.96, -26.25) * mm, "end": v(5.22, -26.49) * mm});
            skLineSegment(sketch, "E4702", {"start": v(5.22, -26.49) * mm, "end": v(5.46, -26.73) * mm});
            skLineSegment(sketch, "E4703", {"start": v(5.46, -26.73) * mm, "end": v(5.7, -26.97) * mm});
            skLineSegment(sketch, "E4704", {"start": v(5.7, -26.97) * mm, "end": v(5.92, -27.22) * mm});
            skLineSegment(sketch, "E4705", {"start": v(5.92, -27.22) * mm, "end": v(6.13, -27.47) * mm});
            skLineSegment(sketch, "E4706", {"start": v(6.13, -27.47) * mm, "end": v(6.33, -27.72) * mm});
            skLineSegment(sketch, "E4707", {"start": v(6.33, -27.72) * mm, "end": v(6.52, -27.98) * mm});
            skLineSegment(sketch, "E4708", {"start": v(6.52, -27.98) * mm, "end": v(6.7, -28.25) * mm});
            skLineSegment(sketch, "E4709", {"start": v(6.7, -28.25) * mm, "end": v(6.87, -28.52) * mm});
            skLineSegment(sketch, "E4710", {"start": v(6.87, -28.52) * mm, "end": v(7.02, -28.79) * mm});
            skLineSegment(sketch, "E4711", {"start": v(7.02, -28.79) * mm, "end": v(7.17, -29.06) * mm});
            skLineSegment(sketch, "E4712", {"start": v(7.17, -29.06) * mm, "end": v(7.45, -29.63) * mm});
            skLineSegment(sketch, "E4713", {"start": v(7.45, -29.63) * mm, "end": v(7.9, -31.14) * mm});
            skLineSegment(sketch, "E4714", {"start": v(7.9, -31.14) * mm, "end": v(8.1, -33.26) * mm});
            skLineSegment(sketch, "E4715", {"start": v(8.1, -33.26) * mm, "end": v(7.98, -34.07) * mm});
            skLineSegment(sketch, "E4716", {"start": v(7.98, -34.07) * mm, "end": v(8.1, -34.07) * mm});
            skLineSegment(sketch, "E4717", {"start": v(-2.5, -24.71) * mm, "end": v(-2.68, -24.47) * mm});
            skLineSegment(sketch, "E4718", {"start": v(-2.68, -24.47) * mm, "end": v(-2.84, -24.24) * mm});
            skLineSegment(sketch, "E4719", {"start": v(-2.84, -24.24) * mm, "end": v(-2.98, -24.02) * mm});
            skLineSegment(sketch, "E4720", {"start": v(-2.98, -24.02) * mm, "end": v(-3.1, -23.8) * mm});
            skLineSegment(sketch, "E4721", {"start": v(-3.1, -23.8) * mm, "end": v(-3.2, -23.56) * mm});
            skLineSegment(sketch, "E4722", {"start": v(-3.2, -23.56) * mm, "end": v(-3.3, -23.32) * mm});
            skLineSegment(sketch, "E4723", {"start": v(-3.3, -23.32) * mm, "end": v(-3.39, -23.07) * mm});
            skLineSegment(sketch, "E4724", {"start": v(-3.39, -23.07) * mm, "end": v(-3.46, -22.8) * mm});
            skLineSegment(sketch, "E4725", {"start": v(-3.46, -22.8) * mm, "end": v(-3.6, -22.26) * mm});
            skLineSegment(sketch, "E4726", {"start": v(-3.6, -22.26) * mm, "end": v(-3.6, -20.56) * mm});
            skLineSegment(sketch, "E4727", {"start": v(-3.6, -20.56) * mm, "end": v(-3.45, -19.91) * mm});
            skLineSegment(sketch, "E4728", {"start": v(-3.45, -19.91) * mm, "end": v(-3.38, -19.62) * mm});
            skLineSegment(sketch, "E4729", {"start": v(-3.38, -19.62) * mm, "end": v(-3.29, -19.3) * mm});
            skLineSegment(sketch, "E4730", {"start": v(-3.29, -19.3) * mm, "end": v(-3.19, -19) * mm});
            skLineSegment(sketch, "E4731", {"start": v(-3.19, -19) * mm, "end": v(-3.1, -18.77) * mm});
            skLineSegment(sketch, "E4732", {"start": v(-3.1, -18.77) * mm, "end": v(-2.88, -18.28) * mm});
            skLineSegment(sketch, "E4733", {"start": v(-2.88, -18.28) * mm, "end": v(-2.98, -18.17) * mm});
            skLineSegment(sketch, "E4734", {"start": v(-2.98, -18.17) * mm, "end": v(-3.87, -19.17) * mm});
            skLineSegment(sketch, "E4735", {"start": v(-3.87, -19.17) * mm, "end": v(-4.4, -20.25) * mm});
            skLineSegment(sketch, "E4736", {"start": v(-4.4, -20.25) * mm, "end": v(-4.61, -21.42) * mm});
            skLineSegment(sketch, "E4737", {"start": v(-4.61, -21.42) * mm, "end": v(-4.55, -21.88) * mm});
            skLineSegment(sketch, "E4738", {"start": v(-4.55, -21.88) * mm, "end": v(-4.47, -22.36) * mm});
            skLineSegment(sketch, "E4739", {"start": v(-4.47, -22.36) * mm, "end": v(-4.36, -22.88) * mm});
            skLineSegment(sketch, "E4740", {"start": v(-4.36, -22.88) * mm, "end": v(-4.22, -23.41) * mm});
            skLineSegment(sketch, "E4741", {"start": v(-4.22, -23.41) * mm, "end": v(-3.68, -24.5) * mm});
            skLineSegment(sketch, "E4742", {"start": v(-3.68, -24.5) * mm, "end": v(-2.74, -25.43) * mm});
            skLineSegment(sketch, "E4743", {"start": v(-2.74, -25.43) * mm, "end": v(-2.32, -25.67) * mm});
            skLineSegment(sketch, "E4744", {"start": v(-2.32, -25.67) * mm, "end": v(-2.12, -25.78) * mm});
            skLineSegment(sketch, "E4745", {"start": v(-2.12, -25.78) * mm, "end": v(-1.89, -25.9) * mm});
            skLineSegment(sketch, "E4746", {"start": v(-1.89, -25.9) * mm, "end": v(-1.64, -26) * mm});
            skLineSegment(sketch, "E4747", {"start": v(-1.64, -26) * mm, "end": v(-1.42, -26.1) * mm});
            skLineSegment(sketch, "E4748", {"start": v(-1.42, -26.1) * mm, "end": v(-0.93, -26.29) * mm});
            skLineSegment(sketch, "E4749", {"start": v(-0.93, -26.29) * mm, "end": v(-1.5, -25.78) * mm});
            skLineSegment(sketch, "E4750", {"start": v(-1.5, -25.78) * mm, "end": v(-1.75, -25.54) * mm});
            skLineSegment(sketch, "E4751", {"start": v(-1.75, -25.54) * mm, "end": v(-2.02, -25.26) * mm});
            skLineSegment(sketch, "E4752", {"start": v(-2.02, -25.26) * mm, "end": v(-2.28, -24.97) * mm});
            skLineSegment(sketch, "E4753", {"start": v(-2.28, -24.97) * mm, "end": v(-2.5, -24.71) * mm});
            skLineSegment(sketch, "E4754", {"start": v(6.46, -23.1) * mm, "end": v(7.33, -23.1) * mm});
            skLineSegment(sketch, "E4755", {"start": v(7.33, -23.1) * mm, "end": v(7.57, -22.86) * mm});
            skLineSegment(sketch, "E4756", {"start": v(7.57, -22.86) * mm, "end": v(7.66, -22.75) * mm});
            skLineSegment(sketch, "E4757", {"start": v(7.66, -22.75) * mm, "end": v(7.76, -22.61) * mm});
            skLineSegment(sketch, "E4758", {"start": v(7.76, -22.61) * mm, "end": v(7.85, -22.47) * mm});
            skLineSegment(sketch, "E4759", {"start": v(7.85, -22.47) * mm, "end": v(7.92, -22.32) * mm});
            skLineSegment(sketch, "E4760", {"start": v(7.92, -22.32) * mm, "end": v(7.99, -22.18) * mm});
            skLineSegment(sketch, "E4761", {"start": v(7.99, -22.18) * mm, "end": v(8.03, -22.05) * mm});
            skLineSegment(sketch, "E4762", {"start": v(8.03, -22.05) * mm, "end": v(8.05, -21.96) * mm});
            skLineSegment(sketch, "E4763", {"start": v(8.05, -21.96) * mm, "end": v(8.04, -21.93) * mm});
            skLineSegment(sketch, "E4764", {"start": v(8.04, -21.93) * mm, "end": v(8.03, -21.9) * mm});
            skLineSegment(sketch, "E4765", {"start": v(8.03, -21.9) * mm, "end": v(8.02, -21.9) * mm});
            skLineSegment(sketch, "E4766", {"start": v(8.02, -21.9) * mm, "end": v(7.99, -21.9) * mm});
            skLineSegment(sketch, "E4767", {"start": v(7.99, -21.9) * mm, "end": v(7.89, -21.93) * mm});
            skLineSegment(sketch, "E4768", {"start": v(7.89, -21.93) * mm, "end": v(7.76, -22) * mm});
            skLineSegment(sketch, "E4769", {"start": v(7.76, -22) * mm, "end": v(7.6, -22.07) * mm});
            skLineSegment(sketch, "E4770", {"start": v(7.6, -22.07) * mm, "end": v(7.44, -22.15) * mm});
            skLineSegment(sketch, "E4771", {"start": v(7.44, -22.15) * mm, "end": v(7.2, -22.25) * mm});
            skLineSegment(sketch, "E4772", {"start": v(7.2, -22.25) * mm, "end": v(6.64, -22.46) * mm});
            skLineSegment(sketch, "E4773", {"start": v(6.64, -22.46) * mm, "end": v(6.03, -22.65) * mm});
            skLineSegment(sketch, "E4774", {"start": v(6.03, -22.65) * mm, "end": v(5.75, -22.73) * mm});
            skLineSegment(sketch, "E4775", {"start": v(5.75, -22.73) * mm, "end": v(5.5, -22.8) * mm});
            skLineSegment(sketch, "E4776", {"start": v(5.5, -22.8) * mm, "end": v(5.23, -22.85) * mm});
            skLineSegment(sketch, "E4777", {"start": v(5.23, -22.85) * mm, "end": v(5.59, -23.1) * mm});
            skLineSegment(sketch, "E4778", {"start": v(5.59, -23.1) * mm, "end": v(6.46, -23.1) * mm});
            skLineSegment(sketch, "E4779", {"start": v(4.74, -22.65) * mm, "end": v(4.85, -22.63) * mm});
            skLineSegment(sketch, "E4780", {"start": v(4.85, -22.63) * mm, "end": v(5.08, -22.56) * mm});
            skLineSegment(sketch, "E4781", {"start": v(5.08, -22.56) * mm, "end": v(5.76, -22.33) * mm});
            skLineSegment(sketch, "E4782", {"start": v(5.76, -22.33) * mm, "end": v(6.5, -22.06) * mm});
            skLineSegment(sketch, "E4783", {"start": v(6.5, -22.06) * mm, "end": v(7.01, -21.86) * mm});
            skLineSegment(sketch, "E4784", {"start": v(7.01, -21.86) * mm, "end": v(7.22, -21.76) * mm});
            skLineSegment(sketch, "E4785", {"start": v(7.22, -21.76) * mm, "end": v(7.48, -21.62) * mm});
            skLineSegment(sketch, "E4786", {"start": v(7.48, -21.62) * mm, "end": v(7.76, -21.46) * mm});
            skLineSegment(sketch, "E4787", {"start": v(7.76, -21.46) * mm, "end": v(8.02, -21.3) * mm});
            skLineSegment(sketch, "E4788", {"start": v(8.02, -21.3) * mm, "end": v(8.61, -20.93) * mm});
            skLineSegment(sketch, "E4789", {"start": v(8.61, -20.93) * mm, "end": v(8.98, -20.53) * mm});
            skLineSegment(sketch, "E4790", {"start": v(8.98, -20.53) * mm, "end": v(9.13, -20.36) * mm});
            skLineSegment(sketch, "E4791", {"start": v(9.13, -20.36) * mm, "end": v(9.28, -20.17) * mm});
            skLineSegment(sketch, "E4792", {"start": v(9.28, -20.17) * mm, "end": v(9.4, -20) * mm});
            skLineSegment(sketch, "E4793", {"start": v(9.4, -20) * mm, "end": v(9.49, -19.86) * mm});
            skLineSegment(sketch, "E4794", {"start": v(9.49, -19.86) * mm, "end": v(9.63, -19.57) * mm});
            skLineSegment(sketch, "E4795", {"start": v(9.63, -19.57) * mm, "end": v(9.49, -19.57) * mm});
            skLineSegment(sketch, "E4796", {"start": v(9.49, -19.57) * mm, "end": v(9.41, -19.6) * mm});
            skLineSegment(sketch, "E4797", {"start": v(9.41, -19.6) * mm, "end": v(9.3, -19.64) * mm});
            skLineSegment(sketch, "E4798", {"start": v(9.3, -19.64) * mm, "end": v(9.18, -19.7) * mm});
            skLineSegment(sketch, "E4799", {"start": v(9.18, -19.7) * mm, "end": v(9.06, -19.8) * mm});
            skLineSegment(sketch, "E4800", {"start": v(9.06, -19.8) * mm, "end": v(8.88, -19.9) * mm});
            skLineSegment(sketch, "E4801", {"start": v(8.88, -19.9) * mm, "end": v(8.62, -20.06) * mm});
            skLineSegment(sketch, "E4802", {"start": v(8.62, -20.06) * mm, "end": v(8.31, -20.23) * mm});
            skLineSegment(sketch, "E4803", {"start": v(8.31, -20.23) * mm, "end": v(7.99, -20.39) * mm});
            skLineSegment(sketch, "E4804", {"start": v(7.99, -20.39) * mm, "end": v(7.2, -20.76) * mm});
            skLineSegment(sketch, "E4805", {"start": v(7.2, -20.76) * mm, "end": v(5.28, -21.16) * mm});
            skLineSegment(sketch, "E4806", {"start": v(5.28, -21.16) * mm, "end": v(4.9, -22.1) * mm});
            skLineSegment(sketch, "E4807", {"start": v(4.9, -22.1) * mm, "end": v(4.46, -22.5) * mm});
            skLineSegment(sketch, "E4808", {"start": v(4.46, -22.5) * mm, "end": v(4.58, -22.58) * mm});
            skLineSegment(sketch, "E4809", {"start": v(4.58, -22.58) * mm, "end": v(4.67, -22.63) * mm});
            skLineSegment(sketch, "E4810", {"start": v(4.67, -22.63) * mm, "end": v(4.74, -22.65) * mm});
            skLineSegment(sketch, "E4811", {"start": v(6.11, -20.66) * mm, "end": v(6.89, -20.34) * mm});
            skLineSegment(sketch, "E4812", {"start": v(6.89, -20.34) * mm, "end": v(7.5, -20.07) * mm});
            skLineSegment(sketch, "E4813", {"start": v(7.5, -20.07) * mm, "end": v(8.02, -19.82) * mm});
            skLineSegment(sketch, "E4814", {"start": v(8.02, -19.82) * mm, "end": v(8.48, -19.56) * mm});
            skLineSegment(sketch, "E4815", {"start": v(8.48, -19.56) * mm, "end": v(9.13, -19.18) * mm});
            skLineSegment(sketch, "E4816", {"start": v(9.13, -19.18) * mm, "end": v(10.26, -18.05) * mm});
            skLineSegment(sketch, "E4817", {"start": v(10.26, -18.05) * mm, "end": v(10.43, -17.66) * mm});
            skLineSegment(sketch, "E4818", {"start": v(10.43, -17.66) * mm, "end": v(10.57, -17.3) * mm});
            skLineSegment(sketch, "E4819", {"start": v(10.57, -17.3) * mm, "end": v(10.66, -17.02) * mm});
            skLineSegment(sketch, "E4820", {"start": v(10.66, -17.02) * mm, "end": v(10.72, -16.77) * mm});
            skLineSegment(sketch, "E4821", {"start": v(10.72, -16.77) * mm, "end": v(10.57, -16.83) * mm});
            skLineSegment(sketch, "E4822", {"start": v(10.57, -16.83) * mm, "end": v(10.45, -16.9) * mm});
            skLineSegment(sketch, "E4823", {"start": v(10.45, -16.9) * mm, "end": v(10.24, -17.03) * mm});
            skLineSegment(sketch, "E4824", {"start": v(10.24, -17.03) * mm, "end": v(9.67, -17.45) * mm});
            skLineSegment(sketch, "E4825", {"start": v(9.67, -17.45) * mm, "end": v(9.32, -17.7) * mm});
            skLineSegment(sketch, "E4826", {"start": v(9.32, -17.7) * mm, "end": v(8.98, -17.94) * mm});
            skLineSegment(sketch, "E4827", {"start": v(8.98, -17.94) * mm, "end": v(8.65, -18.15) * mm});
            skLineSegment(sketch, "E4828", {"start": v(8.65, -18.15) * mm, "end": v(8.3, -18.35) * mm});
            skLineSegment(sketch, "E4829", {"start": v(8.3, -18.35) * mm, "end": v(7.96, -18.53) * mm});
            skLineSegment(sketch, "E4830", {"start": v(7.96, -18.53) * mm, "end": v(7.6, -18.7) * mm});
            skLineSegment(sketch, "E4831", {"start": v(7.6, -18.7) * mm, "end": v(7.23, -18.88) * mm});
            skLineSegment(sketch, "E4832", {"start": v(7.23, -18.88) * mm, "end": v(6.83, -19.04) * mm});
            skLineSegment(sketch, "E4833", {"start": v(6.83, -19.04) * mm, "end": v(5.96, -19.38) * mm});
            skLineSegment(sketch, "E4834", {"start": v(5.96, -19.38) * mm, "end": v(5.86, -19.78) * mm});
            skLineSegment(sketch, "E4835", {"start": v(5.86, -19.78) * mm, "end": v(5.75, -20.12) * mm});
            skLineSegment(sketch, "E4836", {"start": v(5.75, -20.12) * mm, "end": v(5.7, -20.27) * mm});
            skLineSegment(sketch, "E4837", {"start": v(5.7, -20.27) * mm, "end": v(5.64, -20.38) * mm});
            skLineSegment(sketch, "E4838", {"start": v(5.64, -20.38) * mm, "end": v(5.54, -20.59) * mm});
            skLineSegment(sketch, "E4839", {"start": v(5.54, -20.59) * mm, "end": v(5.64, -20.84) * mm});
            skLineSegment(sketch, "E4840", {"start": v(5.64, -20.84) * mm, "end": v(6.11, -20.66) * mm});
            skLineSegment(sketch, "E4841", {"start": v(6.44, -18.89) * mm, "end": v(6.87, -18.7) * mm});
            skLineSegment(sketch, "E4842", {"start": v(6.87, -18.7) * mm, "end": v(7.36, -18.44) * mm});
            skLineSegment(sketch, "E4843", {"start": v(7.36, -18.44) * mm, "end": v(7.89, -18.15) * mm});
            skLineSegment(sketch, "E4844", {"start": v(7.89, -18.15) * mm, "end": v(8.42, -17.83) * mm});
            skLineSegment(sketch, "E4845", {"start": v(8.42, -17.83) * mm, "end": v(8.95, -17.5) * mm});
            skLineSegment(sketch, "E4846", {"start": v(8.95, -17.5) * mm, "end": v(9.43, -17.17) * mm});
            skLineSegment(sketch, "E4847", {"start": v(9.43, -17.17) * mm, "end": v(9.86, -16.86) * mm});
            skLineSegment(sketch, "E4848", {"start": v(9.86, -16.86) * mm, "end": v(10.04, -16.72) * mm});
            skLineSegment(sketch, "E4849", {"start": v(10.04, -16.72) * mm, "end": v(10.2, -16.58) * mm});
            skLineSegment(sketch, "E4850", {"start": v(10.2, -16.58) * mm, "end": v(10.63, -16.2) * mm});
            skLineSegment(sketch, "E4851", {"start": v(10.63, -16.2) * mm, "end": v(11.42, -15.09) * mm});
            skLineSegment(sketch, "E4852", {"start": v(11.42, -15.09) * mm, "end": v(11.74, -14.17) * mm});
            skLineSegment(sketch, "E4853", {"start": v(11.74, -14.17) * mm, "end": v(11.62, -13.83) * mm});
            skLineSegment(sketch, "E4854", {"start": v(11.62, -13.83) * mm, "end": v(11.05, -14.38) * mm});
            skLineSegment(sketch, "E4855", {"start": v(11.05, -14.38) * mm, "end": v(10.57, -14.83) * mm});
            skLineSegment(sketch, "E4856", {"start": v(10.57, -14.83) * mm, "end": v(10.06, -15.27) * mm});
            skLineSegment(sketch, "E4857", {"start": v(10.06, -15.27) * mm, "end": v(9.54, -15.7) * mm});
            skLineSegment(sketch, "E4858", {"start": v(9.54, -15.7) * mm, "end": v(9, -16.1) * mm});
            skLineSegment(sketch, "E4859", {"start": v(9, -16.1) * mm, "end": v(8.45, -16.48) * mm});
            skLineSegment(sketch, "E4860", {"start": v(8.45, -16.48) * mm, "end": v(7.9, -16.84) * mm});
            skLineSegment(sketch, "E4861", {"start": v(7.9, -16.84) * mm, "end": v(7.34, -17.16) * mm});
            skLineSegment(sketch, "E4862", {"start": v(7.34, -17.16) * mm, "end": v(6.8, -17.45) * mm});
            skLineSegment(sketch, "E4863", {"start": v(6.8, -17.45) * mm, "end": v(6.08, -17.8) * mm});
            skLineSegment(sketch, "E4864", {"start": v(6.08, -17.8) * mm, "end": v(6.18, -18.29) * mm});
            skLineSegment(sketch, "E4865", {"start": v(6.18, -18.29) * mm, "end": v(6.1, -18.55) * mm});
            skLineSegment(sketch, "E4866", {"start": v(6.1, -18.55) * mm, "end": v(6.08, -18.66) * mm});
            skLineSegment(sketch, "E4867", {"start": v(6.08, -18.66) * mm, "end": v(6.06, -18.76) * mm});
            skLineSegment(sketch, "E4868", {"start": v(6.06, -18.76) * mm, "end": v(6.06, -18.85) * mm});
            skLineSegment(sketch, "E4869", {"start": v(6.06, -18.85) * mm, "end": v(6.07, -18.92) * mm});
            skLineSegment(sketch, "E4870", {"start": v(6.07, -18.92) * mm, "end": v(6.1, -19.03) * mm});
            skLineSegment(sketch, "E4871", {"start": v(6.1, -19.03) * mm, "end": v(6.44, -18.89) * mm});
            skLineSegment(sketch, "E4872", {"start": v(6.26, -17.3) * mm, "end": v(6.33, -17.3) * mm});
            skLineSegment(sketch, "E4873", {"start": v(6.33, -17.3) * mm, "end": v(8.7, -15.88) * mm});
            skLineSegment(sketch, "E4874", {"start": v(8.7, -15.88) * mm, "end": v(9.49, -15.32) * mm});
            skLineSegment(sketch, "E4875", {"start": v(9.49, -15.32) * mm, "end": v(9.85, -15.04) * mm});
            skLineSegment(sketch, "E4876", {"start": v(9.85, -15.04) * mm, "end": v(10.26, -14.7) * mm});
            skLineSegment(sketch, "E4877", {"start": v(10.26, -14.7) * mm, "end": v(10.68, -14.35) * mm});
            skLineSegment(sketch, "E4878", {"start": v(10.68, -14.35) * mm, "end": v(11.04, -14.03) * mm});
            skLineSegment(sketch, "E4879", {"start": v(11.04, -14.03) * mm, "end": v(11.8, -13.3) * mm});
            skLineSegment(sketch, "E4880", {"start": v(11.8, -13.3) * mm, "end": v(12.29, -12.56) * mm});
            skLineSegment(sketch, "E4881", {"start": v(12.29, -12.56) * mm, "end": v(12.48, -12.26) * mm});
            skLineSegment(sketch, "E4882", {"start": v(12.48, -12.26) * mm, "end": v(12.65, -11.97) * mm});
            skLineSegment(sketch, "E4883", {"start": v(12.65, -11.97) * mm, "end": v(12.8, -11.7) * mm});
            skLineSegment(sketch, "E4884", {"start": v(12.8, -11.7) * mm, "end": v(12.93, -11.43) * mm});
            skLineSegment(sketch, "E4885", {"start": v(12.93, -11.43) * mm, "end": v(13.03, -11.19) * mm});
            skLineSegment(sketch, "E4886", {"start": v(13.03, -11.19) * mm, "end": v(13.11, -10.95) * mm});
            skLineSegment(sketch, "E4887", {"start": v(13.11, -10.95) * mm, "end": v(13.18, -10.72) * mm});
            skLineSegment(sketch, "E4888", {"start": v(13.18, -10.72) * mm, "end": v(13.22, -10.5) * mm});
            skLineSegment(sketch, "E4889", {"start": v(13.22, -10.5) * mm, "end": v(13.28, -10.1) * mm});
            skLineSegment(sketch, "E4890", {"start": v(13.28, -10.1) * mm, "end": v(12.52, -10.92) * mm});
            skLineSegment(sketch, "E4891", {"start": v(12.52, -10.92) * mm, "end": v(11.82, -11.66) * mm});
            skLineSegment(sketch, "E4892", {"start": v(11.82, -11.66) * mm, "end": v(11.49, -12) * mm});
            skLineSegment(sketch, "E4893", {"start": v(11.49, -12) * mm, "end": v(11.15, -12.33) * mm});
            skLineSegment(sketch, "E4894", {"start": v(11.15, -12.33) * mm, "end": v(10.81, -12.64) * mm});
            skLineSegment(sketch, "E4895", {"start": v(10.81, -12.64) * mm, "end": v(10.47, -12.96) * mm});
            skLineSegment(sketch, "E4896", {"start": v(10.47, -12.96) * mm, "end": v(9.72, -13.61) * mm});
            skLineSegment(sketch, "E4897", {"start": v(9.72, -13.61) * mm, "end": v(8.86, -14.34) * mm});
            skLineSegment(sketch, "E4898", {"start": v(8.86, -14.34) * mm, "end": v(6.14, -16.14) * mm});
            skLineSegment(sketch, "E4899", {"start": v(6.14, -16.14) * mm, "end": v(6.12, -16.61) * mm});
            skLineSegment(sketch, "E4900", {"start": v(6.12, -16.61) * mm, "end": v(6.12, -16.94) * mm});
            skLineSegment(sketch, "E4901", {"start": v(6.12, -16.94) * mm, "end": v(6.13, -17.06) * mm});
            skLineSegment(sketch, "E4902", {"start": v(6.13, -17.06) * mm, "end": v(6.14, -17.15) * mm});
            skLineSegment(sketch, "E4903", {"start": v(6.14, -17.15) * mm, "end": v(6.16, -17.22) * mm});
            skLineSegment(sketch, "E4904", {"start": v(6.16, -17.22) * mm, "end": v(6.18, -17.27) * mm});
            skLineSegment(sketch, "E4905", {"start": v(6.18, -17.27) * mm, "end": v(6.22, -17.3) * mm});
            skLineSegment(sketch, "E4906", {"start": v(6.22, -17.3) * mm, "end": v(6.26, -17.3) * mm});
            skLineSegment(sketch, "E4907", {"start": v(2.8, -16.5) * mm, "end": v(2.84, -16.48) * mm});
            skLineSegment(sketch, "E4908", {"start": v(2.84, -16.48) * mm, "end": v(2.9, -16.45) * mm});
            skLineSegment(sketch, "E4909", {"start": v(2.9, -16.45) * mm, "end": v(3.11, -16.31) * mm});
            skLineSegment(sketch, "E4910", {"start": v(3.11, -16.31) * mm, "end": v(3.42, -16.1) * mm});
            skLineSegment(sketch, "E4911", {"start": v(3.42, -16.1) * mm, "end": v(3.79, -15.83) * mm});
            skLineSegment(sketch, "E4912", {"start": v(3.79, -15.83) * mm, "end": v(4.68, -15.17) * mm});
            skLineSegment(sketch, "E4913", {"start": v(4.68, -15.17) * mm, "end": v(5.62, -14.43) * mm});
            skLineSegment(sketch, "E4914", {"start": v(5.62, -14.43) * mm, "end": v(6.92, -13.4) * mm});
            skLineSegment(sketch, "E4915", {"start": v(6.92, -13.4) * mm, "end": v(8.59, -11.74) * mm});
            skLineSegment(sketch, "E4916", {"start": v(8.59, -11.74) * mm, "end": v(9.47, -10.56) * mm});
            skLineSegment(sketch, "E4917", {"start": v(9.47, -10.56) * mm, "end": v(10.1, -9.23) * mm});
            skLineSegment(sketch, "E4918", {"start": v(10.1, -9.23) * mm, "end": v(10.1, -8.2) * mm});
            skLineSegment(sketch, "E4919", {"start": v(10.1, -8.2) * mm, "end": v(10, -7.93) * mm});
            skLineSegment(sketch, "E4920", {"start": v(10, -7.93) * mm, "end": v(9.95, -7.82) * mm});
            skLineSegment(sketch, "E4921", {"start": v(9.95, -7.82) * mm, "end": v(9.9, -7.72) * mm});
            skLineSegment(sketch, "E4922", {"start": v(9.9, -7.72) * mm, "end": v(9.83, -7.62) * mm});
            skLineSegment(sketch, "E4923", {"start": v(9.83, -7.62) * mm, "end": v(9.76, -7.53) * mm});
            skLineSegment(sketch, "E4924", {"start": v(9.76, -7.53) * mm, "end": v(9.7, -7.45) * mm});
            skLineSegment(sketch, "E4925", {"start": v(9.7, -7.45) * mm, "end": v(9.64, -7.4) * mm});
            skLineSegment(sketch, "E4926", {"start": v(9.64, -7.4) * mm, "end": v(9.58, -7.35) * mm});
            skLineSegment(sketch, "E4927", {"start": v(9.58, -7.35) * mm, "end": v(9.54, -7.34) * mm});
            skLineSegment(sketch, "E4928", {"start": v(9.54, -7.34) * mm, "end": v(9.47, -7.34) * mm});
            skLineSegment(sketch, "E4929", {"start": v(9.47, -7.34) * mm, "end": v(9.36, -8.57) * mm});
            skLineSegment(sketch, "E4930", {"start": v(9.36, -8.57) * mm, "end": v(9.17, -9.14) * mm});
            skLineSegment(sketch, "E4931", {"start": v(9.17, -9.14) * mm, "end": v(9.08, -9.4) * mm});
            skLineSegment(sketch, "E4932", {"start": v(9.08, -9.4) * mm, "end": v(8.99, -9.66) * mm});
            skLineSegment(sketch, "E4933", {"start": v(8.99, -9.66) * mm, "end": v(8.88, -9.9) * mm});
            skLineSegment(sketch, "E4934", {"start": v(8.88, -9.9) * mm, "end": v(8.76, -10.13) * mm});
            skLineSegment(sketch, "E4935", {"start": v(8.76, -10.13) * mm, "end": v(8.63, -10.36) * mm});
            skLineSegment(sketch, "E4936", {"start": v(8.63, -10.36) * mm, "end": v(8.48, -10.6) * mm});
            skLineSegment(sketch, "E4937", {"start": v(8.48, -10.6) * mm, "end": v(8.31, -10.83) * mm});
            skLineSegment(sketch, "E4938", {"start": v(8.31, -10.83) * mm, "end": v(8.12, -11.08) * mm});
            skLineSegment(sketch, "E4939", {"start": v(8.12, -11.08) * mm, "end": v(7.9, -11.33) * mm});
            skLineSegment(sketch, "E4940", {"start": v(7.9, -11.33) * mm, "end": v(7.65, -11.6) * mm});
            skLineSegment(sketch, "E4941", {"start": v(7.65, -11.6) * mm, "end": v(7.36, -11.9) * mm});
            skLineSegment(sketch, "E4942", {"start": v(7.36, -11.9) * mm, "end": v(7.04, -12.22) * mm});
            skLineSegment(sketch, "E4943", {"start": v(7.04, -12.22) * mm, "end": v(6.27, -12.93) * mm});
            skLineSegment(sketch, "E4944", {"start": v(6.27, -12.93) * mm, "end": v(5.32, -13.8) * mm});
            skLineSegment(sketch, "E4945", {"start": v(5.32, -13.8) * mm, "end": v(4.15, -14.84) * mm});
            skLineSegment(sketch, "E4946", {"start": v(4.15, -14.84) * mm, "end": v(2.86, -16.18) * mm});
            skLineSegment(sketch, "E4947", {"start": v(2.86, -16.18) * mm, "end": v(2.75, -16.5) * mm});
            skLineSegment(sketch, "E4948", {"start": v(2.75, -16.5) * mm, "end": v(2.8, -16.5) * mm});
            skLineSegment(sketch, "E4949", {"start": v(-2.74, -11.74) * mm, "end": v(-2.74, -11.55) * mm});
            skLineSegment(sketch, "E4950", {"start": v(-2.74, -11.55) * mm, "end": v(-3.4, -11.5) * mm});
            skLineSegment(sketch, "E4951", {"start": v(-3.4, -11.5) * mm, "end": v(-3.45, -11.7) * mm});
            skLineSegment(sketch, "E4952", {"start": v(-3.45, -11.7) * mm, "end": v(-3.5, -11.91) * mm});
            skLineSegment(sketch, "E4953", {"start": v(-3.5, -11.91) * mm, "end": v(-3.5, -12.08) * mm});
            skLineSegment(sketch, "E4954", {"start": v(-3.5, -12.08) * mm, "end": v(-3.5, -12.14) * mm});
            skLineSegment(sketch, "E4955", {"start": v(-3.5, -12.14) * mm, "end": v(-3.5, -12.2) * mm});
            skLineSegment(sketch, "E4956", {"start": v(-3.5, -12.2) * mm, "end": v(-3.47, -12.22) * mm});
            skLineSegment(sketch, "E4957", {"start": v(-3.47, -12.22) * mm, "end": v(-3.44, -12.23) * mm});
            skLineSegment(sketch, "E4958", {"start": v(-3.44, -12.23) * mm, "end": v(-3.4, -12.22) * mm});
            skLineSegment(sketch, "E4959", {"start": v(-3.4, -12.22) * mm, "end": v(-3.3, -12.19) * mm});
            skLineSegment(sketch, "E4960", {"start": v(-3.3, -12.19) * mm, "end": v(-3.06, -12.08) * mm});
            skLineSegment(sketch, "E4961", {"start": v(-3.06, -12.08) * mm, "end": v(-2.74, -11.92) * mm});
            skLineSegment(sketch, "E4962", {"start": v(-2.74, -11.92) * mm, "end": v(-2.74, -11.74) * mm});
            skLineSegment(sketch, "E4963", {"start": v(-0.97, -11.15) * mm, "end": v(-0.98, -11.14) * mm});
            skLineSegment(sketch, "E4964", {"start": v(-0.98, -11.14) * mm, "end": v(-1, -11.12) * mm});
            skLineSegment(sketch, "E4965", {"start": v(-1, -11.12) * mm, "end": v(-1.07, -11.08) * mm});
            skLineSegment(sketch, "E4966", {"start": v(-1.07, -11.08) * mm, "end": v(-1.3, -10.99) * mm});
            skLineSegment(sketch, "E4967", {"start": v(-1.3, -10.99) * mm, "end": v(-1.57, -10.9) * mm});
            skLineSegment(sketch, "E4968", {"start": v(-1.57, -10.9) * mm, "end": v(-1.7, -10.88) * mm});
            skLineSegment(sketch, "E4969", {"start": v(-1.7, -10.88) * mm, "end": v(-1.78, -10.88) * mm});
            skLineSegment(sketch, "E4970", {"start": v(-1.78, -10.88) * mm, "end": v(-1.9, -10.88) * mm});
            skLineSegment(sketch, "E4971", {"start": v(-1.9, -10.88) * mm, "end": v(-1.84, -11.28) * mm});
            skLineSegment(sketch, "E4972", {"start": v(-1.84, -11.28) * mm, "end": v(-1.52, -11.3) * mm});
            skLineSegment(sketch, "E4973", {"start": v(-1.52, -11.3) * mm, "end": v(-1.29, -11.3) * mm});
            skLineSegment(sketch, "E4974", {"start": v(-1.29, -11.3) * mm, "end": v(-1.2, -11.3) * mm});
            skLineSegment(sketch, "E4975", {"start": v(-1.2, -11.3) * mm, "end": v(-1.12, -11.28) * mm});
            skLineSegment(sketch, "E4976", {"start": v(-1.12, -11.28) * mm, "end": v(-1.06, -11.25) * mm});
            skLineSegment(sketch, "E4977", {"start": v(-1.06, -11.25) * mm, "end": v(-1.01, -11.23) * mm});
            skLineSegment(sketch, "E4978", {"start": v(-1.01, -11.23) * mm, "end": v(-0.98, -11.2) * mm});
            skLineSegment(sketch, "E4979", {"start": v(-0.98, -11.2) * mm, "end": v(-0.97, -11.15) * mm});
            skLineSegment(sketch, "E4980", {"start": v(-0.85, 41.83) * mm, "end": v(-0.82, 41.84) * mm});
            skLineSegment(sketch, "E4981", {"start": v(-0.82, 41.84) * mm, "end": v(-0.8, 41.88) * mm});
            skLineSegment(sketch, "E4982", {"start": v(-0.8, 41.88) * mm, "end": v(-0.8, 41.9) * mm});
            skLineSegment(sketch, "E4983", {"start": v(-0.8, 41.9) * mm, "end": v(-0.72, 41.95) * mm});
            skLineSegment(sketch, "E4984", {"start": v(-0.72, 41.95) * mm, "end": v(-0.14, 41.95) * mm});
            skLineSegment(sketch, "E4985", {"start": v(-0.14, 41.95) * mm, "end": v(-0.07, 41.86) * mm});
            skLineSegment(sketch, "E4986", {"start": v(-0.07, 41.86) * mm, "end": v(0, 41.95) * mm});
            skLineSegment(sketch, "E4987", {"start": v(0, 41.95) * mm, "end": v(0, 41.97) * mm});
            skLineSegment(sketch, "E4988", {"start": v(0, 41.97) * mm, "end": v(0, 42.02) * mm});
            skLineSegment(sketch, "E4989", {"start": v(0, 42.02) * mm, "end": v(-0.03, 42.04) * mm});
            skLineSegment(sketch, "E4990", {"start": v(-0.03, 42.04) * mm, "end": v(-0.15, 42.07) * mm});
            skLineSegment(sketch, "E4991", {"start": v(-0.15, 42.07) * mm, "end": v(-0.3, 42.05) * mm});
            skLineSegment(sketch, "E4992", {"start": v(-0.3, 42.05) * mm, "end": v(-0.32, 42.1) * mm});
            skLineSegment(sketch, "E4993", {"start": v(-0.32, 42.1) * mm, "end": v(-0.25, 42.18) * mm});
            skLineSegment(sketch, "E4994", {"start": v(-0.25, 42.18) * mm, "end": v(0, 42.53) * mm});
            skLineSegment(sketch, "E4995", {"start": v(0, 42.53) * mm, "end": v(0.11, 42.74) * mm});
            skLineSegment(sketch, "E4996", {"start": v(0.11, 42.74) * mm, "end": v(0.13, 42.8) * mm});
            skLineSegment(sketch, "E4997", {"start": v(0.13, 42.8) * mm, "end": v(0.15, 42.87) * mm});
            skLineSegment(sketch, "E4998", {"start": v(0.15, 42.87) * mm, "end": v(0.15, 42.88) * mm});
            skLineSegment(sketch, "E4999", {"start": v(0.15, 42.88) * mm, "end": v(0.22, 42.83) * mm});
            skLineSegment(sketch, "E5000", {"start": v(0.22, 42.83) * mm, "end": v(0.27, 42.8) * mm});
            skLineSegment(sketch, "E5001", {"start": v(0.27, 42.8) * mm, "end": v(0.3, 42.79) * mm});
            skLineSegment(sketch, "E5002", {"start": v(0.3, 42.79) * mm, "end": v(0.26, 42.9) * mm});
            skLineSegment(sketch, "E5003", {"start": v(0.26, 42.9) * mm, "end": v(0.23, 43) * mm});
            skLineSegment(sketch, "E5004", {"start": v(0.23, 43) * mm, "end": v(0.2, 43.2) * mm});
            skLineSegment(sketch, "E5005", {"start": v(0.2, 43.2) * mm, "end": v(0.18, 43.2) * mm});
            skLineSegment(sketch, "E5006", {"start": v(0.18, 43.2) * mm, "end": v(0.06, 43.23) * mm});
            skLineSegment(sketch, "E5007", {"start": v(0.06, 43.23) * mm, "end": v(-0.08, 43.28) * mm});
            skLineSegment(sketch, "E5008", {"start": v(-0.08, 43.28) * mm, "end": v(-0.16, 43.31) * mm});
            skLineSegment(sketch, "E5009", {"start": v(-0.16, 43.31) * mm, "end": v(-0.17, 43.31) * mm});
            skLineSegment(sketch, "E5010", {"start": v(-0.17, 43.31) * mm, "end": v(-0.18, 43.3) * mm});
            skLineSegment(sketch, "E5011", {"start": v(-0.18, 43.3) * mm, "end": v(-0.2, 43.18) * mm});
            skLineSegment(sketch, "E5012", {"start": v(-0.2, 43.18) * mm, "end": v(-0.2, 43.09) * mm});
            skLineSegment(sketch, "E5013", {"start": v(-0.2, 43.09) * mm, "end": v(-0.28, 42.87) * mm});
            skLineSegment(sketch, "E5014", {"start": v(-0.28, 42.87) * mm, "end": v(-0.21, 42.87) * mm});
            skLineSegment(sketch, "E5015", {"start": v(-0.21, 42.87) * mm, "end": v(-0.16, 42.9) * mm});
            skLineSegment(sketch, "E5016", {"start": v(-0.16, 42.9) * mm, "end": v(-0.1, 42.93) * mm});
            skLineSegment(sketch, "E5017", {"start": v(-0.1, 42.93) * mm, "end": v(-0.1, 42.9) * mm});
            skLineSegment(sketch, "E5018", {"start": v(-0.1, 42.9) * mm, "end": v(-0.12, 42.85) * mm});
            skLineSegment(sketch, "E5019", {"start": v(-0.12, 42.85) * mm, "end": v(-0.2, 42.68) * mm});
            skLineSegment(sketch, "E5020", {"start": v(-0.2, 42.68) * mm, "end": v(-0.3, 42.47) * mm});
            skLineSegment(sketch, "E5021", {"start": v(-0.3, 42.47) * mm, "end": v(-0.41, 42.26) * mm});
            skLineSegment(sketch, "E5022", {"start": v(-0.41, 42.26) * mm, "end": v(-0.5, 42.1) * mm});
            skLineSegment(sketch, "E5023", {"start": v(-0.5, 42.1) * mm, "end": v(-0.62, 42.1) * mm});
            skLineSegment(sketch, "E5024", {"start": v(-0.62, 42.1) * mm, "end": v(-0.74, 42.15) * mm});
            skLineSegment(sketch, "E5025", {"start": v(-0.74, 42.15) * mm, "end": v(-0.84, 42.13) * mm});
            skLineSegment(sketch, "E5026", {"start": v(-0.84, 42.13) * mm, "end": v(-0.87, 42.08) * mm});
            skLineSegment(sketch, "E5027", {"start": v(-0.87, 42.08) * mm, "end": v(-0.9, 42.08) * mm});
            skLineSegment(sketch, "E5028", {"start": v(-0.9, 42.08) * mm, "end": v(-0.97, 42.07) * mm});
            skLineSegment(sketch, "E5029", {"start": v(-0.97, 42.07) * mm, "end": v(-1.01, 42.05) * mm});
            skLineSegment(sketch, "E5030", {"start": v(-1.01, 42.05) * mm, "end": v(-1.03, 42.03) * mm});
            skLineSegment(sketch, "E5031", {"start": v(-1.03, 42.03) * mm, "end": v(-1.04, 41.97) * mm});
            skLineSegment(sketch, "E5032", {"start": v(-1.04, 41.97) * mm, "end": v(-1.04, 41.94) * mm});
            skLineSegment(sketch, "E5033", {"start": v(-1.04, 41.94) * mm, "end": v(-1.03, 41.93) * mm});
            skLineSegment(sketch, "E5034", {"start": v(-1.03, 41.93) * mm, "end": v(-0.96, 41.97) * mm});
            skLineSegment(sketch, "E5035", {"start": v(-0.96, 41.97) * mm, "end": v(-0.9, 42) * mm});
            skLineSegment(sketch, "E5036", {"start": v(-0.9, 42) * mm, "end": v(-0.88, 41.99) * mm});
            skLineSegment(sketch, "E5037", {"start": v(-0.88, 41.99) * mm, "end": v(-0.89, 41.96) * mm});
            skLineSegment(sketch, "E5038", {"start": v(-0.89, 41.96) * mm, "end": v(-0.9, 41.9) * mm});
            skLineSegment(sketch, "E5039", {"start": v(-0.9, 41.9) * mm, "end": v(-0.88, 41.86) * mm});
            skLineSegment(sketch, "E5040", {"start": v(-0.88, 41.86) * mm, "end": v(-0.87, 41.83) * mm});
            skLineSegment(sketch, "E5041", {"start": v(-0.87, 41.83) * mm, "end": v(-0.85, 41.83) * mm});
            skLineSegment(sketch, "E5042", {"start": v(0.41, 41.83) * mm, "end": v(0.44, 41.86) * mm});
            skLineSegment(sketch, "E5043", {"start": v(0.44, 41.86) * mm, "end": v(0.47, 41.9) * mm});
            skLineSegment(sketch, "E5044", {"start": v(0.47, 41.9) * mm, "end": v(0.56, 41.93) * mm});
            skLineSegment(sketch, "E5045", {"start": v(0.56, 41.93) * mm, "end": v(1.13, 41.93) * mm});
            skLineSegment(sketch, "E5046", {"start": v(1.13, 41.93) * mm, "end": v(1.2, 41.9) * mm});
            skLineSegment(sketch, "E5047", {"start": v(1.2, 41.9) * mm, "end": v(1.25, 41.84) * mm});
            skLineSegment(sketch, "E5048", {"start": v(1.25, 41.84) * mm, "end": v(1.3, 41.9) * mm});
            skLineSegment(sketch, "E5049", {"start": v(1.3, 41.9) * mm, "end": v(1.32, 41.96) * mm});
            skLineSegment(sketch, "E5050", {"start": v(1.32, 41.96) * mm, "end": v(1.3, 42.01) * mm});
            skLineSegment(sketch, "E5051", {"start": v(1.3, 42.01) * mm, "end": v(1.23, 42.06) * mm});
            skLineSegment(sketch, "E5052", {"start": v(1.23, 42.06) * mm, "end": v(0.98, 42.05) * mm});
            skLineSegment(sketch, "E5053", {"start": v(0.98, 42.05) * mm, "end": v(0.95, 42.12) * mm});
            skLineSegment(sketch, "E5054", {"start": v(0.95, 42.12) * mm, "end": v(0.9, 42.24) * mm});
            skLineSegment(sketch, "E5055", {"start": v(0.9, 42.24) * mm, "end": v(0.85, 42.38) * mm});
            skLineSegment(sketch, "E5056", {"start": v(0.85, 42.38) * mm, "end": v(0.81, 42.54) * mm});
            skLineSegment(sketch, "E5057", {"start": v(0.81, 42.54) * mm, "end": v(0.8, 42.71) * mm});
            skLineSegment(sketch, "E5058", {"start": v(0.8, 42.71) * mm, "end": v(0.78, 42.84) * mm});
            skLineSegment(sketch, "E5059", {"start": v(0.78, 42.84) * mm, "end": v(0.89, 42.8) * mm});
            skLineSegment(sketch, "E5060", {"start": v(0.89, 42.8) * mm, "end": v(0.97, 42.8) * mm});
            skLineSegment(sketch, "E5061", {"start": v(0.97, 42.8) * mm, "end": v(1, 42.82) * mm});
            skLineSegment(sketch, "E5062", {"start": v(1, 42.82) * mm, "end": v(0.87, 42.94) * mm});
            skLineSegment(sketch, "E5063", {"start": v(0.87, 42.94) * mm, "end": v(0.78, 43.12) * mm});
            skLineSegment(sketch, "E5064", {"start": v(0.78, 43.12) * mm, "end": v(0.77, 43.45) * mm});
            skLineSegment(sketch, "E5065", {"start": v(0.77, 43.45) * mm, "end": v(0.53, 43.64) * mm});
            skLineSegment(sketch, "E5066", {"start": v(0.53, 43.64) * mm, "end": v(0.38, 43.82) * mm});
            skLineSegment(sketch, "E5067", {"start": v(0.38, 43.82) * mm, "end": v(0.3, 43.99) * mm});
            skLineSegment(sketch, "E5068", {"start": v(0.3, 43.99) * mm, "end": v(0.29, 44.11) * mm});
            skLineSegment(sketch, "E5069", {"start": v(0.29, 44.11) * mm, "end": v(0.48, 43.83) * mm});
            skLineSegment(sketch, "E5070", {"start": v(0.48, 43.83) * mm, "end": v(0.96, 43.33) * mm});
            skLineSegment(sketch, "E5071", {"start": v(0.96, 43.33) * mm, "end": v(1.02, 43.18) * mm});
            skLineSegment(sketch, "E5072", {"start": v(1.02, 43.18) * mm, "end": v(1.04, 42.95) * mm});
            skLineSegment(sketch, "E5073", {"start": v(1.04, 42.95) * mm, "end": v(1.07, 42.92) * mm});
            skLineSegment(sketch, "E5074", {"start": v(1.07, 42.92) * mm, "end": v(1.08, 42.95) * mm});
            skLineSegment(sketch, "E5075", {"start": v(1.08, 42.95) * mm, "end": v(1.08, 42.97) * mm});
            skLineSegment(sketch, "E5076", {"start": v(1.08, 42.97) * mm, "end": v(1.11, 43.14) * mm});
            skLineSegment(sketch, "E5077", {"start": v(1.11, 43.14) * mm, "end": v(1.1, 43.33) * mm});
            skLineSegment(sketch, "E5078", {"start": v(1.1, 43.33) * mm, "end": v(1.01, 43.5) * mm});
            skLineSegment(sketch, "E5079", {"start": v(1.01, 43.5) * mm, "end": v(0.88, 43.64) * mm});
            skLineSegment(sketch, "E5080", {"start": v(0.88, 43.64) * mm, "end": v(0.62, 43.9) * mm});
            skLineSegment(sketch, "E5081", {"start": v(0.62, 43.9) * mm, "end": v(0.5, 44.02) * mm});
            skLineSegment(sketch, "E5082", {"start": v(0.5, 44.02) * mm, "end": v(0.41, 44.14) * mm});
            skLineSegment(sketch, "E5083", {"start": v(0.41, 44.14) * mm, "end": v(0.5, 44.08) * mm});
            skLineSegment(sketch, "E5084", {"start": v(0.5, 44.08) * mm, "end": v(0.66, 43.98) * mm});
            skLineSegment(sketch, "E5085", {"start": v(0.66, 43.98) * mm, "end": v(0.74, 43.94) * mm});
            skLineSegment(sketch, "E5086", {"start": v(0.74, 43.94) * mm, "end": v(0.8, 43.91) * mm});
            skLineSegment(sketch, "E5087", {"start": v(0.8, 43.91) * mm, "end": v(0.87, 43.9) * mm});
            skLineSegment(sketch, "E5088", {"start": v(0.87, 43.9) * mm, "end": v(1.05, 43.9) * mm});
            skLineSegment(sketch, "E5089", {"start": v(1.05, 43.9) * mm, "end": v(1.2, 43.97) * mm});
            skLineSegment(sketch, "E5090", {"start": v(1.2, 43.97) * mm, "end": v(1.25, 44.02) * mm});
            skLineSegment(sketch, "E5091", {"start": v(1.25, 44.02) * mm, "end": v(1.3, 44.07) * mm});
            skLineSegment(sketch, "E5092", {"start": v(1.3, 44.07) * mm, "end": v(1.3, 44.08) * mm});
            skLineSegment(sketch, "E5093", {"start": v(1.3, 44.08) * mm, "end": v(1.02, 44.08) * mm});
            skLineSegment(sketch, "E5094", {"start": v(1.02, 44.08) * mm, "end": v(0.84, 44.12) * mm});
            skLineSegment(sketch, "E5095", {"start": v(0.84, 44.12) * mm, "end": v(0.78, 44.15) * mm});
            skLineSegment(sketch, "E5096", {"start": v(0.78, 44.15) * mm, "end": v(0.7, 44.2) * mm});
            skLineSegment(sketch, "E5097", {"start": v(0.7, 44.2) * mm, "end": v(0.67, 44.22) * mm});
            skLineSegment(sketch, "E5098", {"start": v(0.67, 44.22) * mm, "end": v(0.8, 44.24) * mm});
            skLineSegment(sketch, "E5099", {"start": v(0.8, 44.24) * mm, "end": v(0.88, 44.3) * mm});
            skLineSegment(sketch, "E5100", {"start": v(0.88, 44.3) * mm, "end": v(0.93, 44.38) * mm});
            skLineSegment(sketch, "E5101", {"start": v(0.93, 44.38) * mm, "end": v(0.92, 44.4) * mm});
            skLineSegment(sketch, "E5102", {"start": v(0.92, 44.4) * mm, "end": v(0.73, 44.4) * mm});
            skLineSegment(sketch, "E5103", {"start": v(0.73, 44.4) * mm, "end": v(0.69, 44.43) * mm});
            skLineSegment(sketch, "E5104", {"start": v(0.69, 44.43) * mm, "end": v(0.75, 44.44) * mm});
            skLineSegment(sketch, "E5105", {"start": v(0.75, 44.44) * mm, "end": v(0.88, 44.47) * mm});
            skLineSegment(sketch, "E5106", {"start": v(0.88, 44.47) * mm, "end": v(0.93, 44.5) * mm});
            skLineSegment(sketch, "E5107", {"start": v(0.93, 44.5) * mm, "end": v(1.03, 44.6) * mm});
            skLineSegment(sketch, "E5108", {"start": v(1.03, 44.6) * mm, "end": v(1.01, 44.62) * mm});
            skLineSegment(sketch, "E5109", {"start": v(1.01, 44.62) * mm, "end": v(0.75, 44.6) * mm});
            skLineSegment(sketch, "E5110", {"start": v(0.75, 44.6) * mm, "end": v(0.75, 44.63) * mm});
            skLineSegment(sketch, "E5111", {"start": v(0.75, 44.63) * mm, "end": v(0.8, 44.64) * mm});
            skLineSegment(sketch, "E5112", {"start": v(0.8, 44.64) * mm, "end": v(0.9, 44.68) * mm});
            skLineSegment(sketch, "E5113", {"start": v(0.9, 44.68) * mm, "end": v(0.96, 44.7) * mm});
            skLineSegment(sketch, "E5114", {"start": v(0.96, 44.7) * mm, "end": v(1, 44.76) * mm});
            skLineSegment(sketch, "E5115", {"start": v(1, 44.76) * mm, "end": v(1.04, 44.8) * mm});
            skLineSegment(sketch, "E5116", {"start": v(1.04, 44.8) * mm, "end": v(1.04, 44.84) * mm});
            skLineSegment(sketch, "E5117", {"start": v(1.04, 44.84) * mm, "end": v(1.06, 44.86) * mm});
            skLineSegment(sketch, "E5118", {"start": v(1.06, 44.86) * mm, "end": v(1.07, 44.87) * mm});
            skLineSegment(sketch, "E5119", {"start": v(1.07, 44.87) * mm, "end": v(1.06, 44.89) * mm});
            skLineSegment(sketch, "E5120", {"start": v(1.06, 44.89) * mm, "end": v(1, 44.86) * mm});
            skLineSegment(sketch, "E5121", {"start": v(1, 44.86) * mm, "end": v(0.88, 44.81) * mm});
            skLineSegment(sketch, "E5122", {"start": v(0.88, 44.81) * mm, "end": v(0.76, 44.8) * mm});
            skLineSegment(sketch, "E5123", {"start": v(0.76, 44.8) * mm, "end": v(0.73, 44.8) * mm});
            skLineSegment(sketch, "E5124", {"start": v(0.73, 44.8) * mm, "end": v(0.94, 44.88) * mm});
            skLineSegment(sketch, "E5125", {"start": v(0.94, 44.88) * mm, "end": v(0.99, 44.93) * mm});
            skLineSegment(sketch, "E5126", {"start": v(0.99, 44.93) * mm, "end": v(1.05, 45) * mm});
            skLineSegment(sketch, "E5127", {"start": v(1.05, 45) * mm, "end": v(1.07, 45.05) * mm});
            skLineSegment(sketch, "E5128", {"start": v(1.07, 45.05) * mm, "end": v(1.07, 45.09) * mm});
            skLineSegment(sketch, "E5129", {"start": v(1.07, 45.09) * mm, "end": v(1.06, 45.13) * mm});
            skLineSegment(sketch, "E5130", {"start": v(1.06, 45.13) * mm, "end": v(1, 45.09) * mm});
            skLineSegment(sketch, "E5131", {"start": v(1, 45.09) * mm, "end": v(0.93, 45.05) * mm});
            skLineSegment(sketch, "E5132", {"start": v(0.93, 45.05) * mm, "end": v(0.89, 45.04) * mm});
            skLineSegment(sketch, "E5133", {"start": v(0.89, 45.04) * mm, "end": v(0.83, 45.04) * mm});
            skLineSegment(sketch, "E5134", {"start": v(0.83, 45.04) * mm, "end": v(0.8, 45.04) * mm});
            skLineSegment(sketch, "E5135", {"start": v(0.8, 45.04) * mm, "end": v(0.96, 45.14) * mm});
            skLineSegment(sketch, "E5136", {"start": v(0.96, 45.14) * mm, "end": v(1.22, 45.33) * mm});
            skLineSegment(sketch, "E5137", {"start": v(1.22, 45.33) * mm, "end": v(1.44, 45.52) * mm});
            skLineSegment(sketch, "E5138", {"start": v(1.44, 45.52) * mm, "end": v(1.56, 45.62) * mm});
            skLineSegment(sketch, "E5139", {"start": v(1.56, 45.62) * mm, "end": v(1.8, 45.91) * mm});
            skLineSegment(sketch, "E5140", {"start": v(1.8, 45.91) * mm, "end": v(2.02, 46.23) * mm});
            skLineSegment(sketch, "E5141", {"start": v(2.02, 46.23) * mm, "end": v(2.14, 46.48) * mm});
            skLineSegment(sketch, "E5142", {"start": v(2.14, 46.48) * mm, "end": v(2.16, 46.54) * mm});
            skLineSegment(sketch, "E5143", {"start": v(2.16, 46.54) * mm, "end": v(2.17, 46.66) * mm});
            skLineSegment(sketch, "E5144", {"start": v(2.17, 46.66) * mm, "end": v(2.17, 46.72) * mm});
            skLineSegment(sketch, "E5145", {"start": v(2.17, 46.72) * mm, "end": v(2.14, 46.77) * mm});
            skLineSegment(sketch, "E5146", {"start": v(2.14, 46.77) * mm, "end": v(2.08, 46.86) * mm});
            skLineSegment(sketch, "E5147", {"start": v(2.08, 46.86) * mm, "end": v(2.05, 46.9) * mm});
            skLineSegment(sketch, "E5148", {"start": v(2.05, 46.9) * mm, "end": v(2.04, 46.89) * mm});
            skLineSegment(sketch, "E5149", {"start": v(2.04, 46.89) * mm, "end": v(2.02, 46.77) * mm});
            skLineSegment(sketch, "E5150", {"start": v(2.02, 46.77) * mm, "end": v(1.98, 46.58) * mm});
            skLineSegment(sketch, "E5151", {"start": v(1.98, 46.58) * mm, "end": v(1.9, 46.37) * mm});
            skLineSegment(sketch, "E5152", {"start": v(1.9, 46.37) * mm, "end": v(1.8, 46.15) * mm});
            skLineSegment(sketch, "E5153", {"start": v(1.8, 46.15) * mm, "end": v(1.68, 45.96) * mm});
            skLineSegment(sketch, "E5154", {"start": v(1.68, 45.96) * mm, "end": v(1.6, 45.84) * mm});
            skLineSegment(sketch, "E5155", {"start": v(1.6, 45.84) * mm, "end": v(1.35, 45.57) * mm});
            skLineSegment(sketch, "E5156", {"start": v(1.35, 45.57) * mm, "end": v(1.02, 45.3) * mm});
            skLineSegment(sketch, "E5157", {"start": v(1.02, 45.3) * mm, "end": v(0.91, 45.23) * mm});
            skLineSegment(sketch, "E5158", {"start": v(0.91, 45.23) * mm, "end": v(0.72, 45.1) * mm});
            skLineSegment(sketch, "E5159", {"start": v(0.72, 45.1) * mm, "end": v(0.59, 45) * mm});
            skLineSegment(sketch, "E5160", {"start": v(0.59, 45) * mm, "end": v(0.51, 44.91) * mm});
            skLineSegment(sketch, "E5161", {"start": v(0.51, 44.91) * mm, "end": v(0.45, 44.83) * mm});
            skLineSegment(sketch, "E5162", {"start": v(0.45, 44.83) * mm, "end": v(0.42, 44.77) * mm});
            skLineSegment(sketch, "E5163", {"start": v(0.42, 44.77) * mm, "end": v(0.37, 44.6) * mm});
            skLineSegment(sketch, "E5164", {"start": v(0.37, 44.6) * mm, "end": v(0.34, 44.53) * mm});
            skLineSegment(sketch, "E5165", {"start": v(0.34, 44.53) * mm, "end": v(0.3, 44.48) * mm});
            skLineSegment(sketch, "E5166", {"start": v(0.3, 44.48) * mm, "end": v(0.27, 44.44) * mm});
            skLineSegment(sketch, "E5167", {"start": v(0.27, 44.44) * mm, "end": v(0.23, 44.4) * mm});
            skLineSegment(sketch, "E5168", {"start": v(0.23, 44.4) * mm, "end": v(0.19, 44.38) * mm});
            skLineSegment(sketch, "E5169", {"start": v(0.19, 44.38) * mm, "end": v(0.15, 44.37) * mm});
            skLineSegment(sketch, "E5170", {"start": v(0.15, 44.37) * mm, "end": v(0.14, 44.37) * mm});
            skLineSegment(sketch, "E5171", {"start": v(0.14, 44.37) * mm, "end": v(0.17, 44.42) * mm});
            skLineSegment(sketch, "E5172", {"start": v(0.17, 44.42) * mm, "end": v(0.25, 44.54) * mm});
            skLineSegment(sketch, "E5173", {"start": v(0.25, 44.54) * mm, "end": v(0.3, 44.63) * mm});
            skLineSegment(sketch, "E5174", {"start": v(0.3, 44.63) * mm, "end": v(0.34, 44.79) * mm});
            skLineSegment(sketch, "E5175", {"start": v(0.34, 44.79) * mm, "end": v(0.4, 44.94) * mm});
            skLineSegment(sketch, "E5176", {"start": v(0.4, 44.94) * mm, "end": v(0.43, 45.01) * mm});
            skLineSegment(sketch, "E5177", {"start": v(0.43, 45.01) * mm, "end": v(0.48, 45.08) * mm});
            skLineSegment(sketch, "E5178", {"start": v(0.48, 45.08) * mm, "end": v(0.6, 45.22) * mm});
            skLineSegment(sketch, "E5179", {"start": v(0.6, 45.22) * mm, "end": v(0.8, 45.39) * mm});
            skLineSegment(sketch, "E5180", {"start": v(0.8, 45.39) * mm, "end": v(0.94, 45.52) * mm});
            skLineSegment(sketch, "E5181", {"start": v(0.94, 45.52) * mm, "end": v(1.09, 45.67) * mm});
            skLineSegment(sketch, "E5182", {"start": v(1.09, 45.67) * mm, "end": v(1.24, 45.82) * mm});
            skLineSegment(sketch, "E5183", {"start": v(1.24, 45.82) * mm, "end": v(1.39, 46) * mm});
            skLineSegment(sketch, "E5184", {"start": v(1.39, 46) * mm, "end": v(1.5, 46.2) * mm});
            skLineSegment(sketch, "E5185", {"start": v(1.5, 46.2) * mm, "end": v(1.55, 46.4) * mm});
            skLineSegment(sketch, "E5186", {"start": v(1.55, 46.4) * mm, "end": v(1.55, 46.51) * mm});
            skLineSegment(sketch, "E5187", {"start": v(1.55, 46.51) * mm, "end": v(1.5, 46.63) * mm});
            skLineSegment(sketch, "E5188", {"start": v(1.5, 46.63) * mm, "end": v(1.45, 46.66) * mm});
            skLineSegment(sketch, "E5189", {"start": v(1.45, 46.66) * mm, "end": v(1.38, 46.68) * mm});
            skLineSegment(sketch, "E5190", {"start": v(1.38, 46.68) * mm, "end": v(1.36, 46.68) * mm});
            skLineSegment(sketch, "E5191", {"start": v(1.36, 46.68) * mm, "end": v(1.37, 46.63) * mm});
            skLineSegment(sketch, "E5192", {"start": v(1.37, 46.63) * mm, "end": v(1.38, 46.49) * mm});
            skLineSegment(sketch, "E5193", {"start": v(1.38, 46.49) * mm, "end": v(1.38, 46.4) * mm});
            skLineSegment(sketch, "E5194", {"start": v(1.38, 46.4) * mm, "end": v(1.32, 46.23) * mm});
            skLineSegment(sketch, "E5195", {"start": v(1.32, 46.23) * mm, "end": v(1.27, 46.13) * mm});
            skLineSegment(sketch, "E5196", {"start": v(1.27, 46.13) * mm, "end": v(1.2, 46.03) * mm});
            skLineSegment(sketch, "E5197", {"start": v(1.2, 46.03) * mm, "end": v(1.12, 45.92) * mm});
            skLineSegment(sketch, "E5198", {"start": v(1.12, 45.92) * mm, "end": v(1.04, 45.82) * mm});
            skLineSegment(sketch, "E5199", {"start": v(1.04, 45.82) * mm, "end": v(0.95, 45.72) * mm});
            skLineSegment(sketch, "E5200", {"start": v(0.95, 45.72) * mm, "end": v(0.83, 45.61) * mm});
            skLineSegment(sketch, "E5201", {"start": v(0.83, 45.61) * mm, "end": v(0.57, 45.4) * mm});
            skLineSegment(sketch, "E5202", {"start": v(0.57, 45.4) * mm, "end": v(0.5, 45.35) * mm});
            skLineSegment(sketch, "E5203", {"start": v(0.5, 45.35) * mm, "end": v(0.4, 45.23) * mm});
            skLineSegment(sketch, "E5204", {"start": v(0.4, 45.23) * mm, "end": v(0.3, 45.07) * mm});
            skLineSegment(sketch, "E5205", {"start": v(0.3, 45.07) * mm, "end": v(0.22, 44.88) * mm});
            skLineSegment(sketch, "E5206", {"start": v(0.22, 44.88) * mm, "end": v(0.13, 44.65) * mm});
            skLineSegment(sketch, "E5207", {"start": v(0.13, 44.65) * mm, "end": v(0.08, 44.5) * mm});
            skLineSegment(sketch, "E5208", {"start": v(0.08, 44.5) * mm, "end": v(0.06, 44.47) * mm});
            skLineSegment(sketch, "E5209", {"start": v(0.06, 44.47) * mm, "end": v(0, 44.47) * mm});
            skLineSegment(sketch, "E5210", {"start": v(0, 44.47) * mm, "end": v(-0.02, 44.54) * mm});
            skLineSegment(sketch, "E5211", {"start": v(-0.02, 44.54) * mm, "end": v(-0.01, 44.8) * mm});
            skLineSegment(sketch, "E5212", {"start": v(-0.01, 44.8) * mm, "end": v(0.03, 44.89) * mm});
            skLineSegment(sketch, "E5213", {"start": v(0.03, 44.89) * mm, "end": v(0.08, 44.98) * mm});
            skLineSegment(sketch, "E5214", {"start": v(0.08, 44.98) * mm, "end": v(0.13, 45.06) * mm});
            skLineSegment(sketch, "E5215", {"start": v(0.13, 45.06) * mm, "end": v(0.3, 45.25) * mm});
            skLineSegment(sketch, "E5216", {"start": v(0.3, 45.25) * mm, "end": v(0.45, 45.4) * mm});
            skLineSegment(sketch, "E5217", {"start": v(0.45, 45.4) * mm, "end": v(0.5, 45.52) * mm});
            skLineSegment(sketch, "E5218", {"start": v(0.5, 45.52) * mm, "end": v(0.5, 45.69) * mm});
            skLineSegment(sketch, "E5219", {"start": v(0.5, 45.69) * mm, "end": v(0.44, 45.83) * mm});
            skLineSegment(sketch, "E5220", {"start": v(0.44, 45.83) * mm, "end": v(0.65, 45.84) * mm});
            skLineSegment(sketch, "E5221", {"start": v(0.65, 45.84) * mm, "end": v(0.74, 45.88) * mm});
            skLineSegment(sketch, "E5222", {"start": v(0.74, 45.88) * mm, "end": v(0.76, 45.9) * mm});
            skLineSegment(sketch, "E5223", {"start": v(0.76, 45.9) * mm, "end": v(0.8, 45.97) * mm});
            skLineSegment(sketch, "E5224", {"start": v(0.8, 45.97) * mm, "end": v(0.8, 46) * mm});
            skLineSegment(sketch, "E5225", {"start": v(0.8, 46) * mm, "end": v(0.76, 46.02) * mm});
            skLineSegment(sketch, "E5226", {"start": v(0.76, 46.02) * mm, "end": v(0.7, 45.94) * mm});
            skLineSegment(sketch, "E5227", {"start": v(0.7, 45.94) * mm, "end": v(0.62, 45.95) * mm});
            skLineSegment(sketch, "E5228", {"start": v(0.62, 45.95) * mm, "end": v(0.45, 45.99) * mm});
            skLineSegment(sketch, "E5229", {"start": v(0.45, 45.99) * mm, "end": v(0.2, 46.06) * mm});
            skLineSegment(sketch, "E5230", {"start": v(0.2, 46.06) * mm, "end": v(0.08, 46.1) * mm});
            skLineSegment(sketch, "E5231", {"start": v(0.08, 46.1) * mm, "end": v(-0.07, 46.1) * mm});
            skLineSegment(sketch, "E5232", {"start": v(-0.07, 46.1) * mm, "end": v(-0.13, 46.06) * mm});
            skLineSegment(sketch, "E5233", {"start": v(-0.13, 46.06) * mm, "end": v(-0.18, 45.99) * mm});
            skLineSegment(sketch, "E5234", {"start": v(-0.18, 45.99) * mm, "end": v(-0.22, 45.99) * mm});
            skLineSegment(sketch, "E5235", {"start": v(-0.22, 45.99) * mm, "end": v(-0.28, 45.98) * mm});
            skLineSegment(sketch, "E5236", {"start": v(-0.28, 45.98) * mm, "end": v(-0.3, 45.97) * mm});
            skLineSegment(sketch, "E5237", {"start": v(-0.3, 45.97) * mm, "end": v(-0.3, 46) * mm});
            skLineSegment(sketch, "E5238", {"start": v(-0.3, 46) * mm, "end": v(-0.33, 46.05) * mm});
            skLineSegment(sketch, "E5239", {"start": v(-0.33, 46.05) * mm, "end": v(-0.34, 46.06) * mm});
            skLineSegment(sketch, "E5240", {"start": v(-0.34, 46.06) * mm, "end": v(-0.42, 46.05) * mm});
            skLineSegment(sketch, "E5241", {"start": v(-0.42, 46.05) * mm, "end": v(-0.4, 45.96) * mm});
            skLineSegment(sketch, "E5242", {"start": v(-0.4, 45.96) * mm, "end": v(-0.44, 45.94) * mm});
            skLineSegment(sketch, "E5243", {"start": v(-0.44, 45.94) * mm, "end": v(-0.51, 45.9) * mm});
            skLineSegment(sketch, "E5244", {"start": v(-0.51, 45.9) * mm, "end": v(-0.55, 45.84) * mm});
            skLineSegment(sketch, "E5245", {"start": v(-0.55, 45.84) * mm, "end": v(-0.57, 45.81) * mm});
            skLineSegment(sketch, "E5246", {"start": v(-0.57, 45.81) * mm, "end": v(-0.55, 45.79) * mm});
            skLineSegment(sketch, "E5247", {"start": v(-0.55, 45.79) * mm, "end": v(-0.5, 45.81) * mm});
            skLineSegment(sketch, "E5248", {"start": v(-0.5, 45.81) * mm, "end": v(-0.42, 45.84) * mm});
            skLineSegment(sketch, "E5249", {"start": v(-0.42, 45.84) * mm, "end": v(-0.4, 45.84) * mm});
            skLineSegment(sketch, "E5250", {"start": v(-0.4, 45.84) * mm, "end": v(-0.4, 45.75) * mm});
            skLineSegment(sketch, "E5251", {"start": v(-0.4, 45.75) * mm, "end": v(-0.47, 45.74) * mm});
            skLineSegment(sketch, "E5252", {"start": v(-0.47, 45.74) * mm, "end": v(-0.47, 45.73) * mm});
            skLineSegment(sketch, "E5253", {"start": v(-0.47, 45.73) * mm, "end": v(-0.45, 45.69) * mm});
            skLineSegment(sketch, "E5254", {"start": v(-0.45, 45.69) * mm, "end": v(-0.43, 45.66) * mm});
            skLineSegment(sketch, "E5255", {"start": v(-0.43, 45.66) * mm, "end": v(-0.47, 45.6) * mm});
            skLineSegment(sketch, "E5256", {"start": v(-0.47, 45.6) * mm, "end": v(-0.5, 45.6) * mm});
            skLineSegment(sketch, "E5257", {"start": v(-0.5, 45.6) * mm, "end": v(-0.58, 45.6) * mm});
            skLineSegment(sketch, "E5258", {"start": v(-0.58, 45.6) * mm, "end": v(-0.63, 45.61) * mm});
            skLineSegment(sketch, "E5259", {"start": v(-0.63, 45.61) * mm, "end": v(-0.73, 45.56) * mm});
            skLineSegment(sketch, "E5260", {"start": v(-0.73, 45.56) * mm, "end": v(-0.82, 45.56) * mm});
            skLineSegment(sketch, "E5261", {"start": v(-0.82, 45.56) * mm, "end": v(-0.84, 45.52) * mm});
            skLineSegment(sketch, "E5262", {"start": v(-0.84, 45.52) * mm, "end": v(-0.78, 45.46) * mm});
            skLineSegment(sketch, "E5263", {"start": v(-0.78, 45.46) * mm, "end": v(-0.73, 45.46) * mm});
            skLineSegment(sketch, "E5264", {"start": v(-0.73, 45.46) * mm, "end": v(-0.64, 45.48) * mm});
            skLineSegment(sketch, "E5265", {"start": v(-0.64, 45.48) * mm, "end": v(-0.58, 45.5) * mm});
            skLineSegment(sketch, "E5266", {"start": v(-0.58, 45.5) * mm, "end": v(-0.68, 45.43) * mm});
            skLineSegment(sketch, "E5267", {"start": v(-0.68, 45.43) * mm, "end": v(-0.74, 45.34) * mm});
            skLineSegment(sketch, "E5268", {"start": v(-0.74, 45.34) * mm, "end": v(-0.74, 45.29) * mm});
            skLineSegment(sketch, "E5269", {"start": v(-0.74, 45.29) * mm, "end": v(-0.68, 45.22) * mm});
            skLineSegment(sketch, "E5270", {"start": v(-0.68, 45.22) * mm, "end": v(-0.62, 45.2) * mm});
            skLineSegment(sketch, "E5271", {"start": v(-0.62, 45.2) * mm, "end": v(-0.62, 45.27) * mm});
            skLineSegment(sketch, "E5272", {"start": v(-0.62, 45.27) * mm, "end": v(-0.58, 45.32) * mm});
            skLineSegment(sketch, "E5273", {"start": v(-0.58, 45.32) * mm, "end": v(-0.52, 45.43) * mm});
            skLineSegment(sketch, "E5274", {"start": v(-0.52, 45.43) * mm, "end": v(-0.49, 45.5) * mm});
            skLineSegment(sketch, "E5275", {"start": v(-0.49, 45.5) * mm, "end": v(-0.37, 45.38) * mm});
            skLineSegment(sketch, "E5276", {"start": v(-0.37, 45.38) * mm, "end": v(-0.28, 45.38) * mm});
            skLineSegment(sketch, "E5277", {"start": v(-0.28, 45.38) * mm, "end": v(-0.24, 45.42) * mm});
            skLineSegment(sketch, "E5278", {"start": v(-0.24, 45.42) * mm, "end": v(-0.22, 45.45) * mm});
            skLineSegment(sketch, "E5279", {"start": v(-0.22, 45.45) * mm, "end": v(-0.2, 45.48) * mm});
            skLineSegment(sketch, "E5280", {"start": v(-0.2, 45.48) * mm, "end": v(-0.2, 45.5) * mm});
            skLineSegment(sketch, "E5281", {"start": v(-0.2, 45.5) * mm, "end": v(-0.28, 45.47) * mm});
            skLineSegment(sketch, "E5282", {"start": v(-0.28, 45.47) * mm, "end": v(-0.42, 45.56) * mm});
            skLineSegment(sketch, "E5283", {"start": v(-0.42, 45.56) * mm, "end": v(-0.34, 45.66) * mm});
            skLineSegment(sketch, "E5284", {"start": v(-0.34, 45.66) * mm, "end": v(-0.03, 45.7) * mm});
            skLineSegment(sketch, "E5285", {"start": v(-0.03, 45.7) * mm, "end": v(0.06, 45.6) * mm});
            skLineSegment(sketch, "E5286", {"start": v(0.06, 45.6) * mm, "end": v(0.08, 45.5) * mm});
            skLineSegment(sketch, "E5287", {"start": v(0.08, 45.5) * mm, "end": v(0.04, 45.43) * mm});
            skLineSegment(sketch, "E5288", {"start": v(0.04, 45.43) * mm, "end": v(-0.05, 45.35) * mm});
            skLineSegment(sketch, "E5289", {"start": v(-0.05, 45.35) * mm, "end": v(-0.23, 45.2) * mm});
            skLineSegment(sketch, "E5290", {"start": v(-0.23, 45.2) * mm, "end": v(-0.47, 44.99) * mm});
            skLineSegment(sketch, "E5291", {"start": v(-0.47, 44.99) * mm, "end": v(-0.6, 44.85) * mm});
            skLineSegment(sketch, "E5292", {"start": v(-0.6, 44.85) * mm, "end": v(-0.75, 44.66) * mm});
            skLineSegment(sketch, "E5293", {"start": v(-0.75, 44.66) * mm, "end": v(-0.85, 44.47) * mm});
            skLineSegment(sketch, "E5294", {"start": v(-0.85, 44.47) * mm, "end": v(-0.9, 44.3) * mm});
            skLineSegment(sketch, "E5295", {"start": v(-0.9, 44.3) * mm, "end": v(-0.9, 44.12) * mm});
            skLineSegment(sketch, "E5296", {"start": v(-0.9, 44.12) * mm, "end": v(-0.84, 43.92) * mm});
            skLineSegment(sketch, "E5297", {"start": v(-0.84, 43.92) * mm, "end": v(-0.74, 43.73) * mm});
            skLineSegment(sketch, "E5298", {"start": v(-0.74, 43.73) * mm, "end": v(-0.54, 43.53) * mm});
            skLineSegment(sketch, "E5299", {"start": v(-0.54, 43.53) * mm, "end": v(-0.45, 43.47) * mm});
            skLineSegment(sketch, "E5300", {"start": v(-0.45, 43.47) * mm, "end": v(-0.26, 43.38) * mm});
            skLineSegment(sketch, "E5301", {"start": v(-0.26, 43.38) * mm, "end": v(-0.17, 43.34) * mm});
            skLineSegment(sketch, "E5302", {"start": v(-0.17, 43.34) * mm, "end": v(0.16, 43.26) * mm});
            skLineSegment(sketch, "E5303", {"start": v(0.16, 43.26) * mm, "end": v(0.35, 43.24) * mm});
            skLineSegment(sketch, "E5304", {"start": v(0.35, 43.24) * mm, "end": v(0.42, 43.1) * mm});
            skLineSegment(sketch, "E5305", {"start": v(0.42, 43.1) * mm, "end": v(0.4, 42.8) * mm});
            skLineSegment(sketch, "E5306", {"start": v(0.4, 42.8) * mm, "end": v(0.4, 42.8) * mm});
            skLineSegment(sketch, "E5307", {"start": v(0.4, 42.8) * mm, "end": v(0.47, 42.83) * mm});
            skLineSegment(sketch, "E5308", {"start": v(0.47, 42.83) * mm, "end": v(0.52, 42.87) * mm});
            skLineSegment(sketch, "E5309", {"start": v(0.52, 42.87) * mm, "end": v(0.56, 42.73) * mm});
            skLineSegment(sketch, "E5310", {"start": v(0.56, 42.73) * mm, "end": v(0.62, 42.48) * mm});
            skLineSegment(sketch, "E5311", {"start": v(0.62, 42.48) * mm, "end": v(0.7, 42.26) * mm});
            skLineSegment(sketch, "E5312", {"start": v(0.7, 42.26) * mm, "end": v(0.75, 42.14) * mm});
            skLineSegment(sketch, "E5313", {"start": v(0.75, 42.14) * mm, "end": v(0.76, 42.07) * mm});
            skLineSegment(sketch, "E5314", {"start": v(0.76, 42.07) * mm, "end": v(0.72, 42.07) * mm});
            skLineSegment(sketch, "E5315", {"start": v(0.72, 42.07) * mm, "end": v(0.6, 42.1) * mm});
            skLineSegment(sketch, "E5316", {"start": v(0.6, 42.1) * mm, "end": v(0.52, 42.12) * mm});
            skLineSegment(sketch, "E5317", {"start": v(0.52, 42.12) * mm, "end": v(0.43, 42.12) * mm});
            skLineSegment(sketch, "E5318", {"start": v(0.43, 42.12) * mm, "end": v(0.38, 42.07) * mm});
            skLineSegment(sketch, "E5319", {"start": v(0.38, 42.07) * mm, "end": v(0.26, 42.04) * mm});
            skLineSegment(sketch, "E5320", {"start": v(0.26, 42.04) * mm, "end": v(0.25, 42.01) * mm});
            skLineSegment(sketch, "E5321", {"start": v(0.25, 42.01) * mm, "end": v(0.24, 41.97) * mm});
            skLineSegment(sketch, "E5322", {"start": v(0.24, 41.97) * mm, "end": v(0.24, 41.95) * mm});
            skLineSegment(sketch, "E5323", {"start": v(0.24, 41.95) * mm, "end": v(0.26, 41.93) * mm});
            skLineSegment(sketch, "E5324", {"start": v(0.26, 41.93) * mm, "end": v(0.28, 41.9) * mm});
            skLineSegment(sketch, "E5325", {"start": v(0.28, 41.9) * mm, "end": v(0.34, 41.96) * mm});
            skLineSegment(sketch, "E5326", {"start": v(0.34, 41.96) * mm, "end": v(0.4, 41.96) * mm});
            skLineSegment(sketch, "E5327", {"start": v(0.4, 41.96) * mm, "end": v(0.38, 41.93) * mm});
            skLineSegment(sketch, "E5328", {"start": v(0.38, 41.93) * mm, "end": v(0.37, 41.9) * mm});
            skLineSegment(sketch, "E5329", {"start": v(0.37, 41.9) * mm, "end": v(0.38, 41.86) * mm});
            skLineSegment(sketch, "E5330", {"start": v(0.38, 41.86) * mm, "end": v(0.39, 41.84) * mm});
            skLineSegment(sketch, "E5331", {"start": v(0.39, 41.84) * mm, "end": v(0.41, 41.83) * mm});
            skLineSegment(sketch, "E5332", {"start": v(1.42, 42.5) * mm, "end": v(1.44, 42.5) * mm});
            skLineSegment(sketch, "E5333", {"start": v(1.44, 42.5) * mm, "end": v(1.49, 42.6) * mm});
            skLineSegment(sketch, "E5334", {"start": v(1.49, 42.6) * mm, "end": v(1.53, 42.7) * mm});
            skLineSegment(sketch, "E5335", {"start": v(1.53, 42.7) * mm, "end": v(1.56, 42.78) * mm});
            skLineSegment(sketch, "E5336", {"start": v(1.56, 42.78) * mm, "end": v(1.59, 42.87) * mm});
            skLineSegment(sketch, "E5337", {"start": v(1.59, 42.87) * mm, "end": v(1.6, 43.05) * mm});
            skLineSegment(sketch, "E5338", {"start": v(1.6, 43.05) * mm, "end": v(1.56, 43.3) * mm});
            skLineSegment(sketch, "E5339", {"start": v(1.56, 43.3) * mm, "end": v(1.47, 43.5) * mm});
            skLineSegment(sketch, "E5340", {"start": v(1.47, 43.5) * mm, "end": v(1.3, 43.66) * mm});
            skLineSegment(sketch, "E5341", {"start": v(1.3, 43.66) * mm, "end": v(1, 43.81) * mm});
            skLineSegment(sketch, "E5342", {"start": v(1, 43.81) * mm, "end": v(0.69, 43.9) * mm});
            skLineSegment(sketch, "E5343", {"start": v(0.69, 43.9) * mm, "end": v(0.67, 43.88) * mm});
            skLineSegment(sketch, "E5344", {"start": v(0.67, 43.88) * mm, "end": v(0.74, 43.83) * mm});
            skLineSegment(sketch, "E5345", {"start": v(0.74, 43.83) * mm, "end": v(0.92, 43.7) * mm});
            skLineSegment(sketch, "E5346", {"start": v(0.92, 43.7) * mm, "end": v(1.06, 43.56) * mm});
            skLineSegment(sketch, "E5347", {"start": v(1.06, 43.56) * mm, "end": v(1.19, 43.41) * mm});
            skLineSegment(sketch, "E5348", {"start": v(1.19, 43.41) * mm, "end": v(1.28, 43.25) * mm});
            skLineSegment(sketch, "E5349", {"start": v(1.28, 43.25) * mm, "end": v(1.32, 43.17) * mm});
            skLineSegment(sketch, "E5350", {"start": v(1.32, 43.17) * mm, "end": v(1.39, 42.94) * mm});
            skLineSegment(sketch, "E5351", {"start": v(1.39, 42.94) * mm, "end": v(1.42, 42.63) * mm});
            skLineSegment(sketch, "E5352", {"start": v(1.42, 42.63) * mm, "end": v(1.4, 42.5) * mm});
            skLineSegment(sketch, "E5353", {"start": v(1.4, 42.5) * mm, "end": v(1.42, 42.5) * mm});
            skLineSegment(sketch, "E5354", {"start": v(-0.15, 43.9) * mm, "end": v(-0.2, 43.97) * mm});
            skLineSegment(sketch, "E5355", {"start": v(-0.2, 43.97) * mm, "end": v(-0.24, 44.03) * mm});
            skLineSegment(sketch, "E5356", {"start": v(-0.24, 44.03) * mm, "end": v(-0.27, 44.1) * mm});
            skLineSegment(sketch, "E5357", {"start": v(-0.27, 44.1) * mm, "end": v(-0.3, 44.18) * mm});
            skLineSegment(sketch, "E5358", {"start": v(-0.3, 44.18) * mm, "end": v(-0.31, 44.26) * mm});
            skLineSegment(sketch, "E5359", {"start": v(-0.31, 44.26) * mm, "end": v(-0.31, 44.51) * mm});
            skLineSegment(sketch, "E5360", {"start": v(-0.31, 44.51) * mm, "end": v(-0.3, 44.6) * mm});
            skLineSegment(sketch, "E5361", {"start": v(-0.3, 44.6) * mm, "end": v(-0.24, 44.78) * mm});
            skLineSegment(sketch, "E5362", {"start": v(-0.24, 44.78) * mm, "end": v(-0.2, 44.85) * mm});
            skLineSegment(sketch, "E5363", {"start": v(-0.2, 44.85) * mm, "end": v(-0.22, 44.87) * mm});
            skLineSegment(sketch, "E5364", {"start": v(-0.22, 44.87) * mm, "end": v(-0.35, 44.72) * mm});
            skLineSegment(sketch, "E5365", {"start": v(-0.35, 44.72) * mm, "end": v(-0.43, 44.56) * mm});
            skLineSegment(sketch, "E5366", {"start": v(-0.43, 44.56) * mm, "end": v(-0.46, 44.38) * mm});
            skLineSegment(sketch, "E5367", {"start": v(-0.46, 44.38) * mm, "end": v(-0.45, 44.32) * mm});
            skLineSegment(sketch, "E5368", {"start": v(-0.45, 44.32) * mm, "end": v(-0.43, 44.17) * mm});
            skLineSegment(sketch, "E5369", {"start": v(-0.43, 44.17) * mm, "end": v(-0.4, 44.09) * mm});
            skLineSegment(sketch, "E5370", {"start": v(-0.4, 44.09) * mm, "end": v(-0.32, 43.93) * mm});
            skLineSegment(sketch, "E5371", {"start": v(-0.32, 43.93) * mm, "end": v(-0.19, 43.8) * mm});
            skLineSegment(sketch, "E5372", {"start": v(-0.19, 43.8) * mm, "end": v(-0.12, 43.75) * mm});
            skLineSegment(sketch, "E5373", {"start": v(-0.12, 43.75) * mm, "end": v(0, 43.7) * mm});
            skLineSegment(sketch, "E5374", {"start": v(0, 43.7) * mm, "end": v(0.08, 43.66) * mm});
            skLineSegment(sketch, "E5375", {"start": v(0.08, 43.66) * mm, "end": v(0, 43.74) * mm});
            skLineSegment(sketch, "E5376", {"start": v(0, 43.74) * mm, "end": v(-0.08, 43.82) * mm});
            skLineSegment(sketch, "E5377", {"start": v(-0.08, 43.82) * mm, "end": v(-0.15, 43.9) * mm});
            skLineSegment(sketch, "E5378", {"start": v(1.18, 44.13) * mm, "end": v(1.3, 44.13) * mm});
            skLineSegment(sketch, "E5379", {"start": v(1.3, 44.13) * mm, "end": v(1.34, 44.17) * mm});
            skLineSegment(sketch, "E5380", {"start": v(1.34, 44.17) * mm, "end": v(1.4, 44.25) * mm});
            skLineSegment(sketch, "E5381", {"start": v(1.4, 44.25) * mm, "end": v(1.4, 44.3) * mm});
            skLineSegment(sketch, "E5382", {"start": v(1.4, 44.3) * mm, "end": v(1.4, 44.31) * mm});
            skLineSegment(sketch, "E5383", {"start": v(1.4, 44.31) * mm, "end": v(1.35, 44.29) * mm});
            skLineSegment(sketch, "E5384", {"start": v(1.35, 44.29) * mm, "end": v(1.2, 44.23) * mm});
            skLineSegment(sketch, "E5385", {"start": v(1.2, 44.23) * mm, "end": v(1.04, 44.18) * mm});
            skLineSegment(sketch, "E5386", {"start": v(1.04, 44.18) * mm, "end": v(1, 44.17) * mm});
            skLineSegment(sketch, "E5387", {"start": v(1, 44.17) * mm, "end": v(1.05, 44.13) * mm});
            skLineSegment(sketch, "E5388", {"start": v(1.05, 44.13) * mm, "end": v(1.18, 44.13) * mm});
            skLineSegment(sketch, "E5389", {"start": v(0.92, 44.2) * mm, "end": v(1.07, 44.25) * mm});
            skLineSegment(sketch, "E5390", {"start": v(1.07, 44.25) * mm, "end": v(1.26, 44.32) * mm});
            skLineSegment(sketch, "E5391", {"start": v(1.26, 44.32) * mm, "end": v(1.4, 44.4) * mm});
            skLineSegment(sketch, "E5392", {"start": v(1.4, 44.4) * mm, "end": v(1.5, 44.46) * mm});
            skLineSegment(sketch, "E5393", {"start": v(1.5, 44.46) * mm, "end": v(1.55, 44.52) * mm});
            skLineSegment(sketch, "E5394", {"start": v(1.55, 44.52) * mm, "end": v(1.63, 44.62) * mm});
            skLineSegment(sketch, "E5395", {"start": v(1.63, 44.62) * mm, "end": v(1.65, 44.66) * mm});
            skLineSegment(sketch, "E5396", {"start": v(1.65, 44.66) * mm, "end": v(1.63, 44.66) * mm});
            skLineSegment(sketch, "E5397", {"start": v(1.63, 44.66) * mm, "end": v(1.6, 44.65) * mm});
            skLineSegment(sketch, "E5398", {"start": v(1.6, 44.65) * mm, "end": v(1.56, 44.62) * mm});
            skLineSegment(sketch, "E5399", {"start": v(1.56, 44.62) * mm, "end": v(1.4, 44.54) * mm});
            skLineSegment(sketch, "E5400", {"start": v(1.4, 44.54) * mm, "end": v(1.29, 44.48) * mm});
            skLineSegment(sketch, "E5401", {"start": v(1.29, 44.48) * mm, "end": v(1, 44.42) * mm});
            skLineSegment(sketch, "E5402", {"start": v(1, 44.42) * mm, "end": v(0.95, 44.28) * mm});
            skLineSegment(sketch, "E5403", {"start": v(0.95, 44.28) * mm, "end": v(0.88, 44.22) * mm});
            skLineSegment(sketch, "E5404", {"start": v(0.88, 44.22) * mm, "end": v(0.9, 44.21) * mm});
            skLineSegment(sketch, "E5405", {"start": v(0.9, 44.21) * mm, "end": v(0.92, 44.2) * mm});
            skLineSegment(sketch, "E5406", {"start": v(1.13, 44.5) * mm, "end": v(1.33, 44.58) * mm});
            skLineSegment(sketch, "E5407", {"start": v(1.33, 44.58) * mm, "end": v(1.48, 44.66) * mm});
            skLineSegment(sketch, "E5408", {"start": v(1.48, 44.66) * mm, "end": v(1.57, 44.72) * mm});
            skLineSegment(sketch, "E5409", {"start": v(1.57, 44.72) * mm, "end": v(1.74, 44.88) * mm});
            skLineSegment(sketch, "E5410", {"start": v(1.74, 44.88) * mm, "end": v(1.76, 44.94) * mm});
            skLineSegment(sketch, "E5411", {"start": v(1.76, 44.94) * mm, "end": v(1.8, 45.04) * mm});
            skLineSegment(sketch, "E5412", {"start": v(1.8, 45.04) * mm, "end": v(1.8, 45.07) * mm});
            skLineSegment(sketch, "E5413", {"start": v(1.8, 45.07) * mm, "end": v(1.79, 45.06) * mm});
            skLineSegment(sketch, "E5414", {"start": v(1.79, 45.06) * mm, "end": v(1.65, 44.97) * mm});
            skLineSegment(sketch, "E5415", {"start": v(1.65, 44.97) * mm, "end": v(1.55, 44.9) * mm});
            skLineSegment(sketch, "E5416", {"start": v(1.55, 44.9) * mm, "end": v(1.45, 44.84) * mm});
            skLineSegment(sketch, "E5417", {"start": v(1.45, 44.84) * mm, "end": v(1.35, 44.79) * mm});
            skLineSegment(sketch, "E5418", {"start": v(1.35, 44.79) * mm, "end": v(1.23, 44.74) * mm});
            skLineSegment(sketch, "E5419", {"start": v(1.23, 44.74) * mm, "end": v(1.1, 44.69) * mm});
            skLineSegment(sketch, "E5420", {"start": v(1.1, 44.69) * mm, "end": v(1.09, 44.63) * mm});
            skLineSegment(sketch, "E5421", {"start": v(1.09, 44.63) * mm, "end": v(1.06, 44.54) * mm});
            skLineSegment(sketch, "E5422", {"start": v(1.06, 44.54) * mm, "end": v(1.04, 44.5) * mm});
            skLineSegment(sketch, "E5423", {"start": v(1.04, 44.5) * mm, "end": v(1.05, 44.47) * mm});
            skLineSegment(sketch, "E5424", {"start": v(1.05, 44.47) * mm, "end": v(1.13, 44.5) * mm});
            skLineSegment(sketch, "E5425", {"start": v(1.17, 44.76) * mm, "end": v(1.31, 44.83) * mm});
            skLineSegment(sketch, "E5426", {"start": v(1.31, 44.83) * mm, "end": v(1.47, 44.92) * mm});
            skLineSegment(sketch, "E5427", {"start": v(1.47, 44.92) * mm, "end": v(1.62, 45.01) * mm});
            skLineSegment(sketch, "E5428", {"start": v(1.62, 45.01) * mm, "end": v(1.73, 45.1) * mm});
            skLineSegment(sketch, "E5429", {"start": v(1.73, 45.1) * mm, "end": v(1.8, 45.16) * mm});
            skLineSegment(sketch, "E5430", {"start": v(1.8, 45.16) * mm, "end": v(1.91, 45.32) * mm});
            skLineSegment(sketch, "E5431", {"start": v(1.91, 45.32) * mm, "end": v(1.96, 45.46) * mm});
            skLineSegment(sketch, "E5432", {"start": v(1.96, 45.46) * mm, "end": v(1.94, 45.5) * mm});
            skLineSegment(sketch, "E5433", {"start": v(1.94, 45.5) * mm, "end": v(1.86, 45.43) * mm});
            skLineSegment(sketch, "E5434", {"start": v(1.86, 45.43) * mm, "end": v(1.71, 45.3) * mm});
            skLineSegment(sketch, "E5435", {"start": v(1.71, 45.3) * mm, "end": v(1.55, 45.17) * mm});
            skLineSegment(sketch, "E5436", {"start": v(1.55, 45.17) * mm, "end": v(1.39, 45.06) * mm});
            skLineSegment(sketch, "E5437", {"start": v(1.39, 45.06) * mm, "end": v(1.23, 44.97) * mm});
            skLineSegment(sketch, "E5438", {"start": v(1.23, 44.97) * mm, "end": v(1.12, 44.92) * mm});
            skLineSegment(sketch, "E5439", {"start": v(1.12, 44.92) * mm, "end": v(1.13, 44.85) * mm});
            skLineSegment(sketch, "E5440", {"start": v(1.13, 44.85) * mm, "end": v(1.12, 44.8) * mm});
            skLineSegment(sketch, "E5441", {"start": v(1.12, 44.8) * mm, "end": v(1.12, 44.76) * mm});
            skLineSegment(sketch, "E5442", {"start": v(1.12, 44.76) * mm, "end": v(1.12, 44.74) * mm});
            skLineSegment(sketch, "E5443", {"start": v(1.12, 44.74) * mm, "end": v(1.17, 44.76) * mm});
            skLineSegment(sketch, "E5444", {"start": v(1.15, 45) * mm, "end": v(1.16, 45) * mm});
            skLineSegment(sketch, "E5445", {"start": v(1.16, 45) * mm, "end": v(1.5, 45.2) * mm});
            skLineSegment(sketch, "E5446", {"start": v(1.5, 45.2) * mm, "end": v(1.63, 45.29) * mm});
            skLineSegment(sketch, "E5447", {"start": v(1.63, 45.29) * mm, "end": v(1.74, 45.38) * mm});
            skLineSegment(sketch, "E5448", {"start": v(1.74, 45.38) * mm, "end": v(1.85, 45.48) * mm});
            skLineSegment(sketch, "E5449", {"start": v(1.85, 45.48) * mm, "end": v(1.97, 45.59) * mm});
            skLineSegment(sketch, "E5450", {"start": v(1.97, 45.59) * mm, "end": v(2.04, 45.7) * mm});
            skLineSegment(sketch, "E5451", {"start": v(2.04, 45.7) * mm, "end": v(2.13, 45.86) * mm});
            skLineSegment(sketch, "E5452", {"start": v(2.13, 45.86) * mm, "end": v(2.16, 45.93) * mm});
            skLineSegment(sketch, "E5453", {"start": v(2.16, 45.93) * mm, "end": v(2.18, 46) * mm});
            skLineSegment(sketch, "E5454", {"start": v(2.18, 46) * mm, "end": v(2.19, 46.06) * mm});
            skLineSegment(sketch, "E5455", {"start": v(2.19, 46.06) * mm, "end": v(2.07, 45.94) * mm});
            skLineSegment(sketch, "E5456", {"start": v(2.07, 45.94) * mm, "end": v(1.87, 45.73) * mm});
            skLineSegment(sketch, "E5457", {"start": v(1.87, 45.73) * mm, "end": v(1.66, 45.54) * mm});
            skLineSegment(sketch, "E5458", {"start": v(1.66, 45.54) * mm, "end": v(1.53, 45.43) * mm});
            skLineSegment(sketch, "E5459", {"start": v(1.53, 45.43) * mm, "end": v(1.13, 45.17) * mm});
            skLineSegment(sketch, "E5460", {"start": v(1.13, 45.17) * mm, "end": v(1.13, 45.1) * mm});
            skLineSegment(sketch, "E5461", {"start": v(1.13, 45.1) * mm, "end": v(1.13, 45.02) * mm});
            skLineSegment(sketch, "E5462", {"start": v(1.13, 45.02) * mm, "end": v(1.14, 45) * mm});
            skLineSegment(sketch, "E5463", {"start": v(1.14, 45) * mm, "end": v(1.15, 45) * mm});
            skLineSegment(sketch, "E5464", {"start": v(0.63, 45.11) * mm, "end": v(0.78, 45.21) * mm});
            skLineSegment(sketch, "E5465", {"start": v(0.78, 45.21) * mm, "end": v(1.05, 45.42) * mm});
            skLineSegment(sketch, "E5466", {"start": v(1.05, 45.42) * mm, "end": v(1.24, 45.57) * mm});
            skLineSegment(sketch, "E5467", {"start": v(1.24, 45.57) * mm, "end": v(1.5, 45.82) * mm});
            skLineSegment(sketch, "E5468", {"start": v(1.5, 45.82) * mm, "end": v(1.62, 46) * mm});
            skLineSegment(sketch, "E5469", {"start": v(1.62, 46) * mm, "end": v(1.71, 46.19) * mm});
            skLineSegment(sketch, "E5470", {"start": v(1.71, 46.19) * mm, "end": v(1.72, 46.34) * mm});
            skLineSegment(sketch, "E5471", {"start": v(1.72, 46.34) * mm, "end": v(1.7, 46.38) * mm});
            skLineSegment(sketch, "E5472", {"start": v(1.7, 46.38) * mm, "end": v(1.67, 46.44) * mm});
            skLineSegment(sketch, "E5473", {"start": v(1.67, 46.44) * mm, "end": v(1.65, 46.46) * mm});
            skLineSegment(sketch, "E5474", {"start": v(1.65, 46.46) * mm, "end": v(1.63, 46.47) * mm});
            skLineSegment(sketch, "E5475", {"start": v(1.63, 46.47) * mm, "end": v(1.62, 46.47) * mm});
            skLineSegment(sketch, "E5476", {"start": v(1.62, 46.47) * mm, "end": v(1.6, 46.29) * mm});
            skLineSegment(sketch, "E5477", {"start": v(1.6, 46.29) * mm, "end": v(1.58, 46.2) * mm});
            skLineSegment(sketch, "E5478", {"start": v(1.58, 46.2) * mm, "end": v(1.55, 46.13) * mm});
            skLineSegment(sketch, "E5479", {"start": v(1.55, 46.13) * mm, "end": v(1.52, 46.06) * mm});
            skLineSegment(sketch, "E5480", {"start": v(1.52, 46.06) * mm, "end": v(1.48, 45.99) * mm});
            skLineSegment(sketch, "E5481", {"start": v(1.48, 45.99) * mm, "end": v(1.42, 45.92) * mm});
            skLineSegment(sketch, "E5482", {"start": v(1.42, 45.92) * mm, "end": v(1.26, 45.75) * mm});
            skLineSegment(sketch, "E5483", {"start": v(1.26, 45.75) * mm, "end": v(1, 45.51) * mm});
            skLineSegment(sketch, "E5484", {"start": v(1, 45.51) * mm, "end": v(0.83, 45.36) * mm});
            skLineSegment(sketch, "E5485", {"start": v(0.83, 45.36) * mm, "end": v(0.64, 45.16) * mm});
            skLineSegment(sketch, "E5486", {"start": v(0.64, 45.16) * mm, "end": v(0.63, 45.11) * mm});
            skLineSegment(sketch, "E5487", {"start": v(0.63, 45.11) * mm, "end": v(0.63, 45.11) * mm});
            skLineSegment(sketch, "E5488", {"start": v(1.7, 45.65) * mm, "end": v(1.9, 45.8) * mm});
            skLineSegment(sketch, "E5489", {"start": v(1.9, 45.8) * mm, "end": v(2.02, 45.92) * mm});
            skLineSegment(sketch, "E5490", {"start": v(2.02, 45.92) * mm, "end": v(2.1, 46.01) * mm});
            skLineSegment(sketch, "E5491", {"start": v(2.1, 46.01) * mm, "end": v(2.15, 46.09) * mm});
            skLineSegment(sketch, "E5492", {"start": v(2.15, 46.09) * mm, "end": v(2.2, 46.16) * mm});
            skLineSegment(sketch, "E5493", {"start": v(2.2, 46.16) * mm, "end": v(2.23, 46.23) * mm});
            skLineSegment(sketch, "E5494", {"start": v(2.23, 46.23) * mm, "end": v(2.25, 46.3) * mm});
            skLineSegment(sketch, "E5495", {"start": v(2.25, 46.3) * mm, "end": v(2.27, 46.36) * mm});
            skLineSegment(sketch, "E5496", {"start": v(2.27, 46.36) * mm, "end": v(2.25, 46.48) * mm});
            skLineSegment(sketch, "E5497", {"start": v(2.25, 46.48) * mm, "end": v(2.24, 46.5) * mm});
            skLineSegment(sketch, "E5498", {"start": v(2.24, 46.5) * mm, "end": v(2.24, 46.52) * mm});
            skLineSegment(sketch, "E5499", {"start": v(2.24, 46.52) * mm, "end": v(2.21, 46.52) * mm});
            skLineSegment(sketch, "E5500", {"start": v(2.21, 46.52) * mm, "end": v(2.15, 46.34) * mm});
            skLineSegment(sketch, "E5501", {"start": v(2.15, 46.34) * mm, "end": v(2.03, 46.12) * mm});
            skLineSegment(sketch, "E5502", {"start": v(2.03, 46.12) * mm, "end": v(1.93, 45.99) * mm});
            skLineSegment(sketch, "E5503", {"start": v(1.93, 45.99) * mm, "end": v(1.74, 45.75) * mm});
            skLineSegment(sketch, "E5504", {"start": v(1.74, 45.75) * mm, "end": v(1.63, 45.63) * mm});
            skLineSegment(sketch, "E5505", {"start": v(1.63, 45.63) * mm, "end": v(1.65, 45.61) * mm});
            skLineSegment(sketch, "E5506", {"start": v(1.65, 45.61) * mm, "end": v(1.7, 45.65) * mm});
            skLineSegment(sketch, "E5507", {"start": v(-0.19, 45.82) * mm, "end": v(-0.19, 45.85) * mm});
            skLineSegment(sketch, "E5508", {"start": v(-0.19, 45.85) * mm, "end": v(-0.28, 45.85) * mm});
            skLineSegment(sketch, "E5509", {"start": v(-0.28, 45.85) * mm, "end": v(-0.3, 45.82) * mm});
            skLineSegment(sketch, "E5510", {"start": v(-0.3, 45.82) * mm, "end": v(-0.3, 45.77) * mm});
            skLineSegment(sketch, "E5511", {"start": v(-0.3, 45.77) * mm, "end": v(-0.3, 45.75) * mm});
            skLineSegment(sketch, "E5512", {"start": v(-0.3, 45.75) * mm, "end": v(-0.3, 45.74) * mm});
            skLineSegment(sketch, "E5513", {"start": v(-0.3, 45.74) * mm, "end": v(-0.23, 45.77) * mm});
            skLineSegment(sketch, "E5514", {"start": v(-0.23, 45.77) * mm, "end": v(-0.19, 45.8) * mm});
            skLineSegment(sketch, "E5515", {"start": v(-0.19, 45.8) * mm, "end": v(-0.19, 45.82) * mm});
            skLineSegment(sketch, "E5516", {"start": v(0.08, 45.9) * mm, "end": v(0.03, 45.93) * mm});
            skLineSegment(sketch, "E5517", {"start": v(0.03, 45.93) * mm, "end": v(-0.04, 45.95) * mm});
            skLineSegment(sketch, "E5518", {"start": v(-0.04, 45.95) * mm, "end": v(-0.06, 45.95) * mm});
            skLineSegment(sketch, "E5519", {"start": v(-0.06, 45.95) * mm, "end": v(-0.05, 45.89) * mm});
            skLineSegment(sketch, "E5520", {"start": v(-0.05, 45.89) * mm, "end": v(0, 45.88) * mm});
            skLineSegment(sketch, "E5521", {"start": v(0, 45.88) * mm, "end": v(0.05, 45.89) * mm});
            skLineSegment(sketch, "E5522", {"start": v(0.05, 45.89) * mm, "end": v(0.07, 45.9) * mm});
            skLineSegment(sketch, "E5523", {"start": v(0.07, 45.9) * mm, "end": v(0.08, 45.9) * mm});
            skLineSegment(sketch, "E5524", {"start": v(5.6, -31.36) * mm, "end": v(5.63, -31.34) * mm});
            skLineSegment(sketch, "E5525", {"start": v(5.63, -31.34) * mm, "end": v(5.64, -31.31) * mm});
            skLineSegment(sketch, "E5526", {"start": v(5.64, -31.31) * mm, "end": v(5.63, -31.28) * mm});
            skLineSegment(sketch, "E5527", {"start": v(5.63, -31.28) * mm, "end": v(5.6, -31.27) * mm});
            skLineSegment(sketch, "E5528", {"start": v(5.6, -31.27) * mm, "end": v(5.56, -31.28) * mm});
            skLineSegment(sketch, "E5529", {"start": v(5.56, -31.28) * mm, "end": v(5.55, -31.31) * mm});
            skLineSegment(sketch, "E5530", {"start": v(5.55, -31.31) * mm, "end": v(5.56, -31.34) * mm});
            skLineSegment(sketch, "E5531", {"start": v(5.56, -31.34) * mm, "end": v(5.6, -31.36) * mm});
            skLineSegment(sketch, "E5532", {"start": v(1.3, -38.7) * mm, "end": v(1.34, -38.68) * mm});
            skLineSegment(sketch, "E5533", {"start": v(1.34, -38.68) * mm, "end": v(1.39, -38.63) * mm});
            skLineSegment(sketch, "E5534", {"start": v(1.39, -38.63) * mm, "end": v(1.45, -38.55) * mm});
            skLineSegment(sketch, "E5535", {"start": v(1.45, -38.55) * mm, "end": v(1.51, -38.46) * mm});
            skLineSegment(sketch, "E5536", {"start": v(1.51, -38.46) * mm, "end": v(1.67, -38.23) * mm});
            skLineSegment(sketch, "E5537", {"start": v(1.67, -38.23) * mm, "end": v(2.28, -37.97) * mm});
            skLineSegment(sketch, "E5538", {"start": v(2.28, -37.97) * mm, "end": v(6.18, -37.97) * mm});
            skLineSegment(sketch, "E5539", {"start": v(6.18, -37.97) * mm, "end": v(6.64, -38.18) * mm});
            skLineSegment(sketch, "E5540", {"start": v(6.64, -38.18) * mm, "end": v(6.93, -38.62) * mm});
            skLineSegment(sketch, "E5541", {"start": v(6.93, -38.62) * mm, "end": v(7.35, -38.23) * mm});
            skLineSegment(sketch, "E5542", {"start": v(7.35, -38.23) * mm, "end": v(7.46, -37.78) * mm});
            skLineSegment(sketch, "E5543", {"start": v(7.46, -37.78) * mm, "end": v(7.35, -37.43) * mm});
            skLineSegment(sketch, "E5544", {"start": v(7.35, -37.43) * mm, "end": v(6.8, -37.14) * mm});
            skLineSegment(sketch, "E5545", {"start": v(6.8, -37.14) * mm, "end": v(5.14, -37.15) * mm});
            skLineSegment(sketch, "E5546", {"start": v(5.14, -37.15) * mm, "end": v(4.9, -36.73) * mm});
            skLineSegment(sketch, "E5547", {"start": v(4.9, -36.73) * mm, "end": v(4.8, -36.53) * mm});
            skLineSegment(sketch, "E5548", {"start": v(4.8, -36.53) * mm, "end": v(4.7, -36.33) * mm});
            skLineSegment(sketch, "E5549", {"start": v(4.7, -36.33) * mm, "end": v(4.61, -36.12) * mm});
            skLineSegment(sketch, "E5550", {"start": v(4.61, -36.12) * mm, "end": v(4.52, -35.9) * mm});
            skLineSegment(sketch, "E5551", {"start": v(4.52, -35.9) * mm, "end": v(4.36, -35.44) * mm});
            skLineSegment(sketch, "E5552", {"start": v(4.36, -35.44) * mm, "end": v(4.22, -34.95) * mm});
            skLineSegment(sketch, "E5553", {"start": v(4.22, -34.95) * mm, "end": v(4.1, -34.43) * mm});
            skLineSegment(sketch, "E5554", {"start": v(4.1, -34.43) * mm, "end": v(4, -33.88) * mm});
            skLineSegment(sketch, "E5555", {"start": v(4, -33.88) * mm, "end": v(3.93, -33.3) * mm});
            skLineSegment(sketch, "E5556", {"start": v(3.93, -33.3) * mm, "end": v(3.87, -32.7) * mm});
            skLineSegment(sketch, "E5557", {"start": v(3.87, -32.7) * mm, "end": v(3.8, -31.82) * mm});
            skLineSegment(sketch, "E5558", {"start": v(3.8, -31.82) * mm, "end": v(4.5, -32.17) * mm});
            skLineSegment(sketch, "E5559", {"start": v(4.5, -32.17) * mm, "end": v(5.09, -32.17) * mm});
            skLineSegment(sketch, "E5560", {"start": v(5.09, -32.17) * mm, "end": v(5.2, -31.99) * mm});
            skLineSegment(sketch, "E5561", {"start": v(5.2, -31.99) * mm, "end": v(4.38, -31.17) * mm});
            skLineSegment(sketch, "E5562", {"start": v(4.38, -31.17) * mm, "end": v(3.8, -29.97) * mm});
            skLineSegment(sketch, "E5563", {"start": v(3.8, -29.97) * mm, "end": v(3.72, -27.75) * mm});
            skLineSegment(sketch, "E5564", {"start": v(3.72, -27.75) * mm, "end": v(2.08, -26.42) * mm});
            skLineSegment(sketch, "E5565", {"start": v(2.08, -26.42) * mm, "end": v(1.1, -25.24) * mm});
            skLineSegment(sketch, "E5566", {"start": v(1.1, -25.24) * mm, "end": v(0.54, -24.11) * mm});
            skLineSegment(sketch, "E5567", {"start": v(0.54, -24.11) * mm, "end": v(0.45, -23.25) * mm});
            skLineSegment(sketch, "E5568", {"start": v(0.45, -23.25) * mm, "end": v(1.74, -25.18) * mm});
            skLineSegment(sketch, "E5569", {"start": v(1.74, -25.18) * mm, "end": v(4.98, -28.52) * mm});
            skLineSegment(sketch, "E5570", {"start": v(4.98, -28.52) * mm, "end": v(5.37, -29.56) * mm});
            skLineSegment(sketch, "E5571", {"start": v(5.37, -29.56) * mm, "end": v(5.53, -31.1) * mm});
            skLineSegment(sketch, "E5572", {"start": v(5.53, -31.1) * mm, "end": v(5.76, -31.31) * mm});
            skLineSegment(sketch, "E5573", {"start": v(5.76, -31.31) * mm, "end": v(5.65, -31) * mm});
            skLineSegment(sketch, "E5574", {"start": v(5.65, -31) * mm, "end": v(5.8, -31) * mm});
            skLineSegment(sketch, "E5575", {"start": v(5.8, -31) * mm, "end": v(6.03, -29.8) * mm});
            skLineSegment(sketch, "E5576", {"start": v(6.03, -29.8) * mm, "end": v(5.94, -28.55) * mm});
            skLineSegment(sketch, "E5577", {"start": v(5.94, -28.55) * mm, "end": v(5.34, -27.33) * mm});
            skLineSegment(sketch, "E5578", {"start": v(5.34, -27.33) * mm, "end": v(4.47, -26.47) * mm});
            skLineSegment(sketch, "E5579", {"start": v(4.47, -26.47) * mm, "end": v(3.6, -25.6) * mm});
            skLineSegment(sketch, "E5580", {"start": v(3.6, -25.6) * mm, "end": v(2.72, -24.75) * mm});
            skLineSegment(sketch, "E5581", {"start": v(2.72, -24.75) * mm, "end": v(1.84, -23.9) * mm});
            skLineSegment(sketch, "E5582", {"start": v(1.84, -23.9) * mm, "end": v(1.3, -23.06) * mm});
            skLineSegment(sketch, "E5583", {"start": v(1.3, -23.06) * mm, "end": v(1.86, -23.47) * mm});
            skLineSegment(sketch, "E5584", {"start": v(1.86, -23.47) * mm, "end": v(2.12, -23.66) * mm});
            skLineSegment(sketch, "E5585", {"start": v(2.12, -23.66) * mm, "end": v(2.4, -23.84) * mm});
            skLineSegment(sketch, "E5586", {"start": v(2.4, -23.84) * mm, "end": v(2.68, -24.01) * mm});
            skLineSegment(sketch, "E5587", {"start": v(2.68, -24.01) * mm, "end": v(2.95, -24.17) * mm});
            skLineSegment(sketch, "E5588", {"start": v(2.95, -24.17) * mm, "end": v(3.22, -24.3) * mm});
            skLineSegment(sketch, "E5589", {"start": v(3.22, -24.3) * mm, "end": v(3.49, -24.43) * mm});
            skLineSegment(sketch, "E5590", {"start": v(3.49, -24.43) * mm, "end": v(3.73, -24.53) * mm});
            skLineSegment(sketch, "E5591", {"start": v(3.73, -24.53) * mm, "end": v(3.96, -24.6) * mm});
            skLineSegment(sketch, "E5592", {"start": v(3.96, -24.6) * mm, "end": v(4.4, -24.74) * mm});
            skLineSegment(sketch, "E5593", {"start": v(4.4, -24.74) * mm, "end": v(5.6, -24.74) * mm});
            skLineSegment(sketch, "E5594", {"start": v(5.6, -24.74) * mm, "end": v(6.68, -24.19) * mm});
            skLineSegment(sketch, "E5595", {"start": v(6.68, -24.19) * mm, "end": v(6.98, -23.9) * mm});
            skLineSegment(sketch, "E5596", {"start": v(6.98, -23.9) * mm, "end": v(7.19, -23.68) * mm});
            skLineSegment(sketch, "E5597", {"start": v(7.19, -23.68) * mm, "end": v(7.25, -23.6) * mm});
            skLineSegment(sketch, "E5598", {"start": v(7.25, -23.6) * mm, "end": v(7.27, -23.56) * mm});
            skLineSegment(sketch, "E5599", {"start": v(7.27, -23.56) * mm, "end": v(7.27, -23.5) * mm});
            skLineSegment(sketch, "E5600", {"start": v(7.27, -23.5) * mm, "end": v(5.43, -23.46) * mm});
            skLineSegment(sketch, "E5601", {"start": v(5.43, -23.46) * mm, "end": v(4.19, -23.2) * mm});
            skLineSegment(sketch, "E5602", {"start": v(4.19, -23.2) * mm, "end": v(3.8, -23) * mm});
            skLineSegment(sketch, "E5603", {"start": v(3.8, -23) * mm, "end": v(3.47, -22.82) * mm});
            skLineSegment(sketch, "E5604", {"start": v(3.47, -22.82) * mm, "end": v(3.33, -22.73) * mm});
            skLineSegment(sketch, "E5605", {"start": v(3.33, -22.73) * mm, "end": v(3.22, -22.66) * mm});
            skLineSegment(sketch, "E5606", {"start": v(3.22, -22.66) * mm, "end": v(3.02, -22.5) * mm});
            skLineSegment(sketch, "E5607", {"start": v(3.02, -22.5) * mm, "end": v(3.87, -22.38) * mm});
            skLineSegment(sketch, "E5608", {"start": v(3.87, -22.38) * mm, "end": v(4.46, -22.02) * mm});
            skLineSegment(sketch, "E5609", {"start": v(4.46, -22.02) * mm, "end": v(4.82, -21.45) * mm});
            skLineSegment(sketch, "E5610", {"start": v(4.82, -21.45) * mm, "end": v(4.73, -21.3) * mm});
            skLineSegment(sketch, "E5611", {"start": v(4.73, -21.3) * mm, "end": v(3.47, -21.3) * mm});
            skLineSegment(sketch, "E5612", {"start": v(3.47, -21.3) * mm, "end": v(3.17, -21.14) * mm});
            skLineSegment(sketch, "E5613", {"start": v(3.17, -21.14) * mm, "end": v(3.61, -21.07) * mm});
            skLineSegment(sketch, "E5614", {"start": v(3.61, -21.07) * mm, "end": v(3.81, -21.04) * mm});
            skLineSegment(sketch, "E5615", {"start": v(3.81, -21.04) * mm, "end": v(4.03, -20.98) * mm});
            skLineSegment(sketch, "E5616", {"start": v(4.03, -20.98) * mm, "end": v(4.25, -20.92) * mm});
            skLineSegment(sketch, "E5617", {"start": v(4.25, -20.92) * mm, "end": v(4.42, -20.85) * mm});
            skLineSegment(sketch, "E5618", {"start": v(4.42, -20.85) * mm, "end": v(4.8, -20.69) * mm});
            skLineSegment(sketch, "E5619", {"start": v(4.8, -20.69) * mm, "end": v(5.46, -20) * mm});
            skLineSegment(sketch, "E5620", {"start": v(5.46, -20) * mm, "end": v(5.36, -19.85) * mm});
            skLineSegment(sketch, "E5621", {"start": v(5.36, -19.85) * mm, "end": v(3.56, -19.96) * mm});
            skLineSegment(sketch, "E5622", {"start": v(3.56, -19.96) * mm, "end": v(3.56, -19.77) * mm});
            skLineSegment(sketch, "E5623", {"start": v(3.56, -19.77) * mm, "end": v(3.85, -19.7) * mm});
            skLineSegment(sketch, "E5624", {"start": v(3.85, -19.7) * mm, "end": v(4, -19.67) * mm});
            skLineSegment(sketch, "E5625", {"start": v(4, -19.67) * mm, "end": v(4.18, -19.6) * mm});
            skLineSegment(sketch, "E5626", {"start": v(4.18, -19.6) * mm, "end": v(4.38, -19.52) * mm});
            skLineSegment(sketch, "E5627", {"start": v(4.38, -19.52) * mm, "end": v(4.56, -19.43) * mm});
            skLineSegment(sketch, "E5628", {"start": v(4.56, -19.43) * mm, "end": v(4.98, -19.22) * mm});
            skLineSegment(sketch, "E5629", {"start": v(4.98, -19.22) * mm, "end": v(5.26, -18.9) * mm});
            skLineSegment(sketch, "E5630", {"start": v(5.26, -18.9) * mm, "end": v(5.43, -18.7) * mm});
            skLineSegment(sketch, "E5631", {"start": v(5.43, -18.7) * mm, "end": v(5.48, -18.63) * mm});
            skLineSegment(sketch, "E5632", {"start": v(5.48, -18.63) * mm, "end": v(5.52, -18.56) * mm});
            skLineSegment(sketch, "E5633", {"start": v(5.52, -18.56) * mm, "end": v(5.54, -18.5) * mm});
            skLineSegment(sketch, "E5634", {"start": v(5.54, -18.5) * mm, "end": v(5.55, -18.45) * mm});
            skLineSegment(sketch, "E5635", {"start": v(5.55, -18.45) * mm, "end": v(5.54, -18.4) * mm});
            skLineSegment(sketch, "E5636", {"start": v(5.54, -18.4) * mm, "end": v(5.53, -18.35) * mm});
            skLineSegment(sketch, "E5637", {"start": v(5.53, -18.35) * mm, "end": v(5.53, -18.32) * mm});
            skLineSegment(sketch, "E5638", {"start": v(5.53, -18.32) * mm, "end": v(5.55, -18.29) * mm});
            skLineSegment(sketch, "E5639", {"start": v(5.55, -18.29) * mm, "end": v(5.59, -18.25) * mm});
            skLineSegment(sketch, "E5640", {"start": v(5.59, -18.25) * mm, "end": v(5.64, -18.22) * mm});
            skLineSegment(sketch, "E5641", {"start": v(5.64, -18.22) * mm, "end": v(5.77, -18.13) * mm});
            skLineSegment(sketch, "E5642", {"start": v(5.77, -18.13) * mm, "end": v(5.66, -18.02) * mm});
            skLineSegment(sketch, "E5643", {"start": v(5.66, -18.02) * mm, "end": v(5.3, -18.2) * mm});
            skLineSegment(sketch, "E5644", {"start": v(5.3, -18.2) * mm, "end": v(5.11, -18.3) * mm});
            skLineSegment(sketch, "E5645", {"start": v(5.11, -18.3) * mm, "end": v(4.9, -18.37) * mm});
            skLineSegment(sketch, "E5646", {"start": v(4.9, -18.37) * mm, "end": v(4.68, -18.45) * mm});
            skLineSegment(sketch, "E5647", {"start": v(4.68, -18.45) * mm, "end": v(4.44, -18.52) * mm});
            skLineSegment(sketch, "E5648", {"start": v(4.44, -18.52) * mm, "end": v(4.2, -18.58) * mm});
            skLineSegment(sketch, "E5649", {"start": v(4.2, -18.58) * mm, "end": v(4, -18.63) * mm});
            skLineSegment(sketch, "E5650", {"start": v(4, -18.63) * mm, "end": v(3.8, -18.66) * mm});
            skLineSegment(sketch, "E5651", {"start": v(3.8, -18.66) * mm, "end": v(3.65, -18.67) * mm});
            skLineSegment(sketch, "E5652", {"start": v(3.65, -18.67) * mm, "end": v(3.42, -18.67) * mm});
            skLineSegment(sketch, "E5653", {"start": v(3.42, -18.67) * mm, "end": v(4.86, -18.04) * mm});
            skLineSegment(sketch, "E5654", {"start": v(4.86, -18.04) * mm, "end": v(5.17, -17.74) * mm});
            skLineSegment(sketch, "E5655", {"start": v(5.17, -17.74) * mm, "end": v(5.3, -17.6) * mm});
            skLineSegment(sketch, "E5656", {"start": v(5.3, -17.6) * mm, "end": v(5.42, -17.46) * mm});
            skLineSegment(sketch, "E5657", {"start": v(5.42, -17.46) * mm, "end": v(5.53, -17.32) * mm});
            skLineSegment(sketch, "E5658", {"start": v(5.53, -17.32) * mm, "end": v(5.6, -17.2) * mm});
            skLineSegment(sketch, "E5659", {"start": v(5.6, -17.2) * mm, "end": v(5.73, -16.95) * mm});
            skLineSegment(sketch, "E5660", {"start": v(5.73, -16.95) * mm, "end": v(5.71, -16.68) * mm});
            skLineSegment(sketch, "E5661", {"start": v(5.71, -16.68) * mm, "end": v(5.7, -16.57) * mm});
            skLineSegment(sketch, "E5662", {"start": v(5.7, -16.57) * mm, "end": v(5.69, -16.48) * mm});
            skLineSegment(sketch, "E5663", {"start": v(5.69, -16.48) * mm, "end": v(5.67, -16.43) * mm});
            skLineSegment(sketch, "E5664", {"start": v(5.67, -16.43) * mm, "end": v(5.64, -16.4) * mm});
            skLineSegment(sketch, "E5665", {"start": v(5.64, -16.4) * mm, "end": v(5.6, -16.43) * mm});
            skLineSegment(sketch, "E5666", {"start": v(5.6, -16.43) * mm, "end": v(5.5, -16.48) * mm});
            skLineSegment(sketch, "E5667", {"start": v(5.5, -16.48) * mm, "end": v(5.2, -16.67) * mm});
            skLineSegment(sketch, "E5668", {"start": v(5.2, -16.67) * mm, "end": v(4.8, -16.94) * mm});
            skLineSegment(sketch, "E5669", {"start": v(4.8, -16.94) * mm, "end": v(4.5, -17) * mm});
            skLineSegment(sketch, "E5670", {"start": v(4.5, -17) * mm, "end": v(4.38, -17.02) * mm});
            skLineSegment(sketch, "E5671", {"start": v(4.38, -17.02) * mm, "end": v(4.26, -17.03) * mm});
            skLineSegment(sketch, "E5672", {"start": v(4.26, -17.03) * mm, "end": v(4.16, -17.03) * mm});
            skLineSegment(sketch, "E5673", {"start": v(4.16, -17.03) * mm, "end": v(4.09, -17.02) * mm});
            skLineSegment(sketch, "E5674", {"start": v(4.09, -17.02) * mm, "end": v(3.98, -16.98) * mm});
            skLineSegment(sketch, "E5675", {"start": v(3.98, -16.98) * mm, "end": v(4.97, -16.31) * mm});
            skLineSegment(sketch, "E5676", {"start": v(4.97, -16.31) * mm, "end": v(5.44, -16) * mm});
            skLineSegment(sketch, "E5677", {"start": v(5.44, -16) * mm, "end": v(5.9, -15.67) * mm});
            skLineSegment(sketch, "E5678", {"start": v(5.9, -15.67) * mm, "end": v(6.32, -15.36) * mm});
            skLineSegment(sketch, "E5679", {"start": v(6.32, -15.36) * mm, "end": v(6.74, -15.04) * mm});
            skLineSegment(sketch, "E5680", {"start": v(6.74, -15.04) * mm, "end": v(7.14, -14.73) * mm});
            skLineSegment(sketch, "E5681", {"start": v(7.14, -14.73) * mm, "end": v(7.53, -14.41) * mm});
            skLineSegment(sketch, "E5682", {"start": v(7.53, -14.41) * mm, "end": v(7.9, -14.1) * mm});
            skLineSegment(sketch, "E5683", {"start": v(7.9, -14.1) * mm, "end": v(8.26, -13.78) * mm});
            skLineSegment(sketch, "E5684", {"start": v(8.26, -13.78) * mm, "end": v(9.03, -13.1) * mm});
            skLineSegment(sketch, "E5685", {"start": v(9.03, -13.1) * mm, "end": v(10.72, -11.12) * mm});
            skLineSegment(sketch, "E5686", {"start": v(10.72, -11.12) * mm, "end": v(12.18, -8.93) * mm});
            skLineSegment(sketch, "E5687", {"start": v(12.18, -8.93) * mm, "end": v(12.97, -7.3) * mm});
            skLineSegment(sketch, "E5688", {"start": v(12.97, -7.3) * mm, "end": v(13.07, -6.89) * mm});
            skLineSegment(sketch, "E5689", {"start": v(13.07, -6.89) * mm, "end": v(13.1, -6.7) * mm});
            skLineSegment(sketch, "E5690", {"start": v(13.1, -6.7) * mm, "end": v(13.13, -6.48) * mm});
            skLineSegment(sketch, "E5691", {"start": v(13.13, -6.48) * mm, "end": v(13.15, -6.26) * mm});
            skLineSegment(sketch, "E5692", {"start": v(13.15, -6.26) * mm, "end": v(13.16, -6.07) * mm});
            skLineSegment(sketch, "E5693", {"start": v(13.16, -6.07) * mm, "end": v(13.16, -5.66) * mm});
            skLineSegment(sketch, "E5694", {"start": v(13.16, -5.66) * mm, "end": v(12.98, -5.3) * mm});
            skLineSegment(sketch, "E5695", {"start": v(12.98, -5.3) * mm, "end": v(12.9, -5.14) * mm});
            skLineSegment(sketch, "E5696", {"start": v(12.9, -5.14) * mm, "end": v(12.8, -4.97) * mm});
            skLineSegment(sketch, "E5697", {"start": v(12.8, -4.97) * mm, "end": v(12.69, -4.8) * mm});
            skLineSegment(sketch, "E5698", {"start": v(12.69, -4.8) * mm, "end": v(12.6, -4.68) * mm});
            skLineSegment(sketch, "E5699", {"start": v(12.6, -4.68) * mm, "end": v(12.37, -4.42) * mm});
            skLineSegment(sketch, "E5700", {"start": v(12.37, -4.42) * mm, "end": v(12.31, -4.51) * mm});
            skLineSegment(sketch, "E5701", {"start": v(12.31, -4.51) * mm, "end": v(12.28, -4.6) * mm});
            skLineSegment(sketch, "E5702", {"start": v(12.28, -4.6) * mm, "end": v(12.25, -4.78) * mm});
            skLineSegment(sketch, "E5703", {"start": v(12.25, -4.78) * mm, "end": v(12.16, -5.3) * mm});
            skLineSegment(sketch, "E5704", {"start": v(12.16, -5.3) * mm, "end": v(12.11, -5.61) * mm});
            skLineSegment(sketch, "E5705", {"start": v(12.11, -5.61) * mm, "end": v(12.04, -5.94) * mm});
            skLineSegment(sketch, "E5706", {"start": v(12.04, -5.94) * mm, "end": v(11.96, -6.28) * mm});
            skLineSegment(sketch, "E5707", {"start": v(11.96, -6.28) * mm, "end": v(11.87, -6.62) * mm});
            skLineSegment(sketch, "E5708", {"start": v(11.87, -6.62) * mm, "end": v(11.76, -6.97) * mm});
            skLineSegment(sketch, "E5709", {"start": v(11.76, -6.97) * mm, "end": v(11.64, -7.33) * mm});
            skLineSegment(sketch, "E5710", {"start": v(11.64, -7.33) * mm, "end": v(11.51, -7.68) * mm});
            skLineSegment(sketch, "E5711", {"start": v(11.51, -7.68) * mm, "end": v(11.37, -8.04) * mm});
            skLineSegment(sketch, "E5712", {"start": v(11.37, -8.04) * mm, "end": v(11.22, -8.4) * mm});
            skLineSegment(sketch, "E5713", {"start": v(11.22, -8.4) * mm, "end": v(11.05, -8.76) * mm});
            skLineSegment(sketch, "E5714", {"start": v(11.05, -8.76) * mm, "end": v(10.88, -9.11) * mm});
            skLineSegment(sketch, "E5715", {"start": v(10.88, -9.11) * mm, "end": v(10.7, -9.47) * mm});
            skLineSegment(sketch, "E5716", {"start": v(10.7, -9.47) * mm, "end": v(10.5, -9.81) * mm});
            skLineSegment(sketch, "E5717", {"start": v(10.5, -9.81) * mm, "end": v(10.3, -10.15) * mm});
            skLineSegment(sketch, "E5718", {"start": v(10.3, -10.15) * mm, "end": v(10.1, -10.49) * mm});
            skLineSegment(sketch, "E5719", {"start": v(10.1, -10.49) * mm, "end": v(9.88, -10.81) * mm});
            skLineSegment(sketch, "E5720", {"start": v(9.88, -10.81) * mm, "end": v(9.33, -11.61) * mm});
            skLineSegment(sketch, "E5721", {"start": v(9.33, -11.61) * mm, "end": v(7.63, -13.4) * mm});
            skLineSegment(sketch, "E5722", {"start": v(7.63, -13.4) * mm, "end": v(5.4, -15.18) * mm});
            skLineSegment(sketch, "E5723", {"start": v(5.4, -15.18) * mm, "end": v(4.7, -15.68) * mm});
            skLineSegment(sketch, "E5724", {"start": v(4.7, -15.68) * mm, "end": v(3.95, -16.2) * mm});
            skLineSegment(sketch, "E5725", {"start": v(3.95, -16.2) * mm, "end": v(3.35, -16.64) * mm});
            skLineSegment(sketch, "E5726", {"start": v(3.35, -16.64) * mm, "end": v(2.87, -17) * mm});
            skLineSegment(sketch, "E5727", {"start": v(2.87, -17) * mm, "end": v(2.5, -17.31) * mm});
            skLineSegment(sketch, "E5728", {"start": v(2.5, -17.31) * mm, "end": v(2.2, -17.59) * mm});
            skLineSegment(sketch, "E5729", {"start": v(2.2, -17.59) * mm, "end": v(2.08, -17.72) * mm});
            skLineSegment(sketch, "E5730", {"start": v(2.08, -17.72) * mm, "end": v(1.97, -17.85) * mm});
            skLineSegment(sketch, "E5731", {"start": v(1.97, -17.85) * mm, "end": v(1.77, -18.1) * mm});
            skLineSegment(sketch, "E5732", {"start": v(1.77, -18.1) * mm, "end": v(1.59, -18.4) * mm});
            skLineSegment(sketch, "E5733", {"start": v(1.59, -18.4) * mm, "end": v(1.34, -18.8) * mm});
            skLineSegment(sketch, "E5734", {"start": v(1.34, -18.8) * mm, "end": v(1.04, -20.03) * mm});
            skLineSegment(sketch, "E5735", {"start": v(1.04, -20.03) * mm, "end": v(0.8, -20.41) * mm});
            skLineSegment(sketch, "E5736", {"start": v(0.8, -20.41) * mm, "end": v(0.7, -20.6) * mm});
            skLineSegment(sketch, "E5737", {"start": v(0.7, -20.6) * mm, "end": v(0.58, -20.77) * mm});
            skLineSegment(sketch, "E5738", {"start": v(0.58, -20.77) * mm, "end": v(0.45, -20.92) * mm});
            skLineSegment(sketch, "E5739", {"start": v(0.45, -20.92) * mm, "end": v(0.32, -21.06) * mm});
            skLineSegment(sketch, "E5740", {"start": v(0.32, -21.06) * mm, "end": v(0.19, -21.18) * mm});
            skLineSegment(sketch, "E5741", {"start": v(0.19, -21.18) * mm, "end": v(0.05, -21.3) * mm});
            skLineSegment(sketch, "E5742", {"start": v(0.05, -21.3) * mm, "end": v(-0.09, -21.38) * mm});
            skLineSegment(sketch, "E5743", {"start": v(-0.09, -21.38) * mm, "end": v(-0.22, -21.45) * mm});
            skLineSegment(sketch, "E5744", {"start": v(-0.22, -21.45) * mm, "end": v(-0.47, -21.54) * mm});
            skLineSegment(sketch, "E5745", {"start": v(-0.47, -21.54) * mm, "end": v(-0.53, -21.55) * mm});
            skLineSegment(sketch, "E5746", {"start": v(-0.53, -21.55) * mm, "end": v(-0.55, -21.55) * mm});
            skLineSegment(sketch, "E5747", {"start": v(-0.55, -21.55) * mm, "end": v(-0.56, -21.54) * mm});
            skLineSegment(sketch, "E5748", {"start": v(-0.56, -21.54) * mm, "end": v(-0.55, -21.5) * mm});
            skLineSegment(sketch, "E5749", {"start": v(-0.55, -21.5) * mm, "end": v(-0.5, -21.43) * mm});
            skLineSegment(sketch, "E5750", {"start": v(-0.5, -21.43) * mm, "end": v(-0.3, -21.18) * mm});
            skLineSegment(sketch, "E5751", {"start": v(-0.3, -21.18) * mm, "end": v(-0.17, -21) * mm});
            skLineSegment(sketch, "E5752", {"start": v(-0.17, -21) * mm, "end": v(-0.02, -20.78) * mm});
            skLineSegment(sketch, "E5753", {"start": v(-0.02, -20.78) * mm, "end": v(0.12, -20.55) * mm});
            skLineSegment(sketch, "E5754", {"start": v(0.12, -20.55) * mm, "end": v(0.23, -20.35) * mm});
            skLineSegment(sketch, "E5755", {"start": v(0.23, -20.35) * mm, "end": v(0.37, -20.05) * mm});
            skLineSegment(sketch, "E5756", {"start": v(0.37, -20.05) * mm, "end": v(0.49, -19.75) * mm});
            skLineSegment(sketch, "E5757", {"start": v(0.49, -19.75) * mm, "end": v(0.62, -19.34) * mm});
            skLineSegment(sketch, "E5758", {"start": v(0.62, -19.34) * mm, "end": v(0.8, -18.71) * mm});
            skLineSegment(sketch, "E5759", {"start": v(0.8, -18.71) * mm, "end": v(0.88, -18.43) * mm});
            skLineSegment(sketch, "E5760", {"start": v(0.88, -18.43) * mm, "end": v(0.97, -18.16) * mm});
            skLineSegment(sketch, "E5761", {"start": v(0.97, -18.16) * mm, "end": v(1.07, -17.9) * mm});
            skLineSegment(sketch, "E5762", {"start": v(1.07, -17.9) * mm, "end": v(1.18, -17.66) * mm});
            skLineSegment(sketch, "E5763", {"start": v(1.18, -17.66) * mm, "end": v(1.3, -17.42) * mm});
            skLineSegment(sketch, "E5764", {"start": v(1.3, -17.42) * mm, "end": v(1.44, -17.18) * mm});
            skLineSegment(sketch, "E5765", {"start": v(1.44, -17.18) * mm, "end": v(1.58, -16.95) * mm});
            skLineSegment(sketch, "E5766", {"start": v(1.58, -16.95) * mm, "end": v(1.75, -16.72) * mm});
            skLineSegment(sketch, "E5767", {"start": v(1.75, -16.72) * mm, "end": v(1.93, -16.5) * mm});
            skLineSegment(sketch, "E5768", {"start": v(1.93, -16.5) * mm, "end": v(2.13, -16.26) * mm});
            skLineSegment(sketch, "E5769", {"start": v(2.13, -16.26) * mm, "end": v(2.36, -16.01) * mm});
            skLineSegment(sketch, "E5770", {"start": v(2.36, -16.01) * mm, "end": v(2.6, -15.76) * mm});
            skLineSegment(sketch, "E5771", {"start": v(2.6, -15.76) * mm, "end": v(2.88, -15.5) * mm});
            skLineSegment(sketch, "E5772", {"start": v(2.88, -15.5) * mm, "end": v(3.18, -15.23) * mm});
            skLineSegment(sketch, "E5773", {"start": v(3.18, -15.23) * mm, "end": v(3.87, -14.63) * mm});
            skLineSegment(sketch, "E5774", {"start": v(3.87, -14.63) * mm, "end": v(4.34, -14.23) * mm});
            skLineSegment(sketch, "E5775", {"start": v(4.34, -14.23) * mm, "end": v(4.87, -13.74) * mm});
            skLineSegment(sketch, "E5776", {"start": v(4.87, -13.74) * mm, "end": v(5.4, -13.23) * mm});
            skLineSegment(sketch, "E5777", {"start": v(5.4, -13.23) * mm, "end": v(5.87, -12.77) * mm});
            skLineSegment(sketch, "E5778", {"start": v(5.87, -12.77) * mm, "end": v(6.88, -11.74) * mm});
            skLineSegment(sketch, "E5779", {"start": v(6.88, -11.74) * mm, "end": v(7.88, -10.47) * mm});
            skLineSegment(sketch, "E5780", {"start": v(7.88, -10.47) * mm, "end": v(8.62, -9.1) * mm});
            skLineSegment(sketch, "E5781", {"start": v(8.62, -9.1) * mm, "end": v(9, -7.75) * mm});
            skLineSegment(sketch, "E5782", {"start": v(9, -7.75) * mm, "end": v(9, -7.04) * mm});
            skLineSegment(sketch, "E5783", {"start": v(9, -7.04) * mm, "end": v(8.62, -6.26) * mm});
            skLineSegment(sketch, "E5784", {"start": v(8.62, -6.26) * mm, "end": v(8.32, -6.08) * mm});
            skLineSegment(sketch, "E5785", {"start": v(8.32, -6.08) * mm, "end": v(8.2, -6) * mm});
            skLineSegment(sketch, "E5786", {"start": v(8.2, -6) * mm, "end": v(8.06, -5.94) * mm});
            skLineSegment(sketch, "E5787", {"start": v(8.06, -5.94) * mm, "end": v(7.95, -5.9) * mm});
            skLineSegment(sketch, "E5788", {"start": v(7.95, -5.9) * mm, "end": v(7.87, -5.9) * mm});
            skLineSegment(sketch, "E5789", {"start": v(7.87, -5.9) * mm, "end": v(7.7, -5.9) * mm});
            skLineSegment(sketch, "E5790", {"start": v(7.7, -5.9) * mm, "end": v(7.78, -6.28) * mm});
            skLineSegment(sketch, "E5791", {"start": v(7.78, -6.28) * mm, "end": v(7.8, -6.47) * mm});
            skLineSegment(sketch, "E5792", {"start": v(7.8, -6.47) * mm, "end": v(7.82, -6.71) * mm});
            skLineSegment(sketch, "E5793", {"start": v(7.82, -6.71) * mm, "end": v(7.83, -6.97) * mm});
            skLineSegment(sketch, "E5794", {"start": v(7.83, -6.97) * mm, "end": v(7.83, -7.22) * mm});
            skLineSegment(sketch, "E5795", {"start": v(7.83, -7.22) * mm, "end": v(7.81, -7.79) * mm});
            skLineSegment(sketch, "E5796", {"start": v(7.81, -7.79) * mm, "end": v(7.46, -8.93) * mm});
            skLineSegment(sketch, "E5797", {"start": v(7.46, -8.93) * mm, "end": v(7.07, -9.6) * mm});
            skLineSegment(sketch, "E5798", {"start": v(7.07, -9.6) * mm, "end": v(6.85, -9.97) * mm});
            skLineSegment(sketch, "E5799", {"start": v(6.85, -9.97) * mm, "end": v(6.62, -10.33) * mm});
            skLineSegment(sketch, "E5800", {"start": v(6.62, -10.33) * mm, "end": v(6.37, -10.69) * mm});
            skLineSegment(sketch, "E5801", {"start": v(6.37, -10.69) * mm, "end": v(6.1, -11.04) * mm});
            skLineSegment(sketch, "E5802", {"start": v(6.1, -11.04) * mm, "end": v(5.82, -11.39) * mm});
            skLineSegment(sketch, "E5803", {"start": v(5.82, -11.39) * mm, "end": v(5.53, -11.73) * mm});
            skLineSegment(sketch, "E5804", {"start": v(5.53, -11.73) * mm, "end": v(5.22, -12.06) * mm});
            skLineSegment(sketch, "E5805", {"start": v(5.22, -12.06) * mm, "end": v(4.9, -12.4) * mm});
            skLineSegment(sketch, "E5806", {"start": v(4.9, -12.4) * mm, "end": v(4.15, -13.14) * mm});
            skLineSegment(sketch, "E5807", {"start": v(4.15, -13.14) * mm, "end": v(2.33, -14.51) * mm});
            skLineSegment(sketch, "E5808", {"start": v(2.33, -14.51) * mm, "end": v(1.94, -14.9) * mm});
            skLineSegment(sketch, "E5809", {"start": v(1.94, -14.9) * mm, "end": v(1.75, -15.08) * mm});
            skLineSegment(sketch, "E5810", {"start": v(1.75, -15.08) * mm, "end": v(1.56, -15.28) * mm});
            skLineSegment(sketch, "E5811", {"start": v(1.56, -15.28) * mm, "end": v(1.39, -15.5) * mm});
            skLineSegment(sketch, "E5812", {"start": v(1.39, -15.5) * mm, "end": v(1.21, -15.72) * mm});
            skLineSegment(sketch, "E5813", {"start": v(1.21, -15.72) * mm, "end": v(1.04, -15.96) * mm});
            skLineSegment(sketch, "E5814", {"start": v(1.04, -15.96) * mm, "end": v(0.88, -16.22) * mm});
            skLineSegment(sketch, "E5815", {"start": v(0.88, -16.22) * mm, "end": v(0.72, -16.48) * mm});
            skLineSegment(sketch, "E5816", {"start": v(0.72, -16.48) * mm, "end": v(0.56, -16.76) * mm});
            skLineSegment(sketch, "E5817", {"start": v(0.56, -16.76) * mm, "end": v(0.41, -17.06) * mm});
            skLineSegment(sketch, "E5818", {"start": v(0.41, -17.06) * mm, "end": v(0.26, -17.37) * mm});
            skLineSegment(sketch, "E5819", {"start": v(0.26, -17.37) * mm, "end": v(0.11, -17.7) * mm});
            skLineSegment(sketch, "E5820", {"start": v(0.11, -17.7) * mm, "end": v(-0.03, -18.05) * mm});
            skLineSegment(sketch, "E5821", {"start": v(-0.03, -18.05) * mm, "end": v(-0.17, -18.42) * mm});
            skLineSegment(sketch, "E5822", {"start": v(-0.17, -18.42) * mm, "end": v(-0.31, -18.8) * mm});
            skLineSegment(sketch, "E5823", {"start": v(-0.31, -18.8) * mm, "end": v(-0.59, -19.62) * mm});
            skLineSegment(sketch, "E5824", {"start": v(-0.59, -19.62) * mm, "end": v(-0.78, -20.2) * mm});
            skLineSegment(sketch, "E5825", {"start": v(-0.78, -20.2) * mm, "end": v(-0.87, -20.44) * mm});
            skLineSegment(sketch, "E5826", {"start": v(-0.87, -20.44) * mm, "end": v(-0.94, -20.6) * mm});
            skLineSegment(sketch, "E5827", {"start": v(-0.94, -20.6) * mm, "end": v(-1.07, -20.84) * mm});
            skLineSegment(sketch, "E5828", {"start": v(-1.07, -20.84) * mm, "end": v(-1.43, -20.84) * mm});
            skLineSegment(sketch, "E5829", {"start": v(-1.43, -20.84) * mm, "end": v(-1.63, -20.35) * mm});
            skLineSegment(sketch, "E5830", {"start": v(-1.63, -20.35) * mm, "end": v(-1.56, -18.62) * mm});
            skLineSegment(sketch, "E5831", {"start": v(-1.56, -18.62) * mm, "end": v(-1.27, -18.01) * mm});
            skLineSegment(sketch, "E5832", {"start": v(-1.27, -18.01) * mm, "end": v(-1.12, -17.7) * mm});
            skLineSegment(sketch, "E5833", {"start": v(-1.12, -17.7) * mm, "end": v(-0.97, -17.42) * mm});
            skLineSegment(sketch, "E5834", {"start": v(-0.97, -17.42) * mm, "end": v(-0.8, -17.15) * mm});
            skLineSegment(sketch, "E5835", {"start": v(-0.8, -17.15) * mm, "end": v(-0.61, -16.88) * mm});
            skLineSegment(sketch, "E5836", {"start": v(-0.61, -16.88) * mm, "end": v(-0.4, -16.6) * mm});
            skLineSegment(sketch, "E5837", {"start": v(-0.4, -16.6) * mm, "end": v(-0.13, -16.3) * mm});
            skLineSegment(sketch, "E5838", {"start": v(-0.13, -16.3) * mm, "end": v(0.19, -15.95) * mm});
            skLineSegment(sketch, "E5839", {"start": v(0.19, -15.95) * mm, "end": v(0.56, -15.55) * mm});
            skLineSegment(sketch, "E5840", {"start": v(0.56, -15.55) * mm, "end": v(1.54, -14.53) * mm});
            skLineSegment(sketch, "E5841", {"start": v(1.54, -14.53) * mm, "end": v(1.96, -13.73) * mm});
            skLineSegment(sketch, "E5842", {"start": v(1.96, -13.73) * mm, "end": v(1.95, -12.62) * mm});
            skLineSegment(sketch, "E5843", {"start": v(1.95, -12.62) * mm, "end": v(1.51, -11.66) * mm});
            skLineSegment(sketch, "E5844", {"start": v(1.51, -11.66) * mm, "end": v(2.88, -11.62) * mm});
            skLineSegment(sketch, "E5845", {"start": v(2.88, -11.62) * mm, "end": v(3.54, -11.34) * mm});
            skLineSegment(sketch, "E5846", {"start": v(3.54, -11.34) * mm, "end": v(3.68, -11.13) * mm});
            skLineSegment(sketch, "E5847", {"start": v(3.68, -11.13) * mm, "end": v(3.79, -10.92) * mm});
            skLineSegment(sketch, "E5848", {"start": v(3.79, -10.92) * mm, "end": v(3.84, -10.81) * mm});
            skLineSegment(sketch, "E5849", {"start": v(3.84, -10.81) * mm, "end": v(3.87, -10.72) * mm});
            skLineSegment(sketch, "E5850", {"start": v(3.87, -10.72) * mm, "end": v(3.93, -10.51) * mm});
            skLineSegment(sketch, "E5851", {"start": v(3.93, -10.51) * mm, "end": v(3.64, -10.4) * mm});
            skLineSegment(sketch, "E5852", {"start": v(3.64, -10.4) * mm, "end": v(3.18, -10.9) * mm});
            skLineSegment(sketch, "E5853", {"start": v(3.18, -10.9) * mm, "end": v(2.71, -10.84) * mm});
            skLineSegment(sketch, "E5854", {"start": v(2.71, -10.84) * mm, "end": v(2.5, -10.8) * mm});
            skLineSegment(sketch, "E5855", {"start": v(2.5, -10.8) * mm, "end": v(2.22, -10.75) * mm});
            skLineSegment(sketch, "E5856", {"start": v(2.22, -10.75) * mm, "end": v(1.54, -10.6) * mm});
            skLineSegment(sketch, "E5857", {"start": v(1.54, -10.6) * mm, "end": v(0.73, -10.38) * mm});
            skLineSegment(sketch, "E5858", {"start": v(0.73, -10.38) * mm, "end": v(-0.15, -10.11) * mm});
            skLineSegment(sketch, "E5859", {"start": v(-0.15, -10.11) * mm, "end": v(-0.92, -9.88) * mm});
            skLineSegment(sketch, "E5860", {"start": v(-0.92, -9.88) * mm, "end": v(-1.96, -9.88) * mm});
            skLineSegment(sketch, "E5861", {"start": v(-1.96, -9.88) * mm, "end": v(-2.4, -10.07) * mm});
            skLineSegment(sketch, "E5862", {"start": v(-2.4, -10.07) * mm, "end": v(-2.7, -10.6) * mm});
            skLineSegment(sketch, "E5863", {"start": v(-2.7, -10.6) * mm, "end": v(-2.97, -10.6) * mm});
            skLineSegment(sketch, "E5864", {"start": v(-2.97, -10.6) * mm, "end": v(-3.19, -10.62) * mm});
            skLineSegment(sketch, "E5865", {"start": v(-3.19, -10.62) * mm, "end": v(-3.29, -10.63) * mm});
            skLineSegment(sketch, "E5866", {"start": v(-3.29, -10.63) * mm, "end": v(-3.36, -10.65) * mm});
            skLineSegment(sketch, "E5867", {"start": v(-3.36, -10.65) * mm, "end": v(-3.5, -10.7) * mm});
            skLineSegment(sketch, "E5868", {"start": v(-3.5, -10.7) * mm, "end": v(-3.56, -10.5) * mm});
            skLineSegment(sketch, "E5869", {"start": v(-3.56, -10.5) * mm, "end": v(-3.63, -10.32) * mm});
            skLineSegment(sketch, "E5870", {"start": v(-3.63, -10.32) * mm, "end": v(-3.67, -10.24) * mm});
            skLineSegment(sketch, "E5871", {"start": v(-3.67, -10.24) * mm, "end": v(-3.7, -10.19) * mm});
            skLineSegment(sketch, "E5872", {"start": v(-3.7, -10.19) * mm, "end": v(-3.78, -10.1) * mm});
            skLineSegment(sketch, "E5873", {"start": v(-3.78, -10.1) * mm, "end": v(-4.34, -10.17) * mm});
            skLineSegment(sketch, "E5874", {"start": v(-4.34, -10.17) * mm, "end": v(-4.23, -10.78) * mm});
            skLineSegment(sketch, "E5875", {"start": v(-4.23, -10.78) * mm, "end": v(-4.48, -10.91) * mm});
            skLineSegment(sketch, "E5876", {"start": v(-4.48, -10.91) * mm, "end": v(-4.6, -10.99) * mm});
            skLineSegment(sketch, "E5877", {"start": v(-4.6, -10.99) * mm, "end": v(-4.73, -11.07) * mm});
            skLineSegment(sketch, "E5878", {"start": v(-4.73, -11.07) * mm, "end": v(-4.84, -11.15) * mm});
            skLineSegment(sketch, "E5879", {"start": v(-4.84, -11.15) * mm, "end": v(-4.94, -11.23) * mm});
            skLineSegment(sketch, "E5880", {"start": v(-4.94, -11.23) * mm, "end": v(-5.03, -11.32) * mm});
            skLineSegment(sketch, "E5881", {"start": v(-5.03, -11.32) * mm, "end": v(-5.1, -11.4) * mm});
            skLineSegment(sketch, "E5882", {"start": v(-5.1, -11.4) * mm, "end": v(-5.17, -11.5) * mm});
            skLineSegment(sketch, "E5883", {"start": v(-5.17, -11.5) * mm, "end": v(-5.22, -11.58) * mm});
            skLineSegment(sketch, "E5884", {"start": v(-5.22, -11.58) * mm, "end": v(-5.33, -11.78) * mm});
            skLineSegment(sketch, "E5885", {"start": v(-5.33, -11.78) * mm, "end": v(-5.22, -11.96) * mm});
            skLineSegment(sketch, "E5886", {"start": v(-5.22, -11.96) * mm, "end": v(-4.87, -11.78) * mm});
            skLineSegment(sketch, "E5887", {"start": v(-4.87, -11.78) * mm, "end": v(-4.72, -11.71) * mm});
            skLineSegment(sketch, "E5888", {"start": v(-4.72, -11.71) * mm, "end": v(-4.56, -11.65) * mm});
            skLineSegment(sketch, "E5889", {"start": v(-4.56, -11.65) * mm, "end": v(-4.43, -11.61) * mm});
            skLineSegment(sketch, "E5890", {"start": v(-4.43, -11.61) * mm, "end": v(-4.33, -11.6) * mm});
            skLineSegment(sketch, "E5891", {"start": v(-4.33, -11.6) * mm, "end": v(-4.13, -11.6) * mm});
            skLineSegment(sketch, "E5892", {"start": v(-4.13, -11.6) * mm, "end": v(-4.2, -12.19) * mm});
            skLineSegment(sketch, "E5893", {"start": v(-4.2, -12.19) * mm, "end": v(-4.7, -12.25) * mm});
            skLineSegment(sketch, "E5894", {"start": v(-4.7, -12.25) * mm, "end": v(-4.7, -12.35) * mm});
            skLineSegment(sketch, "E5895", {"start": v(-4.7, -12.35) * mm, "end": v(-4.68, -12.4) * mm});
            skLineSegment(sketch, "E5896", {"start": v(-4.68, -12.4) * mm, "end": v(-4.64, -12.47) * mm});
            skLineSegment(sketch, "E5897", {"start": v(-4.64, -12.47) * mm, "end": v(-4.6, -12.54) * mm});
            skLineSegment(sketch, "E5898", {"start": v(-4.6, -12.54) * mm, "end": v(-4.54, -12.62) * mm});
            skLineSegment(sketch, "E5899", {"start": v(-4.54, -12.62) * mm, "end": v(-4.38, -12.79) * mm});
            skLineSegment(sketch, "E5900", {"start": v(-4.38, -12.79) * mm, "end": v(-4.68, -13.28) * mm});
            skLineSegment(sketch, "E5901", {"start": v(-4.68, -13.28) * mm, "end": v(-4.84, -13.26) * mm});
            skLineSegment(sketch, "E5902", {"start": v(-4.84, -13.26) * mm, "end": v(-5.39, -13.18) * mm});
            skLineSegment(sketch, "E5903", {"start": v(-5.39, -13.18) * mm, "end": v(-5.77, -13.12) * mm});
            skLineSegment(sketch, "E5904", {"start": v(-5.77, -13.12) * mm, "end": v(-6.42, -13.5) * mm});
            skLineSegment(sketch, "E5905", {"start": v(-6.42, -13.5) * mm, "end": v(-7.03, -13.5) * mm});
            skLineSegment(sketch, "E5906", {"start": v(-7.03, -13.5) * mm, "end": v(-7.12, -13.76) * mm});
            skLineSegment(sketch, "E5907", {"start": v(-7.12, -13.76) * mm, "end": v(-6.72, -14.14) * mm});
            skLineSegment(sketch, "E5908", {"start": v(-6.72, -14.14) * mm, "end": v(-6.44, -14.14) * mm});
            skLineSegment(sketch, "E5909", {"start": v(-6.44, -14.14) * mm, "end": v(-6.3, -14.13) * mm});
            skLineSegment(sketch, "E5910", {"start": v(-6.3, -14.13) * mm, "end": v(-6.13, -14.1) * mm});
            skLineSegment(sketch, "E5911", {"start": v(-6.13, -14.1) * mm, "end": v(-5.95, -14.07) * mm});
            skLineSegment(sketch, "E5912", {"start": v(-5.95, -14.07) * mm, "end": v(-5.78, -14.02) * mm});
            skLineSegment(sketch, "E5913", {"start": v(-5.78, -14.02) * mm, "end": v(-5.4, -13.91) * mm});
            skLineSegment(sketch, "E5914", {"start": v(-5.4, -13.91) * mm, "end": v(-6.09, -14.36) * mm});
            skLineSegment(sketch, "E5915", {"start": v(-6.09, -14.36) * mm, "end": v(-6.5, -14.98) * mm});
            skLineSegment(sketch, "E5916", {"start": v(-6.5, -14.98) * mm, "end": v(-6.5, -15.3) * mm});
            skLineSegment(sketch, "E5917", {"start": v(-6.5, -15.3) * mm, "end": v(-6.1, -15.77) * mm});
            skLineSegment(sketch, "E5918", {"start": v(-6.1, -15.77) * mm, "end": v(-5.69, -15.85) * mm});
            skLineSegment(sketch, "E5919", {"start": v(-5.69, -15.85) * mm, "end": v(-5.69, -15.45) * mm});
            skLineSegment(sketch, "E5920", {"start": v(-5.69, -15.45) * mm, "end": v(-5.43, -15.13) * mm});
            skLineSegment(sketch, "E5921", {"start": v(-5.43, -15.13) * mm, "end": v(-5.31, -14.98) * mm});
            skLineSegment(sketch, "E5922", {"start": v(-5.31, -14.98) * mm, "end": v(-5.19, -14.78) * mm});
            skLineSegment(sketch, "E5923", {"start": v(-5.19, -14.78) * mm, "end": v(-5.07, -14.57) * mm});
            skLineSegment(sketch, "E5924", {"start": v(-5.07, -14.57) * mm, "end": v(-4.98, -14.38) * mm});
            skLineSegment(sketch, "E5925", {"start": v(-4.98, -14.38) * mm, "end": v(-4.78, -13.93) * mm});
            skLineSegment(sketch, "E5926", {"start": v(-4.78, -13.93) * mm, "end": v(-3.97, -14.68) * mm});
            skLineSegment(sketch, "E5927", {"start": v(-3.97, -14.68) * mm, "end": v(-3.36, -14.68) * mm});
            skLineSegment(sketch, "E5928", {"start": v(-3.36, -14.68) * mm, "end": v(-3.12, -14.43) * mm});
            skLineSegment(sketch, "E5929", {"start": v(-3.12, -14.43) * mm, "end": v(-3.03, -14.32) * mm});
            skLineSegment(sketch, "E5930", {"start": v(-3.03, -14.32) * mm, "end": v(-2.95, -14.21) * mm});
            skLineSegment(sketch, "E5931", {"start": v(-2.95, -14.21) * mm, "end": v(-2.9, -14.12) * mm});
            skLineSegment(sketch, "E5932", {"start": v(-2.9, -14.12) * mm, "end": v(-2.88, -14.05) * mm});
            skLineSegment(sketch, "E5933", {"start": v(-2.88, -14.05) * mm, "end": v(-2.88, -13.94) * mm});
            skLineSegment(sketch, "E5934", {"start": v(-2.88, -13.94) * mm, "end": v(-3.35, -14.06) * mm});
            skLineSegment(sketch, "E5935", {"start": v(-3.35, -14.06) * mm, "end": v(-4.31, -13.47) * mm});
            skLineSegment(sketch, "E5936", {"start": v(-4.31, -13.47) * mm, "end": v(-3.77, -12.8) * mm});
            skLineSegment(sketch, "E5937", {"start": v(-3.77, -12.8) * mm, "end": v(-1.69, -12.57) * mm});
            skLineSegment(sketch, "E5938", {"start": v(-1.69, -12.57) * mm, "end": v(-1.08, -13.16) * mm});
            skLineSegment(sketch, "E5939", {"start": v(-1.08, -13.16) * mm, "end": v(-0.96, -13.85) * mm});
            skLineSegment(sketch, "E5940", {"start": v(-0.96, -13.85) * mm, "end": v(-1.24, -14.39) * mm});
            skLineSegment(sketch, "E5941", {"start": v(-1.24, -14.39) * mm, "end": v(-1.8, -14.88) * mm});
            skLineSegment(sketch, "E5942", {"start": v(-1.8, -14.88) * mm, "end": v(-2.41, -15.38) * mm});
            skLineSegment(sketch, "E5943", {"start": v(-2.41, -15.38) * mm, "end": v(-3.06, -15.9) * mm});
            skLineSegment(sketch, "E5944", {"start": v(-3.06, -15.9) * mm, "end": v(-3.4, -16.19) * mm});
            skLineSegment(sketch, "E5945", {"start": v(-3.4, -16.19) * mm, "end": v(-3.8, -16.55) * mm});
            skLineSegment(sketch, "E5946", {"start": v(-3.8, -16.55) * mm, "end": v(-4.25, -16.95) * mm});
            skLineSegment(sketch, "E5947", {"start": v(-4.25, -16.95) * mm, "end": v(-4.67, -17.35) * mm});
            skLineSegment(sketch, "E5948", {"start": v(-4.67, -17.35) * mm, "end": v(-5.6, -18.24) * mm});
            skLineSegment(sketch, "E5949", {"start": v(-5.6, -18.24) * mm, "end": v(-6.57, -19.53) * mm});
            skLineSegment(sketch, "E5950", {"start": v(-6.57, -19.53) * mm, "end": v(-7.23, -20.84) * mm});
            skLineSegment(sketch, "E5951", {"start": v(-7.23, -20.84) * mm, "end": v(-7.5, -21.98) * mm});
            skLineSegment(sketch, "E5952", {"start": v(-7.5, -21.98) * mm, "end": v(-7.5, -23.17) * mm});
            skLineSegment(sketch, "E5953", {"start": v(-7.5, -23.17) * mm, "end": v(-7.14, -24.57) * mm});
            skLineSegment(sketch, "E5954", {"start": v(-7.14, -24.57) * mm, "end": v(-6.46, -25.87) * mm});
            skLineSegment(sketch, "E5955", {"start": v(-6.46, -25.87) * mm, "end": v(-5.16, -27.17) * mm});
            skLineSegment(sketch, "E5956", {"start": v(-5.16, -27.17) * mm, "end": v(-4.5, -27.56) * mm});
            skLineSegment(sketch, "E5957", {"start": v(-4.5, -27.56) * mm, "end": v(-4.19, -27.73) * mm});
            skLineSegment(sketch, "E5958", {"start": v(-4.19, -27.73) * mm, "end": v(-3.85, -27.9) * mm});
            skLineSegment(sketch, "E5959", {"start": v(-3.85, -27.9) * mm, "end": v(-3.51, -28.07) * mm});
            skLineSegment(sketch, "E5960", {"start": v(-3.51, -28.07) * mm, "end": v(-3.22, -28.2) * mm});
            skLineSegment(sketch, "E5961", {"start": v(-3.22, -28.2) * mm, "end": v(-2.62, -28.46) * mm});
            skLineSegment(sketch, "E5962", {"start": v(-2.62, -28.46) * mm, "end": v(-0.39, -29) * mm});
            skLineSegment(sketch, "E5963", {"start": v(-0.39, -29) * mm, "end": v(0.86, -29.12) * mm});
            skLineSegment(sketch, "E5964", {"start": v(0.86, -29.12) * mm, "end": v(1.32, -30.12) * mm});
            skLineSegment(sketch, "E5965", {"start": v(1.32, -30.12) * mm, "end": v(1.2, -32.17) * mm});
            skLineSegment(sketch, "E5966", {"start": v(1.2, -32.17) * mm, "end": v(1.27, -32.17) * mm});
            skLineSegment(sketch, "E5967", {"start": v(1.27, -32.17) * mm, "end": v(1.33, -32.15) * mm});
            skLineSegment(sketch, "E5968", {"start": v(1.33, -32.15) * mm, "end": v(1.42, -32.09) * mm});
            skLineSegment(sketch, "E5969", {"start": v(1.42, -32.09) * mm, "end": v(1.68, -31.89) * mm});
            skLineSegment(sketch, "E5970", {"start": v(1.68, -31.89) * mm, "end": v(1.93, -31.7) * mm});
            skLineSegment(sketch, "E5971", {"start": v(1.93, -31.7) * mm, "end": v(2.02, -31.65) * mm});
            skLineSegment(sketch, "E5972", {"start": v(2.02, -31.65) * mm, "end": v(2.04, -31.64) * mm});
            skLineSegment(sketch, "E5973", {"start": v(2.04, -31.64) * mm, "end": v(2.05, -31.64) * mm});
            skLineSegment(sketch, "E5974", {"start": v(2.05, -31.64) * mm, "end": v(2.08, -31.73) * mm});
            skLineSegment(sketch, "E5975", {"start": v(2.08, -31.73) * mm, "end": v(2.13, -31.93) * mm});
            skLineSegment(sketch, "E5976", {"start": v(2.13, -31.93) * mm, "end": v(2.28, -32.6) * mm});
            skLineSegment(sketch, "E5977", {"start": v(2.28, -32.6) * mm, "end": v(2.38, -33.03) * mm});
            skLineSegment(sketch, "E5978", {"start": v(2.38, -33.03) * mm, "end": v(2.48, -33.45) * mm});
            skLineSegment(sketch, "E5979", {"start": v(2.48, -33.45) * mm, "end": v(2.58, -33.85) * mm});
            skLineSegment(sketch, "E5980", {"start": v(2.58, -33.85) * mm, "end": v(2.7, -34.24) * mm});
            skLineSegment(sketch, "E5981", {"start": v(2.7, -34.24) * mm, "end": v(2.82, -34.63) * mm});
            skLineSegment(sketch, "E5982", {"start": v(2.82, -34.63) * mm, "end": v(2.95, -35) * mm});
            skLineSegment(sketch, "E5983", {"start": v(2.95, -35) * mm, "end": v(3.09, -35.38) * mm});
            skLineSegment(sketch, "E5984", {"start": v(3.09, -35.38) * mm, "end": v(3.24, -35.75) * mm});
            skLineSegment(sketch, "E5985", {"start": v(3.24, -35.75) * mm, "end": v(3.57, -36.57) * mm});
            skLineSegment(sketch, "E5986", {"start": v(3.57, -36.57) * mm, "end": v(3.67, -37.07) * mm});
            skLineSegment(sketch, "E5987", {"start": v(3.67, -37.07) * mm, "end": v(3.4, -37.06) * mm});
            skLineSegment(sketch, "E5988", {"start": v(3.4, -37.06) * mm, "end": v(3.26, -37.05) * mm});
            skLineSegment(sketch, "E5989", {"start": v(3.26, -37.05) * mm, "end": v(3.06, -37.01) * mm});
            skLineSegment(sketch, "E5990", {"start": v(3.06, -37.01) * mm, "end": v(2.82, -36.95) * mm});
            skLineSegment(sketch, "E5991", {"start": v(2.82, -36.95) * mm, "end": v(2.57, -36.88) * mm});
            skLineSegment(sketch, "E5992", {"start": v(2.57, -36.88) * mm, "end": v(2, -36.7) * mm});
            skLineSegment(sketch, "E5993", {"start": v(2, -36.7) * mm, "end": v(1.39, -36.7) * mm});
            skLineSegment(sketch, "E5994", {"start": v(1.39, -36.7) * mm, "end": v(1.06, -37.05) * mm});
            skLineSegment(sketch, "E5995", {"start": v(1.06, -37.05) * mm, "end": v(0.3, -37.25) * mm});
            skLineSegment(sketch, "E5996", {"start": v(0.3, -37.25) * mm, "end": v(0.2, -37.43) * mm});
            skLineSegment(sketch, "E5997", {"start": v(0.2, -37.43) * mm, "end": v(0.16, -37.51) * mm});
            skLineSegment(sketch, "E5998", {"start": v(0.16, -37.51) * mm, "end": v(0.13, -37.6) * mm});
            skLineSegment(sketch, "E5999", {"start": v(0.13, -37.6) * mm, "end": v(0.12, -37.67) * mm});
            skLineSegment(sketch, "E6000", {"start": v(0.12, -37.67) * mm, "end": v(0.12, -37.75) * mm});
            skLineSegment(sketch, "E6001", {"start": v(0.12, -37.75) * mm, "end": v(0.13, -37.82) * mm});
            skLineSegment(sketch, "E6002", {"start": v(0.13, -37.82) * mm, "end": v(0.16, -37.89) * mm});
            skLineSegment(sketch, "E6003", {"start": v(0.16, -37.89) * mm, "end": v(0.2, -37.95) * mm});
            skLineSegment(sketch, "E6004", {"start": v(0.2, -37.95) * mm, "end": v(0.26, -38.02) * mm});
            skLineSegment(sketch, "E6005", {"start": v(0.26, -38.02) * mm, "end": v(0.4, -38.16) * mm});
            skLineSegment(sketch, "E6006", {"start": v(0.4, -38.16) * mm, "end": v(0.8, -37.8) * mm});
            skLineSegment(sketch, "E6007", {"start": v(0.8, -37.8) * mm, "end": v(1.2, -37.8) * mm});
            skLineSegment(sketch, "E6008", {"start": v(1.2, -37.8) * mm, "end": v(1.11, -37.97) * mm});
            skLineSegment(sketch, "E6009", {"start": v(1.11, -37.97) * mm, "end": v(1.06, -38.09) * mm});
            skLineSegment(sketch, "E6010", {"start": v(1.06, -38.09) * mm, "end": v(1.04, -38.21) * mm});
            skLineSegment(sketch, "E6011", {"start": v(1.04, -38.21) * mm, "end": v(1.03, -38.33) * mm});
            skLineSegment(sketch, "E6012", {"start": v(1.03, -38.33) * mm, "end": v(1.05, -38.45) * mm});
            skLineSegment(sketch, "E6013", {"start": v(1.05, -38.45) * mm, "end": v(1.09, -38.55) * mm});
            skLineSegment(sketch, "E6014", {"start": v(1.09, -38.55) * mm, "end": v(1.14, -38.63) * mm});
            skLineSegment(sketch, "E6015", {"start": v(1.14, -38.63) * mm, "end": v(1.18, -38.66) * mm});
            skLineSegment(sketch, "E6016", {"start": v(1.18, -38.66) * mm, "end": v(1.21, -38.68) * mm});
            skLineSegment(sketch, "E6017", {"start": v(1.21, -38.68) * mm, "end": v(1.25, -38.7) * mm});
            skLineSegment(sketch, "E6018", {"start": v(1.25, -38.7) * mm, "end": v(1.3, -38.7) * mm});
            skLineSegment(sketch, "E6019", {"start": v(10.02, -12.86) * mm, "end": v(10.24, -12.7) * mm});
            skLineSegment(sketch, "E6020", {"start": v(10.24, -12.7) * mm, "end": v(10.55, -12.44) * mm});
            skLineSegment(sketch, "E6021", {"start": v(10.55, -12.44) * mm, "end": v(11.28, -11.81) * mm});
            skLineSegment(sketch, "E6022", {"start": v(11.28, -11.81) * mm, "end": v(12.17, -11.04) * mm});
            skLineSegment(sketch, "E6023", {"start": v(12.17, -11.04) * mm, "end": v(12.66, -10.44) * mm});
            skLineSegment(sketch, "E6024", {"start": v(12.66, -10.44) * mm, "end": v(12.86, -10.18) * mm});
            skLineSegment(sketch, "E6025", {"start": v(12.86, -10.18) * mm, "end": v(13.04, -9.93) * mm});
            skLineSegment(sketch, "E6026", {"start": v(13.04, -9.93) * mm, "end": v(13.2, -9.69) * mm});
            skLineSegment(sketch, "E6027", {"start": v(13.2, -9.69) * mm, "end": v(13.33, -9.44) * mm});
            skLineSegment(sketch, "E6028", {"start": v(13.33, -9.44) * mm, "end": v(13.45, -9.2) * mm});
            skLineSegment(sketch, "E6029", {"start": v(13.45, -9.2) * mm, "end": v(13.56, -8.97) * mm});
            skLineSegment(sketch, "E6030", {"start": v(13.56, -8.97) * mm, "end": v(13.64, -8.73) * mm});
            skLineSegment(sketch, "E6031", {"start": v(13.64, -8.73) * mm, "end": v(13.71, -8.5) * mm});
            skLineSegment(sketch, "E6032", {"start": v(13.71, -8.5) * mm, "end": v(13.82, -8.07) * mm});
            skLineSegment(sketch, "E6033", {"start": v(13.82, -8.07) * mm, "end": v(13.7, -7.25) * mm});
            skLineSegment(sketch, "E6034", {"start": v(13.7, -7.25) * mm, "end": v(13.52, -7.15) * mm});
            skLineSegment(sketch, "E6035", {"start": v(13.52, -7.15) * mm, "end": v(13.63, -6.98) * mm});
            skLineSegment(sketch, "E6036", {"start": v(13.63, -6.98) * mm, "end": v(13.45, -6.98) * mm});
            skLineSegment(sketch, "E6037", {"start": v(13.45, -6.98) * mm, "end": v(13.06, -8.2) * mm});
            skLineSegment(sketch, "E6038", {"start": v(13.06, -8.2) * mm, "end": v(12.24, -9.71) * mm});
            skLineSegment(sketch, "E6039", {"start": v(12.24, -9.71) * mm, "end": v(11.57, -10.59) * mm});
            skLineSegment(sketch, "E6040", {"start": v(11.57, -10.59) * mm, "end": v(11.26, -10.99) * mm});
            skLineSegment(sketch, "E6041", {"start": v(11.26, -10.99) * mm, "end": v(10.9, -11.43) * mm});
            skLineSegment(sketch, "E6042", {"start": v(10.9, -11.43) * mm, "end": v(10.55, -11.86) * mm});
            skLineSegment(sketch, "E6043", {"start": v(10.55, -11.86) * mm, "end": v(10.23, -12.23) * mm});
            skLineSegment(sketch, "E6044", {"start": v(10.23, -12.23) * mm, "end": v(9.55, -13) * mm});
            skLineSegment(sketch, "E6045", {"start": v(9.55, -13) * mm, "end": v(9.64, -13.14) * mm});
            skLineSegment(sketch, "E6046", {"start": v(9.64, -13.14) * mm, "end": v(10.02, -12.86) * mm});
            skLineSegment(sketch, "E6047", {"start": v(33.82, -23.1) * mm, "end": v(33.86, -23.09) * mm});
            skLineSegment(sketch, "E6048", {"start": v(33.86, -23.09) * mm, "end": v(33.95, -23.02) * mm});
            skLineSegment(sketch, "E6049", {"start": v(33.95, -23.02) * mm, "end": v(34.05, -22.93) * mm});
            skLineSegment(sketch, "E6050", {"start": v(34.05, -22.93) * mm, "end": v(34.17, -22.81) * mm});
            skLineSegment(sketch, "E6051", {"start": v(34.17, -22.81) * mm, "end": v(34.46, -22.51) * mm});
            skLineSegment(sketch, "E6052", {"start": v(34.46, -22.51) * mm, "end": v(34.75, -21.66) * mm});
            skLineSegment(sketch, "E6053", {"start": v(34.75, -21.66) * mm, "end": v(34.55, -20.52) * mm});
            skLineSegment(sketch, "E6054", {"start": v(34.55, -20.52) * mm, "end": v(34.36, -20.11) * mm});
            skLineSegment(sketch, "E6055", {"start": v(34.36, -20.11) * mm, "end": v(34.24, -19.9) * mm});
            skLineSegment(sketch, "E6056", {"start": v(34.24, -19.9) * mm, "end": v(34.07, -19.6) * mm});
            skLineSegment(sketch, "E6057", {"start": v(34.07, -19.6) * mm, "end": v(33.87, -19.28) * mm});
            skLineSegment(sketch, "E6058", {"start": v(33.87, -19.28) * mm, "end": v(33.67, -18.95) * mm});
            skLineSegment(sketch, "E6059", {"start": v(33.67, -18.95) * mm, "end": v(33.17, -18.18) * mm});
            skLineSegment(sketch, "E6060", {"start": v(33.17, -18.18) * mm, "end": v(32.9, -17.36) * mm});
            skLineSegment(sketch, "E6061", {"start": v(32.9, -17.36) * mm, "end": v(32.59, -17.72) * mm});
            skLineSegment(sketch, "E6062", {"start": v(32.59, -17.72) * mm, "end": v(32.45, -17.88) * mm});
            skLineSegment(sketch, "E6063", {"start": v(32.45, -17.88) * mm, "end": v(32.3, -18.08) * mm});
            skLineSegment(sketch, "E6064", {"start": v(32.3, -18.08) * mm, "end": v(32.17, -18.28) * mm});
            skLineSegment(sketch, "E6065", {"start": v(32.17, -18.28) * mm, "end": v(32.05, -18.46) * mm});
            skLineSegment(sketch, "E6066", {"start": v(32.05, -18.46) * mm, "end": v(31.82, -18.85) * mm});
            skLineSegment(sketch, "E6067", {"start": v(31.82, -18.85) * mm, "end": v(31.44, -20.35) * mm});
            skLineSegment(sketch, "E6068", {"start": v(31.44, -20.35) * mm, "end": v(31.64, -21.74) * mm});
            skLineSegment(sketch, "E6069", {"start": v(31.64, -21.74) * mm, "end": v(31.86, -22.18) * mm});
            skLineSegment(sketch, "E6070", {"start": v(31.86, -22.18) * mm, "end": v(31.96, -22.36) * mm});
            skLineSegment(sketch, "E6071", {"start": v(31.96, -22.36) * mm, "end": v(32.07, -22.53) * mm});
            skLineSegment(sketch, "E6072", {"start": v(32.07, -22.53) * mm, "end": v(32.18, -22.68) * mm});
            skLineSegment(sketch, "E6073", {"start": v(32.18, -22.68) * mm, "end": v(32.27, -22.78) * mm});
            skLineSegment(sketch, "E6074", {"start": v(32.27, -22.78) * mm, "end": v(32.45, -22.94) * mm});
            skLineSegment(sketch, "E6075", {"start": v(32.45, -22.94) * mm, "end": v(32.35, -21.61) * mm});
            skLineSegment(sketch, "E6076", {"start": v(32.35, -21.61) * mm, "end": v(32.56, -20.62) * mm});
            skLineSegment(sketch, "E6077", {"start": v(32.56, -20.62) * mm, "end": v(32.9, -20.1) * mm});
            skLineSegment(sketch, "E6078", {"start": v(32.9, -20.1) * mm, "end": v(33.13, -20.54) * mm});
            skLineSegment(sketch, "E6079", {"start": v(33.13, -20.54) * mm, "end": v(33.23, -20.76) * mm});
            skLineSegment(sketch, "E6080", {"start": v(33.23, -20.76) * mm, "end": v(33.33, -20.99) * mm});
            skLineSegment(sketch, "E6081", {"start": v(33.33, -20.99) * mm, "end": v(33.41, -21.23) * mm});
            skLineSegment(sketch, "E6082", {"start": v(33.41, -21.23) * mm, "end": v(33.49, -21.48) * mm});
            skLineSegment(sketch, "E6083", {"start": v(33.49, -21.48) * mm, "end": v(33.56, -21.74) * mm});
            skLineSegment(sketch, "E6084", {"start": v(33.56, -21.74) * mm, "end": v(33.61, -22) * mm});
            skLineSegment(sketch, "E6085", {"start": v(33.61, -22) * mm, "end": v(33.66, -22.27) * mm});
            skLineSegment(sketch, "E6086", {"start": v(33.66, -22.27) * mm, "end": v(33.7, -22.54) * mm});
            skLineSegment(sketch, "E6087", {"start": v(33.7, -22.54) * mm, "end": v(33.75, -23.1) * mm});
            skLineSegment(sketch, "E6088", {"start": v(33.75, -23.1) * mm, "end": v(33.82, -23.1) * mm});
            skLineSegment(sketch, "E6089", {"start": v(36.94, -20.61) * mm, "end": v(37, -20.41) * mm});
            skLineSegment(sketch, "E6090", {"start": v(37, -20.41) * mm, "end": v(37.06, -20.14) * mm});
            skLineSegment(sketch, "E6091", {"start": v(37.06, -20.14) * mm, "end": v(37.12, -19.82) * mm});
            skLineSegment(sketch, "E6092", {"start": v(37.12, -19.82) * mm, "end": v(37.18, -19.5) * mm});
            skLineSegment(sketch, "E6093", {"start": v(37.18, -19.5) * mm, "end": v(37.3, -18.73) * mm});
            skLineSegment(sketch, "E6094", {"start": v(37.3, -18.73) * mm, "end": v(37.18, -16.37) * mm});
            skLineSegment(sketch, "E6095", {"start": v(37.18, -16.37) * mm, "end": v(37.03, -16.22) * mm});
            skLineSegment(sketch, "E6096", {"start": v(37.03, -16.22) * mm, "end": v(36.67, -16.72) * mm});
            skLineSegment(sketch, "E6097", {"start": v(36.67, -16.72) * mm, "end": v(36.4, -17.07) * mm});
            skLineSegment(sketch, "E6098", {"start": v(36.4, -17.07) * mm, "end": v(36.31, -17.18) * mm});
            skLineSegment(sketch, "E6099", {"start": v(36.31, -17.18) * mm, "end": v(36.27, -17.22) * mm});
            skLineSegment(sketch, "E6100", {"start": v(36.27, -17.22) * mm, "end": v(36.25, -17.2) * mm});
            skLineSegment(sketch, "E6101", {"start": v(36.25, -17.2) * mm, "end": v(36.24, -17.18) * mm});
            skLineSegment(sketch, "E6102", {"start": v(36.24, -17.18) * mm, "end": v(36.2, -17.08) * mm});
            skLineSegment(sketch, "E6103", {"start": v(36.2, -17.08) * mm, "end": v(36.15, -16.93) * mm});
            skLineSegment(sketch, "E6104", {"start": v(36.15, -16.93) * mm, "end": v(36.1, -16.74) * mm});
            skLineSegment(sketch, "E6105", {"start": v(36.1, -16.74) * mm, "end": v(35.9, -16) * mm});
            skLineSegment(sketch, "E6106", {"start": v(35.9, -16) * mm, "end": v(35.7, -15.28) * mm});
            skLineSegment(sketch, "E6107", {"start": v(35.7, -15.28) * mm, "end": v(35.48, -14.58) * mm});
            skLineSegment(sketch, "E6108", {"start": v(35.48, -14.58) * mm, "end": v(35.24, -13.88) * mm});
            skLineSegment(sketch, "E6109", {"start": v(35.24, -13.88) * mm, "end": v(34.97, -13.17) * mm});
            skLineSegment(sketch, "E6110", {"start": v(34.97, -13.17) * mm, "end": v(34.66, -12.42) * mm});
            skLineSegment(sketch, "E6111", {"start": v(34.66, -12.42) * mm, "end": v(34.31, -11.63) * mm});
            skLineSegment(sketch, "E6112", {"start": v(34.31, -11.63) * mm, "end": v(33.92, -10.78) * mm});
            skLineSegment(sketch, "E6113", {"start": v(33.92, -10.78) * mm, "end": v(33.22, -9.29) * mm});
            skLineSegment(sketch, "E6114", {"start": v(33.22, -9.29) * mm, "end": v(32.61, -7.68) * mm});
            skLineSegment(sketch, "E6115", {"start": v(32.61, -7.68) * mm, "end": v(32.54, -7.85) * mm});
            skLineSegment(sketch, "E6116", {"start": v(32.54, -7.85) * mm, "end": v(32.5, -8) * mm});
            skLineSegment(sketch, "E6117", {"start": v(32.5, -8) * mm, "end": v(32.44, -8.3) * mm});
            skLineSegment(sketch, "E6118", {"start": v(32.44, -8.3) * mm, "end": v(32.29, -9.12) * mm});
            skLineSegment(sketch, "E6119", {"start": v(32.29, -9.12) * mm, "end": v(32.1, -10.23) * mm});
            skLineSegment(sketch, "E6120", {"start": v(32.1, -10.23) * mm, "end": v(31.48, -12.38) * mm});
            skLineSegment(sketch, "E6121", {"start": v(31.48, -12.38) * mm, "end": v(31.1, -13.23) * mm});
            skLineSegment(sketch, "E6122", {"start": v(31.1, -13.23) * mm, "end": v(30.72, -14.12) * mm});
            skLineSegment(sketch, "E6123", {"start": v(30.72, -14.12) * mm, "end": v(30.33, -15.05) * mm});
            skLineSegment(sketch, "E6124", {"start": v(30.33, -15.05) * mm, "end": v(29.93, -16) * mm});
            skLineSegment(sketch, "E6125", {"start": v(29.93, -16) * mm, "end": v(29.45, -17.8) * mm});
            skLineSegment(sketch, "E6126", {"start": v(29.45, -17.8) * mm, "end": v(29.44, -19.9) * mm});
            skLineSegment(sketch, "E6127", {"start": v(29.44, -19.9) * mm, "end": v(29.65, -20.55) * mm});
            skLineSegment(sketch, "E6128", {"start": v(29.65, -20.55) * mm, "end": v(29.74, -20.81) * mm});
            skLineSegment(sketch, "E6129", {"start": v(29.74, -20.81) * mm, "end": v(29.83, -21.03) * mm});
            skLineSegment(sketch, "E6130", {"start": v(29.83, -21.03) * mm, "end": v(29.9, -21.2) * mm});
            skLineSegment(sketch, "E6131", {"start": v(29.9, -21.2) * mm, "end": v(29.93, -21.24) * mm});
            skLineSegment(sketch, "E6132", {"start": v(29.93, -21.24) * mm, "end": v(29.95, -21.27) * mm});
            skLineSegment(sketch, "E6133", {"start": v(29.95, -21.27) * mm, "end": v(30.04, -21.32) * mm});
            skLineSegment(sketch, "E6134", {"start": v(30.04, -21.32) * mm, "end": v(29.96, -19.94) * mm});
            skLineSegment(sketch, "E6135", {"start": v(29.96, -19.94) * mm, "end": v(30.09, -18.26) * mm});
            skLineSegment(sketch, "E6136", {"start": v(30.09, -18.26) * mm, "end": v(30.25, -17.63) * mm});
            skLineSegment(sketch, "E6137", {"start": v(30.25, -17.63) * mm, "end": v(30.33, -17.32) * mm});
            skLineSegment(sketch, "E6138", {"start": v(30.33, -17.32) * mm, "end": v(30.46, -16.95) * mm});
            skLineSegment(sketch, "E6139", {"start": v(30.46, -16.95) * mm, "end": v(30.6, -16.56) * mm});
            skLineSegment(sketch, "E6140", {"start": v(30.6, -16.56) * mm, "end": v(30.74, -16.21) * mm});
            skLineSegment(sketch, "E6141", {"start": v(30.74, -16.21) * mm, "end": v(31.08, -15.43) * mm});
            skLineSegment(sketch, "E6142", {"start": v(31.08, -15.43) * mm, "end": v(32.21, -13.59) * mm});
            skLineSegment(sketch, "E6143", {"start": v(32.21, -13.59) * mm, "end": v(32.4, -13.12) * mm});
            skLineSegment(sketch, "E6144", {"start": v(32.4, -13.12) * mm, "end": v(32.48, -12.88) * mm});
            skLineSegment(sketch, "E6145", {"start": v(32.48, -12.88) * mm, "end": v(32.57, -12.6) * mm});
            skLineSegment(sketch, "E6146", {"start": v(32.57, -12.6) * mm, "end": v(32.66, -12.3) * mm});
            skLineSegment(sketch, "E6147", {"start": v(32.66, -12.3) * mm, "end": v(32.73, -12) * mm});
            skLineSegment(sketch, "E6148", {"start": v(32.73, -12) * mm, "end": v(32.89, -11.37) * mm});
            skLineSegment(sketch, "E6149", {"start": v(32.89, -11.37) * mm, "end": v(33.06, -11.37) * mm});
            skLineSegment(sketch, "E6150", {"start": v(33.06, -11.37) * mm, "end": v(33.92, -13.1) * mm});
            skLineSegment(sketch, "E6151", {"start": v(33.92, -13.1) * mm, "end": v(34.29, -14.81) * mm});
            skLineSegment(sketch, "E6152", {"start": v(34.29, -14.81) * mm, "end": v(34.46, -15.09) * mm});
            skLineSegment(sketch, "E6153", {"start": v(34.46, -15.09) * mm, "end": v(34.56, -15.28) * mm});
            skLineSegment(sketch, "E6154", {"start": v(34.56, -15.28) * mm, "end": v(34.71, -15.6) * mm});
            skLineSegment(sketch, "E6155", {"start": v(34.71, -15.6) * mm, "end": v(34.9, -16) * mm});
            skLineSegment(sketch, "E6156", {"start": v(34.9, -16) * mm, "end": v(35.08, -16.46) * mm});
            skLineSegment(sketch, "E6157", {"start": v(35.08, -16.46) * mm, "end": v(35.54, -17.55) * mm});
            skLineSegment(sketch, "E6158", {"start": v(35.54, -17.55) * mm, "end": v(36.1, -19.71) * mm});
            skLineSegment(sketch, "E6159", {"start": v(36.1, -19.71) * mm, "end": v(36.2, -21.66) * mm});
            skLineSegment(sketch, "E6160", {"start": v(36.2, -21.66) * mm, "end": v(36.35, -21.75) * mm});
            skLineSegment(sketch, "E6161", {"start": v(36.35, -21.75) * mm, "end": v(36.58, -21.36) * mm});
            skLineSegment(sketch, "E6162", {"start": v(36.58, -21.36) * mm, "end": v(36.68, -21.18) * mm});
            skLineSegment(sketch, "E6163", {"start": v(36.68, -21.18) * mm, "end": v(36.78, -20.98) * mm});
            skLineSegment(sketch, "E6164", {"start": v(36.78, -20.98) * mm, "end": v(36.87, -20.78) * mm});
            skLineSegment(sketch, "E6165", {"start": v(36.87, -20.78) * mm, "end": v(36.94, -20.61) * mm});
            skLineSegment(sketch, "E6166", {"start": v(28.8, -9.79) * mm, "end": v(28.83, -9.77) * mm});
            skLineSegment(sketch, "E6167", {"start": v(28.83, -9.77) * mm, "end": v(28.84, -9.74) * mm});
            skLineSegment(sketch, "E6168", {"start": v(28.84, -9.74) * mm, "end": v(28.83, -9.71) * mm});
            skLineSegment(sketch, "E6169", {"start": v(28.83, -9.71) * mm, "end": v(28.8, -9.7) * mm});
            skLineSegment(sketch, "E6170", {"start": v(28.8, -9.7) * mm, "end": v(28.76, -9.71) * mm});
            skLineSegment(sketch, "E6171", {"start": v(28.76, -9.71) * mm, "end": v(28.75, -9.74) * mm});
            skLineSegment(sketch, "E6172", {"start": v(28.75, -9.74) * mm, "end": v(28.76, -9.77) * mm});
            skLineSegment(sketch, "E6173", {"start": v(28.76, -9.77) * mm, "end": v(28.8, -9.79) * mm});
            skLineSegment(sketch, "E6174", {"start": v(34.92, -23.55) * mm, "end": v(36.64, -22.63) * mm});
            skLineSegment(sketch, "E6175", {"start": v(36.64, -22.63) * mm, "end": v(37.47, -21.71) * mm});
            skLineSegment(sketch, "E6176", {"start": v(37.47, -21.71) * mm, "end": v(37.72, -21.2) * mm});
            skLineSegment(sketch, "E6177", {"start": v(37.72, -21.2) * mm, "end": v(37.83, -20.98) * mm});
            skLineSegment(sketch, "E6178", {"start": v(37.83, -20.98) * mm, "end": v(37.93, -20.74) * mm});
            skLineSegment(sketch, "E6179", {"start": v(37.93, -20.74) * mm, "end": v(38.02, -20.5) * mm});
            skLineSegment(sketch, "E6180", {"start": v(38.02, -20.5) * mm, "end": v(38.1, -20.24) * mm});
            skLineSegment(sketch, "E6181", {"start": v(38.1, -20.24) * mm, "end": v(38.18, -19.97) * mm});
            skLineSegment(sketch, "E6182", {"start": v(38.18, -19.97) * mm, "end": v(38.25, -19.7) * mm});
            skLineSegment(sketch, "E6183", {"start": v(38.25, -19.7) * mm, "end": v(38.3, -19.4) * mm});
            skLineSegment(sketch, "E6184", {"start": v(38.3, -19.4) * mm, "end": v(38.36, -19.08) * mm});
            skLineSegment(sketch, "E6185", {"start": v(38.36, -19.08) * mm, "end": v(38.46, -18.44) * mm});
            skLineSegment(sketch, "E6186", {"start": v(38.46, -18.44) * mm, "end": v(38.52, -14.55) * mm});
            skLineSegment(sketch, "E6187", {"start": v(38.52, -14.55) * mm, "end": v(38.7, -14.05) * mm});
            skLineSegment(sketch, "E6188", {"start": v(38.7, -14.05) * mm, "end": v(38.84, -13.66) * mm});
            skLineSegment(sketch, "E6189", {"start": v(38.84, -13.66) * mm, "end": v(38.89, -13.52) * mm});
            skLineSegment(sketch, "E6190", {"start": v(38.89, -13.52) * mm, "end": v(38.9, -13.44) * mm});
            skLineSegment(sketch, "E6191", {"start": v(38.9, -13.44) * mm, "end": v(38.9, -13.34) * mm});
            skLineSegment(sketch, "E6192", {"start": v(38.9, -13.34) * mm, "end": v(38.53, -13.42) * mm});
            skLineSegment(sketch, "E6193", {"start": v(38.53, -13.42) * mm, "end": v(38.34, -13.47) * mm});
            skLineSegment(sketch, "E6194", {"start": v(38.34, -13.47) * mm, "end": v(38.16, -13.53) * mm});
            skLineSegment(sketch, "E6195", {"start": v(38.16, -13.53) * mm, "end": v(38, -13.6) * mm});
            skLineSegment(sketch, "E6196", {"start": v(38, -13.6) * mm, "end": v(37.84, -13.68) * mm});
            skLineSegment(sketch, "E6197", {"start": v(37.84, -13.68) * mm, "end": v(37.68, -13.78) * mm});
            skLineSegment(sketch, "E6198", {"start": v(37.68, -13.78) * mm, "end": v(37.52, -13.9) * mm});
            skLineSegment(sketch, "E6199", {"start": v(37.52, -13.9) * mm, "end": v(37.35, -14.04) * mm});
            skLineSegment(sketch, "E6200", {"start": v(37.35, -14.04) * mm, "end": v(37.17, -14.2) * mm});
            skLineSegment(sketch, "E6201", {"start": v(37.17, -14.2) * mm, "end": v(36.74, -14.6) * mm});
            skLineSegment(sketch, "E6202", {"start": v(36.74, -14.6) * mm, "end": v(36.68, -14.17) * mm});
            skLineSegment(sketch, "E6203", {"start": v(36.68, -14.17) * mm, "end": v(36.63, -13.83) * mm});
            skLineSegment(sketch, "E6204", {"start": v(36.63, -13.83) * mm, "end": v(36.57, -13.45) * mm});
            skLineSegment(sketch, "E6205", {"start": v(36.57, -13.45) * mm, "end": v(36.49, -13.05) * mm});
            skLineSegment(sketch, "E6206", {"start": v(36.49, -13.05) * mm, "end": v(36.4, -12.64) * mm});
            skLineSegment(sketch, "E6207", {"start": v(36.4, -12.64) * mm, "end": v(36.3, -12.24) * mm});
            skLineSegment(sketch, "E6208", {"start": v(36.3, -12.24) * mm, "end": v(36.2, -11.84) * mm});
            skLineSegment(sketch, "E6209", {"start": v(36.2, -11.84) * mm, "end": v(36.1, -11.47) * mm});
            skLineSegment(sketch, "E6210", {"start": v(36.1, -11.47) * mm, "end": v(36, -11.13) * mm});
            skLineSegment(sketch, "E6211", {"start": v(36, -11.13) * mm, "end": v(35.71, -10.29) * mm});
            skLineSegment(sketch, "E6212", {"start": v(35.71, -10.29) * mm, "end": v(33.92, -6.57) * mm});
            skLineSegment(sketch, "E6213", {"start": v(33.92, -6.57) * mm, "end": v(33.74, -5.92) * mm});
            skLineSegment(sketch, "E6214", {"start": v(33.74, -5.92) * mm, "end": v(33.67, -5.6) * mm});
            skLineSegment(sketch, "E6215", {"start": v(33.67, -5.6) * mm, "end": v(33.59, -5.2) * mm});
            skLineSegment(sketch, "E6216", {"start": v(33.59, -5.2) * mm, "end": v(33.51, -4.79) * mm});
            skLineSegment(sketch, "E6217", {"start": v(33.51, -4.79) * mm, "end": v(33.45, -4.4) * mm});
            skLineSegment(sketch, "E6218", {"start": v(33.45, -4.4) * mm, "end": v(33.34, -3.53) * mm});
            skLineSegment(sketch, "E6219", {"start": v(33.34, -3.53) * mm, "end": v(33.26, -3.53) * mm});
            skLineSegment(sketch, "E6220", {"start": v(33.26, -3.53) * mm, "end": v(33.23, -3.54) * mm});
            skLineSegment(sketch, "E6221", {"start": v(33.23, -3.54) * mm, "end": v(33.19, -3.57) * mm});
            skLineSegment(sketch, "E6222", {"start": v(33.19, -3.57) * mm, "end": v(33.08, -3.65) * mm});
            skLineSegment(sketch, "E6223", {"start": v(33.08, -3.65) * mm, "end": v(32.95, -3.78) * mm});
            skLineSegment(sketch, "E6224", {"start": v(32.95, -3.78) * mm, "end": v(32.8, -3.96) * mm});
            skLineSegment(sketch, "E6225", {"start": v(32.8, -3.96) * mm, "end": v(32.64, -4.15) * mm});
            skLineSegment(sketch, "E6226", {"start": v(32.64, -4.15) * mm, "end": v(32.48, -4.37) * mm});
            skLineSegment(sketch, "E6227", {"start": v(32.48, -4.37) * mm, "end": v(32.32, -4.6) * mm});
            skLineSegment(sketch, "E6228", {"start": v(32.32, -4.6) * mm, "end": v(32.17, -4.83) * mm});
            skLineSegment(sketch, "E6229", {"start": v(32.17, -4.83) * mm, "end": v(31.83, -5.39) * mm});
            skLineSegment(sketch, "E6230", {"start": v(31.83, -5.39) * mm, "end": v(31.6, -6.08) * mm});
            skLineSegment(sketch, "E6231", {"start": v(31.6, -6.08) * mm, "end": v(31.51, -6.4) * mm});
            skLineSegment(sketch, "E6232", {"start": v(31.51, -6.4) * mm, "end": v(31.42, -6.76) * mm});
            skLineSegment(sketch, "E6233", {"start": v(31.42, -6.76) * mm, "end": v(31.34, -7.11) * mm});
            skLineSegment(sketch, "E6234", {"start": v(31.34, -7.11) * mm, "end": v(31.26, -7.48) * mm});
            skLineSegment(sketch, "E6235", {"start": v(31.26, -7.48) * mm, "end": v(31.2, -7.84) * mm});
            skLineSegment(sketch, "E6236", {"start": v(31.2, -7.84) * mm, "end": v(31.14, -8.21) * mm});
            skLineSegment(sketch, "E6237", {"start": v(31.14, -8.21) * mm, "end": v(31.1, -8.57) * mm});
            skLineSegment(sketch, "E6238", {"start": v(31.1, -8.57) * mm, "end": v(31.06, -8.93) * mm});
            skLineSegment(sketch, "E6239", {"start": v(31.06, -8.93) * mm, "end": v(31.01, -9.52) * mm});
            skLineSegment(sketch, "E6240", {"start": v(31.01, -9.52) * mm, "end": v(30.96, -9.94) * mm});
            skLineSegment(sketch, "E6241", {"start": v(30.96, -9.94) * mm, "end": v(30.92, -10.22) * mm});
            skLineSegment(sketch, "E6242", {"start": v(30.92, -10.22) * mm, "end": v(30.1, -9.77) * mm});
            skLineSegment(sketch, "E6243", {"start": v(30.1, -9.77) * mm, "end": v(29.79, -9.74) * mm});
            skLineSegment(sketch, "E6244", {"start": v(29.79, -9.74) * mm, "end": v(29.57, -9.73) * mm});
            skLineSegment(sketch, "E6245", {"start": v(29.57, -9.73) * mm, "end": v(29.5, -9.73) * mm});
            skLineSegment(sketch, "E6246", {"start": v(29.5, -9.73) * mm, "end": v(29.48, -9.73) * mm});
            skLineSegment(sketch, "E6247", {"start": v(29.48, -9.73) * mm, "end": v(29.66, -10.29) * mm});
            skLineSegment(sketch, "E6248", {"start": v(29.66, -10.29) * mm, "end": v(29.84, -10.82) * mm});
            skLineSegment(sketch, "E6249", {"start": v(29.84, -10.82) * mm, "end": v(29.95, -12) * mm});
            skLineSegment(sketch, "E6250", {"start": v(29.95, -12) * mm, "end": v(29.8, -12.66) * mm});
            skLineSegment(sketch, "E6251", {"start": v(29.8, -12.66) * mm, "end": v(29.72, -13) * mm});
            skLineSegment(sketch, "E6252", {"start": v(29.72, -13) * mm, "end": v(29.58, -13.49) * mm});
            skLineSegment(sketch, "E6253", {"start": v(29.58, -13.49) * mm, "end": v(29.4, -14.03) * mm});
            skLineSegment(sketch, "E6254", {"start": v(29.4, -14.03) * mm, "end": v(29.22, -14.58) * mm});
            skLineSegment(sketch, "E6255", {"start": v(29.22, -14.58) * mm, "end": v(28.76, -15.84) * mm});
            skLineSegment(sketch, "E6256", {"start": v(28.76, -15.84) * mm, "end": v(28.63, -16.5) * mm});
            skLineSegment(sketch, "E6257", {"start": v(28.63, -16.5) * mm, "end": v(28.57, -16.82) * mm});
            skLineSegment(sketch, "E6258", {"start": v(28.57, -16.82) * mm, "end": v(28.51, -17.2) * mm});
            skLineSegment(sketch, "E6259", {"start": v(28.51, -17.2) * mm, "end": v(28.47, -17.56) * mm});
            skLineSegment(sketch, "E6260", {"start": v(28.47, -17.56) * mm, "end": v(28.43, -17.9) * mm});
            skLineSegment(sketch, "E6261", {"start": v(28.43, -17.9) * mm, "end": v(28.38, -18.62) * mm});
            skLineSegment(sketch, "E6262", {"start": v(28.38, -18.62) * mm, "end": v(28.66, -20.07) * mm});
            skLineSegment(sketch, "E6263", {"start": v(28.66, -20.07) * mm, "end": v(29.5, -21.78) * mm});
            skLineSegment(sketch, "E6264", {"start": v(29.5, -21.78) * mm, "end": v(31.08, -23.55) * mm});
            skLineSegment(sketch, "E6265", {"start": v(31.08, -23.55) * mm, "end": v(32.93, -23.55) * mm});
            skLineSegment(sketch, "E6266", {"start": v(32.93, -23.55) * mm, "end": v(34.92, -23.55) * mm});
            skLineSegment(sketch, "E6267", {"start": v(34.63, -23.26) * mm, "end": v(31.33, -23.3) * mm});
            skLineSegment(sketch, "E6268", {"start": v(31.33, -23.3) * mm, "end": v(31.08, -22.65) * mm});
            skLineSegment(sketch, "E6269", {"start": v(31.08, -22.65) * mm, "end": v(30.97, -22.35) * mm});
            skLineSegment(sketch, "E6270", {"start": v(30.97, -22.35) * mm, "end": v(30.87, -22.04) * mm});
            skLineSegment(sketch, "E6271", {"start": v(30.87, -22.04) * mm, "end": v(30.79, -21.74) * mm});
            skLineSegment(sketch, "E6272", {"start": v(30.79, -21.74) * mm, "end": v(30.73, -21.49) * mm});
            skLineSegment(sketch, "E6273", {"start": v(30.73, -21.49) * mm, "end": v(30.63, -20.98) * mm});
            skLineSegment(sketch, "E6274", {"start": v(30.63, -20.98) * mm, "end": v(30.72, -19.08) * mm});
            skLineSegment(sketch, "E6275", {"start": v(30.72, -19.08) * mm, "end": v(31.26, -17.7) * mm});
            skLineSegment(sketch, "E6276", {"start": v(31.26, -17.7) * mm, "end": v(32.4, -15.81) * mm});
            skLineSegment(sketch, "E6277", {"start": v(32.4, -15.81) * mm, "end": v(32.89, -15.2) * mm});
            skLineSegment(sketch, "E6278", {"start": v(32.89, -15.2) * mm, "end": v(33.38, -16.54) * mm});
            skLineSegment(sketch, "E6279", {"start": v(33.38, -16.54) * mm, "end": v(34.91, -19.26) * mm});
            skLineSegment(sketch, "E6280", {"start": v(34.91, -19.26) * mm, "end": v(35.48, -20.6) * mm});
            skLineSegment(sketch, "E6281", {"start": v(35.48, -20.6) * mm, "end": v(35.5, -21.98) * mm});
            skLineSegment(sketch, "E6282", {"start": v(35.5, -21.98) * mm, "end": v(35.15, -23.13) * mm});
            skLineSegment(sketch, "E6283", {"start": v(35.15, -23.13) * mm, "end": v(34.63, -23.26) * mm});
            skLineSegment(sketch, "E6284", {"start": v(-33.82, -23.13) * mm, "end": v(-33.86, -23.1) * mm});
            skLineSegment(sketch, "E6285", {"start": v(-33.86, -23.1) * mm, "end": v(-33.95, -23.04) * mm});
            skLineSegment(sketch, "E6286", {"start": v(-33.95, -23.04) * mm, "end": v(-34.05, -22.95) * mm});
            skLineSegment(sketch, "E6287", {"start": v(-34.05, -22.95) * mm, "end": v(-34.17, -22.83) * mm});
            skLineSegment(sketch, "E6288", {"start": v(-34.17, -22.83) * mm, "end": v(-34.46, -22.54) * mm});
            skLineSegment(sketch, "E6289", {"start": v(-34.46, -22.54) * mm, "end": v(-34.75, -21.68) * mm});
            skLineSegment(sketch, "E6290", {"start": v(-34.75, -21.68) * mm, "end": v(-34.55, -20.54) * mm});
            skLineSegment(sketch, "E6291", {"start": v(-34.55, -20.54) * mm, "end": v(-34.36, -20.14) * mm});
            skLineSegment(sketch, "E6292", {"start": v(-34.36, -20.14) * mm, "end": v(-34.24, -19.92) * mm});
            skLineSegment(sketch, "E6293", {"start": v(-34.24, -19.92) * mm, "end": v(-34.07, -19.63) * mm});
            skLineSegment(sketch, "E6294", {"start": v(-34.07, -19.63) * mm, "end": v(-33.87, -19.3) * mm});
            skLineSegment(sketch, "E6295", {"start": v(-33.87, -19.3) * mm, "end": v(-33.67, -18.97) * mm});
            skLineSegment(sketch, "E6296", {"start": v(-33.67, -18.97) * mm, "end": v(-33.17, -18.2) * mm});
            skLineSegment(sketch, "E6297", {"start": v(-33.17, -18.2) * mm, "end": v(-32.9, -17.39) * mm});
            skLineSegment(sketch, "E6298", {"start": v(-32.9, -17.39) * mm, "end": v(-32.59, -17.74) * mm});
            skLineSegment(sketch, "E6299", {"start": v(-32.59, -17.74) * mm, "end": v(-32.45, -17.9) * mm});
            skLineSegment(sketch, "E6300", {"start": v(-32.45, -17.9) * mm, "end": v(-32.3, -18.1) * mm});
            skLineSegment(sketch, "E6301", {"start": v(-32.3, -18.1) * mm, "end": v(-32.17, -18.3) * mm});
            skLineSegment(sketch, "E6302", {"start": v(-32.17, -18.3) * mm, "end": v(-32.05, -18.48) * mm});
            skLineSegment(sketch, "E6303", {"start": v(-32.05, -18.48) * mm, "end": v(-31.82, -18.88) * mm});
            skLineSegment(sketch, "E6304", {"start": v(-31.82, -18.88) * mm, "end": v(-31.44, -20.37) * mm});
            skLineSegment(sketch, "E6305", {"start": v(-31.44, -20.37) * mm, "end": v(-31.64, -21.76) * mm});
            skLineSegment(sketch, "E6306", {"start": v(-31.64, -21.76) * mm, "end": v(-31.86, -22.2) * mm});
            skLineSegment(sketch, "E6307", {"start": v(-31.86, -22.2) * mm, "end": v(-31.96, -22.38) * mm});
            skLineSegment(sketch, "E6308", {"start": v(-31.96, -22.38) * mm, "end": v(-32.07, -22.55) * mm});
            skLineSegment(sketch, "E6309", {"start": v(-32.07, -22.55) * mm, "end": v(-32.18, -22.7) * mm});
            skLineSegment(sketch, "E6310", {"start": v(-32.18, -22.7) * mm, "end": v(-32.27, -22.8) * mm});
            skLineSegment(sketch, "E6311", {"start": v(-32.27, -22.8) * mm, "end": v(-32.45, -22.97) * mm});
            skLineSegment(sketch, "E6312", {"start": v(-32.45, -22.97) * mm, "end": v(-32.35, -21.64) * mm});
            skLineSegment(sketch, "E6313", {"start": v(-32.35, -21.64) * mm, "end": v(-32.56, -20.64) * mm});
            skLineSegment(sketch, "E6314", {"start": v(-32.56, -20.64) * mm, "end": v(-32.9, -20.12) * mm});
            skLineSegment(sketch, "E6315", {"start": v(-32.9, -20.12) * mm, "end": v(-33.13, -20.56) * mm});
            skLineSegment(sketch, "E6316", {"start": v(-33.13, -20.56) * mm, "end": v(-33.23, -20.78) * mm});
            skLineSegment(sketch, "E6317", {"start": v(-33.23, -20.78) * mm, "end": v(-33.33, -21.01) * mm});
            skLineSegment(sketch, "E6318", {"start": v(-33.33, -21.01) * mm, "end": v(-33.41, -21.25) * mm});
            skLineSegment(sketch, "E6319", {"start": v(-33.41, -21.25) * mm, "end": v(-33.49, -21.5) * mm});
            skLineSegment(sketch, "E6320", {"start": v(-33.49, -21.5) * mm, "end": v(-33.56, -21.76) * mm});
            skLineSegment(sketch, "E6321", {"start": v(-33.56, -21.76) * mm, "end": v(-33.61, -22.02) * mm});
            skLineSegment(sketch, "E6322", {"start": v(-33.61, -22.02) * mm, "end": v(-33.66, -22.3) * mm});
            skLineSegment(sketch, "E6323", {"start": v(-33.66, -22.3) * mm, "end": v(-33.7, -22.56) * mm});
            skLineSegment(sketch, "E6324", {"start": v(-33.7, -22.56) * mm, "end": v(-33.75, -23.13) * mm});
            skLineSegment(sketch, "E6325", {"start": v(-33.75, -23.13) * mm, "end": v(-33.82, -23.13) * mm});
            skLineSegment(sketch, "E6326", {"start": v(-36.94, -20.64) * mm, "end": v(-37, -20.44) * mm});
            skLineSegment(sketch, "E6327", {"start": v(-37, -20.44) * mm, "end": v(-37.06, -20.16) * mm});
            skLineSegment(sketch, "E6328", {"start": v(-37.06, -20.16) * mm, "end": v(-37.12, -19.84) * mm});
            skLineSegment(sketch, "E6329", {"start": v(-37.12, -19.84) * mm, "end": v(-37.18, -19.51) * mm});
            skLineSegment(sketch, "E6330", {"start": v(-37.18, -19.51) * mm, "end": v(-37.3, -18.75) * mm});
            skLineSegment(sketch, "E6331", {"start": v(-37.3, -18.75) * mm, "end": v(-37.18, -16.4) * mm});
            skLineSegment(sketch, "E6332", {"start": v(-37.18, -16.4) * mm, "end": v(-37.03, -16.24) * mm});
            skLineSegment(sketch, "E6333", {"start": v(-37.03, -16.24) * mm, "end": v(-36.67, -16.74) * mm});
            skLineSegment(sketch, "E6334", {"start": v(-36.67, -16.74) * mm, "end": v(-36.4, -17.1) * mm});
            skLineSegment(sketch, "E6335", {"start": v(-36.4, -17.1) * mm, "end": v(-36.31, -17.2) * mm});
            skLineSegment(sketch, "E6336", {"start": v(-36.31, -17.2) * mm, "end": v(-36.27, -17.24) * mm});
            skLineSegment(sketch, "E6337", {"start": v(-36.27, -17.24) * mm, "end": v(-36.25, -17.23) * mm});
            skLineSegment(sketch, "E6338", {"start": v(-36.25, -17.23) * mm, "end": v(-36.24, -17.2) * mm});
            skLineSegment(sketch, "E6339", {"start": v(-36.24, -17.2) * mm, "end": v(-36.2, -17.1) * mm});
            skLineSegment(sketch, "E6340", {"start": v(-36.2, -17.1) * mm, "end": v(-36.15, -16.95) * mm});
            skLineSegment(sketch, "E6341", {"start": v(-36.15, -16.95) * mm, "end": v(-36.1, -16.76) * mm});
            skLineSegment(sketch, "E6342", {"start": v(-36.1, -16.76) * mm, "end": v(-35.9, -16.02) * mm});
            skLineSegment(sketch, "E6343", {"start": v(-35.9, -16.02) * mm, "end": v(-35.7, -15.3) * mm});
            skLineSegment(sketch, "E6344", {"start": v(-35.7, -15.3) * mm, "end": v(-35.48, -14.6) * mm});
            skLineSegment(sketch, "E6345", {"start": v(-35.48, -14.6) * mm, "end": v(-35.24, -13.9) * mm});
            skLineSegment(sketch, "E6346", {"start": v(-35.24, -13.9) * mm, "end": v(-34.97, -13.2) * mm});
            skLineSegment(sketch, "E6347", {"start": v(-34.97, -13.2) * mm, "end": v(-34.66, -12.45) * mm});
            skLineSegment(sketch, "E6348", {"start": v(-34.66, -12.45) * mm, "end": v(-34.31, -11.66) * mm});
            skLineSegment(sketch, "E6349", {"start": v(-34.31, -11.66) * mm, "end": v(-33.92, -10.8) * mm});
            skLineSegment(sketch, "E6350", {"start": v(-33.92, -10.8) * mm, "end": v(-33.22, -9.31) * mm});
            skLineSegment(sketch, "E6351", {"start": v(-33.22, -9.31) * mm, "end": v(-32.61, -7.7) * mm});
            skLineSegment(sketch, "E6352", {"start": v(-32.61, -7.7) * mm, "end": v(-32.54, -7.87) * mm});
            skLineSegment(sketch, "E6353", {"start": v(-32.54, -7.87) * mm, "end": v(-32.5, -8.02) * mm});
            skLineSegment(sketch, "E6354", {"start": v(-32.5, -8.02) * mm, "end": v(-32.44, -8.32) * mm});
            skLineSegment(sketch, "E6355", {"start": v(-32.44, -8.32) * mm, "end": v(-32.29, -9.15) * mm});
            skLineSegment(sketch, "E6356", {"start": v(-32.29, -9.15) * mm, "end": v(-32.1, -10.25) * mm});
            skLineSegment(sketch, "E6357", {"start": v(-32.1, -10.25) * mm, "end": v(-31.48, -12.4) * mm});
            skLineSegment(sketch, "E6358", {"start": v(-31.48, -12.4) * mm, "end": v(-31.1, -13.26) * mm});
            skLineSegment(sketch, "E6359", {"start": v(-31.1, -13.26) * mm, "end": v(-30.72, -14.14) * mm});
            skLineSegment(sketch, "E6360", {"start": v(-30.72, -14.14) * mm, "end": v(-30.33, -15.07) * mm});
            skLineSegment(sketch, "E6361", {"start": v(-30.33, -15.07) * mm, "end": v(-29.93, -16.03) * mm});
            skLineSegment(sketch, "E6362", {"start": v(-29.93, -16.03) * mm, "end": v(-29.45, -17.83) * mm});
            skLineSegment(sketch, "E6363", {"start": v(-29.45, -17.83) * mm, "end": v(-29.44, -19.91) * mm});
            skLineSegment(sketch, "E6364", {"start": v(-29.44, -19.91) * mm, "end": v(-29.65, -20.57) * mm});
            skLineSegment(sketch, "E6365", {"start": v(-29.65, -20.57) * mm, "end": v(-29.74, -20.83) * mm});
            skLineSegment(sketch, "E6366", {"start": v(-29.74, -20.83) * mm, "end": v(-29.83, -21.06) * mm});
            skLineSegment(sketch, "E6367", {"start": v(-29.83, -21.06) * mm, "end": v(-29.9, -21.22) * mm});
            skLineSegment(sketch, "E6368", {"start": v(-29.9, -21.22) * mm, "end": v(-29.93, -21.26) * mm});
            skLineSegment(sketch, "E6369", {"start": v(-29.93, -21.26) * mm, "end": v(-29.95, -21.29) * mm});
            skLineSegment(sketch, "E6370", {"start": v(-29.95, -21.29) * mm, "end": v(-30.04, -21.34) * mm});
            skLineSegment(sketch, "E6371", {"start": v(-30.04, -21.34) * mm, "end": v(-29.96, -19.97) * mm});
            skLineSegment(sketch, "E6372", {"start": v(-29.96, -19.97) * mm, "end": v(-30.09, -18.28) * mm});
            skLineSegment(sketch, "E6373", {"start": v(-30.09, -18.28) * mm, "end": v(-30.25, -17.65) * mm});
            skLineSegment(sketch, "E6374", {"start": v(-30.25, -17.65) * mm, "end": v(-30.33, -17.34) * mm});
            skLineSegment(sketch, "E6375", {"start": v(-30.33, -17.34) * mm, "end": v(-30.46, -16.97) * mm});
            skLineSegment(sketch, "E6376", {"start": v(-30.46, -16.97) * mm, "end": v(-30.6, -16.59) * mm});
            skLineSegment(sketch, "E6377", {"start": v(-30.6, -16.59) * mm, "end": v(-30.74, -16.23) * mm});
            skLineSegment(sketch, "E6378", {"start": v(-30.74, -16.23) * mm, "end": v(-31.08, -15.45) * mm});
            skLineSegment(sketch, "E6379", {"start": v(-31.08, -15.45) * mm, "end": v(-32.21, -13.61) * mm});
            skLineSegment(sketch, "E6380", {"start": v(-32.21, -13.61) * mm, "end": v(-32.4, -13.14) * mm});
            skLineSegment(sketch, "E6381", {"start": v(-32.4, -13.14) * mm, "end": v(-32.48, -12.9) * mm});
            skLineSegment(sketch, "E6382", {"start": v(-32.48, -12.9) * mm, "end": v(-32.57, -12.62) * mm});
            skLineSegment(sketch, "E6383", {"start": v(-32.57, -12.62) * mm, "end": v(-32.66, -12.31) * mm});
            skLineSegment(sketch, "E6384", {"start": v(-32.66, -12.31) * mm, "end": v(-32.73, -12.03) * mm});
            skLineSegment(sketch, "E6385", {"start": v(-32.73, -12.03) * mm, "end": v(-32.89, -11.4) * mm});
            skLineSegment(sketch, "E6386", {"start": v(-32.89, -11.4) * mm, "end": v(-33.06, -11.4) * mm});
            skLineSegment(sketch, "E6387", {"start": v(-33.06, -11.4) * mm, "end": v(-33.92, -13.12) * mm});
            skLineSegment(sketch, "E6388", {"start": v(-33.92, -13.12) * mm, "end": v(-34.29, -14.83) * mm});
            skLineSegment(sketch, "E6389", {"start": v(-34.29, -14.83) * mm, "end": v(-34.46, -15.1) * mm});
            skLineSegment(sketch, "E6390", {"start": v(-34.46, -15.1) * mm, "end": v(-34.56, -15.3) * mm});
            skLineSegment(sketch, "E6391", {"start": v(-34.56, -15.3) * mm, "end": v(-34.71, -15.62) * mm});
            skLineSegment(sketch, "E6392", {"start": v(-34.71, -15.62) * mm, "end": v(-34.9, -16.03) * mm});
            skLineSegment(sketch, "E6393", {"start": v(-34.9, -16.03) * mm, "end": v(-35.08, -16.48) * mm});
            skLineSegment(sketch, "E6394", {"start": v(-35.08, -16.48) * mm, "end": v(-35.54, -17.57) * mm});
            skLineSegment(sketch, "E6395", {"start": v(-35.54, -17.57) * mm, "end": v(-36.1, -19.73) * mm});
            skLineSegment(sketch, "E6396", {"start": v(-36.1, -19.73) * mm, "end": v(-36.2, -21.69) * mm});
            skLineSegment(sketch, "E6397", {"start": v(-36.2, -21.69) * mm, "end": v(-36.35, -21.78) * mm});
            skLineSegment(sketch, "E6398", {"start": v(-36.35, -21.78) * mm, "end": v(-36.58, -21.39) * mm});
            skLineSegment(sketch, "E6399", {"start": v(-36.58, -21.39) * mm, "end": v(-36.68, -21.2) * mm});
            skLineSegment(sketch, "E6400", {"start": v(-36.68, -21.2) * mm, "end": v(-36.78, -21) * mm});
            skLineSegment(sketch, "E6401", {"start": v(-36.78, -21) * mm, "end": v(-36.87, -20.8) * mm});
            skLineSegment(sketch, "E6402", {"start": v(-36.87, -20.8) * mm, "end": v(-36.94, -20.64) * mm});
            skLineSegment(sketch, "E6403", {"start": v(-28.8, -9.8) * mm, "end": v(-28.83, -9.8) * mm});
            skLineSegment(sketch, "E6404", {"start": v(-28.83, -9.8) * mm, "end": v(-28.84, -9.76) * mm});
            skLineSegment(sketch, "E6405", {"start": v(-28.84, -9.76) * mm, "end": v(-28.83, -9.73) * mm});
            skLineSegment(sketch, "E6406", {"start": v(-28.83, -9.73) * mm, "end": v(-28.8, -9.72) * mm});
            skLineSegment(sketch, "E6407", {"start": v(-28.8, -9.72) * mm, "end": v(-28.76, -9.73) * mm});
            skLineSegment(sketch, "E6408", {"start": v(-28.76, -9.73) * mm, "end": v(-28.75, -9.76) * mm});
            skLineSegment(sketch, "E6409", {"start": v(-28.75, -9.76) * mm, "end": v(-28.76, -9.8) * mm});
            skLineSegment(sketch, "E6410", {"start": v(-28.76, -9.8) * mm, "end": v(-28.8, -9.8) * mm});
            skLineSegment(sketch, "E6411", {"start": v(-34.92, -23.57) * mm, "end": v(-36.64, -22.65) * mm});
            skLineSegment(sketch, "E6412", {"start": v(-36.64, -22.65) * mm, "end": v(-37.47, -21.73) * mm});
            skLineSegment(sketch, "E6413", {"start": v(-37.47, -21.73) * mm, "end": v(-37.72, -21.23) * mm});
            skLineSegment(sketch, "E6414", {"start": v(-37.72, -21.23) * mm, "end": v(-37.83, -21) * mm});
            skLineSegment(sketch, "E6415", {"start": v(-37.83, -21) * mm, "end": v(-37.93, -20.76) * mm});
            skLineSegment(sketch, "E6416", {"start": v(-37.93, -20.76) * mm, "end": v(-38.02, -20.52) * mm});
            skLineSegment(sketch, "E6417", {"start": v(-38.02, -20.52) * mm, "end": v(-38.1, -20.26) * mm});
            skLineSegment(sketch, "E6418", {"start": v(-38.1, -20.26) * mm, "end": v(-38.18, -20) * mm});
            skLineSegment(sketch, "E6419", {"start": v(-38.18, -20) * mm, "end": v(-38.25, -19.71) * mm});
            skLineSegment(sketch, "E6420", {"start": v(-38.25, -19.71) * mm, "end": v(-38.3, -19.41) * mm});
            skLineSegment(sketch, "E6421", {"start": v(-38.3, -19.41) * mm, "end": v(-38.36, -19.1) * mm});
            skLineSegment(sketch, "E6422", {"start": v(-38.36, -19.1) * mm, "end": v(-38.46, -18.46) * mm});
            skLineSegment(sketch, "E6423", {"start": v(-38.46, -18.46) * mm, "end": v(-38.52, -14.57) * mm});
            skLineSegment(sketch, "E6424", {"start": v(-38.52, -14.57) * mm, "end": v(-38.7, -14.07) * mm});
            skLineSegment(sketch, "E6425", {"start": v(-38.7, -14.07) * mm, "end": v(-38.84, -13.69) * mm});
            skLineSegment(sketch, "E6426", {"start": v(-38.84, -13.69) * mm, "end": v(-38.89, -13.55) * mm});
            skLineSegment(sketch, "E6427", {"start": v(-38.89, -13.55) * mm, "end": v(-38.9, -13.47) * mm});
            skLineSegment(sketch, "E6428", {"start": v(-38.9, -13.47) * mm, "end": v(-38.9, -13.36) * mm});
            skLineSegment(sketch, "E6429", {"start": v(-38.9, -13.36) * mm, "end": v(-38.53, -13.45) * mm});
            skLineSegment(sketch, "E6430", {"start": v(-38.53, -13.45) * mm, "end": v(-38.34, -13.5) * mm});
            skLineSegment(sketch, "E6431", {"start": v(-38.34, -13.5) * mm, "end": v(-38.16, -13.55) * mm});
            skLineSegment(sketch, "E6432", {"start": v(-38.16, -13.55) * mm, "end": v(-38, -13.62) * mm});
            skLineSegment(sketch, "E6433", {"start": v(-38, -13.62) * mm, "end": v(-37.84, -13.7) * mm});
            skLineSegment(sketch, "E6434", {"start": v(-37.84, -13.7) * mm, "end": v(-37.68, -13.8) * mm});
            skLineSegment(sketch, "E6435", {"start": v(-37.68, -13.8) * mm, "end": v(-37.52, -13.92) * mm});
            skLineSegment(sketch, "E6436", {"start": v(-37.52, -13.92) * mm, "end": v(-37.35, -14.06) * mm});
            skLineSegment(sketch, "E6437", {"start": v(-37.35, -14.06) * mm, "end": v(-37.17, -14.22) * mm});
            skLineSegment(sketch, "E6438", {"start": v(-37.17, -14.22) * mm, "end": v(-36.74, -14.63) * mm});
            skLineSegment(sketch, "E6439", {"start": v(-36.74, -14.63) * mm, "end": v(-36.68, -14.19) * mm});
            skLineSegment(sketch, "E6440", {"start": v(-36.68, -14.19) * mm, "end": v(-36.63, -13.85) * mm});
            skLineSegment(sketch, "E6441", {"start": v(-36.63, -13.85) * mm, "end": v(-36.57, -13.47) * mm});
            skLineSegment(sketch, "E6442", {"start": v(-36.57, -13.47) * mm, "end": v(-36.49, -13.07) * mm});
            skLineSegment(sketch, "E6443", {"start": v(-36.49, -13.07) * mm, "end": v(-36.4, -12.67) * mm});
            skLineSegment(sketch, "E6444", {"start": v(-36.4, -12.67) * mm, "end": v(-36.3, -12.26) * mm});
            skLineSegment(sketch, "E6445", {"start": v(-36.3, -12.26) * mm, "end": v(-36.2, -11.86) * mm});
            skLineSegment(sketch, "E6446", {"start": v(-36.2, -11.86) * mm, "end": v(-36.1, -11.49) * mm});
            skLineSegment(sketch, "E6447", {"start": v(-36.1, -11.49) * mm, "end": v(-36, -11.15) * mm});
            skLineSegment(sketch, "E6448", {"start": v(-36, -11.15) * mm, "end": v(-35.71, -10.3) * mm});
            skLineSegment(sketch, "E6449", {"start": v(-35.71, -10.3) * mm, "end": v(-33.92, -6.6) * mm});
            skLineSegment(sketch, "E6450", {"start": v(-33.92, -6.6) * mm, "end": v(-33.74, -5.94) * mm});
            skLineSegment(sketch, "E6451", {"start": v(-33.74, -5.94) * mm, "end": v(-33.67, -5.62) * mm});
            skLineSegment(sketch, "E6452", {"start": v(-33.67, -5.62) * mm, "end": v(-33.59, -5.22) * mm});
            skLineSegment(sketch, "E6453", {"start": v(-33.59, -5.22) * mm, "end": v(-33.51, -4.8) * mm});
            skLineSegment(sketch, "E6454", {"start": v(-33.51, -4.8) * mm, "end": v(-33.45, -4.42) * mm});
            skLineSegment(sketch, "E6455", {"start": v(-33.45, -4.42) * mm, "end": v(-33.34, -3.56) * mm});
            skLineSegment(sketch, "E6456", {"start": v(-33.34, -3.56) * mm, "end": v(-33.26, -3.56) * mm});
            skLineSegment(sketch, "E6457", {"start": v(-33.26, -3.56) * mm, "end": v(-33.23, -3.56) * mm});
            skLineSegment(sketch, "E6458", {"start": v(-33.23, -3.56) * mm, "end": v(-33.19, -3.59) * mm});
            skLineSegment(sketch, "E6459", {"start": v(-33.19, -3.59) * mm, "end": v(-33.08, -3.67) * mm});
            skLineSegment(sketch, "E6460", {"start": v(-33.08, -3.67) * mm, "end": v(-32.95, -3.8) * mm});
            skLineSegment(sketch, "E6461", {"start": v(-32.95, -3.8) * mm, "end": v(-32.8, -3.98) * mm});
            skLineSegment(sketch, "E6462", {"start": v(-32.8, -3.98) * mm, "end": v(-32.64, -4.18) * mm});
            skLineSegment(sketch, "E6463", {"start": v(-32.64, -4.18) * mm, "end": v(-32.48, -4.4) * mm});
            skLineSegment(sketch, "E6464", {"start": v(-32.48, -4.4) * mm, "end": v(-32.32, -4.62) * mm});
            skLineSegment(sketch, "E6465", {"start": v(-32.32, -4.62) * mm, "end": v(-32.17, -4.85) * mm});
            skLineSegment(sketch, "E6466", {"start": v(-32.17, -4.85) * mm, "end": v(-31.83, -5.41) * mm});
            skLineSegment(sketch, "E6467", {"start": v(-31.83, -5.41) * mm, "end": v(-31.6, -6.1) * mm});
            skLineSegment(sketch, "E6468", {"start": v(-31.6, -6.1) * mm, "end": v(-31.51, -6.43) * mm});
            skLineSegment(sketch, "E6469", {"start": v(-31.51, -6.43) * mm, "end": v(-31.42, -6.78) * mm});
            skLineSegment(sketch, "E6470", {"start": v(-31.42, -6.78) * mm, "end": v(-31.34, -7.13) * mm});
            skLineSegment(sketch, "E6471", {"start": v(-31.34, -7.13) * mm, "end": v(-31.26, -7.5) * mm});
            skLineSegment(sketch, "E6472", {"start": v(-31.26, -7.5) * mm, "end": v(-31.2, -7.87) * mm});
            skLineSegment(sketch, "E6473", {"start": v(-31.2, -7.87) * mm, "end": v(-31.14, -8.23) * mm});
            skLineSegment(sketch, "E6474", {"start": v(-31.14, -8.23) * mm, "end": v(-31.1, -8.6) * mm});
            skLineSegment(sketch, "E6475", {"start": v(-31.1, -8.6) * mm, "end": v(-31.06, -8.95) * mm});
            skLineSegment(sketch, "E6476", {"start": v(-31.06, -8.95) * mm, "end": v(-31.01, -9.55) * mm});
            skLineSegment(sketch, "E6477", {"start": v(-31.01, -9.55) * mm, "end": v(-30.96, -9.96) * mm});
            skLineSegment(sketch, "E6478", {"start": v(-30.96, -9.96) * mm, "end": v(-30.92, -10.25) * mm});
            skLineSegment(sketch, "E6479", {"start": v(-30.92, -10.25) * mm, "end": v(-30.1, -9.8) * mm});
            skLineSegment(sketch, "E6480", {"start": v(-30.1, -9.8) * mm, "end": v(-29.79, -9.76) * mm});
            skLineSegment(sketch, "E6481", {"start": v(-29.79, -9.76) * mm, "end": v(-29.57, -9.75) * mm});
            skLineSegment(sketch, "E6482", {"start": v(-29.57, -9.75) * mm, "end": v(-29.5, -9.75) * mm});
            skLineSegment(sketch, "E6483", {"start": v(-29.5, -9.75) * mm, "end": v(-29.48, -9.76) * mm});
            skLineSegment(sketch, "E6484", {"start": v(-29.48, -9.76) * mm, "end": v(-29.66, -10.31) * mm});
            skLineSegment(sketch, "E6485", {"start": v(-29.66, -10.31) * mm, "end": v(-29.84, -10.84) * mm});
            skLineSegment(sketch, "E6486", {"start": v(-29.84, -10.84) * mm, "end": v(-29.95, -12.03) * mm});
            skLineSegment(sketch, "E6487", {"start": v(-29.95, -12.03) * mm, "end": v(-29.8, -12.68) * mm});
            skLineSegment(sketch, "E6488", {"start": v(-29.8, -12.68) * mm, "end": v(-29.72, -13.03) * mm});
            skLineSegment(sketch, "E6489", {"start": v(-29.72, -13.03) * mm, "end": v(-29.58, -13.51) * mm});
            skLineSegment(sketch, "E6490", {"start": v(-29.58, -13.51) * mm, "end": v(-29.4, -14.05) * mm});
            skLineSegment(sketch, "E6491", {"start": v(-29.4, -14.05) * mm, "end": v(-29.22, -14.6) * mm});
            skLineSegment(sketch, "E6492", {"start": v(-29.22, -14.6) * mm, "end": v(-28.76, -15.87) * mm});
            skLineSegment(sketch, "E6493", {"start": v(-28.76, -15.87) * mm, "end": v(-28.63, -16.53) * mm});
            skLineSegment(sketch, "E6494", {"start": v(-28.63, -16.53) * mm, "end": v(-28.57, -16.85) * mm});
            skLineSegment(sketch, "E6495", {"start": v(-28.57, -16.85) * mm, "end": v(-28.51, -17.21) * mm});
            skLineSegment(sketch, "E6496", {"start": v(-28.51, -17.21) * mm, "end": v(-28.47, -17.59) * mm});
            skLineSegment(sketch, "E6497", {"start": v(-28.47, -17.59) * mm, "end": v(-28.43, -17.92) * mm});
            skLineSegment(sketch, "E6498", {"start": v(-28.43, -17.92) * mm, "end": v(-28.38, -18.65) * mm});
            skLineSegment(sketch, "E6499", {"start": v(-28.38, -18.65) * mm, "end": v(-28.66, -20.1) * mm});
            skLineSegment(sketch, "E6500", {"start": v(-28.66, -20.1) * mm, "end": v(-29.5, -21.8) * mm});
            skLineSegment(sketch, "E6501", {"start": v(-29.5, -21.8) * mm, "end": v(-31.08, -23.57) * mm});
            skLineSegment(sketch, "E6502", {"start": v(-31.08, -23.57) * mm, "end": v(-32.93, -23.57) * mm});
            skLineSegment(sketch, "E6503", {"start": v(-32.93, -23.57) * mm, "end": v(-34.92, -23.57) * mm});
            skLineSegment(sketch, "E6504", {"start": v(-34.63, -23.29) * mm, "end": v(-31.33, -23.32) * mm});
            skLineSegment(sketch, "E6505", {"start": v(-31.33, -23.32) * mm, "end": v(-31.08, -22.67) * mm});
            skLineSegment(sketch, "E6506", {"start": v(-31.08, -22.67) * mm, "end": v(-30.97, -22.38) * mm});
            skLineSegment(sketch, "E6507", {"start": v(-30.97, -22.38) * mm, "end": v(-30.87, -22.06) * mm});
            skLineSegment(sketch, "E6508", {"start": v(-30.87, -22.06) * mm, "end": v(-30.79, -21.76) * mm});
            skLineSegment(sketch, "E6509", {"start": v(-30.79, -21.76) * mm, "end": v(-30.73, -21.51) * mm});
            skLineSegment(sketch, "E6510", {"start": v(-30.73, -21.51) * mm, "end": v(-30.63, -21) * mm});
            skLineSegment(sketch, "E6511", {"start": v(-30.63, -21) * mm, "end": v(-30.72, -19.1) * mm});
            skLineSegment(sketch, "E6512", {"start": v(-30.72, -19.1) * mm, "end": v(-31.26, -17.71) * mm});
            skLineSegment(sketch, "E6513", {"start": v(-31.26, -17.71) * mm, "end": v(-32.4, -15.83) * mm});
            skLineSegment(sketch, "E6514", {"start": v(-32.4, -15.83) * mm, "end": v(-32.89, -15.23) * mm});
            skLineSegment(sketch, "E6515", {"start": v(-32.89, -15.23) * mm, "end": v(-33.38, -16.56) * mm});
            skLineSegment(sketch, "E6516", {"start": v(-33.38, -16.56) * mm, "end": v(-34.91, -19.28) * mm});
            skLineSegment(sketch, "E6517", {"start": v(-34.91, -19.28) * mm, "end": v(-35.48, -20.63) * mm});
            skLineSegment(sketch, "E6518", {"start": v(-35.48, -20.63) * mm, "end": v(-35.5, -22) * mm});
            skLineSegment(sketch, "E6519", {"start": v(-35.5, -22) * mm, "end": v(-35.15, -23.15) * mm});
            skLineSegment(sketch, "E6520", {"start": v(-35.15, -23.15) * mm, "end": v(-34.63, -23.29) * mm});
            skSolve(sketch);
        }
        {
            var Q0;
            Q0=qCreatedBy(makeId("Top.planeOp"),FACE);
            var sketch = newSketch(context, id + "F1", { "sketchPlane" : qUnion([Q0])});
            skLineSegment(sketch, "E6521.bottom", {"start": v(-42, 56) * mm, "end": v(42, 56) * mm});
            skLineSegment(sketch, "E6521.top", {"start": v(-42, -56.24) * mm, "end": v(42, -56.24) * mm});
            skLineSegment(sketch, "E6521.left", {"start": v(-42, 56) * mm, "end": v(-42, -56.24) * mm});
            skLineSegment(sketch, "E6521.right", {"start": v(42, 56) * mm, "end": v(42, -56.24) * mm});
            skLineSegment(sketch, "E6522", {"start": v(0, 68.25) * mm, "end": v(0, -74.34) * mm, "construction": true});
            skSolve(sketch);
        }
        {
            var Q0;
            Q0 = qSketchRegion(id + "F1", true);
            extrude(context, id + "F2", {"entities" : qUnion([Q0]), "oppositeDirection" : true, "depth" : 3 * mm});
        }
        {
            var Q0;
            Q0 = qSketchRegion(id + "F0", true);
            extrude(context, id + "F3", {"entities" : qUnion([Q0]), "operationType" : NewBodyOperationType.ADD, "depth" : 5 * mm});
        }
    });
